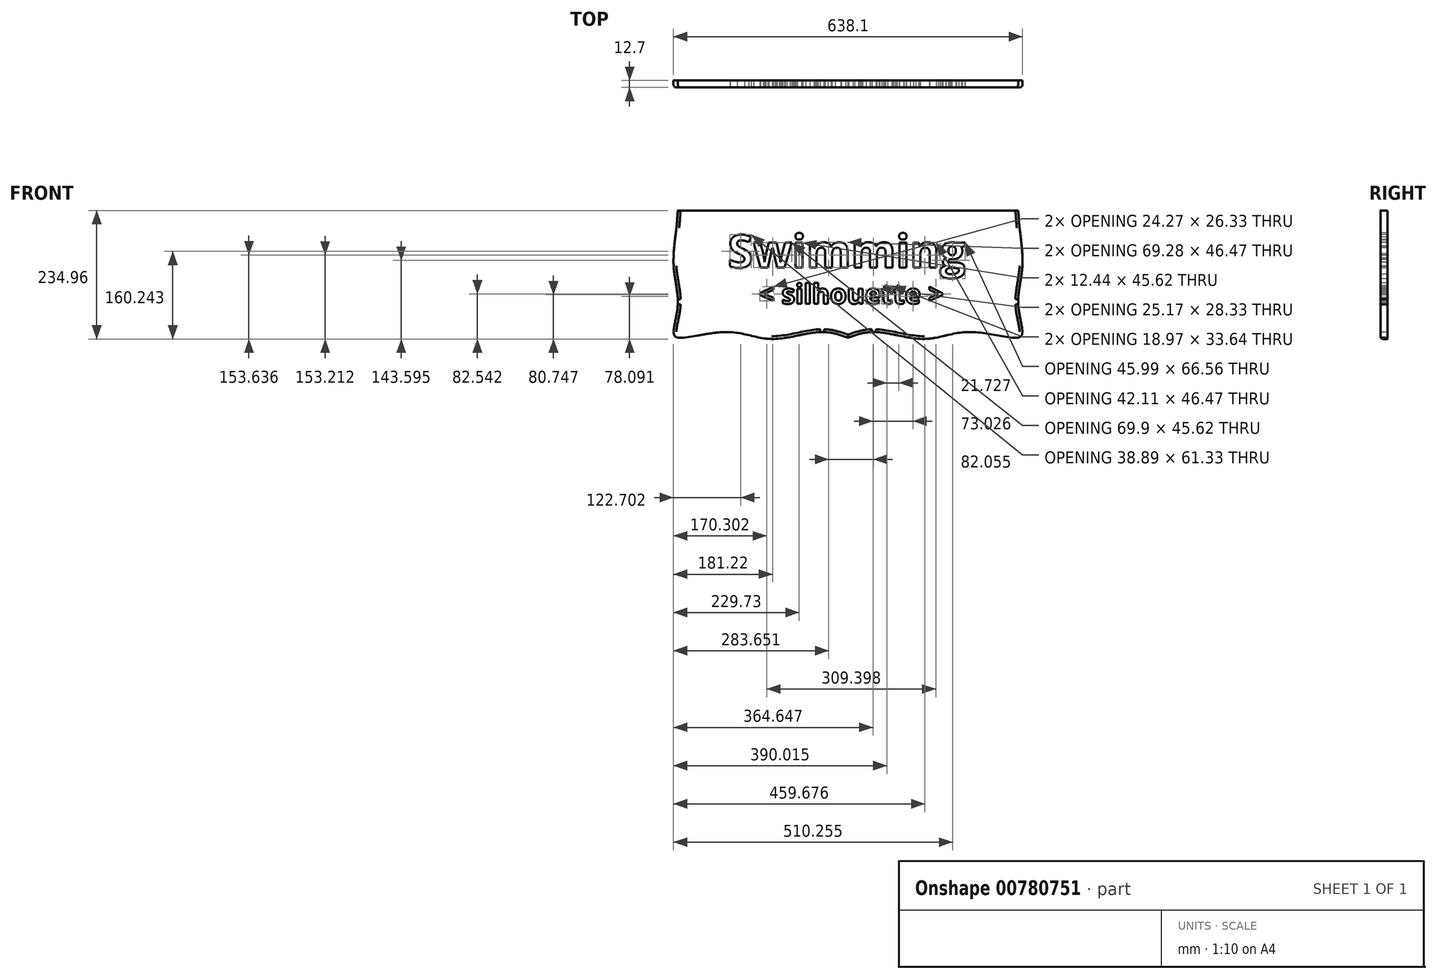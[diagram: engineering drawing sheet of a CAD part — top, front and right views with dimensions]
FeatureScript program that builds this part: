
annotation { "Feature Type Name" : "Feature", "Feature Type Description" : "" }
export const myFeature = defineFeature(function(context is Context, id is Id, definition is map)
    precondition{}
    {
        {
            var Q0;
            Q0=qCreatedBy(makeId("Front.planeOp"),FACE);
            var sketch = newSketch(context, id + "F0", { "sketchPlane" : qUnion([Q0])});
            skLineSegment(sketch, "E0.bottom", {"start": v(-290.57, 108.48) * mm, "end": v(331.73, 108.48) * mm});
            skLineSegment(sketch, "E0.top", {"start": v(-290.57, -113.77) * mm, "end": v(331.73, -113.77) * mm});
            skLineSegment(sketch, "E0.left", {"start": v(-290.57, 108.48) * mm, "end": v(-290.57, -113.77) * mm});
            skLineSegment(sketch, "E0.right", {"start": v(331.73, 108.48) * mm, "end": v(331.73, -113.77) * mm});
            skPoint(sketch, "E1", {"position": v(20.58, 108.48) * mm});
            skSolve(sketch);
        }
        {
            var Q0;
            Q0=makeQuery(id+"F0.imprint","IMPRINT",FACE,{"disambiguationData":[TD([[makeQuery(id+"F0.imprint","IMPRINT",EDGE,{"derivedFrom":sQuery(id+"F0.wireOp",EDGE,"E0.bottom")}),-1.0]])]});
            extrude(context, id + "F1", {"entities" : qUnion([Q0]), "depth" : 12.7 * mm, "offsetDistance" : 25.4 * mm});
        }
        {
            var Q0;
            Q0=makeQuery(id+"F1.opExtrude","CAP_FACE",FACE,{"disambiguationData":[OSD([sQuery(id+"F0.wireOp",EDGE,"E0.bottom"),sQuery(id+"F0.wireOp",EDGE,"E0.top"),sQuery(id+"F0.wireOp",EDGE,"E0.left"),sQuery(id+"F0.wireOp",EDGE,"E0.right")])],"isStart":false});
            var sketch = newSketch(context, id + "F2", { "sketchPlane" : qUnion([Q0])});
            skText(sketch, "E2", { "text": "Swimming", "fontName": "OpenSans-Bold.ttf"});
            skPoint(sketch, "E3", {"position": v(20.58, 108.48) * mm});
            const initialGuessF2  = {"E2": [-0.19905, 0.00392, 1, 0, 0.06017]};
            skSetInitialGuess(sketch, initialGuessF2);
            skSolve(sketch);
        }
        {
            var Q0;
            Q0=makeQuery(id+"F2.imprint","IMPRINT",FACE,{"disambiguationData":[TD([[makeQuery(id+"F2.imprint","IMPRINT",EDGE,{"derivedFrom":sQuery(id+"F2.wireOp",EDGE,"E2.sketch_text.stroke-0")}),1.0]])]});
            var sketch = newSketch(context, id + "F3", { "sketchPlane" : qUnion([Q0])});
            skText(sketch, "E4", { "text": " < silhouette >", "fontName": "OpenSans-Bold.ttf"});
            skPoint(sketch, "E5", {"position": v(20.58, -113.77) * mm});
            const initialGuessF3  = {"E4": [-0.15546, -0.06206, 1, 0, 0.03604]};
            skSetInitialGuess(sketch, initialGuessF3);
            skSolve(sketch);
        }
        {
            var Q0;
            Q0=qSketchRegion(id+"F2",true);
            var Q1;
            Q1=qSketchRegion(id+"F3",true);
            extrude(context, id + "F4", {"entities" : qUnion([Q0, Q1]), "operationType" : NewBodyOperationType.REMOVE, "oppositeDirection" : true, "depth" : 25.4 * mm, "offsetDistance" : 25.4 * mm});
        }
        {
            var Q0;
            {var subQ0=sQuery(id+"F0.wireOp",EDGE,"E0.right");var subQ1=sQuery(id+"F0.wireOp",EDGE,"E0.bottom");var subQ2=sQuery(id+"F0.wireOp",EDGE,"E0.left");var subQ3=sQuery(id+"F0.wireOp",EDGE,"E0.top");Q0=makeQuery(id+"F4.boolean.opBoolean","SPLIT",FACE,{"disambiguationData":[TD([makeQuery(id+"F1.opExtrude","SWEPT_FACE",FACE,{"disambiguationData":[OSD([subQ1])]})])],"derivedFrom":makeQuery(id+"F1.opExtrude","CAP_FACE",FACE,{"disambiguationData":[OSD([subQ1,subQ3,subQ2,subQ0])],"isStart":false})});}
            var sketch = newSketch(context, id + "F5", { "sketchPlane" : qUnion([Q0])});
            skPoint(sketch, "E6", {"position": v(-290.57, -62.97) * mm});
            skPoint(sketch, "E7", {"position": v(-290.57, 6.88) * mm});
            skPoint(sketch, "E8", {"position": v(-290.57, 76.73) * mm});
            skLineSegment(sketch, "E9", {"start": v(-290.57, 76.73) * mm, "end": v(-293.1, 76.73) * mm});
            skLineSegment(sketch, "E10", {"start": v(-290.57, 6.88) * mm, "end": v(-298.19, 6.88) * mm});
            skLineSegment(sketch, "E11", {"start": v(-290.57, -113.77) * mm, "end": v(-298.19, -113.77) * mm});
            skLineSegment(sketch, "E12", {"start": v(-290.57, -113.77) * mm, "end": v(-290.57, -123.93) * mm});
            skPoint(sketch, "E13", {"position": v(-201.67, -113.77) * mm});
            skPoint(sketch, "E14", {"position": v(20.58, -113.77) * mm});
            skPoint(sketch, "E15", {"position": v(-30.22, -113.77) * mm});
            skPoint(sketch, "E16", {"position": v(-119.12, -113.77) * mm});
            skPoint(sketch, "E17", {"position": v(71.38, -113.77) * mm});
            skPoint(sketch, "E18", {"position": v(160.28, -113.77) * mm});
            skPoint(sketch, "E19", {"position": v(242.83, -113.77) * mm});
            skPoint(sketch, "E20", {"position": v(331.73, -62.97) * mm});
            skPoint(sketch, "E21", {"position": v(331.73, 6.88) * mm});
            skPoint(sketch, "E22", {"position": v(331.73, 76.73) * mm});
            skLineSegment(sketch, "E23", {"start": v(331.73, 76.73) * mm, "end": v(334.27, 76.73) * mm});
            skLineSegment(sketch, "E24", {"start": v(331.73, 6.88) * mm, "end": v(339.35, 6.88) * mm});
            skLineSegment(sketch, "E25", {"start": v(331.73, -113.77) * mm, "end": v(339.35, -113.77) * mm});
            skLineSegment(sketch, "E26", {"start": v(331.73, -113.77) * mm, "end": v(331.73, -123.93) * mm});
            skLineSegment(sketch, "E27", {"start": v(-119.12, -113.77) * mm, "end": v(-119.12, -126.47) * mm});
            skLineSegment(sketch, "E28", {"start": v(20.58, -113.77) * mm, "end": v(20.58, -123.93) * mm});
            skLineSegment(sketch, "E29", {"start": v(160.28, -113.77) * mm, "end": v(160.28, -126.47) * mm});
            skFitSpline(sketch, "E30", {"points": [v(-290.57, 108.48) * mm, v(-293.1, 76.73) * mm, v(-298.19, 6.88) * mm, v(-290.57, -62.97) * mm, v(-298.19, -113.77) * mm, v(-290.57, -123.93) * mm, v(-201.67, -113.77) * mm, v(-119.12, -126.47) * mm, v(-30.22, -113.77) * mm, v(20.58, -123.93) * mm], "startDerivative": vector(-26.2, -341.82) * mm, "endDerivative": vector(438.15, -148.5) * mm});
            skFitSpline(sketch, "E31", {"points": [v(331.73, 108.48) * mm, v(334.27, 76.73) * mm, v(339.35, 6.88) * mm, v(331.73, -62.97) * mm, v(339.35, -113.77) * mm, v(331.73, -123.93) * mm, v(242.83, -113.77) * mm, v(160.28, -126.47) * mm, v(71.38, -113.77) * mm, v(20.58, -123.93) * mm], "startDerivative": vector(26.2, -341.82) * mm, "endDerivative": vector(-438.15, -148.5) * mm});
            skSolve(sketch);
        }
        {
            var Q0;
            {var subQ0=sQuery(id+"F5.wireOp",EDGE,"E28");Q0=makeQuery(id+"F5.imprint","IMPRINT",FACE,{"disambiguationData":[TD([[makeQuery(id+"F5.imprint","IMPRINT",EDGE,{"derivedFrom":subQ0}),-1.0]])]});}
            var Q1;
            {var subQ0=sQuery(id+"F5.wireOp",EDGE,"E28");Q1=makeQuery(id+"F5.imprint","IMPRINT",FACE,{"disambiguationData":[TD([[makeQuery(id+"F5.imprint","IMPRINT",EDGE,{"derivedFrom":subQ0}),1.0]])]});}
            var Q2;
            {var subQ0=sQuery(id+"F5.wireOp",EDGE,"E27");Q2=makeQuery(id+"F5.imprint","IMPRINT",FACE,{"disambiguationData":[TD([[makeQuery(id+"F5.imprint","IMPRINT",EDGE,{"derivedFrom":subQ0}),1.0]])]});}
            var Q3;
            {var subQ0=sQuery(id+"F5.wireOp",EDGE,"E27");Q3=makeQuery(id+"F5.imprint","IMPRINT",FACE,{"disambiguationData":[TD([[makeQuery(id+"F5.imprint","IMPRINT",EDGE,{"derivedFrom":subQ0}),-1.0]])]});}
            var Q4;
            {var subQ0=sQuery(id+"F5.wireOp",EDGE,"E12");Q4=makeQuery(id+"F5.imprint","IMPRINT",FACE,{"disambiguationData":[TD([[makeQuery(id+"F5.imprint","IMPRINT",EDGE,{"derivedFrom":subQ0}),1.0]])]});}
            var Q5;
            {var subQ0=sQuery(id+"F5.wireOp",EDGE,"E11");Q5=makeQuery(id+"F5.imprint","IMPRINT",FACE,{"disambiguationData":[TD([[makeQuery(id+"F5.imprint","IMPRINT",EDGE,{"derivedFrom":subQ0}),1.0]])]});}
            var Q6;
            {var subQ0=sQuery(id+"F5.wireOp",EDGE,"E11");Q6=makeQuery(id+"F5.imprint","IMPRINT",FACE,{"disambiguationData":[TD([[makeQuery(id+"F5.imprint","IMPRINT",EDGE,{"derivedFrom":subQ0}),-1.0]])]});}
            var Q7;
            {var subQ0=sQuery(id+"F5.wireOp",EDGE,"E10");Q7=makeQuery(id+"F5.imprint","IMPRINT",FACE,{"disambiguationData":[TD([[makeQuery(id+"F5.imprint","IMPRINT",EDGE,{"derivedFrom":subQ0}),1.0]])]});}
            var Q8;
            {var subQ0=sQuery(id+"F5.wireOp",EDGE,"E9");Q8=makeQuery(id+"F5.imprint","IMPRINT",FACE,{"disambiguationData":[TD([[makeQuery(id+"F5.imprint","IMPRINT",EDGE,{"derivedFrom":subQ0}),1.0]])]});}
            var Q9;
            {var subQ0=makeQuery(id+"F1.opExtrude","CAP_EDGE",EDGE,{"disambiguationData":[OSD([sQuery(id+"F0.wireOp",EDGE,"E0.bottom")])],"isStart":false});Q9=makeQuery(id+"F5.imprint","IMPRINT",FACE,{"disambiguationData":[TD([[makeQuery(id+"F5.imprint","IMPRINT",EDGE,{"derivedFrom":subQ0}),-1.0]])]});}
            var Q10;
            {var subQ0=sQuery(id+"F5.wireOp",EDGE,"E29");Q10=makeQuery(id+"F5.imprint","IMPRINT",FACE,{"disambiguationData":[TD([[makeQuery(id+"F5.imprint","IMPRINT",EDGE,{"derivedFrom":subQ0}),-1.0]])]});}
            var Q11;
            {var subQ0=sQuery(id+"F5.wireOp",EDGE,"E29");Q11=makeQuery(id+"F5.imprint","IMPRINT",FACE,{"disambiguationData":[TD([[makeQuery(id+"F5.imprint","IMPRINT",EDGE,{"derivedFrom":subQ0}),1.0]])]});}
            var Q12;
            {var subQ0=sQuery(id+"F5.wireOp",EDGE,"E26");Q12=makeQuery(id+"F5.imprint","IMPRINT",FACE,{"disambiguationData":[TD([[makeQuery(id+"F5.imprint","IMPRINT",EDGE,{"derivedFrom":subQ0}),-1.0]])]});}
            var Q13;
            {var subQ0=sQuery(id+"F5.wireOp",EDGE,"E25");Q13=makeQuery(id+"F5.imprint","IMPRINT",FACE,{"disambiguationData":[TD([[makeQuery(id+"F5.imprint","IMPRINT",EDGE,{"derivedFrom":subQ0}),-1.0]])]});}
            var Q14;
            {var subQ0=sQuery(id+"F5.wireOp",EDGE,"E25");Q14=makeQuery(id+"F5.imprint","IMPRINT",FACE,{"disambiguationData":[TD([[makeQuery(id+"F5.imprint","IMPRINT",EDGE,{"derivedFrom":subQ0}),1.0]])]});}
            var Q15;
            {var subQ0=sQuery(id+"F5.wireOp",EDGE,"E24");Q15=makeQuery(id+"F5.imprint","IMPRINT",FACE,{"disambiguationData":[TD([[makeQuery(id+"F5.imprint","IMPRINT",EDGE,{"derivedFrom":subQ0}),-1.0]])]});}
            var Q16;
            {var subQ0=sQuery(id+"F5.wireOp",EDGE,"E23");Q16=makeQuery(id+"F5.imprint","IMPRINT",FACE,{"disambiguationData":[TD([[makeQuery(id+"F5.imprint","IMPRINT",EDGE,{"derivedFrom":subQ0}),-1.0]])]});}
            var Q17;
            {var subQ0=sQuery(id+"F5.wireOp",EDGE,"E23");Q17=makeQuery(id+"F5.imprint","IMPRINT",FACE,{"disambiguationData":[TD([[makeQuery(id+"F5.imprint","IMPRINT",EDGE,{"derivedFrom":subQ0}),1.0]])]});}
            var Q18;
            {var subQ0=sQuery(id+"F5.wireOp",EDGE,"E9");Q18=makeQuery(id+"F5.imprint","IMPRINT",FACE,{"disambiguationData":[TD([[makeQuery(id+"F5.imprint","IMPRINT",EDGE,{"derivedFrom":subQ0}),-1.0]])]});}
            extrude(context, id + "F6", {"entities" : qUnion([Q0, Q1, Q2, Q3, Q4, Q5, Q6, Q7, Q8, Q9, Q10, Q11, Q12, Q13, Q14, Q15, Q16, Q17, Q18]), "operationType" : NewBodyOperationType.ADD, "depth" : -12.7 * mm, "offsetDistance" : 25.4 * mm});
        }
        {
            var Q0;
            {var subQ0=sQuery(id+"F5.wireOp",EDGE,"8007402e-1a4e-4a06-85a5-2af08e553504");var subQ1=sQuery(id+"F0.wireOp",EDGE,"E0.left");var subQ2=sQuery(id+"F0.wireOp",EDGE,"E0.top");var subQ3=sQuery(id+"F0.wireOp",EDGE,"E0.bottom");Q0=makeQuery(id+"F6.boolean.opBoolean","SPLIT",EDGE,{"disambiguationData":[TD([makeQuery(id+"F1.opExtrude","CAP_FACE",FACE,{"disambiguationData":[OSD([subQ3,subQ2,subQ1,sQuery(id+"F0.wireOp",EDGE,"E0.right")])],"isStart":false}),makeQuery(id+"F1.opExtrude","SWEPT_FACE",FACE,{"disambiguationData":[OSD([subQ2])]}),makeQuery(id+"F1.opExtrude","SWEPT_FACE",FACE,{"disambiguationData":[OSD([subQ1])]}),makeQuery(id+"F6.opExtrude","SWEPT_FACE",FACE,{"disambiguationData":[OSD([subQ0])]}),makeQuery(id+"F6.opExtrude","CAP_FACE",FACE,{"disambiguationData":[OSD([subQ3,sQuery(id+"F2.wireOp",EDGE,"E2.sketch_text.stroke-0"),sQuery(id+"F2.wireOp",EDGE,"E2.sketch_text.stroke-1"),sQuery(id+"F2.wireOp",EDGE,"E2.sketch_text.stroke-2"),sQuery(id+"F2.wireOp",EDGE,"E2.sketch_text.stroke-3"),sQuery(id+"F2.wireOp",EDGE,"E2.sketch_text.stroke-4"),sQuery(id+"F2.wireOp",EDGE,"E2.sketch_text.stroke-5"),sQuery(id+"F2.wireOp",EDGE,"E2.sketch_text.stroke-6"),sQuery(id+"F2.wireOp",EDGE,"E2.sketch_text.stroke-7"),sQuery(id+"F2.wireOp",EDGE,"E2.sketch_text.stroke-8"),sQuery(id+"F2.wireOp",EDGE,"E2.sketch_text.stroke-9"),sQuery(id+"F2.wireOp",EDGE,"E2.sketch_text.stroke-10"),sQuery(id+"F2.wireOp",EDGE,"E2.sketch_text.stroke-11"),sQuery(id+"F2.wireOp",EDGE,"E2.sketch_text.stroke-12"),sQuery(id+"F2.wireOp",EDGE,"E2.sketch_text.stroke-13"),sQuery(id+"F2.wireOp",EDGE,"E2.sketch_text.stroke-14"),sQuery(id+"F2.wireOp",EDGE,"E2.sketch_text.stroke-15"),sQuery(id+"F2.wireOp",EDGE,"E2.sketch_text.stroke-16"),sQuery(id+"F2.wireOp",EDGE,"E2.sketch_text.stroke-17"),sQuery(id+"F2.wireOp",EDGE,"E2.sketch_text.stroke-18"),sQuery(id+"F2.wireOp",EDGE,"E2.sketch_text.stroke-19"),sQuery(id+"F2.wireOp",EDGE,"E2.sketch_text.stroke-20"),sQuery(id+"F2.wireOp",EDGE,"E2.sketch_text.stroke-21"),sQuery(id+"F2.wireOp",EDGE,"E2.sketch_text.stroke-22"),sQuery(id+"F2.wireOp",EDGE,"E2.sketch_text.stroke-23"),sQuery(id+"F2.wireOp",EDGE,"E2.sketch_text.stroke-24"),sQuery(id+"F2.wireOp",EDGE,"E2.sketch_text.stroke-25"),sQuery(id+"F2.wireOp",EDGE,"E2.sketch_text.stroke-26"),sQuery(id+"F2.wireOp",EDGE,"E2.sketch_text.stroke-27"),sQuery(id+"F2.wireOp",EDGE,"E2.sketch_text.stroke-28"),sQuery(id+"F2.wireOp",EDGE,"E2.sketch_text.stroke-29"),sQuery(id+"F2.wireOp",EDGE,"E2.sketch_text.stroke-30"),sQuery(id+"F2.wireOp",EDGE,"E2.sketch_text.stroke-31"),sQuery(id+"F2.wireOp",EDGE,"E2.sketch_text.stroke-32"),sQuery(id+"F2.wireOp",EDGE,"E2.sketch_text.stroke-33"),sQuery(id+"F2.wireOp",EDGE,"E2.sketch_text.stroke-34"),sQuery(id+"F2.wireOp",EDGE,"E2.sketch_text.stroke-35"),sQuery(id+"F2.wireOp",EDGE,"E2.sketch_text.stroke-36"),sQuery(id+"F2.wireOp",EDGE,"E2.sketch_text.stroke-37"),sQuery(id+"F2.wireOp",EDGE,"E2.sketch_text.stroke-38"),sQuery(id+"F2.wireOp",EDGE,"E2.sketch_text.stroke-39"),sQuery(id+"F2.wireOp",EDGE,"E2.sketch_text.stroke-40"),sQuery(id+"F2.wireOp",EDGE,"E2.sketch_text.stroke-41"),sQuery(id+"F2.wireOp",EDGE,"E2.sketch_text.stroke-42"),sQuery(id+"F2.wireOp",EDGE,"E2.sketch_text.stroke-43"),sQuery(id+"F2.wireOp",EDGE,"E2.sketch_text.stroke-44"),sQuery(id+"F2.wireOp",EDGE,"E2.sketch_text.stroke-45"),sQuery(id+"F2.wireOp",EDGE,"E2.sketch_text.stroke-46"),sQuery(id+"F2.wireOp",EDGE,"E2.sketch_text.stroke-47"),sQuery(id+"F2.wireOp",EDGE,"E2.sketch_text.stroke-48"),sQuery(id+"F2.wireOp",EDGE,"E2.sketch_text.stroke-49"),sQuery(id+"F2.wireOp",EDGE,"E2.sketch_text.stroke-50"),sQuery(id+"F2.wireOp",EDGE,"E2.sketch_text.stroke-51"),sQuery(id+"F2.wireOp",EDGE,"E2.sketch_text.stroke-52"),sQuery(id+"F2.wireOp",EDGE,"E2.sketch_text.stroke-53"),sQuery(id+"F2.wireOp",EDGE,"E2.sketch_text.stroke-54"),sQuery(id+"F2.wireOp",EDGE,"E2.sketch_text.stroke-55"),sQuery(id+"F2.wireOp",EDGE,"E2.sketch_text.stroke-56"),sQuery(id+"F2.wireOp",EDGE,"E2.sketch_text.stroke-57"),sQuery(id+"F2.wireOp",EDGE,"E2.sketch_text.stroke-58"),sQuery(id+"F2.wireOp",EDGE,"E2.sketch_text.stroke-59"),sQuery(id+"F2.wireOp",EDGE,"E2.sketch_text.stroke-60"),sQuery(id+"F2.wireOp",EDGE,"E2.sketch_text.stroke-61"),sQuery(id+"F2.wireOp",EDGE,"E2.sketch_text.stroke-62"),sQuery(id+"F2.wireOp",EDGE,"E2.sketch_text.stroke-63"),sQuery(id+"F2.wireOp",EDGE,"E2.sketch_text.stroke-64"),sQuery(id+"F2.wireOp",EDGE,"E2.sketch_text.stroke-65"),sQuery(id+"F2.wireOp",EDGE,"E2.sketch_text.stroke-66"),sQuery(id+"F2.wireOp",EDGE,"E2.sketch_text.stroke-67"),sQuery(id+"F2.wireOp",EDGE,"E2.sketch_text.stroke-68"),sQuery(id+"F2.wireOp",EDGE,"E2.sketch_text.stroke-69"),sQuery(id+"F2.wireOp",EDGE,"E2.sketch_text.stroke-70"),sQuery(id+"F2.wireOp",EDGE,"E2.sketch_text.stroke-71"),sQuery(id+"F2.wireOp",EDGE,"E2.sketch_text.stroke-72"),sQuery(id+"F2.wireOp",EDGE,"E2.sketch_text.stroke-73"),sQuery(id+"F2.wireOp",EDGE,"E2.sketch_text.stroke-74"),sQuery(id+"F2.wireOp",EDGE,"E2.sketch_text.stroke-75"),sQuery(id+"F2.wireOp",EDGE,"E2.sketch_text.stroke-76"),sQuery(id+"F2.wireOp",EDGE,"E2.sketch_text.stroke-77"),sQuery(id+"F2.wireOp",EDGE,"E2.sketch_text.stroke-78"),sQuery(id+"F2.wireOp",EDGE,"E2.sketch_text.stroke-79"),sQuery(id+"F2.wireOp",EDGE,"E2.sketch_text.stroke-80"),sQuery(id+"F2.wireOp",EDGE,"E2.sketch_text.stroke-81"),sQuery(id+"F2.wireOp",EDGE,"E2.sketch_text.stroke-82"),sQuery(id+"F2.wireOp",EDGE,"E2.sketch_text.stroke-83"),sQuery(id+"F2.wireOp",EDGE,"E2.sketch_text.stroke-84"),sQuery(id+"F2.wireOp",EDGE,"E2.sketch_text.stroke-85"),sQuery(id+"F2.wireOp",EDGE,"E2.sketch_text.stroke-86"),sQuery(id+"F2.wireOp",EDGE,"E2.sketch_text.stroke-87"),sQuery(id+"F2.wireOp",EDGE,"E2.sketch_text.stroke-88"),sQuery(id+"F2.wireOp",EDGE,"E2.sketch_text.stroke-89"),sQuery(id+"F2.wireOp",EDGE,"E2.sketch_text.stroke-90"),sQuery(id+"F2.wireOp",EDGE,"E2.sketch_text.stroke-91"),sQuery(id+"F2.wireOp",EDGE,"E2.sketch_text.stroke-92"),sQuery(id+"F2.wireOp",EDGE,"E2.sketch_text.stroke-93"),sQuery(id+"F2.wireOp",EDGE,"E2.sketch_text.stroke-94"),sQuery(id+"F2.wireOp",EDGE,"E2.sketch_text.stroke-95"),sQuery(id+"F2.wireOp",EDGE,"E2.sketch_text.stroke-96"),sQuery(id+"F2.wireOp",EDGE,"E2.sketch_text.stroke-97"),sQuery(id+"F2.wireOp",EDGE,"E2.sketch_text.stroke-98"),sQuery(id+"F2.wireOp",EDGE,"E2.sketch_text.stroke-99"),sQuery(id+"F2.wireOp",EDGE,"E2.sketch_text.stroke-100"),sQuery(id+"F2.wireOp",EDGE,"E2.sketch_text.stroke-101"),sQuery(id+"F2.wireOp",EDGE,"E2.sketch_text.stroke-102"),sQuery(id+"F2.wireOp",EDGE,"E2.sketch_text.stroke-103"),sQuery(id+"F2.wireOp",EDGE,"E2.sketch_text.stroke-104"),sQuery(id+"F2.wireOp",EDGE,"E2.sketch_text.stroke-105"),sQuery(id+"F2.wireOp",EDGE,"E2.sketch_text.stroke-106"),sQuery(id+"F2.wireOp",EDGE,"E2.sketch_text.stroke-107"),sQuery(id+"F2.wireOp",EDGE,"E2.sketch_text.stroke-108"),sQuery(id+"F2.wireOp",EDGE,"E2.sketch_text.stroke-109"),sQuery(id+"F2.wireOp",EDGE,"E2.sketch_text.stroke-110"),sQuery(id+"F2.wireOp",EDGE,"E2.sketch_text.stroke-111"),sQuery(id+"F2.wireOp",EDGE,"E2.sketch_text.stroke-112"),sQuery(id+"F2.wireOp",EDGE,"E2.sketch_text.stroke-113"),sQuery(id+"F2.wireOp",EDGE,"E2.sketch_text.stroke-114"),sQuery(id+"F2.wireOp",EDGE,"E2.sketch_text.stroke-115"),sQuery(id+"F2.wireOp",EDGE,"E2.sketch_text.stroke-116"),sQuery(id+"F2.wireOp",EDGE,"E2.sketch_text.stroke-117"),sQuery(id+"F2.wireOp",EDGE,"E2.sketch_text.stroke-118"),sQuery(id+"F2.wireOp",EDGE,"E2.sketch_text.stroke-119"),sQuery(id+"F2.wireOp",EDGE,"E2.sketch_text.stroke-120"),sQuery(id+"F2.wireOp",EDGE,"E2.sketch_text.stroke-121"),sQuery(id+"F2.wireOp",EDGE,"E2.sketch_text.stroke-122"),sQuery(id+"F2.wireOp",EDGE,"E2.sketch_text.stroke-123"),sQuery(id+"F2.wireOp",EDGE,"E2.sketch_text.stroke-124"),sQuery(id+"F2.wireOp",EDGE,"E2.sketch_text.stroke-125"),sQuery(id+"F2.wireOp",EDGE,"E2.sketch_text.stroke-126"),sQuery(id+"F2.wireOp",EDGE,"E2.sketch_text.stroke-127"),sQuery(id+"F2.wireOp",EDGE,"E2.sketch_text.stroke-128"),sQuery(id+"F2.wireOp",EDGE,"E2.sketch_text.stroke-129"),sQuery(id+"F2.wireOp",EDGE,"E2.sketch_text.stroke-130"),sQuery(id+"F2.wireOp",EDGE,"E2.sketch_text.stroke-131"),sQuery(id+"F2.wireOp",EDGE,"E2.sketch_text.stroke-132"),sQuery(id+"F2.wireOp",EDGE,"E2.sketch_text.stroke-133"),sQuery(id+"F2.wireOp",EDGE,"E2.sketch_text.stroke-134"),sQuery(id+"F2.wireOp",EDGE,"E2.sketch_text.stroke-135"),sQuery(id+"F2.wireOp",EDGE,"E2.sketch_text.stroke-136"),sQuery(id+"F2.wireOp",EDGE,"E2.sketch_text.stroke-137"),sQuery(id+"F2.wireOp",EDGE,"E2.sketch_text.stroke-138"),sQuery(id+"F2.wireOp",EDGE,"E2.sketch_text.stroke-139"),sQuery(id+"F2.wireOp",EDGE,"E2.sketch_text.stroke-140"),sQuery(id+"F2.wireOp",EDGE,"E2.sketch_text.stroke-141"),sQuery(id+"F2.wireOp",EDGE,"E2.sketch_text.stroke-142"),sQuery(id+"F2.wireOp",EDGE,"E2.sketch_text.stroke-143"),sQuery(id+"F2.wireOp",EDGE,"E2.sketch_text.stroke-144"),sQuery(id+"F2.wireOp",EDGE,"E2.sketch_text.stroke-145"),sQuery(id+"F2.wireOp",EDGE,"E2.sketch_text.stroke-146"),sQuery(id+"F2.wireOp",EDGE,"E2.sketch_text.stroke-147"),sQuery(id+"F2.wireOp",EDGE,"E2.sketch_text.stroke-148"),sQuery(id+"F2.wireOp",EDGE,"E2.sketch_text.stroke-149"),sQuery(id+"F2.wireOp",EDGE,"E2.sketch_text.stroke-150"),sQuery(id+"F2.wireOp",EDGE,"E2.sketch_text.stroke-151"),sQuery(id+"F2.wireOp",EDGE,"E2.sketch_text.stroke-152"),sQuery(id+"F2.wireOp",EDGE,"E2.sketch_text.stroke-153"),sQuery(id+"F2.wireOp",EDGE,"E2.sketch_text.stroke-154"),sQuery(id+"F2.wireOp",EDGE,"E2.sketch_text.stroke-155"),sQuery(id+"F2.wireOp",EDGE,"E2.sketch_text.stroke-156"),sQuery(id+"F2.wireOp",EDGE,"E2.sketch_text.stroke-157"),sQuery(id+"F2.wireOp",EDGE,"E2.sketch_text.stroke-158"),sQuery(id+"F2.wireOp",EDGE,"E2.sketch_text.stroke-159"),sQuery(id+"F2.wireOp",EDGE,"E2.sketch_text.stroke-160"),sQuery(id+"F2.wireOp",EDGE,"E2.sketch_text.stroke-161"),sQuery(id+"F2.wireOp",EDGE,"E2.sketch_text.stroke-162"),sQuery(id+"F2.wireOp",EDGE,"E2.sketch_text.stroke-163"),sQuery(id+"F2.wireOp",EDGE,"E2.sketch_text.stroke-164"),sQuery(id+"F2.wireOp",EDGE,"E2.sketch_text.stroke-165"),sQuery(id+"F2.wireOp",EDGE,"E2.sketch_text.stroke-166"),sQuery(id+"F2.wireOp",EDGE,"E2.sketch_text.stroke-167"),sQuery(id+"F2.wireOp",EDGE,"E2.sketch_text.stroke-168"),sQuery(id+"F2.wireOp",EDGE,"E2.sketch_text.stroke-169"),sQuery(id+"F2.wireOp",EDGE,"E2.sketch_text.stroke-170"),sQuery(id+"F2.wireOp",EDGE,"E2.sketch_text.stroke-171"),sQuery(id+"F2.wireOp",EDGE,"E2.sketch_text.stroke-172"),sQuery(id+"F2.wireOp",EDGE,"E2.sketch_text.stroke-173"),sQuery(id+"F3.wireOp",EDGE,"E4.sketch_text.stroke-0"),sQuery(id+"F3.wireOp",EDGE,"E4.sketch_text.stroke-1"),sQuery(id+"F3.wireOp",EDGE,"E4.sketch_text.stroke-2"),sQuery(id+"F3.wireOp",EDGE,"E4.sketch_text.stroke-3"),sQuery(id+"F3.wireOp",EDGE,"E4.sketch_text.stroke-4"),sQuery(id+"F3.wireOp",EDGE,"E4.sketch_text.stroke-5"),sQuery(id+"F3.wireOp",EDGE,"E4.sketch_text.stroke-6"),sQuery(id+"F3.wireOp",EDGE,"E4.sketch_text.stroke-7"),sQuery(id+"F3.wireOp",EDGE,"E4.sketch_text.stroke-8"),sQuery(id+"F3.wireOp",EDGE,"E4.sketch_text.stroke-9"),sQuery(id+"F3.wireOp",EDGE,"E4.sketch_text.stroke-10"),sQuery(id+"F3.wireOp",EDGE,"E4.sketch_text.stroke-11"),sQuery(id+"F3.wireOp",EDGE,"E4.sketch_text.stroke-12"),sQuery(id+"F3.wireOp",EDGE,"E4.sketch_text.stroke-13"),sQuery(id+"F3.wireOp",EDGE,"E4.sketch_text.stroke-14"),sQuery(id+"F3.wireOp",EDGE,"E4.sketch_text.stroke-15"),sQuery(id+"F3.wireOp",EDGE,"E4.sketch_text.stroke-16"),sQuery(id+"F3.wireOp",EDGE,"E4.sketch_text.stroke-17"),sQuery(id+"F3.wireOp",EDGE,"E4.sketch_text.stroke-18"),sQuery(id+"F3.wireOp",EDGE,"E4.sketch_text.stroke-19"),sQuery(id+"F3.wireOp",EDGE,"E4.sketch_text.stroke-20"),sQuery(id+"F3.wireOp",EDGE,"E4.sketch_text.stroke-21"),sQuery(id+"F3.wireOp",EDGE,"E4.sketch_text.stroke-22"),sQuery(id+"F3.wireOp",EDGE,"E4.sketch_text.stroke-23"),sQuery(id+"F3.wireOp",EDGE,"E4.sketch_text.stroke-24"),sQuery(id+"F3.wireOp",EDGE,"E4.sketch_text.stroke-25"),sQuery(id+"F3.wireOp",EDGE,"E4.sketch_text.stroke-26"),sQuery(id+"F3.wireOp",EDGE,"E4.sketch_text.stroke-27"),sQuery(id+"F3.wireOp",EDGE,"E4.sketch_text.stroke-28"),sQuery(id+"F3.wireOp",EDGE,"E4.sketch_text.stroke-29"),sQuery(id+"F3.wireOp",EDGE,"E4.sketch_text.stroke-30"),sQuery(id+"F3.wireOp",EDGE,"E4.sketch_text.stroke-31"),sQuery(id+"F3.wireOp",EDGE,"E4.sketch_text.stroke-32"),sQuery(id+"F3.wireOp",EDGE,"E4.sketch_text.stroke-33"),sQuery(id+"F3.wireOp",EDGE,"E4.sketch_text.stroke-34"),sQuery(id+"F3.wireOp",EDGE,"E4.sketch_text.stroke-35"),sQuery(id+"F3.wireOp",EDGE,"E4.sketch_text.stroke-36"),sQuery(id+"F3.wireOp",EDGE,"E4.sketch_text.stroke-37"),sQuery(id+"F3.wireOp",EDGE,"E4.sketch_text.stroke-38"),sQuery(id+"F3.wireOp",EDGE,"E4.sketch_text.stroke-39"),sQuery(id+"F3.wireOp",EDGE,"E4.sketch_text.stroke-40"),sQuery(id+"F3.wireOp",EDGE,"E4.sketch_text.stroke-41"),sQuery(id+"F3.wireOp",EDGE,"E4.sketch_text.stroke-42"),sQuery(id+"F3.wireOp",EDGE,"E4.sketch_text.stroke-43"),sQuery(id+"F3.wireOp",EDGE,"E4.sketch_text.stroke-44"),sQuery(id+"F3.wireOp",EDGE,"E4.sketch_text.stroke-45"),sQuery(id+"F3.wireOp",EDGE,"E4.sketch_text.stroke-46"),sQuery(id+"F3.wireOp",EDGE,"E4.sketch_text.stroke-47"),sQuery(id+"F3.wireOp",EDGE,"E4.sketch_text.stroke-48"),sQuery(id+"F3.wireOp",EDGE,"E4.sketch_text.stroke-49"),sQuery(id+"F3.wireOp",EDGE,"E4.sketch_text.stroke-50"),sQuery(id+"F3.wireOp",EDGE,"E4.sketch_text.stroke-51"),sQuery(id+"F3.wireOp",EDGE,"E4.sketch_text.stroke-52"),sQuery(id+"F3.wireOp",EDGE,"E4.sketch_text.stroke-53"),sQuery(id+"F3.wireOp",EDGE,"E4.sketch_text.stroke-54"),sQuery(id+"F3.wireOp",EDGE,"E4.sketch_text.stroke-55"),sQuery(id+"F3.wireOp",EDGE,"E4.sketch_text.stroke-56"),sQuery(id+"F3.wireOp",EDGE,"E4.sketch_text.stroke-57"),sQuery(id+"F3.wireOp",EDGE,"E4.sketch_text.stroke-58"),sQuery(id+"F3.wireOp",EDGE,"E4.sketch_text.stroke-59"),sQuery(id+"F3.wireOp",EDGE,"E4.sketch_text.stroke-60"),sQuery(id+"F3.wireOp",EDGE,"E4.sketch_text.stroke-61"),sQuery(id+"F3.wireOp",EDGE,"E4.sketch_text.stroke-62"),sQuery(id+"F3.wireOp",EDGE,"E4.sketch_text.stroke-71"),sQuery(id+"F3.wireOp",EDGE,"E4.sketch_text.stroke-72"),sQuery(id+"F3.wireOp",EDGE,"E4.sketch_text.stroke-73"),sQuery(id+"F3.wireOp",EDGE,"E4.sketch_text.stroke-74"),sQuery(id+"F3.wireOp",EDGE,"E4.sketch_text.stroke-75"),sQuery(id+"F3.wireOp",EDGE,"E4.sketch_text.stroke-76"),sQuery(id+"F3.wireOp",EDGE,"E4.sketch_text.stroke-77"),sQuery(id+"F3.wireOp",EDGE,"E4.sketch_text.stroke-78"),sQuery(id+"F3.wireOp",EDGE,"E4.sketch_text.stroke-79"),sQuery(id+"F3.wireOp",EDGE,"E4.sketch_text.stroke-80"),sQuery(id+"F3.wireOp",EDGE,"E4.sketch_text.stroke-81"),sQuery(id+"F3.wireOp",EDGE,"E4.sketch_text.stroke-82"),sQuery(id+"F3.wireOp",EDGE,"E4.sketch_text.stroke-83"),sQuery(id+"F3.wireOp",EDGE,"E4.sketch_text.stroke-84"),sQuery(id+"F3.wireOp",EDGE,"E4.sketch_text.stroke-85"),sQuery(id+"F3.wireOp",EDGE,"E4.sketch_text.stroke-86"),sQuery(id+"F3.wireOp",EDGE,"E4.sketch_text.stroke-87"),sQuery(id+"F3.wireOp",EDGE,"E4.sketch_text.stroke-88"),sQuery(id+"F3.wireOp",EDGE,"E4.sketch_text.stroke-89"),sQuery(id+"F3.wireOp",EDGE,"E4.sketch_text.stroke-90"),sQuery(id+"F3.wireOp",EDGE,"E4.sketch_text.stroke-91"),sQuery(id+"F3.wireOp",EDGE,"E4.sketch_text.stroke-92"),sQuery(id+"F3.wireOp",EDGE,"E4.sketch_text.stroke-93"),sQuery(id+"F3.wireOp",EDGE,"E4.sketch_text.stroke-94"),sQuery(id+"F3.wireOp",EDGE,"E4.sketch_text.stroke-95"),sQuery(id+"F3.wireOp",EDGE,"E4.sketch_text.stroke-96"),sQuery(id+"F3.wireOp",EDGE,"E4.sketch_text.stroke-97"),sQuery(id+"F3.wireOp",EDGE,"E4.sketch_text.stroke-103"),sQuery(id+"F3.wireOp",EDGE,"E4.sketch_text.stroke-104"),sQuery(id+"F3.wireOp",EDGE,"E4.sketch_text.stroke-105"),sQuery(id+"F3.wireOp",EDGE,"E4.sketch_text.stroke-106"),sQuery(id+"F3.wireOp",EDGE,"E4.sketch_text.stroke-107"),sQuery(id+"F3.wireOp",EDGE,"E4.sketch_text.stroke-108"),sQuery(id+"F3.wireOp",EDGE,"E4.sketch_text.stroke-109"),sQuery(id+"F3.wireOp",EDGE,"E4.sketch_text.stroke-110"),sQuery(id+"F3.wireOp",EDGE,"E4.sketch_text.stroke-111"),sQuery(id+"F3.wireOp",EDGE,"E4.sketch_text.stroke-112"),sQuery(id+"F3.wireOp",EDGE,"E4.sketch_text.stroke-113"),sQuery(id+"F3.wireOp",EDGE,"E4.sketch_text.stroke-114"),sQuery(id+"F3.wireOp",EDGE,"E4.sketch_text.stroke-115"),sQuery(id+"F3.wireOp",EDGE,"E4.sketch_text.stroke-116"),sQuery(id+"F3.wireOp",EDGE,"E4.sketch_text.stroke-117"),sQuery(id+"F3.wireOp",EDGE,"E4.sketch_text.stroke-118"),sQuery(id+"F3.wireOp",EDGE,"E4.sketch_text.stroke-119"),sQuery(id+"F3.wireOp",EDGE,"E4.sketch_text.stroke-120"),sQuery(id+"F3.wireOp",EDGE,"E4.sketch_text.stroke-121"),sQuery(id+"F3.wireOp",EDGE,"E4.sketch_text.stroke-122"),sQuery(id+"F3.wireOp",EDGE,"E4.sketch_text.stroke-123"),sQuery(id+"F3.wireOp",EDGE,"E4.sketch_text.stroke-124"),sQuery(id+"F3.wireOp",EDGE,"E4.sketch_text.stroke-125"),sQuery(id+"F3.wireOp",EDGE,"E4.sketch_text.stroke-126"),sQuery(id+"F3.wireOp",EDGE,"E4.sketch_text.stroke-127"),sQuery(id+"F3.wireOp",EDGE,"E4.sketch_text.stroke-128"),sQuery(id+"F3.wireOp",EDGE,"E4.sketch_text.stroke-129"),sQuery(id+"F3.wireOp",EDGE,"E4.sketch_text.stroke-130"),sQuery(id+"F3.wireOp",EDGE,"E4.sketch_text.stroke-131"),sQuery(id+"F3.wireOp",EDGE,"E4.sketch_text.stroke-132"),sQuery(id+"F3.wireOp",EDGE,"E4.sketch_text.stroke-133"),sQuery(id+"F3.wireOp",EDGE,"E4.sketch_text.stroke-134"),sQuery(id+"F3.wireOp",EDGE,"E4.sketch_text.stroke-135"),sQuery(id+"F3.wireOp",EDGE,"E4.sketch_text.stroke-136"),sQuery(id+"F3.wireOp",EDGE,"E4.sketch_text.stroke-137"),sQuery(id+"F3.wireOp",EDGE,"E4.sketch_text.stroke-138"),sQuery(id+"F3.wireOp",EDGE,"E4.sketch_text.stroke-139"),sQuery(id+"F3.wireOp",EDGE,"E4.sketch_text.stroke-140"),sQuery(id+"F3.wireOp",EDGE,"E4.sketch_text.stroke-141"),sQuery(id+"F3.wireOp",EDGE,"E4.sketch_text.stroke-142"),sQuery(id+"F3.wireOp",EDGE,"E4.sketch_text.stroke-143"),sQuery(id+"F3.wireOp",EDGE,"E4.sketch_text.stroke-144"),sQuery(id+"F3.wireOp",EDGE,"E4.sketch_text.stroke-145"),sQuery(id+"F3.wireOp",EDGE,"E4.sketch_text.stroke-146"),sQuery(id+"F3.wireOp",EDGE,"E4.sketch_text.stroke-147"),sQuery(id+"F3.wireOp",EDGE,"E4.sketch_text.stroke-148"),sQuery(id+"F3.wireOp",EDGE,"E4.sketch_text.stroke-149"),sQuery(id+"F3.wireOp",EDGE,"E4.sketch_text.stroke-150"),sQuery(id+"F3.wireOp",EDGE,"E4.sketch_text.stroke-151"),sQuery(id+"F3.wireOp",EDGE,"E4.sketch_text.stroke-152"),sQuery(id+"F3.wireOp",EDGE,"E4.sketch_text.stroke-153"),sQuery(id+"F3.wireOp",EDGE,"E4.sketch_text.stroke-159"),sQuery(id+"F3.wireOp",EDGE,"E4.sketch_text.stroke-160"),sQuery(id+"F3.wireOp",EDGE,"E4.sketch_text.stroke-161"),sQuery(id+"F3.wireOp",EDGE,"E4.sketch_text.stroke-162"),sQuery(id+"F3.wireOp",EDGE,"E4.sketch_text.stroke-163"),sQuery(id+"F3.wireOp",EDGE,"E4.sketch_text.stroke-164"),sQuery(id+"F3.wireOp",EDGE,"E4.sketch_text.stroke-165"),sQuery(id+"F3.wireOp",EDGE,"E4.sketch_text.stroke-166"),sQuery(id+"F3.wireOp",EDGE,"E4.sketch_text.stroke-167"),sQuery(id+"F3.wireOp",EDGE,"E4.sketch_text.stroke-168"),sQuery(id+"F3.wireOp",EDGE,"E4.sketch_text.stroke-169"),sQuery(id+"F3.wireOp",EDGE,"E4.sketch_text.stroke-170"),sQuery(id+"F3.wireOp",EDGE,"E4.sketch_text.stroke-171"),sQuery(id+"F3.wireOp",EDGE,"E4.sketch_text.stroke-172"),sQuery(id+"F3.wireOp",EDGE,"E4.sketch_text.stroke-173"),sQuery(id+"F3.wireOp",EDGE,"E4.sketch_text.stroke-174"),sQuery(id+"F3.wireOp",EDGE,"E4.sketch_text.stroke-175"),sQuery(id+"F3.wireOp",EDGE,"E4.sketch_text.stroke-176"),sQuery(id+"F3.wireOp",EDGE,"E4.sketch_text.stroke-177"),sQuery(id+"F3.wireOp",EDGE,"E4.sketch_text.stroke-178"),sQuery(id+"F3.wireOp",EDGE,"E4.sketch_text.stroke-179"),sQuery(id+"F3.wireOp",EDGE,"E4.sketch_text.stroke-180"),subQ0,sQuery(id+"F5.wireOp",EDGE,"6ee83ff3-586e-4dbe-aaea-af71240543bd")])],"isStart":true})])],"derivedFrom":makeQuery(id+"F6.opExtrude","CAP_EDGE",EDGE,{"disambiguationData":[OSD([subQ0])],"isStart":true})});}
            var Q1;
            Q1=makeQuery(id+"F1.opExtrude","CAP_EDGE",EDGE,{"disambiguationData":[OSD([sQuery(id+"F0.wireOp",EDGE,"E0.left")])],"isStart":false});
            var Q2;
            {var subQ0=sQuery(id+"F0.wireOp",EDGE,"E0.top");var subQ1=sQuery(id+"F0.wireOp",EDGE,"E0.bottom");var subQ2=sQuery(id+"F5.wireOp",EDGE,"8007402e-1a4e-4a06-85a5-2af08e553504");Q2=makeQuery(id+"F6.boolean.opBoolean","SPLIT",EDGE,{"disambiguationData":[TD([makeQuery(id+"F1.opExtrude","CAP_FACE",FACE,{"disambiguationData":[OSD([subQ1,subQ0,sQuery(id+"F0.wireOp",EDGE,"E0.left"),sQuery(id+"F0.wireOp",EDGE,"E0.right")])],"isStart":false}),makeQuery(id+"F1.opExtrude","SWEPT_FACE",FACE,{"disambiguationData":[OSD([subQ0])]}),makeQuery(id+"F6.opExtrude","SWEPT_FACE",FACE,{"disambiguationData":[OSD([subQ2])]}),makeQuery(id+"F6.opExtrude","CAP_FACE",FACE,{"disambiguationData":[OSD([subQ1,sQuery(id+"F2.wireOp",EDGE,"E2.sketch_text.stroke-0"),sQuery(id+"F2.wireOp",EDGE,"E2.sketch_text.stroke-1"),sQuery(id+"F2.wireOp",EDGE,"E2.sketch_text.stroke-2"),sQuery(id+"F2.wireOp",EDGE,"E2.sketch_text.stroke-3"),sQuery(id+"F2.wireOp",EDGE,"E2.sketch_text.stroke-4"),sQuery(id+"F2.wireOp",EDGE,"E2.sketch_text.stroke-5"),sQuery(id+"F2.wireOp",EDGE,"E2.sketch_text.stroke-6"),sQuery(id+"F2.wireOp",EDGE,"E2.sketch_text.stroke-7"),sQuery(id+"F2.wireOp",EDGE,"E2.sketch_text.stroke-8"),sQuery(id+"F2.wireOp",EDGE,"E2.sketch_text.stroke-9"),sQuery(id+"F2.wireOp",EDGE,"E2.sketch_text.stroke-10"),sQuery(id+"F2.wireOp",EDGE,"E2.sketch_text.stroke-11"),sQuery(id+"F2.wireOp",EDGE,"E2.sketch_text.stroke-12"),sQuery(id+"F2.wireOp",EDGE,"E2.sketch_text.stroke-13"),sQuery(id+"F2.wireOp",EDGE,"E2.sketch_text.stroke-14"),sQuery(id+"F2.wireOp",EDGE,"E2.sketch_text.stroke-15"),sQuery(id+"F2.wireOp",EDGE,"E2.sketch_text.stroke-16"),sQuery(id+"F2.wireOp",EDGE,"E2.sketch_text.stroke-17"),sQuery(id+"F2.wireOp",EDGE,"E2.sketch_text.stroke-18"),sQuery(id+"F2.wireOp",EDGE,"E2.sketch_text.stroke-19"),sQuery(id+"F2.wireOp",EDGE,"E2.sketch_text.stroke-20"),sQuery(id+"F2.wireOp",EDGE,"E2.sketch_text.stroke-21"),sQuery(id+"F2.wireOp",EDGE,"E2.sketch_text.stroke-22"),sQuery(id+"F2.wireOp",EDGE,"E2.sketch_text.stroke-23"),sQuery(id+"F2.wireOp",EDGE,"E2.sketch_text.stroke-24"),sQuery(id+"F2.wireOp",EDGE,"E2.sketch_text.stroke-25"),sQuery(id+"F2.wireOp",EDGE,"E2.sketch_text.stroke-26"),sQuery(id+"F2.wireOp",EDGE,"E2.sketch_text.stroke-27"),sQuery(id+"F2.wireOp",EDGE,"E2.sketch_text.stroke-28"),sQuery(id+"F2.wireOp",EDGE,"E2.sketch_text.stroke-29"),sQuery(id+"F2.wireOp",EDGE,"E2.sketch_text.stroke-30"),sQuery(id+"F2.wireOp",EDGE,"E2.sketch_text.stroke-31"),sQuery(id+"F2.wireOp",EDGE,"E2.sketch_text.stroke-32"),sQuery(id+"F2.wireOp",EDGE,"E2.sketch_text.stroke-33"),sQuery(id+"F2.wireOp",EDGE,"E2.sketch_text.stroke-34"),sQuery(id+"F2.wireOp",EDGE,"E2.sketch_text.stroke-35"),sQuery(id+"F2.wireOp",EDGE,"E2.sketch_text.stroke-36"),sQuery(id+"F2.wireOp",EDGE,"E2.sketch_text.stroke-37"),sQuery(id+"F2.wireOp",EDGE,"E2.sketch_text.stroke-38"),sQuery(id+"F2.wireOp",EDGE,"E2.sketch_text.stroke-39"),sQuery(id+"F2.wireOp",EDGE,"E2.sketch_text.stroke-40"),sQuery(id+"F2.wireOp",EDGE,"E2.sketch_text.stroke-41"),sQuery(id+"F2.wireOp",EDGE,"E2.sketch_text.stroke-42"),sQuery(id+"F2.wireOp",EDGE,"E2.sketch_text.stroke-43"),sQuery(id+"F2.wireOp",EDGE,"E2.sketch_text.stroke-44"),sQuery(id+"F2.wireOp",EDGE,"E2.sketch_text.stroke-45"),sQuery(id+"F2.wireOp",EDGE,"E2.sketch_text.stroke-46"),sQuery(id+"F2.wireOp",EDGE,"E2.sketch_text.stroke-47"),sQuery(id+"F2.wireOp",EDGE,"E2.sketch_text.stroke-48"),sQuery(id+"F2.wireOp",EDGE,"E2.sketch_text.stroke-49"),sQuery(id+"F2.wireOp",EDGE,"E2.sketch_text.stroke-50"),sQuery(id+"F2.wireOp",EDGE,"E2.sketch_text.stroke-51"),sQuery(id+"F2.wireOp",EDGE,"E2.sketch_text.stroke-52"),sQuery(id+"F2.wireOp",EDGE,"E2.sketch_text.stroke-53"),sQuery(id+"F2.wireOp",EDGE,"E2.sketch_text.stroke-54"),sQuery(id+"F2.wireOp",EDGE,"E2.sketch_text.stroke-55"),sQuery(id+"F2.wireOp",EDGE,"E2.sketch_text.stroke-56"),sQuery(id+"F2.wireOp",EDGE,"E2.sketch_text.stroke-57"),sQuery(id+"F2.wireOp",EDGE,"E2.sketch_text.stroke-58"),sQuery(id+"F2.wireOp",EDGE,"E2.sketch_text.stroke-59"),sQuery(id+"F2.wireOp",EDGE,"E2.sketch_text.stroke-60"),sQuery(id+"F2.wireOp",EDGE,"E2.sketch_text.stroke-61"),sQuery(id+"F2.wireOp",EDGE,"E2.sketch_text.stroke-62"),sQuery(id+"F2.wireOp",EDGE,"E2.sketch_text.stroke-63"),sQuery(id+"F2.wireOp",EDGE,"E2.sketch_text.stroke-64"),sQuery(id+"F2.wireOp",EDGE,"E2.sketch_text.stroke-65"),sQuery(id+"F2.wireOp",EDGE,"E2.sketch_text.stroke-66"),sQuery(id+"F2.wireOp",EDGE,"E2.sketch_text.stroke-67"),sQuery(id+"F2.wireOp",EDGE,"E2.sketch_text.stroke-68"),sQuery(id+"F2.wireOp",EDGE,"E2.sketch_text.stroke-69"),sQuery(id+"F2.wireOp",EDGE,"E2.sketch_text.stroke-70"),sQuery(id+"F2.wireOp",EDGE,"E2.sketch_text.stroke-71"),sQuery(id+"F2.wireOp",EDGE,"E2.sketch_text.stroke-72"),sQuery(id+"F2.wireOp",EDGE,"E2.sketch_text.stroke-73"),sQuery(id+"F2.wireOp",EDGE,"E2.sketch_text.stroke-74"),sQuery(id+"F2.wireOp",EDGE,"E2.sketch_text.stroke-75"),sQuery(id+"F2.wireOp",EDGE,"E2.sketch_text.stroke-76"),sQuery(id+"F2.wireOp",EDGE,"E2.sketch_text.stroke-77"),sQuery(id+"F2.wireOp",EDGE,"E2.sketch_text.stroke-78"),sQuery(id+"F2.wireOp",EDGE,"E2.sketch_text.stroke-79"),sQuery(id+"F2.wireOp",EDGE,"E2.sketch_text.stroke-80"),sQuery(id+"F2.wireOp",EDGE,"E2.sketch_text.stroke-81"),sQuery(id+"F2.wireOp",EDGE,"E2.sketch_text.stroke-82"),sQuery(id+"F2.wireOp",EDGE,"E2.sketch_text.stroke-83"),sQuery(id+"F2.wireOp",EDGE,"E2.sketch_text.stroke-84"),sQuery(id+"F2.wireOp",EDGE,"E2.sketch_text.stroke-85"),sQuery(id+"F2.wireOp",EDGE,"E2.sketch_text.stroke-86"),sQuery(id+"F2.wireOp",EDGE,"E2.sketch_text.stroke-87"),sQuery(id+"F2.wireOp",EDGE,"E2.sketch_text.stroke-88"),sQuery(id+"F2.wireOp",EDGE,"E2.sketch_text.stroke-89"),sQuery(id+"F2.wireOp",EDGE,"E2.sketch_text.stroke-90"),sQuery(id+"F2.wireOp",EDGE,"E2.sketch_text.stroke-91"),sQuery(id+"F2.wireOp",EDGE,"E2.sketch_text.stroke-92"),sQuery(id+"F2.wireOp",EDGE,"E2.sketch_text.stroke-93"),sQuery(id+"F2.wireOp",EDGE,"E2.sketch_text.stroke-94"),sQuery(id+"F2.wireOp",EDGE,"E2.sketch_text.stroke-95"),sQuery(id+"F2.wireOp",EDGE,"E2.sketch_text.stroke-96"),sQuery(id+"F2.wireOp",EDGE,"E2.sketch_text.stroke-97"),sQuery(id+"F2.wireOp",EDGE,"E2.sketch_text.stroke-98"),sQuery(id+"F2.wireOp",EDGE,"E2.sketch_text.stroke-99"),sQuery(id+"F2.wireOp",EDGE,"E2.sketch_text.stroke-100"),sQuery(id+"F2.wireOp",EDGE,"E2.sketch_text.stroke-101"),sQuery(id+"F2.wireOp",EDGE,"E2.sketch_text.stroke-102"),sQuery(id+"F2.wireOp",EDGE,"E2.sketch_text.stroke-103"),sQuery(id+"F2.wireOp",EDGE,"E2.sketch_text.stroke-104"),sQuery(id+"F2.wireOp",EDGE,"E2.sketch_text.stroke-105"),sQuery(id+"F2.wireOp",EDGE,"E2.sketch_text.stroke-106"),sQuery(id+"F2.wireOp",EDGE,"E2.sketch_text.stroke-107"),sQuery(id+"F2.wireOp",EDGE,"E2.sketch_text.stroke-108"),sQuery(id+"F2.wireOp",EDGE,"E2.sketch_text.stroke-109"),sQuery(id+"F2.wireOp",EDGE,"E2.sketch_text.stroke-110"),sQuery(id+"F2.wireOp",EDGE,"E2.sketch_text.stroke-111"),sQuery(id+"F2.wireOp",EDGE,"E2.sketch_text.stroke-112"),sQuery(id+"F2.wireOp",EDGE,"E2.sketch_text.stroke-113"),sQuery(id+"F2.wireOp",EDGE,"E2.sketch_text.stroke-114"),sQuery(id+"F2.wireOp",EDGE,"E2.sketch_text.stroke-115"),sQuery(id+"F2.wireOp",EDGE,"E2.sketch_text.stroke-116"),sQuery(id+"F2.wireOp",EDGE,"E2.sketch_text.stroke-117"),sQuery(id+"F2.wireOp",EDGE,"E2.sketch_text.stroke-118"),sQuery(id+"F2.wireOp",EDGE,"E2.sketch_text.stroke-119"),sQuery(id+"F2.wireOp",EDGE,"E2.sketch_text.stroke-120"),sQuery(id+"F2.wireOp",EDGE,"E2.sketch_text.stroke-121"),sQuery(id+"F2.wireOp",EDGE,"E2.sketch_text.stroke-122"),sQuery(id+"F2.wireOp",EDGE,"E2.sketch_text.stroke-123"),sQuery(id+"F2.wireOp",EDGE,"E2.sketch_text.stroke-124"),sQuery(id+"F2.wireOp",EDGE,"E2.sketch_text.stroke-125"),sQuery(id+"F2.wireOp",EDGE,"E2.sketch_text.stroke-126"),sQuery(id+"F2.wireOp",EDGE,"E2.sketch_text.stroke-127"),sQuery(id+"F2.wireOp",EDGE,"E2.sketch_text.stroke-128"),sQuery(id+"F2.wireOp",EDGE,"E2.sketch_text.stroke-129"),sQuery(id+"F2.wireOp",EDGE,"E2.sketch_text.stroke-130"),sQuery(id+"F2.wireOp",EDGE,"E2.sketch_text.stroke-131"),sQuery(id+"F2.wireOp",EDGE,"E2.sketch_text.stroke-132"),sQuery(id+"F2.wireOp",EDGE,"E2.sketch_text.stroke-133"),sQuery(id+"F2.wireOp",EDGE,"E2.sketch_text.stroke-134"),sQuery(id+"F2.wireOp",EDGE,"E2.sketch_text.stroke-135"),sQuery(id+"F2.wireOp",EDGE,"E2.sketch_text.stroke-136"),sQuery(id+"F2.wireOp",EDGE,"E2.sketch_text.stroke-137"),sQuery(id+"F2.wireOp",EDGE,"E2.sketch_text.stroke-138"),sQuery(id+"F2.wireOp",EDGE,"E2.sketch_text.stroke-139"),sQuery(id+"F2.wireOp",EDGE,"E2.sketch_text.stroke-140"),sQuery(id+"F2.wireOp",EDGE,"E2.sketch_text.stroke-141"),sQuery(id+"F2.wireOp",EDGE,"E2.sketch_text.stroke-142"),sQuery(id+"F2.wireOp",EDGE,"E2.sketch_text.stroke-143"),sQuery(id+"F2.wireOp",EDGE,"E2.sketch_text.stroke-144"),sQuery(id+"F2.wireOp",EDGE,"E2.sketch_text.stroke-145"),sQuery(id+"F2.wireOp",EDGE,"E2.sketch_text.stroke-146"),sQuery(id+"F2.wireOp",EDGE,"E2.sketch_text.stroke-147"),sQuery(id+"F2.wireOp",EDGE,"E2.sketch_text.stroke-148"),sQuery(id+"F2.wireOp",EDGE,"E2.sketch_text.stroke-149"),sQuery(id+"F2.wireOp",EDGE,"E2.sketch_text.stroke-150"),sQuery(id+"F2.wireOp",EDGE,"E2.sketch_text.stroke-151"),sQuery(id+"F2.wireOp",EDGE,"E2.sketch_text.stroke-152"),sQuery(id+"F2.wireOp",EDGE,"E2.sketch_text.stroke-153"),sQuery(id+"F2.wireOp",EDGE,"E2.sketch_text.stroke-154"),sQuery(id+"F2.wireOp",EDGE,"E2.sketch_text.stroke-155"),sQuery(id+"F2.wireOp",EDGE,"E2.sketch_text.stroke-156"),sQuery(id+"F2.wireOp",EDGE,"E2.sketch_text.stroke-157"),sQuery(id+"F2.wireOp",EDGE,"E2.sketch_text.stroke-158"),sQuery(id+"F2.wireOp",EDGE,"E2.sketch_text.stroke-159"),sQuery(id+"F2.wireOp",EDGE,"E2.sketch_text.stroke-160"),sQuery(id+"F2.wireOp",EDGE,"E2.sketch_text.stroke-161"),sQuery(id+"F2.wireOp",EDGE,"E2.sketch_text.stroke-162"),sQuery(id+"F2.wireOp",EDGE,"E2.sketch_text.stroke-163"),sQuery(id+"F2.wireOp",EDGE,"E2.sketch_text.stroke-164"),sQuery(id+"F2.wireOp",EDGE,"E2.sketch_text.stroke-165"),sQuery(id+"F2.wireOp",EDGE,"E2.sketch_text.stroke-166"),sQuery(id+"F2.wireOp",EDGE,"E2.sketch_text.stroke-167"),sQuery(id+"F2.wireOp",EDGE,"E2.sketch_text.stroke-168"),sQuery(id+"F2.wireOp",EDGE,"E2.sketch_text.stroke-169"),sQuery(id+"F2.wireOp",EDGE,"E2.sketch_text.stroke-170"),sQuery(id+"F2.wireOp",EDGE,"E2.sketch_text.stroke-171"),sQuery(id+"F2.wireOp",EDGE,"E2.sketch_text.stroke-172"),sQuery(id+"F2.wireOp",EDGE,"E2.sketch_text.stroke-173"),sQuery(id+"F3.wireOp",EDGE,"E4.sketch_text.stroke-0"),sQuery(id+"F3.wireOp",EDGE,"E4.sketch_text.stroke-1"),sQuery(id+"F3.wireOp",EDGE,"E4.sketch_text.stroke-2"),sQuery(id+"F3.wireOp",EDGE,"E4.sketch_text.stroke-3"),sQuery(id+"F3.wireOp",EDGE,"E4.sketch_text.stroke-4"),sQuery(id+"F3.wireOp",EDGE,"E4.sketch_text.stroke-5"),sQuery(id+"F3.wireOp",EDGE,"E4.sketch_text.stroke-6"),sQuery(id+"F3.wireOp",EDGE,"E4.sketch_text.stroke-7"),sQuery(id+"F3.wireOp",EDGE,"E4.sketch_text.stroke-8"),sQuery(id+"F3.wireOp",EDGE,"E4.sketch_text.stroke-9"),sQuery(id+"F3.wireOp",EDGE,"E4.sketch_text.stroke-10"),sQuery(id+"F3.wireOp",EDGE,"E4.sketch_text.stroke-11"),sQuery(id+"F3.wireOp",EDGE,"E4.sketch_text.stroke-12"),sQuery(id+"F3.wireOp",EDGE,"E4.sketch_text.stroke-13"),sQuery(id+"F3.wireOp",EDGE,"E4.sketch_text.stroke-14"),sQuery(id+"F3.wireOp",EDGE,"E4.sketch_text.stroke-15"),sQuery(id+"F3.wireOp",EDGE,"E4.sketch_text.stroke-16"),sQuery(id+"F3.wireOp",EDGE,"E4.sketch_text.stroke-17"),sQuery(id+"F3.wireOp",EDGE,"E4.sketch_text.stroke-18"),sQuery(id+"F3.wireOp",EDGE,"E4.sketch_text.stroke-19"),sQuery(id+"F3.wireOp",EDGE,"E4.sketch_text.stroke-20"),sQuery(id+"F3.wireOp",EDGE,"E4.sketch_text.stroke-21"),sQuery(id+"F3.wireOp",EDGE,"E4.sketch_text.stroke-22"),sQuery(id+"F3.wireOp",EDGE,"E4.sketch_text.stroke-23"),sQuery(id+"F3.wireOp",EDGE,"E4.sketch_text.stroke-24"),sQuery(id+"F3.wireOp",EDGE,"E4.sketch_text.stroke-25"),sQuery(id+"F3.wireOp",EDGE,"E4.sketch_text.stroke-26"),sQuery(id+"F3.wireOp",EDGE,"E4.sketch_text.stroke-27"),sQuery(id+"F3.wireOp",EDGE,"E4.sketch_text.stroke-28"),sQuery(id+"F3.wireOp",EDGE,"E4.sketch_text.stroke-29"),sQuery(id+"F3.wireOp",EDGE,"E4.sketch_text.stroke-30"),sQuery(id+"F3.wireOp",EDGE,"E4.sketch_text.stroke-31"),sQuery(id+"F3.wireOp",EDGE,"E4.sketch_text.stroke-32"),sQuery(id+"F3.wireOp",EDGE,"E4.sketch_text.stroke-33"),sQuery(id+"F3.wireOp",EDGE,"E4.sketch_text.stroke-34"),sQuery(id+"F3.wireOp",EDGE,"E4.sketch_text.stroke-35"),sQuery(id+"F3.wireOp",EDGE,"E4.sketch_text.stroke-36"),sQuery(id+"F3.wireOp",EDGE,"E4.sketch_text.stroke-37"),sQuery(id+"F3.wireOp",EDGE,"E4.sketch_text.stroke-38"),sQuery(id+"F3.wireOp",EDGE,"E4.sketch_text.stroke-39"),sQuery(id+"F3.wireOp",EDGE,"E4.sketch_text.stroke-40"),sQuery(id+"F3.wireOp",EDGE,"E4.sketch_text.stroke-41"),sQuery(id+"F3.wireOp",EDGE,"E4.sketch_text.stroke-42"),sQuery(id+"F3.wireOp",EDGE,"E4.sketch_text.stroke-43"),sQuery(id+"F3.wireOp",EDGE,"E4.sketch_text.stroke-44"),sQuery(id+"F3.wireOp",EDGE,"E4.sketch_text.stroke-45"),sQuery(id+"F3.wireOp",EDGE,"E4.sketch_text.stroke-46"),sQuery(id+"F3.wireOp",EDGE,"E4.sketch_text.stroke-47"),sQuery(id+"F3.wireOp",EDGE,"E4.sketch_text.stroke-48"),sQuery(id+"F3.wireOp",EDGE,"E4.sketch_text.stroke-49"),sQuery(id+"F3.wireOp",EDGE,"E4.sketch_text.stroke-50"),sQuery(id+"F3.wireOp",EDGE,"E4.sketch_text.stroke-51"),sQuery(id+"F3.wireOp",EDGE,"E4.sketch_text.stroke-52"),sQuery(id+"F3.wireOp",EDGE,"E4.sketch_text.stroke-53"),sQuery(id+"F3.wireOp",EDGE,"E4.sketch_text.stroke-54"),sQuery(id+"F3.wireOp",EDGE,"E4.sketch_text.stroke-55"),sQuery(id+"F3.wireOp",EDGE,"E4.sketch_text.stroke-56"),sQuery(id+"F3.wireOp",EDGE,"E4.sketch_text.stroke-57"),sQuery(id+"F3.wireOp",EDGE,"E4.sketch_text.stroke-58"),sQuery(id+"F3.wireOp",EDGE,"E4.sketch_text.stroke-59"),sQuery(id+"F3.wireOp",EDGE,"E4.sketch_text.stroke-60"),sQuery(id+"F3.wireOp",EDGE,"E4.sketch_text.stroke-61"),sQuery(id+"F3.wireOp",EDGE,"E4.sketch_text.stroke-62"),sQuery(id+"F3.wireOp",EDGE,"E4.sketch_text.stroke-71"),sQuery(id+"F3.wireOp",EDGE,"E4.sketch_text.stroke-72"),sQuery(id+"F3.wireOp",EDGE,"E4.sketch_text.stroke-73"),sQuery(id+"F3.wireOp",EDGE,"E4.sketch_text.stroke-74"),sQuery(id+"F3.wireOp",EDGE,"E4.sketch_text.stroke-75"),sQuery(id+"F3.wireOp",EDGE,"E4.sketch_text.stroke-76"),sQuery(id+"F3.wireOp",EDGE,"E4.sketch_text.stroke-77"),sQuery(id+"F3.wireOp",EDGE,"E4.sketch_text.stroke-78"),sQuery(id+"F3.wireOp",EDGE,"E4.sketch_text.stroke-79"),sQuery(id+"F3.wireOp",EDGE,"E4.sketch_text.stroke-80"),sQuery(id+"F3.wireOp",EDGE,"E4.sketch_text.stroke-81"),sQuery(id+"F3.wireOp",EDGE,"E4.sketch_text.stroke-82"),sQuery(id+"F3.wireOp",EDGE,"E4.sketch_text.stroke-83"),sQuery(id+"F3.wireOp",EDGE,"E4.sketch_text.stroke-84"),sQuery(id+"F3.wireOp",EDGE,"E4.sketch_text.stroke-85"),sQuery(id+"F3.wireOp",EDGE,"E4.sketch_text.stroke-86"),sQuery(id+"F3.wireOp",EDGE,"E4.sketch_text.stroke-87"),sQuery(id+"F3.wireOp",EDGE,"E4.sketch_text.stroke-88"),sQuery(id+"F3.wireOp",EDGE,"E4.sketch_text.stroke-89"),sQuery(id+"F3.wireOp",EDGE,"E4.sketch_text.stroke-90"),sQuery(id+"F3.wireOp",EDGE,"E4.sketch_text.stroke-91"),sQuery(id+"F3.wireOp",EDGE,"E4.sketch_text.stroke-92"),sQuery(id+"F3.wireOp",EDGE,"E4.sketch_text.stroke-93"),sQuery(id+"F3.wireOp",EDGE,"E4.sketch_text.stroke-94"),sQuery(id+"F3.wireOp",EDGE,"E4.sketch_text.stroke-95"),sQuery(id+"F3.wireOp",EDGE,"E4.sketch_text.stroke-96"),sQuery(id+"F3.wireOp",EDGE,"E4.sketch_text.stroke-97"),sQuery(id+"F3.wireOp",EDGE,"E4.sketch_text.stroke-103"),sQuery(id+"F3.wireOp",EDGE,"E4.sketch_text.stroke-104"),sQuery(id+"F3.wireOp",EDGE,"E4.sketch_text.stroke-105"),sQuery(id+"F3.wireOp",EDGE,"E4.sketch_text.stroke-106"),sQuery(id+"F3.wireOp",EDGE,"E4.sketch_text.stroke-107"),sQuery(id+"F3.wireOp",EDGE,"E4.sketch_text.stroke-108"),sQuery(id+"F3.wireOp",EDGE,"E4.sketch_text.stroke-109"),sQuery(id+"F3.wireOp",EDGE,"E4.sketch_text.stroke-110"),sQuery(id+"F3.wireOp",EDGE,"E4.sketch_text.stroke-111"),sQuery(id+"F3.wireOp",EDGE,"E4.sketch_text.stroke-112"),sQuery(id+"F3.wireOp",EDGE,"E4.sketch_text.stroke-113"),sQuery(id+"F3.wireOp",EDGE,"E4.sketch_text.stroke-114"),sQuery(id+"F3.wireOp",EDGE,"E4.sketch_text.stroke-115"),sQuery(id+"F3.wireOp",EDGE,"E4.sketch_text.stroke-116"),sQuery(id+"F3.wireOp",EDGE,"E4.sketch_text.stroke-117"),sQuery(id+"F3.wireOp",EDGE,"E4.sketch_text.stroke-118"),sQuery(id+"F3.wireOp",EDGE,"E4.sketch_text.stroke-119"),sQuery(id+"F3.wireOp",EDGE,"E4.sketch_text.stroke-120"),sQuery(id+"F3.wireOp",EDGE,"E4.sketch_text.stroke-121"),sQuery(id+"F3.wireOp",EDGE,"E4.sketch_text.stroke-122"),sQuery(id+"F3.wireOp",EDGE,"E4.sketch_text.stroke-123"),sQuery(id+"F3.wireOp",EDGE,"E4.sketch_text.stroke-124"),sQuery(id+"F3.wireOp",EDGE,"E4.sketch_text.stroke-125"),sQuery(id+"F3.wireOp",EDGE,"E4.sketch_text.stroke-126"),sQuery(id+"F3.wireOp",EDGE,"E4.sketch_text.stroke-127"),sQuery(id+"F3.wireOp",EDGE,"E4.sketch_text.stroke-128"),sQuery(id+"F3.wireOp",EDGE,"E4.sketch_text.stroke-129"),sQuery(id+"F3.wireOp",EDGE,"E4.sketch_text.stroke-130"),sQuery(id+"F3.wireOp",EDGE,"E4.sketch_text.stroke-131"),sQuery(id+"F3.wireOp",EDGE,"E4.sketch_text.stroke-132"),sQuery(id+"F3.wireOp",EDGE,"E4.sketch_text.stroke-133"),sQuery(id+"F3.wireOp",EDGE,"E4.sketch_text.stroke-134"),sQuery(id+"F3.wireOp",EDGE,"E4.sketch_text.stroke-135"),sQuery(id+"F3.wireOp",EDGE,"E4.sketch_text.stroke-136"),sQuery(id+"F3.wireOp",EDGE,"E4.sketch_text.stroke-137"),sQuery(id+"F3.wireOp",EDGE,"E4.sketch_text.stroke-138"),sQuery(id+"F3.wireOp",EDGE,"E4.sketch_text.stroke-139"),sQuery(id+"F3.wireOp",EDGE,"E4.sketch_text.stroke-140"),sQuery(id+"F3.wireOp",EDGE,"E4.sketch_text.stroke-141"),sQuery(id+"F3.wireOp",EDGE,"E4.sketch_text.stroke-142"),sQuery(id+"F3.wireOp",EDGE,"E4.sketch_text.stroke-143"),sQuery(id+"F3.wireOp",EDGE,"E4.sketch_text.stroke-144"),sQuery(id+"F3.wireOp",EDGE,"E4.sketch_text.stroke-145"),sQuery(id+"F3.wireOp",EDGE,"E4.sketch_text.stroke-146"),sQuery(id+"F3.wireOp",EDGE,"E4.sketch_text.stroke-147"),sQuery(id+"F3.wireOp",EDGE,"E4.sketch_text.stroke-148"),sQuery(id+"F3.wireOp",EDGE,"E4.sketch_text.stroke-149"),sQuery(id+"F3.wireOp",EDGE,"E4.sketch_text.stroke-150"),sQuery(id+"F3.wireOp",EDGE,"E4.sketch_text.stroke-151"),sQuery(id+"F3.wireOp",EDGE,"E4.sketch_text.stroke-152"),sQuery(id+"F3.wireOp",EDGE,"E4.sketch_text.stroke-153"),sQuery(id+"F3.wireOp",EDGE,"E4.sketch_text.stroke-159"),sQuery(id+"F3.wireOp",EDGE,"E4.sketch_text.stroke-160"),sQuery(id+"F3.wireOp",EDGE,"E4.sketch_text.stroke-161"),sQuery(id+"F3.wireOp",EDGE,"E4.sketch_text.stroke-162"),sQuery(id+"F3.wireOp",EDGE,"E4.sketch_text.stroke-163"),sQuery(id+"F3.wireOp",EDGE,"E4.sketch_text.stroke-164"),sQuery(id+"F3.wireOp",EDGE,"E4.sketch_text.stroke-165"),sQuery(id+"F3.wireOp",EDGE,"E4.sketch_text.stroke-166"),sQuery(id+"F3.wireOp",EDGE,"E4.sketch_text.stroke-167"),sQuery(id+"F3.wireOp",EDGE,"E4.sketch_text.stroke-168"),sQuery(id+"F3.wireOp",EDGE,"E4.sketch_text.stroke-169"),sQuery(id+"F3.wireOp",EDGE,"E4.sketch_text.stroke-170"),sQuery(id+"F3.wireOp",EDGE,"E4.sketch_text.stroke-171"),sQuery(id+"F3.wireOp",EDGE,"E4.sketch_text.stroke-172"),sQuery(id+"F3.wireOp",EDGE,"E4.sketch_text.stroke-173"),sQuery(id+"F3.wireOp",EDGE,"E4.sketch_text.stroke-174"),sQuery(id+"F3.wireOp",EDGE,"E4.sketch_text.stroke-175"),sQuery(id+"F3.wireOp",EDGE,"E4.sketch_text.stroke-176"),sQuery(id+"F3.wireOp",EDGE,"E4.sketch_text.stroke-177"),sQuery(id+"F3.wireOp",EDGE,"E4.sketch_text.stroke-178"),sQuery(id+"F3.wireOp",EDGE,"E4.sketch_text.stroke-179"),sQuery(id+"F3.wireOp",EDGE,"E4.sketch_text.stroke-180"),subQ2,sQuery(id+"F5.wireOp",EDGE,"6ee83ff3-586e-4dbe-aaea-af71240543bd")])],"isStart":true})])],"derivedFrom":makeQuery(id+"F6.opExtrude","CAP_EDGE",EDGE,{"disambiguationData":[OSD([subQ2])],"isStart":true})});}
            var Q3;
            {var subQ0=sQuery(id+"F5.wireOp",EDGE,"8007402e-1a4e-4a06-85a5-2af08e553504");var subQ1=sQuery(id+"F0.wireOp",EDGE,"E0.top");var subQ2=sQuery(id+"F5.wireOp",EDGE,"6ee83ff3-586e-4dbe-aaea-af71240543bd");var subQ3=sQuery(id+"F0.wireOp",EDGE,"E0.bottom");Q3=makeQuery(id+"F6.boolean.opBoolean","SPLIT",EDGE,{"disambiguationData":[TD([makeQuery(id+"F1.opExtrude","CAP_FACE",FACE,{"disambiguationData":[OSD([subQ3,subQ1,sQuery(id+"F0.wireOp",EDGE,"E0.left"),sQuery(id+"F0.wireOp",EDGE,"E0.right")])],"isStart":false}),makeQuery(id+"F1.opExtrude","SWEPT_FACE",FACE,{"disambiguationData":[OSD([subQ1])]}),makeQuery(id+"F6.opExtrude","SWEPT_FACE",FACE,{"disambiguationData":[OSD([subQ0])]}),makeQuery(id+"F6.opExtrude","CAP_FACE",FACE,{"disambiguationData":[OSD([subQ3,sQuery(id+"F2.wireOp",EDGE,"E2.sketch_text.stroke-0"),sQuery(id+"F2.wireOp",EDGE,"E2.sketch_text.stroke-1"),sQuery(id+"F2.wireOp",EDGE,"E2.sketch_text.stroke-2"),sQuery(id+"F2.wireOp",EDGE,"E2.sketch_text.stroke-3"),sQuery(id+"F2.wireOp",EDGE,"E2.sketch_text.stroke-4"),sQuery(id+"F2.wireOp",EDGE,"E2.sketch_text.stroke-5"),sQuery(id+"F2.wireOp",EDGE,"E2.sketch_text.stroke-6"),sQuery(id+"F2.wireOp",EDGE,"E2.sketch_text.stroke-7"),sQuery(id+"F2.wireOp",EDGE,"E2.sketch_text.stroke-8"),sQuery(id+"F2.wireOp",EDGE,"E2.sketch_text.stroke-9"),sQuery(id+"F2.wireOp",EDGE,"E2.sketch_text.stroke-10"),sQuery(id+"F2.wireOp",EDGE,"E2.sketch_text.stroke-11"),sQuery(id+"F2.wireOp",EDGE,"E2.sketch_text.stroke-12"),sQuery(id+"F2.wireOp",EDGE,"E2.sketch_text.stroke-13"),sQuery(id+"F2.wireOp",EDGE,"E2.sketch_text.stroke-14"),sQuery(id+"F2.wireOp",EDGE,"E2.sketch_text.stroke-15"),sQuery(id+"F2.wireOp",EDGE,"E2.sketch_text.stroke-16"),sQuery(id+"F2.wireOp",EDGE,"E2.sketch_text.stroke-17"),sQuery(id+"F2.wireOp",EDGE,"E2.sketch_text.stroke-18"),sQuery(id+"F2.wireOp",EDGE,"E2.sketch_text.stroke-19"),sQuery(id+"F2.wireOp",EDGE,"E2.sketch_text.stroke-20"),sQuery(id+"F2.wireOp",EDGE,"E2.sketch_text.stroke-21"),sQuery(id+"F2.wireOp",EDGE,"E2.sketch_text.stroke-22"),sQuery(id+"F2.wireOp",EDGE,"E2.sketch_text.stroke-23"),sQuery(id+"F2.wireOp",EDGE,"E2.sketch_text.stroke-24"),sQuery(id+"F2.wireOp",EDGE,"E2.sketch_text.stroke-25"),sQuery(id+"F2.wireOp",EDGE,"E2.sketch_text.stroke-26"),sQuery(id+"F2.wireOp",EDGE,"E2.sketch_text.stroke-27"),sQuery(id+"F2.wireOp",EDGE,"E2.sketch_text.stroke-28"),sQuery(id+"F2.wireOp",EDGE,"E2.sketch_text.stroke-29"),sQuery(id+"F2.wireOp",EDGE,"E2.sketch_text.stroke-30"),sQuery(id+"F2.wireOp",EDGE,"E2.sketch_text.stroke-31"),sQuery(id+"F2.wireOp",EDGE,"E2.sketch_text.stroke-32"),sQuery(id+"F2.wireOp",EDGE,"E2.sketch_text.stroke-33"),sQuery(id+"F2.wireOp",EDGE,"E2.sketch_text.stroke-34"),sQuery(id+"F2.wireOp",EDGE,"E2.sketch_text.stroke-35"),sQuery(id+"F2.wireOp",EDGE,"E2.sketch_text.stroke-36"),sQuery(id+"F2.wireOp",EDGE,"E2.sketch_text.stroke-37"),sQuery(id+"F2.wireOp",EDGE,"E2.sketch_text.stroke-38"),sQuery(id+"F2.wireOp",EDGE,"E2.sketch_text.stroke-39"),sQuery(id+"F2.wireOp",EDGE,"E2.sketch_text.stroke-40"),sQuery(id+"F2.wireOp",EDGE,"E2.sketch_text.stroke-41"),sQuery(id+"F2.wireOp",EDGE,"E2.sketch_text.stroke-42"),sQuery(id+"F2.wireOp",EDGE,"E2.sketch_text.stroke-43"),sQuery(id+"F2.wireOp",EDGE,"E2.sketch_text.stroke-44"),sQuery(id+"F2.wireOp",EDGE,"E2.sketch_text.stroke-45"),sQuery(id+"F2.wireOp",EDGE,"E2.sketch_text.stroke-46"),sQuery(id+"F2.wireOp",EDGE,"E2.sketch_text.stroke-47"),sQuery(id+"F2.wireOp",EDGE,"E2.sketch_text.stroke-48"),sQuery(id+"F2.wireOp",EDGE,"E2.sketch_text.stroke-49"),sQuery(id+"F2.wireOp",EDGE,"E2.sketch_text.stroke-50"),sQuery(id+"F2.wireOp",EDGE,"E2.sketch_text.stroke-51"),sQuery(id+"F2.wireOp",EDGE,"E2.sketch_text.stroke-52"),sQuery(id+"F2.wireOp",EDGE,"E2.sketch_text.stroke-53"),sQuery(id+"F2.wireOp",EDGE,"E2.sketch_text.stroke-54"),sQuery(id+"F2.wireOp",EDGE,"E2.sketch_text.stroke-55"),sQuery(id+"F2.wireOp",EDGE,"E2.sketch_text.stroke-56"),sQuery(id+"F2.wireOp",EDGE,"E2.sketch_text.stroke-57"),sQuery(id+"F2.wireOp",EDGE,"E2.sketch_text.stroke-58"),sQuery(id+"F2.wireOp",EDGE,"E2.sketch_text.stroke-59"),sQuery(id+"F2.wireOp",EDGE,"E2.sketch_text.stroke-60"),sQuery(id+"F2.wireOp",EDGE,"E2.sketch_text.stroke-61"),sQuery(id+"F2.wireOp",EDGE,"E2.sketch_text.stroke-62"),sQuery(id+"F2.wireOp",EDGE,"E2.sketch_text.stroke-63"),sQuery(id+"F2.wireOp",EDGE,"E2.sketch_text.stroke-64"),sQuery(id+"F2.wireOp",EDGE,"E2.sketch_text.stroke-65"),sQuery(id+"F2.wireOp",EDGE,"E2.sketch_text.stroke-66"),sQuery(id+"F2.wireOp",EDGE,"E2.sketch_text.stroke-67"),sQuery(id+"F2.wireOp",EDGE,"E2.sketch_text.stroke-68"),sQuery(id+"F2.wireOp",EDGE,"E2.sketch_text.stroke-69"),sQuery(id+"F2.wireOp",EDGE,"E2.sketch_text.stroke-70"),sQuery(id+"F2.wireOp",EDGE,"E2.sketch_text.stroke-71"),sQuery(id+"F2.wireOp",EDGE,"E2.sketch_text.stroke-72"),sQuery(id+"F2.wireOp",EDGE,"E2.sketch_text.stroke-73"),sQuery(id+"F2.wireOp",EDGE,"E2.sketch_text.stroke-74"),sQuery(id+"F2.wireOp",EDGE,"E2.sketch_text.stroke-75"),sQuery(id+"F2.wireOp",EDGE,"E2.sketch_text.stroke-76"),sQuery(id+"F2.wireOp",EDGE,"E2.sketch_text.stroke-77"),sQuery(id+"F2.wireOp",EDGE,"E2.sketch_text.stroke-78"),sQuery(id+"F2.wireOp",EDGE,"E2.sketch_text.stroke-79"),sQuery(id+"F2.wireOp",EDGE,"E2.sketch_text.stroke-80"),sQuery(id+"F2.wireOp",EDGE,"E2.sketch_text.stroke-81"),sQuery(id+"F2.wireOp",EDGE,"E2.sketch_text.stroke-82"),sQuery(id+"F2.wireOp",EDGE,"E2.sketch_text.stroke-83"),sQuery(id+"F2.wireOp",EDGE,"E2.sketch_text.stroke-84"),sQuery(id+"F2.wireOp",EDGE,"E2.sketch_text.stroke-85"),sQuery(id+"F2.wireOp",EDGE,"E2.sketch_text.stroke-86"),sQuery(id+"F2.wireOp",EDGE,"E2.sketch_text.stroke-87"),sQuery(id+"F2.wireOp",EDGE,"E2.sketch_text.stroke-88"),sQuery(id+"F2.wireOp",EDGE,"E2.sketch_text.stroke-89"),sQuery(id+"F2.wireOp",EDGE,"E2.sketch_text.stroke-90"),sQuery(id+"F2.wireOp",EDGE,"E2.sketch_text.stroke-91"),sQuery(id+"F2.wireOp",EDGE,"E2.sketch_text.stroke-92"),sQuery(id+"F2.wireOp",EDGE,"E2.sketch_text.stroke-93"),sQuery(id+"F2.wireOp",EDGE,"E2.sketch_text.stroke-94"),sQuery(id+"F2.wireOp",EDGE,"E2.sketch_text.stroke-95"),sQuery(id+"F2.wireOp",EDGE,"E2.sketch_text.stroke-96"),sQuery(id+"F2.wireOp",EDGE,"E2.sketch_text.stroke-97"),sQuery(id+"F2.wireOp",EDGE,"E2.sketch_text.stroke-98"),sQuery(id+"F2.wireOp",EDGE,"E2.sketch_text.stroke-99"),sQuery(id+"F2.wireOp",EDGE,"E2.sketch_text.stroke-100"),sQuery(id+"F2.wireOp",EDGE,"E2.sketch_text.stroke-101"),sQuery(id+"F2.wireOp",EDGE,"E2.sketch_text.stroke-102"),sQuery(id+"F2.wireOp",EDGE,"E2.sketch_text.stroke-103"),sQuery(id+"F2.wireOp",EDGE,"E2.sketch_text.stroke-104"),sQuery(id+"F2.wireOp",EDGE,"E2.sketch_text.stroke-105"),sQuery(id+"F2.wireOp",EDGE,"E2.sketch_text.stroke-106"),sQuery(id+"F2.wireOp",EDGE,"E2.sketch_text.stroke-107"),sQuery(id+"F2.wireOp",EDGE,"E2.sketch_text.stroke-108"),sQuery(id+"F2.wireOp",EDGE,"E2.sketch_text.stroke-109"),sQuery(id+"F2.wireOp",EDGE,"E2.sketch_text.stroke-110"),sQuery(id+"F2.wireOp",EDGE,"E2.sketch_text.stroke-111"),sQuery(id+"F2.wireOp",EDGE,"E2.sketch_text.stroke-112"),sQuery(id+"F2.wireOp",EDGE,"E2.sketch_text.stroke-113"),sQuery(id+"F2.wireOp",EDGE,"E2.sketch_text.stroke-114"),sQuery(id+"F2.wireOp",EDGE,"E2.sketch_text.stroke-115"),sQuery(id+"F2.wireOp",EDGE,"E2.sketch_text.stroke-116"),sQuery(id+"F2.wireOp",EDGE,"E2.sketch_text.stroke-117"),sQuery(id+"F2.wireOp",EDGE,"E2.sketch_text.stroke-118"),sQuery(id+"F2.wireOp",EDGE,"E2.sketch_text.stroke-119"),sQuery(id+"F2.wireOp",EDGE,"E2.sketch_text.stroke-120"),sQuery(id+"F2.wireOp",EDGE,"E2.sketch_text.stroke-121"),sQuery(id+"F2.wireOp",EDGE,"E2.sketch_text.stroke-122"),sQuery(id+"F2.wireOp",EDGE,"E2.sketch_text.stroke-123"),sQuery(id+"F2.wireOp",EDGE,"E2.sketch_text.stroke-124"),sQuery(id+"F2.wireOp",EDGE,"E2.sketch_text.stroke-125"),sQuery(id+"F2.wireOp",EDGE,"E2.sketch_text.stroke-126"),sQuery(id+"F2.wireOp",EDGE,"E2.sketch_text.stroke-127"),sQuery(id+"F2.wireOp",EDGE,"E2.sketch_text.stroke-128"),sQuery(id+"F2.wireOp",EDGE,"E2.sketch_text.stroke-129"),sQuery(id+"F2.wireOp",EDGE,"E2.sketch_text.stroke-130"),sQuery(id+"F2.wireOp",EDGE,"E2.sketch_text.stroke-131"),sQuery(id+"F2.wireOp",EDGE,"E2.sketch_text.stroke-132"),sQuery(id+"F2.wireOp",EDGE,"E2.sketch_text.stroke-133"),sQuery(id+"F2.wireOp",EDGE,"E2.sketch_text.stroke-134"),sQuery(id+"F2.wireOp",EDGE,"E2.sketch_text.stroke-135"),sQuery(id+"F2.wireOp",EDGE,"E2.sketch_text.stroke-136"),sQuery(id+"F2.wireOp",EDGE,"E2.sketch_text.stroke-137"),sQuery(id+"F2.wireOp",EDGE,"E2.sketch_text.stroke-138"),sQuery(id+"F2.wireOp",EDGE,"E2.sketch_text.stroke-139"),sQuery(id+"F2.wireOp",EDGE,"E2.sketch_text.stroke-140"),sQuery(id+"F2.wireOp",EDGE,"E2.sketch_text.stroke-141"),sQuery(id+"F2.wireOp",EDGE,"E2.sketch_text.stroke-142"),sQuery(id+"F2.wireOp",EDGE,"E2.sketch_text.stroke-143"),sQuery(id+"F2.wireOp",EDGE,"E2.sketch_text.stroke-144"),sQuery(id+"F2.wireOp",EDGE,"E2.sketch_text.stroke-145"),sQuery(id+"F2.wireOp",EDGE,"E2.sketch_text.stroke-146"),sQuery(id+"F2.wireOp",EDGE,"E2.sketch_text.stroke-147"),sQuery(id+"F2.wireOp",EDGE,"E2.sketch_text.stroke-148"),sQuery(id+"F2.wireOp",EDGE,"E2.sketch_text.stroke-149"),sQuery(id+"F2.wireOp",EDGE,"E2.sketch_text.stroke-150"),sQuery(id+"F2.wireOp",EDGE,"E2.sketch_text.stroke-151"),sQuery(id+"F2.wireOp",EDGE,"E2.sketch_text.stroke-152"),sQuery(id+"F2.wireOp",EDGE,"E2.sketch_text.stroke-153"),sQuery(id+"F2.wireOp",EDGE,"E2.sketch_text.stroke-154"),sQuery(id+"F2.wireOp",EDGE,"E2.sketch_text.stroke-155"),sQuery(id+"F2.wireOp",EDGE,"E2.sketch_text.stroke-156"),sQuery(id+"F2.wireOp",EDGE,"E2.sketch_text.stroke-157"),sQuery(id+"F2.wireOp",EDGE,"E2.sketch_text.stroke-158"),sQuery(id+"F2.wireOp",EDGE,"E2.sketch_text.stroke-159"),sQuery(id+"F2.wireOp",EDGE,"E2.sketch_text.stroke-160"),sQuery(id+"F2.wireOp",EDGE,"E2.sketch_text.stroke-161"),sQuery(id+"F2.wireOp",EDGE,"E2.sketch_text.stroke-162"),sQuery(id+"F2.wireOp",EDGE,"E2.sketch_text.stroke-163"),sQuery(id+"F2.wireOp",EDGE,"E2.sketch_text.stroke-164"),sQuery(id+"F2.wireOp",EDGE,"E2.sketch_text.stroke-165"),sQuery(id+"F2.wireOp",EDGE,"E2.sketch_text.stroke-166"),sQuery(id+"F2.wireOp",EDGE,"E2.sketch_text.stroke-167"),sQuery(id+"F2.wireOp",EDGE,"E2.sketch_text.stroke-168"),sQuery(id+"F2.wireOp",EDGE,"E2.sketch_text.stroke-169"),sQuery(id+"F2.wireOp",EDGE,"E2.sketch_text.stroke-170"),sQuery(id+"F2.wireOp",EDGE,"E2.sketch_text.stroke-171"),sQuery(id+"F2.wireOp",EDGE,"E2.sketch_text.stroke-172"),sQuery(id+"F2.wireOp",EDGE,"E2.sketch_text.stroke-173"),sQuery(id+"F3.wireOp",EDGE,"E4.sketch_text.stroke-0"),sQuery(id+"F3.wireOp",EDGE,"E4.sketch_text.stroke-1"),sQuery(id+"F3.wireOp",EDGE,"E4.sketch_text.stroke-2"),sQuery(id+"F3.wireOp",EDGE,"E4.sketch_text.stroke-3"),sQuery(id+"F3.wireOp",EDGE,"E4.sketch_text.stroke-4"),sQuery(id+"F3.wireOp",EDGE,"E4.sketch_text.stroke-5"),sQuery(id+"F3.wireOp",EDGE,"E4.sketch_text.stroke-6"),sQuery(id+"F3.wireOp",EDGE,"E4.sketch_text.stroke-7"),sQuery(id+"F3.wireOp",EDGE,"E4.sketch_text.stroke-8"),sQuery(id+"F3.wireOp",EDGE,"E4.sketch_text.stroke-9"),sQuery(id+"F3.wireOp",EDGE,"E4.sketch_text.stroke-10"),sQuery(id+"F3.wireOp",EDGE,"E4.sketch_text.stroke-11"),sQuery(id+"F3.wireOp",EDGE,"E4.sketch_text.stroke-12"),sQuery(id+"F3.wireOp",EDGE,"E4.sketch_text.stroke-13"),sQuery(id+"F3.wireOp",EDGE,"E4.sketch_text.stroke-14"),sQuery(id+"F3.wireOp",EDGE,"E4.sketch_text.stroke-15"),sQuery(id+"F3.wireOp",EDGE,"E4.sketch_text.stroke-16"),sQuery(id+"F3.wireOp",EDGE,"E4.sketch_text.stroke-17"),sQuery(id+"F3.wireOp",EDGE,"E4.sketch_text.stroke-18"),sQuery(id+"F3.wireOp",EDGE,"E4.sketch_text.stroke-19"),sQuery(id+"F3.wireOp",EDGE,"E4.sketch_text.stroke-20"),sQuery(id+"F3.wireOp",EDGE,"E4.sketch_text.stroke-21"),sQuery(id+"F3.wireOp",EDGE,"E4.sketch_text.stroke-22"),sQuery(id+"F3.wireOp",EDGE,"E4.sketch_text.stroke-23"),sQuery(id+"F3.wireOp",EDGE,"E4.sketch_text.stroke-24"),sQuery(id+"F3.wireOp",EDGE,"E4.sketch_text.stroke-25"),sQuery(id+"F3.wireOp",EDGE,"E4.sketch_text.stroke-26"),sQuery(id+"F3.wireOp",EDGE,"E4.sketch_text.stroke-27"),sQuery(id+"F3.wireOp",EDGE,"E4.sketch_text.stroke-28"),sQuery(id+"F3.wireOp",EDGE,"E4.sketch_text.stroke-29"),sQuery(id+"F3.wireOp",EDGE,"E4.sketch_text.stroke-30"),sQuery(id+"F3.wireOp",EDGE,"E4.sketch_text.stroke-31"),sQuery(id+"F3.wireOp",EDGE,"E4.sketch_text.stroke-32"),sQuery(id+"F3.wireOp",EDGE,"E4.sketch_text.stroke-33"),sQuery(id+"F3.wireOp",EDGE,"E4.sketch_text.stroke-34"),sQuery(id+"F3.wireOp",EDGE,"E4.sketch_text.stroke-35"),sQuery(id+"F3.wireOp",EDGE,"E4.sketch_text.stroke-36"),sQuery(id+"F3.wireOp",EDGE,"E4.sketch_text.stroke-37"),sQuery(id+"F3.wireOp",EDGE,"E4.sketch_text.stroke-38"),sQuery(id+"F3.wireOp",EDGE,"E4.sketch_text.stroke-39"),sQuery(id+"F3.wireOp",EDGE,"E4.sketch_text.stroke-40"),sQuery(id+"F3.wireOp",EDGE,"E4.sketch_text.stroke-41"),sQuery(id+"F3.wireOp",EDGE,"E4.sketch_text.stroke-42"),sQuery(id+"F3.wireOp",EDGE,"E4.sketch_text.stroke-43"),sQuery(id+"F3.wireOp",EDGE,"E4.sketch_text.stroke-44"),sQuery(id+"F3.wireOp",EDGE,"E4.sketch_text.stroke-45"),sQuery(id+"F3.wireOp",EDGE,"E4.sketch_text.stroke-46"),sQuery(id+"F3.wireOp",EDGE,"E4.sketch_text.stroke-47"),sQuery(id+"F3.wireOp",EDGE,"E4.sketch_text.stroke-48"),sQuery(id+"F3.wireOp",EDGE,"E4.sketch_text.stroke-49"),sQuery(id+"F3.wireOp",EDGE,"E4.sketch_text.stroke-50"),sQuery(id+"F3.wireOp",EDGE,"E4.sketch_text.stroke-51"),sQuery(id+"F3.wireOp",EDGE,"E4.sketch_text.stroke-52"),sQuery(id+"F3.wireOp",EDGE,"E4.sketch_text.stroke-53"),sQuery(id+"F3.wireOp",EDGE,"E4.sketch_text.stroke-54"),sQuery(id+"F3.wireOp",EDGE,"E4.sketch_text.stroke-55"),sQuery(id+"F3.wireOp",EDGE,"E4.sketch_text.stroke-56"),sQuery(id+"F3.wireOp",EDGE,"E4.sketch_text.stroke-57"),sQuery(id+"F3.wireOp",EDGE,"E4.sketch_text.stroke-58"),sQuery(id+"F3.wireOp",EDGE,"E4.sketch_text.stroke-59"),sQuery(id+"F3.wireOp",EDGE,"E4.sketch_text.stroke-60"),sQuery(id+"F3.wireOp",EDGE,"E4.sketch_text.stroke-61"),sQuery(id+"F3.wireOp",EDGE,"E4.sketch_text.stroke-62"),sQuery(id+"F3.wireOp",EDGE,"E4.sketch_text.stroke-71"),sQuery(id+"F3.wireOp",EDGE,"E4.sketch_text.stroke-72"),sQuery(id+"F3.wireOp",EDGE,"E4.sketch_text.stroke-73"),sQuery(id+"F3.wireOp",EDGE,"E4.sketch_text.stroke-74"),sQuery(id+"F3.wireOp",EDGE,"E4.sketch_text.stroke-75"),sQuery(id+"F3.wireOp",EDGE,"E4.sketch_text.stroke-76"),sQuery(id+"F3.wireOp",EDGE,"E4.sketch_text.stroke-77"),sQuery(id+"F3.wireOp",EDGE,"E4.sketch_text.stroke-78"),sQuery(id+"F3.wireOp",EDGE,"E4.sketch_text.stroke-79"),sQuery(id+"F3.wireOp",EDGE,"E4.sketch_text.stroke-80"),sQuery(id+"F3.wireOp",EDGE,"E4.sketch_text.stroke-81"),sQuery(id+"F3.wireOp",EDGE,"E4.sketch_text.stroke-82"),sQuery(id+"F3.wireOp",EDGE,"E4.sketch_text.stroke-83"),sQuery(id+"F3.wireOp",EDGE,"E4.sketch_text.stroke-84"),sQuery(id+"F3.wireOp",EDGE,"E4.sketch_text.stroke-85"),sQuery(id+"F3.wireOp",EDGE,"E4.sketch_text.stroke-86"),sQuery(id+"F3.wireOp",EDGE,"E4.sketch_text.stroke-87"),sQuery(id+"F3.wireOp",EDGE,"E4.sketch_text.stroke-88"),sQuery(id+"F3.wireOp",EDGE,"E4.sketch_text.stroke-89"),sQuery(id+"F3.wireOp",EDGE,"E4.sketch_text.stroke-90"),sQuery(id+"F3.wireOp",EDGE,"E4.sketch_text.stroke-91"),sQuery(id+"F3.wireOp",EDGE,"E4.sketch_text.stroke-92"),sQuery(id+"F3.wireOp",EDGE,"E4.sketch_text.stroke-93"),sQuery(id+"F3.wireOp",EDGE,"E4.sketch_text.stroke-94"),sQuery(id+"F3.wireOp",EDGE,"E4.sketch_text.stroke-95"),sQuery(id+"F3.wireOp",EDGE,"E4.sketch_text.stroke-96"),sQuery(id+"F3.wireOp",EDGE,"E4.sketch_text.stroke-97"),sQuery(id+"F3.wireOp",EDGE,"E4.sketch_text.stroke-103"),sQuery(id+"F3.wireOp",EDGE,"E4.sketch_text.stroke-104"),sQuery(id+"F3.wireOp",EDGE,"E4.sketch_text.stroke-105"),sQuery(id+"F3.wireOp",EDGE,"E4.sketch_text.stroke-106"),sQuery(id+"F3.wireOp",EDGE,"E4.sketch_text.stroke-107"),sQuery(id+"F3.wireOp",EDGE,"E4.sketch_text.stroke-108"),sQuery(id+"F3.wireOp",EDGE,"E4.sketch_text.stroke-109"),sQuery(id+"F3.wireOp",EDGE,"E4.sketch_text.stroke-110"),sQuery(id+"F3.wireOp",EDGE,"E4.sketch_text.stroke-111"),sQuery(id+"F3.wireOp",EDGE,"E4.sketch_text.stroke-112"),sQuery(id+"F3.wireOp",EDGE,"E4.sketch_text.stroke-113"),sQuery(id+"F3.wireOp",EDGE,"E4.sketch_text.stroke-114"),sQuery(id+"F3.wireOp",EDGE,"E4.sketch_text.stroke-115"),sQuery(id+"F3.wireOp",EDGE,"E4.sketch_text.stroke-116"),sQuery(id+"F3.wireOp",EDGE,"E4.sketch_text.stroke-117"),sQuery(id+"F3.wireOp",EDGE,"E4.sketch_text.stroke-118"),sQuery(id+"F3.wireOp",EDGE,"E4.sketch_text.stroke-119"),sQuery(id+"F3.wireOp",EDGE,"E4.sketch_text.stroke-120"),sQuery(id+"F3.wireOp",EDGE,"E4.sketch_text.stroke-121"),sQuery(id+"F3.wireOp",EDGE,"E4.sketch_text.stroke-122"),sQuery(id+"F3.wireOp",EDGE,"E4.sketch_text.stroke-123"),sQuery(id+"F3.wireOp",EDGE,"E4.sketch_text.stroke-124"),sQuery(id+"F3.wireOp",EDGE,"E4.sketch_text.stroke-125"),sQuery(id+"F3.wireOp",EDGE,"E4.sketch_text.stroke-126"),sQuery(id+"F3.wireOp",EDGE,"E4.sketch_text.stroke-127"),sQuery(id+"F3.wireOp",EDGE,"E4.sketch_text.stroke-128"),sQuery(id+"F3.wireOp",EDGE,"E4.sketch_text.stroke-129"),sQuery(id+"F3.wireOp",EDGE,"E4.sketch_text.stroke-130"),sQuery(id+"F3.wireOp",EDGE,"E4.sketch_text.stroke-131"),sQuery(id+"F3.wireOp",EDGE,"E4.sketch_text.stroke-132"),sQuery(id+"F3.wireOp",EDGE,"E4.sketch_text.stroke-133"),sQuery(id+"F3.wireOp",EDGE,"E4.sketch_text.stroke-134"),sQuery(id+"F3.wireOp",EDGE,"E4.sketch_text.stroke-135"),sQuery(id+"F3.wireOp",EDGE,"E4.sketch_text.stroke-136"),sQuery(id+"F3.wireOp",EDGE,"E4.sketch_text.stroke-137"),sQuery(id+"F3.wireOp",EDGE,"E4.sketch_text.stroke-138"),sQuery(id+"F3.wireOp",EDGE,"E4.sketch_text.stroke-139"),sQuery(id+"F3.wireOp",EDGE,"E4.sketch_text.stroke-140"),sQuery(id+"F3.wireOp",EDGE,"E4.sketch_text.stroke-141"),sQuery(id+"F3.wireOp",EDGE,"E4.sketch_text.stroke-142"),sQuery(id+"F3.wireOp",EDGE,"E4.sketch_text.stroke-143"),sQuery(id+"F3.wireOp",EDGE,"E4.sketch_text.stroke-144"),sQuery(id+"F3.wireOp",EDGE,"E4.sketch_text.stroke-145"),sQuery(id+"F3.wireOp",EDGE,"E4.sketch_text.stroke-146"),sQuery(id+"F3.wireOp",EDGE,"E4.sketch_text.stroke-147"),sQuery(id+"F3.wireOp",EDGE,"E4.sketch_text.stroke-148"),sQuery(id+"F3.wireOp",EDGE,"E4.sketch_text.stroke-149"),sQuery(id+"F3.wireOp",EDGE,"E4.sketch_text.stroke-150"),sQuery(id+"F3.wireOp",EDGE,"E4.sketch_text.stroke-151"),sQuery(id+"F3.wireOp",EDGE,"E4.sketch_text.stroke-152"),sQuery(id+"F3.wireOp",EDGE,"E4.sketch_text.stroke-153"),sQuery(id+"F3.wireOp",EDGE,"E4.sketch_text.stroke-159"),sQuery(id+"F3.wireOp",EDGE,"E4.sketch_text.stroke-160"),sQuery(id+"F3.wireOp",EDGE,"E4.sketch_text.stroke-161"),sQuery(id+"F3.wireOp",EDGE,"E4.sketch_text.stroke-162"),sQuery(id+"F3.wireOp",EDGE,"E4.sketch_text.stroke-163"),sQuery(id+"F3.wireOp",EDGE,"E4.sketch_text.stroke-164"),sQuery(id+"F3.wireOp",EDGE,"E4.sketch_text.stroke-165"),sQuery(id+"F3.wireOp",EDGE,"E4.sketch_text.stroke-166"),sQuery(id+"F3.wireOp",EDGE,"E4.sketch_text.stroke-167"),sQuery(id+"F3.wireOp",EDGE,"E4.sketch_text.stroke-168"),sQuery(id+"F3.wireOp",EDGE,"E4.sketch_text.stroke-169"),sQuery(id+"F3.wireOp",EDGE,"E4.sketch_text.stroke-170"),sQuery(id+"F3.wireOp",EDGE,"E4.sketch_text.stroke-171"),sQuery(id+"F3.wireOp",EDGE,"E4.sketch_text.stroke-172"),sQuery(id+"F3.wireOp",EDGE,"E4.sketch_text.stroke-173"),sQuery(id+"F3.wireOp",EDGE,"E4.sketch_text.stroke-174"),sQuery(id+"F3.wireOp",EDGE,"E4.sketch_text.stroke-175"),sQuery(id+"F3.wireOp",EDGE,"E4.sketch_text.stroke-176"),sQuery(id+"F3.wireOp",EDGE,"E4.sketch_text.stroke-177"),sQuery(id+"F3.wireOp",EDGE,"E4.sketch_text.stroke-178"),sQuery(id+"F3.wireOp",EDGE,"E4.sketch_text.stroke-179"),sQuery(id+"F3.wireOp",EDGE,"E4.sketch_text.stroke-180"),subQ0,subQ2])],"isStart":true}),makeQuery(id+"F6.opExtrude","SWEPT_FACE",FACE,{"disambiguationData":[OSD([subQ2])]})])],"derivedFrom":makeQuery(id+"F6.opExtrude","CAP_EDGE",EDGE,{"disambiguationData":[OSD([subQ0])],"isStart":true})});}
            var Q4;
            {var subQ0=sQuery(id+"F0.wireOp",EDGE,"E0.top");var subQ1=sQuery(id+"F0.wireOp",EDGE,"E0.bottom");var subQ2=sQuery(id+"F5.wireOp",EDGE,"8007402e-1a4e-4a06-85a5-2af08e553504");Q4=makeQuery(id+"F6.boolean.opBoolean","SPLIT",EDGE,{"disambiguationData":[TD([makeQuery(id+"F1.opExtrude","CAP_FACE",FACE,{"disambiguationData":[OSD([subQ1,subQ0,sQuery(id+"F0.wireOp",EDGE,"E0.left"),sQuery(id+"F0.wireOp",EDGE,"E0.right")])],"isStart":false}),makeQuery(id+"F1.opExtrude","SWEPT_FACE",FACE,{"disambiguationData":[OSD([subQ0])]}),makeQuery(id+"F6.opExtrude","SWEPT_FACE",FACE,{"disambiguationData":[OSD([subQ2])]}),makeQuery(id+"F6.opExtrude","CAP_FACE",FACE,{"disambiguationData":[OSD([subQ1,sQuery(id+"F2.wireOp",EDGE,"E2.sketch_text.stroke-0"),sQuery(id+"F2.wireOp",EDGE,"E2.sketch_text.stroke-1"),sQuery(id+"F2.wireOp",EDGE,"E2.sketch_text.stroke-2"),sQuery(id+"F2.wireOp",EDGE,"E2.sketch_text.stroke-3"),sQuery(id+"F2.wireOp",EDGE,"E2.sketch_text.stroke-4"),sQuery(id+"F2.wireOp",EDGE,"E2.sketch_text.stroke-5"),sQuery(id+"F2.wireOp",EDGE,"E2.sketch_text.stroke-6"),sQuery(id+"F2.wireOp",EDGE,"E2.sketch_text.stroke-7"),sQuery(id+"F2.wireOp",EDGE,"E2.sketch_text.stroke-8"),sQuery(id+"F2.wireOp",EDGE,"E2.sketch_text.stroke-9"),sQuery(id+"F2.wireOp",EDGE,"E2.sketch_text.stroke-10"),sQuery(id+"F2.wireOp",EDGE,"E2.sketch_text.stroke-11"),sQuery(id+"F2.wireOp",EDGE,"E2.sketch_text.stroke-12"),sQuery(id+"F2.wireOp",EDGE,"E2.sketch_text.stroke-13"),sQuery(id+"F2.wireOp",EDGE,"E2.sketch_text.stroke-14"),sQuery(id+"F2.wireOp",EDGE,"E2.sketch_text.stroke-15"),sQuery(id+"F2.wireOp",EDGE,"E2.sketch_text.stroke-16"),sQuery(id+"F2.wireOp",EDGE,"E2.sketch_text.stroke-17"),sQuery(id+"F2.wireOp",EDGE,"E2.sketch_text.stroke-18"),sQuery(id+"F2.wireOp",EDGE,"E2.sketch_text.stroke-19"),sQuery(id+"F2.wireOp",EDGE,"E2.sketch_text.stroke-20"),sQuery(id+"F2.wireOp",EDGE,"E2.sketch_text.stroke-21"),sQuery(id+"F2.wireOp",EDGE,"E2.sketch_text.stroke-22"),sQuery(id+"F2.wireOp",EDGE,"E2.sketch_text.stroke-23"),sQuery(id+"F2.wireOp",EDGE,"E2.sketch_text.stroke-24"),sQuery(id+"F2.wireOp",EDGE,"E2.sketch_text.stroke-25"),sQuery(id+"F2.wireOp",EDGE,"E2.sketch_text.stroke-26"),sQuery(id+"F2.wireOp",EDGE,"E2.sketch_text.stroke-27"),sQuery(id+"F2.wireOp",EDGE,"E2.sketch_text.stroke-28"),sQuery(id+"F2.wireOp",EDGE,"E2.sketch_text.stroke-29"),sQuery(id+"F2.wireOp",EDGE,"E2.sketch_text.stroke-30"),sQuery(id+"F2.wireOp",EDGE,"E2.sketch_text.stroke-31"),sQuery(id+"F2.wireOp",EDGE,"E2.sketch_text.stroke-32"),sQuery(id+"F2.wireOp",EDGE,"E2.sketch_text.stroke-33"),sQuery(id+"F2.wireOp",EDGE,"E2.sketch_text.stroke-34"),sQuery(id+"F2.wireOp",EDGE,"E2.sketch_text.stroke-35"),sQuery(id+"F2.wireOp",EDGE,"E2.sketch_text.stroke-36"),sQuery(id+"F2.wireOp",EDGE,"E2.sketch_text.stroke-37"),sQuery(id+"F2.wireOp",EDGE,"E2.sketch_text.stroke-38"),sQuery(id+"F2.wireOp",EDGE,"E2.sketch_text.stroke-39"),sQuery(id+"F2.wireOp",EDGE,"E2.sketch_text.stroke-40"),sQuery(id+"F2.wireOp",EDGE,"E2.sketch_text.stroke-41"),sQuery(id+"F2.wireOp",EDGE,"E2.sketch_text.stroke-42"),sQuery(id+"F2.wireOp",EDGE,"E2.sketch_text.stroke-43"),sQuery(id+"F2.wireOp",EDGE,"E2.sketch_text.stroke-44"),sQuery(id+"F2.wireOp",EDGE,"E2.sketch_text.stroke-45"),sQuery(id+"F2.wireOp",EDGE,"E2.sketch_text.stroke-46"),sQuery(id+"F2.wireOp",EDGE,"E2.sketch_text.stroke-47"),sQuery(id+"F2.wireOp",EDGE,"E2.sketch_text.stroke-48"),sQuery(id+"F2.wireOp",EDGE,"E2.sketch_text.stroke-49"),sQuery(id+"F2.wireOp",EDGE,"E2.sketch_text.stroke-50"),sQuery(id+"F2.wireOp",EDGE,"E2.sketch_text.stroke-51"),sQuery(id+"F2.wireOp",EDGE,"E2.sketch_text.stroke-52"),sQuery(id+"F2.wireOp",EDGE,"E2.sketch_text.stroke-53"),sQuery(id+"F2.wireOp",EDGE,"E2.sketch_text.stroke-54"),sQuery(id+"F2.wireOp",EDGE,"E2.sketch_text.stroke-55"),sQuery(id+"F2.wireOp",EDGE,"E2.sketch_text.stroke-56"),sQuery(id+"F2.wireOp",EDGE,"E2.sketch_text.stroke-57"),sQuery(id+"F2.wireOp",EDGE,"E2.sketch_text.stroke-58"),sQuery(id+"F2.wireOp",EDGE,"E2.sketch_text.stroke-59"),sQuery(id+"F2.wireOp",EDGE,"E2.sketch_text.stroke-60"),sQuery(id+"F2.wireOp",EDGE,"E2.sketch_text.stroke-61"),sQuery(id+"F2.wireOp",EDGE,"E2.sketch_text.stroke-62"),sQuery(id+"F2.wireOp",EDGE,"E2.sketch_text.stroke-63"),sQuery(id+"F2.wireOp",EDGE,"E2.sketch_text.stroke-64"),sQuery(id+"F2.wireOp",EDGE,"E2.sketch_text.stroke-65"),sQuery(id+"F2.wireOp",EDGE,"E2.sketch_text.stroke-66"),sQuery(id+"F2.wireOp",EDGE,"E2.sketch_text.stroke-67"),sQuery(id+"F2.wireOp",EDGE,"E2.sketch_text.stroke-68"),sQuery(id+"F2.wireOp",EDGE,"E2.sketch_text.stroke-69"),sQuery(id+"F2.wireOp",EDGE,"E2.sketch_text.stroke-70"),sQuery(id+"F2.wireOp",EDGE,"E2.sketch_text.stroke-71"),sQuery(id+"F2.wireOp",EDGE,"E2.sketch_text.stroke-72"),sQuery(id+"F2.wireOp",EDGE,"E2.sketch_text.stroke-73"),sQuery(id+"F2.wireOp",EDGE,"E2.sketch_text.stroke-74"),sQuery(id+"F2.wireOp",EDGE,"E2.sketch_text.stroke-75"),sQuery(id+"F2.wireOp",EDGE,"E2.sketch_text.stroke-76"),sQuery(id+"F2.wireOp",EDGE,"E2.sketch_text.stroke-77"),sQuery(id+"F2.wireOp",EDGE,"E2.sketch_text.stroke-78"),sQuery(id+"F2.wireOp",EDGE,"E2.sketch_text.stroke-79"),sQuery(id+"F2.wireOp",EDGE,"E2.sketch_text.stroke-80"),sQuery(id+"F2.wireOp",EDGE,"E2.sketch_text.stroke-81"),sQuery(id+"F2.wireOp",EDGE,"E2.sketch_text.stroke-82"),sQuery(id+"F2.wireOp",EDGE,"E2.sketch_text.stroke-83"),sQuery(id+"F2.wireOp",EDGE,"E2.sketch_text.stroke-84"),sQuery(id+"F2.wireOp",EDGE,"E2.sketch_text.stroke-85"),sQuery(id+"F2.wireOp",EDGE,"E2.sketch_text.stroke-86"),sQuery(id+"F2.wireOp",EDGE,"E2.sketch_text.stroke-87"),sQuery(id+"F2.wireOp",EDGE,"E2.sketch_text.stroke-88"),sQuery(id+"F2.wireOp",EDGE,"E2.sketch_text.stroke-89"),sQuery(id+"F2.wireOp",EDGE,"E2.sketch_text.stroke-90"),sQuery(id+"F2.wireOp",EDGE,"E2.sketch_text.stroke-91"),sQuery(id+"F2.wireOp",EDGE,"E2.sketch_text.stroke-92"),sQuery(id+"F2.wireOp",EDGE,"E2.sketch_text.stroke-93"),sQuery(id+"F2.wireOp",EDGE,"E2.sketch_text.stroke-94"),sQuery(id+"F2.wireOp",EDGE,"E2.sketch_text.stroke-95"),sQuery(id+"F2.wireOp",EDGE,"E2.sketch_text.stroke-96"),sQuery(id+"F2.wireOp",EDGE,"E2.sketch_text.stroke-97"),sQuery(id+"F2.wireOp",EDGE,"E2.sketch_text.stroke-98"),sQuery(id+"F2.wireOp",EDGE,"E2.sketch_text.stroke-99"),sQuery(id+"F2.wireOp",EDGE,"E2.sketch_text.stroke-100"),sQuery(id+"F2.wireOp",EDGE,"E2.sketch_text.stroke-101"),sQuery(id+"F2.wireOp",EDGE,"E2.sketch_text.stroke-102"),sQuery(id+"F2.wireOp",EDGE,"E2.sketch_text.stroke-103"),sQuery(id+"F2.wireOp",EDGE,"E2.sketch_text.stroke-104"),sQuery(id+"F2.wireOp",EDGE,"E2.sketch_text.stroke-105"),sQuery(id+"F2.wireOp",EDGE,"E2.sketch_text.stroke-106"),sQuery(id+"F2.wireOp",EDGE,"E2.sketch_text.stroke-107"),sQuery(id+"F2.wireOp",EDGE,"E2.sketch_text.stroke-108"),sQuery(id+"F2.wireOp",EDGE,"E2.sketch_text.stroke-109"),sQuery(id+"F2.wireOp",EDGE,"E2.sketch_text.stroke-110"),sQuery(id+"F2.wireOp",EDGE,"E2.sketch_text.stroke-111"),sQuery(id+"F2.wireOp",EDGE,"E2.sketch_text.stroke-112"),sQuery(id+"F2.wireOp",EDGE,"E2.sketch_text.stroke-113"),sQuery(id+"F2.wireOp",EDGE,"E2.sketch_text.stroke-114"),sQuery(id+"F2.wireOp",EDGE,"E2.sketch_text.stroke-115"),sQuery(id+"F2.wireOp",EDGE,"E2.sketch_text.stroke-116"),sQuery(id+"F2.wireOp",EDGE,"E2.sketch_text.stroke-117"),sQuery(id+"F2.wireOp",EDGE,"E2.sketch_text.stroke-118"),sQuery(id+"F2.wireOp",EDGE,"E2.sketch_text.stroke-119"),sQuery(id+"F2.wireOp",EDGE,"E2.sketch_text.stroke-120"),sQuery(id+"F2.wireOp",EDGE,"E2.sketch_text.stroke-121"),sQuery(id+"F2.wireOp",EDGE,"E2.sketch_text.stroke-122"),sQuery(id+"F2.wireOp",EDGE,"E2.sketch_text.stroke-123"),sQuery(id+"F2.wireOp",EDGE,"E2.sketch_text.stroke-124"),sQuery(id+"F2.wireOp",EDGE,"E2.sketch_text.stroke-125"),sQuery(id+"F2.wireOp",EDGE,"E2.sketch_text.stroke-126"),sQuery(id+"F2.wireOp",EDGE,"E2.sketch_text.stroke-127"),sQuery(id+"F2.wireOp",EDGE,"E2.sketch_text.stroke-128"),sQuery(id+"F2.wireOp",EDGE,"E2.sketch_text.stroke-129"),sQuery(id+"F2.wireOp",EDGE,"E2.sketch_text.stroke-130"),sQuery(id+"F2.wireOp",EDGE,"E2.sketch_text.stroke-131"),sQuery(id+"F2.wireOp",EDGE,"E2.sketch_text.stroke-132"),sQuery(id+"F2.wireOp",EDGE,"E2.sketch_text.stroke-133"),sQuery(id+"F2.wireOp",EDGE,"E2.sketch_text.stroke-134"),sQuery(id+"F2.wireOp",EDGE,"E2.sketch_text.stroke-135"),sQuery(id+"F2.wireOp",EDGE,"E2.sketch_text.stroke-136"),sQuery(id+"F2.wireOp",EDGE,"E2.sketch_text.stroke-137"),sQuery(id+"F2.wireOp",EDGE,"E2.sketch_text.stroke-138"),sQuery(id+"F2.wireOp",EDGE,"E2.sketch_text.stroke-139"),sQuery(id+"F2.wireOp",EDGE,"E2.sketch_text.stroke-140"),sQuery(id+"F2.wireOp",EDGE,"E2.sketch_text.stroke-141"),sQuery(id+"F2.wireOp",EDGE,"E2.sketch_text.stroke-142"),sQuery(id+"F2.wireOp",EDGE,"E2.sketch_text.stroke-143"),sQuery(id+"F2.wireOp",EDGE,"E2.sketch_text.stroke-144"),sQuery(id+"F2.wireOp",EDGE,"E2.sketch_text.stroke-145"),sQuery(id+"F2.wireOp",EDGE,"E2.sketch_text.stroke-146"),sQuery(id+"F2.wireOp",EDGE,"E2.sketch_text.stroke-147"),sQuery(id+"F2.wireOp",EDGE,"E2.sketch_text.stroke-148"),sQuery(id+"F2.wireOp",EDGE,"E2.sketch_text.stroke-149"),sQuery(id+"F2.wireOp",EDGE,"E2.sketch_text.stroke-150"),sQuery(id+"F2.wireOp",EDGE,"E2.sketch_text.stroke-151"),sQuery(id+"F2.wireOp",EDGE,"E2.sketch_text.stroke-152"),sQuery(id+"F2.wireOp",EDGE,"E2.sketch_text.stroke-153"),sQuery(id+"F2.wireOp",EDGE,"E2.sketch_text.stroke-154"),sQuery(id+"F2.wireOp",EDGE,"E2.sketch_text.stroke-155"),sQuery(id+"F2.wireOp",EDGE,"E2.sketch_text.stroke-156"),sQuery(id+"F2.wireOp",EDGE,"E2.sketch_text.stroke-157"),sQuery(id+"F2.wireOp",EDGE,"E2.sketch_text.stroke-158"),sQuery(id+"F2.wireOp",EDGE,"E2.sketch_text.stroke-159"),sQuery(id+"F2.wireOp",EDGE,"E2.sketch_text.stroke-160"),sQuery(id+"F2.wireOp",EDGE,"E2.sketch_text.stroke-161"),sQuery(id+"F2.wireOp",EDGE,"E2.sketch_text.stroke-162"),sQuery(id+"F2.wireOp",EDGE,"E2.sketch_text.stroke-163"),sQuery(id+"F2.wireOp",EDGE,"E2.sketch_text.stroke-164"),sQuery(id+"F2.wireOp",EDGE,"E2.sketch_text.stroke-165"),sQuery(id+"F2.wireOp",EDGE,"E2.sketch_text.stroke-166"),sQuery(id+"F2.wireOp",EDGE,"E2.sketch_text.stroke-167"),sQuery(id+"F2.wireOp",EDGE,"E2.sketch_text.stroke-168"),sQuery(id+"F2.wireOp",EDGE,"E2.sketch_text.stroke-169"),sQuery(id+"F2.wireOp",EDGE,"E2.sketch_text.stroke-170"),sQuery(id+"F2.wireOp",EDGE,"E2.sketch_text.stroke-171"),sQuery(id+"F2.wireOp",EDGE,"E2.sketch_text.stroke-172"),sQuery(id+"F2.wireOp",EDGE,"E2.sketch_text.stroke-173"),sQuery(id+"F3.wireOp",EDGE,"E4.sketch_text.stroke-0"),sQuery(id+"F3.wireOp",EDGE,"E4.sketch_text.stroke-1"),sQuery(id+"F3.wireOp",EDGE,"E4.sketch_text.stroke-2"),sQuery(id+"F3.wireOp",EDGE,"E4.sketch_text.stroke-3"),sQuery(id+"F3.wireOp",EDGE,"E4.sketch_text.stroke-4"),sQuery(id+"F3.wireOp",EDGE,"E4.sketch_text.stroke-5"),sQuery(id+"F3.wireOp",EDGE,"E4.sketch_text.stroke-6"),sQuery(id+"F3.wireOp",EDGE,"E4.sketch_text.stroke-7"),sQuery(id+"F3.wireOp",EDGE,"E4.sketch_text.stroke-8"),sQuery(id+"F3.wireOp",EDGE,"E4.sketch_text.stroke-9"),sQuery(id+"F3.wireOp",EDGE,"E4.sketch_text.stroke-10"),sQuery(id+"F3.wireOp",EDGE,"E4.sketch_text.stroke-11"),sQuery(id+"F3.wireOp",EDGE,"E4.sketch_text.stroke-12"),sQuery(id+"F3.wireOp",EDGE,"E4.sketch_text.stroke-13"),sQuery(id+"F3.wireOp",EDGE,"E4.sketch_text.stroke-14"),sQuery(id+"F3.wireOp",EDGE,"E4.sketch_text.stroke-15"),sQuery(id+"F3.wireOp",EDGE,"E4.sketch_text.stroke-16"),sQuery(id+"F3.wireOp",EDGE,"E4.sketch_text.stroke-17"),sQuery(id+"F3.wireOp",EDGE,"E4.sketch_text.stroke-18"),sQuery(id+"F3.wireOp",EDGE,"E4.sketch_text.stroke-19"),sQuery(id+"F3.wireOp",EDGE,"E4.sketch_text.stroke-20"),sQuery(id+"F3.wireOp",EDGE,"E4.sketch_text.stroke-21"),sQuery(id+"F3.wireOp",EDGE,"E4.sketch_text.stroke-22"),sQuery(id+"F3.wireOp",EDGE,"E4.sketch_text.stroke-23"),sQuery(id+"F3.wireOp",EDGE,"E4.sketch_text.stroke-24"),sQuery(id+"F3.wireOp",EDGE,"E4.sketch_text.stroke-25"),sQuery(id+"F3.wireOp",EDGE,"E4.sketch_text.stroke-26"),sQuery(id+"F3.wireOp",EDGE,"E4.sketch_text.stroke-27"),sQuery(id+"F3.wireOp",EDGE,"E4.sketch_text.stroke-28"),sQuery(id+"F3.wireOp",EDGE,"E4.sketch_text.stroke-29"),sQuery(id+"F3.wireOp",EDGE,"E4.sketch_text.stroke-30"),sQuery(id+"F3.wireOp",EDGE,"E4.sketch_text.stroke-31"),sQuery(id+"F3.wireOp",EDGE,"E4.sketch_text.stroke-32"),sQuery(id+"F3.wireOp",EDGE,"E4.sketch_text.stroke-33"),sQuery(id+"F3.wireOp",EDGE,"E4.sketch_text.stroke-34"),sQuery(id+"F3.wireOp",EDGE,"E4.sketch_text.stroke-35"),sQuery(id+"F3.wireOp",EDGE,"E4.sketch_text.stroke-36"),sQuery(id+"F3.wireOp",EDGE,"E4.sketch_text.stroke-37"),sQuery(id+"F3.wireOp",EDGE,"E4.sketch_text.stroke-38"),sQuery(id+"F3.wireOp",EDGE,"E4.sketch_text.stroke-39"),sQuery(id+"F3.wireOp",EDGE,"E4.sketch_text.stroke-40"),sQuery(id+"F3.wireOp",EDGE,"E4.sketch_text.stroke-41"),sQuery(id+"F3.wireOp",EDGE,"E4.sketch_text.stroke-42"),sQuery(id+"F3.wireOp",EDGE,"E4.sketch_text.stroke-43"),sQuery(id+"F3.wireOp",EDGE,"E4.sketch_text.stroke-44"),sQuery(id+"F3.wireOp",EDGE,"E4.sketch_text.stroke-45"),sQuery(id+"F3.wireOp",EDGE,"E4.sketch_text.stroke-46"),sQuery(id+"F3.wireOp",EDGE,"E4.sketch_text.stroke-47"),sQuery(id+"F3.wireOp",EDGE,"E4.sketch_text.stroke-48"),sQuery(id+"F3.wireOp",EDGE,"E4.sketch_text.stroke-49"),sQuery(id+"F3.wireOp",EDGE,"E4.sketch_text.stroke-50"),sQuery(id+"F3.wireOp",EDGE,"E4.sketch_text.stroke-51"),sQuery(id+"F3.wireOp",EDGE,"E4.sketch_text.stroke-52"),sQuery(id+"F3.wireOp",EDGE,"E4.sketch_text.stroke-53"),sQuery(id+"F3.wireOp",EDGE,"E4.sketch_text.stroke-54"),sQuery(id+"F3.wireOp",EDGE,"E4.sketch_text.stroke-55"),sQuery(id+"F3.wireOp",EDGE,"E4.sketch_text.stroke-56"),sQuery(id+"F3.wireOp",EDGE,"E4.sketch_text.stroke-57"),sQuery(id+"F3.wireOp",EDGE,"E4.sketch_text.stroke-58"),sQuery(id+"F3.wireOp",EDGE,"E4.sketch_text.stroke-59"),sQuery(id+"F3.wireOp",EDGE,"E4.sketch_text.stroke-60"),sQuery(id+"F3.wireOp",EDGE,"E4.sketch_text.stroke-61"),sQuery(id+"F3.wireOp",EDGE,"E4.sketch_text.stroke-62"),sQuery(id+"F3.wireOp",EDGE,"E4.sketch_text.stroke-71"),sQuery(id+"F3.wireOp",EDGE,"E4.sketch_text.stroke-72"),sQuery(id+"F3.wireOp",EDGE,"E4.sketch_text.stroke-73"),sQuery(id+"F3.wireOp",EDGE,"E4.sketch_text.stroke-74"),sQuery(id+"F3.wireOp",EDGE,"E4.sketch_text.stroke-75"),sQuery(id+"F3.wireOp",EDGE,"E4.sketch_text.stroke-76"),sQuery(id+"F3.wireOp",EDGE,"E4.sketch_text.stroke-77"),sQuery(id+"F3.wireOp",EDGE,"E4.sketch_text.stroke-78"),sQuery(id+"F3.wireOp",EDGE,"E4.sketch_text.stroke-79"),sQuery(id+"F3.wireOp",EDGE,"E4.sketch_text.stroke-80"),sQuery(id+"F3.wireOp",EDGE,"E4.sketch_text.stroke-81"),sQuery(id+"F3.wireOp",EDGE,"E4.sketch_text.stroke-82"),sQuery(id+"F3.wireOp",EDGE,"E4.sketch_text.stroke-83"),sQuery(id+"F3.wireOp",EDGE,"E4.sketch_text.stroke-84"),sQuery(id+"F3.wireOp",EDGE,"E4.sketch_text.stroke-85"),sQuery(id+"F3.wireOp",EDGE,"E4.sketch_text.stroke-86"),sQuery(id+"F3.wireOp",EDGE,"E4.sketch_text.stroke-87"),sQuery(id+"F3.wireOp",EDGE,"E4.sketch_text.stroke-88"),sQuery(id+"F3.wireOp",EDGE,"E4.sketch_text.stroke-89"),sQuery(id+"F3.wireOp",EDGE,"E4.sketch_text.stroke-90"),sQuery(id+"F3.wireOp",EDGE,"E4.sketch_text.stroke-91"),sQuery(id+"F3.wireOp",EDGE,"E4.sketch_text.stroke-92"),sQuery(id+"F3.wireOp",EDGE,"E4.sketch_text.stroke-93"),sQuery(id+"F3.wireOp",EDGE,"E4.sketch_text.stroke-94"),sQuery(id+"F3.wireOp",EDGE,"E4.sketch_text.stroke-95"),sQuery(id+"F3.wireOp",EDGE,"E4.sketch_text.stroke-96"),sQuery(id+"F3.wireOp",EDGE,"E4.sketch_text.stroke-97"),sQuery(id+"F3.wireOp",EDGE,"E4.sketch_text.stroke-103"),sQuery(id+"F3.wireOp",EDGE,"E4.sketch_text.stroke-104"),sQuery(id+"F3.wireOp",EDGE,"E4.sketch_text.stroke-105"),sQuery(id+"F3.wireOp",EDGE,"E4.sketch_text.stroke-106"),sQuery(id+"F3.wireOp",EDGE,"E4.sketch_text.stroke-107"),sQuery(id+"F3.wireOp",EDGE,"E4.sketch_text.stroke-108"),sQuery(id+"F3.wireOp",EDGE,"E4.sketch_text.stroke-109"),sQuery(id+"F3.wireOp",EDGE,"E4.sketch_text.stroke-110"),sQuery(id+"F3.wireOp",EDGE,"E4.sketch_text.stroke-111"),sQuery(id+"F3.wireOp",EDGE,"E4.sketch_text.stroke-112"),sQuery(id+"F3.wireOp",EDGE,"E4.sketch_text.stroke-113"),sQuery(id+"F3.wireOp",EDGE,"E4.sketch_text.stroke-114"),sQuery(id+"F3.wireOp",EDGE,"E4.sketch_text.stroke-115"),sQuery(id+"F3.wireOp",EDGE,"E4.sketch_text.stroke-116"),sQuery(id+"F3.wireOp",EDGE,"E4.sketch_text.stroke-117"),sQuery(id+"F3.wireOp",EDGE,"E4.sketch_text.stroke-118"),sQuery(id+"F3.wireOp",EDGE,"E4.sketch_text.stroke-119"),sQuery(id+"F3.wireOp",EDGE,"E4.sketch_text.stroke-120"),sQuery(id+"F3.wireOp",EDGE,"E4.sketch_text.stroke-121"),sQuery(id+"F3.wireOp",EDGE,"E4.sketch_text.stroke-122"),sQuery(id+"F3.wireOp",EDGE,"E4.sketch_text.stroke-123"),sQuery(id+"F3.wireOp",EDGE,"E4.sketch_text.stroke-124"),sQuery(id+"F3.wireOp",EDGE,"E4.sketch_text.stroke-125"),sQuery(id+"F3.wireOp",EDGE,"E4.sketch_text.stroke-126"),sQuery(id+"F3.wireOp",EDGE,"E4.sketch_text.stroke-127"),sQuery(id+"F3.wireOp",EDGE,"E4.sketch_text.stroke-128"),sQuery(id+"F3.wireOp",EDGE,"E4.sketch_text.stroke-129"),sQuery(id+"F3.wireOp",EDGE,"E4.sketch_text.stroke-130"),sQuery(id+"F3.wireOp",EDGE,"E4.sketch_text.stroke-131"),sQuery(id+"F3.wireOp",EDGE,"E4.sketch_text.stroke-132"),sQuery(id+"F3.wireOp",EDGE,"E4.sketch_text.stroke-133"),sQuery(id+"F3.wireOp",EDGE,"E4.sketch_text.stroke-134"),sQuery(id+"F3.wireOp",EDGE,"E4.sketch_text.stroke-135"),sQuery(id+"F3.wireOp",EDGE,"E4.sketch_text.stroke-136"),sQuery(id+"F3.wireOp",EDGE,"E4.sketch_text.stroke-137"),sQuery(id+"F3.wireOp",EDGE,"E4.sketch_text.stroke-138"),sQuery(id+"F3.wireOp",EDGE,"E4.sketch_text.stroke-139"),sQuery(id+"F3.wireOp",EDGE,"E4.sketch_text.stroke-140"),sQuery(id+"F3.wireOp",EDGE,"E4.sketch_text.stroke-141"),sQuery(id+"F3.wireOp",EDGE,"E4.sketch_text.stroke-142"),sQuery(id+"F3.wireOp",EDGE,"E4.sketch_text.stroke-143"),sQuery(id+"F3.wireOp",EDGE,"E4.sketch_text.stroke-144"),sQuery(id+"F3.wireOp",EDGE,"E4.sketch_text.stroke-145"),sQuery(id+"F3.wireOp",EDGE,"E4.sketch_text.stroke-146"),sQuery(id+"F3.wireOp",EDGE,"E4.sketch_text.stroke-147"),sQuery(id+"F3.wireOp",EDGE,"E4.sketch_text.stroke-148"),sQuery(id+"F3.wireOp",EDGE,"E4.sketch_text.stroke-149"),sQuery(id+"F3.wireOp",EDGE,"E4.sketch_text.stroke-150"),sQuery(id+"F3.wireOp",EDGE,"E4.sketch_text.stroke-151"),sQuery(id+"F3.wireOp",EDGE,"E4.sketch_text.stroke-152"),sQuery(id+"F3.wireOp",EDGE,"E4.sketch_text.stroke-153"),sQuery(id+"F3.wireOp",EDGE,"E4.sketch_text.stroke-159"),sQuery(id+"F3.wireOp",EDGE,"E4.sketch_text.stroke-160"),sQuery(id+"F3.wireOp",EDGE,"E4.sketch_text.stroke-161"),sQuery(id+"F3.wireOp",EDGE,"E4.sketch_text.stroke-162"),sQuery(id+"F3.wireOp",EDGE,"E4.sketch_text.stroke-163"),sQuery(id+"F3.wireOp",EDGE,"E4.sketch_text.stroke-164"),sQuery(id+"F3.wireOp",EDGE,"E4.sketch_text.stroke-165"),sQuery(id+"F3.wireOp",EDGE,"E4.sketch_text.stroke-166"),sQuery(id+"F3.wireOp",EDGE,"E4.sketch_text.stroke-167"),sQuery(id+"F3.wireOp",EDGE,"E4.sketch_text.stroke-168"),sQuery(id+"F3.wireOp",EDGE,"E4.sketch_text.stroke-169"),sQuery(id+"F3.wireOp",EDGE,"E4.sketch_text.stroke-170"),sQuery(id+"F3.wireOp",EDGE,"E4.sketch_text.stroke-171"),sQuery(id+"F3.wireOp",EDGE,"E4.sketch_text.stroke-172"),sQuery(id+"F3.wireOp",EDGE,"E4.sketch_text.stroke-173"),sQuery(id+"F3.wireOp",EDGE,"E4.sketch_text.stroke-174"),sQuery(id+"F3.wireOp",EDGE,"E4.sketch_text.stroke-175"),sQuery(id+"F3.wireOp",EDGE,"E4.sketch_text.stroke-176"),sQuery(id+"F3.wireOp",EDGE,"E4.sketch_text.stroke-177"),sQuery(id+"F3.wireOp",EDGE,"E4.sketch_text.stroke-178"),sQuery(id+"F3.wireOp",EDGE,"E4.sketch_text.stroke-179"),sQuery(id+"F3.wireOp",EDGE,"E4.sketch_text.stroke-180"),subQ2,sQuery(id+"F5.wireOp",EDGE,"6ee83ff3-586e-4dbe-aaea-af71240543bd")])],"isStart":true})]),OD(1.0)],"derivedFrom":makeQuery(id+"F1.opExtrude","CAP_EDGE",EDGE,{"disambiguationData":[OSD([subQ0])],"isStart":false})});}
            var Q5;
            {var subQ0=sQuery(id+"F0.wireOp",EDGE,"E0.top");var subQ1=sQuery(id+"F0.wireOp",EDGE,"E0.bottom");var subQ2=sQuery(id+"F5.wireOp",EDGE,"8007402e-1a4e-4a06-85a5-2af08e553504");Q5=makeQuery(id+"F6.boolean.opBoolean","SPLIT",EDGE,{"disambiguationData":[TD([makeQuery(id+"F1.opExtrude","CAP_FACE",FACE,{"disambiguationData":[OSD([subQ1,subQ0,sQuery(id+"F0.wireOp",EDGE,"E0.left"),sQuery(id+"F0.wireOp",EDGE,"E0.right")])],"isStart":false}),makeQuery(id+"F1.opExtrude","SWEPT_FACE",FACE,{"disambiguationData":[OSD([subQ0])]}),makeQuery(id+"F6.opExtrude","SWEPT_FACE",FACE,{"disambiguationData":[OSD([subQ2])]}),makeQuery(id+"F6.opExtrude","CAP_FACE",FACE,{"disambiguationData":[OSD([subQ1,sQuery(id+"F2.wireOp",EDGE,"E2.sketch_text.stroke-0"),sQuery(id+"F2.wireOp",EDGE,"E2.sketch_text.stroke-1"),sQuery(id+"F2.wireOp",EDGE,"E2.sketch_text.stroke-2"),sQuery(id+"F2.wireOp",EDGE,"E2.sketch_text.stroke-3"),sQuery(id+"F2.wireOp",EDGE,"E2.sketch_text.stroke-4"),sQuery(id+"F2.wireOp",EDGE,"E2.sketch_text.stroke-5"),sQuery(id+"F2.wireOp",EDGE,"E2.sketch_text.stroke-6"),sQuery(id+"F2.wireOp",EDGE,"E2.sketch_text.stroke-7"),sQuery(id+"F2.wireOp",EDGE,"E2.sketch_text.stroke-8"),sQuery(id+"F2.wireOp",EDGE,"E2.sketch_text.stroke-9"),sQuery(id+"F2.wireOp",EDGE,"E2.sketch_text.stroke-10"),sQuery(id+"F2.wireOp",EDGE,"E2.sketch_text.stroke-11"),sQuery(id+"F2.wireOp",EDGE,"E2.sketch_text.stroke-12"),sQuery(id+"F2.wireOp",EDGE,"E2.sketch_text.stroke-13"),sQuery(id+"F2.wireOp",EDGE,"E2.sketch_text.stroke-14"),sQuery(id+"F2.wireOp",EDGE,"E2.sketch_text.stroke-15"),sQuery(id+"F2.wireOp",EDGE,"E2.sketch_text.stroke-16"),sQuery(id+"F2.wireOp",EDGE,"E2.sketch_text.stroke-17"),sQuery(id+"F2.wireOp",EDGE,"E2.sketch_text.stroke-18"),sQuery(id+"F2.wireOp",EDGE,"E2.sketch_text.stroke-19"),sQuery(id+"F2.wireOp",EDGE,"E2.sketch_text.stroke-20"),sQuery(id+"F2.wireOp",EDGE,"E2.sketch_text.stroke-21"),sQuery(id+"F2.wireOp",EDGE,"E2.sketch_text.stroke-22"),sQuery(id+"F2.wireOp",EDGE,"E2.sketch_text.stroke-23"),sQuery(id+"F2.wireOp",EDGE,"E2.sketch_text.stroke-24"),sQuery(id+"F2.wireOp",EDGE,"E2.sketch_text.stroke-25"),sQuery(id+"F2.wireOp",EDGE,"E2.sketch_text.stroke-26"),sQuery(id+"F2.wireOp",EDGE,"E2.sketch_text.stroke-27"),sQuery(id+"F2.wireOp",EDGE,"E2.sketch_text.stroke-28"),sQuery(id+"F2.wireOp",EDGE,"E2.sketch_text.stroke-29"),sQuery(id+"F2.wireOp",EDGE,"E2.sketch_text.stroke-30"),sQuery(id+"F2.wireOp",EDGE,"E2.sketch_text.stroke-31"),sQuery(id+"F2.wireOp",EDGE,"E2.sketch_text.stroke-32"),sQuery(id+"F2.wireOp",EDGE,"E2.sketch_text.stroke-33"),sQuery(id+"F2.wireOp",EDGE,"E2.sketch_text.stroke-34"),sQuery(id+"F2.wireOp",EDGE,"E2.sketch_text.stroke-35"),sQuery(id+"F2.wireOp",EDGE,"E2.sketch_text.stroke-36"),sQuery(id+"F2.wireOp",EDGE,"E2.sketch_text.stroke-37"),sQuery(id+"F2.wireOp",EDGE,"E2.sketch_text.stroke-38"),sQuery(id+"F2.wireOp",EDGE,"E2.sketch_text.stroke-39"),sQuery(id+"F2.wireOp",EDGE,"E2.sketch_text.stroke-40"),sQuery(id+"F2.wireOp",EDGE,"E2.sketch_text.stroke-41"),sQuery(id+"F2.wireOp",EDGE,"E2.sketch_text.stroke-42"),sQuery(id+"F2.wireOp",EDGE,"E2.sketch_text.stroke-43"),sQuery(id+"F2.wireOp",EDGE,"E2.sketch_text.stroke-44"),sQuery(id+"F2.wireOp",EDGE,"E2.sketch_text.stroke-45"),sQuery(id+"F2.wireOp",EDGE,"E2.sketch_text.stroke-46"),sQuery(id+"F2.wireOp",EDGE,"E2.sketch_text.stroke-47"),sQuery(id+"F2.wireOp",EDGE,"E2.sketch_text.stroke-48"),sQuery(id+"F2.wireOp",EDGE,"E2.sketch_text.stroke-49"),sQuery(id+"F2.wireOp",EDGE,"E2.sketch_text.stroke-50"),sQuery(id+"F2.wireOp",EDGE,"E2.sketch_text.stroke-51"),sQuery(id+"F2.wireOp",EDGE,"E2.sketch_text.stroke-52"),sQuery(id+"F2.wireOp",EDGE,"E2.sketch_text.stroke-53"),sQuery(id+"F2.wireOp",EDGE,"E2.sketch_text.stroke-54"),sQuery(id+"F2.wireOp",EDGE,"E2.sketch_text.stroke-55"),sQuery(id+"F2.wireOp",EDGE,"E2.sketch_text.stroke-56"),sQuery(id+"F2.wireOp",EDGE,"E2.sketch_text.stroke-57"),sQuery(id+"F2.wireOp",EDGE,"E2.sketch_text.stroke-58"),sQuery(id+"F2.wireOp",EDGE,"E2.sketch_text.stroke-59"),sQuery(id+"F2.wireOp",EDGE,"E2.sketch_text.stroke-60"),sQuery(id+"F2.wireOp",EDGE,"E2.sketch_text.stroke-61"),sQuery(id+"F2.wireOp",EDGE,"E2.sketch_text.stroke-62"),sQuery(id+"F2.wireOp",EDGE,"E2.sketch_text.stroke-63"),sQuery(id+"F2.wireOp",EDGE,"E2.sketch_text.stroke-64"),sQuery(id+"F2.wireOp",EDGE,"E2.sketch_text.stroke-65"),sQuery(id+"F2.wireOp",EDGE,"E2.sketch_text.stroke-66"),sQuery(id+"F2.wireOp",EDGE,"E2.sketch_text.stroke-67"),sQuery(id+"F2.wireOp",EDGE,"E2.sketch_text.stroke-68"),sQuery(id+"F2.wireOp",EDGE,"E2.sketch_text.stroke-69"),sQuery(id+"F2.wireOp",EDGE,"E2.sketch_text.stroke-70"),sQuery(id+"F2.wireOp",EDGE,"E2.sketch_text.stroke-71"),sQuery(id+"F2.wireOp",EDGE,"E2.sketch_text.stroke-72"),sQuery(id+"F2.wireOp",EDGE,"E2.sketch_text.stroke-73"),sQuery(id+"F2.wireOp",EDGE,"E2.sketch_text.stroke-74"),sQuery(id+"F2.wireOp",EDGE,"E2.sketch_text.stroke-75"),sQuery(id+"F2.wireOp",EDGE,"E2.sketch_text.stroke-76"),sQuery(id+"F2.wireOp",EDGE,"E2.sketch_text.stroke-77"),sQuery(id+"F2.wireOp",EDGE,"E2.sketch_text.stroke-78"),sQuery(id+"F2.wireOp",EDGE,"E2.sketch_text.stroke-79"),sQuery(id+"F2.wireOp",EDGE,"E2.sketch_text.stroke-80"),sQuery(id+"F2.wireOp",EDGE,"E2.sketch_text.stroke-81"),sQuery(id+"F2.wireOp",EDGE,"E2.sketch_text.stroke-82"),sQuery(id+"F2.wireOp",EDGE,"E2.sketch_text.stroke-83"),sQuery(id+"F2.wireOp",EDGE,"E2.sketch_text.stroke-84"),sQuery(id+"F2.wireOp",EDGE,"E2.sketch_text.stroke-85"),sQuery(id+"F2.wireOp",EDGE,"E2.sketch_text.stroke-86"),sQuery(id+"F2.wireOp",EDGE,"E2.sketch_text.stroke-87"),sQuery(id+"F2.wireOp",EDGE,"E2.sketch_text.stroke-88"),sQuery(id+"F2.wireOp",EDGE,"E2.sketch_text.stroke-89"),sQuery(id+"F2.wireOp",EDGE,"E2.sketch_text.stroke-90"),sQuery(id+"F2.wireOp",EDGE,"E2.sketch_text.stroke-91"),sQuery(id+"F2.wireOp",EDGE,"E2.sketch_text.stroke-92"),sQuery(id+"F2.wireOp",EDGE,"E2.sketch_text.stroke-93"),sQuery(id+"F2.wireOp",EDGE,"E2.sketch_text.stroke-94"),sQuery(id+"F2.wireOp",EDGE,"E2.sketch_text.stroke-95"),sQuery(id+"F2.wireOp",EDGE,"E2.sketch_text.stroke-96"),sQuery(id+"F2.wireOp",EDGE,"E2.sketch_text.stroke-97"),sQuery(id+"F2.wireOp",EDGE,"E2.sketch_text.stroke-98"),sQuery(id+"F2.wireOp",EDGE,"E2.sketch_text.stroke-99"),sQuery(id+"F2.wireOp",EDGE,"E2.sketch_text.stroke-100"),sQuery(id+"F2.wireOp",EDGE,"E2.sketch_text.stroke-101"),sQuery(id+"F2.wireOp",EDGE,"E2.sketch_text.stroke-102"),sQuery(id+"F2.wireOp",EDGE,"E2.sketch_text.stroke-103"),sQuery(id+"F2.wireOp",EDGE,"E2.sketch_text.stroke-104"),sQuery(id+"F2.wireOp",EDGE,"E2.sketch_text.stroke-105"),sQuery(id+"F2.wireOp",EDGE,"E2.sketch_text.stroke-106"),sQuery(id+"F2.wireOp",EDGE,"E2.sketch_text.stroke-107"),sQuery(id+"F2.wireOp",EDGE,"E2.sketch_text.stroke-108"),sQuery(id+"F2.wireOp",EDGE,"E2.sketch_text.stroke-109"),sQuery(id+"F2.wireOp",EDGE,"E2.sketch_text.stroke-110"),sQuery(id+"F2.wireOp",EDGE,"E2.sketch_text.stroke-111"),sQuery(id+"F2.wireOp",EDGE,"E2.sketch_text.stroke-112"),sQuery(id+"F2.wireOp",EDGE,"E2.sketch_text.stroke-113"),sQuery(id+"F2.wireOp",EDGE,"E2.sketch_text.stroke-114"),sQuery(id+"F2.wireOp",EDGE,"E2.sketch_text.stroke-115"),sQuery(id+"F2.wireOp",EDGE,"E2.sketch_text.stroke-116"),sQuery(id+"F2.wireOp",EDGE,"E2.sketch_text.stroke-117"),sQuery(id+"F2.wireOp",EDGE,"E2.sketch_text.stroke-118"),sQuery(id+"F2.wireOp",EDGE,"E2.sketch_text.stroke-119"),sQuery(id+"F2.wireOp",EDGE,"E2.sketch_text.stroke-120"),sQuery(id+"F2.wireOp",EDGE,"E2.sketch_text.stroke-121"),sQuery(id+"F2.wireOp",EDGE,"E2.sketch_text.stroke-122"),sQuery(id+"F2.wireOp",EDGE,"E2.sketch_text.stroke-123"),sQuery(id+"F2.wireOp",EDGE,"E2.sketch_text.stroke-124"),sQuery(id+"F2.wireOp",EDGE,"E2.sketch_text.stroke-125"),sQuery(id+"F2.wireOp",EDGE,"E2.sketch_text.stroke-126"),sQuery(id+"F2.wireOp",EDGE,"E2.sketch_text.stroke-127"),sQuery(id+"F2.wireOp",EDGE,"E2.sketch_text.stroke-128"),sQuery(id+"F2.wireOp",EDGE,"E2.sketch_text.stroke-129"),sQuery(id+"F2.wireOp",EDGE,"E2.sketch_text.stroke-130"),sQuery(id+"F2.wireOp",EDGE,"E2.sketch_text.stroke-131"),sQuery(id+"F2.wireOp",EDGE,"E2.sketch_text.stroke-132"),sQuery(id+"F2.wireOp",EDGE,"E2.sketch_text.stroke-133"),sQuery(id+"F2.wireOp",EDGE,"E2.sketch_text.stroke-134"),sQuery(id+"F2.wireOp",EDGE,"E2.sketch_text.stroke-135"),sQuery(id+"F2.wireOp",EDGE,"E2.sketch_text.stroke-136"),sQuery(id+"F2.wireOp",EDGE,"E2.sketch_text.stroke-137"),sQuery(id+"F2.wireOp",EDGE,"E2.sketch_text.stroke-138"),sQuery(id+"F2.wireOp",EDGE,"E2.sketch_text.stroke-139"),sQuery(id+"F2.wireOp",EDGE,"E2.sketch_text.stroke-140"),sQuery(id+"F2.wireOp",EDGE,"E2.sketch_text.stroke-141"),sQuery(id+"F2.wireOp",EDGE,"E2.sketch_text.stroke-142"),sQuery(id+"F2.wireOp",EDGE,"E2.sketch_text.stroke-143"),sQuery(id+"F2.wireOp",EDGE,"E2.sketch_text.stroke-144"),sQuery(id+"F2.wireOp",EDGE,"E2.sketch_text.stroke-145"),sQuery(id+"F2.wireOp",EDGE,"E2.sketch_text.stroke-146"),sQuery(id+"F2.wireOp",EDGE,"E2.sketch_text.stroke-147"),sQuery(id+"F2.wireOp",EDGE,"E2.sketch_text.stroke-148"),sQuery(id+"F2.wireOp",EDGE,"E2.sketch_text.stroke-149"),sQuery(id+"F2.wireOp",EDGE,"E2.sketch_text.stroke-150"),sQuery(id+"F2.wireOp",EDGE,"E2.sketch_text.stroke-151"),sQuery(id+"F2.wireOp",EDGE,"E2.sketch_text.stroke-152"),sQuery(id+"F2.wireOp",EDGE,"E2.sketch_text.stroke-153"),sQuery(id+"F2.wireOp",EDGE,"E2.sketch_text.stroke-154"),sQuery(id+"F2.wireOp",EDGE,"E2.sketch_text.stroke-155"),sQuery(id+"F2.wireOp",EDGE,"E2.sketch_text.stroke-156"),sQuery(id+"F2.wireOp",EDGE,"E2.sketch_text.stroke-157"),sQuery(id+"F2.wireOp",EDGE,"E2.sketch_text.stroke-158"),sQuery(id+"F2.wireOp",EDGE,"E2.sketch_text.stroke-159"),sQuery(id+"F2.wireOp",EDGE,"E2.sketch_text.stroke-160"),sQuery(id+"F2.wireOp",EDGE,"E2.sketch_text.stroke-161"),sQuery(id+"F2.wireOp",EDGE,"E2.sketch_text.stroke-162"),sQuery(id+"F2.wireOp",EDGE,"E2.sketch_text.stroke-163"),sQuery(id+"F2.wireOp",EDGE,"E2.sketch_text.stroke-164"),sQuery(id+"F2.wireOp",EDGE,"E2.sketch_text.stroke-165"),sQuery(id+"F2.wireOp",EDGE,"E2.sketch_text.stroke-166"),sQuery(id+"F2.wireOp",EDGE,"E2.sketch_text.stroke-167"),sQuery(id+"F2.wireOp",EDGE,"E2.sketch_text.stroke-168"),sQuery(id+"F2.wireOp",EDGE,"E2.sketch_text.stroke-169"),sQuery(id+"F2.wireOp",EDGE,"E2.sketch_text.stroke-170"),sQuery(id+"F2.wireOp",EDGE,"E2.sketch_text.stroke-171"),sQuery(id+"F2.wireOp",EDGE,"E2.sketch_text.stroke-172"),sQuery(id+"F2.wireOp",EDGE,"E2.sketch_text.stroke-173"),sQuery(id+"F3.wireOp",EDGE,"E4.sketch_text.stroke-0"),sQuery(id+"F3.wireOp",EDGE,"E4.sketch_text.stroke-1"),sQuery(id+"F3.wireOp",EDGE,"E4.sketch_text.stroke-2"),sQuery(id+"F3.wireOp",EDGE,"E4.sketch_text.stroke-3"),sQuery(id+"F3.wireOp",EDGE,"E4.sketch_text.stroke-4"),sQuery(id+"F3.wireOp",EDGE,"E4.sketch_text.stroke-5"),sQuery(id+"F3.wireOp",EDGE,"E4.sketch_text.stroke-6"),sQuery(id+"F3.wireOp",EDGE,"E4.sketch_text.stroke-7"),sQuery(id+"F3.wireOp",EDGE,"E4.sketch_text.stroke-8"),sQuery(id+"F3.wireOp",EDGE,"E4.sketch_text.stroke-9"),sQuery(id+"F3.wireOp",EDGE,"E4.sketch_text.stroke-10"),sQuery(id+"F3.wireOp",EDGE,"E4.sketch_text.stroke-11"),sQuery(id+"F3.wireOp",EDGE,"E4.sketch_text.stroke-12"),sQuery(id+"F3.wireOp",EDGE,"E4.sketch_text.stroke-13"),sQuery(id+"F3.wireOp",EDGE,"E4.sketch_text.stroke-14"),sQuery(id+"F3.wireOp",EDGE,"E4.sketch_text.stroke-15"),sQuery(id+"F3.wireOp",EDGE,"E4.sketch_text.stroke-16"),sQuery(id+"F3.wireOp",EDGE,"E4.sketch_text.stroke-17"),sQuery(id+"F3.wireOp",EDGE,"E4.sketch_text.stroke-18"),sQuery(id+"F3.wireOp",EDGE,"E4.sketch_text.stroke-19"),sQuery(id+"F3.wireOp",EDGE,"E4.sketch_text.stroke-20"),sQuery(id+"F3.wireOp",EDGE,"E4.sketch_text.stroke-21"),sQuery(id+"F3.wireOp",EDGE,"E4.sketch_text.stroke-22"),sQuery(id+"F3.wireOp",EDGE,"E4.sketch_text.stroke-23"),sQuery(id+"F3.wireOp",EDGE,"E4.sketch_text.stroke-24"),sQuery(id+"F3.wireOp",EDGE,"E4.sketch_text.stroke-25"),sQuery(id+"F3.wireOp",EDGE,"E4.sketch_text.stroke-26"),sQuery(id+"F3.wireOp",EDGE,"E4.sketch_text.stroke-27"),sQuery(id+"F3.wireOp",EDGE,"E4.sketch_text.stroke-28"),sQuery(id+"F3.wireOp",EDGE,"E4.sketch_text.stroke-29"),sQuery(id+"F3.wireOp",EDGE,"E4.sketch_text.stroke-30"),sQuery(id+"F3.wireOp",EDGE,"E4.sketch_text.stroke-31"),sQuery(id+"F3.wireOp",EDGE,"E4.sketch_text.stroke-32"),sQuery(id+"F3.wireOp",EDGE,"E4.sketch_text.stroke-33"),sQuery(id+"F3.wireOp",EDGE,"E4.sketch_text.stroke-34"),sQuery(id+"F3.wireOp",EDGE,"E4.sketch_text.stroke-35"),sQuery(id+"F3.wireOp",EDGE,"E4.sketch_text.stroke-36"),sQuery(id+"F3.wireOp",EDGE,"E4.sketch_text.stroke-37"),sQuery(id+"F3.wireOp",EDGE,"E4.sketch_text.stroke-38"),sQuery(id+"F3.wireOp",EDGE,"E4.sketch_text.stroke-39"),sQuery(id+"F3.wireOp",EDGE,"E4.sketch_text.stroke-40"),sQuery(id+"F3.wireOp",EDGE,"E4.sketch_text.stroke-41"),sQuery(id+"F3.wireOp",EDGE,"E4.sketch_text.stroke-42"),sQuery(id+"F3.wireOp",EDGE,"E4.sketch_text.stroke-43"),sQuery(id+"F3.wireOp",EDGE,"E4.sketch_text.stroke-44"),sQuery(id+"F3.wireOp",EDGE,"E4.sketch_text.stroke-45"),sQuery(id+"F3.wireOp",EDGE,"E4.sketch_text.stroke-46"),sQuery(id+"F3.wireOp",EDGE,"E4.sketch_text.stroke-47"),sQuery(id+"F3.wireOp",EDGE,"E4.sketch_text.stroke-48"),sQuery(id+"F3.wireOp",EDGE,"E4.sketch_text.stroke-49"),sQuery(id+"F3.wireOp",EDGE,"E4.sketch_text.stroke-50"),sQuery(id+"F3.wireOp",EDGE,"E4.sketch_text.stroke-51"),sQuery(id+"F3.wireOp",EDGE,"E4.sketch_text.stroke-52"),sQuery(id+"F3.wireOp",EDGE,"E4.sketch_text.stroke-53"),sQuery(id+"F3.wireOp",EDGE,"E4.sketch_text.stroke-54"),sQuery(id+"F3.wireOp",EDGE,"E4.sketch_text.stroke-55"),sQuery(id+"F3.wireOp",EDGE,"E4.sketch_text.stroke-56"),sQuery(id+"F3.wireOp",EDGE,"E4.sketch_text.stroke-57"),sQuery(id+"F3.wireOp",EDGE,"E4.sketch_text.stroke-58"),sQuery(id+"F3.wireOp",EDGE,"E4.sketch_text.stroke-59"),sQuery(id+"F3.wireOp",EDGE,"E4.sketch_text.stroke-60"),sQuery(id+"F3.wireOp",EDGE,"E4.sketch_text.stroke-61"),sQuery(id+"F3.wireOp",EDGE,"E4.sketch_text.stroke-62"),sQuery(id+"F3.wireOp",EDGE,"E4.sketch_text.stroke-71"),sQuery(id+"F3.wireOp",EDGE,"E4.sketch_text.stroke-72"),sQuery(id+"F3.wireOp",EDGE,"E4.sketch_text.stroke-73"),sQuery(id+"F3.wireOp",EDGE,"E4.sketch_text.stroke-74"),sQuery(id+"F3.wireOp",EDGE,"E4.sketch_text.stroke-75"),sQuery(id+"F3.wireOp",EDGE,"E4.sketch_text.stroke-76"),sQuery(id+"F3.wireOp",EDGE,"E4.sketch_text.stroke-77"),sQuery(id+"F3.wireOp",EDGE,"E4.sketch_text.stroke-78"),sQuery(id+"F3.wireOp",EDGE,"E4.sketch_text.stroke-79"),sQuery(id+"F3.wireOp",EDGE,"E4.sketch_text.stroke-80"),sQuery(id+"F3.wireOp",EDGE,"E4.sketch_text.stroke-81"),sQuery(id+"F3.wireOp",EDGE,"E4.sketch_text.stroke-82"),sQuery(id+"F3.wireOp",EDGE,"E4.sketch_text.stroke-83"),sQuery(id+"F3.wireOp",EDGE,"E4.sketch_text.stroke-84"),sQuery(id+"F3.wireOp",EDGE,"E4.sketch_text.stroke-85"),sQuery(id+"F3.wireOp",EDGE,"E4.sketch_text.stroke-86"),sQuery(id+"F3.wireOp",EDGE,"E4.sketch_text.stroke-87"),sQuery(id+"F3.wireOp",EDGE,"E4.sketch_text.stroke-88"),sQuery(id+"F3.wireOp",EDGE,"E4.sketch_text.stroke-89"),sQuery(id+"F3.wireOp",EDGE,"E4.sketch_text.stroke-90"),sQuery(id+"F3.wireOp",EDGE,"E4.sketch_text.stroke-91"),sQuery(id+"F3.wireOp",EDGE,"E4.sketch_text.stroke-92"),sQuery(id+"F3.wireOp",EDGE,"E4.sketch_text.stroke-93"),sQuery(id+"F3.wireOp",EDGE,"E4.sketch_text.stroke-94"),sQuery(id+"F3.wireOp",EDGE,"E4.sketch_text.stroke-95"),sQuery(id+"F3.wireOp",EDGE,"E4.sketch_text.stroke-96"),sQuery(id+"F3.wireOp",EDGE,"E4.sketch_text.stroke-97"),sQuery(id+"F3.wireOp",EDGE,"E4.sketch_text.stroke-103"),sQuery(id+"F3.wireOp",EDGE,"E4.sketch_text.stroke-104"),sQuery(id+"F3.wireOp",EDGE,"E4.sketch_text.stroke-105"),sQuery(id+"F3.wireOp",EDGE,"E4.sketch_text.stroke-106"),sQuery(id+"F3.wireOp",EDGE,"E4.sketch_text.stroke-107"),sQuery(id+"F3.wireOp",EDGE,"E4.sketch_text.stroke-108"),sQuery(id+"F3.wireOp",EDGE,"E4.sketch_text.stroke-109"),sQuery(id+"F3.wireOp",EDGE,"E4.sketch_text.stroke-110"),sQuery(id+"F3.wireOp",EDGE,"E4.sketch_text.stroke-111"),sQuery(id+"F3.wireOp",EDGE,"E4.sketch_text.stroke-112"),sQuery(id+"F3.wireOp",EDGE,"E4.sketch_text.stroke-113"),sQuery(id+"F3.wireOp",EDGE,"E4.sketch_text.stroke-114"),sQuery(id+"F3.wireOp",EDGE,"E4.sketch_text.stroke-115"),sQuery(id+"F3.wireOp",EDGE,"E4.sketch_text.stroke-116"),sQuery(id+"F3.wireOp",EDGE,"E4.sketch_text.stroke-117"),sQuery(id+"F3.wireOp",EDGE,"E4.sketch_text.stroke-118"),sQuery(id+"F3.wireOp",EDGE,"E4.sketch_text.stroke-119"),sQuery(id+"F3.wireOp",EDGE,"E4.sketch_text.stroke-120"),sQuery(id+"F3.wireOp",EDGE,"E4.sketch_text.stroke-121"),sQuery(id+"F3.wireOp",EDGE,"E4.sketch_text.stroke-122"),sQuery(id+"F3.wireOp",EDGE,"E4.sketch_text.stroke-123"),sQuery(id+"F3.wireOp",EDGE,"E4.sketch_text.stroke-124"),sQuery(id+"F3.wireOp",EDGE,"E4.sketch_text.stroke-125"),sQuery(id+"F3.wireOp",EDGE,"E4.sketch_text.stroke-126"),sQuery(id+"F3.wireOp",EDGE,"E4.sketch_text.stroke-127"),sQuery(id+"F3.wireOp",EDGE,"E4.sketch_text.stroke-128"),sQuery(id+"F3.wireOp",EDGE,"E4.sketch_text.stroke-129"),sQuery(id+"F3.wireOp",EDGE,"E4.sketch_text.stroke-130"),sQuery(id+"F3.wireOp",EDGE,"E4.sketch_text.stroke-131"),sQuery(id+"F3.wireOp",EDGE,"E4.sketch_text.stroke-132"),sQuery(id+"F3.wireOp",EDGE,"E4.sketch_text.stroke-133"),sQuery(id+"F3.wireOp",EDGE,"E4.sketch_text.stroke-134"),sQuery(id+"F3.wireOp",EDGE,"E4.sketch_text.stroke-135"),sQuery(id+"F3.wireOp",EDGE,"E4.sketch_text.stroke-136"),sQuery(id+"F3.wireOp",EDGE,"E4.sketch_text.stroke-137"),sQuery(id+"F3.wireOp",EDGE,"E4.sketch_text.stroke-138"),sQuery(id+"F3.wireOp",EDGE,"E4.sketch_text.stroke-139"),sQuery(id+"F3.wireOp",EDGE,"E4.sketch_text.stroke-140"),sQuery(id+"F3.wireOp",EDGE,"E4.sketch_text.stroke-141"),sQuery(id+"F3.wireOp",EDGE,"E4.sketch_text.stroke-142"),sQuery(id+"F3.wireOp",EDGE,"E4.sketch_text.stroke-143"),sQuery(id+"F3.wireOp",EDGE,"E4.sketch_text.stroke-144"),sQuery(id+"F3.wireOp",EDGE,"E4.sketch_text.stroke-145"),sQuery(id+"F3.wireOp",EDGE,"E4.sketch_text.stroke-146"),sQuery(id+"F3.wireOp",EDGE,"E4.sketch_text.stroke-147"),sQuery(id+"F3.wireOp",EDGE,"E4.sketch_text.stroke-148"),sQuery(id+"F3.wireOp",EDGE,"E4.sketch_text.stroke-149"),sQuery(id+"F3.wireOp",EDGE,"E4.sketch_text.stroke-150"),sQuery(id+"F3.wireOp",EDGE,"E4.sketch_text.stroke-151"),sQuery(id+"F3.wireOp",EDGE,"E4.sketch_text.stroke-152"),sQuery(id+"F3.wireOp",EDGE,"E4.sketch_text.stroke-153"),sQuery(id+"F3.wireOp",EDGE,"E4.sketch_text.stroke-159"),sQuery(id+"F3.wireOp",EDGE,"E4.sketch_text.stroke-160"),sQuery(id+"F3.wireOp",EDGE,"E4.sketch_text.stroke-161"),sQuery(id+"F3.wireOp",EDGE,"E4.sketch_text.stroke-162"),sQuery(id+"F3.wireOp",EDGE,"E4.sketch_text.stroke-163"),sQuery(id+"F3.wireOp",EDGE,"E4.sketch_text.stroke-164"),sQuery(id+"F3.wireOp",EDGE,"E4.sketch_text.stroke-165"),sQuery(id+"F3.wireOp",EDGE,"E4.sketch_text.stroke-166"),sQuery(id+"F3.wireOp",EDGE,"E4.sketch_text.stroke-167"),sQuery(id+"F3.wireOp",EDGE,"E4.sketch_text.stroke-168"),sQuery(id+"F3.wireOp",EDGE,"E4.sketch_text.stroke-169"),sQuery(id+"F3.wireOp",EDGE,"E4.sketch_text.stroke-170"),sQuery(id+"F3.wireOp",EDGE,"E4.sketch_text.stroke-171"),sQuery(id+"F3.wireOp",EDGE,"E4.sketch_text.stroke-172"),sQuery(id+"F3.wireOp",EDGE,"E4.sketch_text.stroke-173"),sQuery(id+"F3.wireOp",EDGE,"E4.sketch_text.stroke-174"),sQuery(id+"F3.wireOp",EDGE,"E4.sketch_text.stroke-175"),sQuery(id+"F3.wireOp",EDGE,"E4.sketch_text.stroke-176"),sQuery(id+"F3.wireOp",EDGE,"E4.sketch_text.stroke-177"),sQuery(id+"F3.wireOp",EDGE,"E4.sketch_text.stroke-178"),sQuery(id+"F3.wireOp",EDGE,"E4.sketch_text.stroke-179"),sQuery(id+"F3.wireOp",EDGE,"E4.sketch_text.stroke-180"),subQ2,sQuery(id+"F5.wireOp",EDGE,"6ee83ff3-586e-4dbe-aaea-af71240543bd")])],"isStart":true})]),OD(0.0)],"derivedFrom":makeQuery(id+"F1.opExtrude","CAP_EDGE",EDGE,{"disambiguationData":[OSD([subQ0])],"isStart":false})});}
            var Q6;
            {var subQ0=sQuery(id+"F5.wireOp",EDGE,"6ee83ff3-586e-4dbe-aaea-af71240543bd");var subQ1=sQuery(id+"F0.wireOp",EDGE,"E0.bottom");var subQ2=sQuery(id+"F0.wireOp",EDGE,"E0.right");Q6=makeQuery(id+"F6.boolean.opBoolean","SPLIT",EDGE,{"disambiguationData":[TD([makeQuery(id+"F1.opExtrude","SWEPT_FACE",FACE,{"disambiguationData":[OSD([subQ1])]}),makeQuery(id+"F1.opExtrude","CAP_FACE",FACE,{"disambiguationData":[OSD([subQ1,sQuery(id+"F0.wireOp",EDGE,"E0.top"),sQuery(id+"F0.wireOp",EDGE,"E0.left"),subQ2])],"isStart":false}),makeQuery(id+"F1.opExtrude","SWEPT_FACE",FACE,{"disambiguationData":[OSD([subQ2])]}),makeQuery(id+"F6.opExtrude","CAP_FACE",FACE,{"disambiguationData":[OSD([subQ1,sQuery(id+"F2.wireOp",EDGE,"E2.sketch_text.stroke-0"),sQuery(id+"F2.wireOp",EDGE,"E2.sketch_text.stroke-1"),sQuery(id+"F2.wireOp",EDGE,"E2.sketch_text.stroke-2"),sQuery(id+"F2.wireOp",EDGE,"E2.sketch_text.stroke-3"),sQuery(id+"F2.wireOp",EDGE,"E2.sketch_text.stroke-4"),sQuery(id+"F2.wireOp",EDGE,"E2.sketch_text.stroke-5"),sQuery(id+"F2.wireOp",EDGE,"E2.sketch_text.stroke-6"),sQuery(id+"F2.wireOp",EDGE,"E2.sketch_text.stroke-7"),sQuery(id+"F2.wireOp",EDGE,"E2.sketch_text.stroke-8"),sQuery(id+"F2.wireOp",EDGE,"E2.sketch_text.stroke-9"),sQuery(id+"F2.wireOp",EDGE,"E2.sketch_text.stroke-10"),sQuery(id+"F2.wireOp",EDGE,"E2.sketch_text.stroke-11"),sQuery(id+"F2.wireOp",EDGE,"E2.sketch_text.stroke-12"),sQuery(id+"F2.wireOp",EDGE,"E2.sketch_text.stroke-13"),sQuery(id+"F2.wireOp",EDGE,"E2.sketch_text.stroke-14"),sQuery(id+"F2.wireOp",EDGE,"E2.sketch_text.stroke-15"),sQuery(id+"F2.wireOp",EDGE,"E2.sketch_text.stroke-16"),sQuery(id+"F2.wireOp",EDGE,"E2.sketch_text.stroke-17"),sQuery(id+"F2.wireOp",EDGE,"E2.sketch_text.stroke-18"),sQuery(id+"F2.wireOp",EDGE,"E2.sketch_text.stroke-19"),sQuery(id+"F2.wireOp",EDGE,"E2.sketch_text.stroke-20"),sQuery(id+"F2.wireOp",EDGE,"E2.sketch_text.stroke-21"),sQuery(id+"F2.wireOp",EDGE,"E2.sketch_text.stroke-22"),sQuery(id+"F2.wireOp",EDGE,"E2.sketch_text.stroke-23"),sQuery(id+"F2.wireOp",EDGE,"E2.sketch_text.stroke-24"),sQuery(id+"F2.wireOp",EDGE,"E2.sketch_text.stroke-25"),sQuery(id+"F2.wireOp",EDGE,"E2.sketch_text.stroke-26"),sQuery(id+"F2.wireOp",EDGE,"E2.sketch_text.stroke-27"),sQuery(id+"F2.wireOp",EDGE,"E2.sketch_text.stroke-28"),sQuery(id+"F2.wireOp",EDGE,"E2.sketch_text.stroke-29"),sQuery(id+"F2.wireOp",EDGE,"E2.sketch_text.stroke-30"),sQuery(id+"F2.wireOp",EDGE,"E2.sketch_text.stroke-31"),sQuery(id+"F2.wireOp",EDGE,"E2.sketch_text.stroke-32"),sQuery(id+"F2.wireOp",EDGE,"E2.sketch_text.stroke-33"),sQuery(id+"F2.wireOp",EDGE,"E2.sketch_text.stroke-34"),sQuery(id+"F2.wireOp",EDGE,"E2.sketch_text.stroke-35"),sQuery(id+"F2.wireOp",EDGE,"E2.sketch_text.stroke-36"),sQuery(id+"F2.wireOp",EDGE,"E2.sketch_text.stroke-37"),sQuery(id+"F2.wireOp",EDGE,"E2.sketch_text.stroke-38"),sQuery(id+"F2.wireOp",EDGE,"E2.sketch_text.stroke-39"),sQuery(id+"F2.wireOp",EDGE,"E2.sketch_text.stroke-40"),sQuery(id+"F2.wireOp",EDGE,"E2.sketch_text.stroke-41"),sQuery(id+"F2.wireOp",EDGE,"E2.sketch_text.stroke-42"),sQuery(id+"F2.wireOp",EDGE,"E2.sketch_text.stroke-43"),sQuery(id+"F2.wireOp",EDGE,"E2.sketch_text.stroke-44"),sQuery(id+"F2.wireOp",EDGE,"E2.sketch_text.stroke-45"),sQuery(id+"F2.wireOp",EDGE,"E2.sketch_text.stroke-46"),sQuery(id+"F2.wireOp",EDGE,"E2.sketch_text.stroke-47"),sQuery(id+"F2.wireOp",EDGE,"E2.sketch_text.stroke-48"),sQuery(id+"F2.wireOp",EDGE,"E2.sketch_text.stroke-49"),sQuery(id+"F2.wireOp",EDGE,"E2.sketch_text.stroke-50"),sQuery(id+"F2.wireOp",EDGE,"E2.sketch_text.stroke-51"),sQuery(id+"F2.wireOp",EDGE,"E2.sketch_text.stroke-52"),sQuery(id+"F2.wireOp",EDGE,"E2.sketch_text.stroke-53"),sQuery(id+"F2.wireOp",EDGE,"E2.sketch_text.stroke-54"),sQuery(id+"F2.wireOp",EDGE,"E2.sketch_text.stroke-55"),sQuery(id+"F2.wireOp",EDGE,"E2.sketch_text.stroke-56"),sQuery(id+"F2.wireOp",EDGE,"E2.sketch_text.stroke-57"),sQuery(id+"F2.wireOp",EDGE,"E2.sketch_text.stroke-58"),sQuery(id+"F2.wireOp",EDGE,"E2.sketch_text.stroke-59"),sQuery(id+"F2.wireOp",EDGE,"E2.sketch_text.stroke-60"),sQuery(id+"F2.wireOp",EDGE,"E2.sketch_text.stroke-61"),sQuery(id+"F2.wireOp",EDGE,"E2.sketch_text.stroke-62"),sQuery(id+"F2.wireOp",EDGE,"E2.sketch_text.stroke-63"),sQuery(id+"F2.wireOp",EDGE,"E2.sketch_text.stroke-64"),sQuery(id+"F2.wireOp",EDGE,"E2.sketch_text.stroke-65"),sQuery(id+"F2.wireOp",EDGE,"E2.sketch_text.stroke-66"),sQuery(id+"F2.wireOp",EDGE,"E2.sketch_text.stroke-67"),sQuery(id+"F2.wireOp",EDGE,"E2.sketch_text.stroke-68"),sQuery(id+"F2.wireOp",EDGE,"E2.sketch_text.stroke-69"),sQuery(id+"F2.wireOp",EDGE,"E2.sketch_text.stroke-70"),sQuery(id+"F2.wireOp",EDGE,"E2.sketch_text.stroke-71"),sQuery(id+"F2.wireOp",EDGE,"E2.sketch_text.stroke-72"),sQuery(id+"F2.wireOp",EDGE,"E2.sketch_text.stroke-73"),sQuery(id+"F2.wireOp",EDGE,"E2.sketch_text.stroke-74"),sQuery(id+"F2.wireOp",EDGE,"E2.sketch_text.stroke-75"),sQuery(id+"F2.wireOp",EDGE,"E2.sketch_text.stroke-76"),sQuery(id+"F2.wireOp",EDGE,"E2.sketch_text.stroke-77"),sQuery(id+"F2.wireOp",EDGE,"E2.sketch_text.stroke-78"),sQuery(id+"F2.wireOp",EDGE,"E2.sketch_text.stroke-79"),sQuery(id+"F2.wireOp",EDGE,"E2.sketch_text.stroke-80"),sQuery(id+"F2.wireOp",EDGE,"E2.sketch_text.stroke-81"),sQuery(id+"F2.wireOp",EDGE,"E2.sketch_text.stroke-82"),sQuery(id+"F2.wireOp",EDGE,"E2.sketch_text.stroke-83"),sQuery(id+"F2.wireOp",EDGE,"E2.sketch_text.stroke-84"),sQuery(id+"F2.wireOp",EDGE,"E2.sketch_text.stroke-85"),sQuery(id+"F2.wireOp",EDGE,"E2.sketch_text.stroke-86"),sQuery(id+"F2.wireOp",EDGE,"E2.sketch_text.stroke-87"),sQuery(id+"F2.wireOp",EDGE,"E2.sketch_text.stroke-88"),sQuery(id+"F2.wireOp",EDGE,"E2.sketch_text.stroke-89"),sQuery(id+"F2.wireOp",EDGE,"E2.sketch_text.stroke-90"),sQuery(id+"F2.wireOp",EDGE,"E2.sketch_text.stroke-91"),sQuery(id+"F2.wireOp",EDGE,"E2.sketch_text.stroke-92"),sQuery(id+"F2.wireOp",EDGE,"E2.sketch_text.stroke-93"),sQuery(id+"F2.wireOp",EDGE,"E2.sketch_text.stroke-94"),sQuery(id+"F2.wireOp",EDGE,"E2.sketch_text.stroke-95"),sQuery(id+"F2.wireOp",EDGE,"E2.sketch_text.stroke-96"),sQuery(id+"F2.wireOp",EDGE,"E2.sketch_text.stroke-97"),sQuery(id+"F2.wireOp",EDGE,"E2.sketch_text.stroke-98"),sQuery(id+"F2.wireOp",EDGE,"E2.sketch_text.stroke-99"),sQuery(id+"F2.wireOp",EDGE,"E2.sketch_text.stroke-100"),sQuery(id+"F2.wireOp",EDGE,"E2.sketch_text.stroke-101"),sQuery(id+"F2.wireOp",EDGE,"E2.sketch_text.stroke-102"),sQuery(id+"F2.wireOp",EDGE,"E2.sketch_text.stroke-103"),sQuery(id+"F2.wireOp",EDGE,"E2.sketch_text.stroke-104"),sQuery(id+"F2.wireOp",EDGE,"E2.sketch_text.stroke-105"),sQuery(id+"F2.wireOp",EDGE,"E2.sketch_text.stroke-106"),sQuery(id+"F2.wireOp",EDGE,"E2.sketch_text.stroke-107"),sQuery(id+"F2.wireOp",EDGE,"E2.sketch_text.stroke-108"),sQuery(id+"F2.wireOp",EDGE,"E2.sketch_text.stroke-109"),sQuery(id+"F2.wireOp",EDGE,"E2.sketch_text.stroke-110"),sQuery(id+"F2.wireOp",EDGE,"E2.sketch_text.stroke-111"),sQuery(id+"F2.wireOp",EDGE,"E2.sketch_text.stroke-112"),sQuery(id+"F2.wireOp",EDGE,"E2.sketch_text.stroke-113"),sQuery(id+"F2.wireOp",EDGE,"E2.sketch_text.stroke-114"),sQuery(id+"F2.wireOp",EDGE,"E2.sketch_text.stroke-115"),sQuery(id+"F2.wireOp",EDGE,"E2.sketch_text.stroke-116"),sQuery(id+"F2.wireOp",EDGE,"E2.sketch_text.stroke-117"),sQuery(id+"F2.wireOp",EDGE,"E2.sketch_text.stroke-118"),sQuery(id+"F2.wireOp",EDGE,"E2.sketch_text.stroke-119"),sQuery(id+"F2.wireOp",EDGE,"E2.sketch_text.stroke-120"),sQuery(id+"F2.wireOp",EDGE,"E2.sketch_text.stroke-121"),sQuery(id+"F2.wireOp",EDGE,"E2.sketch_text.stroke-122"),sQuery(id+"F2.wireOp",EDGE,"E2.sketch_text.stroke-123"),sQuery(id+"F2.wireOp",EDGE,"E2.sketch_text.stroke-124"),sQuery(id+"F2.wireOp",EDGE,"E2.sketch_text.stroke-125"),sQuery(id+"F2.wireOp",EDGE,"E2.sketch_text.stroke-126"),sQuery(id+"F2.wireOp",EDGE,"E2.sketch_text.stroke-127"),sQuery(id+"F2.wireOp",EDGE,"E2.sketch_text.stroke-128"),sQuery(id+"F2.wireOp",EDGE,"E2.sketch_text.stroke-129"),sQuery(id+"F2.wireOp",EDGE,"E2.sketch_text.stroke-130"),sQuery(id+"F2.wireOp",EDGE,"E2.sketch_text.stroke-131"),sQuery(id+"F2.wireOp",EDGE,"E2.sketch_text.stroke-132"),sQuery(id+"F2.wireOp",EDGE,"E2.sketch_text.stroke-133"),sQuery(id+"F2.wireOp",EDGE,"E2.sketch_text.stroke-134"),sQuery(id+"F2.wireOp",EDGE,"E2.sketch_text.stroke-135"),sQuery(id+"F2.wireOp",EDGE,"E2.sketch_text.stroke-136"),sQuery(id+"F2.wireOp",EDGE,"E2.sketch_text.stroke-137"),sQuery(id+"F2.wireOp",EDGE,"E2.sketch_text.stroke-138"),sQuery(id+"F2.wireOp",EDGE,"E2.sketch_text.stroke-139"),sQuery(id+"F2.wireOp",EDGE,"E2.sketch_text.stroke-140"),sQuery(id+"F2.wireOp",EDGE,"E2.sketch_text.stroke-141"),sQuery(id+"F2.wireOp",EDGE,"E2.sketch_text.stroke-142"),sQuery(id+"F2.wireOp",EDGE,"E2.sketch_text.stroke-143"),sQuery(id+"F2.wireOp",EDGE,"E2.sketch_text.stroke-144"),sQuery(id+"F2.wireOp",EDGE,"E2.sketch_text.stroke-145"),sQuery(id+"F2.wireOp",EDGE,"E2.sketch_text.stroke-146"),sQuery(id+"F2.wireOp",EDGE,"E2.sketch_text.stroke-147"),sQuery(id+"F2.wireOp",EDGE,"E2.sketch_text.stroke-148"),sQuery(id+"F2.wireOp",EDGE,"E2.sketch_text.stroke-149"),sQuery(id+"F2.wireOp",EDGE,"E2.sketch_text.stroke-150"),sQuery(id+"F2.wireOp",EDGE,"E2.sketch_text.stroke-151"),sQuery(id+"F2.wireOp",EDGE,"E2.sketch_text.stroke-152"),sQuery(id+"F2.wireOp",EDGE,"E2.sketch_text.stroke-153"),sQuery(id+"F2.wireOp",EDGE,"E2.sketch_text.stroke-154"),sQuery(id+"F2.wireOp",EDGE,"E2.sketch_text.stroke-155"),sQuery(id+"F2.wireOp",EDGE,"E2.sketch_text.stroke-156"),sQuery(id+"F2.wireOp",EDGE,"E2.sketch_text.stroke-157"),sQuery(id+"F2.wireOp",EDGE,"E2.sketch_text.stroke-158"),sQuery(id+"F2.wireOp",EDGE,"E2.sketch_text.stroke-159"),sQuery(id+"F2.wireOp",EDGE,"E2.sketch_text.stroke-160"),sQuery(id+"F2.wireOp",EDGE,"E2.sketch_text.stroke-161"),sQuery(id+"F2.wireOp",EDGE,"E2.sketch_text.stroke-162"),sQuery(id+"F2.wireOp",EDGE,"E2.sketch_text.stroke-163"),sQuery(id+"F2.wireOp",EDGE,"E2.sketch_text.stroke-164"),sQuery(id+"F2.wireOp",EDGE,"E2.sketch_text.stroke-165"),sQuery(id+"F2.wireOp",EDGE,"E2.sketch_text.stroke-166"),sQuery(id+"F2.wireOp",EDGE,"E2.sketch_text.stroke-167"),sQuery(id+"F2.wireOp",EDGE,"E2.sketch_text.stroke-168"),sQuery(id+"F2.wireOp",EDGE,"E2.sketch_text.stroke-169"),sQuery(id+"F2.wireOp",EDGE,"E2.sketch_text.stroke-170"),sQuery(id+"F2.wireOp",EDGE,"E2.sketch_text.stroke-171"),sQuery(id+"F2.wireOp",EDGE,"E2.sketch_text.stroke-172"),sQuery(id+"F2.wireOp",EDGE,"E2.sketch_text.stroke-173"),sQuery(id+"F3.wireOp",EDGE,"E4.sketch_text.stroke-0"),sQuery(id+"F3.wireOp",EDGE,"E4.sketch_text.stroke-1"),sQuery(id+"F3.wireOp",EDGE,"E4.sketch_text.stroke-2"),sQuery(id+"F3.wireOp",EDGE,"E4.sketch_text.stroke-3"),sQuery(id+"F3.wireOp",EDGE,"E4.sketch_text.stroke-4"),sQuery(id+"F3.wireOp",EDGE,"E4.sketch_text.stroke-5"),sQuery(id+"F3.wireOp",EDGE,"E4.sketch_text.stroke-6"),sQuery(id+"F3.wireOp",EDGE,"E4.sketch_text.stroke-7"),sQuery(id+"F3.wireOp",EDGE,"E4.sketch_text.stroke-8"),sQuery(id+"F3.wireOp",EDGE,"E4.sketch_text.stroke-9"),sQuery(id+"F3.wireOp",EDGE,"E4.sketch_text.stroke-10"),sQuery(id+"F3.wireOp",EDGE,"E4.sketch_text.stroke-11"),sQuery(id+"F3.wireOp",EDGE,"E4.sketch_text.stroke-12"),sQuery(id+"F3.wireOp",EDGE,"E4.sketch_text.stroke-13"),sQuery(id+"F3.wireOp",EDGE,"E4.sketch_text.stroke-14"),sQuery(id+"F3.wireOp",EDGE,"E4.sketch_text.stroke-15"),sQuery(id+"F3.wireOp",EDGE,"E4.sketch_text.stroke-16"),sQuery(id+"F3.wireOp",EDGE,"E4.sketch_text.stroke-17"),sQuery(id+"F3.wireOp",EDGE,"E4.sketch_text.stroke-18"),sQuery(id+"F3.wireOp",EDGE,"E4.sketch_text.stroke-19"),sQuery(id+"F3.wireOp",EDGE,"E4.sketch_text.stroke-20"),sQuery(id+"F3.wireOp",EDGE,"E4.sketch_text.stroke-21"),sQuery(id+"F3.wireOp",EDGE,"E4.sketch_text.stroke-22"),sQuery(id+"F3.wireOp",EDGE,"E4.sketch_text.stroke-23"),sQuery(id+"F3.wireOp",EDGE,"E4.sketch_text.stroke-24"),sQuery(id+"F3.wireOp",EDGE,"E4.sketch_text.stroke-25"),sQuery(id+"F3.wireOp",EDGE,"E4.sketch_text.stroke-26"),sQuery(id+"F3.wireOp",EDGE,"E4.sketch_text.stroke-27"),sQuery(id+"F3.wireOp",EDGE,"E4.sketch_text.stroke-28"),sQuery(id+"F3.wireOp",EDGE,"E4.sketch_text.stroke-29"),sQuery(id+"F3.wireOp",EDGE,"E4.sketch_text.stroke-30"),sQuery(id+"F3.wireOp",EDGE,"E4.sketch_text.stroke-31"),sQuery(id+"F3.wireOp",EDGE,"E4.sketch_text.stroke-32"),sQuery(id+"F3.wireOp",EDGE,"E4.sketch_text.stroke-33"),sQuery(id+"F3.wireOp",EDGE,"E4.sketch_text.stroke-34"),sQuery(id+"F3.wireOp",EDGE,"E4.sketch_text.stroke-35"),sQuery(id+"F3.wireOp",EDGE,"E4.sketch_text.stroke-36"),sQuery(id+"F3.wireOp",EDGE,"E4.sketch_text.stroke-37"),sQuery(id+"F3.wireOp",EDGE,"E4.sketch_text.stroke-38"),sQuery(id+"F3.wireOp",EDGE,"E4.sketch_text.stroke-39"),sQuery(id+"F3.wireOp",EDGE,"E4.sketch_text.stroke-40"),sQuery(id+"F3.wireOp",EDGE,"E4.sketch_text.stroke-41"),sQuery(id+"F3.wireOp",EDGE,"E4.sketch_text.stroke-42"),sQuery(id+"F3.wireOp",EDGE,"E4.sketch_text.stroke-43"),sQuery(id+"F3.wireOp",EDGE,"E4.sketch_text.stroke-44"),sQuery(id+"F3.wireOp",EDGE,"E4.sketch_text.stroke-45"),sQuery(id+"F3.wireOp",EDGE,"E4.sketch_text.stroke-46"),sQuery(id+"F3.wireOp",EDGE,"E4.sketch_text.stroke-47"),sQuery(id+"F3.wireOp",EDGE,"E4.sketch_text.stroke-48"),sQuery(id+"F3.wireOp",EDGE,"E4.sketch_text.stroke-49"),sQuery(id+"F3.wireOp",EDGE,"E4.sketch_text.stroke-50"),sQuery(id+"F3.wireOp",EDGE,"E4.sketch_text.stroke-51"),sQuery(id+"F3.wireOp",EDGE,"E4.sketch_text.stroke-52"),sQuery(id+"F3.wireOp",EDGE,"E4.sketch_text.stroke-53"),sQuery(id+"F3.wireOp",EDGE,"E4.sketch_text.stroke-54"),sQuery(id+"F3.wireOp",EDGE,"E4.sketch_text.stroke-55"),sQuery(id+"F3.wireOp",EDGE,"E4.sketch_text.stroke-56"),sQuery(id+"F3.wireOp",EDGE,"E4.sketch_text.stroke-57"),sQuery(id+"F3.wireOp",EDGE,"E4.sketch_text.stroke-58"),sQuery(id+"F3.wireOp",EDGE,"E4.sketch_text.stroke-59"),sQuery(id+"F3.wireOp",EDGE,"E4.sketch_text.stroke-60"),sQuery(id+"F3.wireOp",EDGE,"E4.sketch_text.stroke-61"),sQuery(id+"F3.wireOp",EDGE,"E4.sketch_text.stroke-62"),sQuery(id+"F3.wireOp",EDGE,"E4.sketch_text.stroke-71"),sQuery(id+"F3.wireOp",EDGE,"E4.sketch_text.stroke-72"),sQuery(id+"F3.wireOp",EDGE,"E4.sketch_text.stroke-73"),sQuery(id+"F3.wireOp",EDGE,"E4.sketch_text.stroke-74"),sQuery(id+"F3.wireOp",EDGE,"E4.sketch_text.stroke-75"),sQuery(id+"F3.wireOp",EDGE,"E4.sketch_text.stroke-76"),sQuery(id+"F3.wireOp",EDGE,"E4.sketch_text.stroke-77"),sQuery(id+"F3.wireOp",EDGE,"E4.sketch_text.stroke-78"),sQuery(id+"F3.wireOp",EDGE,"E4.sketch_text.stroke-79"),sQuery(id+"F3.wireOp",EDGE,"E4.sketch_text.stroke-80"),sQuery(id+"F3.wireOp",EDGE,"E4.sketch_text.stroke-81"),sQuery(id+"F3.wireOp",EDGE,"E4.sketch_text.stroke-82"),sQuery(id+"F3.wireOp",EDGE,"E4.sketch_text.stroke-83"),sQuery(id+"F3.wireOp",EDGE,"E4.sketch_text.stroke-84"),sQuery(id+"F3.wireOp",EDGE,"E4.sketch_text.stroke-85"),sQuery(id+"F3.wireOp",EDGE,"E4.sketch_text.stroke-86"),sQuery(id+"F3.wireOp",EDGE,"E4.sketch_text.stroke-87"),sQuery(id+"F3.wireOp",EDGE,"E4.sketch_text.stroke-88"),sQuery(id+"F3.wireOp",EDGE,"E4.sketch_text.stroke-89"),sQuery(id+"F3.wireOp",EDGE,"E4.sketch_text.stroke-90"),sQuery(id+"F3.wireOp",EDGE,"E4.sketch_text.stroke-91"),sQuery(id+"F3.wireOp",EDGE,"E4.sketch_text.stroke-92"),sQuery(id+"F3.wireOp",EDGE,"E4.sketch_text.stroke-93"),sQuery(id+"F3.wireOp",EDGE,"E4.sketch_text.stroke-94"),sQuery(id+"F3.wireOp",EDGE,"E4.sketch_text.stroke-95"),sQuery(id+"F3.wireOp",EDGE,"E4.sketch_text.stroke-96"),sQuery(id+"F3.wireOp",EDGE,"E4.sketch_text.stroke-97"),sQuery(id+"F3.wireOp",EDGE,"E4.sketch_text.stroke-103"),sQuery(id+"F3.wireOp",EDGE,"E4.sketch_text.stroke-104"),sQuery(id+"F3.wireOp",EDGE,"E4.sketch_text.stroke-105"),sQuery(id+"F3.wireOp",EDGE,"E4.sketch_text.stroke-106"),sQuery(id+"F3.wireOp",EDGE,"E4.sketch_text.stroke-107"),sQuery(id+"F3.wireOp",EDGE,"E4.sketch_text.stroke-108"),sQuery(id+"F3.wireOp",EDGE,"E4.sketch_text.stroke-109"),sQuery(id+"F3.wireOp",EDGE,"E4.sketch_text.stroke-110"),sQuery(id+"F3.wireOp",EDGE,"E4.sketch_text.stroke-111"),sQuery(id+"F3.wireOp",EDGE,"E4.sketch_text.stroke-112"),sQuery(id+"F3.wireOp",EDGE,"E4.sketch_text.stroke-113"),sQuery(id+"F3.wireOp",EDGE,"E4.sketch_text.stroke-114"),sQuery(id+"F3.wireOp",EDGE,"E4.sketch_text.stroke-115"),sQuery(id+"F3.wireOp",EDGE,"E4.sketch_text.stroke-116"),sQuery(id+"F3.wireOp",EDGE,"E4.sketch_text.stroke-117"),sQuery(id+"F3.wireOp",EDGE,"E4.sketch_text.stroke-118"),sQuery(id+"F3.wireOp",EDGE,"E4.sketch_text.stroke-119"),sQuery(id+"F3.wireOp",EDGE,"E4.sketch_text.stroke-120"),sQuery(id+"F3.wireOp",EDGE,"E4.sketch_text.stroke-121"),sQuery(id+"F3.wireOp",EDGE,"E4.sketch_text.stroke-122"),sQuery(id+"F3.wireOp",EDGE,"E4.sketch_text.stroke-123"),sQuery(id+"F3.wireOp",EDGE,"E4.sketch_text.stroke-124"),sQuery(id+"F3.wireOp",EDGE,"E4.sketch_text.stroke-125"),sQuery(id+"F3.wireOp",EDGE,"E4.sketch_text.stroke-126"),sQuery(id+"F3.wireOp",EDGE,"E4.sketch_text.stroke-127"),sQuery(id+"F3.wireOp",EDGE,"E4.sketch_text.stroke-128"),sQuery(id+"F3.wireOp",EDGE,"E4.sketch_text.stroke-129"),sQuery(id+"F3.wireOp",EDGE,"E4.sketch_text.stroke-130"),sQuery(id+"F3.wireOp",EDGE,"E4.sketch_text.stroke-131"),sQuery(id+"F3.wireOp",EDGE,"E4.sketch_text.stroke-132"),sQuery(id+"F3.wireOp",EDGE,"E4.sketch_text.stroke-133"),sQuery(id+"F3.wireOp",EDGE,"E4.sketch_text.stroke-134"),sQuery(id+"F3.wireOp",EDGE,"E4.sketch_text.stroke-135"),sQuery(id+"F3.wireOp",EDGE,"E4.sketch_text.stroke-136"),sQuery(id+"F3.wireOp",EDGE,"E4.sketch_text.stroke-137"),sQuery(id+"F3.wireOp",EDGE,"E4.sketch_text.stroke-138"),sQuery(id+"F3.wireOp",EDGE,"E4.sketch_text.stroke-139"),sQuery(id+"F3.wireOp",EDGE,"E4.sketch_text.stroke-140"),sQuery(id+"F3.wireOp",EDGE,"E4.sketch_text.stroke-141"),sQuery(id+"F3.wireOp",EDGE,"E4.sketch_text.stroke-142"),sQuery(id+"F3.wireOp",EDGE,"E4.sketch_text.stroke-143"),sQuery(id+"F3.wireOp",EDGE,"E4.sketch_text.stroke-144"),sQuery(id+"F3.wireOp",EDGE,"E4.sketch_text.stroke-145"),sQuery(id+"F3.wireOp",EDGE,"E4.sketch_text.stroke-146"),sQuery(id+"F3.wireOp",EDGE,"E4.sketch_text.stroke-147"),sQuery(id+"F3.wireOp",EDGE,"E4.sketch_text.stroke-148"),sQuery(id+"F3.wireOp",EDGE,"E4.sketch_text.stroke-149"),sQuery(id+"F3.wireOp",EDGE,"E4.sketch_text.stroke-150"),sQuery(id+"F3.wireOp",EDGE,"E4.sketch_text.stroke-151"),sQuery(id+"F3.wireOp",EDGE,"E4.sketch_text.stroke-152"),sQuery(id+"F3.wireOp",EDGE,"E4.sketch_text.stroke-153"),sQuery(id+"F3.wireOp",EDGE,"E4.sketch_text.stroke-159"),sQuery(id+"F3.wireOp",EDGE,"E4.sketch_text.stroke-160"),sQuery(id+"F3.wireOp",EDGE,"E4.sketch_text.stroke-161"),sQuery(id+"F3.wireOp",EDGE,"E4.sketch_text.stroke-162"),sQuery(id+"F3.wireOp",EDGE,"E4.sketch_text.stroke-163"),sQuery(id+"F3.wireOp",EDGE,"E4.sketch_text.stroke-164"),sQuery(id+"F3.wireOp",EDGE,"E4.sketch_text.stroke-165"),sQuery(id+"F3.wireOp",EDGE,"E4.sketch_text.stroke-166"),sQuery(id+"F3.wireOp",EDGE,"E4.sketch_text.stroke-167"),sQuery(id+"F3.wireOp",EDGE,"E4.sketch_text.stroke-168"),sQuery(id+"F3.wireOp",EDGE,"E4.sketch_text.stroke-169"),sQuery(id+"F3.wireOp",EDGE,"E4.sketch_text.stroke-170"),sQuery(id+"F3.wireOp",EDGE,"E4.sketch_text.stroke-171"),sQuery(id+"F3.wireOp",EDGE,"E4.sketch_text.stroke-172"),sQuery(id+"F3.wireOp",EDGE,"E4.sketch_text.stroke-173"),sQuery(id+"F3.wireOp",EDGE,"E4.sketch_text.stroke-174"),sQuery(id+"F3.wireOp",EDGE,"E4.sketch_text.stroke-175"),sQuery(id+"F3.wireOp",EDGE,"E4.sketch_text.stroke-176"),sQuery(id+"F3.wireOp",EDGE,"E4.sketch_text.stroke-177"),sQuery(id+"F3.wireOp",EDGE,"E4.sketch_text.stroke-178"),sQuery(id+"F3.wireOp",EDGE,"E4.sketch_text.stroke-179"),sQuery(id+"F3.wireOp",EDGE,"E4.sketch_text.stroke-180"),sQuery(id+"F5.wireOp",EDGE,"8007402e-1a4e-4a06-85a5-2af08e553504"),subQ0])],"isStart":true}),makeQuery(id+"F6.opExtrude","SWEPT_FACE",FACE,{"disambiguationData":[OSD([subQ0])]})])],"derivedFrom":makeQuery(id+"F6.opExtrude","CAP_EDGE",EDGE,{"disambiguationData":[OSD([subQ0])],"isStart":true})});}
            var Q7;
            {var subQ0=sQuery(id+"F0.wireOp",EDGE,"E0.right");var subQ1=sQuery(id+"F0.wireOp",EDGE,"E0.top");var subQ2=sQuery(id+"F5.wireOp",EDGE,"6ee83ff3-586e-4dbe-aaea-af71240543bd");var subQ3=sQuery(id+"F0.wireOp",EDGE,"E0.bottom");Q7=makeQuery(id+"F6.boolean.opBoolean","SPLIT",EDGE,{"disambiguationData":[TD([makeQuery(id+"F1.opExtrude","CAP_FACE",FACE,{"disambiguationData":[OSD([subQ3,subQ1,sQuery(id+"F0.wireOp",EDGE,"E0.left"),subQ0])],"isStart":false}),makeQuery(id+"F1.opExtrude","SWEPT_FACE",FACE,{"disambiguationData":[OSD([subQ1])]}),makeQuery(id+"F1.opExtrude","SWEPT_FACE",FACE,{"disambiguationData":[OSD([subQ0])]}),makeQuery(id+"F6.opExtrude","CAP_FACE",FACE,{"disambiguationData":[OSD([subQ3,sQuery(id+"F2.wireOp",EDGE,"E2.sketch_text.stroke-0"),sQuery(id+"F2.wireOp",EDGE,"E2.sketch_text.stroke-1"),sQuery(id+"F2.wireOp",EDGE,"E2.sketch_text.stroke-2"),sQuery(id+"F2.wireOp",EDGE,"E2.sketch_text.stroke-3"),sQuery(id+"F2.wireOp",EDGE,"E2.sketch_text.stroke-4"),sQuery(id+"F2.wireOp",EDGE,"E2.sketch_text.stroke-5"),sQuery(id+"F2.wireOp",EDGE,"E2.sketch_text.stroke-6"),sQuery(id+"F2.wireOp",EDGE,"E2.sketch_text.stroke-7"),sQuery(id+"F2.wireOp",EDGE,"E2.sketch_text.stroke-8"),sQuery(id+"F2.wireOp",EDGE,"E2.sketch_text.stroke-9"),sQuery(id+"F2.wireOp",EDGE,"E2.sketch_text.stroke-10"),sQuery(id+"F2.wireOp",EDGE,"E2.sketch_text.stroke-11"),sQuery(id+"F2.wireOp",EDGE,"E2.sketch_text.stroke-12"),sQuery(id+"F2.wireOp",EDGE,"E2.sketch_text.stroke-13"),sQuery(id+"F2.wireOp",EDGE,"E2.sketch_text.stroke-14"),sQuery(id+"F2.wireOp",EDGE,"E2.sketch_text.stroke-15"),sQuery(id+"F2.wireOp",EDGE,"E2.sketch_text.stroke-16"),sQuery(id+"F2.wireOp",EDGE,"E2.sketch_text.stroke-17"),sQuery(id+"F2.wireOp",EDGE,"E2.sketch_text.stroke-18"),sQuery(id+"F2.wireOp",EDGE,"E2.sketch_text.stroke-19"),sQuery(id+"F2.wireOp",EDGE,"E2.sketch_text.stroke-20"),sQuery(id+"F2.wireOp",EDGE,"E2.sketch_text.stroke-21"),sQuery(id+"F2.wireOp",EDGE,"E2.sketch_text.stroke-22"),sQuery(id+"F2.wireOp",EDGE,"E2.sketch_text.stroke-23"),sQuery(id+"F2.wireOp",EDGE,"E2.sketch_text.stroke-24"),sQuery(id+"F2.wireOp",EDGE,"E2.sketch_text.stroke-25"),sQuery(id+"F2.wireOp",EDGE,"E2.sketch_text.stroke-26"),sQuery(id+"F2.wireOp",EDGE,"E2.sketch_text.stroke-27"),sQuery(id+"F2.wireOp",EDGE,"E2.sketch_text.stroke-28"),sQuery(id+"F2.wireOp",EDGE,"E2.sketch_text.stroke-29"),sQuery(id+"F2.wireOp",EDGE,"E2.sketch_text.stroke-30"),sQuery(id+"F2.wireOp",EDGE,"E2.sketch_text.stroke-31"),sQuery(id+"F2.wireOp",EDGE,"E2.sketch_text.stroke-32"),sQuery(id+"F2.wireOp",EDGE,"E2.sketch_text.stroke-33"),sQuery(id+"F2.wireOp",EDGE,"E2.sketch_text.stroke-34"),sQuery(id+"F2.wireOp",EDGE,"E2.sketch_text.stroke-35"),sQuery(id+"F2.wireOp",EDGE,"E2.sketch_text.stroke-36"),sQuery(id+"F2.wireOp",EDGE,"E2.sketch_text.stroke-37"),sQuery(id+"F2.wireOp",EDGE,"E2.sketch_text.stroke-38"),sQuery(id+"F2.wireOp",EDGE,"E2.sketch_text.stroke-39"),sQuery(id+"F2.wireOp",EDGE,"E2.sketch_text.stroke-40"),sQuery(id+"F2.wireOp",EDGE,"E2.sketch_text.stroke-41"),sQuery(id+"F2.wireOp",EDGE,"E2.sketch_text.stroke-42"),sQuery(id+"F2.wireOp",EDGE,"E2.sketch_text.stroke-43"),sQuery(id+"F2.wireOp",EDGE,"E2.sketch_text.stroke-44"),sQuery(id+"F2.wireOp",EDGE,"E2.sketch_text.stroke-45"),sQuery(id+"F2.wireOp",EDGE,"E2.sketch_text.stroke-46"),sQuery(id+"F2.wireOp",EDGE,"E2.sketch_text.stroke-47"),sQuery(id+"F2.wireOp",EDGE,"E2.sketch_text.stroke-48"),sQuery(id+"F2.wireOp",EDGE,"E2.sketch_text.stroke-49"),sQuery(id+"F2.wireOp",EDGE,"E2.sketch_text.stroke-50"),sQuery(id+"F2.wireOp",EDGE,"E2.sketch_text.stroke-51"),sQuery(id+"F2.wireOp",EDGE,"E2.sketch_text.stroke-52"),sQuery(id+"F2.wireOp",EDGE,"E2.sketch_text.stroke-53"),sQuery(id+"F2.wireOp",EDGE,"E2.sketch_text.stroke-54"),sQuery(id+"F2.wireOp",EDGE,"E2.sketch_text.stroke-55"),sQuery(id+"F2.wireOp",EDGE,"E2.sketch_text.stroke-56"),sQuery(id+"F2.wireOp",EDGE,"E2.sketch_text.stroke-57"),sQuery(id+"F2.wireOp",EDGE,"E2.sketch_text.stroke-58"),sQuery(id+"F2.wireOp",EDGE,"E2.sketch_text.stroke-59"),sQuery(id+"F2.wireOp",EDGE,"E2.sketch_text.stroke-60"),sQuery(id+"F2.wireOp",EDGE,"E2.sketch_text.stroke-61"),sQuery(id+"F2.wireOp",EDGE,"E2.sketch_text.stroke-62"),sQuery(id+"F2.wireOp",EDGE,"E2.sketch_text.stroke-63"),sQuery(id+"F2.wireOp",EDGE,"E2.sketch_text.stroke-64"),sQuery(id+"F2.wireOp",EDGE,"E2.sketch_text.stroke-65"),sQuery(id+"F2.wireOp",EDGE,"E2.sketch_text.stroke-66"),sQuery(id+"F2.wireOp",EDGE,"E2.sketch_text.stroke-67"),sQuery(id+"F2.wireOp",EDGE,"E2.sketch_text.stroke-68"),sQuery(id+"F2.wireOp",EDGE,"E2.sketch_text.stroke-69"),sQuery(id+"F2.wireOp",EDGE,"E2.sketch_text.stroke-70"),sQuery(id+"F2.wireOp",EDGE,"E2.sketch_text.stroke-71"),sQuery(id+"F2.wireOp",EDGE,"E2.sketch_text.stroke-72"),sQuery(id+"F2.wireOp",EDGE,"E2.sketch_text.stroke-73"),sQuery(id+"F2.wireOp",EDGE,"E2.sketch_text.stroke-74"),sQuery(id+"F2.wireOp",EDGE,"E2.sketch_text.stroke-75"),sQuery(id+"F2.wireOp",EDGE,"E2.sketch_text.stroke-76"),sQuery(id+"F2.wireOp",EDGE,"E2.sketch_text.stroke-77"),sQuery(id+"F2.wireOp",EDGE,"E2.sketch_text.stroke-78"),sQuery(id+"F2.wireOp",EDGE,"E2.sketch_text.stroke-79"),sQuery(id+"F2.wireOp",EDGE,"E2.sketch_text.stroke-80"),sQuery(id+"F2.wireOp",EDGE,"E2.sketch_text.stroke-81"),sQuery(id+"F2.wireOp",EDGE,"E2.sketch_text.stroke-82"),sQuery(id+"F2.wireOp",EDGE,"E2.sketch_text.stroke-83"),sQuery(id+"F2.wireOp",EDGE,"E2.sketch_text.stroke-84"),sQuery(id+"F2.wireOp",EDGE,"E2.sketch_text.stroke-85"),sQuery(id+"F2.wireOp",EDGE,"E2.sketch_text.stroke-86"),sQuery(id+"F2.wireOp",EDGE,"E2.sketch_text.stroke-87"),sQuery(id+"F2.wireOp",EDGE,"E2.sketch_text.stroke-88"),sQuery(id+"F2.wireOp",EDGE,"E2.sketch_text.stroke-89"),sQuery(id+"F2.wireOp",EDGE,"E2.sketch_text.stroke-90"),sQuery(id+"F2.wireOp",EDGE,"E2.sketch_text.stroke-91"),sQuery(id+"F2.wireOp",EDGE,"E2.sketch_text.stroke-92"),sQuery(id+"F2.wireOp",EDGE,"E2.sketch_text.stroke-93"),sQuery(id+"F2.wireOp",EDGE,"E2.sketch_text.stroke-94"),sQuery(id+"F2.wireOp",EDGE,"E2.sketch_text.stroke-95"),sQuery(id+"F2.wireOp",EDGE,"E2.sketch_text.stroke-96"),sQuery(id+"F2.wireOp",EDGE,"E2.sketch_text.stroke-97"),sQuery(id+"F2.wireOp",EDGE,"E2.sketch_text.stroke-98"),sQuery(id+"F2.wireOp",EDGE,"E2.sketch_text.stroke-99"),sQuery(id+"F2.wireOp",EDGE,"E2.sketch_text.stroke-100"),sQuery(id+"F2.wireOp",EDGE,"E2.sketch_text.stroke-101"),sQuery(id+"F2.wireOp",EDGE,"E2.sketch_text.stroke-102"),sQuery(id+"F2.wireOp",EDGE,"E2.sketch_text.stroke-103"),sQuery(id+"F2.wireOp",EDGE,"E2.sketch_text.stroke-104"),sQuery(id+"F2.wireOp",EDGE,"E2.sketch_text.stroke-105"),sQuery(id+"F2.wireOp",EDGE,"E2.sketch_text.stroke-106"),sQuery(id+"F2.wireOp",EDGE,"E2.sketch_text.stroke-107"),sQuery(id+"F2.wireOp",EDGE,"E2.sketch_text.stroke-108"),sQuery(id+"F2.wireOp",EDGE,"E2.sketch_text.stroke-109"),sQuery(id+"F2.wireOp",EDGE,"E2.sketch_text.stroke-110"),sQuery(id+"F2.wireOp",EDGE,"E2.sketch_text.stroke-111"),sQuery(id+"F2.wireOp",EDGE,"E2.sketch_text.stroke-112"),sQuery(id+"F2.wireOp",EDGE,"E2.sketch_text.stroke-113"),sQuery(id+"F2.wireOp",EDGE,"E2.sketch_text.stroke-114"),sQuery(id+"F2.wireOp",EDGE,"E2.sketch_text.stroke-115"),sQuery(id+"F2.wireOp",EDGE,"E2.sketch_text.stroke-116"),sQuery(id+"F2.wireOp",EDGE,"E2.sketch_text.stroke-117"),sQuery(id+"F2.wireOp",EDGE,"E2.sketch_text.stroke-118"),sQuery(id+"F2.wireOp",EDGE,"E2.sketch_text.stroke-119"),sQuery(id+"F2.wireOp",EDGE,"E2.sketch_text.stroke-120"),sQuery(id+"F2.wireOp",EDGE,"E2.sketch_text.stroke-121"),sQuery(id+"F2.wireOp",EDGE,"E2.sketch_text.stroke-122"),sQuery(id+"F2.wireOp",EDGE,"E2.sketch_text.stroke-123"),sQuery(id+"F2.wireOp",EDGE,"E2.sketch_text.stroke-124"),sQuery(id+"F2.wireOp",EDGE,"E2.sketch_text.stroke-125"),sQuery(id+"F2.wireOp",EDGE,"E2.sketch_text.stroke-126"),sQuery(id+"F2.wireOp",EDGE,"E2.sketch_text.stroke-127"),sQuery(id+"F2.wireOp",EDGE,"E2.sketch_text.stroke-128"),sQuery(id+"F2.wireOp",EDGE,"E2.sketch_text.stroke-129"),sQuery(id+"F2.wireOp",EDGE,"E2.sketch_text.stroke-130"),sQuery(id+"F2.wireOp",EDGE,"E2.sketch_text.stroke-131"),sQuery(id+"F2.wireOp",EDGE,"E2.sketch_text.stroke-132"),sQuery(id+"F2.wireOp",EDGE,"E2.sketch_text.stroke-133"),sQuery(id+"F2.wireOp",EDGE,"E2.sketch_text.stroke-134"),sQuery(id+"F2.wireOp",EDGE,"E2.sketch_text.stroke-135"),sQuery(id+"F2.wireOp",EDGE,"E2.sketch_text.stroke-136"),sQuery(id+"F2.wireOp",EDGE,"E2.sketch_text.stroke-137"),sQuery(id+"F2.wireOp",EDGE,"E2.sketch_text.stroke-138"),sQuery(id+"F2.wireOp",EDGE,"E2.sketch_text.stroke-139"),sQuery(id+"F2.wireOp",EDGE,"E2.sketch_text.stroke-140"),sQuery(id+"F2.wireOp",EDGE,"E2.sketch_text.stroke-141"),sQuery(id+"F2.wireOp",EDGE,"E2.sketch_text.stroke-142"),sQuery(id+"F2.wireOp",EDGE,"E2.sketch_text.stroke-143"),sQuery(id+"F2.wireOp",EDGE,"E2.sketch_text.stroke-144"),sQuery(id+"F2.wireOp",EDGE,"E2.sketch_text.stroke-145"),sQuery(id+"F2.wireOp",EDGE,"E2.sketch_text.stroke-146"),sQuery(id+"F2.wireOp",EDGE,"E2.sketch_text.stroke-147"),sQuery(id+"F2.wireOp",EDGE,"E2.sketch_text.stroke-148"),sQuery(id+"F2.wireOp",EDGE,"E2.sketch_text.stroke-149"),sQuery(id+"F2.wireOp",EDGE,"E2.sketch_text.stroke-150"),sQuery(id+"F2.wireOp",EDGE,"E2.sketch_text.stroke-151"),sQuery(id+"F2.wireOp",EDGE,"E2.sketch_text.stroke-152"),sQuery(id+"F2.wireOp",EDGE,"E2.sketch_text.stroke-153"),sQuery(id+"F2.wireOp",EDGE,"E2.sketch_text.stroke-154"),sQuery(id+"F2.wireOp",EDGE,"E2.sketch_text.stroke-155"),sQuery(id+"F2.wireOp",EDGE,"E2.sketch_text.stroke-156"),sQuery(id+"F2.wireOp",EDGE,"E2.sketch_text.stroke-157"),sQuery(id+"F2.wireOp",EDGE,"E2.sketch_text.stroke-158"),sQuery(id+"F2.wireOp",EDGE,"E2.sketch_text.stroke-159"),sQuery(id+"F2.wireOp",EDGE,"E2.sketch_text.stroke-160"),sQuery(id+"F2.wireOp",EDGE,"E2.sketch_text.stroke-161"),sQuery(id+"F2.wireOp",EDGE,"E2.sketch_text.stroke-162"),sQuery(id+"F2.wireOp",EDGE,"E2.sketch_text.stroke-163"),sQuery(id+"F2.wireOp",EDGE,"E2.sketch_text.stroke-164"),sQuery(id+"F2.wireOp",EDGE,"E2.sketch_text.stroke-165"),sQuery(id+"F2.wireOp",EDGE,"E2.sketch_text.stroke-166"),sQuery(id+"F2.wireOp",EDGE,"E2.sketch_text.stroke-167"),sQuery(id+"F2.wireOp",EDGE,"E2.sketch_text.stroke-168"),sQuery(id+"F2.wireOp",EDGE,"E2.sketch_text.stroke-169"),sQuery(id+"F2.wireOp",EDGE,"E2.sketch_text.stroke-170"),sQuery(id+"F2.wireOp",EDGE,"E2.sketch_text.stroke-171"),sQuery(id+"F2.wireOp",EDGE,"E2.sketch_text.stroke-172"),sQuery(id+"F2.wireOp",EDGE,"E2.sketch_text.stroke-173"),sQuery(id+"F3.wireOp",EDGE,"E4.sketch_text.stroke-0"),sQuery(id+"F3.wireOp",EDGE,"E4.sketch_text.stroke-1"),sQuery(id+"F3.wireOp",EDGE,"E4.sketch_text.stroke-2"),sQuery(id+"F3.wireOp",EDGE,"E4.sketch_text.stroke-3"),sQuery(id+"F3.wireOp",EDGE,"E4.sketch_text.stroke-4"),sQuery(id+"F3.wireOp",EDGE,"E4.sketch_text.stroke-5"),sQuery(id+"F3.wireOp",EDGE,"E4.sketch_text.stroke-6"),sQuery(id+"F3.wireOp",EDGE,"E4.sketch_text.stroke-7"),sQuery(id+"F3.wireOp",EDGE,"E4.sketch_text.stroke-8"),sQuery(id+"F3.wireOp",EDGE,"E4.sketch_text.stroke-9"),sQuery(id+"F3.wireOp",EDGE,"E4.sketch_text.stroke-10"),sQuery(id+"F3.wireOp",EDGE,"E4.sketch_text.stroke-11"),sQuery(id+"F3.wireOp",EDGE,"E4.sketch_text.stroke-12"),sQuery(id+"F3.wireOp",EDGE,"E4.sketch_text.stroke-13"),sQuery(id+"F3.wireOp",EDGE,"E4.sketch_text.stroke-14"),sQuery(id+"F3.wireOp",EDGE,"E4.sketch_text.stroke-15"),sQuery(id+"F3.wireOp",EDGE,"E4.sketch_text.stroke-16"),sQuery(id+"F3.wireOp",EDGE,"E4.sketch_text.stroke-17"),sQuery(id+"F3.wireOp",EDGE,"E4.sketch_text.stroke-18"),sQuery(id+"F3.wireOp",EDGE,"E4.sketch_text.stroke-19"),sQuery(id+"F3.wireOp",EDGE,"E4.sketch_text.stroke-20"),sQuery(id+"F3.wireOp",EDGE,"E4.sketch_text.stroke-21"),sQuery(id+"F3.wireOp",EDGE,"E4.sketch_text.stroke-22"),sQuery(id+"F3.wireOp",EDGE,"E4.sketch_text.stroke-23"),sQuery(id+"F3.wireOp",EDGE,"E4.sketch_text.stroke-24"),sQuery(id+"F3.wireOp",EDGE,"E4.sketch_text.stroke-25"),sQuery(id+"F3.wireOp",EDGE,"E4.sketch_text.stroke-26"),sQuery(id+"F3.wireOp",EDGE,"E4.sketch_text.stroke-27"),sQuery(id+"F3.wireOp",EDGE,"E4.sketch_text.stroke-28"),sQuery(id+"F3.wireOp",EDGE,"E4.sketch_text.stroke-29"),sQuery(id+"F3.wireOp",EDGE,"E4.sketch_text.stroke-30"),sQuery(id+"F3.wireOp",EDGE,"E4.sketch_text.stroke-31"),sQuery(id+"F3.wireOp",EDGE,"E4.sketch_text.stroke-32"),sQuery(id+"F3.wireOp",EDGE,"E4.sketch_text.stroke-33"),sQuery(id+"F3.wireOp",EDGE,"E4.sketch_text.stroke-34"),sQuery(id+"F3.wireOp",EDGE,"E4.sketch_text.stroke-35"),sQuery(id+"F3.wireOp",EDGE,"E4.sketch_text.stroke-36"),sQuery(id+"F3.wireOp",EDGE,"E4.sketch_text.stroke-37"),sQuery(id+"F3.wireOp",EDGE,"E4.sketch_text.stroke-38"),sQuery(id+"F3.wireOp",EDGE,"E4.sketch_text.stroke-39"),sQuery(id+"F3.wireOp",EDGE,"E4.sketch_text.stroke-40"),sQuery(id+"F3.wireOp",EDGE,"E4.sketch_text.stroke-41"),sQuery(id+"F3.wireOp",EDGE,"E4.sketch_text.stroke-42"),sQuery(id+"F3.wireOp",EDGE,"E4.sketch_text.stroke-43"),sQuery(id+"F3.wireOp",EDGE,"E4.sketch_text.stroke-44"),sQuery(id+"F3.wireOp",EDGE,"E4.sketch_text.stroke-45"),sQuery(id+"F3.wireOp",EDGE,"E4.sketch_text.stroke-46"),sQuery(id+"F3.wireOp",EDGE,"E4.sketch_text.stroke-47"),sQuery(id+"F3.wireOp",EDGE,"E4.sketch_text.stroke-48"),sQuery(id+"F3.wireOp",EDGE,"E4.sketch_text.stroke-49"),sQuery(id+"F3.wireOp",EDGE,"E4.sketch_text.stroke-50"),sQuery(id+"F3.wireOp",EDGE,"E4.sketch_text.stroke-51"),sQuery(id+"F3.wireOp",EDGE,"E4.sketch_text.stroke-52"),sQuery(id+"F3.wireOp",EDGE,"E4.sketch_text.stroke-53"),sQuery(id+"F3.wireOp",EDGE,"E4.sketch_text.stroke-54"),sQuery(id+"F3.wireOp",EDGE,"E4.sketch_text.stroke-55"),sQuery(id+"F3.wireOp",EDGE,"E4.sketch_text.stroke-56"),sQuery(id+"F3.wireOp",EDGE,"E4.sketch_text.stroke-57"),sQuery(id+"F3.wireOp",EDGE,"E4.sketch_text.stroke-58"),sQuery(id+"F3.wireOp",EDGE,"E4.sketch_text.stroke-59"),sQuery(id+"F3.wireOp",EDGE,"E4.sketch_text.stroke-60"),sQuery(id+"F3.wireOp",EDGE,"E4.sketch_text.stroke-61"),sQuery(id+"F3.wireOp",EDGE,"E4.sketch_text.stroke-62"),sQuery(id+"F3.wireOp",EDGE,"E4.sketch_text.stroke-71"),sQuery(id+"F3.wireOp",EDGE,"E4.sketch_text.stroke-72"),sQuery(id+"F3.wireOp",EDGE,"E4.sketch_text.stroke-73"),sQuery(id+"F3.wireOp",EDGE,"E4.sketch_text.stroke-74"),sQuery(id+"F3.wireOp",EDGE,"E4.sketch_text.stroke-75"),sQuery(id+"F3.wireOp",EDGE,"E4.sketch_text.stroke-76"),sQuery(id+"F3.wireOp",EDGE,"E4.sketch_text.stroke-77"),sQuery(id+"F3.wireOp",EDGE,"E4.sketch_text.stroke-78"),sQuery(id+"F3.wireOp",EDGE,"E4.sketch_text.stroke-79"),sQuery(id+"F3.wireOp",EDGE,"E4.sketch_text.stroke-80"),sQuery(id+"F3.wireOp",EDGE,"E4.sketch_text.stroke-81"),sQuery(id+"F3.wireOp",EDGE,"E4.sketch_text.stroke-82"),sQuery(id+"F3.wireOp",EDGE,"E4.sketch_text.stroke-83"),sQuery(id+"F3.wireOp",EDGE,"E4.sketch_text.stroke-84"),sQuery(id+"F3.wireOp",EDGE,"E4.sketch_text.stroke-85"),sQuery(id+"F3.wireOp",EDGE,"E4.sketch_text.stroke-86"),sQuery(id+"F3.wireOp",EDGE,"E4.sketch_text.stroke-87"),sQuery(id+"F3.wireOp",EDGE,"E4.sketch_text.stroke-88"),sQuery(id+"F3.wireOp",EDGE,"E4.sketch_text.stroke-89"),sQuery(id+"F3.wireOp",EDGE,"E4.sketch_text.stroke-90"),sQuery(id+"F3.wireOp",EDGE,"E4.sketch_text.stroke-91"),sQuery(id+"F3.wireOp",EDGE,"E4.sketch_text.stroke-92"),sQuery(id+"F3.wireOp",EDGE,"E4.sketch_text.stroke-93"),sQuery(id+"F3.wireOp",EDGE,"E4.sketch_text.stroke-94"),sQuery(id+"F3.wireOp",EDGE,"E4.sketch_text.stroke-95"),sQuery(id+"F3.wireOp",EDGE,"E4.sketch_text.stroke-96"),sQuery(id+"F3.wireOp",EDGE,"E4.sketch_text.stroke-97"),sQuery(id+"F3.wireOp",EDGE,"E4.sketch_text.stroke-103"),sQuery(id+"F3.wireOp",EDGE,"E4.sketch_text.stroke-104"),sQuery(id+"F3.wireOp",EDGE,"E4.sketch_text.stroke-105"),sQuery(id+"F3.wireOp",EDGE,"E4.sketch_text.stroke-106"),sQuery(id+"F3.wireOp",EDGE,"E4.sketch_text.stroke-107"),sQuery(id+"F3.wireOp",EDGE,"E4.sketch_text.stroke-108"),sQuery(id+"F3.wireOp",EDGE,"E4.sketch_text.stroke-109"),sQuery(id+"F3.wireOp",EDGE,"E4.sketch_text.stroke-110"),sQuery(id+"F3.wireOp",EDGE,"E4.sketch_text.stroke-111"),sQuery(id+"F3.wireOp",EDGE,"E4.sketch_text.stroke-112"),sQuery(id+"F3.wireOp",EDGE,"E4.sketch_text.stroke-113"),sQuery(id+"F3.wireOp",EDGE,"E4.sketch_text.stroke-114"),sQuery(id+"F3.wireOp",EDGE,"E4.sketch_text.stroke-115"),sQuery(id+"F3.wireOp",EDGE,"E4.sketch_text.stroke-116"),sQuery(id+"F3.wireOp",EDGE,"E4.sketch_text.stroke-117"),sQuery(id+"F3.wireOp",EDGE,"E4.sketch_text.stroke-118"),sQuery(id+"F3.wireOp",EDGE,"E4.sketch_text.stroke-119"),sQuery(id+"F3.wireOp",EDGE,"E4.sketch_text.stroke-120"),sQuery(id+"F3.wireOp",EDGE,"E4.sketch_text.stroke-121"),sQuery(id+"F3.wireOp",EDGE,"E4.sketch_text.stroke-122"),sQuery(id+"F3.wireOp",EDGE,"E4.sketch_text.stroke-123"),sQuery(id+"F3.wireOp",EDGE,"E4.sketch_text.stroke-124"),sQuery(id+"F3.wireOp",EDGE,"E4.sketch_text.stroke-125"),sQuery(id+"F3.wireOp",EDGE,"E4.sketch_text.stroke-126"),sQuery(id+"F3.wireOp",EDGE,"E4.sketch_text.stroke-127"),sQuery(id+"F3.wireOp",EDGE,"E4.sketch_text.stroke-128"),sQuery(id+"F3.wireOp",EDGE,"E4.sketch_text.stroke-129"),sQuery(id+"F3.wireOp",EDGE,"E4.sketch_text.stroke-130"),sQuery(id+"F3.wireOp",EDGE,"E4.sketch_text.stroke-131"),sQuery(id+"F3.wireOp",EDGE,"E4.sketch_text.stroke-132"),sQuery(id+"F3.wireOp",EDGE,"E4.sketch_text.stroke-133"),sQuery(id+"F3.wireOp",EDGE,"E4.sketch_text.stroke-134"),sQuery(id+"F3.wireOp",EDGE,"E4.sketch_text.stroke-135"),sQuery(id+"F3.wireOp",EDGE,"E4.sketch_text.stroke-136"),sQuery(id+"F3.wireOp",EDGE,"E4.sketch_text.stroke-137"),sQuery(id+"F3.wireOp",EDGE,"E4.sketch_text.stroke-138"),sQuery(id+"F3.wireOp",EDGE,"E4.sketch_text.stroke-139"),sQuery(id+"F3.wireOp",EDGE,"E4.sketch_text.stroke-140"),sQuery(id+"F3.wireOp",EDGE,"E4.sketch_text.stroke-141"),sQuery(id+"F3.wireOp",EDGE,"E4.sketch_text.stroke-142"),sQuery(id+"F3.wireOp",EDGE,"E4.sketch_text.stroke-143"),sQuery(id+"F3.wireOp",EDGE,"E4.sketch_text.stroke-144"),sQuery(id+"F3.wireOp",EDGE,"E4.sketch_text.stroke-145"),sQuery(id+"F3.wireOp",EDGE,"E4.sketch_text.stroke-146"),sQuery(id+"F3.wireOp",EDGE,"E4.sketch_text.stroke-147"),sQuery(id+"F3.wireOp",EDGE,"E4.sketch_text.stroke-148"),sQuery(id+"F3.wireOp",EDGE,"E4.sketch_text.stroke-149"),sQuery(id+"F3.wireOp",EDGE,"E4.sketch_text.stroke-150"),sQuery(id+"F3.wireOp",EDGE,"E4.sketch_text.stroke-151"),sQuery(id+"F3.wireOp",EDGE,"E4.sketch_text.stroke-152"),sQuery(id+"F3.wireOp",EDGE,"E4.sketch_text.stroke-153"),sQuery(id+"F3.wireOp",EDGE,"E4.sketch_text.stroke-159"),sQuery(id+"F3.wireOp",EDGE,"E4.sketch_text.stroke-160"),sQuery(id+"F3.wireOp",EDGE,"E4.sketch_text.stroke-161"),sQuery(id+"F3.wireOp",EDGE,"E4.sketch_text.stroke-162"),sQuery(id+"F3.wireOp",EDGE,"E4.sketch_text.stroke-163"),sQuery(id+"F3.wireOp",EDGE,"E4.sketch_text.stroke-164"),sQuery(id+"F3.wireOp",EDGE,"E4.sketch_text.stroke-165"),sQuery(id+"F3.wireOp",EDGE,"E4.sketch_text.stroke-166"),sQuery(id+"F3.wireOp",EDGE,"E4.sketch_text.stroke-167"),sQuery(id+"F3.wireOp",EDGE,"E4.sketch_text.stroke-168"),sQuery(id+"F3.wireOp",EDGE,"E4.sketch_text.stroke-169"),sQuery(id+"F3.wireOp",EDGE,"E4.sketch_text.stroke-170"),sQuery(id+"F3.wireOp",EDGE,"E4.sketch_text.stroke-171"),sQuery(id+"F3.wireOp",EDGE,"E4.sketch_text.stroke-172"),sQuery(id+"F3.wireOp",EDGE,"E4.sketch_text.stroke-173"),sQuery(id+"F3.wireOp",EDGE,"E4.sketch_text.stroke-174"),sQuery(id+"F3.wireOp",EDGE,"E4.sketch_text.stroke-175"),sQuery(id+"F3.wireOp",EDGE,"E4.sketch_text.stroke-176"),sQuery(id+"F3.wireOp",EDGE,"E4.sketch_text.stroke-177"),sQuery(id+"F3.wireOp",EDGE,"E4.sketch_text.stroke-178"),sQuery(id+"F3.wireOp",EDGE,"E4.sketch_text.stroke-179"),sQuery(id+"F3.wireOp",EDGE,"E4.sketch_text.stroke-180"),sQuery(id+"F5.wireOp",EDGE,"8007402e-1a4e-4a06-85a5-2af08e553504"),subQ2])],"isStart":true}),makeQuery(id+"F6.opExtrude","SWEPT_FACE",FACE,{"disambiguationData":[OSD([subQ2])]})])],"derivedFrom":makeQuery(id+"F6.opExtrude","CAP_EDGE",EDGE,{"disambiguationData":[OSD([subQ2])],"isStart":true})});}
            var Q8;
            Q8=makeQuery(id+"F1.opExtrude","CAP_EDGE",EDGE,{"disambiguationData":[OSD([sQuery(id+"F0.wireOp",EDGE,"E0.right")])],"isStart":false});
            var Q9;
            {var subQ0=sQuery(id+"F0.wireOp",EDGE,"E0.top");var subQ1=sQuery(id+"F0.wireOp",EDGE,"E0.bottom");var subQ2=sQuery(id+"F5.wireOp",EDGE,"6ee83ff3-586e-4dbe-aaea-af71240543bd");Q9=makeQuery(id+"F6.boolean.opBoolean","SPLIT",EDGE,{"disambiguationData":[TD([makeQuery(id+"F1.opExtrude","CAP_FACE",FACE,{"disambiguationData":[OSD([subQ1,subQ0,sQuery(id+"F0.wireOp",EDGE,"E0.left"),sQuery(id+"F0.wireOp",EDGE,"E0.right")])],"isStart":false}),makeQuery(id+"F1.opExtrude","SWEPT_FACE",FACE,{"disambiguationData":[OSD([subQ0])]}),makeQuery(id+"F6.opExtrude","CAP_FACE",FACE,{"disambiguationData":[OSD([subQ1,sQuery(id+"F2.wireOp",EDGE,"E2.sketch_text.stroke-0"),sQuery(id+"F2.wireOp",EDGE,"E2.sketch_text.stroke-1"),sQuery(id+"F2.wireOp",EDGE,"E2.sketch_text.stroke-2"),sQuery(id+"F2.wireOp",EDGE,"E2.sketch_text.stroke-3"),sQuery(id+"F2.wireOp",EDGE,"E2.sketch_text.stroke-4"),sQuery(id+"F2.wireOp",EDGE,"E2.sketch_text.stroke-5"),sQuery(id+"F2.wireOp",EDGE,"E2.sketch_text.stroke-6"),sQuery(id+"F2.wireOp",EDGE,"E2.sketch_text.stroke-7"),sQuery(id+"F2.wireOp",EDGE,"E2.sketch_text.stroke-8"),sQuery(id+"F2.wireOp",EDGE,"E2.sketch_text.stroke-9"),sQuery(id+"F2.wireOp",EDGE,"E2.sketch_text.stroke-10"),sQuery(id+"F2.wireOp",EDGE,"E2.sketch_text.stroke-11"),sQuery(id+"F2.wireOp",EDGE,"E2.sketch_text.stroke-12"),sQuery(id+"F2.wireOp",EDGE,"E2.sketch_text.stroke-13"),sQuery(id+"F2.wireOp",EDGE,"E2.sketch_text.stroke-14"),sQuery(id+"F2.wireOp",EDGE,"E2.sketch_text.stroke-15"),sQuery(id+"F2.wireOp",EDGE,"E2.sketch_text.stroke-16"),sQuery(id+"F2.wireOp",EDGE,"E2.sketch_text.stroke-17"),sQuery(id+"F2.wireOp",EDGE,"E2.sketch_text.stroke-18"),sQuery(id+"F2.wireOp",EDGE,"E2.sketch_text.stroke-19"),sQuery(id+"F2.wireOp",EDGE,"E2.sketch_text.stroke-20"),sQuery(id+"F2.wireOp",EDGE,"E2.sketch_text.stroke-21"),sQuery(id+"F2.wireOp",EDGE,"E2.sketch_text.stroke-22"),sQuery(id+"F2.wireOp",EDGE,"E2.sketch_text.stroke-23"),sQuery(id+"F2.wireOp",EDGE,"E2.sketch_text.stroke-24"),sQuery(id+"F2.wireOp",EDGE,"E2.sketch_text.stroke-25"),sQuery(id+"F2.wireOp",EDGE,"E2.sketch_text.stroke-26"),sQuery(id+"F2.wireOp",EDGE,"E2.sketch_text.stroke-27"),sQuery(id+"F2.wireOp",EDGE,"E2.sketch_text.stroke-28"),sQuery(id+"F2.wireOp",EDGE,"E2.sketch_text.stroke-29"),sQuery(id+"F2.wireOp",EDGE,"E2.sketch_text.stroke-30"),sQuery(id+"F2.wireOp",EDGE,"E2.sketch_text.stroke-31"),sQuery(id+"F2.wireOp",EDGE,"E2.sketch_text.stroke-32"),sQuery(id+"F2.wireOp",EDGE,"E2.sketch_text.stroke-33"),sQuery(id+"F2.wireOp",EDGE,"E2.sketch_text.stroke-34"),sQuery(id+"F2.wireOp",EDGE,"E2.sketch_text.stroke-35"),sQuery(id+"F2.wireOp",EDGE,"E2.sketch_text.stroke-36"),sQuery(id+"F2.wireOp",EDGE,"E2.sketch_text.stroke-37"),sQuery(id+"F2.wireOp",EDGE,"E2.sketch_text.stroke-38"),sQuery(id+"F2.wireOp",EDGE,"E2.sketch_text.stroke-39"),sQuery(id+"F2.wireOp",EDGE,"E2.sketch_text.stroke-40"),sQuery(id+"F2.wireOp",EDGE,"E2.sketch_text.stroke-41"),sQuery(id+"F2.wireOp",EDGE,"E2.sketch_text.stroke-42"),sQuery(id+"F2.wireOp",EDGE,"E2.sketch_text.stroke-43"),sQuery(id+"F2.wireOp",EDGE,"E2.sketch_text.stroke-44"),sQuery(id+"F2.wireOp",EDGE,"E2.sketch_text.stroke-45"),sQuery(id+"F2.wireOp",EDGE,"E2.sketch_text.stroke-46"),sQuery(id+"F2.wireOp",EDGE,"E2.sketch_text.stroke-47"),sQuery(id+"F2.wireOp",EDGE,"E2.sketch_text.stroke-48"),sQuery(id+"F2.wireOp",EDGE,"E2.sketch_text.stroke-49"),sQuery(id+"F2.wireOp",EDGE,"E2.sketch_text.stroke-50"),sQuery(id+"F2.wireOp",EDGE,"E2.sketch_text.stroke-51"),sQuery(id+"F2.wireOp",EDGE,"E2.sketch_text.stroke-52"),sQuery(id+"F2.wireOp",EDGE,"E2.sketch_text.stroke-53"),sQuery(id+"F2.wireOp",EDGE,"E2.sketch_text.stroke-54"),sQuery(id+"F2.wireOp",EDGE,"E2.sketch_text.stroke-55"),sQuery(id+"F2.wireOp",EDGE,"E2.sketch_text.stroke-56"),sQuery(id+"F2.wireOp",EDGE,"E2.sketch_text.stroke-57"),sQuery(id+"F2.wireOp",EDGE,"E2.sketch_text.stroke-58"),sQuery(id+"F2.wireOp",EDGE,"E2.sketch_text.stroke-59"),sQuery(id+"F2.wireOp",EDGE,"E2.sketch_text.stroke-60"),sQuery(id+"F2.wireOp",EDGE,"E2.sketch_text.stroke-61"),sQuery(id+"F2.wireOp",EDGE,"E2.sketch_text.stroke-62"),sQuery(id+"F2.wireOp",EDGE,"E2.sketch_text.stroke-63"),sQuery(id+"F2.wireOp",EDGE,"E2.sketch_text.stroke-64"),sQuery(id+"F2.wireOp",EDGE,"E2.sketch_text.stroke-65"),sQuery(id+"F2.wireOp",EDGE,"E2.sketch_text.stroke-66"),sQuery(id+"F2.wireOp",EDGE,"E2.sketch_text.stroke-67"),sQuery(id+"F2.wireOp",EDGE,"E2.sketch_text.stroke-68"),sQuery(id+"F2.wireOp",EDGE,"E2.sketch_text.stroke-69"),sQuery(id+"F2.wireOp",EDGE,"E2.sketch_text.stroke-70"),sQuery(id+"F2.wireOp",EDGE,"E2.sketch_text.stroke-71"),sQuery(id+"F2.wireOp",EDGE,"E2.sketch_text.stroke-72"),sQuery(id+"F2.wireOp",EDGE,"E2.sketch_text.stroke-73"),sQuery(id+"F2.wireOp",EDGE,"E2.sketch_text.stroke-74"),sQuery(id+"F2.wireOp",EDGE,"E2.sketch_text.stroke-75"),sQuery(id+"F2.wireOp",EDGE,"E2.sketch_text.stroke-76"),sQuery(id+"F2.wireOp",EDGE,"E2.sketch_text.stroke-77"),sQuery(id+"F2.wireOp",EDGE,"E2.sketch_text.stroke-78"),sQuery(id+"F2.wireOp",EDGE,"E2.sketch_text.stroke-79"),sQuery(id+"F2.wireOp",EDGE,"E2.sketch_text.stroke-80"),sQuery(id+"F2.wireOp",EDGE,"E2.sketch_text.stroke-81"),sQuery(id+"F2.wireOp",EDGE,"E2.sketch_text.stroke-82"),sQuery(id+"F2.wireOp",EDGE,"E2.sketch_text.stroke-83"),sQuery(id+"F2.wireOp",EDGE,"E2.sketch_text.stroke-84"),sQuery(id+"F2.wireOp",EDGE,"E2.sketch_text.stroke-85"),sQuery(id+"F2.wireOp",EDGE,"E2.sketch_text.stroke-86"),sQuery(id+"F2.wireOp",EDGE,"E2.sketch_text.stroke-87"),sQuery(id+"F2.wireOp",EDGE,"E2.sketch_text.stroke-88"),sQuery(id+"F2.wireOp",EDGE,"E2.sketch_text.stroke-89"),sQuery(id+"F2.wireOp",EDGE,"E2.sketch_text.stroke-90"),sQuery(id+"F2.wireOp",EDGE,"E2.sketch_text.stroke-91"),sQuery(id+"F2.wireOp",EDGE,"E2.sketch_text.stroke-92"),sQuery(id+"F2.wireOp",EDGE,"E2.sketch_text.stroke-93"),sQuery(id+"F2.wireOp",EDGE,"E2.sketch_text.stroke-94"),sQuery(id+"F2.wireOp",EDGE,"E2.sketch_text.stroke-95"),sQuery(id+"F2.wireOp",EDGE,"E2.sketch_text.stroke-96"),sQuery(id+"F2.wireOp",EDGE,"E2.sketch_text.stroke-97"),sQuery(id+"F2.wireOp",EDGE,"E2.sketch_text.stroke-98"),sQuery(id+"F2.wireOp",EDGE,"E2.sketch_text.stroke-99"),sQuery(id+"F2.wireOp",EDGE,"E2.sketch_text.stroke-100"),sQuery(id+"F2.wireOp",EDGE,"E2.sketch_text.stroke-101"),sQuery(id+"F2.wireOp",EDGE,"E2.sketch_text.stroke-102"),sQuery(id+"F2.wireOp",EDGE,"E2.sketch_text.stroke-103"),sQuery(id+"F2.wireOp",EDGE,"E2.sketch_text.stroke-104"),sQuery(id+"F2.wireOp",EDGE,"E2.sketch_text.stroke-105"),sQuery(id+"F2.wireOp",EDGE,"E2.sketch_text.stroke-106"),sQuery(id+"F2.wireOp",EDGE,"E2.sketch_text.stroke-107"),sQuery(id+"F2.wireOp",EDGE,"E2.sketch_text.stroke-108"),sQuery(id+"F2.wireOp",EDGE,"E2.sketch_text.stroke-109"),sQuery(id+"F2.wireOp",EDGE,"E2.sketch_text.stroke-110"),sQuery(id+"F2.wireOp",EDGE,"E2.sketch_text.stroke-111"),sQuery(id+"F2.wireOp",EDGE,"E2.sketch_text.stroke-112"),sQuery(id+"F2.wireOp",EDGE,"E2.sketch_text.stroke-113"),sQuery(id+"F2.wireOp",EDGE,"E2.sketch_text.stroke-114"),sQuery(id+"F2.wireOp",EDGE,"E2.sketch_text.stroke-115"),sQuery(id+"F2.wireOp",EDGE,"E2.sketch_text.stroke-116"),sQuery(id+"F2.wireOp",EDGE,"E2.sketch_text.stroke-117"),sQuery(id+"F2.wireOp",EDGE,"E2.sketch_text.stroke-118"),sQuery(id+"F2.wireOp",EDGE,"E2.sketch_text.stroke-119"),sQuery(id+"F2.wireOp",EDGE,"E2.sketch_text.stroke-120"),sQuery(id+"F2.wireOp",EDGE,"E2.sketch_text.stroke-121"),sQuery(id+"F2.wireOp",EDGE,"E2.sketch_text.stroke-122"),sQuery(id+"F2.wireOp",EDGE,"E2.sketch_text.stroke-123"),sQuery(id+"F2.wireOp",EDGE,"E2.sketch_text.stroke-124"),sQuery(id+"F2.wireOp",EDGE,"E2.sketch_text.stroke-125"),sQuery(id+"F2.wireOp",EDGE,"E2.sketch_text.stroke-126"),sQuery(id+"F2.wireOp",EDGE,"E2.sketch_text.stroke-127"),sQuery(id+"F2.wireOp",EDGE,"E2.sketch_text.stroke-128"),sQuery(id+"F2.wireOp",EDGE,"E2.sketch_text.stroke-129"),sQuery(id+"F2.wireOp",EDGE,"E2.sketch_text.stroke-130"),sQuery(id+"F2.wireOp",EDGE,"E2.sketch_text.stroke-131"),sQuery(id+"F2.wireOp",EDGE,"E2.sketch_text.stroke-132"),sQuery(id+"F2.wireOp",EDGE,"E2.sketch_text.stroke-133"),sQuery(id+"F2.wireOp",EDGE,"E2.sketch_text.stroke-134"),sQuery(id+"F2.wireOp",EDGE,"E2.sketch_text.stroke-135"),sQuery(id+"F2.wireOp",EDGE,"E2.sketch_text.stroke-136"),sQuery(id+"F2.wireOp",EDGE,"E2.sketch_text.stroke-137"),sQuery(id+"F2.wireOp",EDGE,"E2.sketch_text.stroke-138"),sQuery(id+"F2.wireOp",EDGE,"E2.sketch_text.stroke-139"),sQuery(id+"F2.wireOp",EDGE,"E2.sketch_text.stroke-140"),sQuery(id+"F2.wireOp",EDGE,"E2.sketch_text.stroke-141"),sQuery(id+"F2.wireOp",EDGE,"E2.sketch_text.stroke-142"),sQuery(id+"F2.wireOp",EDGE,"E2.sketch_text.stroke-143"),sQuery(id+"F2.wireOp",EDGE,"E2.sketch_text.stroke-144"),sQuery(id+"F2.wireOp",EDGE,"E2.sketch_text.stroke-145"),sQuery(id+"F2.wireOp",EDGE,"E2.sketch_text.stroke-146"),sQuery(id+"F2.wireOp",EDGE,"E2.sketch_text.stroke-147"),sQuery(id+"F2.wireOp",EDGE,"E2.sketch_text.stroke-148"),sQuery(id+"F2.wireOp",EDGE,"E2.sketch_text.stroke-149"),sQuery(id+"F2.wireOp",EDGE,"E2.sketch_text.stroke-150"),sQuery(id+"F2.wireOp",EDGE,"E2.sketch_text.stroke-151"),sQuery(id+"F2.wireOp",EDGE,"E2.sketch_text.stroke-152"),sQuery(id+"F2.wireOp",EDGE,"E2.sketch_text.stroke-153"),sQuery(id+"F2.wireOp",EDGE,"E2.sketch_text.stroke-154"),sQuery(id+"F2.wireOp",EDGE,"E2.sketch_text.stroke-155"),sQuery(id+"F2.wireOp",EDGE,"E2.sketch_text.stroke-156"),sQuery(id+"F2.wireOp",EDGE,"E2.sketch_text.stroke-157"),sQuery(id+"F2.wireOp",EDGE,"E2.sketch_text.stroke-158"),sQuery(id+"F2.wireOp",EDGE,"E2.sketch_text.stroke-159"),sQuery(id+"F2.wireOp",EDGE,"E2.sketch_text.stroke-160"),sQuery(id+"F2.wireOp",EDGE,"E2.sketch_text.stroke-161"),sQuery(id+"F2.wireOp",EDGE,"E2.sketch_text.stroke-162"),sQuery(id+"F2.wireOp",EDGE,"E2.sketch_text.stroke-163"),sQuery(id+"F2.wireOp",EDGE,"E2.sketch_text.stroke-164"),sQuery(id+"F2.wireOp",EDGE,"E2.sketch_text.stroke-165"),sQuery(id+"F2.wireOp",EDGE,"E2.sketch_text.stroke-166"),sQuery(id+"F2.wireOp",EDGE,"E2.sketch_text.stroke-167"),sQuery(id+"F2.wireOp",EDGE,"E2.sketch_text.stroke-168"),sQuery(id+"F2.wireOp",EDGE,"E2.sketch_text.stroke-169"),sQuery(id+"F2.wireOp",EDGE,"E2.sketch_text.stroke-170"),sQuery(id+"F2.wireOp",EDGE,"E2.sketch_text.stroke-171"),sQuery(id+"F2.wireOp",EDGE,"E2.sketch_text.stroke-172"),sQuery(id+"F2.wireOp",EDGE,"E2.sketch_text.stroke-173"),sQuery(id+"F3.wireOp",EDGE,"E4.sketch_text.stroke-0"),sQuery(id+"F3.wireOp",EDGE,"E4.sketch_text.stroke-1"),sQuery(id+"F3.wireOp",EDGE,"E4.sketch_text.stroke-2"),sQuery(id+"F3.wireOp",EDGE,"E4.sketch_text.stroke-3"),sQuery(id+"F3.wireOp",EDGE,"E4.sketch_text.stroke-4"),sQuery(id+"F3.wireOp",EDGE,"E4.sketch_text.stroke-5"),sQuery(id+"F3.wireOp",EDGE,"E4.sketch_text.stroke-6"),sQuery(id+"F3.wireOp",EDGE,"E4.sketch_text.stroke-7"),sQuery(id+"F3.wireOp",EDGE,"E4.sketch_text.stroke-8"),sQuery(id+"F3.wireOp",EDGE,"E4.sketch_text.stroke-9"),sQuery(id+"F3.wireOp",EDGE,"E4.sketch_text.stroke-10"),sQuery(id+"F3.wireOp",EDGE,"E4.sketch_text.stroke-11"),sQuery(id+"F3.wireOp",EDGE,"E4.sketch_text.stroke-12"),sQuery(id+"F3.wireOp",EDGE,"E4.sketch_text.stroke-13"),sQuery(id+"F3.wireOp",EDGE,"E4.sketch_text.stroke-14"),sQuery(id+"F3.wireOp",EDGE,"E4.sketch_text.stroke-15"),sQuery(id+"F3.wireOp",EDGE,"E4.sketch_text.stroke-16"),sQuery(id+"F3.wireOp",EDGE,"E4.sketch_text.stroke-17"),sQuery(id+"F3.wireOp",EDGE,"E4.sketch_text.stroke-18"),sQuery(id+"F3.wireOp",EDGE,"E4.sketch_text.stroke-19"),sQuery(id+"F3.wireOp",EDGE,"E4.sketch_text.stroke-20"),sQuery(id+"F3.wireOp",EDGE,"E4.sketch_text.stroke-21"),sQuery(id+"F3.wireOp",EDGE,"E4.sketch_text.stroke-22"),sQuery(id+"F3.wireOp",EDGE,"E4.sketch_text.stroke-23"),sQuery(id+"F3.wireOp",EDGE,"E4.sketch_text.stroke-24"),sQuery(id+"F3.wireOp",EDGE,"E4.sketch_text.stroke-25"),sQuery(id+"F3.wireOp",EDGE,"E4.sketch_text.stroke-26"),sQuery(id+"F3.wireOp",EDGE,"E4.sketch_text.stroke-27"),sQuery(id+"F3.wireOp",EDGE,"E4.sketch_text.stroke-28"),sQuery(id+"F3.wireOp",EDGE,"E4.sketch_text.stroke-29"),sQuery(id+"F3.wireOp",EDGE,"E4.sketch_text.stroke-30"),sQuery(id+"F3.wireOp",EDGE,"E4.sketch_text.stroke-31"),sQuery(id+"F3.wireOp",EDGE,"E4.sketch_text.stroke-32"),sQuery(id+"F3.wireOp",EDGE,"E4.sketch_text.stroke-33"),sQuery(id+"F3.wireOp",EDGE,"E4.sketch_text.stroke-34"),sQuery(id+"F3.wireOp",EDGE,"E4.sketch_text.stroke-35"),sQuery(id+"F3.wireOp",EDGE,"E4.sketch_text.stroke-36"),sQuery(id+"F3.wireOp",EDGE,"E4.sketch_text.stroke-37"),sQuery(id+"F3.wireOp",EDGE,"E4.sketch_text.stroke-38"),sQuery(id+"F3.wireOp",EDGE,"E4.sketch_text.stroke-39"),sQuery(id+"F3.wireOp",EDGE,"E4.sketch_text.stroke-40"),sQuery(id+"F3.wireOp",EDGE,"E4.sketch_text.stroke-41"),sQuery(id+"F3.wireOp",EDGE,"E4.sketch_text.stroke-42"),sQuery(id+"F3.wireOp",EDGE,"E4.sketch_text.stroke-43"),sQuery(id+"F3.wireOp",EDGE,"E4.sketch_text.stroke-44"),sQuery(id+"F3.wireOp",EDGE,"E4.sketch_text.stroke-45"),sQuery(id+"F3.wireOp",EDGE,"E4.sketch_text.stroke-46"),sQuery(id+"F3.wireOp",EDGE,"E4.sketch_text.stroke-47"),sQuery(id+"F3.wireOp",EDGE,"E4.sketch_text.stroke-48"),sQuery(id+"F3.wireOp",EDGE,"E4.sketch_text.stroke-49"),sQuery(id+"F3.wireOp",EDGE,"E4.sketch_text.stroke-50"),sQuery(id+"F3.wireOp",EDGE,"E4.sketch_text.stroke-51"),sQuery(id+"F3.wireOp",EDGE,"E4.sketch_text.stroke-52"),sQuery(id+"F3.wireOp",EDGE,"E4.sketch_text.stroke-53"),sQuery(id+"F3.wireOp",EDGE,"E4.sketch_text.stroke-54"),sQuery(id+"F3.wireOp",EDGE,"E4.sketch_text.stroke-55"),sQuery(id+"F3.wireOp",EDGE,"E4.sketch_text.stroke-56"),sQuery(id+"F3.wireOp",EDGE,"E4.sketch_text.stroke-57"),sQuery(id+"F3.wireOp",EDGE,"E4.sketch_text.stroke-58"),sQuery(id+"F3.wireOp",EDGE,"E4.sketch_text.stroke-59"),sQuery(id+"F3.wireOp",EDGE,"E4.sketch_text.stroke-60"),sQuery(id+"F3.wireOp",EDGE,"E4.sketch_text.stroke-61"),sQuery(id+"F3.wireOp",EDGE,"E4.sketch_text.stroke-62"),sQuery(id+"F3.wireOp",EDGE,"E4.sketch_text.stroke-71"),sQuery(id+"F3.wireOp",EDGE,"E4.sketch_text.stroke-72"),sQuery(id+"F3.wireOp",EDGE,"E4.sketch_text.stroke-73"),sQuery(id+"F3.wireOp",EDGE,"E4.sketch_text.stroke-74"),sQuery(id+"F3.wireOp",EDGE,"E4.sketch_text.stroke-75"),sQuery(id+"F3.wireOp",EDGE,"E4.sketch_text.stroke-76"),sQuery(id+"F3.wireOp",EDGE,"E4.sketch_text.stroke-77"),sQuery(id+"F3.wireOp",EDGE,"E4.sketch_text.stroke-78"),sQuery(id+"F3.wireOp",EDGE,"E4.sketch_text.stroke-79"),sQuery(id+"F3.wireOp",EDGE,"E4.sketch_text.stroke-80"),sQuery(id+"F3.wireOp",EDGE,"E4.sketch_text.stroke-81"),sQuery(id+"F3.wireOp",EDGE,"E4.sketch_text.stroke-82"),sQuery(id+"F3.wireOp",EDGE,"E4.sketch_text.stroke-83"),sQuery(id+"F3.wireOp",EDGE,"E4.sketch_text.stroke-84"),sQuery(id+"F3.wireOp",EDGE,"E4.sketch_text.stroke-85"),sQuery(id+"F3.wireOp",EDGE,"E4.sketch_text.stroke-86"),sQuery(id+"F3.wireOp",EDGE,"E4.sketch_text.stroke-87"),sQuery(id+"F3.wireOp",EDGE,"E4.sketch_text.stroke-88"),sQuery(id+"F3.wireOp",EDGE,"E4.sketch_text.stroke-89"),sQuery(id+"F3.wireOp",EDGE,"E4.sketch_text.stroke-90"),sQuery(id+"F3.wireOp",EDGE,"E4.sketch_text.stroke-91"),sQuery(id+"F3.wireOp",EDGE,"E4.sketch_text.stroke-92"),sQuery(id+"F3.wireOp",EDGE,"E4.sketch_text.stroke-93"),sQuery(id+"F3.wireOp",EDGE,"E4.sketch_text.stroke-94"),sQuery(id+"F3.wireOp",EDGE,"E4.sketch_text.stroke-95"),sQuery(id+"F3.wireOp",EDGE,"E4.sketch_text.stroke-96"),sQuery(id+"F3.wireOp",EDGE,"E4.sketch_text.stroke-97"),sQuery(id+"F3.wireOp",EDGE,"E4.sketch_text.stroke-103"),sQuery(id+"F3.wireOp",EDGE,"E4.sketch_text.stroke-104"),sQuery(id+"F3.wireOp",EDGE,"E4.sketch_text.stroke-105"),sQuery(id+"F3.wireOp",EDGE,"E4.sketch_text.stroke-106"),sQuery(id+"F3.wireOp",EDGE,"E4.sketch_text.stroke-107"),sQuery(id+"F3.wireOp",EDGE,"E4.sketch_text.stroke-108"),sQuery(id+"F3.wireOp",EDGE,"E4.sketch_text.stroke-109"),sQuery(id+"F3.wireOp",EDGE,"E4.sketch_text.stroke-110"),sQuery(id+"F3.wireOp",EDGE,"E4.sketch_text.stroke-111"),sQuery(id+"F3.wireOp",EDGE,"E4.sketch_text.stroke-112"),sQuery(id+"F3.wireOp",EDGE,"E4.sketch_text.stroke-113"),sQuery(id+"F3.wireOp",EDGE,"E4.sketch_text.stroke-114"),sQuery(id+"F3.wireOp",EDGE,"E4.sketch_text.stroke-115"),sQuery(id+"F3.wireOp",EDGE,"E4.sketch_text.stroke-116"),sQuery(id+"F3.wireOp",EDGE,"E4.sketch_text.stroke-117"),sQuery(id+"F3.wireOp",EDGE,"E4.sketch_text.stroke-118"),sQuery(id+"F3.wireOp",EDGE,"E4.sketch_text.stroke-119"),sQuery(id+"F3.wireOp",EDGE,"E4.sketch_text.stroke-120"),sQuery(id+"F3.wireOp",EDGE,"E4.sketch_text.stroke-121"),sQuery(id+"F3.wireOp",EDGE,"E4.sketch_text.stroke-122"),sQuery(id+"F3.wireOp",EDGE,"E4.sketch_text.stroke-123"),sQuery(id+"F3.wireOp",EDGE,"E4.sketch_text.stroke-124"),sQuery(id+"F3.wireOp",EDGE,"E4.sketch_text.stroke-125"),sQuery(id+"F3.wireOp",EDGE,"E4.sketch_text.stroke-126"),sQuery(id+"F3.wireOp",EDGE,"E4.sketch_text.stroke-127"),sQuery(id+"F3.wireOp",EDGE,"E4.sketch_text.stroke-128"),sQuery(id+"F3.wireOp",EDGE,"E4.sketch_text.stroke-129"),sQuery(id+"F3.wireOp",EDGE,"E4.sketch_text.stroke-130"),sQuery(id+"F3.wireOp",EDGE,"E4.sketch_text.stroke-131"),sQuery(id+"F3.wireOp",EDGE,"E4.sketch_text.stroke-132"),sQuery(id+"F3.wireOp",EDGE,"E4.sketch_text.stroke-133"),sQuery(id+"F3.wireOp",EDGE,"E4.sketch_text.stroke-134"),sQuery(id+"F3.wireOp",EDGE,"E4.sketch_text.stroke-135"),sQuery(id+"F3.wireOp",EDGE,"E4.sketch_text.stroke-136"),sQuery(id+"F3.wireOp",EDGE,"E4.sketch_text.stroke-137"),sQuery(id+"F3.wireOp",EDGE,"E4.sketch_text.stroke-138"),sQuery(id+"F3.wireOp",EDGE,"E4.sketch_text.stroke-139"),sQuery(id+"F3.wireOp",EDGE,"E4.sketch_text.stroke-140"),sQuery(id+"F3.wireOp",EDGE,"E4.sketch_text.stroke-141"),sQuery(id+"F3.wireOp",EDGE,"E4.sketch_text.stroke-142"),sQuery(id+"F3.wireOp",EDGE,"E4.sketch_text.stroke-143"),sQuery(id+"F3.wireOp",EDGE,"E4.sketch_text.stroke-144"),sQuery(id+"F3.wireOp",EDGE,"E4.sketch_text.stroke-145"),sQuery(id+"F3.wireOp",EDGE,"E4.sketch_text.stroke-146"),sQuery(id+"F3.wireOp",EDGE,"E4.sketch_text.stroke-147"),sQuery(id+"F3.wireOp",EDGE,"E4.sketch_text.stroke-148"),sQuery(id+"F3.wireOp",EDGE,"E4.sketch_text.stroke-149"),sQuery(id+"F3.wireOp",EDGE,"E4.sketch_text.stroke-150"),sQuery(id+"F3.wireOp",EDGE,"E4.sketch_text.stroke-151"),sQuery(id+"F3.wireOp",EDGE,"E4.sketch_text.stroke-152"),sQuery(id+"F3.wireOp",EDGE,"E4.sketch_text.stroke-153"),sQuery(id+"F3.wireOp",EDGE,"E4.sketch_text.stroke-159"),sQuery(id+"F3.wireOp",EDGE,"E4.sketch_text.stroke-160"),sQuery(id+"F3.wireOp",EDGE,"E4.sketch_text.stroke-161"),sQuery(id+"F3.wireOp",EDGE,"E4.sketch_text.stroke-162"),sQuery(id+"F3.wireOp",EDGE,"E4.sketch_text.stroke-163"),sQuery(id+"F3.wireOp",EDGE,"E4.sketch_text.stroke-164"),sQuery(id+"F3.wireOp",EDGE,"E4.sketch_text.stroke-165"),sQuery(id+"F3.wireOp",EDGE,"E4.sketch_text.stroke-166"),sQuery(id+"F3.wireOp",EDGE,"E4.sketch_text.stroke-167"),sQuery(id+"F3.wireOp",EDGE,"E4.sketch_text.stroke-168"),sQuery(id+"F3.wireOp",EDGE,"E4.sketch_text.stroke-169"),sQuery(id+"F3.wireOp",EDGE,"E4.sketch_text.stroke-170"),sQuery(id+"F3.wireOp",EDGE,"E4.sketch_text.stroke-171"),sQuery(id+"F3.wireOp",EDGE,"E4.sketch_text.stroke-172"),sQuery(id+"F3.wireOp",EDGE,"E4.sketch_text.stroke-173"),sQuery(id+"F3.wireOp",EDGE,"E4.sketch_text.stroke-174"),sQuery(id+"F3.wireOp",EDGE,"E4.sketch_text.stroke-175"),sQuery(id+"F3.wireOp",EDGE,"E4.sketch_text.stroke-176"),sQuery(id+"F3.wireOp",EDGE,"E4.sketch_text.stroke-177"),sQuery(id+"F3.wireOp",EDGE,"E4.sketch_text.stroke-178"),sQuery(id+"F3.wireOp",EDGE,"E4.sketch_text.stroke-179"),sQuery(id+"F3.wireOp",EDGE,"E4.sketch_text.stroke-180"),sQuery(id+"F5.wireOp",EDGE,"8007402e-1a4e-4a06-85a5-2af08e553504"),subQ2])],"isStart":true}),makeQuery(id+"F6.opExtrude","SWEPT_FACE",FACE,{"disambiguationData":[OSD([subQ2])]})])],"derivedFrom":makeQuery(id+"F6.opExtrude","CAP_EDGE",EDGE,{"disambiguationData":[OSD([subQ2])],"isStart":true})});}
            var Q10;
            {var subQ0=sQuery(id+"F5.wireOp",EDGE,"8007402e-1a4e-4a06-85a5-2af08e553504");var subQ1=sQuery(id+"F0.wireOp",EDGE,"E0.top");var subQ2=sQuery(id+"F5.wireOp",EDGE,"6ee83ff3-586e-4dbe-aaea-af71240543bd");var subQ3=sQuery(id+"F0.wireOp",EDGE,"E0.bottom");Q10=makeQuery(id+"F6.boolean.opBoolean","SPLIT",EDGE,{"disambiguationData":[TD([makeQuery(id+"F1.opExtrude","CAP_FACE",FACE,{"disambiguationData":[OSD([subQ3,subQ1,sQuery(id+"F0.wireOp",EDGE,"E0.left"),sQuery(id+"F0.wireOp",EDGE,"E0.right")])],"isStart":false}),makeQuery(id+"F1.opExtrude","SWEPT_FACE",FACE,{"disambiguationData":[OSD([subQ1])]}),makeQuery(id+"F6.opExtrude","SWEPT_FACE",FACE,{"disambiguationData":[OSD([subQ0])]}),makeQuery(id+"F6.opExtrude","CAP_FACE",FACE,{"disambiguationData":[OSD([subQ3,sQuery(id+"F2.wireOp",EDGE,"E2.sketch_text.stroke-0"),sQuery(id+"F2.wireOp",EDGE,"E2.sketch_text.stroke-1"),sQuery(id+"F2.wireOp",EDGE,"E2.sketch_text.stroke-2"),sQuery(id+"F2.wireOp",EDGE,"E2.sketch_text.stroke-3"),sQuery(id+"F2.wireOp",EDGE,"E2.sketch_text.stroke-4"),sQuery(id+"F2.wireOp",EDGE,"E2.sketch_text.stroke-5"),sQuery(id+"F2.wireOp",EDGE,"E2.sketch_text.stroke-6"),sQuery(id+"F2.wireOp",EDGE,"E2.sketch_text.stroke-7"),sQuery(id+"F2.wireOp",EDGE,"E2.sketch_text.stroke-8"),sQuery(id+"F2.wireOp",EDGE,"E2.sketch_text.stroke-9"),sQuery(id+"F2.wireOp",EDGE,"E2.sketch_text.stroke-10"),sQuery(id+"F2.wireOp",EDGE,"E2.sketch_text.stroke-11"),sQuery(id+"F2.wireOp",EDGE,"E2.sketch_text.stroke-12"),sQuery(id+"F2.wireOp",EDGE,"E2.sketch_text.stroke-13"),sQuery(id+"F2.wireOp",EDGE,"E2.sketch_text.stroke-14"),sQuery(id+"F2.wireOp",EDGE,"E2.sketch_text.stroke-15"),sQuery(id+"F2.wireOp",EDGE,"E2.sketch_text.stroke-16"),sQuery(id+"F2.wireOp",EDGE,"E2.sketch_text.stroke-17"),sQuery(id+"F2.wireOp",EDGE,"E2.sketch_text.stroke-18"),sQuery(id+"F2.wireOp",EDGE,"E2.sketch_text.stroke-19"),sQuery(id+"F2.wireOp",EDGE,"E2.sketch_text.stroke-20"),sQuery(id+"F2.wireOp",EDGE,"E2.sketch_text.stroke-21"),sQuery(id+"F2.wireOp",EDGE,"E2.sketch_text.stroke-22"),sQuery(id+"F2.wireOp",EDGE,"E2.sketch_text.stroke-23"),sQuery(id+"F2.wireOp",EDGE,"E2.sketch_text.stroke-24"),sQuery(id+"F2.wireOp",EDGE,"E2.sketch_text.stroke-25"),sQuery(id+"F2.wireOp",EDGE,"E2.sketch_text.stroke-26"),sQuery(id+"F2.wireOp",EDGE,"E2.sketch_text.stroke-27"),sQuery(id+"F2.wireOp",EDGE,"E2.sketch_text.stroke-28"),sQuery(id+"F2.wireOp",EDGE,"E2.sketch_text.stroke-29"),sQuery(id+"F2.wireOp",EDGE,"E2.sketch_text.stroke-30"),sQuery(id+"F2.wireOp",EDGE,"E2.sketch_text.stroke-31"),sQuery(id+"F2.wireOp",EDGE,"E2.sketch_text.stroke-32"),sQuery(id+"F2.wireOp",EDGE,"E2.sketch_text.stroke-33"),sQuery(id+"F2.wireOp",EDGE,"E2.sketch_text.stroke-34"),sQuery(id+"F2.wireOp",EDGE,"E2.sketch_text.stroke-35"),sQuery(id+"F2.wireOp",EDGE,"E2.sketch_text.stroke-36"),sQuery(id+"F2.wireOp",EDGE,"E2.sketch_text.stroke-37"),sQuery(id+"F2.wireOp",EDGE,"E2.sketch_text.stroke-38"),sQuery(id+"F2.wireOp",EDGE,"E2.sketch_text.stroke-39"),sQuery(id+"F2.wireOp",EDGE,"E2.sketch_text.stroke-40"),sQuery(id+"F2.wireOp",EDGE,"E2.sketch_text.stroke-41"),sQuery(id+"F2.wireOp",EDGE,"E2.sketch_text.stroke-42"),sQuery(id+"F2.wireOp",EDGE,"E2.sketch_text.stroke-43"),sQuery(id+"F2.wireOp",EDGE,"E2.sketch_text.stroke-44"),sQuery(id+"F2.wireOp",EDGE,"E2.sketch_text.stroke-45"),sQuery(id+"F2.wireOp",EDGE,"E2.sketch_text.stroke-46"),sQuery(id+"F2.wireOp",EDGE,"E2.sketch_text.stroke-47"),sQuery(id+"F2.wireOp",EDGE,"E2.sketch_text.stroke-48"),sQuery(id+"F2.wireOp",EDGE,"E2.sketch_text.stroke-49"),sQuery(id+"F2.wireOp",EDGE,"E2.sketch_text.stroke-50"),sQuery(id+"F2.wireOp",EDGE,"E2.sketch_text.stroke-51"),sQuery(id+"F2.wireOp",EDGE,"E2.sketch_text.stroke-52"),sQuery(id+"F2.wireOp",EDGE,"E2.sketch_text.stroke-53"),sQuery(id+"F2.wireOp",EDGE,"E2.sketch_text.stroke-54"),sQuery(id+"F2.wireOp",EDGE,"E2.sketch_text.stroke-55"),sQuery(id+"F2.wireOp",EDGE,"E2.sketch_text.stroke-56"),sQuery(id+"F2.wireOp",EDGE,"E2.sketch_text.stroke-57"),sQuery(id+"F2.wireOp",EDGE,"E2.sketch_text.stroke-58"),sQuery(id+"F2.wireOp",EDGE,"E2.sketch_text.stroke-59"),sQuery(id+"F2.wireOp",EDGE,"E2.sketch_text.stroke-60"),sQuery(id+"F2.wireOp",EDGE,"E2.sketch_text.stroke-61"),sQuery(id+"F2.wireOp",EDGE,"E2.sketch_text.stroke-62"),sQuery(id+"F2.wireOp",EDGE,"E2.sketch_text.stroke-63"),sQuery(id+"F2.wireOp",EDGE,"E2.sketch_text.stroke-64"),sQuery(id+"F2.wireOp",EDGE,"E2.sketch_text.stroke-65"),sQuery(id+"F2.wireOp",EDGE,"E2.sketch_text.stroke-66"),sQuery(id+"F2.wireOp",EDGE,"E2.sketch_text.stroke-67"),sQuery(id+"F2.wireOp",EDGE,"E2.sketch_text.stroke-68"),sQuery(id+"F2.wireOp",EDGE,"E2.sketch_text.stroke-69"),sQuery(id+"F2.wireOp",EDGE,"E2.sketch_text.stroke-70"),sQuery(id+"F2.wireOp",EDGE,"E2.sketch_text.stroke-71"),sQuery(id+"F2.wireOp",EDGE,"E2.sketch_text.stroke-72"),sQuery(id+"F2.wireOp",EDGE,"E2.sketch_text.stroke-73"),sQuery(id+"F2.wireOp",EDGE,"E2.sketch_text.stroke-74"),sQuery(id+"F2.wireOp",EDGE,"E2.sketch_text.stroke-75"),sQuery(id+"F2.wireOp",EDGE,"E2.sketch_text.stroke-76"),sQuery(id+"F2.wireOp",EDGE,"E2.sketch_text.stroke-77"),sQuery(id+"F2.wireOp",EDGE,"E2.sketch_text.stroke-78"),sQuery(id+"F2.wireOp",EDGE,"E2.sketch_text.stroke-79"),sQuery(id+"F2.wireOp",EDGE,"E2.sketch_text.stroke-80"),sQuery(id+"F2.wireOp",EDGE,"E2.sketch_text.stroke-81"),sQuery(id+"F2.wireOp",EDGE,"E2.sketch_text.stroke-82"),sQuery(id+"F2.wireOp",EDGE,"E2.sketch_text.stroke-83"),sQuery(id+"F2.wireOp",EDGE,"E2.sketch_text.stroke-84"),sQuery(id+"F2.wireOp",EDGE,"E2.sketch_text.stroke-85"),sQuery(id+"F2.wireOp",EDGE,"E2.sketch_text.stroke-86"),sQuery(id+"F2.wireOp",EDGE,"E2.sketch_text.stroke-87"),sQuery(id+"F2.wireOp",EDGE,"E2.sketch_text.stroke-88"),sQuery(id+"F2.wireOp",EDGE,"E2.sketch_text.stroke-89"),sQuery(id+"F2.wireOp",EDGE,"E2.sketch_text.stroke-90"),sQuery(id+"F2.wireOp",EDGE,"E2.sketch_text.stroke-91"),sQuery(id+"F2.wireOp",EDGE,"E2.sketch_text.stroke-92"),sQuery(id+"F2.wireOp",EDGE,"E2.sketch_text.stroke-93"),sQuery(id+"F2.wireOp",EDGE,"E2.sketch_text.stroke-94"),sQuery(id+"F2.wireOp",EDGE,"E2.sketch_text.stroke-95"),sQuery(id+"F2.wireOp",EDGE,"E2.sketch_text.stroke-96"),sQuery(id+"F2.wireOp",EDGE,"E2.sketch_text.stroke-97"),sQuery(id+"F2.wireOp",EDGE,"E2.sketch_text.stroke-98"),sQuery(id+"F2.wireOp",EDGE,"E2.sketch_text.stroke-99"),sQuery(id+"F2.wireOp",EDGE,"E2.sketch_text.stroke-100"),sQuery(id+"F2.wireOp",EDGE,"E2.sketch_text.stroke-101"),sQuery(id+"F2.wireOp",EDGE,"E2.sketch_text.stroke-102"),sQuery(id+"F2.wireOp",EDGE,"E2.sketch_text.stroke-103"),sQuery(id+"F2.wireOp",EDGE,"E2.sketch_text.stroke-104"),sQuery(id+"F2.wireOp",EDGE,"E2.sketch_text.stroke-105"),sQuery(id+"F2.wireOp",EDGE,"E2.sketch_text.stroke-106"),sQuery(id+"F2.wireOp",EDGE,"E2.sketch_text.stroke-107"),sQuery(id+"F2.wireOp",EDGE,"E2.sketch_text.stroke-108"),sQuery(id+"F2.wireOp",EDGE,"E2.sketch_text.stroke-109"),sQuery(id+"F2.wireOp",EDGE,"E2.sketch_text.stroke-110"),sQuery(id+"F2.wireOp",EDGE,"E2.sketch_text.stroke-111"),sQuery(id+"F2.wireOp",EDGE,"E2.sketch_text.stroke-112"),sQuery(id+"F2.wireOp",EDGE,"E2.sketch_text.stroke-113"),sQuery(id+"F2.wireOp",EDGE,"E2.sketch_text.stroke-114"),sQuery(id+"F2.wireOp",EDGE,"E2.sketch_text.stroke-115"),sQuery(id+"F2.wireOp",EDGE,"E2.sketch_text.stroke-116"),sQuery(id+"F2.wireOp",EDGE,"E2.sketch_text.stroke-117"),sQuery(id+"F2.wireOp",EDGE,"E2.sketch_text.stroke-118"),sQuery(id+"F2.wireOp",EDGE,"E2.sketch_text.stroke-119"),sQuery(id+"F2.wireOp",EDGE,"E2.sketch_text.stroke-120"),sQuery(id+"F2.wireOp",EDGE,"E2.sketch_text.stroke-121"),sQuery(id+"F2.wireOp",EDGE,"E2.sketch_text.stroke-122"),sQuery(id+"F2.wireOp",EDGE,"E2.sketch_text.stroke-123"),sQuery(id+"F2.wireOp",EDGE,"E2.sketch_text.stroke-124"),sQuery(id+"F2.wireOp",EDGE,"E2.sketch_text.stroke-125"),sQuery(id+"F2.wireOp",EDGE,"E2.sketch_text.stroke-126"),sQuery(id+"F2.wireOp",EDGE,"E2.sketch_text.stroke-127"),sQuery(id+"F2.wireOp",EDGE,"E2.sketch_text.stroke-128"),sQuery(id+"F2.wireOp",EDGE,"E2.sketch_text.stroke-129"),sQuery(id+"F2.wireOp",EDGE,"E2.sketch_text.stroke-130"),sQuery(id+"F2.wireOp",EDGE,"E2.sketch_text.stroke-131"),sQuery(id+"F2.wireOp",EDGE,"E2.sketch_text.stroke-132"),sQuery(id+"F2.wireOp",EDGE,"E2.sketch_text.stroke-133"),sQuery(id+"F2.wireOp",EDGE,"E2.sketch_text.stroke-134"),sQuery(id+"F2.wireOp",EDGE,"E2.sketch_text.stroke-135"),sQuery(id+"F2.wireOp",EDGE,"E2.sketch_text.stroke-136"),sQuery(id+"F2.wireOp",EDGE,"E2.sketch_text.stroke-137"),sQuery(id+"F2.wireOp",EDGE,"E2.sketch_text.stroke-138"),sQuery(id+"F2.wireOp",EDGE,"E2.sketch_text.stroke-139"),sQuery(id+"F2.wireOp",EDGE,"E2.sketch_text.stroke-140"),sQuery(id+"F2.wireOp",EDGE,"E2.sketch_text.stroke-141"),sQuery(id+"F2.wireOp",EDGE,"E2.sketch_text.stroke-142"),sQuery(id+"F2.wireOp",EDGE,"E2.sketch_text.stroke-143"),sQuery(id+"F2.wireOp",EDGE,"E2.sketch_text.stroke-144"),sQuery(id+"F2.wireOp",EDGE,"E2.sketch_text.stroke-145"),sQuery(id+"F2.wireOp",EDGE,"E2.sketch_text.stroke-146"),sQuery(id+"F2.wireOp",EDGE,"E2.sketch_text.stroke-147"),sQuery(id+"F2.wireOp",EDGE,"E2.sketch_text.stroke-148"),sQuery(id+"F2.wireOp",EDGE,"E2.sketch_text.stroke-149"),sQuery(id+"F2.wireOp",EDGE,"E2.sketch_text.stroke-150"),sQuery(id+"F2.wireOp",EDGE,"E2.sketch_text.stroke-151"),sQuery(id+"F2.wireOp",EDGE,"E2.sketch_text.stroke-152"),sQuery(id+"F2.wireOp",EDGE,"E2.sketch_text.stroke-153"),sQuery(id+"F2.wireOp",EDGE,"E2.sketch_text.stroke-154"),sQuery(id+"F2.wireOp",EDGE,"E2.sketch_text.stroke-155"),sQuery(id+"F2.wireOp",EDGE,"E2.sketch_text.stroke-156"),sQuery(id+"F2.wireOp",EDGE,"E2.sketch_text.stroke-157"),sQuery(id+"F2.wireOp",EDGE,"E2.sketch_text.stroke-158"),sQuery(id+"F2.wireOp",EDGE,"E2.sketch_text.stroke-159"),sQuery(id+"F2.wireOp",EDGE,"E2.sketch_text.stroke-160"),sQuery(id+"F2.wireOp",EDGE,"E2.sketch_text.stroke-161"),sQuery(id+"F2.wireOp",EDGE,"E2.sketch_text.stroke-162"),sQuery(id+"F2.wireOp",EDGE,"E2.sketch_text.stroke-163"),sQuery(id+"F2.wireOp",EDGE,"E2.sketch_text.stroke-164"),sQuery(id+"F2.wireOp",EDGE,"E2.sketch_text.stroke-165"),sQuery(id+"F2.wireOp",EDGE,"E2.sketch_text.stroke-166"),sQuery(id+"F2.wireOp",EDGE,"E2.sketch_text.stroke-167"),sQuery(id+"F2.wireOp",EDGE,"E2.sketch_text.stroke-168"),sQuery(id+"F2.wireOp",EDGE,"E2.sketch_text.stroke-169"),sQuery(id+"F2.wireOp",EDGE,"E2.sketch_text.stroke-170"),sQuery(id+"F2.wireOp",EDGE,"E2.sketch_text.stroke-171"),sQuery(id+"F2.wireOp",EDGE,"E2.sketch_text.stroke-172"),sQuery(id+"F2.wireOp",EDGE,"E2.sketch_text.stroke-173"),sQuery(id+"F3.wireOp",EDGE,"E4.sketch_text.stroke-0"),sQuery(id+"F3.wireOp",EDGE,"E4.sketch_text.stroke-1"),sQuery(id+"F3.wireOp",EDGE,"E4.sketch_text.stroke-2"),sQuery(id+"F3.wireOp",EDGE,"E4.sketch_text.stroke-3"),sQuery(id+"F3.wireOp",EDGE,"E4.sketch_text.stroke-4"),sQuery(id+"F3.wireOp",EDGE,"E4.sketch_text.stroke-5"),sQuery(id+"F3.wireOp",EDGE,"E4.sketch_text.stroke-6"),sQuery(id+"F3.wireOp",EDGE,"E4.sketch_text.stroke-7"),sQuery(id+"F3.wireOp",EDGE,"E4.sketch_text.stroke-8"),sQuery(id+"F3.wireOp",EDGE,"E4.sketch_text.stroke-9"),sQuery(id+"F3.wireOp",EDGE,"E4.sketch_text.stroke-10"),sQuery(id+"F3.wireOp",EDGE,"E4.sketch_text.stroke-11"),sQuery(id+"F3.wireOp",EDGE,"E4.sketch_text.stroke-12"),sQuery(id+"F3.wireOp",EDGE,"E4.sketch_text.stroke-13"),sQuery(id+"F3.wireOp",EDGE,"E4.sketch_text.stroke-14"),sQuery(id+"F3.wireOp",EDGE,"E4.sketch_text.stroke-15"),sQuery(id+"F3.wireOp",EDGE,"E4.sketch_text.stroke-16"),sQuery(id+"F3.wireOp",EDGE,"E4.sketch_text.stroke-17"),sQuery(id+"F3.wireOp",EDGE,"E4.sketch_text.stroke-18"),sQuery(id+"F3.wireOp",EDGE,"E4.sketch_text.stroke-19"),sQuery(id+"F3.wireOp",EDGE,"E4.sketch_text.stroke-20"),sQuery(id+"F3.wireOp",EDGE,"E4.sketch_text.stroke-21"),sQuery(id+"F3.wireOp",EDGE,"E4.sketch_text.stroke-22"),sQuery(id+"F3.wireOp",EDGE,"E4.sketch_text.stroke-23"),sQuery(id+"F3.wireOp",EDGE,"E4.sketch_text.stroke-24"),sQuery(id+"F3.wireOp",EDGE,"E4.sketch_text.stroke-25"),sQuery(id+"F3.wireOp",EDGE,"E4.sketch_text.stroke-26"),sQuery(id+"F3.wireOp",EDGE,"E4.sketch_text.stroke-27"),sQuery(id+"F3.wireOp",EDGE,"E4.sketch_text.stroke-28"),sQuery(id+"F3.wireOp",EDGE,"E4.sketch_text.stroke-29"),sQuery(id+"F3.wireOp",EDGE,"E4.sketch_text.stroke-30"),sQuery(id+"F3.wireOp",EDGE,"E4.sketch_text.stroke-31"),sQuery(id+"F3.wireOp",EDGE,"E4.sketch_text.stroke-32"),sQuery(id+"F3.wireOp",EDGE,"E4.sketch_text.stroke-33"),sQuery(id+"F3.wireOp",EDGE,"E4.sketch_text.stroke-34"),sQuery(id+"F3.wireOp",EDGE,"E4.sketch_text.stroke-35"),sQuery(id+"F3.wireOp",EDGE,"E4.sketch_text.stroke-36"),sQuery(id+"F3.wireOp",EDGE,"E4.sketch_text.stroke-37"),sQuery(id+"F3.wireOp",EDGE,"E4.sketch_text.stroke-38"),sQuery(id+"F3.wireOp",EDGE,"E4.sketch_text.stroke-39"),sQuery(id+"F3.wireOp",EDGE,"E4.sketch_text.stroke-40"),sQuery(id+"F3.wireOp",EDGE,"E4.sketch_text.stroke-41"),sQuery(id+"F3.wireOp",EDGE,"E4.sketch_text.stroke-42"),sQuery(id+"F3.wireOp",EDGE,"E4.sketch_text.stroke-43"),sQuery(id+"F3.wireOp",EDGE,"E4.sketch_text.stroke-44"),sQuery(id+"F3.wireOp",EDGE,"E4.sketch_text.stroke-45"),sQuery(id+"F3.wireOp",EDGE,"E4.sketch_text.stroke-46"),sQuery(id+"F3.wireOp",EDGE,"E4.sketch_text.stroke-47"),sQuery(id+"F3.wireOp",EDGE,"E4.sketch_text.stroke-48"),sQuery(id+"F3.wireOp",EDGE,"E4.sketch_text.stroke-49"),sQuery(id+"F3.wireOp",EDGE,"E4.sketch_text.stroke-50"),sQuery(id+"F3.wireOp",EDGE,"E4.sketch_text.stroke-51"),sQuery(id+"F3.wireOp",EDGE,"E4.sketch_text.stroke-52"),sQuery(id+"F3.wireOp",EDGE,"E4.sketch_text.stroke-53"),sQuery(id+"F3.wireOp",EDGE,"E4.sketch_text.stroke-54"),sQuery(id+"F3.wireOp",EDGE,"E4.sketch_text.stroke-55"),sQuery(id+"F3.wireOp",EDGE,"E4.sketch_text.stroke-56"),sQuery(id+"F3.wireOp",EDGE,"E4.sketch_text.stroke-57"),sQuery(id+"F3.wireOp",EDGE,"E4.sketch_text.stroke-58"),sQuery(id+"F3.wireOp",EDGE,"E4.sketch_text.stroke-59"),sQuery(id+"F3.wireOp",EDGE,"E4.sketch_text.stroke-60"),sQuery(id+"F3.wireOp",EDGE,"E4.sketch_text.stroke-61"),sQuery(id+"F3.wireOp",EDGE,"E4.sketch_text.stroke-62"),sQuery(id+"F3.wireOp",EDGE,"E4.sketch_text.stroke-71"),sQuery(id+"F3.wireOp",EDGE,"E4.sketch_text.stroke-72"),sQuery(id+"F3.wireOp",EDGE,"E4.sketch_text.stroke-73"),sQuery(id+"F3.wireOp",EDGE,"E4.sketch_text.stroke-74"),sQuery(id+"F3.wireOp",EDGE,"E4.sketch_text.stroke-75"),sQuery(id+"F3.wireOp",EDGE,"E4.sketch_text.stroke-76"),sQuery(id+"F3.wireOp",EDGE,"E4.sketch_text.stroke-77"),sQuery(id+"F3.wireOp",EDGE,"E4.sketch_text.stroke-78"),sQuery(id+"F3.wireOp",EDGE,"E4.sketch_text.stroke-79"),sQuery(id+"F3.wireOp",EDGE,"E4.sketch_text.stroke-80"),sQuery(id+"F3.wireOp",EDGE,"E4.sketch_text.stroke-81"),sQuery(id+"F3.wireOp",EDGE,"E4.sketch_text.stroke-82"),sQuery(id+"F3.wireOp",EDGE,"E4.sketch_text.stroke-83"),sQuery(id+"F3.wireOp",EDGE,"E4.sketch_text.stroke-84"),sQuery(id+"F3.wireOp",EDGE,"E4.sketch_text.stroke-85"),sQuery(id+"F3.wireOp",EDGE,"E4.sketch_text.stroke-86"),sQuery(id+"F3.wireOp",EDGE,"E4.sketch_text.stroke-87"),sQuery(id+"F3.wireOp",EDGE,"E4.sketch_text.stroke-88"),sQuery(id+"F3.wireOp",EDGE,"E4.sketch_text.stroke-89"),sQuery(id+"F3.wireOp",EDGE,"E4.sketch_text.stroke-90"),sQuery(id+"F3.wireOp",EDGE,"E4.sketch_text.stroke-91"),sQuery(id+"F3.wireOp",EDGE,"E4.sketch_text.stroke-92"),sQuery(id+"F3.wireOp",EDGE,"E4.sketch_text.stroke-93"),sQuery(id+"F3.wireOp",EDGE,"E4.sketch_text.stroke-94"),sQuery(id+"F3.wireOp",EDGE,"E4.sketch_text.stroke-95"),sQuery(id+"F3.wireOp",EDGE,"E4.sketch_text.stroke-96"),sQuery(id+"F3.wireOp",EDGE,"E4.sketch_text.stroke-97"),sQuery(id+"F3.wireOp",EDGE,"E4.sketch_text.stroke-103"),sQuery(id+"F3.wireOp",EDGE,"E4.sketch_text.stroke-104"),sQuery(id+"F3.wireOp",EDGE,"E4.sketch_text.stroke-105"),sQuery(id+"F3.wireOp",EDGE,"E4.sketch_text.stroke-106"),sQuery(id+"F3.wireOp",EDGE,"E4.sketch_text.stroke-107"),sQuery(id+"F3.wireOp",EDGE,"E4.sketch_text.stroke-108"),sQuery(id+"F3.wireOp",EDGE,"E4.sketch_text.stroke-109"),sQuery(id+"F3.wireOp",EDGE,"E4.sketch_text.stroke-110"),sQuery(id+"F3.wireOp",EDGE,"E4.sketch_text.stroke-111"),sQuery(id+"F3.wireOp",EDGE,"E4.sketch_text.stroke-112"),sQuery(id+"F3.wireOp",EDGE,"E4.sketch_text.stroke-113"),sQuery(id+"F3.wireOp",EDGE,"E4.sketch_text.stroke-114"),sQuery(id+"F3.wireOp",EDGE,"E4.sketch_text.stroke-115"),sQuery(id+"F3.wireOp",EDGE,"E4.sketch_text.stroke-116"),sQuery(id+"F3.wireOp",EDGE,"E4.sketch_text.stroke-117"),sQuery(id+"F3.wireOp",EDGE,"E4.sketch_text.stroke-118"),sQuery(id+"F3.wireOp",EDGE,"E4.sketch_text.stroke-119"),sQuery(id+"F3.wireOp",EDGE,"E4.sketch_text.stroke-120"),sQuery(id+"F3.wireOp",EDGE,"E4.sketch_text.stroke-121"),sQuery(id+"F3.wireOp",EDGE,"E4.sketch_text.stroke-122"),sQuery(id+"F3.wireOp",EDGE,"E4.sketch_text.stroke-123"),sQuery(id+"F3.wireOp",EDGE,"E4.sketch_text.stroke-124"),sQuery(id+"F3.wireOp",EDGE,"E4.sketch_text.stroke-125"),sQuery(id+"F3.wireOp",EDGE,"E4.sketch_text.stroke-126"),sQuery(id+"F3.wireOp",EDGE,"E4.sketch_text.stroke-127"),sQuery(id+"F3.wireOp",EDGE,"E4.sketch_text.stroke-128"),sQuery(id+"F3.wireOp",EDGE,"E4.sketch_text.stroke-129"),sQuery(id+"F3.wireOp",EDGE,"E4.sketch_text.stroke-130"),sQuery(id+"F3.wireOp",EDGE,"E4.sketch_text.stroke-131"),sQuery(id+"F3.wireOp",EDGE,"E4.sketch_text.stroke-132"),sQuery(id+"F3.wireOp",EDGE,"E4.sketch_text.stroke-133"),sQuery(id+"F3.wireOp",EDGE,"E4.sketch_text.stroke-134"),sQuery(id+"F3.wireOp",EDGE,"E4.sketch_text.stroke-135"),sQuery(id+"F3.wireOp",EDGE,"E4.sketch_text.stroke-136"),sQuery(id+"F3.wireOp",EDGE,"E4.sketch_text.stroke-137"),sQuery(id+"F3.wireOp",EDGE,"E4.sketch_text.stroke-138"),sQuery(id+"F3.wireOp",EDGE,"E4.sketch_text.stroke-139"),sQuery(id+"F3.wireOp",EDGE,"E4.sketch_text.stroke-140"),sQuery(id+"F3.wireOp",EDGE,"E4.sketch_text.stroke-141"),sQuery(id+"F3.wireOp",EDGE,"E4.sketch_text.stroke-142"),sQuery(id+"F3.wireOp",EDGE,"E4.sketch_text.stroke-143"),sQuery(id+"F3.wireOp",EDGE,"E4.sketch_text.stroke-144"),sQuery(id+"F3.wireOp",EDGE,"E4.sketch_text.stroke-145"),sQuery(id+"F3.wireOp",EDGE,"E4.sketch_text.stroke-146"),sQuery(id+"F3.wireOp",EDGE,"E4.sketch_text.stroke-147"),sQuery(id+"F3.wireOp",EDGE,"E4.sketch_text.stroke-148"),sQuery(id+"F3.wireOp",EDGE,"E4.sketch_text.stroke-149"),sQuery(id+"F3.wireOp",EDGE,"E4.sketch_text.stroke-150"),sQuery(id+"F3.wireOp",EDGE,"E4.sketch_text.stroke-151"),sQuery(id+"F3.wireOp",EDGE,"E4.sketch_text.stroke-152"),sQuery(id+"F3.wireOp",EDGE,"E4.sketch_text.stroke-153"),sQuery(id+"F3.wireOp",EDGE,"E4.sketch_text.stroke-159"),sQuery(id+"F3.wireOp",EDGE,"E4.sketch_text.stroke-160"),sQuery(id+"F3.wireOp",EDGE,"E4.sketch_text.stroke-161"),sQuery(id+"F3.wireOp",EDGE,"E4.sketch_text.stroke-162"),sQuery(id+"F3.wireOp",EDGE,"E4.sketch_text.stroke-163"),sQuery(id+"F3.wireOp",EDGE,"E4.sketch_text.stroke-164"),sQuery(id+"F3.wireOp",EDGE,"E4.sketch_text.stroke-165"),sQuery(id+"F3.wireOp",EDGE,"E4.sketch_text.stroke-166"),sQuery(id+"F3.wireOp",EDGE,"E4.sketch_text.stroke-167"),sQuery(id+"F3.wireOp",EDGE,"E4.sketch_text.stroke-168"),sQuery(id+"F3.wireOp",EDGE,"E4.sketch_text.stroke-169"),sQuery(id+"F3.wireOp",EDGE,"E4.sketch_text.stroke-170"),sQuery(id+"F3.wireOp",EDGE,"E4.sketch_text.stroke-171"),sQuery(id+"F3.wireOp",EDGE,"E4.sketch_text.stroke-172"),sQuery(id+"F3.wireOp",EDGE,"E4.sketch_text.stroke-173"),sQuery(id+"F3.wireOp",EDGE,"E4.sketch_text.stroke-174"),sQuery(id+"F3.wireOp",EDGE,"E4.sketch_text.stroke-175"),sQuery(id+"F3.wireOp",EDGE,"E4.sketch_text.stroke-176"),sQuery(id+"F3.wireOp",EDGE,"E4.sketch_text.stroke-177"),sQuery(id+"F3.wireOp",EDGE,"E4.sketch_text.stroke-178"),sQuery(id+"F3.wireOp",EDGE,"E4.sketch_text.stroke-179"),sQuery(id+"F3.wireOp",EDGE,"E4.sketch_text.stroke-180"),subQ0,subQ2])],"isStart":true}),makeQuery(id+"F6.opExtrude","SWEPT_FACE",FACE,{"disambiguationData":[OSD([subQ2])]})])],"derivedFrom":makeQuery(id+"F6.opExtrude","CAP_EDGE",EDGE,{"disambiguationData":[OSD([subQ2])],"isStart":true})});}
            var Q11;
            {var subQ0=sQuery(id+"F0.wireOp",EDGE,"E0.top");var subQ1=sQuery(id+"F0.wireOp",EDGE,"E0.bottom");var subQ2=sQuery(id+"F5.wireOp",EDGE,"6ee83ff3-586e-4dbe-aaea-af71240543bd");Q11=makeQuery(id+"F6.boolean.opBoolean","SPLIT",EDGE,{"disambiguationData":[TD([makeQuery(id+"F1.opExtrude","CAP_FACE",FACE,{"disambiguationData":[OSD([subQ1,subQ0,sQuery(id+"F0.wireOp",EDGE,"E0.left"),sQuery(id+"F0.wireOp",EDGE,"E0.right")])],"isStart":false}),makeQuery(id+"F1.opExtrude","SWEPT_FACE",FACE,{"disambiguationData":[OSD([subQ0])]}),makeQuery(id+"F6.opExtrude","CAP_FACE",FACE,{"disambiguationData":[OSD([subQ1,sQuery(id+"F2.wireOp",EDGE,"E2.sketch_text.stroke-0"),sQuery(id+"F2.wireOp",EDGE,"E2.sketch_text.stroke-1"),sQuery(id+"F2.wireOp",EDGE,"E2.sketch_text.stroke-2"),sQuery(id+"F2.wireOp",EDGE,"E2.sketch_text.stroke-3"),sQuery(id+"F2.wireOp",EDGE,"E2.sketch_text.stroke-4"),sQuery(id+"F2.wireOp",EDGE,"E2.sketch_text.stroke-5"),sQuery(id+"F2.wireOp",EDGE,"E2.sketch_text.stroke-6"),sQuery(id+"F2.wireOp",EDGE,"E2.sketch_text.stroke-7"),sQuery(id+"F2.wireOp",EDGE,"E2.sketch_text.stroke-8"),sQuery(id+"F2.wireOp",EDGE,"E2.sketch_text.stroke-9"),sQuery(id+"F2.wireOp",EDGE,"E2.sketch_text.stroke-10"),sQuery(id+"F2.wireOp",EDGE,"E2.sketch_text.stroke-11"),sQuery(id+"F2.wireOp",EDGE,"E2.sketch_text.stroke-12"),sQuery(id+"F2.wireOp",EDGE,"E2.sketch_text.stroke-13"),sQuery(id+"F2.wireOp",EDGE,"E2.sketch_text.stroke-14"),sQuery(id+"F2.wireOp",EDGE,"E2.sketch_text.stroke-15"),sQuery(id+"F2.wireOp",EDGE,"E2.sketch_text.stroke-16"),sQuery(id+"F2.wireOp",EDGE,"E2.sketch_text.stroke-17"),sQuery(id+"F2.wireOp",EDGE,"E2.sketch_text.stroke-18"),sQuery(id+"F2.wireOp",EDGE,"E2.sketch_text.stroke-19"),sQuery(id+"F2.wireOp",EDGE,"E2.sketch_text.stroke-20"),sQuery(id+"F2.wireOp",EDGE,"E2.sketch_text.stroke-21"),sQuery(id+"F2.wireOp",EDGE,"E2.sketch_text.stroke-22"),sQuery(id+"F2.wireOp",EDGE,"E2.sketch_text.stroke-23"),sQuery(id+"F2.wireOp",EDGE,"E2.sketch_text.stroke-24"),sQuery(id+"F2.wireOp",EDGE,"E2.sketch_text.stroke-25"),sQuery(id+"F2.wireOp",EDGE,"E2.sketch_text.stroke-26"),sQuery(id+"F2.wireOp",EDGE,"E2.sketch_text.stroke-27"),sQuery(id+"F2.wireOp",EDGE,"E2.sketch_text.stroke-28"),sQuery(id+"F2.wireOp",EDGE,"E2.sketch_text.stroke-29"),sQuery(id+"F2.wireOp",EDGE,"E2.sketch_text.stroke-30"),sQuery(id+"F2.wireOp",EDGE,"E2.sketch_text.stroke-31"),sQuery(id+"F2.wireOp",EDGE,"E2.sketch_text.stroke-32"),sQuery(id+"F2.wireOp",EDGE,"E2.sketch_text.stroke-33"),sQuery(id+"F2.wireOp",EDGE,"E2.sketch_text.stroke-34"),sQuery(id+"F2.wireOp",EDGE,"E2.sketch_text.stroke-35"),sQuery(id+"F2.wireOp",EDGE,"E2.sketch_text.stroke-36"),sQuery(id+"F2.wireOp",EDGE,"E2.sketch_text.stroke-37"),sQuery(id+"F2.wireOp",EDGE,"E2.sketch_text.stroke-38"),sQuery(id+"F2.wireOp",EDGE,"E2.sketch_text.stroke-39"),sQuery(id+"F2.wireOp",EDGE,"E2.sketch_text.stroke-40"),sQuery(id+"F2.wireOp",EDGE,"E2.sketch_text.stroke-41"),sQuery(id+"F2.wireOp",EDGE,"E2.sketch_text.stroke-42"),sQuery(id+"F2.wireOp",EDGE,"E2.sketch_text.stroke-43"),sQuery(id+"F2.wireOp",EDGE,"E2.sketch_text.stroke-44"),sQuery(id+"F2.wireOp",EDGE,"E2.sketch_text.stroke-45"),sQuery(id+"F2.wireOp",EDGE,"E2.sketch_text.stroke-46"),sQuery(id+"F2.wireOp",EDGE,"E2.sketch_text.stroke-47"),sQuery(id+"F2.wireOp",EDGE,"E2.sketch_text.stroke-48"),sQuery(id+"F2.wireOp",EDGE,"E2.sketch_text.stroke-49"),sQuery(id+"F2.wireOp",EDGE,"E2.sketch_text.stroke-50"),sQuery(id+"F2.wireOp",EDGE,"E2.sketch_text.stroke-51"),sQuery(id+"F2.wireOp",EDGE,"E2.sketch_text.stroke-52"),sQuery(id+"F2.wireOp",EDGE,"E2.sketch_text.stroke-53"),sQuery(id+"F2.wireOp",EDGE,"E2.sketch_text.stroke-54"),sQuery(id+"F2.wireOp",EDGE,"E2.sketch_text.stroke-55"),sQuery(id+"F2.wireOp",EDGE,"E2.sketch_text.stroke-56"),sQuery(id+"F2.wireOp",EDGE,"E2.sketch_text.stroke-57"),sQuery(id+"F2.wireOp",EDGE,"E2.sketch_text.stroke-58"),sQuery(id+"F2.wireOp",EDGE,"E2.sketch_text.stroke-59"),sQuery(id+"F2.wireOp",EDGE,"E2.sketch_text.stroke-60"),sQuery(id+"F2.wireOp",EDGE,"E2.sketch_text.stroke-61"),sQuery(id+"F2.wireOp",EDGE,"E2.sketch_text.stroke-62"),sQuery(id+"F2.wireOp",EDGE,"E2.sketch_text.stroke-63"),sQuery(id+"F2.wireOp",EDGE,"E2.sketch_text.stroke-64"),sQuery(id+"F2.wireOp",EDGE,"E2.sketch_text.stroke-65"),sQuery(id+"F2.wireOp",EDGE,"E2.sketch_text.stroke-66"),sQuery(id+"F2.wireOp",EDGE,"E2.sketch_text.stroke-67"),sQuery(id+"F2.wireOp",EDGE,"E2.sketch_text.stroke-68"),sQuery(id+"F2.wireOp",EDGE,"E2.sketch_text.stroke-69"),sQuery(id+"F2.wireOp",EDGE,"E2.sketch_text.stroke-70"),sQuery(id+"F2.wireOp",EDGE,"E2.sketch_text.stroke-71"),sQuery(id+"F2.wireOp",EDGE,"E2.sketch_text.stroke-72"),sQuery(id+"F2.wireOp",EDGE,"E2.sketch_text.stroke-73"),sQuery(id+"F2.wireOp",EDGE,"E2.sketch_text.stroke-74"),sQuery(id+"F2.wireOp",EDGE,"E2.sketch_text.stroke-75"),sQuery(id+"F2.wireOp",EDGE,"E2.sketch_text.stroke-76"),sQuery(id+"F2.wireOp",EDGE,"E2.sketch_text.stroke-77"),sQuery(id+"F2.wireOp",EDGE,"E2.sketch_text.stroke-78"),sQuery(id+"F2.wireOp",EDGE,"E2.sketch_text.stroke-79"),sQuery(id+"F2.wireOp",EDGE,"E2.sketch_text.stroke-80"),sQuery(id+"F2.wireOp",EDGE,"E2.sketch_text.stroke-81"),sQuery(id+"F2.wireOp",EDGE,"E2.sketch_text.stroke-82"),sQuery(id+"F2.wireOp",EDGE,"E2.sketch_text.stroke-83"),sQuery(id+"F2.wireOp",EDGE,"E2.sketch_text.stroke-84"),sQuery(id+"F2.wireOp",EDGE,"E2.sketch_text.stroke-85"),sQuery(id+"F2.wireOp",EDGE,"E2.sketch_text.stroke-86"),sQuery(id+"F2.wireOp",EDGE,"E2.sketch_text.stroke-87"),sQuery(id+"F2.wireOp",EDGE,"E2.sketch_text.stroke-88"),sQuery(id+"F2.wireOp",EDGE,"E2.sketch_text.stroke-89"),sQuery(id+"F2.wireOp",EDGE,"E2.sketch_text.stroke-90"),sQuery(id+"F2.wireOp",EDGE,"E2.sketch_text.stroke-91"),sQuery(id+"F2.wireOp",EDGE,"E2.sketch_text.stroke-92"),sQuery(id+"F2.wireOp",EDGE,"E2.sketch_text.stroke-93"),sQuery(id+"F2.wireOp",EDGE,"E2.sketch_text.stroke-94"),sQuery(id+"F2.wireOp",EDGE,"E2.sketch_text.stroke-95"),sQuery(id+"F2.wireOp",EDGE,"E2.sketch_text.stroke-96"),sQuery(id+"F2.wireOp",EDGE,"E2.sketch_text.stroke-97"),sQuery(id+"F2.wireOp",EDGE,"E2.sketch_text.stroke-98"),sQuery(id+"F2.wireOp",EDGE,"E2.sketch_text.stroke-99"),sQuery(id+"F2.wireOp",EDGE,"E2.sketch_text.stroke-100"),sQuery(id+"F2.wireOp",EDGE,"E2.sketch_text.stroke-101"),sQuery(id+"F2.wireOp",EDGE,"E2.sketch_text.stroke-102"),sQuery(id+"F2.wireOp",EDGE,"E2.sketch_text.stroke-103"),sQuery(id+"F2.wireOp",EDGE,"E2.sketch_text.stroke-104"),sQuery(id+"F2.wireOp",EDGE,"E2.sketch_text.stroke-105"),sQuery(id+"F2.wireOp",EDGE,"E2.sketch_text.stroke-106"),sQuery(id+"F2.wireOp",EDGE,"E2.sketch_text.stroke-107"),sQuery(id+"F2.wireOp",EDGE,"E2.sketch_text.stroke-108"),sQuery(id+"F2.wireOp",EDGE,"E2.sketch_text.stroke-109"),sQuery(id+"F2.wireOp",EDGE,"E2.sketch_text.stroke-110"),sQuery(id+"F2.wireOp",EDGE,"E2.sketch_text.stroke-111"),sQuery(id+"F2.wireOp",EDGE,"E2.sketch_text.stroke-112"),sQuery(id+"F2.wireOp",EDGE,"E2.sketch_text.stroke-113"),sQuery(id+"F2.wireOp",EDGE,"E2.sketch_text.stroke-114"),sQuery(id+"F2.wireOp",EDGE,"E2.sketch_text.stroke-115"),sQuery(id+"F2.wireOp",EDGE,"E2.sketch_text.stroke-116"),sQuery(id+"F2.wireOp",EDGE,"E2.sketch_text.stroke-117"),sQuery(id+"F2.wireOp",EDGE,"E2.sketch_text.stroke-118"),sQuery(id+"F2.wireOp",EDGE,"E2.sketch_text.stroke-119"),sQuery(id+"F2.wireOp",EDGE,"E2.sketch_text.stroke-120"),sQuery(id+"F2.wireOp",EDGE,"E2.sketch_text.stroke-121"),sQuery(id+"F2.wireOp",EDGE,"E2.sketch_text.stroke-122"),sQuery(id+"F2.wireOp",EDGE,"E2.sketch_text.stroke-123"),sQuery(id+"F2.wireOp",EDGE,"E2.sketch_text.stroke-124"),sQuery(id+"F2.wireOp",EDGE,"E2.sketch_text.stroke-125"),sQuery(id+"F2.wireOp",EDGE,"E2.sketch_text.stroke-126"),sQuery(id+"F2.wireOp",EDGE,"E2.sketch_text.stroke-127"),sQuery(id+"F2.wireOp",EDGE,"E2.sketch_text.stroke-128"),sQuery(id+"F2.wireOp",EDGE,"E2.sketch_text.stroke-129"),sQuery(id+"F2.wireOp",EDGE,"E2.sketch_text.stroke-130"),sQuery(id+"F2.wireOp",EDGE,"E2.sketch_text.stroke-131"),sQuery(id+"F2.wireOp",EDGE,"E2.sketch_text.stroke-132"),sQuery(id+"F2.wireOp",EDGE,"E2.sketch_text.stroke-133"),sQuery(id+"F2.wireOp",EDGE,"E2.sketch_text.stroke-134"),sQuery(id+"F2.wireOp",EDGE,"E2.sketch_text.stroke-135"),sQuery(id+"F2.wireOp",EDGE,"E2.sketch_text.stroke-136"),sQuery(id+"F2.wireOp",EDGE,"E2.sketch_text.stroke-137"),sQuery(id+"F2.wireOp",EDGE,"E2.sketch_text.stroke-138"),sQuery(id+"F2.wireOp",EDGE,"E2.sketch_text.stroke-139"),sQuery(id+"F2.wireOp",EDGE,"E2.sketch_text.stroke-140"),sQuery(id+"F2.wireOp",EDGE,"E2.sketch_text.stroke-141"),sQuery(id+"F2.wireOp",EDGE,"E2.sketch_text.stroke-142"),sQuery(id+"F2.wireOp",EDGE,"E2.sketch_text.stroke-143"),sQuery(id+"F2.wireOp",EDGE,"E2.sketch_text.stroke-144"),sQuery(id+"F2.wireOp",EDGE,"E2.sketch_text.stroke-145"),sQuery(id+"F2.wireOp",EDGE,"E2.sketch_text.stroke-146"),sQuery(id+"F2.wireOp",EDGE,"E2.sketch_text.stroke-147"),sQuery(id+"F2.wireOp",EDGE,"E2.sketch_text.stroke-148"),sQuery(id+"F2.wireOp",EDGE,"E2.sketch_text.stroke-149"),sQuery(id+"F2.wireOp",EDGE,"E2.sketch_text.stroke-150"),sQuery(id+"F2.wireOp",EDGE,"E2.sketch_text.stroke-151"),sQuery(id+"F2.wireOp",EDGE,"E2.sketch_text.stroke-152"),sQuery(id+"F2.wireOp",EDGE,"E2.sketch_text.stroke-153"),sQuery(id+"F2.wireOp",EDGE,"E2.sketch_text.stroke-154"),sQuery(id+"F2.wireOp",EDGE,"E2.sketch_text.stroke-155"),sQuery(id+"F2.wireOp",EDGE,"E2.sketch_text.stroke-156"),sQuery(id+"F2.wireOp",EDGE,"E2.sketch_text.stroke-157"),sQuery(id+"F2.wireOp",EDGE,"E2.sketch_text.stroke-158"),sQuery(id+"F2.wireOp",EDGE,"E2.sketch_text.stroke-159"),sQuery(id+"F2.wireOp",EDGE,"E2.sketch_text.stroke-160"),sQuery(id+"F2.wireOp",EDGE,"E2.sketch_text.stroke-161"),sQuery(id+"F2.wireOp",EDGE,"E2.sketch_text.stroke-162"),sQuery(id+"F2.wireOp",EDGE,"E2.sketch_text.stroke-163"),sQuery(id+"F2.wireOp",EDGE,"E2.sketch_text.stroke-164"),sQuery(id+"F2.wireOp",EDGE,"E2.sketch_text.stroke-165"),sQuery(id+"F2.wireOp",EDGE,"E2.sketch_text.stroke-166"),sQuery(id+"F2.wireOp",EDGE,"E2.sketch_text.stroke-167"),sQuery(id+"F2.wireOp",EDGE,"E2.sketch_text.stroke-168"),sQuery(id+"F2.wireOp",EDGE,"E2.sketch_text.stroke-169"),sQuery(id+"F2.wireOp",EDGE,"E2.sketch_text.stroke-170"),sQuery(id+"F2.wireOp",EDGE,"E2.sketch_text.stroke-171"),sQuery(id+"F2.wireOp",EDGE,"E2.sketch_text.stroke-172"),sQuery(id+"F2.wireOp",EDGE,"E2.sketch_text.stroke-173"),sQuery(id+"F3.wireOp",EDGE,"E4.sketch_text.stroke-0"),sQuery(id+"F3.wireOp",EDGE,"E4.sketch_text.stroke-1"),sQuery(id+"F3.wireOp",EDGE,"E4.sketch_text.stroke-2"),sQuery(id+"F3.wireOp",EDGE,"E4.sketch_text.stroke-3"),sQuery(id+"F3.wireOp",EDGE,"E4.sketch_text.stroke-4"),sQuery(id+"F3.wireOp",EDGE,"E4.sketch_text.stroke-5"),sQuery(id+"F3.wireOp",EDGE,"E4.sketch_text.stroke-6"),sQuery(id+"F3.wireOp",EDGE,"E4.sketch_text.stroke-7"),sQuery(id+"F3.wireOp",EDGE,"E4.sketch_text.stroke-8"),sQuery(id+"F3.wireOp",EDGE,"E4.sketch_text.stroke-9"),sQuery(id+"F3.wireOp",EDGE,"E4.sketch_text.stroke-10"),sQuery(id+"F3.wireOp",EDGE,"E4.sketch_text.stroke-11"),sQuery(id+"F3.wireOp",EDGE,"E4.sketch_text.stroke-12"),sQuery(id+"F3.wireOp",EDGE,"E4.sketch_text.stroke-13"),sQuery(id+"F3.wireOp",EDGE,"E4.sketch_text.stroke-14"),sQuery(id+"F3.wireOp",EDGE,"E4.sketch_text.stroke-15"),sQuery(id+"F3.wireOp",EDGE,"E4.sketch_text.stroke-16"),sQuery(id+"F3.wireOp",EDGE,"E4.sketch_text.stroke-17"),sQuery(id+"F3.wireOp",EDGE,"E4.sketch_text.stroke-18"),sQuery(id+"F3.wireOp",EDGE,"E4.sketch_text.stroke-19"),sQuery(id+"F3.wireOp",EDGE,"E4.sketch_text.stroke-20"),sQuery(id+"F3.wireOp",EDGE,"E4.sketch_text.stroke-21"),sQuery(id+"F3.wireOp",EDGE,"E4.sketch_text.stroke-22"),sQuery(id+"F3.wireOp",EDGE,"E4.sketch_text.stroke-23"),sQuery(id+"F3.wireOp",EDGE,"E4.sketch_text.stroke-24"),sQuery(id+"F3.wireOp",EDGE,"E4.sketch_text.stroke-25"),sQuery(id+"F3.wireOp",EDGE,"E4.sketch_text.stroke-26"),sQuery(id+"F3.wireOp",EDGE,"E4.sketch_text.stroke-27"),sQuery(id+"F3.wireOp",EDGE,"E4.sketch_text.stroke-28"),sQuery(id+"F3.wireOp",EDGE,"E4.sketch_text.stroke-29"),sQuery(id+"F3.wireOp",EDGE,"E4.sketch_text.stroke-30"),sQuery(id+"F3.wireOp",EDGE,"E4.sketch_text.stroke-31"),sQuery(id+"F3.wireOp",EDGE,"E4.sketch_text.stroke-32"),sQuery(id+"F3.wireOp",EDGE,"E4.sketch_text.stroke-33"),sQuery(id+"F3.wireOp",EDGE,"E4.sketch_text.stroke-34"),sQuery(id+"F3.wireOp",EDGE,"E4.sketch_text.stroke-35"),sQuery(id+"F3.wireOp",EDGE,"E4.sketch_text.stroke-36"),sQuery(id+"F3.wireOp",EDGE,"E4.sketch_text.stroke-37"),sQuery(id+"F3.wireOp",EDGE,"E4.sketch_text.stroke-38"),sQuery(id+"F3.wireOp",EDGE,"E4.sketch_text.stroke-39"),sQuery(id+"F3.wireOp",EDGE,"E4.sketch_text.stroke-40"),sQuery(id+"F3.wireOp",EDGE,"E4.sketch_text.stroke-41"),sQuery(id+"F3.wireOp",EDGE,"E4.sketch_text.stroke-42"),sQuery(id+"F3.wireOp",EDGE,"E4.sketch_text.stroke-43"),sQuery(id+"F3.wireOp",EDGE,"E4.sketch_text.stroke-44"),sQuery(id+"F3.wireOp",EDGE,"E4.sketch_text.stroke-45"),sQuery(id+"F3.wireOp",EDGE,"E4.sketch_text.stroke-46"),sQuery(id+"F3.wireOp",EDGE,"E4.sketch_text.stroke-47"),sQuery(id+"F3.wireOp",EDGE,"E4.sketch_text.stroke-48"),sQuery(id+"F3.wireOp",EDGE,"E4.sketch_text.stroke-49"),sQuery(id+"F3.wireOp",EDGE,"E4.sketch_text.stroke-50"),sQuery(id+"F3.wireOp",EDGE,"E4.sketch_text.stroke-51"),sQuery(id+"F3.wireOp",EDGE,"E4.sketch_text.stroke-52"),sQuery(id+"F3.wireOp",EDGE,"E4.sketch_text.stroke-53"),sQuery(id+"F3.wireOp",EDGE,"E4.sketch_text.stroke-54"),sQuery(id+"F3.wireOp",EDGE,"E4.sketch_text.stroke-55"),sQuery(id+"F3.wireOp",EDGE,"E4.sketch_text.stroke-56"),sQuery(id+"F3.wireOp",EDGE,"E4.sketch_text.stroke-57"),sQuery(id+"F3.wireOp",EDGE,"E4.sketch_text.stroke-58"),sQuery(id+"F3.wireOp",EDGE,"E4.sketch_text.stroke-59"),sQuery(id+"F3.wireOp",EDGE,"E4.sketch_text.stroke-60"),sQuery(id+"F3.wireOp",EDGE,"E4.sketch_text.stroke-61"),sQuery(id+"F3.wireOp",EDGE,"E4.sketch_text.stroke-62"),sQuery(id+"F3.wireOp",EDGE,"E4.sketch_text.stroke-71"),sQuery(id+"F3.wireOp",EDGE,"E4.sketch_text.stroke-72"),sQuery(id+"F3.wireOp",EDGE,"E4.sketch_text.stroke-73"),sQuery(id+"F3.wireOp",EDGE,"E4.sketch_text.stroke-74"),sQuery(id+"F3.wireOp",EDGE,"E4.sketch_text.stroke-75"),sQuery(id+"F3.wireOp",EDGE,"E4.sketch_text.stroke-76"),sQuery(id+"F3.wireOp",EDGE,"E4.sketch_text.stroke-77"),sQuery(id+"F3.wireOp",EDGE,"E4.sketch_text.stroke-78"),sQuery(id+"F3.wireOp",EDGE,"E4.sketch_text.stroke-79"),sQuery(id+"F3.wireOp",EDGE,"E4.sketch_text.stroke-80"),sQuery(id+"F3.wireOp",EDGE,"E4.sketch_text.stroke-81"),sQuery(id+"F3.wireOp",EDGE,"E4.sketch_text.stroke-82"),sQuery(id+"F3.wireOp",EDGE,"E4.sketch_text.stroke-83"),sQuery(id+"F3.wireOp",EDGE,"E4.sketch_text.stroke-84"),sQuery(id+"F3.wireOp",EDGE,"E4.sketch_text.stroke-85"),sQuery(id+"F3.wireOp",EDGE,"E4.sketch_text.stroke-86"),sQuery(id+"F3.wireOp",EDGE,"E4.sketch_text.stroke-87"),sQuery(id+"F3.wireOp",EDGE,"E4.sketch_text.stroke-88"),sQuery(id+"F3.wireOp",EDGE,"E4.sketch_text.stroke-89"),sQuery(id+"F3.wireOp",EDGE,"E4.sketch_text.stroke-90"),sQuery(id+"F3.wireOp",EDGE,"E4.sketch_text.stroke-91"),sQuery(id+"F3.wireOp",EDGE,"E4.sketch_text.stroke-92"),sQuery(id+"F3.wireOp",EDGE,"E4.sketch_text.stroke-93"),sQuery(id+"F3.wireOp",EDGE,"E4.sketch_text.stroke-94"),sQuery(id+"F3.wireOp",EDGE,"E4.sketch_text.stroke-95"),sQuery(id+"F3.wireOp",EDGE,"E4.sketch_text.stroke-96"),sQuery(id+"F3.wireOp",EDGE,"E4.sketch_text.stroke-97"),sQuery(id+"F3.wireOp",EDGE,"E4.sketch_text.stroke-103"),sQuery(id+"F3.wireOp",EDGE,"E4.sketch_text.stroke-104"),sQuery(id+"F3.wireOp",EDGE,"E4.sketch_text.stroke-105"),sQuery(id+"F3.wireOp",EDGE,"E4.sketch_text.stroke-106"),sQuery(id+"F3.wireOp",EDGE,"E4.sketch_text.stroke-107"),sQuery(id+"F3.wireOp",EDGE,"E4.sketch_text.stroke-108"),sQuery(id+"F3.wireOp",EDGE,"E4.sketch_text.stroke-109"),sQuery(id+"F3.wireOp",EDGE,"E4.sketch_text.stroke-110"),sQuery(id+"F3.wireOp",EDGE,"E4.sketch_text.stroke-111"),sQuery(id+"F3.wireOp",EDGE,"E4.sketch_text.stroke-112"),sQuery(id+"F3.wireOp",EDGE,"E4.sketch_text.stroke-113"),sQuery(id+"F3.wireOp",EDGE,"E4.sketch_text.stroke-114"),sQuery(id+"F3.wireOp",EDGE,"E4.sketch_text.stroke-115"),sQuery(id+"F3.wireOp",EDGE,"E4.sketch_text.stroke-116"),sQuery(id+"F3.wireOp",EDGE,"E4.sketch_text.stroke-117"),sQuery(id+"F3.wireOp",EDGE,"E4.sketch_text.stroke-118"),sQuery(id+"F3.wireOp",EDGE,"E4.sketch_text.stroke-119"),sQuery(id+"F3.wireOp",EDGE,"E4.sketch_text.stroke-120"),sQuery(id+"F3.wireOp",EDGE,"E4.sketch_text.stroke-121"),sQuery(id+"F3.wireOp",EDGE,"E4.sketch_text.stroke-122"),sQuery(id+"F3.wireOp",EDGE,"E4.sketch_text.stroke-123"),sQuery(id+"F3.wireOp",EDGE,"E4.sketch_text.stroke-124"),sQuery(id+"F3.wireOp",EDGE,"E4.sketch_text.stroke-125"),sQuery(id+"F3.wireOp",EDGE,"E4.sketch_text.stroke-126"),sQuery(id+"F3.wireOp",EDGE,"E4.sketch_text.stroke-127"),sQuery(id+"F3.wireOp",EDGE,"E4.sketch_text.stroke-128"),sQuery(id+"F3.wireOp",EDGE,"E4.sketch_text.stroke-129"),sQuery(id+"F3.wireOp",EDGE,"E4.sketch_text.stroke-130"),sQuery(id+"F3.wireOp",EDGE,"E4.sketch_text.stroke-131"),sQuery(id+"F3.wireOp",EDGE,"E4.sketch_text.stroke-132"),sQuery(id+"F3.wireOp",EDGE,"E4.sketch_text.stroke-133"),sQuery(id+"F3.wireOp",EDGE,"E4.sketch_text.stroke-134"),sQuery(id+"F3.wireOp",EDGE,"E4.sketch_text.stroke-135"),sQuery(id+"F3.wireOp",EDGE,"E4.sketch_text.stroke-136"),sQuery(id+"F3.wireOp",EDGE,"E4.sketch_text.stroke-137"),sQuery(id+"F3.wireOp",EDGE,"E4.sketch_text.stroke-138"),sQuery(id+"F3.wireOp",EDGE,"E4.sketch_text.stroke-139"),sQuery(id+"F3.wireOp",EDGE,"E4.sketch_text.stroke-140"),sQuery(id+"F3.wireOp",EDGE,"E4.sketch_text.stroke-141"),sQuery(id+"F3.wireOp",EDGE,"E4.sketch_text.stroke-142"),sQuery(id+"F3.wireOp",EDGE,"E4.sketch_text.stroke-143"),sQuery(id+"F3.wireOp",EDGE,"E4.sketch_text.stroke-144"),sQuery(id+"F3.wireOp",EDGE,"E4.sketch_text.stroke-145"),sQuery(id+"F3.wireOp",EDGE,"E4.sketch_text.stroke-146"),sQuery(id+"F3.wireOp",EDGE,"E4.sketch_text.stroke-147"),sQuery(id+"F3.wireOp",EDGE,"E4.sketch_text.stroke-148"),sQuery(id+"F3.wireOp",EDGE,"E4.sketch_text.stroke-149"),sQuery(id+"F3.wireOp",EDGE,"E4.sketch_text.stroke-150"),sQuery(id+"F3.wireOp",EDGE,"E4.sketch_text.stroke-151"),sQuery(id+"F3.wireOp",EDGE,"E4.sketch_text.stroke-152"),sQuery(id+"F3.wireOp",EDGE,"E4.sketch_text.stroke-153"),sQuery(id+"F3.wireOp",EDGE,"E4.sketch_text.stroke-159"),sQuery(id+"F3.wireOp",EDGE,"E4.sketch_text.stroke-160"),sQuery(id+"F3.wireOp",EDGE,"E4.sketch_text.stroke-161"),sQuery(id+"F3.wireOp",EDGE,"E4.sketch_text.stroke-162"),sQuery(id+"F3.wireOp",EDGE,"E4.sketch_text.stroke-163"),sQuery(id+"F3.wireOp",EDGE,"E4.sketch_text.stroke-164"),sQuery(id+"F3.wireOp",EDGE,"E4.sketch_text.stroke-165"),sQuery(id+"F3.wireOp",EDGE,"E4.sketch_text.stroke-166"),sQuery(id+"F3.wireOp",EDGE,"E4.sketch_text.stroke-167"),sQuery(id+"F3.wireOp",EDGE,"E4.sketch_text.stroke-168"),sQuery(id+"F3.wireOp",EDGE,"E4.sketch_text.stroke-169"),sQuery(id+"F3.wireOp",EDGE,"E4.sketch_text.stroke-170"),sQuery(id+"F3.wireOp",EDGE,"E4.sketch_text.stroke-171"),sQuery(id+"F3.wireOp",EDGE,"E4.sketch_text.stroke-172"),sQuery(id+"F3.wireOp",EDGE,"E4.sketch_text.stroke-173"),sQuery(id+"F3.wireOp",EDGE,"E4.sketch_text.stroke-174"),sQuery(id+"F3.wireOp",EDGE,"E4.sketch_text.stroke-175"),sQuery(id+"F3.wireOp",EDGE,"E4.sketch_text.stroke-176"),sQuery(id+"F3.wireOp",EDGE,"E4.sketch_text.stroke-177"),sQuery(id+"F3.wireOp",EDGE,"E4.sketch_text.stroke-178"),sQuery(id+"F3.wireOp",EDGE,"E4.sketch_text.stroke-179"),sQuery(id+"F3.wireOp",EDGE,"E4.sketch_text.stroke-180"),sQuery(id+"F5.wireOp",EDGE,"8007402e-1a4e-4a06-85a5-2af08e553504"),subQ2])],"isStart":true}),makeQuery(id+"F6.opExtrude","SWEPT_FACE",FACE,{"disambiguationData":[OSD([subQ2])]})]),OD(0.0)],"derivedFrom":makeQuery(id+"F1.opExtrude","CAP_EDGE",EDGE,{"disambiguationData":[OSD([subQ0])],"isStart":false})});}
            var Q12;
            {var subQ0=sQuery(id+"F0.wireOp",EDGE,"E0.top");var subQ1=sQuery(id+"F0.wireOp",EDGE,"E0.bottom");var subQ2=sQuery(id+"F5.wireOp",EDGE,"6ee83ff3-586e-4dbe-aaea-af71240543bd");Q12=makeQuery(id+"F6.boolean.opBoolean","SPLIT",EDGE,{"disambiguationData":[TD([makeQuery(id+"F1.opExtrude","CAP_FACE",FACE,{"disambiguationData":[OSD([subQ1,subQ0,sQuery(id+"F0.wireOp",EDGE,"E0.left"),sQuery(id+"F0.wireOp",EDGE,"E0.right")])],"isStart":false}),makeQuery(id+"F1.opExtrude","SWEPT_FACE",FACE,{"disambiguationData":[OSD([subQ0])]}),makeQuery(id+"F6.opExtrude","CAP_FACE",FACE,{"disambiguationData":[OSD([subQ1,sQuery(id+"F2.wireOp",EDGE,"E2.sketch_text.stroke-0"),sQuery(id+"F2.wireOp",EDGE,"E2.sketch_text.stroke-1"),sQuery(id+"F2.wireOp",EDGE,"E2.sketch_text.stroke-2"),sQuery(id+"F2.wireOp",EDGE,"E2.sketch_text.stroke-3"),sQuery(id+"F2.wireOp",EDGE,"E2.sketch_text.stroke-4"),sQuery(id+"F2.wireOp",EDGE,"E2.sketch_text.stroke-5"),sQuery(id+"F2.wireOp",EDGE,"E2.sketch_text.stroke-6"),sQuery(id+"F2.wireOp",EDGE,"E2.sketch_text.stroke-7"),sQuery(id+"F2.wireOp",EDGE,"E2.sketch_text.stroke-8"),sQuery(id+"F2.wireOp",EDGE,"E2.sketch_text.stroke-9"),sQuery(id+"F2.wireOp",EDGE,"E2.sketch_text.stroke-10"),sQuery(id+"F2.wireOp",EDGE,"E2.sketch_text.stroke-11"),sQuery(id+"F2.wireOp",EDGE,"E2.sketch_text.stroke-12"),sQuery(id+"F2.wireOp",EDGE,"E2.sketch_text.stroke-13"),sQuery(id+"F2.wireOp",EDGE,"E2.sketch_text.stroke-14"),sQuery(id+"F2.wireOp",EDGE,"E2.sketch_text.stroke-15"),sQuery(id+"F2.wireOp",EDGE,"E2.sketch_text.stroke-16"),sQuery(id+"F2.wireOp",EDGE,"E2.sketch_text.stroke-17"),sQuery(id+"F2.wireOp",EDGE,"E2.sketch_text.stroke-18"),sQuery(id+"F2.wireOp",EDGE,"E2.sketch_text.stroke-19"),sQuery(id+"F2.wireOp",EDGE,"E2.sketch_text.stroke-20"),sQuery(id+"F2.wireOp",EDGE,"E2.sketch_text.stroke-21"),sQuery(id+"F2.wireOp",EDGE,"E2.sketch_text.stroke-22"),sQuery(id+"F2.wireOp",EDGE,"E2.sketch_text.stroke-23"),sQuery(id+"F2.wireOp",EDGE,"E2.sketch_text.stroke-24"),sQuery(id+"F2.wireOp",EDGE,"E2.sketch_text.stroke-25"),sQuery(id+"F2.wireOp",EDGE,"E2.sketch_text.stroke-26"),sQuery(id+"F2.wireOp",EDGE,"E2.sketch_text.stroke-27"),sQuery(id+"F2.wireOp",EDGE,"E2.sketch_text.stroke-28"),sQuery(id+"F2.wireOp",EDGE,"E2.sketch_text.stroke-29"),sQuery(id+"F2.wireOp",EDGE,"E2.sketch_text.stroke-30"),sQuery(id+"F2.wireOp",EDGE,"E2.sketch_text.stroke-31"),sQuery(id+"F2.wireOp",EDGE,"E2.sketch_text.stroke-32"),sQuery(id+"F2.wireOp",EDGE,"E2.sketch_text.stroke-33"),sQuery(id+"F2.wireOp",EDGE,"E2.sketch_text.stroke-34"),sQuery(id+"F2.wireOp",EDGE,"E2.sketch_text.stroke-35"),sQuery(id+"F2.wireOp",EDGE,"E2.sketch_text.stroke-36"),sQuery(id+"F2.wireOp",EDGE,"E2.sketch_text.stroke-37"),sQuery(id+"F2.wireOp",EDGE,"E2.sketch_text.stroke-38"),sQuery(id+"F2.wireOp",EDGE,"E2.sketch_text.stroke-39"),sQuery(id+"F2.wireOp",EDGE,"E2.sketch_text.stroke-40"),sQuery(id+"F2.wireOp",EDGE,"E2.sketch_text.stroke-41"),sQuery(id+"F2.wireOp",EDGE,"E2.sketch_text.stroke-42"),sQuery(id+"F2.wireOp",EDGE,"E2.sketch_text.stroke-43"),sQuery(id+"F2.wireOp",EDGE,"E2.sketch_text.stroke-44"),sQuery(id+"F2.wireOp",EDGE,"E2.sketch_text.stroke-45"),sQuery(id+"F2.wireOp",EDGE,"E2.sketch_text.stroke-46"),sQuery(id+"F2.wireOp",EDGE,"E2.sketch_text.stroke-47"),sQuery(id+"F2.wireOp",EDGE,"E2.sketch_text.stroke-48"),sQuery(id+"F2.wireOp",EDGE,"E2.sketch_text.stroke-49"),sQuery(id+"F2.wireOp",EDGE,"E2.sketch_text.stroke-50"),sQuery(id+"F2.wireOp",EDGE,"E2.sketch_text.stroke-51"),sQuery(id+"F2.wireOp",EDGE,"E2.sketch_text.stroke-52"),sQuery(id+"F2.wireOp",EDGE,"E2.sketch_text.stroke-53"),sQuery(id+"F2.wireOp",EDGE,"E2.sketch_text.stroke-54"),sQuery(id+"F2.wireOp",EDGE,"E2.sketch_text.stroke-55"),sQuery(id+"F2.wireOp",EDGE,"E2.sketch_text.stroke-56"),sQuery(id+"F2.wireOp",EDGE,"E2.sketch_text.stroke-57"),sQuery(id+"F2.wireOp",EDGE,"E2.sketch_text.stroke-58"),sQuery(id+"F2.wireOp",EDGE,"E2.sketch_text.stroke-59"),sQuery(id+"F2.wireOp",EDGE,"E2.sketch_text.stroke-60"),sQuery(id+"F2.wireOp",EDGE,"E2.sketch_text.stroke-61"),sQuery(id+"F2.wireOp",EDGE,"E2.sketch_text.stroke-62"),sQuery(id+"F2.wireOp",EDGE,"E2.sketch_text.stroke-63"),sQuery(id+"F2.wireOp",EDGE,"E2.sketch_text.stroke-64"),sQuery(id+"F2.wireOp",EDGE,"E2.sketch_text.stroke-65"),sQuery(id+"F2.wireOp",EDGE,"E2.sketch_text.stroke-66"),sQuery(id+"F2.wireOp",EDGE,"E2.sketch_text.stroke-67"),sQuery(id+"F2.wireOp",EDGE,"E2.sketch_text.stroke-68"),sQuery(id+"F2.wireOp",EDGE,"E2.sketch_text.stroke-69"),sQuery(id+"F2.wireOp",EDGE,"E2.sketch_text.stroke-70"),sQuery(id+"F2.wireOp",EDGE,"E2.sketch_text.stroke-71"),sQuery(id+"F2.wireOp",EDGE,"E2.sketch_text.stroke-72"),sQuery(id+"F2.wireOp",EDGE,"E2.sketch_text.stroke-73"),sQuery(id+"F2.wireOp",EDGE,"E2.sketch_text.stroke-74"),sQuery(id+"F2.wireOp",EDGE,"E2.sketch_text.stroke-75"),sQuery(id+"F2.wireOp",EDGE,"E2.sketch_text.stroke-76"),sQuery(id+"F2.wireOp",EDGE,"E2.sketch_text.stroke-77"),sQuery(id+"F2.wireOp",EDGE,"E2.sketch_text.stroke-78"),sQuery(id+"F2.wireOp",EDGE,"E2.sketch_text.stroke-79"),sQuery(id+"F2.wireOp",EDGE,"E2.sketch_text.stroke-80"),sQuery(id+"F2.wireOp",EDGE,"E2.sketch_text.stroke-81"),sQuery(id+"F2.wireOp",EDGE,"E2.sketch_text.stroke-82"),sQuery(id+"F2.wireOp",EDGE,"E2.sketch_text.stroke-83"),sQuery(id+"F2.wireOp",EDGE,"E2.sketch_text.stroke-84"),sQuery(id+"F2.wireOp",EDGE,"E2.sketch_text.stroke-85"),sQuery(id+"F2.wireOp",EDGE,"E2.sketch_text.stroke-86"),sQuery(id+"F2.wireOp",EDGE,"E2.sketch_text.stroke-87"),sQuery(id+"F2.wireOp",EDGE,"E2.sketch_text.stroke-88"),sQuery(id+"F2.wireOp",EDGE,"E2.sketch_text.stroke-89"),sQuery(id+"F2.wireOp",EDGE,"E2.sketch_text.stroke-90"),sQuery(id+"F2.wireOp",EDGE,"E2.sketch_text.stroke-91"),sQuery(id+"F2.wireOp",EDGE,"E2.sketch_text.stroke-92"),sQuery(id+"F2.wireOp",EDGE,"E2.sketch_text.stroke-93"),sQuery(id+"F2.wireOp",EDGE,"E2.sketch_text.stroke-94"),sQuery(id+"F2.wireOp",EDGE,"E2.sketch_text.stroke-95"),sQuery(id+"F2.wireOp",EDGE,"E2.sketch_text.stroke-96"),sQuery(id+"F2.wireOp",EDGE,"E2.sketch_text.stroke-97"),sQuery(id+"F2.wireOp",EDGE,"E2.sketch_text.stroke-98"),sQuery(id+"F2.wireOp",EDGE,"E2.sketch_text.stroke-99"),sQuery(id+"F2.wireOp",EDGE,"E2.sketch_text.stroke-100"),sQuery(id+"F2.wireOp",EDGE,"E2.sketch_text.stroke-101"),sQuery(id+"F2.wireOp",EDGE,"E2.sketch_text.stroke-102"),sQuery(id+"F2.wireOp",EDGE,"E2.sketch_text.stroke-103"),sQuery(id+"F2.wireOp",EDGE,"E2.sketch_text.stroke-104"),sQuery(id+"F2.wireOp",EDGE,"E2.sketch_text.stroke-105"),sQuery(id+"F2.wireOp",EDGE,"E2.sketch_text.stroke-106"),sQuery(id+"F2.wireOp",EDGE,"E2.sketch_text.stroke-107"),sQuery(id+"F2.wireOp",EDGE,"E2.sketch_text.stroke-108"),sQuery(id+"F2.wireOp",EDGE,"E2.sketch_text.stroke-109"),sQuery(id+"F2.wireOp",EDGE,"E2.sketch_text.stroke-110"),sQuery(id+"F2.wireOp",EDGE,"E2.sketch_text.stroke-111"),sQuery(id+"F2.wireOp",EDGE,"E2.sketch_text.stroke-112"),sQuery(id+"F2.wireOp",EDGE,"E2.sketch_text.stroke-113"),sQuery(id+"F2.wireOp",EDGE,"E2.sketch_text.stroke-114"),sQuery(id+"F2.wireOp",EDGE,"E2.sketch_text.stroke-115"),sQuery(id+"F2.wireOp",EDGE,"E2.sketch_text.stroke-116"),sQuery(id+"F2.wireOp",EDGE,"E2.sketch_text.stroke-117"),sQuery(id+"F2.wireOp",EDGE,"E2.sketch_text.stroke-118"),sQuery(id+"F2.wireOp",EDGE,"E2.sketch_text.stroke-119"),sQuery(id+"F2.wireOp",EDGE,"E2.sketch_text.stroke-120"),sQuery(id+"F2.wireOp",EDGE,"E2.sketch_text.stroke-121"),sQuery(id+"F2.wireOp",EDGE,"E2.sketch_text.stroke-122"),sQuery(id+"F2.wireOp",EDGE,"E2.sketch_text.stroke-123"),sQuery(id+"F2.wireOp",EDGE,"E2.sketch_text.stroke-124"),sQuery(id+"F2.wireOp",EDGE,"E2.sketch_text.stroke-125"),sQuery(id+"F2.wireOp",EDGE,"E2.sketch_text.stroke-126"),sQuery(id+"F2.wireOp",EDGE,"E2.sketch_text.stroke-127"),sQuery(id+"F2.wireOp",EDGE,"E2.sketch_text.stroke-128"),sQuery(id+"F2.wireOp",EDGE,"E2.sketch_text.stroke-129"),sQuery(id+"F2.wireOp",EDGE,"E2.sketch_text.stroke-130"),sQuery(id+"F2.wireOp",EDGE,"E2.sketch_text.stroke-131"),sQuery(id+"F2.wireOp",EDGE,"E2.sketch_text.stroke-132"),sQuery(id+"F2.wireOp",EDGE,"E2.sketch_text.stroke-133"),sQuery(id+"F2.wireOp",EDGE,"E2.sketch_text.stroke-134"),sQuery(id+"F2.wireOp",EDGE,"E2.sketch_text.stroke-135"),sQuery(id+"F2.wireOp",EDGE,"E2.sketch_text.stroke-136"),sQuery(id+"F2.wireOp",EDGE,"E2.sketch_text.stroke-137"),sQuery(id+"F2.wireOp",EDGE,"E2.sketch_text.stroke-138"),sQuery(id+"F2.wireOp",EDGE,"E2.sketch_text.stroke-139"),sQuery(id+"F2.wireOp",EDGE,"E2.sketch_text.stroke-140"),sQuery(id+"F2.wireOp",EDGE,"E2.sketch_text.stroke-141"),sQuery(id+"F2.wireOp",EDGE,"E2.sketch_text.stroke-142"),sQuery(id+"F2.wireOp",EDGE,"E2.sketch_text.stroke-143"),sQuery(id+"F2.wireOp",EDGE,"E2.sketch_text.stroke-144"),sQuery(id+"F2.wireOp",EDGE,"E2.sketch_text.stroke-145"),sQuery(id+"F2.wireOp",EDGE,"E2.sketch_text.stroke-146"),sQuery(id+"F2.wireOp",EDGE,"E2.sketch_text.stroke-147"),sQuery(id+"F2.wireOp",EDGE,"E2.sketch_text.stroke-148"),sQuery(id+"F2.wireOp",EDGE,"E2.sketch_text.stroke-149"),sQuery(id+"F2.wireOp",EDGE,"E2.sketch_text.stroke-150"),sQuery(id+"F2.wireOp",EDGE,"E2.sketch_text.stroke-151"),sQuery(id+"F2.wireOp",EDGE,"E2.sketch_text.stroke-152"),sQuery(id+"F2.wireOp",EDGE,"E2.sketch_text.stroke-153"),sQuery(id+"F2.wireOp",EDGE,"E2.sketch_text.stroke-154"),sQuery(id+"F2.wireOp",EDGE,"E2.sketch_text.stroke-155"),sQuery(id+"F2.wireOp",EDGE,"E2.sketch_text.stroke-156"),sQuery(id+"F2.wireOp",EDGE,"E2.sketch_text.stroke-157"),sQuery(id+"F2.wireOp",EDGE,"E2.sketch_text.stroke-158"),sQuery(id+"F2.wireOp",EDGE,"E2.sketch_text.stroke-159"),sQuery(id+"F2.wireOp",EDGE,"E2.sketch_text.stroke-160"),sQuery(id+"F2.wireOp",EDGE,"E2.sketch_text.stroke-161"),sQuery(id+"F2.wireOp",EDGE,"E2.sketch_text.stroke-162"),sQuery(id+"F2.wireOp",EDGE,"E2.sketch_text.stroke-163"),sQuery(id+"F2.wireOp",EDGE,"E2.sketch_text.stroke-164"),sQuery(id+"F2.wireOp",EDGE,"E2.sketch_text.stroke-165"),sQuery(id+"F2.wireOp",EDGE,"E2.sketch_text.stroke-166"),sQuery(id+"F2.wireOp",EDGE,"E2.sketch_text.stroke-167"),sQuery(id+"F2.wireOp",EDGE,"E2.sketch_text.stroke-168"),sQuery(id+"F2.wireOp",EDGE,"E2.sketch_text.stroke-169"),sQuery(id+"F2.wireOp",EDGE,"E2.sketch_text.stroke-170"),sQuery(id+"F2.wireOp",EDGE,"E2.sketch_text.stroke-171"),sQuery(id+"F2.wireOp",EDGE,"E2.sketch_text.stroke-172"),sQuery(id+"F2.wireOp",EDGE,"E2.sketch_text.stroke-173"),sQuery(id+"F3.wireOp",EDGE,"E4.sketch_text.stroke-0"),sQuery(id+"F3.wireOp",EDGE,"E4.sketch_text.stroke-1"),sQuery(id+"F3.wireOp",EDGE,"E4.sketch_text.stroke-2"),sQuery(id+"F3.wireOp",EDGE,"E4.sketch_text.stroke-3"),sQuery(id+"F3.wireOp",EDGE,"E4.sketch_text.stroke-4"),sQuery(id+"F3.wireOp",EDGE,"E4.sketch_text.stroke-5"),sQuery(id+"F3.wireOp",EDGE,"E4.sketch_text.stroke-6"),sQuery(id+"F3.wireOp",EDGE,"E4.sketch_text.stroke-7"),sQuery(id+"F3.wireOp",EDGE,"E4.sketch_text.stroke-8"),sQuery(id+"F3.wireOp",EDGE,"E4.sketch_text.stroke-9"),sQuery(id+"F3.wireOp",EDGE,"E4.sketch_text.stroke-10"),sQuery(id+"F3.wireOp",EDGE,"E4.sketch_text.stroke-11"),sQuery(id+"F3.wireOp",EDGE,"E4.sketch_text.stroke-12"),sQuery(id+"F3.wireOp",EDGE,"E4.sketch_text.stroke-13"),sQuery(id+"F3.wireOp",EDGE,"E4.sketch_text.stroke-14"),sQuery(id+"F3.wireOp",EDGE,"E4.sketch_text.stroke-15"),sQuery(id+"F3.wireOp",EDGE,"E4.sketch_text.stroke-16"),sQuery(id+"F3.wireOp",EDGE,"E4.sketch_text.stroke-17"),sQuery(id+"F3.wireOp",EDGE,"E4.sketch_text.stroke-18"),sQuery(id+"F3.wireOp",EDGE,"E4.sketch_text.stroke-19"),sQuery(id+"F3.wireOp",EDGE,"E4.sketch_text.stroke-20"),sQuery(id+"F3.wireOp",EDGE,"E4.sketch_text.stroke-21"),sQuery(id+"F3.wireOp",EDGE,"E4.sketch_text.stroke-22"),sQuery(id+"F3.wireOp",EDGE,"E4.sketch_text.stroke-23"),sQuery(id+"F3.wireOp",EDGE,"E4.sketch_text.stroke-24"),sQuery(id+"F3.wireOp",EDGE,"E4.sketch_text.stroke-25"),sQuery(id+"F3.wireOp",EDGE,"E4.sketch_text.stroke-26"),sQuery(id+"F3.wireOp",EDGE,"E4.sketch_text.stroke-27"),sQuery(id+"F3.wireOp",EDGE,"E4.sketch_text.stroke-28"),sQuery(id+"F3.wireOp",EDGE,"E4.sketch_text.stroke-29"),sQuery(id+"F3.wireOp",EDGE,"E4.sketch_text.stroke-30"),sQuery(id+"F3.wireOp",EDGE,"E4.sketch_text.stroke-31"),sQuery(id+"F3.wireOp",EDGE,"E4.sketch_text.stroke-32"),sQuery(id+"F3.wireOp",EDGE,"E4.sketch_text.stroke-33"),sQuery(id+"F3.wireOp",EDGE,"E4.sketch_text.stroke-34"),sQuery(id+"F3.wireOp",EDGE,"E4.sketch_text.stroke-35"),sQuery(id+"F3.wireOp",EDGE,"E4.sketch_text.stroke-36"),sQuery(id+"F3.wireOp",EDGE,"E4.sketch_text.stroke-37"),sQuery(id+"F3.wireOp",EDGE,"E4.sketch_text.stroke-38"),sQuery(id+"F3.wireOp",EDGE,"E4.sketch_text.stroke-39"),sQuery(id+"F3.wireOp",EDGE,"E4.sketch_text.stroke-40"),sQuery(id+"F3.wireOp",EDGE,"E4.sketch_text.stroke-41"),sQuery(id+"F3.wireOp",EDGE,"E4.sketch_text.stroke-42"),sQuery(id+"F3.wireOp",EDGE,"E4.sketch_text.stroke-43"),sQuery(id+"F3.wireOp",EDGE,"E4.sketch_text.stroke-44"),sQuery(id+"F3.wireOp",EDGE,"E4.sketch_text.stroke-45"),sQuery(id+"F3.wireOp",EDGE,"E4.sketch_text.stroke-46"),sQuery(id+"F3.wireOp",EDGE,"E4.sketch_text.stroke-47"),sQuery(id+"F3.wireOp",EDGE,"E4.sketch_text.stroke-48"),sQuery(id+"F3.wireOp",EDGE,"E4.sketch_text.stroke-49"),sQuery(id+"F3.wireOp",EDGE,"E4.sketch_text.stroke-50"),sQuery(id+"F3.wireOp",EDGE,"E4.sketch_text.stroke-51"),sQuery(id+"F3.wireOp",EDGE,"E4.sketch_text.stroke-52"),sQuery(id+"F3.wireOp",EDGE,"E4.sketch_text.stroke-53"),sQuery(id+"F3.wireOp",EDGE,"E4.sketch_text.stroke-54"),sQuery(id+"F3.wireOp",EDGE,"E4.sketch_text.stroke-55"),sQuery(id+"F3.wireOp",EDGE,"E4.sketch_text.stroke-56"),sQuery(id+"F3.wireOp",EDGE,"E4.sketch_text.stroke-57"),sQuery(id+"F3.wireOp",EDGE,"E4.sketch_text.stroke-58"),sQuery(id+"F3.wireOp",EDGE,"E4.sketch_text.stroke-59"),sQuery(id+"F3.wireOp",EDGE,"E4.sketch_text.stroke-60"),sQuery(id+"F3.wireOp",EDGE,"E4.sketch_text.stroke-61"),sQuery(id+"F3.wireOp",EDGE,"E4.sketch_text.stroke-62"),sQuery(id+"F3.wireOp",EDGE,"E4.sketch_text.stroke-71"),sQuery(id+"F3.wireOp",EDGE,"E4.sketch_text.stroke-72"),sQuery(id+"F3.wireOp",EDGE,"E4.sketch_text.stroke-73"),sQuery(id+"F3.wireOp",EDGE,"E4.sketch_text.stroke-74"),sQuery(id+"F3.wireOp",EDGE,"E4.sketch_text.stroke-75"),sQuery(id+"F3.wireOp",EDGE,"E4.sketch_text.stroke-76"),sQuery(id+"F3.wireOp",EDGE,"E4.sketch_text.stroke-77"),sQuery(id+"F3.wireOp",EDGE,"E4.sketch_text.stroke-78"),sQuery(id+"F3.wireOp",EDGE,"E4.sketch_text.stroke-79"),sQuery(id+"F3.wireOp",EDGE,"E4.sketch_text.stroke-80"),sQuery(id+"F3.wireOp",EDGE,"E4.sketch_text.stroke-81"),sQuery(id+"F3.wireOp",EDGE,"E4.sketch_text.stroke-82"),sQuery(id+"F3.wireOp",EDGE,"E4.sketch_text.stroke-83"),sQuery(id+"F3.wireOp",EDGE,"E4.sketch_text.stroke-84"),sQuery(id+"F3.wireOp",EDGE,"E4.sketch_text.stroke-85"),sQuery(id+"F3.wireOp",EDGE,"E4.sketch_text.stroke-86"),sQuery(id+"F3.wireOp",EDGE,"E4.sketch_text.stroke-87"),sQuery(id+"F3.wireOp",EDGE,"E4.sketch_text.stroke-88"),sQuery(id+"F3.wireOp",EDGE,"E4.sketch_text.stroke-89"),sQuery(id+"F3.wireOp",EDGE,"E4.sketch_text.stroke-90"),sQuery(id+"F3.wireOp",EDGE,"E4.sketch_text.stroke-91"),sQuery(id+"F3.wireOp",EDGE,"E4.sketch_text.stroke-92"),sQuery(id+"F3.wireOp",EDGE,"E4.sketch_text.stroke-93"),sQuery(id+"F3.wireOp",EDGE,"E4.sketch_text.stroke-94"),sQuery(id+"F3.wireOp",EDGE,"E4.sketch_text.stroke-95"),sQuery(id+"F3.wireOp",EDGE,"E4.sketch_text.stroke-96"),sQuery(id+"F3.wireOp",EDGE,"E4.sketch_text.stroke-97"),sQuery(id+"F3.wireOp",EDGE,"E4.sketch_text.stroke-103"),sQuery(id+"F3.wireOp",EDGE,"E4.sketch_text.stroke-104"),sQuery(id+"F3.wireOp",EDGE,"E4.sketch_text.stroke-105"),sQuery(id+"F3.wireOp",EDGE,"E4.sketch_text.stroke-106"),sQuery(id+"F3.wireOp",EDGE,"E4.sketch_text.stroke-107"),sQuery(id+"F3.wireOp",EDGE,"E4.sketch_text.stroke-108"),sQuery(id+"F3.wireOp",EDGE,"E4.sketch_text.stroke-109"),sQuery(id+"F3.wireOp",EDGE,"E4.sketch_text.stroke-110"),sQuery(id+"F3.wireOp",EDGE,"E4.sketch_text.stroke-111"),sQuery(id+"F3.wireOp",EDGE,"E4.sketch_text.stroke-112"),sQuery(id+"F3.wireOp",EDGE,"E4.sketch_text.stroke-113"),sQuery(id+"F3.wireOp",EDGE,"E4.sketch_text.stroke-114"),sQuery(id+"F3.wireOp",EDGE,"E4.sketch_text.stroke-115"),sQuery(id+"F3.wireOp",EDGE,"E4.sketch_text.stroke-116"),sQuery(id+"F3.wireOp",EDGE,"E4.sketch_text.stroke-117"),sQuery(id+"F3.wireOp",EDGE,"E4.sketch_text.stroke-118"),sQuery(id+"F3.wireOp",EDGE,"E4.sketch_text.stroke-119"),sQuery(id+"F3.wireOp",EDGE,"E4.sketch_text.stroke-120"),sQuery(id+"F3.wireOp",EDGE,"E4.sketch_text.stroke-121"),sQuery(id+"F3.wireOp",EDGE,"E4.sketch_text.stroke-122"),sQuery(id+"F3.wireOp",EDGE,"E4.sketch_text.stroke-123"),sQuery(id+"F3.wireOp",EDGE,"E4.sketch_text.stroke-124"),sQuery(id+"F3.wireOp",EDGE,"E4.sketch_text.stroke-125"),sQuery(id+"F3.wireOp",EDGE,"E4.sketch_text.stroke-126"),sQuery(id+"F3.wireOp",EDGE,"E4.sketch_text.stroke-127"),sQuery(id+"F3.wireOp",EDGE,"E4.sketch_text.stroke-128"),sQuery(id+"F3.wireOp",EDGE,"E4.sketch_text.stroke-129"),sQuery(id+"F3.wireOp",EDGE,"E4.sketch_text.stroke-130"),sQuery(id+"F3.wireOp",EDGE,"E4.sketch_text.stroke-131"),sQuery(id+"F3.wireOp",EDGE,"E4.sketch_text.stroke-132"),sQuery(id+"F3.wireOp",EDGE,"E4.sketch_text.stroke-133"),sQuery(id+"F3.wireOp",EDGE,"E4.sketch_text.stroke-134"),sQuery(id+"F3.wireOp",EDGE,"E4.sketch_text.stroke-135"),sQuery(id+"F3.wireOp",EDGE,"E4.sketch_text.stroke-136"),sQuery(id+"F3.wireOp",EDGE,"E4.sketch_text.stroke-137"),sQuery(id+"F3.wireOp",EDGE,"E4.sketch_text.stroke-138"),sQuery(id+"F3.wireOp",EDGE,"E4.sketch_text.stroke-139"),sQuery(id+"F3.wireOp",EDGE,"E4.sketch_text.stroke-140"),sQuery(id+"F3.wireOp",EDGE,"E4.sketch_text.stroke-141"),sQuery(id+"F3.wireOp",EDGE,"E4.sketch_text.stroke-142"),sQuery(id+"F3.wireOp",EDGE,"E4.sketch_text.stroke-143"),sQuery(id+"F3.wireOp",EDGE,"E4.sketch_text.stroke-144"),sQuery(id+"F3.wireOp",EDGE,"E4.sketch_text.stroke-145"),sQuery(id+"F3.wireOp",EDGE,"E4.sketch_text.stroke-146"),sQuery(id+"F3.wireOp",EDGE,"E4.sketch_text.stroke-147"),sQuery(id+"F3.wireOp",EDGE,"E4.sketch_text.stroke-148"),sQuery(id+"F3.wireOp",EDGE,"E4.sketch_text.stroke-149"),sQuery(id+"F3.wireOp",EDGE,"E4.sketch_text.stroke-150"),sQuery(id+"F3.wireOp",EDGE,"E4.sketch_text.stroke-151"),sQuery(id+"F3.wireOp",EDGE,"E4.sketch_text.stroke-152"),sQuery(id+"F3.wireOp",EDGE,"E4.sketch_text.stroke-153"),sQuery(id+"F3.wireOp",EDGE,"E4.sketch_text.stroke-159"),sQuery(id+"F3.wireOp",EDGE,"E4.sketch_text.stroke-160"),sQuery(id+"F3.wireOp",EDGE,"E4.sketch_text.stroke-161"),sQuery(id+"F3.wireOp",EDGE,"E4.sketch_text.stroke-162"),sQuery(id+"F3.wireOp",EDGE,"E4.sketch_text.stroke-163"),sQuery(id+"F3.wireOp",EDGE,"E4.sketch_text.stroke-164"),sQuery(id+"F3.wireOp",EDGE,"E4.sketch_text.stroke-165"),sQuery(id+"F3.wireOp",EDGE,"E4.sketch_text.stroke-166"),sQuery(id+"F3.wireOp",EDGE,"E4.sketch_text.stroke-167"),sQuery(id+"F3.wireOp",EDGE,"E4.sketch_text.stroke-168"),sQuery(id+"F3.wireOp",EDGE,"E4.sketch_text.stroke-169"),sQuery(id+"F3.wireOp",EDGE,"E4.sketch_text.stroke-170"),sQuery(id+"F3.wireOp",EDGE,"E4.sketch_text.stroke-171"),sQuery(id+"F3.wireOp",EDGE,"E4.sketch_text.stroke-172"),sQuery(id+"F3.wireOp",EDGE,"E4.sketch_text.stroke-173"),sQuery(id+"F3.wireOp",EDGE,"E4.sketch_text.stroke-174"),sQuery(id+"F3.wireOp",EDGE,"E4.sketch_text.stroke-175"),sQuery(id+"F3.wireOp",EDGE,"E4.sketch_text.stroke-176"),sQuery(id+"F3.wireOp",EDGE,"E4.sketch_text.stroke-177"),sQuery(id+"F3.wireOp",EDGE,"E4.sketch_text.stroke-178"),sQuery(id+"F3.wireOp",EDGE,"E4.sketch_text.stroke-179"),sQuery(id+"F3.wireOp",EDGE,"E4.sketch_text.stroke-180"),sQuery(id+"F5.wireOp",EDGE,"8007402e-1a4e-4a06-85a5-2af08e553504"),subQ2])],"isStart":true}),makeQuery(id+"F6.opExtrude","SWEPT_FACE",FACE,{"disambiguationData":[OSD([subQ2])]})]),OD(1.0)],"derivedFrom":makeQuery(id+"F1.opExtrude","CAP_EDGE",EDGE,{"disambiguationData":[OSD([subQ0])],"isStart":false})});}
            var Q13;
            {var subQ0=sQuery(id+"F0.wireOp",EDGE,"E0.top");var subQ1=sQuery(id+"F0.wireOp",EDGE,"E0.bottom");var subQ2=sQuery(id+"F5.wireOp",EDGE,"727ac2c1-f511-4829-95a7-a443ef16a4cd");Q13=makeQuery(id+"F6.boolean.opBoolean","SPLIT",EDGE,{"disambiguationData":[TD([makeQuery(id+"F1.opExtrude","CAP_FACE",FACE,{"disambiguationData":[OSD([subQ1,subQ0,sQuery(id+"F0.wireOp",EDGE,"E0.left"),sQuery(id+"F0.wireOp",EDGE,"E0.right")])],"isStart":false}),makeQuery(id+"F1.opExtrude","SWEPT_FACE",FACE,{"disambiguationData":[OSD([subQ0])]}),makeQuery(id+"F6.opExtrude","CAP_FACE",FACE,{"disambiguationData":[OSD([subQ1,sQuery(id+"F2.wireOp",EDGE,"E2.sketch_text.stroke-0"),sQuery(id+"F2.wireOp",EDGE,"E2.sketch_text.stroke-1"),sQuery(id+"F2.wireOp",EDGE,"E2.sketch_text.stroke-2"),sQuery(id+"F2.wireOp",EDGE,"E2.sketch_text.stroke-3"),sQuery(id+"F2.wireOp",EDGE,"E2.sketch_text.stroke-4"),sQuery(id+"F2.wireOp",EDGE,"E2.sketch_text.stroke-5"),sQuery(id+"F2.wireOp",EDGE,"E2.sketch_text.stroke-6"),sQuery(id+"F2.wireOp",EDGE,"E2.sketch_text.stroke-7"),sQuery(id+"F2.wireOp",EDGE,"E2.sketch_text.stroke-8"),sQuery(id+"F2.wireOp",EDGE,"E2.sketch_text.stroke-9"),sQuery(id+"F2.wireOp",EDGE,"E2.sketch_text.stroke-10"),sQuery(id+"F2.wireOp",EDGE,"E2.sketch_text.stroke-11"),sQuery(id+"F2.wireOp",EDGE,"E2.sketch_text.stroke-12"),sQuery(id+"F2.wireOp",EDGE,"E2.sketch_text.stroke-13"),sQuery(id+"F2.wireOp",EDGE,"E2.sketch_text.stroke-14"),sQuery(id+"F2.wireOp",EDGE,"E2.sketch_text.stroke-15"),sQuery(id+"F2.wireOp",EDGE,"E2.sketch_text.stroke-16"),sQuery(id+"F2.wireOp",EDGE,"E2.sketch_text.stroke-17"),sQuery(id+"F2.wireOp",EDGE,"E2.sketch_text.stroke-18"),sQuery(id+"F2.wireOp",EDGE,"E2.sketch_text.stroke-19"),sQuery(id+"F2.wireOp",EDGE,"E2.sketch_text.stroke-20"),sQuery(id+"F2.wireOp",EDGE,"E2.sketch_text.stroke-21"),sQuery(id+"F2.wireOp",EDGE,"E2.sketch_text.stroke-22"),sQuery(id+"F2.wireOp",EDGE,"E2.sketch_text.stroke-23"),sQuery(id+"F2.wireOp",EDGE,"E2.sketch_text.stroke-24"),sQuery(id+"F2.wireOp",EDGE,"E2.sketch_text.stroke-25"),sQuery(id+"F2.wireOp",EDGE,"E2.sketch_text.stroke-26"),sQuery(id+"F2.wireOp",EDGE,"E2.sketch_text.stroke-27"),sQuery(id+"F2.wireOp",EDGE,"E2.sketch_text.stroke-28"),sQuery(id+"F2.wireOp",EDGE,"E2.sketch_text.stroke-29"),sQuery(id+"F2.wireOp",EDGE,"E2.sketch_text.stroke-30"),sQuery(id+"F2.wireOp",EDGE,"E2.sketch_text.stroke-31"),sQuery(id+"F2.wireOp",EDGE,"E2.sketch_text.stroke-32"),sQuery(id+"F2.wireOp",EDGE,"E2.sketch_text.stroke-33"),sQuery(id+"F2.wireOp",EDGE,"E2.sketch_text.stroke-34"),sQuery(id+"F2.wireOp",EDGE,"E2.sketch_text.stroke-35"),sQuery(id+"F2.wireOp",EDGE,"E2.sketch_text.stroke-36"),sQuery(id+"F2.wireOp",EDGE,"E2.sketch_text.stroke-37"),sQuery(id+"F2.wireOp",EDGE,"E2.sketch_text.stroke-38"),sQuery(id+"F2.wireOp",EDGE,"E2.sketch_text.stroke-39"),sQuery(id+"F2.wireOp",EDGE,"E2.sketch_text.stroke-40"),sQuery(id+"F2.wireOp",EDGE,"E2.sketch_text.stroke-41"),sQuery(id+"F2.wireOp",EDGE,"E2.sketch_text.stroke-42"),sQuery(id+"F2.wireOp",EDGE,"E2.sketch_text.stroke-43"),sQuery(id+"F2.wireOp",EDGE,"E2.sketch_text.stroke-44"),sQuery(id+"F2.wireOp",EDGE,"E2.sketch_text.stroke-45"),sQuery(id+"F2.wireOp",EDGE,"E2.sketch_text.stroke-46"),sQuery(id+"F2.wireOp",EDGE,"E2.sketch_text.stroke-47"),sQuery(id+"F2.wireOp",EDGE,"E2.sketch_text.stroke-48"),sQuery(id+"F2.wireOp",EDGE,"E2.sketch_text.stroke-49"),sQuery(id+"F2.wireOp",EDGE,"E2.sketch_text.stroke-50"),sQuery(id+"F2.wireOp",EDGE,"E2.sketch_text.stroke-51"),sQuery(id+"F2.wireOp",EDGE,"E2.sketch_text.stroke-52"),sQuery(id+"F2.wireOp",EDGE,"E2.sketch_text.stroke-53"),sQuery(id+"F2.wireOp",EDGE,"E2.sketch_text.stroke-54"),sQuery(id+"F2.wireOp",EDGE,"E2.sketch_text.stroke-55"),sQuery(id+"F2.wireOp",EDGE,"E2.sketch_text.stroke-56"),sQuery(id+"F2.wireOp",EDGE,"E2.sketch_text.stroke-57"),sQuery(id+"F2.wireOp",EDGE,"E2.sketch_text.stroke-58"),sQuery(id+"F2.wireOp",EDGE,"E2.sketch_text.stroke-59"),sQuery(id+"F2.wireOp",EDGE,"E2.sketch_text.stroke-60"),sQuery(id+"F2.wireOp",EDGE,"E2.sketch_text.stroke-61"),sQuery(id+"F2.wireOp",EDGE,"E2.sketch_text.stroke-62"),sQuery(id+"F2.wireOp",EDGE,"E2.sketch_text.stroke-63"),sQuery(id+"F2.wireOp",EDGE,"E2.sketch_text.stroke-64"),sQuery(id+"F2.wireOp",EDGE,"E2.sketch_text.stroke-65"),sQuery(id+"F2.wireOp",EDGE,"E2.sketch_text.stroke-66"),sQuery(id+"F2.wireOp",EDGE,"E2.sketch_text.stroke-67"),sQuery(id+"F2.wireOp",EDGE,"E2.sketch_text.stroke-68"),sQuery(id+"F2.wireOp",EDGE,"E2.sketch_text.stroke-69"),sQuery(id+"F2.wireOp",EDGE,"E2.sketch_text.stroke-70"),sQuery(id+"F2.wireOp",EDGE,"E2.sketch_text.stroke-71"),sQuery(id+"F2.wireOp",EDGE,"E2.sketch_text.stroke-72"),sQuery(id+"F2.wireOp",EDGE,"E2.sketch_text.stroke-73"),sQuery(id+"F2.wireOp",EDGE,"E2.sketch_text.stroke-74"),sQuery(id+"F2.wireOp",EDGE,"E2.sketch_text.stroke-75"),sQuery(id+"F2.wireOp",EDGE,"E2.sketch_text.stroke-76"),sQuery(id+"F2.wireOp",EDGE,"E2.sketch_text.stroke-77"),sQuery(id+"F2.wireOp",EDGE,"E2.sketch_text.stroke-78"),sQuery(id+"F2.wireOp",EDGE,"E2.sketch_text.stroke-79"),sQuery(id+"F2.wireOp",EDGE,"E2.sketch_text.stroke-80"),sQuery(id+"F2.wireOp",EDGE,"E2.sketch_text.stroke-81"),sQuery(id+"F2.wireOp",EDGE,"E2.sketch_text.stroke-82"),sQuery(id+"F2.wireOp",EDGE,"E2.sketch_text.stroke-83"),sQuery(id+"F2.wireOp",EDGE,"E2.sketch_text.stroke-84"),sQuery(id+"F2.wireOp",EDGE,"E2.sketch_text.stroke-85"),sQuery(id+"F2.wireOp",EDGE,"E2.sketch_text.stroke-86"),sQuery(id+"F2.wireOp",EDGE,"E2.sketch_text.stroke-87"),sQuery(id+"F2.wireOp",EDGE,"E2.sketch_text.stroke-88"),sQuery(id+"F2.wireOp",EDGE,"E2.sketch_text.stroke-89"),sQuery(id+"F2.wireOp",EDGE,"E2.sketch_text.stroke-90"),sQuery(id+"F2.wireOp",EDGE,"E2.sketch_text.stroke-91"),sQuery(id+"F2.wireOp",EDGE,"E2.sketch_text.stroke-92"),sQuery(id+"F2.wireOp",EDGE,"E2.sketch_text.stroke-93"),sQuery(id+"F2.wireOp",EDGE,"E2.sketch_text.stroke-94"),sQuery(id+"F2.wireOp",EDGE,"E2.sketch_text.stroke-95"),sQuery(id+"F2.wireOp",EDGE,"E2.sketch_text.stroke-96"),sQuery(id+"F2.wireOp",EDGE,"E2.sketch_text.stroke-97"),sQuery(id+"F2.wireOp",EDGE,"E2.sketch_text.stroke-98"),sQuery(id+"F2.wireOp",EDGE,"E2.sketch_text.stroke-99"),sQuery(id+"F2.wireOp",EDGE,"E2.sketch_text.stroke-100"),sQuery(id+"F2.wireOp",EDGE,"E2.sketch_text.stroke-101"),sQuery(id+"F2.wireOp",EDGE,"E2.sketch_text.stroke-102"),sQuery(id+"F2.wireOp",EDGE,"E2.sketch_text.stroke-103"),sQuery(id+"F2.wireOp",EDGE,"E2.sketch_text.stroke-104"),sQuery(id+"F2.wireOp",EDGE,"E2.sketch_text.stroke-105"),sQuery(id+"F2.wireOp",EDGE,"E2.sketch_text.stroke-106"),sQuery(id+"F2.wireOp",EDGE,"E2.sketch_text.stroke-107"),sQuery(id+"F2.wireOp",EDGE,"E2.sketch_text.stroke-108"),sQuery(id+"F2.wireOp",EDGE,"E2.sketch_text.stroke-109"),sQuery(id+"F2.wireOp",EDGE,"E2.sketch_text.stroke-110"),sQuery(id+"F2.wireOp",EDGE,"E2.sketch_text.stroke-111"),sQuery(id+"F2.wireOp",EDGE,"E2.sketch_text.stroke-112"),sQuery(id+"F2.wireOp",EDGE,"E2.sketch_text.stroke-113"),sQuery(id+"F2.wireOp",EDGE,"E2.sketch_text.stroke-114"),sQuery(id+"F2.wireOp",EDGE,"E2.sketch_text.stroke-115"),sQuery(id+"F2.wireOp",EDGE,"E2.sketch_text.stroke-116"),sQuery(id+"F2.wireOp",EDGE,"E2.sketch_text.stroke-117"),sQuery(id+"F2.wireOp",EDGE,"E2.sketch_text.stroke-118"),sQuery(id+"F2.wireOp",EDGE,"E2.sketch_text.stroke-119"),sQuery(id+"F2.wireOp",EDGE,"E2.sketch_text.stroke-120"),sQuery(id+"F2.wireOp",EDGE,"E2.sketch_text.stroke-121"),sQuery(id+"F2.wireOp",EDGE,"E2.sketch_text.stroke-122"),sQuery(id+"F2.wireOp",EDGE,"E2.sketch_text.stroke-123"),sQuery(id+"F2.wireOp",EDGE,"E2.sketch_text.stroke-124"),sQuery(id+"F2.wireOp",EDGE,"E2.sketch_text.stroke-125"),sQuery(id+"F2.wireOp",EDGE,"E2.sketch_text.stroke-126"),sQuery(id+"F2.wireOp",EDGE,"E2.sketch_text.stroke-127"),sQuery(id+"F2.wireOp",EDGE,"E2.sketch_text.stroke-128"),sQuery(id+"F2.wireOp",EDGE,"E2.sketch_text.stroke-129"),sQuery(id+"F2.wireOp",EDGE,"E2.sketch_text.stroke-130"),sQuery(id+"F2.wireOp",EDGE,"E2.sketch_text.stroke-131"),sQuery(id+"F2.wireOp",EDGE,"E2.sketch_text.stroke-132"),sQuery(id+"F2.wireOp",EDGE,"E2.sketch_text.stroke-133"),sQuery(id+"F2.wireOp",EDGE,"E2.sketch_text.stroke-134"),sQuery(id+"F2.wireOp",EDGE,"E2.sketch_text.stroke-135"),sQuery(id+"F2.wireOp",EDGE,"E2.sketch_text.stroke-136"),sQuery(id+"F2.wireOp",EDGE,"E2.sketch_text.stroke-137"),sQuery(id+"F2.wireOp",EDGE,"E2.sketch_text.stroke-138"),sQuery(id+"F2.wireOp",EDGE,"E2.sketch_text.stroke-139"),sQuery(id+"F2.wireOp",EDGE,"E2.sketch_text.stroke-140"),sQuery(id+"F2.wireOp",EDGE,"E2.sketch_text.stroke-141"),sQuery(id+"F2.wireOp",EDGE,"E2.sketch_text.stroke-142"),sQuery(id+"F2.wireOp",EDGE,"E2.sketch_text.stroke-143"),sQuery(id+"F2.wireOp",EDGE,"E2.sketch_text.stroke-144"),sQuery(id+"F2.wireOp",EDGE,"E2.sketch_text.stroke-145"),sQuery(id+"F2.wireOp",EDGE,"E2.sketch_text.stroke-146"),sQuery(id+"F2.wireOp",EDGE,"E2.sketch_text.stroke-147"),sQuery(id+"F2.wireOp",EDGE,"E2.sketch_text.stroke-148"),sQuery(id+"F2.wireOp",EDGE,"E2.sketch_text.stroke-149"),sQuery(id+"F2.wireOp",EDGE,"E2.sketch_text.stroke-150"),sQuery(id+"F2.wireOp",EDGE,"E2.sketch_text.stroke-151"),sQuery(id+"F2.wireOp",EDGE,"E2.sketch_text.stroke-152"),sQuery(id+"F2.wireOp",EDGE,"E2.sketch_text.stroke-153"),sQuery(id+"F2.wireOp",EDGE,"E2.sketch_text.stroke-154"),sQuery(id+"F2.wireOp",EDGE,"E2.sketch_text.stroke-155"),sQuery(id+"F2.wireOp",EDGE,"E2.sketch_text.stroke-156"),sQuery(id+"F2.wireOp",EDGE,"E2.sketch_text.stroke-157"),sQuery(id+"F2.wireOp",EDGE,"E2.sketch_text.stroke-158"),sQuery(id+"F2.wireOp",EDGE,"E2.sketch_text.stroke-159"),sQuery(id+"F2.wireOp",EDGE,"E2.sketch_text.stroke-160"),sQuery(id+"F2.wireOp",EDGE,"E2.sketch_text.stroke-161"),sQuery(id+"F2.wireOp",EDGE,"E2.sketch_text.stroke-162"),sQuery(id+"F2.wireOp",EDGE,"E2.sketch_text.stroke-163"),sQuery(id+"F2.wireOp",EDGE,"E2.sketch_text.stroke-164"),sQuery(id+"F2.wireOp",EDGE,"E2.sketch_text.stroke-165"),sQuery(id+"F2.wireOp",EDGE,"E2.sketch_text.stroke-166"),sQuery(id+"F2.wireOp",EDGE,"E2.sketch_text.stroke-167"),sQuery(id+"F2.wireOp",EDGE,"E2.sketch_text.stroke-168"),sQuery(id+"F2.wireOp",EDGE,"E2.sketch_text.stroke-169"),sQuery(id+"F2.wireOp",EDGE,"E2.sketch_text.stroke-170"),sQuery(id+"F2.wireOp",EDGE,"E2.sketch_text.stroke-171"),sQuery(id+"F2.wireOp",EDGE,"E2.sketch_text.stroke-172"),sQuery(id+"F2.wireOp",EDGE,"E2.sketch_text.stroke-173"),sQuery(id+"F3.wireOp",EDGE,"E4.sketch_text.stroke-0"),sQuery(id+"F3.wireOp",EDGE,"E4.sketch_text.stroke-1"),sQuery(id+"F3.wireOp",EDGE,"E4.sketch_text.stroke-2"),sQuery(id+"F3.wireOp",EDGE,"E4.sketch_text.stroke-3"),sQuery(id+"F3.wireOp",EDGE,"E4.sketch_text.stroke-4"),sQuery(id+"F3.wireOp",EDGE,"E4.sketch_text.stroke-5"),sQuery(id+"F3.wireOp",EDGE,"E4.sketch_text.stroke-6"),sQuery(id+"F3.wireOp",EDGE,"E4.sketch_text.stroke-7"),sQuery(id+"F3.wireOp",EDGE,"E4.sketch_text.stroke-8"),sQuery(id+"F3.wireOp",EDGE,"E4.sketch_text.stroke-9"),sQuery(id+"F3.wireOp",EDGE,"E4.sketch_text.stroke-10"),sQuery(id+"F3.wireOp",EDGE,"E4.sketch_text.stroke-11"),sQuery(id+"F3.wireOp",EDGE,"E4.sketch_text.stroke-12"),sQuery(id+"F3.wireOp",EDGE,"E4.sketch_text.stroke-13"),sQuery(id+"F3.wireOp",EDGE,"E4.sketch_text.stroke-14"),sQuery(id+"F3.wireOp",EDGE,"E4.sketch_text.stroke-15"),sQuery(id+"F3.wireOp",EDGE,"E4.sketch_text.stroke-16"),sQuery(id+"F3.wireOp",EDGE,"E4.sketch_text.stroke-17"),sQuery(id+"F3.wireOp",EDGE,"E4.sketch_text.stroke-18"),sQuery(id+"F3.wireOp",EDGE,"E4.sketch_text.stroke-19"),sQuery(id+"F3.wireOp",EDGE,"E4.sketch_text.stroke-20"),sQuery(id+"F3.wireOp",EDGE,"E4.sketch_text.stroke-21"),sQuery(id+"F3.wireOp",EDGE,"E4.sketch_text.stroke-22"),sQuery(id+"F3.wireOp",EDGE,"E4.sketch_text.stroke-23"),sQuery(id+"F3.wireOp",EDGE,"E4.sketch_text.stroke-24"),sQuery(id+"F3.wireOp",EDGE,"E4.sketch_text.stroke-25"),sQuery(id+"F3.wireOp",EDGE,"E4.sketch_text.stroke-26"),sQuery(id+"F3.wireOp",EDGE,"E4.sketch_text.stroke-27"),sQuery(id+"F3.wireOp",EDGE,"E4.sketch_text.stroke-28"),sQuery(id+"F3.wireOp",EDGE,"E4.sketch_text.stroke-29"),sQuery(id+"F3.wireOp",EDGE,"E4.sketch_text.stroke-30"),sQuery(id+"F3.wireOp",EDGE,"E4.sketch_text.stroke-31"),sQuery(id+"F3.wireOp",EDGE,"E4.sketch_text.stroke-32"),sQuery(id+"F3.wireOp",EDGE,"E4.sketch_text.stroke-33"),sQuery(id+"F3.wireOp",EDGE,"E4.sketch_text.stroke-34"),sQuery(id+"F3.wireOp",EDGE,"E4.sketch_text.stroke-35"),sQuery(id+"F3.wireOp",EDGE,"E4.sketch_text.stroke-36"),sQuery(id+"F3.wireOp",EDGE,"E4.sketch_text.stroke-37"),sQuery(id+"F3.wireOp",EDGE,"E4.sketch_text.stroke-38"),sQuery(id+"F3.wireOp",EDGE,"E4.sketch_text.stroke-39"),sQuery(id+"F3.wireOp",EDGE,"E4.sketch_text.stroke-40"),sQuery(id+"F3.wireOp",EDGE,"E4.sketch_text.stroke-41"),sQuery(id+"F3.wireOp",EDGE,"E4.sketch_text.stroke-42"),sQuery(id+"F3.wireOp",EDGE,"E4.sketch_text.stroke-43"),sQuery(id+"F3.wireOp",EDGE,"E4.sketch_text.stroke-44"),sQuery(id+"F3.wireOp",EDGE,"E4.sketch_text.stroke-45"),sQuery(id+"F3.wireOp",EDGE,"E4.sketch_text.stroke-46"),sQuery(id+"F3.wireOp",EDGE,"E4.sketch_text.stroke-47"),sQuery(id+"F3.wireOp",EDGE,"E4.sketch_text.stroke-48"),sQuery(id+"F3.wireOp",EDGE,"E4.sketch_text.stroke-49"),sQuery(id+"F3.wireOp",EDGE,"E4.sketch_text.stroke-50"),sQuery(id+"F3.wireOp",EDGE,"E4.sketch_text.stroke-51"),sQuery(id+"F3.wireOp",EDGE,"E4.sketch_text.stroke-52"),sQuery(id+"F3.wireOp",EDGE,"E4.sketch_text.stroke-53"),sQuery(id+"F3.wireOp",EDGE,"E4.sketch_text.stroke-54"),sQuery(id+"F3.wireOp",EDGE,"E4.sketch_text.stroke-55"),sQuery(id+"F3.wireOp",EDGE,"E4.sketch_text.stroke-56"),sQuery(id+"F3.wireOp",EDGE,"E4.sketch_text.stroke-57"),sQuery(id+"F3.wireOp",EDGE,"E4.sketch_text.stroke-58"),sQuery(id+"F3.wireOp",EDGE,"E4.sketch_text.stroke-59"),sQuery(id+"F3.wireOp",EDGE,"E4.sketch_text.stroke-60"),sQuery(id+"F3.wireOp",EDGE,"E4.sketch_text.stroke-61"),sQuery(id+"F3.wireOp",EDGE,"E4.sketch_text.stroke-62"),sQuery(id+"F3.wireOp",EDGE,"E4.sketch_text.stroke-71"),sQuery(id+"F3.wireOp",EDGE,"E4.sketch_text.stroke-72"),sQuery(id+"F3.wireOp",EDGE,"E4.sketch_text.stroke-73"),sQuery(id+"F3.wireOp",EDGE,"E4.sketch_text.stroke-74"),sQuery(id+"F3.wireOp",EDGE,"E4.sketch_text.stroke-75"),sQuery(id+"F3.wireOp",EDGE,"E4.sketch_text.stroke-76"),sQuery(id+"F3.wireOp",EDGE,"E4.sketch_text.stroke-77"),sQuery(id+"F3.wireOp",EDGE,"E4.sketch_text.stroke-78"),sQuery(id+"F3.wireOp",EDGE,"E4.sketch_text.stroke-79"),sQuery(id+"F3.wireOp",EDGE,"E4.sketch_text.stroke-80"),sQuery(id+"F3.wireOp",EDGE,"E4.sketch_text.stroke-81"),sQuery(id+"F3.wireOp",EDGE,"E4.sketch_text.stroke-82"),sQuery(id+"F3.wireOp",EDGE,"E4.sketch_text.stroke-83"),sQuery(id+"F3.wireOp",EDGE,"E4.sketch_text.stroke-84"),sQuery(id+"F3.wireOp",EDGE,"E4.sketch_text.stroke-85"),sQuery(id+"F3.wireOp",EDGE,"E4.sketch_text.stroke-86"),sQuery(id+"F3.wireOp",EDGE,"E4.sketch_text.stroke-87"),sQuery(id+"F3.wireOp",EDGE,"E4.sketch_text.stroke-88"),sQuery(id+"F3.wireOp",EDGE,"E4.sketch_text.stroke-89"),sQuery(id+"F3.wireOp",EDGE,"E4.sketch_text.stroke-90"),sQuery(id+"F3.wireOp",EDGE,"E4.sketch_text.stroke-91"),sQuery(id+"F3.wireOp",EDGE,"E4.sketch_text.stroke-92"),sQuery(id+"F3.wireOp",EDGE,"E4.sketch_text.stroke-93"),sQuery(id+"F3.wireOp",EDGE,"E4.sketch_text.stroke-94"),sQuery(id+"F3.wireOp",EDGE,"E4.sketch_text.stroke-95"),sQuery(id+"F3.wireOp",EDGE,"E4.sketch_text.stroke-96"),sQuery(id+"F3.wireOp",EDGE,"E4.sketch_text.stroke-97"),sQuery(id+"F3.wireOp",EDGE,"E4.sketch_text.stroke-103"),sQuery(id+"F3.wireOp",EDGE,"E4.sketch_text.stroke-104"),sQuery(id+"F3.wireOp",EDGE,"E4.sketch_text.stroke-105"),sQuery(id+"F3.wireOp",EDGE,"E4.sketch_text.stroke-106"),sQuery(id+"F3.wireOp",EDGE,"E4.sketch_text.stroke-107"),sQuery(id+"F3.wireOp",EDGE,"E4.sketch_text.stroke-108"),sQuery(id+"F3.wireOp",EDGE,"E4.sketch_text.stroke-109"),sQuery(id+"F3.wireOp",EDGE,"E4.sketch_text.stroke-110"),sQuery(id+"F3.wireOp",EDGE,"E4.sketch_text.stroke-111"),sQuery(id+"F3.wireOp",EDGE,"E4.sketch_text.stroke-112"),sQuery(id+"F3.wireOp",EDGE,"E4.sketch_text.stroke-113"),sQuery(id+"F3.wireOp",EDGE,"E4.sketch_text.stroke-114"),sQuery(id+"F3.wireOp",EDGE,"E4.sketch_text.stroke-115"),sQuery(id+"F3.wireOp",EDGE,"E4.sketch_text.stroke-116"),sQuery(id+"F3.wireOp",EDGE,"E4.sketch_text.stroke-117"),sQuery(id+"F3.wireOp",EDGE,"E4.sketch_text.stroke-118"),sQuery(id+"F3.wireOp",EDGE,"E4.sketch_text.stroke-119"),sQuery(id+"F3.wireOp",EDGE,"E4.sketch_text.stroke-120"),sQuery(id+"F3.wireOp",EDGE,"E4.sketch_text.stroke-121"),sQuery(id+"F3.wireOp",EDGE,"E4.sketch_text.stroke-122"),sQuery(id+"F3.wireOp",EDGE,"E4.sketch_text.stroke-123"),sQuery(id+"F3.wireOp",EDGE,"E4.sketch_text.stroke-124"),sQuery(id+"F3.wireOp",EDGE,"E4.sketch_text.stroke-125"),sQuery(id+"F3.wireOp",EDGE,"E4.sketch_text.stroke-126"),sQuery(id+"F3.wireOp",EDGE,"E4.sketch_text.stroke-127"),sQuery(id+"F3.wireOp",EDGE,"E4.sketch_text.stroke-128"),sQuery(id+"F3.wireOp",EDGE,"E4.sketch_text.stroke-129"),sQuery(id+"F3.wireOp",EDGE,"E4.sketch_text.stroke-130"),sQuery(id+"F3.wireOp",EDGE,"E4.sketch_text.stroke-131"),sQuery(id+"F3.wireOp",EDGE,"E4.sketch_text.stroke-132"),sQuery(id+"F3.wireOp",EDGE,"E4.sketch_text.stroke-133"),sQuery(id+"F3.wireOp",EDGE,"E4.sketch_text.stroke-134"),sQuery(id+"F3.wireOp",EDGE,"E4.sketch_text.stroke-135"),sQuery(id+"F3.wireOp",EDGE,"E4.sketch_text.stroke-136"),sQuery(id+"F3.wireOp",EDGE,"E4.sketch_text.stroke-137"),sQuery(id+"F3.wireOp",EDGE,"E4.sketch_text.stroke-138"),sQuery(id+"F3.wireOp",EDGE,"E4.sketch_text.stroke-139"),sQuery(id+"F3.wireOp",EDGE,"E4.sketch_text.stroke-140"),sQuery(id+"F3.wireOp",EDGE,"E4.sketch_text.stroke-141"),sQuery(id+"F3.wireOp",EDGE,"E4.sketch_text.stroke-142"),sQuery(id+"F3.wireOp",EDGE,"E4.sketch_text.stroke-143"),sQuery(id+"F3.wireOp",EDGE,"E4.sketch_text.stroke-144"),sQuery(id+"F3.wireOp",EDGE,"E4.sketch_text.stroke-145"),sQuery(id+"F3.wireOp",EDGE,"E4.sketch_text.stroke-146"),sQuery(id+"F3.wireOp",EDGE,"E4.sketch_text.stroke-147"),sQuery(id+"F3.wireOp",EDGE,"E4.sketch_text.stroke-148"),sQuery(id+"F3.wireOp",EDGE,"E4.sketch_text.stroke-149"),sQuery(id+"F3.wireOp",EDGE,"E4.sketch_text.stroke-150"),sQuery(id+"F3.wireOp",EDGE,"E4.sketch_text.stroke-151"),sQuery(id+"F3.wireOp",EDGE,"E4.sketch_text.stroke-152"),sQuery(id+"F3.wireOp",EDGE,"E4.sketch_text.stroke-153"),sQuery(id+"F3.wireOp",EDGE,"E4.sketch_text.stroke-159"),sQuery(id+"F3.wireOp",EDGE,"E4.sketch_text.stroke-160"),sQuery(id+"F3.wireOp",EDGE,"E4.sketch_text.stroke-161"),sQuery(id+"F3.wireOp",EDGE,"E4.sketch_text.stroke-162"),sQuery(id+"F3.wireOp",EDGE,"E4.sketch_text.stroke-163"),sQuery(id+"F3.wireOp",EDGE,"E4.sketch_text.stroke-164"),sQuery(id+"F3.wireOp",EDGE,"E4.sketch_text.stroke-165"),sQuery(id+"F3.wireOp",EDGE,"E4.sketch_text.stroke-166"),sQuery(id+"F3.wireOp",EDGE,"E4.sketch_text.stroke-167"),sQuery(id+"F3.wireOp",EDGE,"E4.sketch_text.stroke-168"),sQuery(id+"F3.wireOp",EDGE,"E4.sketch_text.stroke-169"),sQuery(id+"F3.wireOp",EDGE,"E4.sketch_text.stroke-170"),sQuery(id+"F3.wireOp",EDGE,"E4.sketch_text.stroke-171"),sQuery(id+"F3.wireOp",EDGE,"E4.sketch_text.stroke-172"),sQuery(id+"F3.wireOp",EDGE,"E4.sketch_text.stroke-173"),sQuery(id+"F3.wireOp",EDGE,"E4.sketch_text.stroke-174"),sQuery(id+"F3.wireOp",EDGE,"E4.sketch_text.stroke-175"),sQuery(id+"F3.wireOp",EDGE,"E4.sketch_text.stroke-176"),sQuery(id+"F3.wireOp",EDGE,"E4.sketch_text.stroke-177"),sQuery(id+"F3.wireOp",EDGE,"E4.sketch_text.stroke-178"),sQuery(id+"F3.wireOp",EDGE,"E4.sketch_text.stroke-179"),sQuery(id+"F3.wireOp",EDGE,"E4.sketch_text.stroke-180"),sQuery(id+"F5.wireOp",EDGE,"8007402e-1a4e-4a06-85a5-2af08e553504"),subQ2])],"isStart":true}),makeQuery(id+"F6.opExtrude","SWEPT_FACE",FACE,{"disambiguationData":[OSD([subQ2])]})])],"derivedFrom":makeQuery(id+"F6.opExtrude","CAP_EDGE",EDGE,{"disambiguationData":[OSD([subQ2])],"isStart":true})});}
            var Q14;
            {var subQ0=sQuery(id+"F0.wireOp",EDGE,"E0.top");var subQ1=sQuery(id+"F0.wireOp",EDGE,"E0.bottom");var subQ2=sQuery(id+"F5.wireOp",EDGE,"727ac2c1-f511-4829-95a7-a443ef16a4cd");Q14=makeQuery(id+"F6.boolean.opBoolean","SPLIT",EDGE,{"disambiguationData":[TD([makeQuery(id+"F1.opExtrude","CAP_FACE",FACE,{"disambiguationData":[OSD([subQ1,subQ0,sQuery(id+"F0.wireOp",EDGE,"E0.left"),sQuery(id+"F0.wireOp",EDGE,"E0.right")])],"isStart":false}),makeQuery(id+"F1.opExtrude","SWEPT_FACE",FACE,{"disambiguationData":[OSD([subQ0])]}),makeQuery(id+"F6.opExtrude","CAP_FACE",FACE,{"disambiguationData":[OSD([subQ1,sQuery(id+"F2.wireOp",EDGE,"E2.sketch_text.stroke-0"),sQuery(id+"F2.wireOp",EDGE,"E2.sketch_text.stroke-1"),sQuery(id+"F2.wireOp",EDGE,"E2.sketch_text.stroke-2"),sQuery(id+"F2.wireOp",EDGE,"E2.sketch_text.stroke-3"),sQuery(id+"F2.wireOp",EDGE,"E2.sketch_text.stroke-4"),sQuery(id+"F2.wireOp",EDGE,"E2.sketch_text.stroke-5"),sQuery(id+"F2.wireOp",EDGE,"E2.sketch_text.stroke-6"),sQuery(id+"F2.wireOp",EDGE,"E2.sketch_text.stroke-7"),sQuery(id+"F2.wireOp",EDGE,"E2.sketch_text.stroke-8"),sQuery(id+"F2.wireOp",EDGE,"E2.sketch_text.stroke-9"),sQuery(id+"F2.wireOp",EDGE,"E2.sketch_text.stroke-10"),sQuery(id+"F2.wireOp",EDGE,"E2.sketch_text.stroke-11"),sQuery(id+"F2.wireOp",EDGE,"E2.sketch_text.stroke-12"),sQuery(id+"F2.wireOp",EDGE,"E2.sketch_text.stroke-13"),sQuery(id+"F2.wireOp",EDGE,"E2.sketch_text.stroke-14"),sQuery(id+"F2.wireOp",EDGE,"E2.sketch_text.stroke-15"),sQuery(id+"F2.wireOp",EDGE,"E2.sketch_text.stroke-16"),sQuery(id+"F2.wireOp",EDGE,"E2.sketch_text.stroke-17"),sQuery(id+"F2.wireOp",EDGE,"E2.sketch_text.stroke-18"),sQuery(id+"F2.wireOp",EDGE,"E2.sketch_text.stroke-19"),sQuery(id+"F2.wireOp",EDGE,"E2.sketch_text.stroke-20"),sQuery(id+"F2.wireOp",EDGE,"E2.sketch_text.stroke-21"),sQuery(id+"F2.wireOp",EDGE,"E2.sketch_text.stroke-22"),sQuery(id+"F2.wireOp",EDGE,"E2.sketch_text.stroke-23"),sQuery(id+"F2.wireOp",EDGE,"E2.sketch_text.stroke-24"),sQuery(id+"F2.wireOp",EDGE,"E2.sketch_text.stroke-25"),sQuery(id+"F2.wireOp",EDGE,"E2.sketch_text.stroke-26"),sQuery(id+"F2.wireOp",EDGE,"E2.sketch_text.stroke-27"),sQuery(id+"F2.wireOp",EDGE,"E2.sketch_text.stroke-28"),sQuery(id+"F2.wireOp",EDGE,"E2.sketch_text.stroke-29"),sQuery(id+"F2.wireOp",EDGE,"E2.sketch_text.stroke-30"),sQuery(id+"F2.wireOp",EDGE,"E2.sketch_text.stroke-31"),sQuery(id+"F2.wireOp",EDGE,"E2.sketch_text.stroke-32"),sQuery(id+"F2.wireOp",EDGE,"E2.sketch_text.stroke-33"),sQuery(id+"F2.wireOp",EDGE,"E2.sketch_text.stroke-34"),sQuery(id+"F2.wireOp",EDGE,"E2.sketch_text.stroke-35"),sQuery(id+"F2.wireOp",EDGE,"E2.sketch_text.stroke-36"),sQuery(id+"F2.wireOp",EDGE,"E2.sketch_text.stroke-37"),sQuery(id+"F2.wireOp",EDGE,"E2.sketch_text.stroke-38"),sQuery(id+"F2.wireOp",EDGE,"E2.sketch_text.stroke-39"),sQuery(id+"F2.wireOp",EDGE,"E2.sketch_text.stroke-40"),sQuery(id+"F2.wireOp",EDGE,"E2.sketch_text.stroke-41"),sQuery(id+"F2.wireOp",EDGE,"E2.sketch_text.stroke-42"),sQuery(id+"F2.wireOp",EDGE,"E2.sketch_text.stroke-43"),sQuery(id+"F2.wireOp",EDGE,"E2.sketch_text.stroke-44"),sQuery(id+"F2.wireOp",EDGE,"E2.sketch_text.stroke-45"),sQuery(id+"F2.wireOp",EDGE,"E2.sketch_text.stroke-46"),sQuery(id+"F2.wireOp",EDGE,"E2.sketch_text.stroke-47"),sQuery(id+"F2.wireOp",EDGE,"E2.sketch_text.stroke-48"),sQuery(id+"F2.wireOp",EDGE,"E2.sketch_text.stroke-49"),sQuery(id+"F2.wireOp",EDGE,"E2.sketch_text.stroke-50"),sQuery(id+"F2.wireOp",EDGE,"E2.sketch_text.stroke-51"),sQuery(id+"F2.wireOp",EDGE,"E2.sketch_text.stroke-52"),sQuery(id+"F2.wireOp",EDGE,"E2.sketch_text.stroke-53"),sQuery(id+"F2.wireOp",EDGE,"E2.sketch_text.stroke-54"),sQuery(id+"F2.wireOp",EDGE,"E2.sketch_text.stroke-55"),sQuery(id+"F2.wireOp",EDGE,"E2.sketch_text.stroke-56"),sQuery(id+"F2.wireOp",EDGE,"E2.sketch_text.stroke-57"),sQuery(id+"F2.wireOp",EDGE,"E2.sketch_text.stroke-58"),sQuery(id+"F2.wireOp",EDGE,"E2.sketch_text.stroke-59"),sQuery(id+"F2.wireOp",EDGE,"E2.sketch_text.stroke-60"),sQuery(id+"F2.wireOp",EDGE,"E2.sketch_text.stroke-61"),sQuery(id+"F2.wireOp",EDGE,"E2.sketch_text.stroke-62"),sQuery(id+"F2.wireOp",EDGE,"E2.sketch_text.stroke-63"),sQuery(id+"F2.wireOp",EDGE,"E2.sketch_text.stroke-64"),sQuery(id+"F2.wireOp",EDGE,"E2.sketch_text.stroke-65"),sQuery(id+"F2.wireOp",EDGE,"E2.sketch_text.stroke-66"),sQuery(id+"F2.wireOp",EDGE,"E2.sketch_text.stroke-67"),sQuery(id+"F2.wireOp",EDGE,"E2.sketch_text.stroke-68"),sQuery(id+"F2.wireOp",EDGE,"E2.sketch_text.stroke-69"),sQuery(id+"F2.wireOp",EDGE,"E2.sketch_text.stroke-70"),sQuery(id+"F2.wireOp",EDGE,"E2.sketch_text.stroke-71"),sQuery(id+"F2.wireOp",EDGE,"E2.sketch_text.stroke-72"),sQuery(id+"F2.wireOp",EDGE,"E2.sketch_text.stroke-73"),sQuery(id+"F2.wireOp",EDGE,"E2.sketch_text.stroke-74"),sQuery(id+"F2.wireOp",EDGE,"E2.sketch_text.stroke-75"),sQuery(id+"F2.wireOp",EDGE,"E2.sketch_text.stroke-76"),sQuery(id+"F2.wireOp",EDGE,"E2.sketch_text.stroke-77"),sQuery(id+"F2.wireOp",EDGE,"E2.sketch_text.stroke-78"),sQuery(id+"F2.wireOp",EDGE,"E2.sketch_text.stroke-79"),sQuery(id+"F2.wireOp",EDGE,"E2.sketch_text.stroke-80"),sQuery(id+"F2.wireOp",EDGE,"E2.sketch_text.stroke-81"),sQuery(id+"F2.wireOp",EDGE,"E2.sketch_text.stroke-82"),sQuery(id+"F2.wireOp",EDGE,"E2.sketch_text.stroke-83"),sQuery(id+"F2.wireOp",EDGE,"E2.sketch_text.stroke-84"),sQuery(id+"F2.wireOp",EDGE,"E2.sketch_text.stroke-85"),sQuery(id+"F2.wireOp",EDGE,"E2.sketch_text.stroke-86"),sQuery(id+"F2.wireOp",EDGE,"E2.sketch_text.stroke-87"),sQuery(id+"F2.wireOp",EDGE,"E2.sketch_text.stroke-88"),sQuery(id+"F2.wireOp",EDGE,"E2.sketch_text.stroke-89"),sQuery(id+"F2.wireOp",EDGE,"E2.sketch_text.stroke-90"),sQuery(id+"F2.wireOp",EDGE,"E2.sketch_text.stroke-91"),sQuery(id+"F2.wireOp",EDGE,"E2.sketch_text.stroke-92"),sQuery(id+"F2.wireOp",EDGE,"E2.sketch_text.stroke-93"),sQuery(id+"F2.wireOp",EDGE,"E2.sketch_text.stroke-94"),sQuery(id+"F2.wireOp",EDGE,"E2.sketch_text.stroke-95"),sQuery(id+"F2.wireOp",EDGE,"E2.sketch_text.stroke-96"),sQuery(id+"F2.wireOp",EDGE,"E2.sketch_text.stroke-97"),sQuery(id+"F2.wireOp",EDGE,"E2.sketch_text.stroke-98"),sQuery(id+"F2.wireOp",EDGE,"E2.sketch_text.stroke-99"),sQuery(id+"F2.wireOp",EDGE,"E2.sketch_text.stroke-100"),sQuery(id+"F2.wireOp",EDGE,"E2.sketch_text.stroke-101"),sQuery(id+"F2.wireOp",EDGE,"E2.sketch_text.stroke-102"),sQuery(id+"F2.wireOp",EDGE,"E2.sketch_text.stroke-103"),sQuery(id+"F2.wireOp",EDGE,"E2.sketch_text.stroke-104"),sQuery(id+"F2.wireOp",EDGE,"E2.sketch_text.stroke-105"),sQuery(id+"F2.wireOp",EDGE,"E2.sketch_text.stroke-106"),sQuery(id+"F2.wireOp",EDGE,"E2.sketch_text.stroke-107"),sQuery(id+"F2.wireOp",EDGE,"E2.sketch_text.stroke-108"),sQuery(id+"F2.wireOp",EDGE,"E2.sketch_text.stroke-109"),sQuery(id+"F2.wireOp",EDGE,"E2.sketch_text.stroke-110"),sQuery(id+"F2.wireOp",EDGE,"E2.sketch_text.stroke-111"),sQuery(id+"F2.wireOp",EDGE,"E2.sketch_text.stroke-112"),sQuery(id+"F2.wireOp",EDGE,"E2.sketch_text.stroke-113"),sQuery(id+"F2.wireOp",EDGE,"E2.sketch_text.stroke-114"),sQuery(id+"F2.wireOp",EDGE,"E2.sketch_text.stroke-115"),sQuery(id+"F2.wireOp",EDGE,"E2.sketch_text.stroke-116"),sQuery(id+"F2.wireOp",EDGE,"E2.sketch_text.stroke-117"),sQuery(id+"F2.wireOp",EDGE,"E2.sketch_text.stroke-118"),sQuery(id+"F2.wireOp",EDGE,"E2.sketch_text.stroke-119"),sQuery(id+"F2.wireOp",EDGE,"E2.sketch_text.stroke-120"),sQuery(id+"F2.wireOp",EDGE,"E2.sketch_text.stroke-121"),sQuery(id+"F2.wireOp",EDGE,"E2.sketch_text.stroke-122"),sQuery(id+"F2.wireOp",EDGE,"E2.sketch_text.stroke-123"),sQuery(id+"F2.wireOp",EDGE,"E2.sketch_text.stroke-124"),sQuery(id+"F2.wireOp",EDGE,"E2.sketch_text.stroke-125"),sQuery(id+"F2.wireOp",EDGE,"E2.sketch_text.stroke-126"),sQuery(id+"F2.wireOp",EDGE,"E2.sketch_text.stroke-127"),sQuery(id+"F2.wireOp",EDGE,"E2.sketch_text.stroke-128"),sQuery(id+"F2.wireOp",EDGE,"E2.sketch_text.stroke-129"),sQuery(id+"F2.wireOp",EDGE,"E2.sketch_text.stroke-130"),sQuery(id+"F2.wireOp",EDGE,"E2.sketch_text.stroke-131"),sQuery(id+"F2.wireOp",EDGE,"E2.sketch_text.stroke-132"),sQuery(id+"F2.wireOp",EDGE,"E2.sketch_text.stroke-133"),sQuery(id+"F2.wireOp",EDGE,"E2.sketch_text.stroke-134"),sQuery(id+"F2.wireOp",EDGE,"E2.sketch_text.stroke-135"),sQuery(id+"F2.wireOp",EDGE,"E2.sketch_text.stroke-136"),sQuery(id+"F2.wireOp",EDGE,"E2.sketch_text.stroke-137"),sQuery(id+"F2.wireOp",EDGE,"E2.sketch_text.stroke-138"),sQuery(id+"F2.wireOp",EDGE,"E2.sketch_text.stroke-139"),sQuery(id+"F2.wireOp",EDGE,"E2.sketch_text.stroke-140"),sQuery(id+"F2.wireOp",EDGE,"E2.sketch_text.stroke-141"),sQuery(id+"F2.wireOp",EDGE,"E2.sketch_text.stroke-142"),sQuery(id+"F2.wireOp",EDGE,"E2.sketch_text.stroke-143"),sQuery(id+"F2.wireOp",EDGE,"E2.sketch_text.stroke-144"),sQuery(id+"F2.wireOp",EDGE,"E2.sketch_text.stroke-145"),sQuery(id+"F2.wireOp",EDGE,"E2.sketch_text.stroke-146"),sQuery(id+"F2.wireOp",EDGE,"E2.sketch_text.stroke-147"),sQuery(id+"F2.wireOp",EDGE,"E2.sketch_text.stroke-148"),sQuery(id+"F2.wireOp",EDGE,"E2.sketch_text.stroke-149"),sQuery(id+"F2.wireOp",EDGE,"E2.sketch_text.stroke-150"),sQuery(id+"F2.wireOp",EDGE,"E2.sketch_text.stroke-151"),sQuery(id+"F2.wireOp",EDGE,"E2.sketch_text.stroke-152"),sQuery(id+"F2.wireOp",EDGE,"E2.sketch_text.stroke-153"),sQuery(id+"F2.wireOp",EDGE,"E2.sketch_text.stroke-154"),sQuery(id+"F2.wireOp",EDGE,"E2.sketch_text.stroke-155"),sQuery(id+"F2.wireOp",EDGE,"E2.sketch_text.stroke-156"),sQuery(id+"F2.wireOp",EDGE,"E2.sketch_text.stroke-157"),sQuery(id+"F2.wireOp",EDGE,"E2.sketch_text.stroke-158"),sQuery(id+"F2.wireOp",EDGE,"E2.sketch_text.stroke-159"),sQuery(id+"F2.wireOp",EDGE,"E2.sketch_text.stroke-160"),sQuery(id+"F2.wireOp",EDGE,"E2.sketch_text.stroke-161"),sQuery(id+"F2.wireOp",EDGE,"E2.sketch_text.stroke-162"),sQuery(id+"F2.wireOp",EDGE,"E2.sketch_text.stroke-163"),sQuery(id+"F2.wireOp",EDGE,"E2.sketch_text.stroke-164"),sQuery(id+"F2.wireOp",EDGE,"E2.sketch_text.stroke-165"),sQuery(id+"F2.wireOp",EDGE,"E2.sketch_text.stroke-166"),sQuery(id+"F2.wireOp",EDGE,"E2.sketch_text.stroke-167"),sQuery(id+"F2.wireOp",EDGE,"E2.sketch_text.stroke-168"),sQuery(id+"F2.wireOp",EDGE,"E2.sketch_text.stroke-169"),sQuery(id+"F2.wireOp",EDGE,"E2.sketch_text.stroke-170"),sQuery(id+"F2.wireOp",EDGE,"E2.sketch_text.stroke-171"),sQuery(id+"F2.wireOp",EDGE,"E2.sketch_text.stroke-172"),sQuery(id+"F2.wireOp",EDGE,"E2.sketch_text.stroke-173"),sQuery(id+"F3.wireOp",EDGE,"E4.sketch_text.stroke-0"),sQuery(id+"F3.wireOp",EDGE,"E4.sketch_text.stroke-1"),sQuery(id+"F3.wireOp",EDGE,"E4.sketch_text.stroke-2"),sQuery(id+"F3.wireOp",EDGE,"E4.sketch_text.stroke-3"),sQuery(id+"F3.wireOp",EDGE,"E4.sketch_text.stroke-4"),sQuery(id+"F3.wireOp",EDGE,"E4.sketch_text.stroke-5"),sQuery(id+"F3.wireOp",EDGE,"E4.sketch_text.stroke-6"),sQuery(id+"F3.wireOp",EDGE,"E4.sketch_text.stroke-7"),sQuery(id+"F3.wireOp",EDGE,"E4.sketch_text.stroke-8"),sQuery(id+"F3.wireOp",EDGE,"E4.sketch_text.stroke-9"),sQuery(id+"F3.wireOp",EDGE,"E4.sketch_text.stroke-10"),sQuery(id+"F3.wireOp",EDGE,"E4.sketch_text.stroke-11"),sQuery(id+"F3.wireOp",EDGE,"E4.sketch_text.stroke-12"),sQuery(id+"F3.wireOp",EDGE,"E4.sketch_text.stroke-13"),sQuery(id+"F3.wireOp",EDGE,"E4.sketch_text.stroke-14"),sQuery(id+"F3.wireOp",EDGE,"E4.sketch_text.stroke-15"),sQuery(id+"F3.wireOp",EDGE,"E4.sketch_text.stroke-16"),sQuery(id+"F3.wireOp",EDGE,"E4.sketch_text.stroke-17"),sQuery(id+"F3.wireOp",EDGE,"E4.sketch_text.stroke-18"),sQuery(id+"F3.wireOp",EDGE,"E4.sketch_text.stroke-19"),sQuery(id+"F3.wireOp",EDGE,"E4.sketch_text.stroke-20"),sQuery(id+"F3.wireOp",EDGE,"E4.sketch_text.stroke-21"),sQuery(id+"F3.wireOp",EDGE,"E4.sketch_text.stroke-22"),sQuery(id+"F3.wireOp",EDGE,"E4.sketch_text.stroke-23"),sQuery(id+"F3.wireOp",EDGE,"E4.sketch_text.stroke-24"),sQuery(id+"F3.wireOp",EDGE,"E4.sketch_text.stroke-25"),sQuery(id+"F3.wireOp",EDGE,"E4.sketch_text.stroke-26"),sQuery(id+"F3.wireOp",EDGE,"E4.sketch_text.stroke-27"),sQuery(id+"F3.wireOp",EDGE,"E4.sketch_text.stroke-28"),sQuery(id+"F3.wireOp",EDGE,"E4.sketch_text.stroke-29"),sQuery(id+"F3.wireOp",EDGE,"E4.sketch_text.stroke-30"),sQuery(id+"F3.wireOp",EDGE,"E4.sketch_text.stroke-31"),sQuery(id+"F3.wireOp",EDGE,"E4.sketch_text.stroke-32"),sQuery(id+"F3.wireOp",EDGE,"E4.sketch_text.stroke-33"),sQuery(id+"F3.wireOp",EDGE,"E4.sketch_text.stroke-34"),sQuery(id+"F3.wireOp",EDGE,"E4.sketch_text.stroke-35"),sQuery(id+"F3.wireOp",EDGE,"E4.sketch_text.stroke-36"),sQuery(id+"F3.wireOp",EDGE,"E4.sketch_text.stroke-37"),sQuery(id+"F3.wireOp",EDGE,"E4.sketch_text.stroke-38"),sQuery(id+"F3.wireOp",EDGE,"E4.sketch_text.stroke-39"),sQuery(id+"F3.wireOp",EDGE,"E4.sketch_text.stroke-40"),sQuery(id+"F3.wireOp",EDGE,"E4.sketch_text.stroke-41"),sQuery(id+"F3.wireOp",EDGE,"E4.sketch_text.stroke-42"),sQuery(id+"F3.wireOp",EDGE,"E4.sketch_text.stroke-43"),sQuery(id+"F3.wireOp",EDGE,"E4.sketch_text.stroke-44"),sQuery(id+"F3.wireOp",EDGE,"E4.sketch_text.stroke-45"),sQuery(id+"F3.wireOp",EDGE,"E4.sketch_text.stroke-46"),sQuery(id+"F3.wireOp",EDGE,"E4.sketch_text.stroke-47"),sQuery(id+"F3.wireOp",EDGE,"E4.sketch_text.stroke-48"),sQuery(id+"F3.wireOp",EDGE,"E4.sketch_text.stroke-49"),sQuery(id+"F3.wireOp",EDGE,"E4.sketch_text.stroke-50"),sQuery(id+"F3.wireOp",EDGE,"E4.sketch_text.stroke-51"),sQuery(id+"F3.wireOp",EDGE,"E4.sketch_text.stroke-52"),sQuery(id+"F3.wireOp",EDGE,"E4.sketch_text.stroke-53"),sQuery(id+"F3.wireOp",EDGE,"E4.sketch_text.stroke-54"),sQuery(id+"F3.wireOp",EDGE,"E4.sketch_text.stroke-55"),sQuery(id+"F3.wireOp",EDGE,"E4.sketch_text.stroke-56"),sQuery(id+"F3.wireOp",EDGE,"E4.sketch_text.stroke-57"),sQuery(id+"F3.wireOp",EDGE,"E4.sketch_text.stroke-58"),sQuery(id+"F3.wireOp",EDGE,"E4.sketch_text.stroke-59"),sQuery(id+"F3.wireOp",EDGE,"E4.sketch_text.stroke-60"),sQuery(id+"F3.wireOp",EDGE,"E4.sketch_text.stroke-61"),sQuery(id+"F3.wireOp",EDGE,"E4.sketch_text.stroke-62"),sQuery(id+"F3.wireOp",EDGE,"E4.sketch_text.stroke-71"),sQuery(id+"F3.wireOp",EDGE,"E4.sketch_text.stroke-72"),sQuery(id+"F3.wireOp",EDGE,"E4.sketch_text.stroke-73"),sQuery(id+"F3.wireOp",EDGE,"E4.sketch_text.stroke-74"),sQuery(id+"F3.wireOp",EDGE,"E4.sketch_text.stroke-75"),sQuery(id+"F3.wireOp",EDGE,"E4.sketch_text.stroke-76"),sQuery(id+"F3.wireOp",EDGE,"E4.sketch_text.stroke-77"),sQuery(id+"F3.wireOp",EDGE,"E4.sketch_text.stroke-78"),sQuery(id+"F3.wireOp",EDGE,"E4.sketch_text.stroke-79"),sQuery(id+"F3.wireOp",EDGE,"E4.sketch_text.stroke-80"),sQuery(id+"F3.wireOp",EDGE,"E4.sketch_text.stroke-81"),sQuery(id+"F3.wireOp",EDGE,"E4.sketch_text.stroke-82"),sQuery(id+"F3.wireOp",EDGE,"E4.sketch_text.stroke-83"),sQuery(id+"F3.wireOp",EDGE,"E4.sketch_text.stroke-84"),sQuery(id+"F3.wireOp",EDGE,"E4.sketch_text.stroke-85"),sQuery(id+"F3.wireOp",EDGE,"E4.sketch_text.stroke-86"),sQuery(id+"F3.wireOp",EDGE,"E4.sketch_text.stroke-87"),sQuery(id+"F3.wireOp",EDGE,"E4.sketch_text.stroke-88"),sQuery(id+"F3.wireOp",EDGE,"E4.sketch_text.stroke-89"),sQuery(id+"F3.wireOp",EDGE,"E4.sketch_text.stroke-90"),sQuery(id+"F3.wireOp",EDGE,"E4.sketch_text.stroke-91"),sQuery(id+"F3.wireOp",EDGE,"E4.sketch_text.stroke-92"),sQuery(id+"F3.wireOp",EDGE,"E4.sketch_text.stroke-93"),sQuery(id+"F3.wireOp",EDGE,"E4.sketch_text.stroke-94"),sQuery(id+"F3.wireOp",EDGE,"E4.sketch_text.stroke-95"),sQuery(id+"F3.wireOp",EDGE,"E4.sketch_text.stroke-96"),sQuery(id+"F3.wireOp",EDGE,"E4.sketch_text.stroke-97"),sQuery(id+"F3.wireOp",EDGE,"E4.sketch_text.stroke-103"),sQuery(id+"F3.wireOp",EDGE,"E4.sketch_text.stroke-104"),sQuery(id+"F3.wireOp",EDGE,"E4.sketch_text.stroke-105"),sQuery(id+"F3.wireOp",EDGE,"E4.sketch_text.stroke-106"),sQuery(id+"F3.wireOp",EDGE,"E4.sketch_text.stroke-107"),sQuery(id+"F3.wireOp",EDGE,"E4.sketch_text.stroke-108"),sQuery(id+"F3.wireOp",EDGE,"E4.sketch_text.stroke-109"),sQuery(id+"F3.wireOp",EDGE,"E4.sketch_text.stroke-110"),sQuery(id+"F3.wireOp",EDGE,"E4.sketch_text.stroke-111"),sQuery(id+"F3.wireOp",EDGE,"E4.sketch_text.stroke-112"),sQuery(id+"F3.wireOp",EDGE,"E4.sketch_text.stroke-113"),sQuery(id+"F3.wireOp",EDGE,"E4.sketch_text.stroke-114"),sQuery(id+"F3.wireOp",EDGE,"E4.sketch_text.stroke-115"),sQuery(id+"F3.wireOp",EDGE,"E4.sketch_text.stroke-116"),sQuery(id+"F3.wireOp",EDGE,"E4.sketch_text.stroke-117"),sQuery(id+"F3.wireOp",EDGE,"E4.sketch_text.stroke-118"),sQuery(id+"F3.wireOp",EDGE,"E4.sketch_text.stroke-119"),sQuery(id+"F3.wireOp",EDGE,"E4.sketch_text.stroke-120"),sQuery(id+"F3.wireOp",EDGE,"E4.sketch_text.stroke-121"),sQuery(id+"F3.wireOp",EDGE,"E4.sketch_text.stroke-122"),sQuery(id+"F3.wireOp",EDGE,"E4.sketch_text.stroke-123"),sQuery(id+"F3.wireOp",EDGE,"E4.sketch_text.stroke-124"),sQuery(id+"F3.wireOp",EDGE,"E4.sketch_text.stroke-125"),sQuery(id+"F3.wireOp",EDGE,"E4.sketch_text.stroke-126"),sQuery(id+"F3.wireOp",EDGE,"E4.sketch_text.stroke-127"),sQuery(id+"F3.wireOp",EDGE,"E4.sketch_text.stroke-128"),sQuery(id+"F3.wireOp",EDGE,"E4.sketch_text.stroke-129"),sQuery(id+"F3.wireOp",EDGE,"E4.sketch_text.stroke-130"),sQuery(id+"F3.wireOp",EDGE,"E4.sketch_text.stroke-131"),sQuery(id+"F3.wireOp",EDGE,"E4.sketch_text.stroke-132"),sQuery(id+"F3.wireOp",EDGE,"E4.sketch_text.stroke-133"),sQuery(id+"F3.wireOp",EDGE,"E4.sketch_text.stroke-134"),sQuery(id+"F3.wireOp",EDGE,"E4.sketch_text.stroke-135"),sQuery(id+"F3.wireOp",EDGE,"E4.sketch_text.stroke-136"),sQuery(id+"F3.wireOp",EDGE,"E4.sketch_text.stroke-137"),sQuery(id+"F3.wireOp",EDGE,"E4.sketch_text.stroke-138"),sQuery(id+"F3.wireOp",EDGE,"E4.sketch_text.stroke-139"),sQuery(id+"F3.wireOp",EDGE,"E4.sketch_text.stroke-140"),sQuery(id+"F3.wireOp",EDGE,"E4.sketch_text.stroke-141"),sQuery(id+"F3.wireOp",EDGE,"E4.sketch_text.stroke-142"),sQuery(id+"F3.wireOp",EDGE,"E4.sketch_text.stroke-143"),sQuery(id+"F3.wireOp",EDGE,"E4.sketch_text.stroke-144"),sQuery(id+"F3.wireOp",EDGE,"E4.sketch_text.stroke-145"),sQuery(id+"F3.wireOp",EDGE,"E4.sketch_text.stroke-146"),sQuery(id+"F3.wireOp",EDGE,"E4.sketch_text.stroke-147"),sQuery(id+"F3.wireOp",EDGE,"E4.sketch_text.stroke-148"),sQuery(id+"F3.wireOp",EDGE,"E4.sketch_text.stroke-149"),sQuery(id+"F3.wireOp",EDGE,"E4.sketch_text.stroke-150"),sQuery(id+"F3.wireOp",EDGE,"E4.sketch_text.stroke-151"),sQuery(id+"F3.wireOp",EDGE,"E4.sketch_text.stroke-152"),sQuery(id+"F3.wireOp",EDGE,"E4.sketch_text.stroke-153"),sQuery(id+"F3.wireOp",EDGE,"E4.sketch_text.stroke-159"),sQuery(id+"F3.wireOp",EDGE,"E4.sketch_text.stroke-160"),sQuery(id+"F3.wireOp",EDGE,"E4.sketch_text.stroke-161"),sQuery(id+"F3.wireOp",EDGE,"E4.sketch_text.stroke-162"),sQuery(id+"F3.wireOp",EDGE,"E4.sketch_text.stroke-163"),sQuery(id+"F3.wireOp",EDGE,"E4.sketch_text.stroke-164"),sQuery(id+"F3.wireOp",EDGE,"E4.sketch_text.stroke-165"),sQuery(id+"F3.wireOp",EDGE,"E4.sketch_text.stroke-166"),sQuery(id+"F3.wireOp",EDGE,"E4.sketch_text.stroke-167"),sQuery(id+"F3.wireOp",EDGE,"E4.sketch_text.stroke-168"),sQuery(id+"F3.wireOp",EDGE,"E4.sketch_text.stroke-169"),sQuery(id+"F3.wireOp",EDGE,"E4.sketch_text.stroke-170"),sQuery(id+"F3.wireOp",EDGE,"E4.sketch_text.stroke-171"),sQuery(id+"F3.wireOp",EDGE,"E4.sketch_text.stroke-172"),sQuery(id+"F3.wireOp",EDGE,"E4.sketch_text.stroke-173"),sQuery(id+"F3.wireOp",EDGE,"E4.sketch_text.stroke-174"),sQuery(id+"F3.wireOp",EDGE,"E4.sketch_text.stroke-175"),sQuery(id+"F3.wireOp",EDGE,"E4.sketch_text.stroke-176"),sQuery(id+"F3.wireOp",EDGE,"E4.sketch_text.stroke-177"),sQuery(id+"F3.wireOp",EDGE,"E4.sketch_text.stroke-178"),sQuery(id+"F3.wireOp",EDGE,"E4.sketch_text.stroke-179"),sQuery(id+"F3.wireOp",EDGE,"E4.sketch_text.stroke-180"),sQuery(id+"F5.wireOp",EDGE,"8007402e-1a4e-4a06-85a5-2af08e553504"),subQ2])],"isStart":true}),makeQuery(id+"F6.opExtrude","SWEPT_FACE",FACE,{"disambiguationData":[OSD([subQ2])]})]),OD(1.0)],"derivedFrom":makeQuery(id+"F1.opExtrude","CAP_EDGE",EDGE,{"disambiguationData":[OSD([subQ0])],"isStart":false})});}
            var Q15;
            {var subQ0=sQuery(id+"F5.wireOp",EDGE,"8007402e-1a4e-4a06-85a5-2af08e553504");var subQ1=sQuery(id+"F0.wireOp",EDGE,"E0.top");var subQ2=sQuery(id+"F5.wireOp",EDGE,"727ac2c1-f511-4829-95a7-a443ef16a4cd");var subQ3=sQuery(id+"F0.wireOp",EDGE,"E0.bottom");Q15=makeQuery(id+"F6.boolean.opBoolean","SPLIT",EDGE,{"disambiguationData":[TD([makeQuery(id+"F1.opExtrude","CAP_FACE",FACE,{"disambiguationData":[OSD([subQ3,subQ1,sQuery(id+"F0.wireOp",EDGE,"E0.left"),sQuery(id+"F0.wireOp",EDGE,"E0.right")])],"isStart":false}),makeQuery(id+"F1.opExtrude","SWEPT_FACE",FACE,{"disambiguationData":[OSD([subQ1])]}),makeQuery(id+"F6.opExtrude","SWEPT_FACE",FACE,{"disambiguationData":[OSD([subQ0])]}),makeQuery(id+"F6.opExtrude","CAP_FACE",FACE,{"disambiguationData":[OSD([subQ3,sQuery(id+"F2.wireOp",EDGE,"E2.sketch_text.stroke-0"),sQuery(id+"F2.wireOp",EDGE,"E2.sketch_text.stroke-1"),sQuery(id+"F2.wireOp",EDGE,"E2.sketch_text.stroke-2"),sQuery(id+"F2.wireOp",EDGE,"E2.sketch_text.stroke-3"),sQuery(id+"F2.wireOp",EDGE,"E2.sketch_text.stroke-4"),sQuery(id+"F2.wireOp",EDGE,"E2.sketch_text.stroke-5"),sQuery(id+"F2.wireOp",EDGE,"E2.sketch_text.stroke-6"),sQuery(id+"F2.wireOp",EDGE,"E2.sketch_text.stroke-7"),sQuery(id+"F2.wireOp",EDGE,"E2.sketch_text.stroke-8"),sQuery(id+"F2.wireOp",EDGE,"E2.sketch_text.stroke-9"),sQuery(id+"F2.wireOp",EDGE,"E2.sketch_text.stroke-10"),sQuery(id+"F2.wireOp",EDGE,"E2.sketch_text.stroke-11"),sQuery(id+"F2.wireOp",EDGE,"E2.sketch_text.stroke-12"),sQuery(id+"F2.wireOp",EDGE,"E2.sketch_text.stroke-13"),sQuery(id+"F2.wireOp",EDGE,"E2.sketch_text.stroke-14"),sQuery(id+"F2.wireOp",EDGE,"E2.sketch_text.stroke-15"),sQuery(id+"F2.wireOp",EDGE,"E2.sketch_text.stroke-16"),sQuery(id+"F2.wireOp",EDGE,"E2.sketch_text.stroke-17"),sQuery(id+"F2.wireOp",EDGE,"E2.sketch_text.stroke-18"),sQuery(id+"F2.wireOp",EDGE,"E2.sketch_text.stroke-19"),sQuery(id+"F2.wireOp",EDGE,"E2.sketch_text.stroke-20"),sQuery(id+"F2.wireOp",EDGE,"E2.sketch_text.stroke-21"),sQuery(id+"F2.wireOp",EDGE,"E2.sketch_text.stroke-22"),sQuery(id+"F2.wireOp",EDGE,"E2.sketch_text.stroke-23"),sQuery(id+"F2.wireOp",EDGE,"E2.sketch_text.stroke-24"),sQuery(id+"F2.wireOp",EDGE,"E2.sketch_text.stroke-25"),sQuery(id+"F2.wireOp",EDGE,"E2.sketch_text.stroke-26"),sQuery(id+"F2.wireOp",EDGE,"E2.sketch_text.stroke-27"),sQuery(id+"F2.wireOp",EDGE,"E2.sketch_text.stroke-28"),sQuery(id+"F2.wireOp",EDGE,"E2.sketch_text.stroke-29"),sQuery(id+"F2.wireOp",EDGE,"E2.sketch_text.stroke-30"),sQuery(id+"F2.wireOp",EDGE,"E2.sketch_text.stroke-31"),sQuery(id+"F2.wireOp",EDGE,"E2.sketch_text.stroke-32"),sQuery(id+"F2.wireOp",EDGE,"E2.sketch_text.stroke-33"),sQuery(id+"F2.wireOp",EDGE,"E2.sketch_text.stroke-34"),sQuery(id+"F2.wireOp",EDGE,"E2.sketch_text.stroke-35"),sQuery(id+"F2.wireOp",EDGE,"E2.sketch_text.stroke-36"),sQuery(id+"F2.wireOp",EDGE,"E2.sketch_text.stroke-37"),sQuery(id+"F2.wireOp",EDGE,"E2.sketch_text.stroke-38"),sQuery(id+"F2.wireOp",EDGE,"E2.sketch_text.stroke-39"),sQuery(id+"F2.wireOp",EDGE,"E2.sketch_text.stroke-40"),sQuery(id+"F2.wireOp",EDGE,"E2.sketch_text.stroke-41"),sQuery(id+"F2.wireOp",EDGE,"E2.sketch_text.stroke-42"),sQuery(id+"F2.wireOp",EDGE,"E2.sketch_text.stroke-43"),sQuery(id+"F2.wireOp",EDGE,"E2.sketch_text.stroke-44"),sQuery(id+"F2.wireOp",EDGE,"E2.sketch_text.stroke-45"),sQuery(id+"F2.wireOp",EDGE,"E2.sketch_text.stroke-46"),sQuery(id+"F2.wireOp",EDGE,"E2.sketch_text.stroke-47"),sQuery(id+"F2.wireOp",EDGE,"E2.sketch_text.stroke-48"),sQuery(id+"F2.wireOp",EDGE,"E2.sketch_text.stroke-49"),sQuery(id+"F2.wireOp",EDGE,"E2.sketch_text.stroke-50"),sQuery(id+"F2.wireOp",EDGE,"E2.sketch_text.stroke-51"),sQuery(id+"F2.wireOp",EDGE,"E2.sketch_text.stroke-52"),sQuery(id+"F2.wireOp",EDGE,"E2.sketch_text.stroke-53"),sQuery(id+"F2.wireOp",EDGE,"E2.sketch_text.stroke-54"),sQuery(id+"F2.wireOp",EDGE,"E2.sketch_text.stroke-55"),sQuery(id+"F2.wireOp",EDGE,"E2.sketch_text.stroke-56"),sQuery(id+"F2.wireOp",EDGE,"E2.sketch_text.stroke-57"),sQuery(id+"F2.wireOp",EDGE,"E2.sketch_text.stroke-58"),sQuery(id+"F2.wireOp",EDGE,"E2.sketch_text.stroke-59"),sQuery(id+"F2.wireOp",EDGE,"E2.sketch_text.stroke-60"),sQuery(id+"F2.wireOp",EDGE,"E2.sketch_text.stroke-61"),sQuery(id+"F2.wireOp",EDGE,"E2.sketch_text.stroke-62"),sQuery(id+"F2.wireOp",EDGE,"E2.sketch_text.stroke-63"),sQuery(id+"F2.wireOp",EDGE,"E2.sketch_text.stroke-64"),sQuery(id+"F2.wireOp",EDGE,"E2.sketch_text.stroke-65"),sQuery(id+"F2.wireOp",EDGE,"E2.sketch_text.stroke-66"),sQuery(id+"F2.wireOp",EDGE,"E2.sketch_text.stroke-67"),sQuery(id+"F2.wireOp",EDGE,"E2.sketch_text.stroke-68"),sQuery(id+"F2.wireOp",EDGE,"E2.sketch_text.stroke-69"),sQuery(id+"F2.wireOp",EDGE,"E2.sketch_text.stroke-70"),sQuery(id+"F2.wireOp",EDGE,"E2.sketch_text.stroke-71"),sQuery(id+"F2.wireOp",EDGE,"E2.sketch_text.stroke-72"),sQuery(id+"F2.wireOp",EDGE,"E2.sketch_text.stroke-73"),sQuery(id+"F2.wireOp",EDGE,"E2.sketch_text.stroke-74"),sQuery(id+"F2.wireOp",EDGE,"E2.sketch_text.stroke-75"),sQuery(id+"F2.wireOp",EDGE,"E2.sketch_text.stroke-76"),sQuery(id+"F2.wireOp",EDGE,"E2.sketch_text.stroke-77"),sQuery(id+"F2.wireOp",EDGE,"E2.sketch_text.stroke-78"),sQuery(id+"F2.wireOp",EDGE,"E2.sketch_text.stroke-79"),sQuery(id+"F2.wireOp",EDGE,"E2.sketch_text.stroke-80"),sQuery(id+"F2.wireOp",EDGE,"E2.sketch_text.stroke-81"),sQuery(id+"F2.wireOp",EDGE,"E2.sketch_text.stroke-82"),sQuery(id+"F2.wireOp",EDGE,"E2.sketch_text.stroke-83"),sQuery(id+"F2.wireOp",EDGE,"E2.sketch_text.stroke-84"),sQuery(id+"F2.wireOp",EDGE,"E2.sketch_text.stroke-85"),sQuery(id+"F2.wireOp",EDGE,"E2.sketch_text.stroke-86"),sQuery(id+"F2.wireOp",EDGE,"E2.sketch_text.stroke-87"),sQuery(id+"F2.wireOp",EDGE,"E2.sketch_text.stroke-88"),sQuery(id+"F2.wireOp",EDGE,"E2.sketch_text.stroke-89"),sQuery(id+"F2.wireOp",EDGE,"E2.sketch_text.stroke-90"),sQuery(id+"F2.wireOp",EDGE,"E2.sketch_text.stroke-91"),sQuery(id+"F2.wireOp",EDGE,"E2.sketch_text.stroke-92"),sQuery(id+"F2.wireOp",EDGE,"E2.sketch_text.stroke-93"),sQuery(id+"F2.wireOp",EDGE,"E2.sketch_text.stroke-94"),sQuery(id+"F2.wireOp",EDGE,"E2.sketch_text.stroke-95"),sQuery(id+"F2.wireOp",EDGE,"E2.sketch_text.stroke-96"),sQuery(id+"F2.wireOp",EDGE,"E2.sketch_text.stroke-97"),sQuery(id+"F2.wireOp",EDGE,"E2.sketch_text.stroke-98"),sQuery(id+"F2.wireOp",EDGE,"E2.sketch_text.stroke-99"),sQuery(id+"F2.wireOp",EDGE,"E2.sketch_text.stroke-100"),sQuery(id+"F2.wireOp",EDGE,"E2.sketch_text.stroke-101"),sQuery(id+"F2.wireOp",EDGE,"E2.sketch_text.stroke-102"),sQuery(id+"F2.wireOp",EDGE,"E2.sketch_text.stroke-103"),sQuery(id+"F2.wireOp",EDGE,"E2.sketch_text.stroke-104"),sQuery(id+"F2.wireOp",EDGE,"E2.sketch_text.stroke-105"),sQuery(id+"F2.wireOp",EDGE,"E2.sketch_text.stroke-106"),sQuery(id+"F2.wireOp",EDGE,"E2.sketch_text.stroke-107"),sQuery(id+"F2.wireOp",EDGE,"E2.sketch_text.stroke-108"),sQuery(id+"F2.wireOp",EDGE,"E2.sketch_text.stroke-109"),sQuery(id+"F2.wireOp",EDGE,"E2.sketch_text.stroke-110"),sQuery(id+"F2.wireOp",EDGE,"E2.sketch_text.stroke-111"),sQuery(id+"F2.wireOp",EDGE,"E2.sketch_text.stroke-112"),sQuery(id+"F2.wireOp",EDGE,"E2.sketch_text.stroke-113"),sQuery(id+"F2.wireOp",EDGE,"E2.sketch_text.stroke-114"),sQuery(id+"F2.wireOp",EDGE,"E2.sketch_text.stroke-115"),sQuery(id+"F2.wireOp",EDGE,"E2.sketch_text.stroke-116"),sQuery(id+"F2.wireOp",EDGE,"E2.sketch_text.stroke-117"),sQuery(id+"F2.wireOp",EDGE,"E2.sketch_text.stroke-118"),sQuery(id+"F2.wireOp",EDGE,"E2.sketch_text.stroke-119"),sQuery(id+"F2.wireOp",EDGE,"E2.sketch_text.stroke-120"),sQuery(id+"F2.wireOp",EDGE,"E2.sketch_text.stroke-121"),sQuery(id+"F2.wireOp",EDGE,"E2.sketch_text.stroke-122"),sQuery(id+"F2.wireOp",EDGE,"E2.sketch_text.stroke-123"),sQuery(id+"F2.wireOp",EDGE,"E2.sketch_text.stroke-124"),sQuery(id+"F2.wireOp",EDGE,"E2.sketch_text.stroke-125"),sQuery(id+"F2.wireOp",EDGE,"E2.sketch_text.stroke-126"),sQuery(id+"F2.wireOp",EDGE,"E2.sketch_text.stroke-127"),sQuery(id+"F2.wireOp",EDGE,"E2.sketch_text.stroke-128"),sQuery(id+"F2.wireOp",EDGE,"E2.sketch_text.stroke-129"),sQuery(id+"F2.wireOp",EDGE,"E2.sketch_text.stroke-130"),sQuery(id+"F2.wireOp",EDGE,"E2.sketch_text.stroke-131"),sQuery(id+"F2.wireOp",EDGE,"E2.sketch_text.stroke-132"),sQuery(id+"F2.wireOp",EDGE,"E2.sketch_text.stroke-133"),sQuery(id+"F2.wireOp",EDGE,"E2.sketch_text.stroke-134"),sQuery(id+"F2.wireOp",EDGE,"E2.sketch_text.stroke-135"),sQuery(id+"F2.wireOp",EDGE,"E2.sketch_text.stroke-136"),sQuery(id+"F2.wireOp",EDGE,"E2.sketch_text.stroke-137"),sQuery(id+"F2.wireOp",EDGE,"E2.sketch_text.stroke-138"),sQuery(id+"F2.wireOp",EDGE,"E2.sketch_text.stroke-139"),sQuery(id+"F2.wireOp",EDGE,"E2.sketch_text.stroke-140"),sQuery(id+"F2.wireOp",EDGE,"E2.sketch_text.stroke-141"),sQuery(id+"F2.wireOp",EDGE,"E2.sketch_text.stroke-142"),sQuery(id+"F2.wireOp",EDGE,"E2.sketch_text.stroke-143"),sQuery(id+"F2.wireOp",EDGE,"E2.sketch_text.stroke-144"),sQuery(id+"F2.wireOp",EDGE,"E2.sketch_text.stroke-145"),sQuery(id+"F2.wireOp",EDGE,"E2.sketch_text.stroke-146"),sQuery(id+"F2.wireOp",EDGE,"E2.sketch_text.stroke-147"),sQuery(id+"F2.wireOp",EDGE,"E2.sketch_text.stroke-148"),sQuery(id+"F2.wireOp",EDGE,"E2.sketch_text.stroke-149"),sQuery(id+"F2.wireOp",EDGE,"E2.sketch_text.stroke-150"),sQuery(id+"F2.wireOp",EDGE,"E2.sketch_text.stroke-151"),sQuery(id+"F2.wireOp",EDGE,"E2.sketch_text.stroke-152"),sQuery(id+"F2.wireOp",EDGE,"E2.sketch_text.stroke-153"),sQuery(id+"F2.wireOp",EDGE,"E2.sketch_text.stroke-154"),sQuery(id+"F2.wireOp",EDGE,"E2.sketch_text.stroke-155"),sQuery(id+"F2.wireOp",EDGE,"E2.sketch_text.stroke-156"),sQuery(id+"F2.wireOp",EDGE,"E2.sketch_text.stroke-157"),sQuery(id+"F2.wireOp",EDGE,"E2.sketch_text.stroke-158"),sQuery(id+"F2.wireOp",EDGE,"E2.sketch_text.stroke-159"),sQuery(id+"F2.wireOp",EDGE,"E2.sketch_text.stroke-160"),sQuery(id+"F2.wireOp",EDGE,"E2.sketch_text.stroke-161"),sQuery(id+"F2.wireOp",EDGE,"E2.sketch_text.stroke-162"),sQuery(id+"F2.wireOp",EDGE,"E2.sketch_text.stroke-163"),sQuery(id+"F2.wireOp",EDGE,"E2.sketch_text.stroke-164"),sQuery(id+"F2.wireOp",EDGE,"E2.sketch_text.stroke-165"),sQuery(id+"F2.wireOp",EDGE,"E2.sketch_text.stroke-166"),sQuery(id+"F2.wireOp",EDGE,"E2.sketch_text.stroke-167"),sQuery(id+"F2.wireOp",EDGE,"E2.sketch_text.stroke-168"),sQuery(id+"F2.wireOp",EDGE,"E2.sketch_text.stroke-169"),sQuery(id+"F2.wireOp",EDGE,"E2.sketch_text.stroke-170"),sQuery(id+"F2.wireOp",EDGE,"E2.sketch_text.stroke-171"),sQuery(id+"F2.wireOp",EDGE,"E2.sketch_text.stroke-172"),sQuery(id+"F2.wireOp",EDGE,"E2.sketch_text.stroke-173"),sQuery(id+"F3.wireOp",EDGE,"E4.sketch_text.stroke-0"),sQuery(id+"F3.wireOp",EDGE,"E4.sketch_text.stroke-1"),sQuery(id+"F3.wireOp",EDGE,"E4.sketch_text.stroke-2"),sQuery(id+"F3.wireOp",EDGE,"E4.sketch_text.stroke-3"),sQuery(id+"F3.wireOp",EDGE,"E4.sketch_text.stroke-4"),sQuery(id+"F3.wireOp",EDGE,"E4.sketch_text.stroke-5"),sQuery(id+"F3.wireOp",EDGE,"E4.sketch_text.stroke-6"),sQuery(id+"F3.wireOp",EDGE,"E4.sketch_text.stroke-7"),sQuery(id+"F3.wireOp",EDGE,"E4.sketch_text.stroke-8"),sQuery(id+"F3.wireOp",EDGE,"E4.sketch_text.stroke-9"),sQuery(id+"F3.wireOp",EDGE,"E4.sketch_text.stroke-10"),sQuery(id+"F3.wireOp",EDGE,"E4.sketch_text.stroke-11"),sQuery(id+"F3.wireOp",EDGE,"E4.sketch_text.stroke-12"),sQuery(id+"F3.wireOp",EDGE,"E4.sketch_text.stroke-13"),sQuery(id+"F3.wireOp",EDGE,"E4.sketch_text.stroke-14"),sQuery(id+"F3.wireOp",EDGE,"E4.sketch_text.stroke-15"),sQuery(id+"F3.wireOp",EDGE,"E4.sketch_text.stroke-16"),sQuery(id+"F3.wireOp",EDGE,"E4.sketch_text.stroke-17"),sQuery(id+"F3.wireOp",EDGE,"E4.sketch_text.stroke-18"),sQuery(id+"F3.wireOp",EDGE,"E4.sketch_text.stroke-19"),sQuery(id+"F3.wireOp",EDGE,"E4.sketch_text.stroke-20"),sQuery(id+"F3.wireOp",EDGE,"E4.sketch_text.stroke-21"),sQuery(id+"F3.wireOp",EDGE,"E4.sketch_text.stroke-22"),sQuery(id+"F3.wireOp",EDGE,"E4.sketch_text.stroke-23"),sQuery(id+"F3.wireOp",EDGE,"E4.sketch_text.stroke-24"),sQuery(id+"F3.wireOp",EDGE,"E4.sketch_text.stroke-25"),sQuery(id+"F3.wireOp",EDGE,"E4.sketch_text.stroke-26"),sQuery(id+"F3.wireOp",EDGE,"E4.sketch_text.stroke-27"),sQuery(id+"F3.wireOp",EDGE,"E4.sketch_text.stroke-28"),sQuery(id+"F3.wireOp",EDGE,"E4.sketch_text.stroke-29"),sQuery(id+"F3.wireOp",EDGE,"E4.sketch_text.stroke-30"),sQuery(id+"F3.wireOp",EDGE,"E4.sketch_text.stroke-31"),sQuery(id+"F3.wireOp",EDGE,"E4.sketch_text.stroke-32"),sQuery(id+"F3.wireOp",EDGE,"E4.sketch_text.stroke-33"),sQuery(id+"F3.wireOp",EDGE,"E4.sketch_text.stroke-34"),sQuery(id+"F3.wireOp",EDGE,"E4.sketch_text.stroke-35"),sQuery(id+"F3.wireOp",EDGE,"E4.sketch_text.stroke-36"),sQuery(id+"F3.wireOp",EDGE,"E4.sketch_text.stroke-37"),sQuery(id+"F3.wireOp",EDGE,"E4.sketch_text.stroke-38"),sQuery(id+"F3.wireOp",EDGE,"E4.sketch_text.stroke-39"),sQuery(id+"F3.wireOp",EDGE,"E4.sketch_text.stroke-40"),sQuery(id+"F3.wireOp",EDGE,"E4.sketch_text.stroke-41"),sQuery(id+"F3.wireOp",EDGE,"E4.sketch_text.stroke-42"),sQuery(id+"F3.wireOp",EDGE,"E4.sketch_text.stroke-43"),sQuery(id+"F3.wireOp",EDGE,"E4.sketch_text.stroke-44"),sQuery(id+"F3.wireOp",EDGE,"E4.sketch_text.stroke-45"),sQuery(id+"F3.wireOp",EDGE,"E4.sketch_text.stroke-46"),sQuery(id+"F3.wireOp",EDGE,"E4.sketch_text.stroke-47"),sQuery(id+"F3.wireOp",EDGE,"E4.sketch_text.stroke-48"),sQuery(id+"F3.wireOp",EDGE,"E4.sketch_text.stroke-49"),sQuery(id+"F3.wireOp",EDGE,"E4.sketch_text.stroke-50"),sQuery(id+"F3.wireOp",EDGE,"E4.sketch_text.stroke-51"),sQuery(id+"F3.wireOp",EDGE,"E4.sketch_text.stroke-52"),sQuery(id+"F3.wireOp",EDGE,"E4.sketch_text.stroke-53"),sQuery(id+"F3.wireOp",EDGE,"E4.sketch_text.stroke-54"),sQuery(id+"F3.wireOp",EDGE,"E4.sketch_text.stroke-55"),sQuery(id+"F3.wireOp",EDGE,"E4.sketch_text.stroke-56"),sQuery(id+"F3.wireOp",EDGE,"E4.sketch_text.stroke-57"),sQuery(id+"F3.wireOp",EDGE,"E4.sketch_text.stroke-58"),sQuery(id+"F3.wireOp",EDGE,"E4.sketch_text.stroke-59"),sQuery(id+"F3.wireOp",EDGE,"E4.sketch_text.stroke-60"),sQuery(id+"F3.wireOp",EDGE,"E4.sketch_text.stroke-61"),sQuery(id+"F3.wireOp",EDGE,"E4.sketch_text.stroke-62"),sQuery(id+"F3.wireOp",EDGE,"E4.sketch_text.stroke-71"),sQuery(id+"F3.wireOp",EDGE,"E4.sketch_text.stroke-72"),sQuery(id+"F3.wireOp",EDGE,"E4.sketch_text.stroke-73"),sQuery(id+"F3.wireOp",EDGE,"E4.sketch_text.stroke-74"),sQuery(id+"F3.wireOp",EDGE,"E4.sketch_text.stroke-75"),sQuery(id+"F3.wireOp",EDGE,"E4.sketch_text.stroke-76"),sQuery(id+"F3.wireOp",EDGE,"E4.sketch_text.stroke-77"),sQuery(id+"F3.wireOp",EDGE,"E4.sketch_text.stroke-78"),sQuery(id+"F3.wireOp",EDGE,"E4.sketch_text.stroke-79"),sQuery(id+"F3.wireOp",EDGE,"E4.sketch_text.stroke-80"),sQuery(id+"F3.wireOp",EDGE,"E4.sketch_text.stroke-81"),sQuery(id+"F3.wireOp",EDGE,"E4.sketch_text.stroke-82"),sQuery(id+"F3.wireOp",EDGE,"E4.sketch_text.stroke-83"),sQuery(id+"F3.wireOp",EDGE,"E4.sketch_text.stroke-84"),sQuery(id+"F3.wireOp",EDGE,"E4.sketch_text.stroke-85"),sQuery(id+"F3.wireOp",EDGE,"E4.sketch_text.stroke-86"),sQuery(id+"F3.wireOp",EDGE,"E4.sketch_text.stroke-87"),sQuery(id+"F3.wireOp",EDGE,"E4.sketch_text.stroke-88"),sQuery(id+"F3.wireOp",EDGE,"E4.sketch_text.stroke-89"),sQuery(id+"F3.wireOp",EDGE,"E4.sketch_text.stroke-90"),sQuery(id+"F3.wireOp",EDGE,"E4.sketch_text.stroke-91"),sQuery(id+"F3.wireOp",EDGE,"E4.sketch_text.stroke-92"),sQuery(id+"F3.wireOp",EDGE,"E4.sketch_text.stroke-93"),sQuery(id+"F3.wireOp",EDGE,"E4.sketch_text.stroke-94"),sQuery(id+"F3.wireOp",EDGE,"E4.sketch_text.stroke-95"),sQuery(id+"F3.wireOp",EDGE,"E4.sketch_text.stroke-96"),sQuery(id+"F3.wireOp",EDGE,"E4.sketch_text.stroke-97"),sQuery(id+"F3.wireOp",EDGE,"E4.sketch_text.stroke-103"),sQuery(id+"F3.wireOp",EDGE,"E4.sketch_text.stroke-104"),sQuery(id+"F3.wireOp",EDGE,"E4.sketch_text.stroke-105"),sQuery(id+"F3.wireOp",EDGE,"E4.sketch_text.stroke-106"),sQuery(id+"F3.wireOp",EDGE,"E4.sketch_text.stroke-107"),sQuery(id+"F3.wireOp",EDGE,"E4.sketch_text.stroke-108"),sQuery(id+"F3.wireOp",EDGE,"E4.sketch_text.stroke-109"),sQuery(id+"F3.wireOp",EDGE,"E4.sketch_text.stroke-110"),sQuery(id+"F3.wireOp",EDGE,"E4.sketch_text.stroke-111"),sQuery(id+"F3.wireOp",EDGE,"E4.sketch_text.stroke-112"),sQuery(id+"F3.wireOp",EDGE,"E4.sketch_text.stroke-113"),sQuery(id+"F3.wireOp",EDGE,"E4.sketch_text.stroke-114"),sQuery(id+"F3.wireOp",EDGE,"E4.sketch_text.stroke-115"),sQuery(id+"F3.wireOp",EDGE,"E4.sketch_text.stroke-116"),sQuery(id+"F3.wireOp",EDGE,"E4.sketch_text.stroke-117"),sQuery(id+"F3.wireOp",EDGE,"E4.sketch_text.stroke-118"),sQuery(id+"F3.wireOp",EDGE,"E4.sketch_text.stroke-119"),sQuery(id+"F3.wireOp",EDGE,"E4.sketch_text.stroke-120"),sQuery(id+"F3.wireOp",EDGE,"E4.sketch_text.stroke-121"),sQuery(id+"F3.wireOp",EDGE,"E4.sketch_text.stroke-122"),sQuery(id+"F3.wireOp",EDGE,"E4.sketch_text.stroke-123"),sQuery(id+"F3.wireOp",EDGE,"E4.sketch_text.stroke-124"),sQuery(id+"F3.wireOp",EDGE,"E4.sketch_text.stroke-125"),sQuery(id+"F3.wireOp",EDGE,"E4.sketch_text.stroke-126"),sQuery(id+"F3.wireOp",EDGE,"E4.sketch_text.stroke-127"),sQuery(id+"F3.wireOp",EDGE,"E4.sketch_text.stroke-128"),sQuery(id+"F3.wireOp",EDGE,"E4.sketch_text.stroke-129"),sQuery(id+"F3.wireOp",EDGE,"E4.sketch_text.stroke-130"),sQuery(id+"F3.wireOp",EDGE,"E4.sketch_text.stroke-131"),sQuery(id+"F3.wireOp",EDGE,"E4.sketch_text.stroke-132"),sQuery(id+"F3.wireOp",EDGE,"E4.sketch_text.stroke-133"),sQuery(id+"F3.wireOp",EDGE,"E4.sketch_text.stroke-134"),sQuery(id+"F3.wireOp",EDGE,"E4.sketch_text.stroke-135"),sQuery(id+"F3.wireOp",EDGE,"E4.sketch_text.stroke-136"),sQuery(id+"F3.wireOp",EDGE,"E4.sketch_text.stroke-137"),sQuery(id+"F3.wireOp",EDGE,"E4.sketch_text.stroke-138"),sQuery(id+"F3.wireOp",EDGE,"E4.sketch_text.stroke-139"),sQuery(id+"F3.wireOp",EDGE,"E4.sketch_text.stroke-140"),sQuery(id+"F3.wireOp",EDGE,"E4.sketch_text.stroke-141"),sQuery(id+"F3.wireOp",EDGE,"E4.sketch_text.stroke-142"),sQuery(id+"F3.wireOp",EDGE,"E4.sketch_text.stroke-143"),sQuery(id+"F3.wireOp",EDGE,"E4.sketch_text.stroke-144"),sQuery(id+"F3.wireOp",EDGE,"E4.sketch_text.stroke-145"),sQuery(id+"F3.wireOp",EDGE,"E4.sketch_text.stroke-146"),sQuery(id+"F3.wireOp",EDGE,"E4.sketch_text.stroke-147"),sQuery(id+"F3.wireOp",EDGE,"E4.sketch_text.stroke-148"),sQuery(id+"F3.wireOp",EDGE,"E4.sketch_text.stroke-149"),sQuery(id+"F3.wireOp",EDGE,"E4.sketch_text.stroke-150"),sQuery(id+"F3.wireOp",EDGE,"E4.sketch_text.stroke-151"),sQuery(id+"F3.wireOp",EDGE,"E4.sketch_text.stroke-152"),sQuery(id+"F3.wireOp",EDGE,"E4.sketch_text.stroke-153"),sQuery(id+"F3.wireOp",EDGE,"E4.sketch_text.stroke-159"),sQuery(id+"F3.wireOp",EDGE,"E4.sketch_text.stroke-160"),sQuery(id+"F3.wireOp",EDGE,"E4.sketch_text.stroke-161"),sQuery(id+"F3.wireOp",EDGE,"E4.sketch_text.stroke-162"),sQuery(id+"F3.wireOp",EDGE,"E4.sketch_text.stroke-163"),sQuery(id+"F3.wireOp",EDGE,"E4.sketch_text.stroke-164"),sQuery(id+"F3.wireOp",EDGE,"E4.sketch_text.stroke-165"),sQuery(id+"F3.wireOp",EDGE,"E4.sketch_text.stroke-166"),sQuery(id+"F3.wireOp",EDGE,"E4.sketch_text.stroke-167"),sQuery(id+"F3.wireOp",EDGE,"E4.sketch_text.stroke-168"),sQuery(id+"F3.wireOp",EDGE,"E4.sketch_text.stroke-169"),sQuery(id+"F3.wireOp",EDGE,"E4.sketch_text.stroke-170"),sQuery(id+"F3.wireOp",EDGE,"E4.sketch_text.stroke-171"),sQuery(id+"F3.wireOp",EDGE,"E4.sketch_text.stroke-172"),sQuery(id+"F3.wireOp",EDGE,"E4.sketch_text.stroke-173"),sQuery(id+"F3.wireOp",EDGE,"E4.sketch_text.stroke-174"),sQuery(id+"F3.wireOp",EDGE,"E4.sketch_text.stroke-175"),sQuery(id+"F3.wireOp",EDGE,"E4.sketch_text.stroke-176"),sQuery(id+"F3.wireOp",EDGE,"E4.sketch_text.stroke-177"),sQuery(id+"F3.wireOp",EDGE,"E4.sketch_text.stroke-178"),sQuery(id+"F3.wireOp",EDGE,"E4.sketch_text.stroke-179"),sQuery(id+"F3.wireOp",EDGE,"E4.sketch_text.stroke-180"),subQ0,subQ2])],"isStart":true}),makeQuery(id+"F6.opExtrude","SWEPT_FACE",FACE,{"disambiguationData":[OSD([subQ2])]})])],"derivedFrom":makeQuery(id+"F6.opExtrude","CAP_EDGE",EDGE,{"disambiguationData":[OSD([subQ2])],"isStart":true})});}
            var Q16;
            {var subQ0=sQuery(id+"F0.wireOp",EDGE,"E0.top");var subQ1=sQuery(id+"F0.wireOp",EDGE,"E0.bottom");var subQ2=sQuery(id+"F5.wireOp",EDGE,"727ac2c1-f511-4829-95a7-a443ef16a4cd");Q16=makeQuery(id+"F6.boolean.opBoolean","SPLIT",EDGE,{"disambiguationData":[TD([makeQuery(id+"F1.opExtrude","CAP_FACE",FACE,{"disambiguationData":[OSD([subQ1,subQ0,sQuery(id+"F0.wireOp",EDGE,"E0.left"),sQuery(id+"F0.wireOp",EDGE,"E0.right")])],"isStart":false}),makeQuery(id+"F1.opExtrude","SWEPT_FACE",FACE,{"disambiguationData":[OSD([subQ0])]}),makeQuery(id+"F6.opExtrude","CAP_FACE",FACE,{"disambiguationData":[OSD([subQ1,sQuery(id+"F2.wireOp",EDGE,"E2.sketch_text.stroke-0"),sQuery(id+"F2.wireOp",EDGE,"E2.sketch_text.stroke-1"),sQuery(id+"F2.wireOp",EDGE,"E2.sketch_text.stroke-2"),sQuery(id+"F2.wireOp",EDGE,"E2.sketch_text.stroke-3"),sQuery(id+"F2.wireOp",EDGE,"E2.sketch_text.stroke-4"),sQuery(id+"F2.wireOp",EDGE,"E2.sketch_text.stroke-5"),sQuery(id+"F2.wireOp",EDGE,"E2.sketch_text.stroke-6"),sQuery(id+"F2.wireOp",EDGE,"E2.sketch_text.stroke-7"),sQuery(id+"F2.wireOp",EDGE,"E2.sketch_text.stroke-8"),sQuery(id+"F2.wireOp",EDGE,"E2.sketch_text.stroke-9"),sQuery(id+"F2.wireOp",EDGE,"E2.sketch_text.stroke-10"),sQuery(id+"F2.wireOp",EDGE,"E2.sketch_text.stroke-11"),sQuery(id+"F2.wireOp",EDGE,"E2.sketch_text.stroke-12"),sQuery(id+"F2.wireOp",EDGE,"E2.sketch_text.stroke-13"),sQuery(id+"F2.wireOp",EDGE,"E2.sketch_text.stroke-14"),sQuery(id+"F2.wireOp",EDGE,"E2.sketch_text.stroke-15"),sQuery(id+"F2.wireOp",EDGE,"E2.sketch_text.stroke-16"),sQuery(id+"F2.wireOp",EDGE,"E2.sketch_text.stroke-17"),sQuery(id+"F2.wireOp",EDGE,"E2.sketch_text.stroke-18"),sQuery(id+"F2.wireOp",EDGE,"E2.sketch_text.stroke-19"),sQuery(id+"F2.wireOp",EDGE,"E2.sketch_text.stroke-20"),sQuery(id+"F2.wireOp",EDGE,"E2.sketch_text.stroke-21"),sQuery(id+"F2.wireOp",EDGE,"E2.sketch_text.stroke-22"),sQuery(id+"F2.wireOp",EDGE,"E2.sketch_text.stroke-23"),sQuery(id+"F2.wireOp",EDGE,"E2.sketch_text.stroke-24"),sQuery(id+"F2.wireOp",EDGE,"E2.sketch_text.stroke-25"),sQuery(id+"F2.wireOp",EDGE,"E2.sketch_text.stroke-26"),sQuery(id+"F2.wireOp",EDGE,"E2.sketch_text.stroke-27"),sQuery(id+"F2.wireOp",EDGE,"E2.sketch_text.stroke-28"),sQuery(id+"F2.wireOp",EDGE,"E2.sketch_text.stroke-29"),sQuery(id+"F2.wireOp",EDGE,"E2.sketch_text.stroke-30"),sQuery(id+"F2.wireOp",EDGE,"E2.sketch_text.stroke-31"),sQuery(id+"F2.wireOp",EDGE,"E2.sketch_text.stroke-32"),sQuery(id+"F2.wireOp",EDGE,"E2.sketch_text.stroke-33"),sQuery(id+"F2.wireOp",EDGE,"E2.sketch_text.stroke-34"),sQuery(id+"F2.wireOp",EDGE,"E2.sketch_text.stroke-35"),sQuery(id+"F2.wireOp",EDGE,"E2.sketch_text.stroke-36"),sQuery(id+"F2.wireOp",EDGE,"E2.sketch_text.stroke-37"),sQuery(id+"F2.wireOp",EDGE,"E2.sketch_text.stroke-38"),sQuery(id+"F2.wireOp",EDGE,"E2.sketch_text.stroke-39"),sQuery(id+"F2.wireOp",EDGE,"E2.sketch_text.stroke-40"),sQuery(id+"F2.wireOp",EDGE,"E2.sketch_text.stroke-41"),sQuery(id+"F2.wireOp",EDGE,"E2.sketch_text.stroke-42"),sQuery(id+"F2.wireOp",EDGE,"E2.sketch_text.stroke-43"),sQuery(id+"F2.wireOp",EDGE,"E2.sketch_text.stroke-44"),sQuery(id+"F2.wireOp",EDGE,"E2.sketch_text.stroke-45"),sQuery(id+"F2.wireOp",EDGE,"E2.sketch_text.stroke-46"),sQuery(id+"F2.wireOp",EDGE,"E2.sketch_text.stroke-47"),sQuery(id+"F2.wireOp",EDGE,"E2.sketch_text.stroke-48"),sQuery(id+"F2.wireOp",EDGE,"E2.sketch_text.stroke-49"),sQuery(id+"F2.wireOp",EDGE,"E2.sketch_text.stroke-50"),sQuery(id+"F2.wireOp",EDGE,"E2.sketch_text.stroke-51"),sQuery(id+"F2.wireOp",EDGE,"E2.sketch_text.stroke-52"),sQuery(id+"F2.wireOp",EDGE,"E2.sketch_text.stroke-53"),sQuery(id+"F2.wireOp",EDGE,"E2.sketch_text.stroke-54"),sQuery(id+"F2.wireOp",EDGE,"E2.sketch_text.stroke-55"),sQuery(id+"F2.wireOp",EDGE,"E2.sketch_text.stroke-56"),sQuery(id+"F2.wireOp",EDGE,"E2.sketch_text.stroke-57"),sQuery(id+"F2.wireOp",EDGE,"E2.sketch_text.stroke-58"),sQuery(id+"F2.wireOp",EDGE,"E2.sketch_text.stroke-59"),sQuery(id+"F2.wireOp",EDGE,"E2.sketch_text.stroke-60"),sQuery(id+"F2.wireOp",EDGE,"E2.sketch_text.stroke-61"),sQuery(id+"F2.wireOp",EDGE,"E2.sketch_text.stroke-62"),sQuery(id+"F2.wireOp",EDGE,"E2.sketch_text.stroke-63"),sQuery(id+"F2.wireOp",EDGE,"E2.sketch_text.stroke-64"),sQuery(id+"F2.wireOp",EDGE,"E2.sketch_text.stroke-65"),sQuery(id+"F2.wireOp",EDGE,"E2.sketch_text.stroke-66"),sQuery(id+"F2.wireOp",EDGE,"E2.sketch_text.stroke-67"),sQuery(id+"F2.wireOp",EDGE,"E2.sketch_text.stroke-68"),sQuery(id+"F2.wireOp",EDGE,"E2.sketch_text.stroke-69"),sQuery(id+"F2.wireOp",EDGE,"E2.sketch_text.stroke-70"),sQuery(id+"F2.wireOp",EDGE,"E2.sketch_text.stroke-71"),sQuery(id+"F2.wireOp",EDGE,"E2.sketch_text.stroke-72"),sQuery(id+"F2.wireOp",EDGE,"E2.sketch_text.stroke-73"),sQuery(id+"F2.wireOp",EDGE,"E2.sketch_text.stroke-74"),sQuery(id+"F2.wireOp",EDGE,"E2.sketch_text.stroke-75"),sQuery(id+"F2.wireOp",EDGE,"E2.sketch_text.stroke-76"),sQuery(id+"F2.wireOp",EDGE,"E2.sketch_text.stroke-77"),sQuery(id+"F2.wireOp",EDGE,"E2.sketch_text.stroke-78"),sQuery(id+"F2.wireOp",EDGE,"E2.sketch_text.stroke-79"),sQuery(id+"F2.wireOp",EDGE,"E2.sketch_text.stroke-80"),sQuery(id+"F2.wireOp",EDGE,"E2.sketch_text.stroke-81"),sQuery(id+"F2.wireOp",EDGE,"E2.sketch_text.stroke-82"),sQuery(id+"F2.wireOp",EDGE,"E2.sketch_text.stroke-83"),sQuery(id+"F2.wireOp",EDGE,"E2.sketch_text.stroke-84"),sQuery(id+"F2.wireOp",EDGE,"E2.sketch_text.stroke-85"),sQuery(id+"F2.wireOp",EDGE,"E2.sketch_text.stroke-86"),sQuery(id+"F2.wireOp",EDGE,"E2.sketch_text.stroke-87"),sQuery(id+"F2.wireOp",EDGE,"E2.sketch_text.stroke-88"),sQuery(id+"F2.wireOp",EDGE,"E2.sketch_text.stroke-89"),sQuery(id+"F2.wireOp",EDGE,"E2.sketch_text.stroke-90"),sQuery(id+"F2.wireOp",EDGE,"E2.sketch_text.stroke-91"),sQuery(id+"F2.wireOp",EDGE,"E2.sketch_text.stroke-92"),sQuery(id+"F2.wireOp",EDGE,"E2.sketch_text.stroke-93"),sQuery(id+"F2.wireOp",EDGE,"E2.sketch_text.stroke-94"),sQuery(id+"F2.wireOp",EDGE,"E2.sketch_text.stroke-95"),sQuery(id+"F2.wireOp",EDGE,"E2.sketch_text.stroke-96"),sQuery(id+"F2.wireOp",EDGE,"E2.sketch_text.stroke-97"),sQuery(id+"F2.wireOp",EDGE,"E2.sketch_text.stroke-98"),sQuery(id+"F2.wireOp",EDGE,"E2.sketch_text.stroke-99"),sQuery(id+"F2.wireOp",EDGE,"E2.sketch_text.stroke-100"),sQuery(id+"F2.wireOp",EDGE,"E2.sketch_text.stroke-101"),sQuery(id+"F2.wireOp",EDGE,"E2.sketch_text.stroke-102"),sQuery(id+"F2.wireOp",EDGE,"E2.sketch_text.stroke-103"),sQuery(id+"F2.wireOp",EDGE,"E2.sketch_text.stroke-104"),sQuery(id+"F2.wireOp",EDGE,"E2.sketch_text.stroke-105"),sQuery(id+"F2.wireOp",EDGE,"E2.sketch_text.stroke-106"),sQuery(id+"F2.wireOp",EDGE,"E2.sketch_text.stroke-107"),sQuery(id+"F2.wireOp",EDGE,"E2.sketch_text.stroke-108"),sQuery(id+"F2.wireOp",EDGE,"E2.sketch_text.stroke-109"),sQuery(id+"F2.wireOp",EDGE,"E2.sketch_text.stroke-110"),sQuery(id+"F2.wireOp",EDGE,"E2.sketch_text.stroke-111"),sQuery(id+"F2.wireOp",EDGE,"E2.sketch_text.stroke-112"),sQuery(id+"F2.wireOp",EDGE,"E2.sketch_text.stroke-113"),sQuery(id+"F2.wireOp",EDGE,"E2.sketch_text.stroke-114"),sQuery(id+"F2.wireOp",EDGE,"E2.sketch_text.stroke-115"),sQuery(id+"F2.wireOp",EDGE,"E2.sketch_text.stroke-116"),sQuery(id+"F2.wireOp",EDGE,"E2.sketch_text.stroke-117"),sQuery(id+"F2.wireOp",EDGE,"E2.sketch_text.stroke-118"),sQuery(id+"F2.wireOp",EDGE,"E2.sketch_text.stroke-119"),sQuery(id+"F2.wireOp",EDGE,"E2.sketch_text.stroke-120"),sQuery(id+"F2.wireOp",EDGE,"E2.sketch_text.stroke-121"),sQuery(id+"F2.wireOp",EDGE,"E2.sketch_text.stroke-122"),sQuery(id+"F2.wireOp",EDGE,"E2.sketch_text.stroke-123"),sQuery(id+"F2.wireOp",EDGE,"E2.sketch_text.stroke-124"),sQuery(id+"F2.wireOp",EDGE,"E2.sketch_text.stroke-125"),sQuery(id+"F2.wireOp",EDGE,"E2.sketch_text.stroke-126"),sQuery(id+"F2.wireOp",EDGE,"E2.sketch_text.stroke-127"),sQuery(id+"F2.wireOp",EDGE,"E2.sketch_text.stroke-128"),sQuery(id+"F2.wireOp",EDGE,"E2.sketch_text.stroke-129"),sQuery(id+"F2.wireOp",EDGE,"E2.sketch_text.stroke-130"),sQuery(id+"F2.wireOp",EDGE,"E2.sketch_text.stroke-131"),sQuery(id+"F2.wireOp",EDGE,"E2.sketch_text.stroke-132"),sQuery(id+"F2.wireOp",EDGE,"E2.sketch_text.stroke-133"),sQuery(id+"F2.wireOp",EDGE,"E2.sketch_text.stroke-134"),sQuery(id+"F2.wireOp",EDGE,"E2.sketch_text.stroke-135"),sQuery(id+"F2.wireOp",EDGE,"E2.sketch_text.stroke-136"),sQuery(id+"F2.wireOp",EDGE,"E2.sketch_text.stroke-137"),sQuery(id+"F2.wireOp",EDGE,"E2.sketch_text.stroke-138"),sQuery(id+"F2.wireOp",EDGE,"E2.sketch_text.stroke-139"),sQuery(id+"F2.wireOp",EDGE,"E2.sketch_text.stroke-140"),sQuery(id+"F2.wireOp",EDGE,"E2.sketch_text.stroke-141"),sQuery(id+"F2.wireOp",EDGE,"E2.sketch_text.stroke-142"),sQuery(id+"F2.wireOp",EDGE,"E2.sketch_text.stroke-143"),sQuery(id+"F2.wireOp",EDGE,"E2.sketch_text.stroke-144"),sQuery(id+"F2.wireOp",EDGE,"E2.sketch_text.stroke-145"),sQuery(id+"F2.wireOp",EDGE,"E2.sketch_text.stroke-146"),sQuery(id+"F2.wireOp",EDGE,"E2.sketch_text.stroke-147"),sQuery(id+"F2.wireOp",EDGE,"E2.sketch_text.stroke-148"),sQuery(id+"F2.wireOp",EDGE,"E2.sketch_text.stroke-149"),sQuery(id+"F2.wireOp",EDGE,"E2.sketch_text.stroke-150"),sQuery(id+"F2.wireOp",EDGE,"E2.sketch_text.stroke-151"),sQuery(id+"F2.wireOp",EDGE,"E2.sketch_text.stroke-152"),sQuery(id+"F2.wireOp",EDGE,"E2.sketch_text.stroke-153"),sQuery(id+"F2.wireOp",EDGE,"E2.sketch_text.stroke-154"),sQuery(id+"F2.wireOp",EDGE,"E2.sketch_text.stroke-155"),sQuery(id+"F2.wireOp",EDGE,"E2.sketch_text.stroke-156"),sQuery(id+"F2.wireOp",EDGE,"E2.sketch_text.stroke-157"),sQuery(id+"F2.wireOp",EDGE,"E2.sketch_text.stroke-158"),sQuery(id+"F2.wireOp",EDGE,"E2.sketch_text.stroke-159"),sQuery(id+"F2.wireOp",EDGE,"E2.sketch_text.stroke-160"),sQuery(id+"F2.wireOp",EDGE,"E2.sketch_text.stroke-161"),sQuery(id+"F2.wireOp",EDGE,"E2.sketch_text.stroke-162"),sQuery(id+"F2.wireOp",EDGE,"E2.sketch_text.stroke-163"),sQuery(id+"F2.wireOp",EDGE,"E2.sketch_text.stroke-164"),sQuery(id+"F2.wireOp",EDGE,"E2.sketch_text.stroke-165"),sQuery(id+"F2.wireOp",EDGE,"E2.sketch_text.stroke-166"),sQuery(id+"F2.wireOp",EDGE,"E2.sketch_text.stroke-167"),sQuery(id+"F2.wireOp",EDGE,"E2.sketch_text.stroke-168"),sQuery(id+"F2.wireOp",EDGE,"E2.sketch_text.stroke-169"),sQuery(id+"F2.wireOp",EDGE,"E2.sketch_text.stroke-170"),sQuery(id+"F2.wireOp",EDGE,"E2.sketch_text.stroke-171"),sQuery(id+"F2.wireOp",EDGE,"E2.sketch_text.stroke-172"),sQuery(id+"F2.wireOp",EDGE,"E2.sketch_text.stroke-173"),sQuery(id+"F3.wireOp",EDGE,"E4.sketch_text.stroke-0"),sQuery(id+"F3.wireOp",EDGE,"E4.sketch_text.stroke-1"),sQuery(id+"F3.wireOp",EDGE,"E4.sketch_text.stroke-2"),sQuery(id+"F3.wireOp",EDGE,"E4.sketch_text.stroke-3"),sQuery(id+"F3.wireOp",EDGE,"E4.sketch_text.stroke-4"),sQuery(id+"F3.wireOp",EDGE,"E4.sketch_text.stroke-5"),sQuery(id+"F3.wireOp",EDGE,"E4.sketch_text.stroke-6"),sQuery(id+"F3.wireOp",EDGE,"E4.sketch_text.stroke-7"),sQuery(id+"F3.wireOp",EDGE,"E4.sketch_text.stroke-8"),sQuery(id+"F3.wireOp",EDGE,"E4.sketch_text.stroke-9"),sQuery(id+"F3.wireOp",EDGE,"E4.sketch_text.stroke-10"),sQuery(id+"F3.wireOp",EDGE,"E4.sketch_text.stroke-11"),sQuery(id+"F3.wireOp",EDGE,"E4.sketch_text.stroke-12"),sQuery(id+"F3.wireOp",EDGE,"E4.sketch_text.stroke-13"),sQuery(id+"F3.wireOp",EDGE,"E4.sketch_text.stroke-14"),sQuery(id+"F3.wireOp",EDGE,"E4.sketch_text.stroke-15"),sQuery(id+"F3.wireOp",EDGE,"E4.sketch_text.stroke-16"),sQuery(id+"F3.wireOp",EDGE,"E4.sketch_text.stroke-17"),sQuery(id+"F3.wireOp",EDGE,"E4.sketch_text.stroke-18"),sQuery(id+"F3.wireOp",EDGE,"E4.sketch_text.stroke-19"),sQuery(id+"F3.wireOp",EDGE,"E4.sketch_text.stroke-20"),sQuery(id+"F3.wireOp",EDGE,"E4.sketch_text.stroke-21"),sQuery(id+"F3.wireOp",EDGE,"E4.sketch_text.stroke-22"),sQuery(id+"F3.wireOp",EDGE,"E4.sketch_text.stroke-23"),sQuery(id+"F3.wireOp",EDGE,"E4.sketch_text.stroke-24"),sQuery(id+"F3.wireOp",EDGE,"E4.sketch_text.stroke-25"),sQuery(id+"F3.wireOp",EDGE,"E4.sketch_text.stroke-26"),sQuery(id+"F3.wireOp",EDGE,"E4.sketch_text.stroke-27"),sQuery(id+"F3.wireOp",EDGE,"E4.sketch_text.stroke-28"),sQuery(id+"F3.wireOp",EDGE,"E4.sketch_text.stroke-29"),sQuery(id+"F3.wireOp",EDGE,"E4.sketch_text.stroke-30"),sQuery(id+"F3.wireOp",EDGE,"E4.sketch_text.stroke-31"),sQuery(id+"F3.wireOp",EDGE,"E4.sketch_text.stroke-32"),sQuery(id+"F3.wireOp",EDGE,"E4.sketch_text.stroke-33"),sQuery(id+"F3.wireOp",EDGE,"E4.sketch_text.stroke-34"),sQuery(id+"F3.wireOp",EDGE,"E4.sketch_text.stroke-35"),sQuery(id+"F3.wireOp",EDGE,"E4.sketch_text.stroke-36"),sQuery(id+"F3.wireOp",EDGE,"E4.sketch_text.stroke-37"),sQuery(id+"F3.wireOp",EDGE,"E4.sketch_text.stroke-38"),sQuery(id+"F3.wireOp",EDGE,"E4.sketch_text.stroke-39"),sQuery(id+"F3.wireOp",EDGE,"E4.sketch_text.stroke-40"),sQuery(id+"F3.wireOp",EDGE,"E4.sketch_text.stroke-41"),sQuery(id+"F3.wireOp",EDGE,"E4.sketch_text.stroke-42"),sQuery(id+"F3.wireOp",EDGE,"E4.sketch_text.stroke-43"),sQuery(id+"F3.wireOp",EDGE,"E4.sketch_text.stroke-44"),sQuery(id+"F3.wireOp",EDGE,"E4.sketch_text.stroke-45"),sQuery(id+"F3.wireOp",EDGE,"E4.sketch_text.stroke-46"),sQuery(id+"F3.wireOp",EDGE,"E4.sketch_text.stroke-47"),sQuery(id+"F3.wireOp",EDGE,"E4.sketch_text.stroke-48"),sQuery(id+"F3.wireOp",EDGE,"E4.sketch_text.stroke-49"),sQuery(id+"F3.wireOp",EDGE,"E4.sketch_text.stroke-50"),sQuery(id+"F3.wireOp",EDGE,"E4.sketch_text.stroke-51"),sQuery(id+"F3.wireOp",EDGE,"E4.sketch_text.stroke-52"),sQuery(id+"F3.wireOp",EDGE,"E4.sketch_text.stroke-53"),sQuery(id+"F3.wireOp",EDGE,"E4.sketch_text.stroke-54"),sQuery(id+"F3.wireOp",EDGE,"E4.sketch_text.stroke-55"),sQuery(id+"F3.wireOp",EDGE,"E4.sketch_text.stroke-56"),sQuery(id+"F3.wireOp",EDGE,"E4.sketch_text.stroke-57"),sQuery(id+"F3.wireOp",EDGE,"E4.sketch_text.stroke-58"),sQuery(id+"F3.wireOp",EDGE,"E4.sketch_text.stroke-59"),sQuery(id+"F3.wireOp",EDGE,"E4.sketch_text.stroke-60"),sQuery(id+"F3.wireOp",EDGE,"E4.sketch_text.stroke-61"),sQuery(id+"F3.wireOp",EDGE,"E4.sketch_text.stroke-62"),sQuery(id+"F3.wireOp",EDGE,"E4.sketch_text.stroke-71"),sQuery(id+"F3.wireOp",EDGE,"E4.sketch_text.stroke-72"),sQuery(id+"F3.wireOp",EDGE,"E4.sketch_text.stroke-73"),sQuery(id+"F3.wireOp",EDGE,"E4.sketch_text.stroke-74"),sQuery(id+"F3.wireOp",EDGE,"E4.sketch_text.stroke-75"),sQuery(id+"F3.wireOp",EDGE,"E4.sketch_text.stroke-76"),sQuery(id+"F3.wireOp",EDGE,"E4.sketch_text.stroke-77"),sQuery(id+"F3.wireOp",EDGE,"E4.sketch_text.stroke-78"),sQuery(id+"F3.wireOp",EDGE,"E4.sketch_text.stroke-79"),sQuery(id+"F3.wireOp",EDGE,"E4.sketch_text.stroke-80"),sQuery(id+"F3.wireOp",EDGE,"E4.sketch_text.stroke-81"),sQuery(id+"F3.wireOp",EDGE,"E4.sketch_text.stroke-82"),sQuery(id+"F3.wireOp",EDGE,"E4.sketch_text.stroke-83"),sQuery(id+"F3.wireOp",EDGE,"E4.sketch_text.stroke-84"),sQuery(id+"F3.wireOp",EDGE,"E4.sketch_text.stroke-85"),sQuery(id+"F3.wireOp",EDGE,"E4.sketch_text.stroke-86"),sQuery(id+"F3.wireOp",EDGE,"E4.sketch_text.stroke-87"),sQuery(id+"F3.wireOp",EDGE,"E4.sketch_text.stroke-88"),sQuery(id+"F3.wireOp",EDGE,"E4.sketch_text.stroke-89"),sQuery(id+"F3.wireOp",EDGE,"E4.sketch_text.stroke-90"),sQuery(id+"F3.wireOp",EDGE,"E4.sketch_text.stroke-91"),sQuery(id+"F3.wireOp",EDGE,"E4.sketch_text.stroke-92"),sQuery(id+"F3.wireOp",EDGE,"E4.sketch_text.stroke-93"),sQuery(id+"F3.wireOp",EDGE,"E4.sketch_text.stroke-94"),sQuery(id+"F3.wireOp",EDGE,"E4.sketch_text.stroke-95"),sQuery(id+"F3.wireOp",EDGE,"E4.sketch_text.stroke-96"),sQuery(id+"F3.wireOp",EDGE,"E4.sketch_text.stroke-97"),sQuery(id+"F3.wireOp",EDGE,"E4.sketch_text.stroke-103"),sQuery(id+"F3.wireOp",EDGE,"E4.sketch_text.stroke-104"),sQuery(id+"F3.wireOp",EDGE,"E4.sketch_text.stroke-105"),sQuery(id+"F3.wireOp",EDGE,"E4.sketch_text.stroke-106"),sQuery(id+"F3.wireOp",EDGE,"E4.sketch_text.stroke-107"),sQuery(id+"F3.wireOp",EDGE,"E4.sketch_text.stroke-108"),sQuery(id+"F3.wireOp",EDGE,"E4.sketch_text.stroke-109"),sQuery(id+"F3.wireOp",EDGE,"E4.sketch_text.stroke-110"),sQuery(id+"F3.wireOp",EDGE,"E4.sketch_text.stroke-111"),sQuery(id+"F3.wireOp",EDGE,"E4.sketch_text.stroke-112"),sQuery(id+"F3.wireOp",EDGE,"E4.sketch_text.stroke-113"),sQuery(id+"F3.wireOp",EDGE,"E4.sketch_text.stroke-114"),sQuery(id+"F3.wireOp",EDGE,"E4.sketch_text.stroke-115"),sQuery(id+"F3.wireOp",EDGE,"E4.sketch_text.stroke-116"),sQuery(id+"F3.wireOp",EDGE,"E4.sketch_text.stroke-117"),sQuery(id+"F3.wireOp",EDGE,"E4.sketch_text.stroke-118"),sQuery(id+"F3.wireOp",EDGE,"E4.sketch_text.stroke-119"),sQuery(id+"F3.wireOp",EDGE,"E4.sketch_text.stroke-120"),sQuery(id+"F3.wireOp",EDGE,"E4.sketch_text.stroke-121"),sQuery(id+"F3.wireOp",EDGE,"E4.sketch_text.stroke-122"),sQuery(id+"F3.wireOp",EDGE,"E4.sketch_text.stroke-123"),sQuery(id+"F3.wireOp",EDGE,"E4.sketch_text.stroke-124"),sQuery(id+"F3.wireOp",EDGE,"E4.sketch_text.stroke-125"),sQuery(id+"F3.wireOp",EDGE,"E4.sketch_text.stroke-126"),sQuery(id+"F3.wireOp",EDGE,"E4.sketch_text.stroke-127"),sQuery(id+"F3.wireOp",EDGE,"E4.sketch_text.stroke-128"),sQuery(id+"F3.wireOp",EDGE,"E4.sketch_text.stroke-129"),sQuery(id+"F3.wireOp",EDGE,"E4.sketch_text.stroke-130"),sQuery(id+"F3.wireOp",EDGE,"E4.sketch_text.stroke-131"),sQuery(id+"F3.wireOp",EDGE,"E4.sketch_text.stroke-132"),sQuery(id+"F3.wireOp",EDGE,"E4.sketch_text.stroke-133"),sQuery(id+"F3.wireOp",EDGE,"E4.sketch_text.stroke-134"),sQuery(id+"F3.wireOp",EDGE,"E4.sketch_text.stroke-135"),sQuery(id+"F3.wireOp",EDGE,"E4.sketch_text.stroke-136"),sQuery(id+"F3.wireOp",EDGE,"E4.sketch_text.stroke-137"),sQuery(id+"F3.wireOp",EDGE,"E4.sketch_text.stroke-138"),sQuery(id+"F3.wireOp",EDGE,"E4.sketch_text.stroke-139"),sQuery(id+"F3.wireOp",EDGE,"E4.sketch_text.stroke-140"),sQuery(id+"F3.wireOp",EDGE,"E4.sketch_text.stroke-141"),sQuery(id+"F3.wireOp",EDGE,"E4.sketch_text.stroke-142"),sQuery(id+"F3.wireOp",EDGE,"E4.sketch_text.stroke-143"),sQuery(id+"F3.wireOp",EDGE,"E4.sketch_text.stroke-144"),sQuery(id+"F3.wireOp",EDGE,"E4.sketch_text.stroke-145"),sQuery(id+"F3.wireOp",EDGE,"E4.sketch_text.stroke-146"),sQuery(id+"F3.wireOp",EDGE,"E4.sketch_text.stroke-147"),sQuery(id+"F3.wireOp",EDGE,"E4.sketch_text.stroke-148"),sQuery(id+"F3.wireOp",EDGE,"E4.sketch_text.stroke-149"),sQuery(id+"F3.wireOp",EDGE,"E4.sketch_text.stroke-150"),sQuery(id+"F3.wireOp",EDGE,"E4.sketch_text.stroke-151"),sQuery(id+"F3.wireOp",EDGE,"E4.sketch_text.stroke-152"),sQuery(id+"F3.wireOp",EDGE,"E4.sketch_text.stroke-153"),sQuery(id+"F3.wireOp",EDGE,"E4.sketch_text.stroke-159"),sQuery(id+"F3.wireOp",EDGE,"E4.sketch_text.stroke-160"),sQuery(id+"F3.wireOp",EDGE,"E4.sketch_text.stroke-161"),sQuery(id+"F3.wireOp",EDGE,"E4.sketch_text.stroke-162"),sQuery(id+"F3.wireOp",EDGE,"E4.sketch_text.stroke-163"),sQuery(id+"F3.wireOp",EDGE,"E4.sketch_text.stroke-164"),sQuery(id+"F3.wireOp",EDGE,"E4.sketch_text.stroke-165"),sQuery(id+"F3.wireOp",EDGE,"E4.sketch_text.stroke-166"),sQuery(id+"F3.wireOp",EDGE,"E4.sketch_text.stroke-167"),sQuery(id+"F3.wireOp",EDGE,"E4.sketch_text.stroke-168"),sQuery(id+"F3.wireOp",EDGE,"E4.sketch_text.stroke-169"),sQuery(id+"F3.wireOp",EDGE,"E4.sketch_text.stroke-170"),sQuery(id+"F3.wireOp",EDGE,"E4.sketch_text.stroke-171"),sQuery(id+"F3.wireOp",EDGE,"E4.sketch_text.stroke-172"),sQuery(id+"F3.wireOp",EDGE,"E4.sketch_text.stroke-173"),sQuery(id+"F3.wireOp",EDGE,"E4.sketch_text.stroke-174"),sQuery(id+"F3.wireOp",EDGE,"E4.sketch_text.stroke-175"),sQuery(id+"F3.wireOp",EDGE,"E4.sketch_text.stroke-176"),sQuery(id+"F3.wireOp",EDGE,"E4.sketch_text.stroke-177"),sQuery(id+"F3.wireOp",EDGE,"E4.sketch_text.stroke-178"),sQuery(id+"F3.wireOp",EDGE,"E4.sketch_text.stroke-179"),sQuery(id+"F3.wireOp",EDGE,"E4.sketch_text.stroke-180"),sQuery(id+"F5.wireOp",EDGE,"8007402e-1a4e-4a06-85a5-2af08e553504"),subQ2])],"isStart":true}),makeQuery(id+"F6.opExtrude","SWEPT_FACE",FACE,{"disambiguationData":[OSD([subQ2])]})]),OD(0.0)],"derivedFrom":makeQuery(id+"F1.opExtrude","CAP_EDGE",EDGE,{"disambiguationData":[OSD([subQ0])],"isStart":false})});}
            var Q17;
            {var subQ0=sQuery(id+"F0.wireOp",EDGE,"E0.top");var subQ1=sQuery(id+"F0.wireOp",EDGE,"E0.bottom");var subQ2=sQuery(id+"F5.wireOp",EDGE,"1a034e28-a7c2-419d-97de-c33d70a47301");Q17=makeQuery(id+"F6.boolean.opBoolean","SPLIT",EDGE,{"disambiguationData":[TD([makeQuery(id+"F1.opExtrude","CAP_FACE",FACE,{"disambiguationData":[OSD([subQ1,subQ0,sQuery(id+"F0.wireOp",EDGE,"E0.left"),sQuery(id+"F0.wireOp",EDGE,"E0.right")])],"isStart":false}),makeQuery(id+"F1.opExtrude","SWEPT_FACE",FACE,{"disambiguationData":[OSD([subQ0])]}),makeQuery(id+"F6.opExtrude","CAP_FACE",FACE,{"disambiguationData":[OSD([subQ1,sQuery(id+"F2.wireOp",EDGE,"E2.sketch_text.stroke-0"),sQuery(id+"F2.wireOp",EDGE,"E2.sketch_text.stroke-1"),sQuery(id+"F2.wireOp",EDGE,"E2.sketch_text.stroke-2"),sQuery(id+"F2.wireOp",EDGE,"E2.sketch_text.stroke-3"),sQuery(id+"F2.wireOp",EDGE,"E2.sketch_text.stroke-4"),sQuery(id+"F2.wireOp",EDGE,"E2.sketch_text.stroke-5"),sQuery(id+"F2.wireOp",EDGE,"E2.sketch_text.stroke-6"),sQuery(id+"F2.wireOp",EDGE,"E2.sketch_text.stroke-7"),sQuery(id+"F2.wireOp",EDGE,"E2.sketch_text.stroke-8"),sQuery(id+"F2.wireOp",EDGE,"E2.sketch_text.stroke-9"),sQuery(id+"F2.wireOp",EDGE,"E2.sketch_text.stroke-10"),sQuery(id+"F2.wireOp",EDGE,"E2.sketch_text.stroke-11"),sQuery(id+"F2.wireOp",EDGE,"E2.sketch_text.stroke-12"),sQuery(id+"F2.wireOp",EDGE,"E2.sketch_text.stroke-13"),sQuery(id+"F2.wireOp",EDGE,"E2.sketch_text.stroke-14"),sQuery(id+"F2.wireOp",EDGE,"E2.sketch_text.stroke-15"),sQuery(id+"F2.wireOp",EDGE,"E2.sketch_text.stroke-16"),sQuery(id+"F2.wireOp",EDGE,"E2.sketch_text.stroke-17"),sQuery(id+"F2.wireOp",EDGE,"E2.sketch_text.stroke-18"),sQuery(id+"F2.wireOp",EDGE,"E2.sketch_text.stroke-19"),sQuery(id+"F2.wireOp",EDGE,"E2.sketch_text.stroke-20"),sQuery(id+"F2.wireOp",EDGE,"E2.sketch_text.stroke-21"),sQuery(id+"F2.wireOp",EDGE,"E2.sketch_text.stroke-22"),sQuery(id+"F2.wireOp",EDGE,"E2.sketch_text.stroke-23"),sQuery(id+"F2.wireOp",EDGE,"E2.sketch_text.stroke-24"),sQuery(id+"F2.wireOp",EDGE,"E2.sketch_text.stroke-25"),sQuery(id+"F2.wireOp",EDGE,"E2.sketch_text.stroke-26"),sQuery(id+"F2.wireOp",EDGE,"E2.sketch_text.stroke-27"),sQuery(id+"F2.wireOp",EDGE,"E2.sketch_text.stroke-28"),sQuery(id+"F2.wireOp",EDGE,"E2.sketch_text.stroke-29"),sQuery(id+"F2.wireOp",EDGE,"E2.sketch_text.stroke-30"),sQuery(id+"F2.wireOp",EDGE,"E2.sketch_text.stroke-31"),sQuery(id+"F2.wireOp",EDGE,"E2.sketch_text.stroke-32"),sQuery(id+"F2.wireOp",EDGE,"E2.sketch_text.stroke-33"),sQuery(id+"F2.wireOp",EDGE,"E2.sketch_text.stroke-34"),sQuery(id+"F2.wireOp",EDGE,"E2.sketch_text.stroke-35"),sQuery(id+"F2.wireOp",EDGE,"E2.sketch_text.stroke-36"),sQuery(id+"F2.wireOp",EDGE,"E2.sketch_text.stroke-37"),sQuery(id+"F2.wireOp",EDGE,"E2.sketch_text.stroke-38"),sQuery(id+"F2.wireOp",EDGE,"E2.sketch_text.stroke-39"),sQuery(id+"F2.wireOp",EDGE,"E2.sketch_text.stroke-40"),sQuery(id+"F2.wireOp",EDGE,"E2.sketch_text.stroke-41"),sQuery(id+"F2.wireOp",EDGE,"E2.sketch_text.stroke-42"),sQuery(id+"F2.wireOp",EDGE,"E2.sketch_text.stroke-43"),sQuery(id+"F2.wireOp",EDGE,"E2.sketch_text.stroke-44"),sQuery(id+"F2.wireOp",EDGE,"E2.sketch_text.stroke-45"),sQuery(id+"F2.wireOp",EDGE,"E2.sketch_text.stroke-46"),sQuery(id+"F2.wireOp",EDGE,"E2.sketch_text.stroke-47"),sQuery(id+"F2.wireOp",EDGE,"E2.sketch_text.stroke-48"),sQuery(id+"F2.wireOp",EDGE,"E2.sketch_text.stroke-49"),sQuery(id+"F2.wireOp",EDGE,"E2.sketch_text.stroke-50"),sQuery(id+"F2.wireOp",EDGE,"E2.sketch_text.stroke-51"),sQuery(id+"F2.wireOp",EDGE,"E2.sketch_text.stroke-52"),sQuery(id+"F2.wireOp",EDGE,"E2.sketch_text.stroke-53"),sQuery(id+"F2.wireOp",EDGE,"E2.sketch_text.stroke-54"),sQuery(id+"F2.wireOp",EDGE,"E2.sketch_text.stroke-55"),sQuery(id+"F2.wireOp",EDGE,"E2.sketch_text.stroke-56"),sQuery(id+"F2.wireOp",EDGE,"E2.sketch_text.stroke-57"),sQuery(id+"F2.wireOp",EDGE,"E2.sketch_text.stroke-58"),sQuery(id+"F2.wireOp",EDGE,"E2.sketch_text.stroke-59"),sQuery(id+"F2.wireOp",EDGE,"E2.sketch_text.stroke-60"),sQuery(id+"F2.wireOp",EDGE,"E2.sketch_text.stroke-61"),sQuery(id+"F2.wireOp",EDGE,"E2.sketch_text.stroke-62"),sQuery(id+"F2.wireOp",EDGE,"E2.sketch_text.stroke-63"),sQuery(id+"F2.wireOp",EDGE,"E2.sketch_text.stroke-64"),sQuery(id+"F2.wireOp",EDGE,"E2.sketch_text.stroke-65"),sQuery(id+"F2.wireOp",EDGE,"E2.sketch_text.stroke-66"),sQuery(id+"F2.wireOp",EDGE,"E2.sketch_text.stroke-67"),sQuery(id+"F2.wireOp",EDGE,"E2.sketch_text.stroke-68"),sQuery(id+"F2.wireOp",EDGE,"E2.sketch_text.stroke-69"),sQuery(id+"F2.wireOp",EDGE,"E2.sketch_text.stroke-70"),sQuery(id+"F2.wireOp",EDGE,"E2.sketch_text.stroke-71"),sQuery(id+"F2.wireOp",EDGE,"E2.sketch_text.stroke-72"),sQuery(id+"F2.wireOp",EDGE,"E2.sketch_text.stroke-73"),sQuery(id+"F2.wireOp",EDGE,"E2.sketch_text.stroke-74"),sQuery(id+"F2.wireOp",EDGE,"E2.sketch_text.stroke-75"),sQuery(id+"F2.wireOp",EDGE,"E2.sketch_text.stroke-76"),sQuery(id+"F2.wireOp",EDGE,"E2.sketch_text.stroke-77"),sQuery(id+"F2.wireOp",EDGE,"E2.sketch_text.stroke-78"),sQuery(id+"F2.wireOp",EDGE,"E2.sketch_text.stroke-79"),sQuery(id+"F2.wireOp",EDGE,"E2.sketch_text.stroke-80"),sQuery(id+"F2.wireOp",EDGE,"E2.sketch_text.stroke-81"),sQuery(id+"F2.wireOp",EDGE,"E2.sketch_text.stroke-82"),sQuery(id+"F2.wireOp",EDGE,"E2.sketch_text.stroke-83"),sQuery(id+"F2.wireOp",EDGE,"E2.sketch_text.stroke-84"),sQuery(id+"F2.wireOp",EDGE,"E2.sketch_text.stroke-85"),sQuery(id+"F2.wireOp",EDGE,"E2.sketch_text.stroke-86"),sQuery(id+"F2.wireOp",EDGE,"E2.sketch_text.stroke-87"),sQuery(id+"F2.wireOp",EDGE,"E2.sketch_text.stroke-88"),sQuery(id+"F2.wireOp",EDGE,"E2.sketch_text.stroke-89"),sQuery(id+"F2.wireOp",EDGE,"E2.sketch_text.stroke-90"),sQuery(id+"F2.wireOp",EDGE,"E2.sketch_text.stroke-91"),sQuery(id+"F2.wireOp",EDGE,"E2.sketch_text.stroke-92"),sQuery(id+"F2.wireOp",EDGE,"E2.sketch_text.stroke-93"),sQuery(id+"F2.wireOp",EDGE,"E2.sketch_text.stroke-94"),sQuery(id+"F2.wireOp",EDGE,"E2.sketch_text.stroke-95"),sQuery(id+"F2.wireOp",EDGE,"E2.sketch_text.stroke-96"),sQuery(id+"F2.wireOp",EDGE,"E2.sketch_text.stroke-97"),sQuery(id+"F2.wireOp",EDGE,"E2.sketch_text.stroke-98"),sQuery(id+"F2.wireOp",EDGE,"E2.sketch_text.stroke-99"),sQuery(id+"F2.wireOp",EDGE,"E2.sketch_text.stroke-100"),sQuery(id+"F2.wireOp",EDGE,"E2.sketch_text.stroke-101"),sQuery(id+"F2.wireOp",EDGE,"E2.sketch_text.stroke-102"),sQuery(id+"F2.wireOp",EDGE,"E2.sketch_text.stroke-103"),sQuery(id+"F2.wireOp",EDGE,"E2.sketch_text.stroke-104"),sQuery(id+"F2.wireOp",EDGE,"E2.sketch_text.stroke-105"),sQuery(id+"F2.wireOp",EDGE,"E2.sketch_text.stroke-106"),sQuery(id+"F2.wireOp",EDGE,"E2.sketch_text.stroke-107"),sQuery(id+"F2.wireOp",EDGE,"E2.sketch_text.stroke-108"),sQuery(id+"F2.wireOp",EDGE,"E2.sketch_text.stroke-109"),sQuery(id+"F2.wireOp",EDGE,"E2.sketch_text.stroke-110"),sQuery(id+"F2.wireOp",EDGE,"E2.sketch_text.stroke-111"),sQuery(id+"F2.wireOp",EDGE,"E2.sketch_text.stroke-112"),sQuery(id+"F2.wireOp",EDGE,"E2.sketch_text.stroke-113"),sQuery(id+"F2.wireOp",EDGE,"E2.sketch_text.stroke-114"),sQuery(id+"F2.wireOp",EDGE,"E2.sketch_text.stroke-115"),sQuery(id+"F2.wireOp",EDGE,"E2.sketch_text.stroke-116"),sQuery(id+"F2.wireOp",EDGE,"E2.sketch_text.stroke-117"),sQuery(id+"F2.wireOp",EDGE,"E2.sketch_text.stroke-118"),sQuery(id+"F2.wireOp",EDGE,"E2.sketch_text.stroke-119"),sQuery(id+"F2.wireOp",EDGE,"E2.sketch_text.stroke-120"),sQuery(id+"F2.wireOp",EDGE,"E2.sketch_text.stroke-121"),sQuery(id+"F2.wireOp",EDGE,"E2.sketch_text.stroke-122"),sQuery(id+"F2.wireOp",EDGE,"E2.sketch_text.stroke-123"),sQuery(id+"F2.wireOp",EDGE,"E2.sketch_text.stroke-124"),sQuery(id+"F2.wireOp",EDGE,"E2.sketch_text.stroke-125"),sQuery(id+"F2.wireOp",EDGE,"E2.sketch_text.stroke-126"),sQuery(id+"F2.wireOp",EDGE,"E2.sketch_text.stroke-127"),sQuery(id+"F2.wireOp",EDGE,"E2.sketch_text.stroke-128"),sQuery(id+"F2.wireOp",EDGE,"E2.sketch_text.stroke-129"),sQuery(id+"F2.wireOp",EDGE,"E2.sketch_text.stroke-130"),sQuery(id+"F2.wireOp",EDGE,"E2.sketch_text.stroke-131"),sQuery(id+"F2.wireOp",EDGE,"E2.sketch_text.stroke-132"),sQuery(id+"F2.wireOp",EDGE,"E2.sketch_text.stroke-133"),sQuery(id+"F2.wireOp",EDGE,"E2.sketch_text.stroke-134"),sQuery(id+"F2.wireOp",EDGE,"E2.sketch_text.stroke-135"),sQuery(id+"F2.wireOp",EDGE,"E2.sketch_text.stroke-136"),sQuery(id+"F2.wireOp",EDGE,"E2.sketch_text.stroke-137"),sQuery(id+"F2.wireOp",EDGE,"E2.sketch_text.stroke-138"),sQuery(id+"F2.wireOp",EDGE,"E2.sketch_text.stroke-139"),sQuery(id+"F2.wireOp",EDGE,"E2.sketch_text.stroke-140"),sQuery(id+"F2.wireOp",EDGE,"E2.sketch_text.stroke-141"),sQuery(id+"F2.wireOp",EDGE,"E2.sketch_text.stroke-142"),sQuery(id+"F2.wireOp",EDGE,"E2.sketch_text.stroke-143"),sQuery(id+"F2.wireOp",EDGE,"E2.sketch_text.stroke-144"),sQuery(id+"F2.wireOp",EDGE,"E2.sketch_text.stroke-145"),sQuery(id+"F2.wireOp",EDGE,"E2.sketch_text.stroke-146"),sQuery(id+"F2.wireOp",EDGE,"E2.sketch_text.stroke-147"),sQuery(id+"F2.wireOp",EDGE,"E2.sketch_text.stroke-148"),sQuery(id+"F2.wireOp",EDGE,"E2.sketch_text.stroke-149"),sQuery(id+"F2.wireOp",EDGE,"E2.sketch_text.stroke-150"),sQuery(id+"F2.wireOp",EDGE,"E2.sketch_text.stroke-151"),sQuery(id+"F2.wireOp",EDGE,"E2.sketch_text.stroke-152"),sQuery(id+"F2.wireOp",EDGE,"E2.sketch_text.stroke-153"),sQuery(id+"F2.wireOp",EDGE,"E2.sketch_text.stroke-154"),sQuery(id+"F2.wireOp",EDGE,"E2.sketch_text.stroke-155"),sQuery(id+"F2.wireOp",EDGE,"E2.sketch_text.stroke-156"),sQuery(id+"F2.wireOp",EDGE,"E2.sketch_text.stroke-157"),sQuery(id+"F2.wireOp",EDGE,"E2.sketch_text.stroke-158"),sQuery(id+"F2.wireOp",EDGE,"E2.sketch_text.stroke-159"),sQuery(id+"F2.wireOp",EDGE,"E2.sketch_text.stroke-160"),sQuery(id+"F2.wireOp",EDGE,"E2.sketch_text.stroke-161"),sQuery(id+"F2.wireOp",EDGE,"E2.sketch_text.stroke-162"),sQuery(id+"F2.wireOp",EDGE,"E2.sketch_text.stroke-163"),sQuery(id+"F2.wireOp",EDGE,"E2.sketch_text.stroke-164"),sQuery(id+"F2.wireOp",EDGE,"E2.sketch_text.stroke-165"),sQuery(id+"F2.wireOp",EDGE,"E2.sketch_text.stroke-166"),sQuery(id+"F2.wireOp",EDGE,"E2.sketch_text.stroke-167"),sQuery(id+"F2.wireOp",EDGE,"E2.sketch_text.stroke-168"),sQuery(id+"F2.wireOp",EDGE,"E2.sketch_text.stroke-169"),sQuery(id+"F2.wireOp",EDGE,"E2.sketch_text.stroke-170"),sQuery(id+"F2.wireOp",EDGE,"E2.sketch_text.stroke-171"),sQuery(id+"F2.wireOp",EDGE,"E2.sketch_text.stroke-172"),sQuery(id+"F2.wireOp",EDGE,"E2.sketch_text.stroke-173"),sQuery(id+"F3.wireOp",EDGE,"E4.sketch_text.stroke-0"),sQuery(id+"F3.wireOp",EDGE,"E4.sketch_text.stroke-1"),sQuery(id+"F3.wireOp",EDGE,"E4.sketch_text.stroke-2"),sQuery(id+"F3.wireOp",EDGE,"E4.sketch_text.stroke-3"),sQuery(id+"F3.wireOp",EDGE,"E4.sketch_text.stroke-4"),sQuery(id+"F3.wireOp",EDGE,"E4.sketch_text.stroke-5"),sQuery(id+"F3.wireOp",EDGE,"E4.sketch_text.stroke-6"),sQuery(id+"F3.wireOp",EDGE,"E4.sketch_text.stroke-7"),sQuery(id+"F3.wireOp",EDGE,"E4.sketch_text.stroke-8"),sQuery(id+"F3.wireOp",EDGE,"E4.sketch_text.stroke-9"),sQuery(id+"F3.wireOp",EDGE,"E4.sketch_text.stroke-10"),sQuery(id+"F3.wireOp",EDGE,"E4.sketch_text.stroke-11"),sQuery(id+"F3.wireOp",EDGE,"E4.sketch_text.stroke-12"),sQuery(id+"F3.wireOp",EDGE,"E4.sketch_text.stroke-13"),sQuery(id+"F3.wireOp",EDGE,"E4.sketch_text.stroke-14"),sQuery(id+"F3.wireOp",EDGE,"E4.sketch_text.stroke-15"),sQuery(id+"F3.wireOp",EDGE,"E4.sketch_text.stroke-16"),sQuery(id+"F3.wireOp",EDGE,"E4.sketch_text.stroke-17"),sQuery(id+"F3.wireOp",EDGE,"E4.sketch_text.stroke-18"),sQuery(id+"F3.wireOp",EDGE,"E4.sketch_text.stroke-19"),sQuery(id+"F3.wireOp",EDGE,"E4.sketch_text.stroke-20"),sQuery(id+"F3.wireOp",EDGE,"E4.sketch_text.stroke-21"),sQuery(id+"F3.wireOp",EDGE,"E4.sketch_text.stroke-22"),sQuery(id+"F3.wireOp",EDGE,"E4.sketch_text.stroke-23"),sQuery(id+"F3.wireOp",EDGE,"E4.sketch_text.stroke-24"),sQuery(id+"F3.wireOp",EDGE,"E4.sketch_text.stroke-25"),sQuery(id+"F3.wireOp",EDGE,"E4.sketch_text.stroke-26"),sQuery(id+"F3.wireOp",EDGE,"E4.sketch_text.stroke-27"),sQuery(id+"F3.wireOp",EDGE,"E4.sketch_text.stroke-28"),sQuery(id+"F3.wireOp",EDGE,"E4.sketch_text.stroke-29"),sQuery(id+"F3.wireOp",EDGE,"E4.sketch_text.stroke-30"),sQuery(id+"F3.wireOp",EDGE,"E4.sketch_text.stroke-31"),sQuery(id+"F3.wireOp",EDGE,"E4.sketch_text.stroke-32"),sQuery(id+"F3.wireOp",EDGE,"E4.sketch_text.stroke-33"),sQuery(id+"F3.wireOp",EDGE,"E4.sketch_text.stroke-34"),sQuery(id+"F3.wireOp",EDGE,"E4.sketch_text.stroke-35"),sQuery(id+"F3.wireOp",EDGE,"E4.sketch_text.stroke-36"),sQuery(id+"F3.wireOp",EDGE,"E4.sketch_text.stroke-37"),sQuery(id+"F3.wireOp",EDGE,"E4.sketch_text.stroke-38"),sQuery(id+"F3.wireOp",EDGE,"E4.sketch_text.stroke-39"),sQuery(id+"F3.wireOp",EDGE,"E4.sketch_text.stroke-40"),sQuery(id+"F3.wireOp",EDGE,"E4.sketch_text.stroke-41"),sQuery(id+"F3.wireOp",EDGE,"E4.sketch_text.stroke-42"),sQuery(id+"F3.wireOp",EDGE,"E4.sketch_text.stroke-43"),sQuery(id+"F3.wireOp",EDGE,"E4.sketch_text.stroke-44"),sQuery(id+"F3.wireOp",EDGE,"E4.sketch_text.stroke-45"),sQuery(id+"F3.wireOp",EDGE,"E4.sketch_text.stroke-46"),sQuery(id+"F3.wireOp",EDGE,"E4.sketch_text.stroke-47"),sQuery(id+"F3.wireOp",EDGE,"E4.sketch_text.stroke-48"),sQuery(id+"F3.wireOp",EDGE,"E4.sketch_text.stroke-49"),sQuery(id+"F3.wireOp",EDGE,"E4.sketch_text.stroke-50"),sQuery(id+"F3.wireOp",EDGE,"E4.sketch_text.stroke-51"),sQuery(id+"F3.wireOp",EDGE,"E4.sketch_text.stroke-52"),sQuery(id+"F3.wireOp",EDGE,"E4.sketch_text.stroke-53"),sQuery(id+"F3.wireOp",EDGE,"E4.sketch_text.stroke-54"),sQuery(id+"F3.wireOp",EDGE,"E4.sketch_text.stroke-55"),sQuery(id+"F3.wireOp",EDGE,"E4.sketch_text.stroke-56"),sQuery(id+"F3.wireOp",EDGE,"E4.sketch_text.stroke-57"),sQuery(id+"F3.wireOp",EDGE,"E4.sketch_text.stroke-58"),sQuery(id+"F3.wireOp",EDGE,"E4.sketch_text.stroke-59"),sQuery(id+"F3.wireOp",EDGE,"E4.sketch_text.stroke-60"),sQuery(id+"F3.wireOp",EDGE,"E4.sketch_text.stroke-61"),sQuery(id+"F3.wireOp",EDGE,"E4.sketch_text.stroke-62"),sQuery(id+"F3.wireOp",EDGE,"E4.sketch_text.stroke-71"),sQuery(id+"F3.wireOp",EDGE,"E4.sketch_text.stroke-72"),sQuery(id+"F3.wireOp",EDGE,"E4.sketch_text.stroke-73"),sQuery(id+"F3.wireOp",EDGE,"E4.sketch_text.stroke-74"),sQuery(id+"F3.wireOp",EDGE,"E4.sketch_text.stroke-75"),sQuery(id+"F3.wireOp",EDGE,"E4.sketch_text.stroke-76"),sQuery(id+"F3.wireOp",EDGE,"E4.sketch_text.stroke-77"),sQuery(id+"F3.wireOp",EDGE,"E4.sketch_text.stroke-78"),sQuery(id+"F3.wireOp",EDGE,"E4.sketch_text.stroke-79"),sQuery(id+"F3.wireOp",EDGE,"E4.sketch_text.stroke-80"),sQuery(id+"F3.wireOp",EDGE,"E4.sketch_text.stroke-81"),sQuery(id+"F3.wireOp",EDGE,"E4.sketch_text.stroke-82"),sQuery(id+"F3.wireOp",EDGE,"E4.sketch_text.stroke-83"),sQuery(id+"F3.wireOp",EDGE,"E4.sketch_text.stroke-84"),sQuery(id+"F3.wireOp",EDGE,"E4.sketch_text.stroke-85"),sQuery(id+"F3.wireOp",EDGE,"E4.sketch_text.stroke-86"),sQuery(id+"F3.wireOp",EDGE,"E4.sketch_text.stroke-87"),sQuery(id+"F3.wireOp",EDGE,"E4.sketch_text.stroke-88"),sQuery(id+"F3.wireOp",EDGE,"E4.sketch_text.stroke-89"),sQuery(id+"F3.wireOp",EDGE,"E4.sketch_text.stroke-90"),sQuery(id+"F3.wireOp",EDGE,"E4.sketch_text.stroke-91"),sQuery(id+"F3.wireOp",EDGE,"E4.sketch_text.stroke-92"),sQuery(id+"F3.wireOp",EDGE,"E4.sketch_text.stroke-93"),sQuery(id+"F3.wireOp",EDGE,"E4.sketch_text.stroke-94"),sQuery(id+"F3.wireOp",EDGE,"E4.sketch_text.stroke-95"),sQuery(id+"F3.wireOp",EDGE,"E4.sketch_text.stroke-96"),sQuery(id+"F3.wireOp",EDGE,"E4.sketch_text.stroke-97"),sQuery(id+"F3.wireOp",EDGE,"E4.sketch_text.stroke-103"),sQuery(id+"F3.wireOp",EDGE,"E4.sketch_text.stroke-104"),sQuery(id+"F3.wireOp",EDGE,"E4.sketch_text.stroke-105"),sQuery(id+"F3.wireOp",EDGE,"E4.sketch_text.stroke-106"),sQuery(id+"F3.wireOp",EDGE,"E4.sketch_text.stroke-107"),sQuery(id+"F3.wireOp",EDGE,"E4.sketch_text.stroke-108"),sQuery(id+"F3.wireOp",EDGE,"E4.sketch_text.stroke-109"),sQuery(id+"F3.wireOp",EDGE,"E4.sketch_text.stroke-110"),sQuery(id+"F3.wireOp",EDGE,"E4.sketch_text.stroke-111"),sQuery(id+"F3.wireOp",EDGE,"E4.sketch_text.stroke-112"),sQuery(id+"F3.wireOp",EDGE,"E4.sketch_text.stroke-113"),sQuery(id+"F3.wireOp",EDGE,"E4.sketch_text.stroke-114"),sQuery(id+"F3.wireOp",EDGE,"E4.sketch_text.stroke-115"),sQuery(id+"F3.wireOp",EDGE,"E4.sketch_text.stroke-116"),sQuery(id+"F3.wireOp",EDGE,"E4.sketch_text.stroke-117"),sQuery(id+"F3.wireOp",EDGE,"E4.sketch_text.stroke-118"),sQuery(id+"F3.wireOp",EDGE,"E4.sketch_text.stroke-119"),sQuery(id+"F3.wireOp",EDGE,"E4.sketch_text.stroke-120"),sQuery(id+"F3.wireOp",EDGE,"E4.sketch_text.stroke-121"),sQuery(id+"F3.wireOp",EDGE,"E4.sketch_text.stroke-122"),sQuery(id+"F3.wireOp",EDGE,"E4.sketch_text.stroke-123"),sQuery(id+"F3.wireOp",EDGE,"E4.sketch_text.stroke-124"),sQuery(id+"F3.wireOp",EDGE,"E4.sketch_text.stroke-125"),sQuery(id+"F3.wireOp",EDGE,"E4.sketch_text.stroke-126"),sQuery(id+"F3.wireOp",EDGE,"E4.sketch_text.stroke-127"),sQuery(id+"F3.wireOp",EDGE,"E4.sketch_text.stroke-128"),sQuery(id+"F3.wireOp",EDGE,"E4.sketch_text.stroke-129"),sQuery(id+"F3.wireOp",EDGE,"E4.sketch_text.stroke-130"),sQuery(id+"F3.wireOp",EDGE,"E4.sketch_text.stroke-131"),sQuery(id+"F3.wireOp",EDGE,"E4.sketch_text.stroke-132"),sQuery(id+"F3.wireOp",EDGE,"E4.sketch_text.stroke-133"),sQuery(id+"F3.wireOp",EDGE,"E4.sketch_text.stroke-134"),sQuery(id+"F3.wireOp",EDGE,"E4.sketch_text.stroke-135"),sQuery(id+"F3.wireOp",EDGE,"E4.sketch_text.stroke-136"),sQuery(id+"F3.wireOp",EDGE,"E4.sketch_text.stroke-137"),sQuery(id+"F3.wireOp",EDGE,"E4.sketch_text.stroke-138"),sQuery(id+"F3.wireOp",EDGE,"E4.sketch_text.stroke-139"),sQuery(id+"F3.wireOp",EDGE,"E4.sketch_text.stroke-140"),sQuery(id+"F3.wireOp",EDGE,"E4.sketch_text.stroke-141"),sQuery(id+"F3.wireOp",EDGE,"E4.sketch_text.stroke-142"),sQuery(id+"F3.wireOp",EDGE,"E4.sketch_text.stroke-143"),sQuery(id+"F3.wireOp",EDGE,"E4.sketch_text.stroke-144"),sQuery(id+"F3.wireOp",EDGE,"E4.sketch_text.stroke-145"),sQuery(id+"F3.wireOp",EDGE,"E4.sketch_text.stroke-146"),sQuery(id+"F3.wireOp",EDGE,"E4.sketch_text.stroke-147"),sQuery(id+"F3.wireOp",EDGE,"E4.sketch_text.stroke-148"),sQuery(id+"F3.wireOp",EDGE,"E4.sketch_text.stroke-149"),sQuery(id+"F3.wireOp",EDGE,"E4.sketch_text.stroke-150"),sQuery(id+"F3.wireOp",EDGE,"E4.sketch_text.stroke-151"),sQuery(id+"F3.wireOp",EDGE,"E4.sketch_text.stroke-152"),sQuery(id+"F3.wireOp",EDGE,"E4.sketch_text.stroke-153"),sQuery(id+"F3.wireOp",EDGE,"E4.sketch_text.stroke-159"),sQuery(id+"F3.wireOp",EDGE,"E4.sketch_text.stroke-160"),sQuery(id+"F3.wireOp",EDGE,"E4.sketch_text.stroke-161"),sQuery(id+"F3.wireOp",EDGE,"E4.sketch_text.stroke-162"),sQuery(id+"F3.wireOp",EDGE,"E4.sketch_text.stroke-163"),sQuery(id+"F3.wireOp",EDGE,"E4.sketch_text.stroke-164"),sQuery(id+"F3.wireOp",EDGE,"E4.sketch_text.stroke-165"),sQuery(id+"F3.wireOp",EDGE,"E4.sketch_text.stroke-166"),sQuery(id+"F3.wireOp",EDGE,"E4.sketch_text.stroke-167"),sQuery(id+"F3.wireOp",EDGE,"E4.sketch_text.stroke-168"),sQuery(id+"F3.wireOp",EDGE,"E4.sketch_text.stroke-169"),sQuery(id+"F3.wireOp",EDGE,"E4.sketch_text.stroke-170"),sQuery(id+"F3.wireOp",EDGE,"E4.sketch_text.stroke-171"),sQuery(id+"F3.wireOp",EDGE,"E4.sketch_text.stroke-172"),sQuery(id+"F3.wireOp",EDGE,"E4.sketch_text.stroke-173"),sQuery(id+"F3.wireOp",EDGE,"E4.sketch_text.stroke-174"),sQuery(id+"F3.wireOp",EDGE,"E4.sketch_text.stroke-175"),sQuery(id+"F3.wireOp",EDGE,"E4.sketch_text.stroke-176"),sQuery(id+"F3.wireOp",EDGE,"E4.sketch_text.stroke-177"),sQuery(id+"F3.wireOp",EDGE,"E4.sketch_text.stroke-178"),sQuery(id+"F3.wireOp",EDGE,"E4.sketch_text.stroke-179"),sQuery(id+"F3.wireOp",EDGE,"E4.sketch_text.stroke-180"),sQuery(id+"F5.wireOp",EDGE,"727ac2c1-f511-4829-95a7-a443ef16a4cd"),subQ2])],"isStart":true}),makeQuery(id+"F6.opExtrude","SWEPT_FACE",FACE,{"disambiguationData":[OSD([subQ2])]})])],"derivedFrom":makeQuery(id+"F6.opExtrude","CAP_EDGE",EDGE,{"disambiguationData":[OSD([subQ2])],"isStart":true})});}
            var Q18;
            {var subQ0=sQuery(id+"F0.wireOp",EDGE,"E0.top");var subQ1=sQuery(id+"F0.wireOp",EDGE,"E0.bottom");var subQ2=sQuery(id+"F5.wireOp",EDGE,"1a034e28-a7c2-419d-97de-c33d70a47301");Q18=makeQuery(id+"F6.boolean.opBoolean","SPLIT",EDGE,{"disambiguationData":[TD([makeQuery(id+"F1.opExtrude","CAP_FACE",FACE,{"disambiguationData":[OSD([subQ1,subQ0,sQuery(id+"F0.wireOp",EDGE,"E0.left"),sQuery(id+"F0.wireOp",EDGE,"E0.right")])],"isStart":false}),makeQuery(id+"F1.opExtrude","SWEPT_FACE",FACE,{"disambiguationData":[OSD([subQ0])]}),makeQuery(id+"F6.opExtrude","CAP_FACE",FACE,{"disambiguationData":[OSD([subQ1,sQuery(id+"F2.wireOp",EDGE,"E2.sketch_text.stroke-0"),sQuery(id+"F2.wireOp",EDGE,"E2.sketch_text.stroke-1"),sQuery(id+"F2.wireOp",EDGE,"E2.sketch_text.stroke-2"),sQuery(id+"F2.wireOp",EDGE,"E2.sketch_text.stroke-3"),sQuery(id+"F2.wireOp",EDGE,"E2.sketch_text.stroke-4"),sQuery(id+"F2.wireOp",EDGE,"E2.sketch_text.stroke-5"),sQuery(id+"F2.wireOp",EDGE,"E2.sketch_text.stroke-6"),sQuery(id+"F2.wireOp",EDGE,"E2.sketch_text.stroke-7"),sQuery(id+"F2.wireOp",EDGE,"E2.sketch_text.stroke-8"),sQuery(id+"F2.wireOp",EDGE,"E2.sketch_text.stroke-9"),sQuery(id+"F2.wireOp",EDGE,"E2.sketch_text.stroke-10"),sQuery(id+"F2.wireOp",EDGE,"E2.sketch_text.stroke-11"),sQuery(id+"F2.wireOp",EDGE,"E2.sketch_text.stroke-12"),sQuery(id+"F2.wireOp",EDGE,"E2.sketch_text.stroke-13"),sQuery(id+"F2.wireOp",EDGE,"E2.sketch_text.stroke-14"),sQuery(id+"F2.wireOp",EDGE,"E2.sketch_text.stroke-15"),sQuery(id+"F2.wireOp",EDGE,"E2.sketch_text.stroke-16"),sQuery(id+"F2.wireOp",EDGE,"E2.sketch_text.stroke-17"),sQuery(id+"F2.wireOp",EDGE,"E2.sketch_text.stroke-18"),sQuery(id+"F2.wireOp",EDGE,"E2.sketch_text.stroke-19"),sQuery(id+"F2.wireOp",EDGE,"E2.sketch_text.stroke-20"),sQuery(id+"F2.wireOp",EDGE,"E2.sketch_text.stroke-21"),sQuery(id+"F2.wireOp",EDGE,"E2.sketch_text.stroke-22"),sQuery(id+"F2.wireOp",EDGE,"E2.sketch_text.stroke-23"),sQuery(id+"F2.wireOp",EDGE,"E2.sketch_text.stroke-24"),sQuery(id+"F2.wireOp",EDGE,"E2.sketch_text.stroke-25"),sQuery(id+"F2.wireOp",EDGE,"E2.sketch_text.stroke-26"),sQuery(id+"F2.wireOp",EDGE,"E2.sketch_text.stroke-27"),sQuery(id+"F2.wireOp",EDGE,"E2.sketch_text.stroke-28"),sQuery(id+"F2.wireOp",EDGE,"E2.sketch_text.stroke-29"),sQuery(id+"F2.wireOp",EDGE,"E2.sketch_text.stroke-30"),sQuery(id+"F2.wireOp",EDGE,"E2.sketch_text.stroke-31"),sQuery(id+"F2.wireOp",EDGE,"E2.sketch_text.stroke-32"),sQuery(id+"F2.wireOp",EDGE,"E2.sketch_text.stroke-33"),sQuery(id+"F2.wireOp",EDGE,"E2.sketch_text.stroke-34"),sQuery(id+"F2.wireOp",EDGE,"E2.sketch_text.stroke-35"),sQuery(id+"F2.wireOp",EDGE,"E2.sketch_text.stroke-36"),sQuery(id+"F2.wireOp",EDGE,"E2.sketch_text.stroke-37"),sQuery(id+"F2.wireOp",EDGE,"E2.sketch_text.stroke-38"),sQuery(id+"F2.wireOp",EDGE,"E2.sketch_text.stroke-39"),sQuery(id+"F2.wireOp",EDGE,"E2.sketch_text.stroke-40"),sQuery(id+"F2.wireOp",EDGE,"E2.sketch_text.stroke-41"),sQuery(id+"F2.wireOp",EDGE,"E2.sketch_text.stroke-42"),sQuery(id+"F2.wireOp",EDGE,"E2.sketch_text.stroke-43"),sQuery(id+"F2.wireOp",EDGE,"E2.sketch_text.stroke-44"),sQuery(id+"F2.wireOp",EDGE,"E2.sketch_text.stroke-45"),sQuery(id+"F2.wireOp",EDGE,"E2.sketch_text.stroke-46"),sQuery(id+"F2.wireOp",EDGE,"E2.sketch_text.stroke-47"),sQuery(id+"F2.wireOp",EDGE,"E2.sketch_text.stroke-48"),sQuery(id+"F2.wireOp",EDGE,"E2.sketch_text.stroke-49"),sQuery(id+"F2.wireOp",EDGE,"E2.sketch_text.stroke-50"),sQuery(id+"F2.wireOp",EDGE,"E2.sketch_text.stroke-51"),sQuery(id+"F2.wireOp",EDGE,"E2.sketch_text.stroke-52"),sQuery(id+"F2.wireOp",EDGE,"E2.sketch_text.stroke-53"),sQuery(id+"F2.wireOp",EDGE,"E2.sketch_text.stroke-54"),sQuery(id+"F2.wireOp",EDGE,"E2.sketch_text.stroke-55"),sQuery(id+"F2.wireOp",EDGE,"E2.sketch_text.stroke-56"),sQuery(id+"F2.wireOp",EDGE,"E2.sketch_text.stroke-57"),sQuery(id+"F2.wireOp",EDGE,"E2.sketch_text.stroke-58"),sQuery(id+"F2.wireOp",EDGE,"E2.sketch_text.stroke-59"),sQuery(id+"F2.wireOp",EDGE,"E2.sketch_text.stroke-60"),sQuery(id+"F2.wireOp",EDGE,"E2.sketch_text.stroke-61"),sQuery(id+"F2.wireOp",EDGE,"E2.sketch_text.stroke-62"),sQuery(id+"F2.wireOp",EDGE,"E2.sketch_text.stroke-63"),sQuery(id+"F2.wireOp",EDGE,"E2.sketch_text.stroke-64"),sQuery(id+"F2.wireOp",EDGE,"E2.sketch_text.stroke-65"),sQuery(id+"F2.wireOp",EDGE,"E2.sketch_text.stroke-66"),sQuery(id+"F2.wireOp",EDGE,"E2.sketch_text.stroke-67"),sQuery(id+"F2.wireOp",EDGE,"E2.sketch_text.stroke-68"),sQuery(id+"F2.wireOp",EDGE,"E2.sketch_text.stroke-69"),sQuery(id+"F2.wireOp",EDGE,"E2.sketch_text.stroke-70"),sQuery(id+"F2.wireOp",EDGE,"E2.sketch_text.stroke-71"),sQuery(id+"F2.wireOp",EDGE,"E2.sketch_text.stroke-72"),sQuery(id+"F2.wireOp",EDGE,"E2.sketch_text.stroke-73"),sQuery(id+"F2.wireOp",EDGE,"E2.sketch_text.stroke-74"),sQuery(id+"F2.wireOp",EDGE,"E2.sketch_text.stroke-75"),sQuery(id+"F2.wireOp",EDGE,"E2.sketch_text.stroke-76"),sQuery(id+"F2.wireOp",EDGE,"E2.sketch_text.stroke-77"),sQuery(id+"F2.wireOp",EDGE,"E2.sketch_text.stroke-78"),sQuery(id+"F2.wireOp",EDGE,"E2.sketch_text.stroke-79"),sQuery(id+"F2.wireOp",EDGE,"E2.sketch_text.stroke-80"),sQuery(id+"F2.wireOp",EDGE,"E2.sketch_text.stroke-81"),sQuery(id+"F2.wireOp",EDGE,"E2.sketch_text.stroke-82"),sQuery(id+"F2.wireOp",EDGE,"E2.sketch_text.stroke-83"),sQuery(id+"F2.wireOp",EDGE,"E2.sketch_text.stroke-84"),sQuery(id+"F2.wireOp",EDGE,"E2.sketch_text.stroke-85"),sQuery(id+"F2.wireOp",EDGE,"E2.sketch_text.stroke-86"),sQuery(id+"F2.wireOp",EDGE,"E2.sketch_text.stroke-87"),sQuery(id+"F2.wireOp",EDGE,"E2.sketch_text.stroke-88"),sQuery(id+"F2.wireOp",EDGE,"E2.sketch_text.stroke-89"),sQuery(id+"F2.wireOp",EDGE,"E2.sketch_text.stroke-90"),sQuery(id+"F2.wireOp",EDGE,"E2.sketch_text.stroke-91"),sQuery(id+"F2.wireOp",EDGE,"E2.sketch_text.stroke-92"),sQuery(id+"F2.wireOp",EDGE,"E2.sketch_text.stroke-93"),sQuery(id+"F2.wireOp",EDGE,"E2.sketch_text.stroke-94"),sQuery(id+"F2.wireOp",EDGE,"E2.sketch_text.stroke-95"),sQuery(id+"F2.wireOp",EDGE,"E2.sketch_text.stroke-96"),sQuery(id+"F2.wireOp",EDGE,"E2.sketch_text.stroke-97"),sQuery(id+"F2.wireOp",EDGE,"E2.sketch_text.stroke-98"),sQuery(id+"F2.wireOp",EDGE,"E2.sketch_text.stroke-99"),sQuery(id+"F2.wireOp",EDGE,"E2.sketch_text.stroke-100"),sQuery(id+"F2.wireOp",EDGE,"E2.sketch_text.stroke-101"),sQuery(id+"F2.wireOp",EDGE,"E2.sketch_text.stroke-102"),sQuery(id+"F2.wireOp",EDGE,"E2.sketch_text.stroke-103"),sQuery(id+"F2.wireOp",EDGE,"E2.sketch_text.stroke-104"),sQuery(id+"F2.wireOp",EDGE,"E2.sketch_text.stroke-105"),sQuery(id+"F2.wireOp",EDGE,"E2.sketch_text.stroke-106"),sQuery(id+"F2.wireOp",EDGE,"E2.sketch_text.stroke-107"),sQuery(id+"F2.wireOp",EDGE,"E2.sketch_text.stroke-108"),sQuery(id+"F2.wireOp",EDGE,"E2.sketch_text.stroke-109"),sQuery(id+"F2.wireOp",EDGE,"E2.sketch_text.stroke-110"),sQuery(id+"F2.wireOp",EDGE,"E2.sketch_text.stroke-111"),sQuery(id+"F2.wireOp",EDGE,"E2.sketch_text.stroke-112"),sQuery(id+"F2.wireOp",EDGE,"E2.sketch_text.stroke-113"),sQuery(id+"F2.wireOp",EDGE,"E2.sketch_text.stroke-114"),sQuery(id+"F2.wireOp",EDGE,"E2.sketch_text.stroke-115"),sQuery(id+"F2.wireOp",EDGE,"E2.sketch_text.stroke-116"),sQuery(id+"F2.wireOp",EDGE,"E2.sketch_text.stroke-117"),sQuery(id+"F2.wireOp",EDGE,"E2.sketch_text.stroke-118"),sQuery(id+"F2.wireOp",EDGE,"E2.sketch_text.stroke-119"),sQuery(id+"F2.wireOp",EDGE,"E2.sketch_text.stroke-120"),sQuery(id+"F2.wireOp",EDGE,"E2.sketch_text.stroke-121"),sQuery(id+"F2.wireOp",EDGE,"E2.sketch_text.stroke-122"),sQuery(id+"F2.wireOp",EDGE,"E2.sketch_text.stroke-123"),sQuery(id+"F2.wireOp",EDGE,"E2.sketch_text.stroke-124"),sQuery(id+"F2.wireOp",EDGE,"E2.sketch_text.stroke-125"),sQuery(id+"F2.wireOp",EDGE,"E2.sketch_text.stroke-126"),sQuery(id+"F2.wireOp",EDGE,"E2.sketch_text.stroke-127"),sQuery(id+"F2.wireOp",EDGE,"E2.sketch_text.stroke-128"),sQuery(id+"F2.wireOp",EDGE,"E2.sketch_text.stroke-129"),sQuery(id+"F2.wireOp",EDGE,"E2.sketch_text.stroke-130"),sQuery(id+"F2.wireOp",EDGE,"E2.sketch_text.stroke-131"),sQuery(id+"F2.wireOp",EDGE,"E2.sketch_text.stroke-132"),sQuery(id+"F2.wireOp",EDGE,"E2.sketch_text.stroke-133"),sQuery(id+"F2.wireOp",EDGE,"E2.sketch_text.stroke-134"),sQuery(id+"F2.wireOp",EDGE,"E2.sketch_text.stroke-135"),sQuery(id+"F2.wireOp",EDGE,"E2.sketch_text.stroke-136"),sQuery(id+"F2.wireOp",EDGE,"E2.sketch_text.stroke-137"),sQuery(id+"F2.wireOp",EDGE,"E2.sketch_text.stroke-138"),sQuery(id+"F2.wireOp",EDGE,"E2.sketch_text.stroke-139"),sQuery(id+"F2.wireOp",EDGE,"E2.sketch_text.stroke-140"),sQuery(id+"F2.wireOp",EDGE,"E2.sketch_text.stroke-141"),sQuery(id+"F2.wireOp",EDGE,"E2.sketch_text.stroke-142"),sQuery(id+"F2.wireOp",EDGE,"E2.sketch_text.stroke-143"),sQuery(id+"F2.wireOp",EDGE,"E2.sketch_text.stroke-144"),sQuery(id+"F2.wireOp",EDGE,"E2.sketch_text.stroke-145"),sQuery(id+"F2.wireOp",EDGE,"E2.sketch_text.stroke-146"),sQuery(id+"F2.wireOp",EDGE,"E2.sketch_text.stroke-147"),sQuery(id+"F2.wireOp",EDGE,"E2.sketch_text.stroke-148"),sQuery(id+"F2.wireOp",EDGE,"E2.sketch_text.stroke-149"),sQuery(id+"F2.wireOp",EDGE,"E2.sketch_text.stroke-150"),sQuery(id+"F2.wireOp",EDGE,"E2.sketch_text.stroke-151"),sQuery(id+"F2.wireOp",EDGE,"E2.sketch_text.stroke-152"),sQuery(id+"F2.wireOp",EDGE,"E2.sketch_text.stroke-153"),sQuery(id+"F2.wireOp",EDGE,"E2.sketch_text.stroke-154"),sQuery(id+"F2.wireOp",EDGE,"E2.sketch_text.stroke-155"),sQuery(id+"F2.wireOp",EDGE,"E2.sketch_text.stroke-156"),sQuery(id+"F2.wireOp",EDGE,"E2.sketch_text.stroke-157"),sQuery(id+"F2.wireOp",EDGE,"E2.sketch_text.stroke-158"),sQuery(id+"F2.wireOp",EDGE,"E2.sketch_text.stroke-159"),sQuery(id+"F2.wireOp",EDGE,"E2.sketch_text.stroke-160"),sQuery(id+"F2.wireOp",EDGE,"E2.sketch_text.stroke-161"),sQuery(id+"F2.wireOp",EDGE,"E2.sketch_text.stroke-162"),sQuery(id+"F2.wireOp",EDGE,"E2.sketch_text.stroke-163"),sQuery(id+"F2.wireOp",EDGE,"E2.sketch_text.stroke-164"),sQuery(id+"F2.wireOp",EDGE,"E2.sketch_text.stroke-165"),sQuery(id+"F2.wireOp",EDGE,"E2.sketch_text.stroke-166"),sQuery(id+"F2.wireOp",EDGE,"E2.sketch_text.stroke-167"),sQuery(id+"F2.wireOp",EDGE,"E2.sketch_text.stroke-168"),sQuery(id+"F2.wireOp",EDGE,"E2.sketch_text.stroke-169"),sQuery(id+"F2.wireOp",EDGE,"E2.sketch_text.stroke-170"),sQuery(id+"F2.wireOp",EDGE,"E2.sketch_text.stroke-171"),sQuery(id+"F2.wireOp",EDGE,"E2.sketch_text.stroke-172"),sQuery(id+"F2.wireOp",EDGE,"E2.sketch_text.stroke-173"),sQuery(id+"F3.wireOp",EDGE,"E4.sketch_text.stroke-0"),sQuery(id+"F3.wireOp",EDGE,"E4.sketch_text.stroke-1"),sQuery(id+"F3.wireOp",EDGE,"E4.sketch_text.stroke-2"),sQuery(id+"F3.wireOp",EDGE,"E4.sketch_text.stroke-3"),sQuery(id+"F3.wireOp",EDGE,"E4.sketch_text.stroke-4"),sQuery(id+"F3.wireOp",EDGE,"E4.sketch_text.stroke-5"),sQuery(id+"F3.wireOp",EDGE,"E4.sketch_text.stroke-6"),sQuery(id+"F3.wireOp",EDGE,"E4.sketch_text.stroke-7"),sQuery(id+"F3.wireOp",EDGE,"E4.sketch_text.stroke-8"),sQuery(id+"F3.wireOp",EDGE,"E4.sketch_text.stroke-9"),sQuery(id+"F3.wireOp",EDGE,"E4.sketch_text.stroke-10"),sQuery(id+"F3.wireOp",EDGE,"E4.sketch_text.stroke-11"),sQuery(id+"F3.wireOp",EDGE,"E4.sketch_text.stroke-12"),sQuery(id+"F3.wireOp",EDGE,"E4.sketch_text.stroke-13"),sQuery(id+"F3.wireOp",EDGE,"E4.sketch_text.stroke-14"),sQuery(id+"F3.wireOp",EDGE,"E4.sketch_text.stroke-15"),sQuery(id+"F3.wireOp",EDGE,"E4.sketch_text.stroke-16"),sQuery(id+"F3.wireOp",EDGE,"E4.sketch_text.stroke-17"),sQuery(id+"F3.wireOp",EDGE,"E4.sketch_text.stroke-18"),sQuery(id+"F3.wireOp",EDGE,"E4.sketch_text.stroke-19"),sQuery(id+"F3.wireOp",EDGE,"E4.sketch_text.stroke-20"),sQuery(id+"F3.wireOp",EDGE,"E4.sketch_text.stroke-21"),sQuery(id+"F3.wireOp",EDGE,"E4.sketch_text.stroke-22"),sQuery(id+"F3.wireOp",EDGE,"E4.sketch_text.stroke-23"),sQuery(id+"F3.wireOp",EDGE,"E4.sketch_text.stroke-24"),sQuery(id+"F3.wireOp",EDGE,"E4.sketch_text.stroke-25"),sQuery(id+"F3.wireOp",EDGE,"E4.sketch_text.stroke-26"),sQuery(id+"F3.wireOp",EDGE,"E4.sketch_text.stroke-27"),sQuery(id+"F3.wireOp",EDGE,"E4.sketch_text.stroke-28"),sQuery(id+"F3.wireOp",EDGE,"E4.sketch_text.stroke-29"),sQuery(id+"F3.wireOp",EDGE,"E4.sketch_text.stroke-30"),sQuery(id+"F3.wireOp",EDGE,"E4.sketch_text.stroke-31"),sQuery(id+"F3.wireOp",EDGE,"E4.sketch_text.stroke-32"),sQuery(id+"F3.wireOp",EDGE,"E4.sketch_text.stroke-33"),sQuery(id+"F3.wireOp",EDGE,"E4.sketch_text.stroke-34"),sQuery(id+"F3.wireOp",EDGE,"E4.sketch_text.stroke-35"),sQuery(id+"F3.wireOp",EDGE,"E4.sketch_text.stroke-36"),sQuery(id+"F3.wireOp",EDGE,"E4.sketch_text.stroke-37"),sQuery(id+"F3.wireOp",EDGE,"E4.sketch_text.stroke-38"),sQuery(id+"F3.wireOp",EDGE,"E4.sketch_text.stroke-39"),sQuery(id+"F3.wireOp",EDGE,"E4.sketch_text.stroke-40"),sQuery(id+"F3.wireOp",EDGE,"E4.sketch_text.stroke-41"),sQuery(id+"F3.wireOp",EDGE,"E4.sketch_text.stroke-42"),sQuery(id+"F3.wireOp",EDGE,"E4.sketch_text.stroke-43"),sQuery(id+"F3.wireOp",EDGE,"E4.sketch_text.stroke-44"),sQuery(id+"F3.wireOp",EDGE,"E4.sketch_text.stroke-45"),sQuery(id+"F3.wireOp",EDGE,"E4.sketch_text.stroke-46"),sQuery(id+"F3.wireOp",EDGE,"E4.sketch_text.stroke-47"),sQuery(id+"F3.wireOp",EDGE,"E4.sketch_text.stroke-48"),sQuery(id+"F3.wireOp",EDGE,"E4.sketch_text.stroke-49"),sQuery(id+"F3.wireOp",EDGE,"E4.sketch_text.stroke-50"),sQuery(id+"F3.wireOp",EDGE,"E4.sketch_text.stroke-51"),sQuery(id+"F3.wireOp",EDGE,"E4.sketch_text.stroke-52"),sQuery(id+"F3.wireOp",EDGE,"E4.sketch_text.stroke-53"),sQuery(id+"F3.wireOp",EDGE,"E4.sketch_text.stroke-54"),sQuery(id+"F3.wireOp",EDGE,"E4.sketch_text.stroke-55"),sQuery(id+"F3.wireOp",EDGE,"E4.sketch_text.stroke-56"),sQuery(id+"F3.wireOp",EDGE,"E4.sketch_text.stroke-57"),sQuery(id+"F3.wireOp",EDGE,"E4.sketch_text.stroke-58"),sQuery(id+"F3.wireOp",EDGE,"E4.sketch_text.stroke-59"),sQuery(id+"F3.wireOp",EDGE,"E4.sketch_text.stroke-60"),sQuery(id+"F3.wireOp",EDGE,"E4.sketch_text.stroke-61"),sQuery(id+"F3.wireOp",EDGE,"E4.sketch_text.stroke-62"),sQuery(id+"F3.wireOp",EDGE,"E4.sketch_text.stroke-71"),sQuery(id+"F3.wireOp",EDGE,"E4.sketch_text.stroke-72"),sQuery(id+"F3.wireOp",EDGE,"E4.sketch_text.stroke-73"),sQuery(id+"F3.wireOp",EDGE,"E4.sketch_text.stroke-74"),sQuery(id+"F3.wireOp",EDGE,"E4.sketch_text.stroke-75"),sQuery(id+"F3.wireOp",EDGE,"E4.sketch_text.stroke-76"),sQuery(id+"F3.wireOp",EDGE,"E4.sketch_text.stroke-77"),sQuery(id+"F3.wireOp",EDGE,"E4.sketch_text.stroke-78"),sQuery(id+"F3.wireOp",EDGE,"E4.sketch_text.stroke-79"),sQuery(id+"F3.wireOp",EDGE,"E4.sketch_text.stroke-80"),sQuery(id+"F3.wireOp",EDGE,"E4.sketch_text.stroke-81"),sQuery(id+"F3.wireOp",EDGE,"E4.sketch_text.stroke-82"),sQuery(id+"F3.wireOp",EDGE,"E4.sketch_text.stroke-83"),sQuery(id+"F3.wireOp",EDGE,"E4.sketch_text.stroke-84"),sQuery(id+"F3.wireOp",EDGE,"E4.sketch_text.stroke-85"),sQuery(id+"F3.wireOp",EDGE,"E4.sketch_text.stroke-86"),sQuery(id+"F3.wireOp",EDGE,"E4.sketch_text.stroke-87"),sQuery(id+"F3.wireOp",EDGE,"E4.sketch_text.stroke-88"),sQuery(id+"F3.wireOp",EDGE,"E4.sketch_text.stroke-89"),sQuery(id+"F3.wireOp",EDGE,"E4.sketch_text.stroke-90"),sQuery(id+"F3.wireOp",EDGE,"E4.sketch_text.stroke-91"),sQuery(id+"F3.wireOp",EDGE,"E4.sketch_text.stroke-92"),sQuery(id+"F3.wireOp",EDGE,"E4.sketch_text.stroke-93"),sQuery(id+"F3.wireOp",EDGE,"E4.sketch_text.stroke-94"),sQuery(id+"F3.wireOp",EDGE,"E4.sketch_text.stroke-95"),sQuery(id+"F3.wireOp",EDGE,"E4.sketch_text.stroke-96"),sQuery(id+"F3.wireOp",EDGE,"E4.sketch_text.stroke-97"),sQuery(id+"F3.wireOp",EDGE,"E4.sketch_text.stroke-103"),sQuery(id+"F3.wireOp",EDGE,"E4.sketch_text.stroke-104"),sQuery(id+"F3.wireOp",EDGE,"E4.sketch_text.stroke-105"),sQuery(id+"F3.wireOp",EDGE,"E4.sketch_text.stroke-106"),sQuery(id+"F3.wireOp",EDGE,"E4.sketch_text.stroke-107"),sQuery(id+"F3.wireOp",EDGE,"E4.sketch_text.stroke-108"),sQuery(id+"F3.wireOp",EDGE,"E4.sketch_text.stroke-109"),sQuery(id+"F3.wireOp",EDGE,"E4.sketch_text.stroke-110"),sQuery(id+"F3.wireOp",EDGE,"E4.sketch_text.stroke-111"),sQuery(id+"F3.wireOp",EDGE,"E4.sketch_text.stroke-112"),sQuery(id+"F3.wireOp",EDGE,"E4.sketch_text.stroke-113"),sQuery(id+"F3.wireOp",EDGE,"E4.sketch_text.stroke-114"),sQuery(id+"F3.wireOp",EDGE,"E4.sketch_text.stroke-115"),sQuery(id+"F3.wireOp",EDGE,"E4.sketch_text.stroke-116"),sQuery(id+"F3.wireOp",EDGE,"E4.sketch_text.stroke-117"),sQuery(id+"F3.wireOp",EDGE,"E4.sketch_text.stroke-118"),sQuery(id+"F3.wireOp",EDGE,"E4.sketch_text.stroke-119"),sQuery(id+"F3.wireOp",EDGE,"E4.sketch_text.stroke-120"),sQuery(id+"F3.wireOp",EDGE,"E4.sketch_text.stroke-121"),sQuery(id+"F3.wireOp",EDGE,"E4.sketch_text.stroke-122"),sQuery(id+"F3.wireOp",EDGE,"E4.sketch_text.stroke-123"),sQuery(id+"F3.wireOp",EDGE,"E4.sketch_text.stroke-124"),sQuery(id+"F3.wireOp",EDGE,"E4.sketch_text.stroke-125"),sQuery(id+"F3.wireOp",EDGE,"E4.sketch_text.stroke-126"),sQuery(id+"F3.wireOp",EDGE,"E4.sketch_text.stroke-127"),sQuery(id+"F3.wireOp",EDGE,"E4.sketch_text.stroke-128"),sQuery(id+"F3.wireOp",EDGE,"E4.sketch_text.stroke-129"),sQuery(id+"F3.wireOp",EDGE,"E4.sketch_text.stroke-130"),sQuery(id+"F3.wireOp",EDGE,"E4.sketch_text.stroke-131"),sQuery(id+"F3.wireOp",EDGE,"E4.sketch_text.stroke-132"),sQuery(id+"F3.wireOp",EDGE,"E4.sketch_text.stroke-133"),sQuery(id+"F3.wireOp",EDGE,"E4.sketch_text.stroke-134"),sQuery(id+"F3.wireOp",EDGE,"E4.sketch_text.stroke-135"),sQuery(id+"F3.wireOp",EDGE,"E4.sketch_text.stroke-136"),sQuery(id+"F3.wireOp",EDGE,"E4.sketch_text.stroke-137"),sQuery(id+"F3.wireOp",EDGE,"E4.sketch_text.stroke-138"),sQuery(id+"F3.wireOp",EDGE,"E4.sketch_text.stroke-139"),sQuery(id+"F3.wireOp",EDGE,"E4.sketch_text.stroke-140"),sQuery(id+"F3.wireOp",EDGE,"E4.sketch_text.stroke-141"),sQuery(id+"F3.wireOp",EDGE,"E4.sketch_text.stroke-142"),sQuery(id+"F3.wireOp",EDGE,"E4.sketch_text.stroke-143"),sQuery(id+"F3.wireOp",EDGE,"E4.sketch_text.stroke-144"),sQuery(id+"F3.wireOp",EDGE,"E4.sketch_text.stroke-145"),sQuery(id+"F3.wireOp",EDGE,"E4.sketch_text.stroke-146"),sQuery(id+"F3.wireOp",EDGE,"E4.sketch_text.stroke-147"),sQuery(id+"F3.wireOp",EDGE,"E4.sketch_text.stroke-148"),sQuery(id+"F3.wireOp",EDGE,"E4.sketch_text.stroke-149"),sQuery(id+"F3.wireOp",EDGE,"E4.sketch_text.stroke-150"),sQuery(id+"F3.wireOp",EDGE,"E4.sketch_text.stroke-151"),sQuery(id+"F3.wireOp",EDGE,"E4.sketch_text.stroke-152"),sQuery(id+"F3.wireOp",EDGE,"E4.sketch_text.stroke-153"),sQuery(id+"F3.wireOp",EDGE,"E4.sketch_text.stroke-159"),sQuery(id+"F3.wireOp",EDGE,"E4.sketch_text.stroke-160"),sQuery(id+"F3.wireOp",EDGE,"E4.sketch_text.stroke-161"),sQuery(id+"F3.wireOp",EDGE,"E4.sketch_text.stroke-162"),sQuery(id+"F3.wireOp",EDGE,"E4.sketch_text.stroke-163"),sQuery(id+"F3.wireOp",EDGE,"E4.sketch_text.stroke-164"),sQuery(id+"F3.wireOp",EDGE,"E4.sketch_text.stroke-165"),sQuery(id+"F3.wireOp",EDGE,"E4.sketch_text.stroke-166"),sQuery(id+"F3.wireOp",EDGE,"E4.sketch_text.stroke-167"),sQuery(id+"F3.wireOp",EDGE,"E4.sketch_text.stroke-168"),sQuery(id+"F3.wireOp",EDGE,"E4.sketch_text.stroke-169"),sQuery(id+"F3.wireOp",EDGE,"E4.sketch_text.stroke-170"),sQuery(id+"F3.wireOp",EDGE,"E4.sketch_text.stroke-171"),sQuery(id+"F3.wireOp",EDGE,"E4.sketch_text.stroke-172"),sQuery(id+"F3.wireOp",EDGE,"E4.sketch_text.stroke-173"),sQuery(id+"F3.wireOp",EDGE,"E4.sketch_text.stroke-174"),sQuery(id+"F3.wireOp",EDGE,"E4.sketch_text.stroke-175"),sQuery(id+"F3.wireOp",EDGE,"E4.sketch_text.stroke-176"),sQuery(id+"F3.wireOp",EDGE,"E4.sketch_text.stroke-177"),sQuery(id+"F3.wireOp",EDGE,"E4.sketch_text.stroke-178"),sQuery(id+"F3.wireOp",EDGE,"E4.sketch_text.stroke-179"),sQuery(id+"F3.wireOp",EDGE,"E4.sketch_text.stroke-180"),sQuery(id+"F5.wireOp",EDGE,"727ac2c1-f511-4829-95a7-a443ef16a4cd"),subQ2])],"isStart":true}),makeQuery(id+"F6.opExtrude","SWEPT_FACE",FACE,{"disambiguationData":[OSD([subQ2])]})]),OD(0.0)],"derivedFrom":makeQuery(id+"F1.opExtrude","CAP_EDGE",EDGE,{"disambiguationData":[OSD([subQ0])],"isStart":false})});}
            var Q19;
            {var subQ0=sQuery(id+"F0.wireOp",EDGE,"E0.top");var subQ1=sQuery(id+"F0.wireOp",EDGE,"E0.bottom");var subQ2=sQuery(id+"F5.wireOp",EDGE,"1a034e28-a7c2-419d-97de-c33d70a47301");Q19=makeQuery(id+"F6.boolean.opBoolean","SPLIT",EDGE,{"disambiguationData":[TD([makeQuery(id+"F1.opExtrude","CAP_FACE",FACE,{"disambiguationData":[OSD([subQ1,subQ0,sQuery(id+"F0.wireOp",EDGE,"E0.left"),sQuery(id+"F0.wireOp",EDGE,"E0.right")])],"isStart":false}),makeQuery(id+"F1.opExtrude","SWEPT_FACE",FACE,{"disambiguationData":[OSD([subQ0])]}),makeQuery(id+"F6.opExtrude","CAP_FACE",FACE,{"disambiguationData":[OSD([subQ1,sQuery(id+"F2.wireOp",EDGE,"E2.sketch_text.stroke-0"),sQuery(id+"F2.wireOp",EDGE,"E2.sketch_text.stroke-1"),sQuery(id+"F2.wireOp",EDGE,"E2.sketch_text.stroke-2"),sQuery(id+"F2.wireOp",EDGE,"E2.sketch_text.stroke-3"),sQuery(id+"F2.wireOp",EDGE,"E2.sketch_text.stroke-4"),sQuery(id+"F2.wireOp",EDGE,"E2.sketch_text.stroke-5"),sQuery(id+"F2.wireOp",EDGE,"E2.sketch_text.stroke-6"),sQuery(id+"F2.wireOp",EDGE,"E2.sketch_text.stroke-7"),sQuery(id+"F2.wireOp",EDGE,"E2.sketch_text.stroke-8"),sQuery(id+"F2.wireOp",EDGE,"E2.sketch_text.stroke-9"),sQuery(id+"F2.wireOp",EDGE,"E2.sketch_text.stroke-10"),sQuery(id+"F2.wireOp",EDGE,"E2.sketch_text.stroke-11"),sQuery(id+"F2.wireOp",EDGE,"E2.sketch_text.stroke-12"),sQuery(id+"F2.wireOp",EDGE,"E2.sketch_text.stroke-13"),sQuery(id+"F2.wireOp",EDGE,"E2.sketch_text.stroke-14"),sQuery(id+"F2.wireOp",EDGE,"E2.sketch_text.stroke-15"),sQuery(id+"F2.wireOp",EDGE,"E2.sketch_text.stroke-16"),sQuery(id+"F2.wireOp",EDGE,"E2.sketch_text.stroke-17"),sQuery(id+"F2.wireOp",EDGE,"E2.sketch_text.stroke-18"),sQuery(id+"F2.wireOp",EDGE,"E2.sketch_text.stroke-19"),sQuery(id+"F2.wireOp",EDGE,"E2.sketch_text.stroke-20"),sQuery(id+"F2.wireOp",EDGE,"E2.sketch_text.stroke-21"),sQuery(id+"F2.wireOp",EDGE,"E2.sketch_text.stroke-22"),sQuery(id+"F2.wireOp",EDGE,"E2.sketch_text.stroke-23"),sQuery(id+"F2.wireOp",EDGE,"E2.sketch_text.stroke-24"),sQuery(id+"F2.wireOp",EDGE,"E2.sketch_text.stroke-25"),sQuery(id+"F2.wireOp",EDGE,"E2.sketch_text.stroke-26"),sQuery(id+"F2.wireOp",EDGE,"E2.sketch_text.stroke-27"),sQuery(id+"F2.wireOp",EDGE,"E2.sketch_text.stroke-28"),sQuery(id+"F2.wireOp",EDGE,"E2.sketch_text.stroke-29"),sQuery(id+"F2.wireOp",EDGE,"E2.sketch_text.stroke-30"),sQuery(id+"F2.wireOp",EDGE,"E2.sketch_text.stroke-31"),sQuery(id+"F2.wireOp",EDGE,"E2.sketch_text.stroke-32"),sQuery(id+"F2.wireOp",EDGE,"E2.sketch_text.stroke-33"),sQuery(id+"F2.wireOp",EDGE,"E2.sketch_text.stroke-34"),sQuery(id+"F2.wireOp",EDGE,"E2.sketch_text.stroke-35"),sQuery(id+"F2.wireOp",EDGE,"E2.sketch_text.stroke-36"),sQuery(id+"F2.wireOp",EDGE,"E2.sketch_text.stroke-37"),sQuery(id+"F2.wireOp",EDGE,"E2.sketch_text.stroke-38"),sQuery(id+"F2.wireOp",EDGE,"E2.sketch_text.stroke-39"),sQuery(id+"F2.wireOp",EDGE,"E2.sketch_text.stroke-40"),sQuery(id+"F2.wireOp",EDGE,"E2.sketch_text.stroke-41"),sQuery(id+"F2.wireOp",EDGE,"E2.sketch_text.stroke-42"),sQuery(id+"F2.wireOp",EDGE,"E2.sketch_text.stroke-43"),sQuery(id+"F2.wireOp",EDGE,"E2.sketch_text.stroke-44"),sQuery(id+"F2.wireOp",EDGE,"E2.sketch_text.stroke-45"),sQuery(id+"F2.wireOp",EDGE,"E2.sketch_text.stroke-46"),sQuery(id+"F2.wireOp",EDGE,"E2.sketch_text.stroke-47"),sQuery(id+"F2.wireOp",EDGE,"E2.sketch_text.stroke-48"),sQuery(id+"F2.wireOp",EDGE,"E2.sketch_text.stroke-49"),sQuery(id+"F2.wireOp",EDGE,"E2.sketch_text.stroke-50"),sQuery(id+"F2.wireOp",EDGE,"E2.sketch_text.stroke-51"),sQuery(id+"F2.wireOp",EDGE,"E2.sketch_text.stroke-52"),sQuery(id+"F2.wireOp",EDGE,"E2.sketch_text.stroke-53"),sQuery(id+"F2.wireOp",EDGE,"E2.sketch_text.stroke-54"),sQuery(id+"F2.wireOp",EDGE,"E2.sketch_text.stroke-55"),sQuery(id+"F2.wireOp",EDGE,"E2.sketch_text.stroke-56"),sQuery(id+"F2.wireOp",EDGE,"E2.sketch_text.stroke-57"),sQuery(id+"F2.wireOp",EDGE,"E2.sketch_text.stroke-58"),sQuery(id+"F2.wireOp",EDGE,"E2.sketch_text.stroke-59"),sQuery(id+"F2.wireOp",EDGE,"E2.sketch_text.stroke-60"),sQuery(id+"F2.wireOp",EDGE,"E2.sketch_text.stroke-61"),sQuery(id+"F2.wireOp",EDGE,"E2.sketch_text.stroke-62"),sQuery(id+"F2.wireOp",EDGE,"E2.sketch_text.stroke-63"),sQuery(id+"F2.wireOp",EDGE,"E2.sketch_text.stroke-64"),sQuery(id+"F2.wireOp",EDGE,"E2.sketch_text.stroke-65"),sQuery(id+"F2.wireOp",EDGE,"E2.sketch_text.stroke-66"),sQuery(id+"F2.wireOp",EDGE,"E2.sketch_text.stroke-67"),sQuery(id+"F2.wireOp",EDGE,"E2.sketch_text.stroke-68"),sQuery(id+"F2.wireOp",EDGE,"E2.sketch_text.stroke-69"),sQuery(id+"F2.wireOp",EDGE,"E2.sketch_text.stroke-70"),sQuery(id+"F2.wireOp",EDGE,"E2.sketch_text.stroke-71"),sQuery(id+"F2.wireOp",EDGE,"E2.sketch_text.stroke-72"),sQuery(id+"F2.wireOp",EDGE,"E2.sketch_text.stroke-73"),sQuery(id+"F2.wireOp",EDGE,"E2.sketch_text.stroke-74"),sQuery(id+"F2.wireOp",EDGE,"E2.sketch_text.stroke-75"),sQuery(id+"F2.wireOp",EDGE,"E2.sketch_text.stroke-76"),sQuery(id+"F2.wireOp",EDGE,"E2.sketch_text.stroke-77"),sQuery(id+"F2.wireOp",EDGE,"E2.sketch_text.stroke-78"),sQuery(id+"F2.wireOp",EDGE,"E2.sketch_text.stroke-79"),sQuery(id+"F2.wireOp",EDGE,"E2.sketch_text.stroke-80"),sQuery(id+"F2.wireOp",EDGE,"E2.sketch_text.stroke-81"),sQuery(id+"F2.wireOp",EDGE,"E2.sketch_text.stroke-82"),sQuery(id+"F2.wireOp",EDGE,"E2.sketch_text.stroke-83"),sQuery(id+"F2.wireOp",EDGE,"E2.sketch_text.stroke-84"),sQuery(id+"F2.wireOp",EDGE,"E2.sketch_text.stroke-85"),sQuery(id+"F2.wireOp",EDGE,"E2.sketch_text.stroke-86"),sQuery(id+"F2.wireOp",EDGE,"E2.sketch_text.stroke-87"),sQuery(id+"F2.wireOp",EDGE,"E2.sketch_text.stroke-88"),sQuery(id+"F2.wireOp",EDGE,"E2.sketch_text.stroke-89"),sQuery(id+"F2.wireOp",EDGE,"E2.sketch_text.stroke-90"),sQuery(id+"F2.wireOp",EDGE,"E2.sketch_text.stroke-91"),sQuery(id+"F2.wireOp",EDGE,"E2.sketch_text.stroke-92"),sQuery(id+"F2.wireOp",EDGE,"E2.sketch_text.stroke-93"),sQuery(id+"F2.wireOp",EDGE,"E2.sketch_text.stroke-94"),sQuery(id+"F2.wireOp",EDGE,"E2.sketch_text.stroke-95"),sQuery(id+"F2.wireOp",EDGE,"E2.sketch_text.stroke-96"),sQuery(id+"F2.wireOp",EDGE,"E2.sketch_text.stroke-97"),sQuery(id+"F2.wireOp",EDGE,"E2.sketch_text.stroke-98"),sQuery(id+"F2.wireOp",EDGE,"E2.sketch_text.stroke-99"),sQuery(id+"F2.wireOp",EDGE,"E2.sketch_text.stroke-100"),sQuery(id+"F2.wireOp",EDGE,"E2.sketch_text.stroke-101"),sQuery(id+"F2.wireOp",EDGE,"E2.sketch_text.stroke-102"),sQuery(id+"F2.wireOp",EDGE,"E2.sketch_text.stroke-103"),sQuery(id+"F2.wireOp",EDGE,"E2.sketch_text.stroke-104"),sQuery(id+"F2.wireOp",EDGE,"E2.sketch_text.stroke-105"),sQuery(id+"F2.wireOp",EDGE,"E2.sketch_text.stroke-106"),sQuery(id+"F2.wireOp",EDGE,"E2.sketch_text.stroke-107"),sQuery(id+"F2.wireOp",EDGE,"E2.sketch_text.stroke-108"),sQuery(id+"F2.wireOp",EDGE,"E2.sketch_text.stroke-109"),sQuery(id+"F2.wireOp",EDGE,"E2.sketch_text.stroke-110"),sQuery(id+"F2.wireOp",EDGE,"E2.sketch_text.stroke-111"),sQuery(id+"F2.wireOp",EDGE,"E2.sketch_text.stroke-112"),sQuery(id+"F2.wireOp",EDGE,"E2.sketch_text.stroke-113"),sQuery(id+"F2.wireOp",EDGE,"E2.sketch_text.stroke-114"),sQuery(id+"F2.wireOp",EDGE,"E2.sketch_text.stroke-115"),sQuery(id+"F2.wireOp",EDGE,"E2.sketch_text.stroke-116"),sQuery(id+"F2.wireOp",EDGE,"E2.sketch_text.stroke-117"),sQuery(id+"F2.wireOp",EDGE,"E2.sketch_text.stroke-118"),sQuery(id+"F2.wireOp",EDGE,"E2.sketch_text.stroke-119"),sQuery(id+"F2.wireOp",EDGE,"E2.sketch_text.stroke-120"),sQuery(id+"F2.wireOp",EDGE,"E2.sketch_text.stroke-121"),sQuery(id+"F2.wireOp",EDGE,"E2.sketch_text.stroke-122"),sQuery(id+"F2.wireOp",EDGE,"E2.sketch_text.stroke-123"),sQuery(id+"F2.wireOp",EDGE,"E2.sketch_text.stroke-124"),sQuery(id+"F2.wireOp",EDGE,"E2.sketch_text.stroke-125"),sQuery(id+"F2.wireOp",EDGE,"E2.sketch_text.stroke-126"),sQuery(id+"F2.wireOp",EDGE,"E2.sketch_text.stroke-127"),sQuery(id+"F2.wireOp",EDGE,"E2.sketch_text.stroke-128"),sQuery(id+"F2.wireOp",EDGE,"E2.sketch_text.stroke-129"),sQuery(id+"F2.wireOp",EDGE,"E2.sketch_text.stroke-130"),sQuery(id+"F2.wireOp",EDGE,"E2.sketch_text.stroke-131"),sQuery(id+"F2.wireOp",EDGE,"E2.sketch_text.stroke-132"),sQuery(id+"F2.wireOp",EDGE,"E2.sketch_text.stroke-133"),sQuery(id+"F2.wireOp",EDGE,"E2.sketch_text.stroke-134"),sQuery(id+"F2.wireOp",EDGE,"E2.sketch_text.stroke-135"),sQuery(id+"F2.wireOp",EDGE,"E2.sketch_text.stroke-136"),sQuery(id+"F2.wireOp",EDGE,"E2.sketch_text.stroke-137"),sQuery(id+"F2.wireOp",EDGE,"E2.sketch_text.stroke-138"),sQuery(id+"F2.wireOp",EDGE,"E2.sketch_text.stroke-139"),sQuery(id+"F2.wireOp",EDGE,"E2.sketch_text.stroke-140"),sQuery(id+"F2.wireOp",EDGE,"E2.sketch_text.stroke-141"),sQuery(id+"F2.wireOp",EDGE,"E2.sketch_text.stroke-142"),sQuery(id+"F2.wireOp",EDGE,"E2.sketch_text.stroke-143"),sQuery(id+"F2.wireOp",EDGE,"E2.sketch_text.stroke-144"),sQuery(id+"F2.wireOp",EDGE,"E2.sketch_text.stroke-145"),sQuery(id+"F2.wireOp",EDGE,"E2.sketch_text.stroke-146"),sQuery(id+"F2.wireOp",EDGE,"E2.sketch_text.stroke-147"),sQuery(id+"F2.wireOp",EDGE,"E2.sketch_text.stroke-148"),sQuery(id+"F2.wireOp",EDGE,"E2.sketch_text.stroke-149"),sQuery(id+"F2.wireOp",EDGE,"E2.sketch_text.stroke-150"),sQuery(id+"F2.wireOp",EDGE,"E2.sketch_text.stroke-151"),sQuery(id+"F2.wireOp",EDGE,"E2.sketch_text.stroke-152"),sQuery(id+"F2.wireOp",EDGE,"E2.sketch_text.stroke-153"),sQuery(id+"F2.wireOp",EDGE,"E2.sketch_text.stroke-154"),sQuery(id+"F2.wireOp",EDGE,"E2.sketch_text.stroke-155"),sQuery(id+"F2.wireOp",EDGE,"E2.sketch_text.stroke-156"),sQuery(id+"F2.wireOp",EDGE,"E2.sketch_text.stroke-157"),sQuery(id+"F2.wireOp",EDGE,"E2.sketch_text.stroke-158"),sQuery(id+"F2.wireOp",EDGE,"E2.sketch_text.stroke-159"),sQuery(id+"F2.wireOp",EDGE,"E2.sketch_text.stroke-160"),sQuery(id+"F2.wireOp",EDGE,"E2.sketch_text.stroke-161"),sQuery(id+"F2.wireOp",EDGE,"E2.sketch_text.stroke-162"),sQuery(id+"F2.wireOp",EDGE,"E2.sketch_text.stroke-163"),sQuery(id+"F2.wireOp",EDGE,"E2.sketch_text.stroke-164"),sQuery(id+"F2.wireOp",EDGE,"E2.sketch_text.stroke-165"),sQuery(id+"F2.wireOp",EDGE,"E2.sketch_text.stroke-166"),sQuery(id+"F2.wireOp",EDGE,"E2.sketch_text.stroke-167"),sQuery(id+"F2.wireOp",EDGE,"E2.sketch_text.stroke-168"),sQuery(id+"F2.wireOp",EDGE,"E2.sketch_text.stroke-169"),sQuery(id+"F2.wireOp",EDGE,"E2.sketch_text.stroke-170"),sQuery(id+"F2.wireOp",EDGE,"E2.sketch_text.stroke-171"),sQuery(id+"F2.wireOp",EDGE,"E2.sketch_text.stroke-172"),sQuery(id+"F2.wireOp",EDGE,"E2.sketch_text.stroke-173"),sQuery(id+"F3.wireOp",EDGE,"E4.sketch_text.stroke-0"),sQuery(id+"F3.wireOp",EDGE,"E4.sketch_text.stroke-1"),sQuery(id+"F3.wireOp",EDGE,"E4.sketch_text.stroke-2"),sQuery(id+"F3.wireOp",EDGE,"E4.sketch_text.stroke-3"),sQuery(id+"F3.wireOp",EDGE,"E4.sketch_text.stroke-4"),sQuery(id+"F3.wireOp",EDGE,"E4.sketch_text.stroke-5"),sQuery(id+"F3.wireOp",EDGE,"E4.sketch_text.stroke-6"),sQuery(id+"F3.wireOp",EDGE,"E4.sketch_text.stroke-7"),sQuery(id+"F3.wireOp",EDGE,"E4.sketch_text.stroke-8"),sQuery(id+"F3.wireOp",EDGE,"E4.sketch_text.stroke-9"),sQuery(id+"F3.wireOp",EDGE,"E4.sketch_text.stroke-10"),sQuery(id+"F3.wireOp",EDGE,"E4.sketch_text.stroke-11"),sQuery(id+"F3.wireOp",EDGE,"E4.sketch_text.stroke-12"),sQuery(id+"F3.wireOp",EDGE,"E4.sketch_text.stroke-13"),sQuery(id+"F3.wireOp",EDGE,"E4.sketch_text.stroke-14"),sQuery(id+"F3.wireOp",EDGE,"E4.sketch_text.stroke-15"),sQuery(id+"F3.wireOp",EDGE,"E4.sketch_text.stroke-16"),sQuery(id+"F3.wireOp",EDGE,"E4.sketch_text.stroke-17"),sQuery(id+"F3.wireOp",EDGE,"E4.sketch_text.stroke-18"),sQuery(id+"F3.wireOp",EDGE,"E4.sketch_text.stroke-19"),sQuery(id+"F3.wireOp",EDGE,"E4.sketch_text.stroke-20"),sQuery(id+"F3.wireOp",EDGE,"E4.sketch_text.stroke-21"),sQuery(id+"F3.wireOp",EDGE,"E4.sketch_text.stroke-22"),sQuery(id+"F3.wireOp",EDGE,"E4.sketch_text.stroke-23"),sQuery(id+"F3.wireOp",EDGE,"E4.sketch_text.stroke-24"),sQuery(id+"F3.wireOp",EDGE,"E4.sketch_text.stroke-25"),sQuery(id+"F3.wireOp",EDGE,"E4.sketch_text.stroke-26"),sQuery(id+"F3.wireOp",EDGE,"E4.sketch_text.stroke-27"),sQuery(id+"F3.wireOp",EDGE,"E4.sketch_text.stroke-28"),sQuery(id+"F3.wireOp",EDGE,"E4.sketch_text.stroke-29"),sQuery(id+"F3.wireOp",EDGE,"E4.sketch_text.stroke-30"),sQuery(id+"F3.wireOp",EDGE,"E4.sketch_text.stroke-31"),sQuery(id+"F3.wireOp",EDGE,"E4.sketch_text.stroke-32"),sQuery(id+"F3.wireOp",EDGE,"E4.sketch_text.stroke-33"),sQuery(id+"F3.wireOp",EDGE,"E4.sketch_text.stroke-34"),sQuery(id+"F3.wireOp",EDGE,"E4.sketch_text.stroke-35"),sQuery(id+"F3.wireOp",EDGE,"E4.sketch_text.stroke-36"),sQuery(id+"F3.wireOp",EDGE,"E4.sketch_text.stroke-37"),sQuery(id+"F3.wireOp",EDGE,"E4.sketch_text.stroke-38"),sQuery(id+"F3.wireOp",EDGE,"E4.sketch_text.stroke-39"),sQuery(id+"F3.wireOp",EDGE,"E4.sketch_text.stroke-40"),sQuery(id+"F3.wireOp",EDGE,"E4.sketch_text.stroke-41"),sQuery(id+"F3.wireOp",EDGE,"E4.sketch_text.stroke-42"),sQuery(id+"F3.wireOp",EDGE,"E4.sketch_text.stroke-43"),sQuery(id+"F3.wireOp",EDGE,"E4.sketch_text.stroke-44"),sQuery(id+"F3.wireOp",EDGE,"E4.sketch_text.stroke-45"),sQuery(id+"F3.wireOp",EDGE,"E4.sketch_text.stroke-46"),sQuery(id+"F3.wireOp",EDGE,"E4.sketch_text.stroke-47"),sQuery(id+"F3.wireOp",EDGE,"E4.sketch_text.stroke-48"),sQuery(id+"F3.wireOp",EDGE,"E4.sketch_text.stroke-49"),sQuery(id+"F3.wireOp",EDGE,"E4.sketch_text.stroke-50"),sQuery(id+"F3.wireOp",EDGE,"E4.sketch_text.stroke-51"),sQuery(id+"F3.wireOp",EDGE,"E4.sketch_text.stroke-52"),sQuery(id+"F3.wireOp",EDGE,"E4.sketch_text.stroke-53"),sQuery(id+"F3.wireOp",EDGE,"E4.sketch_text.stroke-54"),sQuery(id+"F3.wireOp",EDGE,"E4.sketch_text.stroke-55"),sQuery(id+"F3.wireOp",EDGE,"E4.sketch_text.stroke-56"),sQuery(id+"F3.wireOp",EDGE,"E4.sketch_text.stroke-57"),sQuery(id+"F3.wireOp",EDGE,"E4.sketch_text.stroke-58"),sQuery(id+"F3.wireOp",EDGE,"E4.sketch_text.stroke-59"),sQuery(id+"F3.wireOp",EDGE,"E4.sketch_text.stroke-60"),sQuery(id+"F3.wireOp",EDGE,"E4.sketch_text.stroke-61"),sQuery(id+"F3.wireOp",EDGE,"E4.sketch_text.stroke-62"),sQuery(id+"F3.wireOp",EDGE,"E4.sketch_text.stroke-71"),sQuery(id+"F3.wireOp",EDGE,"E4.sketch_text.stroke-72"),sQuery(id+"F3.wireOp",EDGE,"E4.sketch_text.stroke-73"),sQuery(id+"F3.wireOp",EDGE,"E4.sketch_text.stroke-74"),sQuery(id+"F3.wireOp",EDGE,"E4.sketch_text.stroke-75"),sQuery(id+"F3.wireOp",EDGE,"E4.sketch_text.stroke-76"),sQuery(id+"F3.wireOp",EDGE,"E4.sketch_text.stroke-77"),sQuery(id+"F3.wireOp",EDGE,"E4.sketch_text.stroke-78"),sQuery(id+"F3.wireOp",EDGE,"E4.sketch_text.stroke-79"),sQuery(id+"F3.wireOp",EDGE,"E4.sketch_text.stroke-80"),sQuery(id+"F3.wireOp",EDGE,"E4.sketch_text.stroke-81"),sQuery(id+"F3.wireOp",EDGE,"E4.sketch_text.stroke-82"),sQuery(id+"F3.wireOp",EDGE,"E4.sketch_text.stroke-83"),sQuery(id+"F3.wireOp",EDGE,"E4.sketch_text.stroke-84"),sQuery(id+"F3.wireOp",EDGE,"E4.sketch_text.stroke-85"),sQuery(id+"F3.wireOp",EDGE,"E4.sketch_text.stroke-86"),sQuery(id+"F3.wireOp",EDGE,"E4.sketch_text.stroke-87"),sQuery(id+"F3.wireOp",EDGE,"E4.sketch_text.stroke-88"),sQuery(id+"F3.wireOp",EDGE,"E4.sketch_text.stroke-89"),sQuery(id+"F3.wireOp",EDGE,"E4.sketch_text.stroke-90"),sQuery(id+"F3.wireOp",EDGE,"E4.sketch_text.stroke-91"),sQuery(id+"F3.wireOp",EDGE,"E4.sketch_text.stroke-92"),sQuery(id+"F3.wireOp",EDGE,"E4.sketch_text.stroke-93"),sQuery(id+"F3.wireOp",EDGE,"E4.sketch_text.stroke-94"),sQuery(id+"F3.wireOp",EDGE,"E4.sketch_text.stroke-95"),sQuery(id+"F3.wireOp",EDGE,"E4.sketch_text.stroke-96"),sQuery(id+"F3.wireOp",EDGE,"E4.sketch_text.stroke-97"),sQuery(id+"F3.wireOp",EDGE,"E4.sketch_text.stroke-103"),sQuery(id+"F3.wireOp",EDGE,"E4.sketch_text.stroke-104"),sQuery(id+"F3.wireOp",EDGE,"E4.sketch_text.stroke-105"),sQuery(id+"F3.wireOp",EDGE,"E4.sketch_text.stroke-106"),sQuery(id+"F3.wireOp",EDGE,"E4.sketch_text.stroke-107"),sQuery(id+"F3.wireOp",EDGE,"E4.sketch_text.stroke-108"),sQuery(id+"F3.wireOp",EDGE,"E4.sketch_text.stroke-109"),sQuery(id+"F3.wireOp",EDGE,"E4.sketch_text.stroke-110"),sQuery(id+"F3.wireOp",EDGE,"E4.sketch_text.stroke-111"),sQuery(id+"F3.wireOp",EDGE,"E4.sketch_text.stroke-112"),sQuery(id+"F3.wireOp",EDGE,"E4.sketch_text.stroke-113"),sQuery(id+"F3.wireOp",EDGE,"E4.sketch_text.stroke-114"),sQuery(id+"F3.wireOp",EDGE,"E4.sketch_text.stroke-115"),sQuery(id+"F3.wireOp",EDGE,"E4.sketch_text.stroke-116"),sQuery(id+"F3.wireOp",EDGE,"E4.sketch_text.stroke-117"),sQuery(id+"F3.wireOp",EDGE,"E4.sketch_text.stroke-118"),sQuery(id+"F3.wireOp",EDGE,"E4.sketch_text.stroke-119"),sQuery(id+"F3.wireOp",EDGE,"E4.sketch_text.stroke-120"),sQuery(id+"F3.wireOp",EDGE,"E4.sketch_text.stroke-121"),sQuery(id+"F3.wireOp",EDGE,"E4.sketch_text.stroke-122"),sQuery(id+"F3.wireOp",EDGE,"E4.sketch_text.stroke-123"),sQuery(id+"F3.wireOp",EDGE,"E4.sketch_text.stroke-124"),sQuery(id+"F3.wireOp",EDGE,"E4.sketch_text.stroke-125"),sQuery(id+"F3.wireOp",EDGE,"E4.sketch_text.stroke-126"),sQuery(id+"F3.wireOp",EDGE,"E4.sketch_text.stroke-127"),sQuery(id+"F3.wireOp",EDGE,"E4.sketch_text.stroke-128"),sQuery(id+"F3.wireOp",EDGE,"E4.sketch_text.stroke-129"),sQuery(id+"F3.wireOp",EDGE,"E4.sketch_text.stroke-130"),sQuery(id+"F3.wireOp",EDGE,"E4.sketch_text.stroke-131"),sQuery(id+"F3.wireOp",EDGE,"E4.sketch_text.stroke-132"),sQuery(id+"F3.wireOp",EDGE,"E4.sketch_text.stroke-133"),sQuery(id+"F3.wireOp",EDGE,"E4.sketch_text.stroke-134"),sQuery(id+"F3.wireOp",EDGE,"E4.sketch_text.stroke-135"),sQuery(id+"F3.wireOp",EDGE,"E4.sketch_text.stroke-136"),sQuery(id+"F3.wireOp",EDGE,"E4.sketch_text.stroke-137"),sQuery(id+"F3.wireOp",EDGE,"E4.sketch_text.stroke-138"),sQuery(id+"F3.wireOp",EDGE,"E4.sketch_text.stroke-139"),sQuery(id+"F3.wireOp",EDGE,"E4.sketch_text.stroke-140"),sQuery(id+"F3.wireOp",EDGE,"E4.sketch_text.stroke-141"),sQuery(id+"F3.wireOp",EDGE,"E4.sketch_text.stroke-142"),sQuery(id+"F3.wireOp",EDGE,"E4.sketch_text.stroke-143"),sQuery(id+"F3.wireOp",EDGE,"E4.sketch_text.stroke-144"),sQuery(id+"F3.wireOp",EDGE,"E4.sketch_text.stroke-145"),sQuery(id+"F3.wireOp",EDGE,"E4.sketch_text.stroke-146"),sQuery(id+"F3.wireOp",EDGE,"E4.sketch_text.stroke-147"),sQuery(id+"F3.wireOp",EDGE,"E4.sketch_text.stroke-148"),sQuery(id+"F3.wireOp",EDGE,"E4.sketch_text.stroke-149"),sQuery(id+"F3.wireOp",EDGE,"E4.sketch_text.stroke-150"),sQuery(id+"F3.wireOp",EDGE,"E4.sketch_text.stroke-151"),sQuery(id+"F3.wireOp",EDGE,"E4.sketch_text.stroke-152"),sQuery(id+"F3.wireOp",EDGE,"E4.sketch_text.stroke-153"),sQuery(id+"F3.wireOp",EDGE,"E4.sketch_text.stroke-159"),sQuery(id+"F3.wireOp",EDGE,"E4.sketch_text.stroke-160"),sQuery(id+"F3.wireOp",EDGE,"E4.sketch_text.stroke-161"),sQuery(id+"F3.wireOp",EDGE,"E4.sketch_text.stroke-162"),sQuery(id+"F3.wireOp",EDGE,"E4.sketch_text.stroke-163"),sQuery(id+"F3.wireOp",EDGE,"E4.sketch_text.stroke-164"),sQuery(id+"F3.wireOp",EDGE,"E4.sketch_text.stroke-165"),sQuery(id+"F3.wireOp",EDGE,"E4.sketch_text.stroke-166"),sQuery(id+"F3.wireOp",EDGE,"E4.sketch_text.stroke-167"),sQuery(id+"F3.wireOp",EDGE,"E4.sketch_text.stroke-168"),sQuery(id+"F3.wireOp",EDGE,"E4.sketch_text.stroke-169"),sQuery(id+"F3.wireOp",EDGE,"E4.sketch_text.stroke-170"),sQuery(id+"F3.wireOp",EDGE,"E4.sketch_text.stroke-171"),sQuery(id+"F3.wireOp",EDGE,"E4.sketch_text.stroke-172"),sQuery(id+"F3.wireOp",EDGE,"E4.sketch_text.stroke-173"),sQuery(id+"F3.wireOp",EDGE,"E4.sketch_text.stroke-174"),sQuery(id+"F3.wireOp",EDGE,"E4.sketch_text.stroke-175"),sQuery(id+"F3.wireOp",EDGE,"E4.sketch_text.stroke-176"),sQuery(id+"F3.wireOp",EDGE,"E4.sketch_text.stroke-177"),sQuery(id+"F3.wireOp",EDGE,"E4.sketch_text.stroke-178"),sQuery(id+"F3.wireOp",EDGE,"E4.sketch_text.stroke-179"),sQuery(id+"F3.wireOp",EDGE,"E4.sketch_text.stroke-180"),sQuery(id+"F5.wireOp",EDGE,"727ac2c1-f511-4829-95a7-a443ef16a4cd"),subQ2])],"isStart":true}),makeQuery(id+"F6.opExtrude","SWEPT_FACE",FACE,{"disambiguationData":[OSD([subQ2])]})]),OD(1.0)],"derivedFrom":makeQuery(id+"F1.opExtrude","CAP_EDGE",EDGE,{"disambiguationData":[OSD([subQ0])],"isStart":false})});}
            var Q20;
            {var subQ0=sQuery(id+"F0.wireOp",EDGE,"E0.top");var subQ1=sQuery(id+"F0.wireOp",EDGE,"E0.bottom");var subQ2=sQuery(id+"F5.wireOp",EDGE,"E30");Q20=makeQuery(id+"F6.boolean.opBoolean","SPLIT",EDGE,{"disambiguationData":[TD([makeQuery(id+"F1.opExtrude","CAP_FACE",FACE,{"disambiguationData":[OSD([subQ1,subQ0,sQuery(id+"F0.wireOp",EDGE,"E0.left"),sQuery(id+"F0.wireOp",EDGE,"E0.right")])],"isStart":false}),makeQuery(id+"F1.opExtrude","SWEPT_FACE",FACE,{"disambiguationData":[OSD([subQ0])]}),makeQuery(id+"F6.opExtrude","SWEPT_FACE",FACE,{"disambiguationData":[OSD([subQ2])]}),makeQuery(id+"F6.opExtrude","CAP_FACE",FACE,{"disambiguationData":[OSD([subQ1,sQuery(id+"F2.wireOp",EDGE,"E2.sketch_text.stroke-0"),sQuery(id+"F2.wireOp",EDGE,"E2.sketch_text.stroke-1"),sQuery(id+"F2.wireOp",EDGE,"E2.sketch_text.stroke-2"),sQuery(id+"F2.wireOp",EDGE,"E2.sketch_text.stroke-3"),sQuery(id+"F2.wireOp",EDGE,"E2.sketch_text.stroke-4"),sQuery(id+"F2.wireOp",EDGE,"E2.sketch_text.stroke-5"),sQuery(id+"F2.wireOp",EDGE,"E2.sketch_text.stroke-6"),sQuery(id+"F2.wireOp",EDGE,"E2.sketch_text.stroke-7"),sQuery(id+"F2.wireOp",EDGE,"E2.sketch_text.stroke-8"),sQuery(id+"F2.wireOp",EDGE,"E2.sketch_text.stroke-9"),sQuery(id+"F2.wireOp",EDGE,"E2.sketch_text.stroke-10"),sQuery(id+"F2.wireOp",EDGE,"E2.sketch_text.stroke-11"),sQuery(id+"F2.wireOp",EDGE,"E2.sketch_text.stroke-12"),sQuery(id+"F2.wireOp",EDGE,"E2.sketch_text.stroke-13"),sQuery(id+"F2.wireOp",EDGE,"E2.sketch_text.stroke-14"),sQuery(id+"F2.wireOp",EDGE,"E2.sketch_text.stroke-15"),sQuery(id+"F2.wireOp",EDGE,"E2.sketch_text.stroke-16"),sQuery(id+"F2.wireOp",EDGE,"E2.sketch_text.stroke-17"),sQuery(id+"F2.wireOp",EDGE,"E2.sketch_text.stroke-18"),sQuery(id+"F2.wireOp",EDGE,"E2.sketch_text.stroke-19"),sQuery(id+"F2.wireOp",EDGE,"E2.sketch_text.stroke-20"),sQuery(id+"F2.wireOp",EDGE,"E2.sketch_text.stroke-21"),sQuery(id+"F2.wireOp",EDGE,"E2.sketch_text.stroke-22"),sQuery(id+"F2.wireOp",EDGE,"E2.sketch_text.stroke-23"),sQuery(id+"F2.wireOp",EDGE,"E2.sketch_text.stroke-24"),sQuery(id+"F2.wireOp",EDGE,"E2.sketch_text.stroke-25"),sQuery(id+"F2.wireOp",EDGE,"E2.sketch_text.stroke-26"),sQuery(id+"F2.wireOp",EDGE,"E2.sketch_text.stroke-27"),sQuery(id+"F2.wireOp",EDGE,"E2.sketch_text.stroke-28"),sQuery(id+"F2.wireOp",EDGE,"E2.sketch_text.stroke-29"),sQuery(id+"F2.wireOp",EDGE,"E2.sketch_text.stroke-30"),sQuery(id+"F2.wireOp",EDGE,"E2.sketch_text.stroke-31"),sQuery(id+"F2.wireOp",EDGE,"E2.sketch_text.stroke-32"),sQuery(id+"F2.wireOp",EDGE,"E2.sketch_text.stroke-33"),sQuery(id+"F2.wireOp",EDGE,"E2.sketch_text.stroke-34"),sQuery(id+"F2.wireOp",EDGE,"E2.sketch_text.stroke-35"),sQuery(id+"F2.wireOp",EDGE,"E2.sketch_text.stroke-36"),sQuery(id+"F2.wireOp",EDGE,"E2.sketch_text.stroke-37"),sQuery(id+"F2.wireOp",EDGE,"E2.sketch_text.stroke-38"),sQuery(id+"F2.wireOp",EDGE,"E2.sketch_text.stroke-39"),sQuery(id+"F2.wireOp",EDGE,"E2.sketch_text.stroke-40"),sQuery(id+"F2.wireOp",EDGE,"E2.sketch_text.stroke-41"),sQuery(id+"F2.wireOp",EDGE,"E2.sketch_text.stroke-42"),sQuery(id+"F2.wireOp",EDGE,"E2.sketch_text.stroke-43"),sQuery(id+"F2.wireOp",EDGE,"E2.sketch_text.stroke-44"),sQuery(id+"F2.wireOp",EDGE,"E2.sketch_text.stroke-45"),sQuery(id+"F2.wireOp",EDGE,"E2.sketch_text.stroke-46"),sQuery(id+"F2.wireOp",EDGE,"E2.sketch_text.stroke-47"),sQuery(id+"F2.wireOp",EDGE,"E2.sketch_text.stroke-48"),sQuery(id+"F2.wireOp",EDGE,"E2.sketch_text.stroke-49"),sQuery(id+"F2.wireOp",EDGE,"E2.sketch_text.stroke-50"),sQuery(id+"F2.wireOp",EDGE,"E2.sketch_text.stroke-51"),sQuery(id+"F2.wireOp",EDGE,"E2.sketch_text.stroke-52"),sQuery(id+"F2.wireOp",EDGE,"E2.sketch_text.stroke-53"),sQuery(id+"F2.wireOp",EDGE,"E2.sketch_text.stroke-54"),sQuery(id+"F2.wireOp",EDGE,"E2.sketch_text.stroke-55"),sQuery(id+"F2.wireOp",EDGE,"E2.sketch_text.stroke-56"),sQuery(id+"F2.wireOp",EDGE,"E2.sketch_text.stroke-57"),sQuery(id+"F2.wireOp",EDGE,"E2.sketch_text.stroke-58"),sQuery(id+"F2.wireOp",EDGE,"E2.sketch_text.stroke-59"),sQuery(id+"F2.wireOp",EDGE,"E2.sketch_text.stroke-60"),sQuery(id+"F2.wireOp",EDGE,"E2.sketch_text.stroke-61"),sQuery(id+"F2.wireOp",EDGE,"E2.sketch_text.stroke-62"),sQuery(id+"F2.wireOp",EDGE,"E2.sketch_text.stroke-63"),sQuery(id+"F2.wireOp",EDGE,"E2.sketch_text.stroke-64"),sQuery(id+"F2.wireOp",EDGE,"E2.sketch_text.stroke-65"),sQuery(id+"F2.wireOp",EDGE,"E2.sketch_text.stroke-66"),sQuery(id+"F2.wireOp",EDGE,"E2.sketch_text.stroke-67"),sQuery(id+"F2.wireOp",EDGE,"E2.sketch_text.stroke-68"),sQuery(id+"F2.wireOp",EDGE,"E2.sketch_text.stroke-69"),sQuery(id+"F2.wireOp",EDGE,"E2.sketch_text.stroke-70"),sQuery(id+"F2.wireOp",EDGE,"E2.sketch_text.stroke-71"),sQuery(id+"F2.wireOp",EDGE,"E2.sketch_text.stroke-72"),sQuery(id+"F2.wireOp",EDGE,"E2.sketch_text.stroke-73"),sQuery(id+"F2.wireOp",EDGE,"E2.sketch_text.stroke-74"),sQuery(id+"F2.wireOp",EDGE,"E2.sketch_text.stroke-75"),sQuery(id+"F2.wireOp",EDGE,"E2.sketch_text.stroke-76"),sQuery(id+"F2.wireOp",EDGE,"E2.sketch_text.stroke-77"),sQuery(id+"F2.wireOp",EDGE,"E2.sketch_text.stroke-78"),sQuery(id+"F2.wireOp",EDGE,"E2.sketch_text.stroke-79"),sQuery(id+"F2.wireOp",EDGE,"E2.sketch_text.stroke-80"),sQuery(id+"F2.wireOp",EDGE,"E2.sketch_text.stroke-81"),sQuery(id+"F2.wireOp",EDGE,"E2.sketch_text.stroke-82"),sQuery(id+"F2.wireOp",EDGE,"E2.sketch_text.stroke-83"),sQuery(id+"F2.wireOp",EDGE,"E2.sketch_text.stroke-84"),sQuery(id+"F2.wireOp",EDGE,"E2.sketch_text.stroke-85"),sQuery(id+"F2.wireOp",EDGE,"E2.sketch_text.stroke-86"),sQuery(id+"F2.wireOp",EDGE,"E2.sketch_text.stroke-87"),sQuery(id+"F2.wireOp",EDGE,"E2.sketch_text.stroke-88"),sQuery(id+"F2.wireOp",EDGE,"E2.sketch_text.stroke-89"),sQuery(id+"F2.wireOp",EDGE,"E2.sketch_text.stroke-90"),sQuery(id+"F2.wireOp",EDGE,"E2.sketch_text.stroke-91"),sQuery(id+"F2.wireOp",EDGE,"E2.sketch_text.stroke-92"),sQuery(id+"F2.wireOp",EDGE,"E2.sketch_text.stroke-93"),sQuery(id+"F2.wireOp",EDGE,"E2.sketch_text.stroke-94"),sQuery(id+"F2.wireOp",EDGE,"E2.sketch_text.stroke-95"),sQuery(id+"F2.wireOp",EDGE,"E2.sketch_text.stroke-96"),sQuery(id+"F2.wireOp",EDGE,"E2.sketch_text.stroke-97"),sQuery(id+"F2.wireOp",EDGE,"E2.sketch_text.stroke-98"),sQuery(id+"F2.wireOp",EDGE,"E2.sketch_text.stroke-99"),sQuery(id+"F2.wireOp",EDGE,"E2.sketch_text.stroke-100"),sQuery(id+"F2.wireOp",EDGE,"E2.sketch_text.stroke-101"),sQuery(id+"F2.wireOp",EDGE,"E2.sketch_text.stroke-102"),sQuery(id+"F2.wireOp",EDGE,"E2.sketch_text.stroke-103"),sQuery(id+"F2.wireOp",EDGE,"E2.sketch_text.stroke-104"),sQuery(id+"F2.wireOp",EDGE,"E2.sketch_text.stroke-105"),sQuery(id+"F2.wireOp",EDGE,"E2.sketch_text.stroke-106"),sQuery(id+"F2.wireOp",EDGE,"E2.sketch_text.stroke-107"),sQuery(id+"F2.wireOp",EDGE,"E2.sketch_text.stroke-108"),sQuery(id+"F2.wireOp",EDGE,"E2.sketch_text.stroke-109"),sQuery(id+"F2.wireOp",EDGE,"E2.sketch_text.stroke-110"),sQuery(id+"F2.wireOp",EDGE,"E2.sketch_text.stroke-111"),sQuery(id+"F2.wireOp",EDGE,"E2.sketch_text.stroke-112"),sQuery(id+"F2.wireOp",EDGE,"E2.sketch_text.stroke-113"),sQuery(id+"F2.wireOp",EDGE,"E2.sketch_text.stroke-114"),sQuery(id+"F2.wireOp",EDGE,"E2.sketch_text.stroke-115"),sQuery(id+"F2.wireOp",EDGE,"E2.sketch_text.stroke-116"),sQuery(id+"F2.wireOp",EDGE,"E2.sketch_text.stroke-117"),sQuery(id+"F2.wireOp",EDGE,"E2.sketch_text.stroke-118"),sQuery(id+"F2.wireOp",EDGE,"E2.sketch_text.stroke-119"),sQuery(id+"F2.wireOp",EDGE,"E2.sketch_text.stroke-120"),sQuery(id+"F2.wireOp",EDGE,"E2.sketch_text.stroke-121"),sQuery(id+"F2.wireOp",EDGE,"E2.sketch_text.stroke-122"),sQuery(id+"F2.wireOp",EDGE,"E2.sketch_text.stroke-123"),sQuery(id+"F2.wireOp",EDGE,"E2.sketch_text.stroke-124"),sQuery(id+"F2.wireOp",EDGE,"E2.sketch_text.stroke-125"),sQuery(id+"F2.wireOp",EDGE,"E2.sketch_text.stroke-126"),sQuery(id+"F2.wireOp",EDGE,"E2.sketch_text.stroke-127"),sQuery(id+"F2.wireOp",EDGE,"E2.sketch_text.stroke-128"),sQuery(id+"F2.wireOp",EDGE,"E2.sketch_text.stroke-129"),sQuery(id+"F2.wireOp",EDGE,"E2.sketch_text.stroke-130"),sQuery(id+"F2.wireOp",EDGE,"E2.sketch_text.stroke-131"),sQuery(id+"F2.wireOp",EDGE,"E2.sketch_text.stroke-132"),sQuery(id+"F2.wireOp",EDGE,"E2.sketch_text.stroke-133"),sQuery(id+"F2.wireOp",EDGE,"E2.sketch_text.stroke-134"),sQuery(id+"F2.wireOp",EDGE,"E2.sketch_text.stroke-135"),sQuery(id+"F2.wireOp",EDGE,"E2.sketch_text.stroke-136"),sQuery(id+"F2.wireOp",EDGE,"E2.sketch_text.stroke-137"),sQuery(id+"F2.wireOp",EDGE,"E2.sketch_text.stroke-138"),sQuery(id+"F2.wireOp",EDGE,"E2.sketch_text.stroke-139"),sQuery(id+"F2.wireOp",EDGE,"E2.sketch_text.stroke-140"),sQuery(id+"F2.wireOp",EDGE,"E2.sketch_text.stroke-141"),sQuery(id+"F2.wireOp",EDGE,"E2.sketch_text.stroke-142"),sQuery(id+"F2.wireOp",EDGE,"E2.sketch_text.stroke-143"),sQuery(id+"F2.wireOp",EDGE,"E2.sketch_text.stroke-144"),sQuery(id+"F2.wireOp",EDGE,"E2.sketch_text.stroke-145"),sQuery(id+"F2.wireOp",EDGE,"E2.sketch_text.stroke-146"),sQuery(id+"F2.wireOp",EDGE,"E2.sketch_text.stroke-147"),sQuery(id+"F2.wireOp",EDGE,"E2.sketch_text.stroke-148"),sQuery(id+"F2.wireOp",EDGE,"E2.sketch_text.stroke-149"),sQuery(id+"F2.wireOp",EDGE,"E2.sketch_text.stroke-150"),sQuery(id+"F2.wireOp",EDGE,"E2.sketch_text.stroke-151"),sQuery(id+"F2.wireOp",EDGE,"E2.sketch_text.stroke-152"),sQuery(id+"F2.wireOp",EDGE,"E2.sketch_text.stroke-153"),sQuery(id+"F2.wireOp",EDGE,"E2.sketch_text.stroke-154"),sQuery(id+"F2.wireOp",EDGE,"E2.sketch_text.stroke-155"),sQuery(id+"F2.wireOp",EDGE,"E2.sketch_text.stroke-156"),sQuery(id+"F2.wireOp",EDGE,"E2.sketch_text.stroke-157"),sQuery(id+"F2.wireOp",EDGE,"E2.sketch_text.stroke-158"),sQuery(id+"F2.wireOp",EDGE,"E2.sketch_text.stroke-159"),sQuery(id+"F2.wireOp",EDGE,"E2.sketch_text.stroke-160"),sQuery(id+"F2.wireOp",EDGE,"E2.sketch_text.stroke-161"),sQuery(id+"F2.wireOp",EDGE,"E2.sketch_text.stroke-162"),sQuery(id+"F2.wireOp",EDGE,"E2.sketch_text.stroke-163"),sQuery(id+"F2.wireOp",EDGE,"E2.sketch_text.stroke-164"),sQuery(id+"F2.wireOp",EDGE,"E2.sketch_text.stroke-165"),sQuery(id+"F2.wireOp",EDGE,"E2.sketch_text.stroke-166"),sQuery(id+"F2.wireOp",EDGE,"E2.sketch_text.stroke-167"),sQuery(id+"F2.wireOp",EDGE,"E2.sketch_text.stroke-168"),sQuery(id+"F2.wireOp",EDGE,"E2.sketch_text.stroke-169"),sQuery(id+"F2.wireOp",EDGE,"E2.sketch_text.stroke-170"),sQuery(id+"F2.wireOp",EDGE,"E2.sketch_text.stroke-171"),sQuery(id+"F2.wireOp",EDGE,"E2.sketch_text.stroke-172"),sQuery(id+"F2.wireOp",EDGE,"E2.sketch_text.stroke-173"),sQuery(id+"F3.wireOp",EDGE,"E4.sketch_text.stroke-0"),sQuery(id+"F3.wireOp",EDGE,"E4.sketch_text.stroke-1"),sQuery(id+"F3.wireOp",EDGE,"E4.sketch_text.stroke-2"),sQuery(id+"F3.wireOp",EDGE,"E4.sketch_text.stroke-3"),sQuery(id+"F3.wireOp",EDGE,"E4.sketch_text.stroke-4"),sQuery(id+"F3.wireOp",EDGE,"E4.sketch_text.stroke-5"),sQuery(id+"F3.wireOp",EDGE,"E4.sketch_text.stroke-6"),sQuery(id+"F3.wireOp",EDGE,"E4.sketch_text.stroke-7"),sQuery(id+"F3.wireOp",EDGE,"E4.sketch_text.stroke-8"),sQuery(id+"F3.wireOp",EDGE,"E4.sketch_text.stroke-9"),sQuery(id+"F3.wireOp",EDGE,"E4.sketch_text.stroke-10"),sQuery(id+"F3.wireOp",EDGE,"E4.sketch_text.stroke-11"),sQuery(id+"F3.wireOp",EDGE,"E4.sketch_text.stroke-12"),sQuery(id+"F3.wireOp",EDGE,"E4.sketch_text.stroke-13"),sQuery(id+"F3.wireOp",EDGE,"E4.sketch_text.stroke-14"),sQuery(id+"F3.wireOp",EDGE,"E4.sketch_text.stroke-15"),sQuery(id+"F3.wireOp",EDGE,"E4.sketch_text.stroke-16"),sQuery(id+"F3.wireOp",EDGE,"E4.sketch_text.stroke-17"),sQuery(id+"F3.wireOp",EDGE,"E4.sketch_text.stroke-18"),sQuery(id+"F3.wireOp",EDGE,"E4.sketch_text.stroke-19"),sQuery(id+"F3.wireOp",EDGE,"E4.sketch_text.stroke-20"),sQuery(id+"F3.wireOp",EDGE,"E4.sketch_text.stroke-21"),sQuery(id+"F3.wireOp",EDGE,"E4.sketch_text.stroke-22"),sQuery(id+"F3.wireOp",EDGE,"E4.sketch_text.stroke-23"),sQuery(id+"F3.wireOp",EDGE,"E4.sketch_text.stroke-24"),sQuery(id+"F3.wireOp",EDGE,"E4.sketch_text.stroke-25"),sQuery(id+"F3.wireOp",EDGE,"E4.sketch_text.stroke-26"),sQuery(id+"F3.wireOp",EDGE,"E4.sketch_text.stroke-27"),sQuery(id+"F3.wireOp",EDGE,"E4.sketch_text.stroke-28"),sQuery(id+"F3.wireOp",EDGE,"E4.sketch_text.stroke-29"),sQuery(id+"F3.wireOp",EDGE,"E4.sketch_text.stroke-30"),sQuery(id+"F3.wireOp",EDGE,"E4.sketch_text.stroke-31"),sQuery(id+"F3.wireOp",EDGE,"E4.sketch_text.stroke-32"),sQuery(id+"F3.wireOp",EDGE,"E4.sketch_text.stroke-33"),sQuery(id+"F3.wireOp",EDGE,"E4.sketch_text.stroke-34"),sQuery(id+"F3.wireOp",EDGE,"E4.sketch_text.stroke-35"),sQuery(id+"F3.wireOp",EDGE,"E4.sketch_text.stroke-36"),sQuery(id+"F3.wireOp",EDGE,"E4.sketch_text.stroke-37"),sQuery(id+"F3.wireOp",EDGE,"E4.sketch_text.stroke-38"),sQuery(id+"F3.wireOp",EDGE,"E4.sketch_text.stroke-39"),sQuery(id+"F3.wireOp",EDGE,"E4.sketch_text.stroke-40"),sQuery(id+"F3.wireOp",EDGE,"E4.sketch_text.stroke-41"),sQuery(id+"F3.wireOp",EDGE,"E4.sketch_text.stroke-42"),sQuery(id+"F3.wireOp",EDGE,"E4.sketch_text.stroke-43"),sQuery(id+"F3.wireOp",EDGE,"E4.sketch_text.stroke-44"),sQuery(id+"F3.wireOp",EDGE,"E4.sketch_text.stroke-45"),sQuery(id+"F3.wireOp",EDGE,"E4.sketch_text.stroke-46"),sQuery(id+"F3.wireOp",EDGE,"E4.sketch_text.stroke-47"),sQuery(id+"F3.wireOp",EDGE,"E4.sketch_text.stroke-48"),sQuery(id+"F3.wireOp",EDGE,"E4.sketch_text.stroke-49"),sQuery(id+"F3.wireOp",EDGE,"E4.sketch_text.stroke-50"),sQuery(id+"F3.wireOp",EDGE,"E4.sketch_text.stroke-51"),sQuery(id+"F3.wireOp",EDGE,"E4.sketch_text.stroke-52"),sQuery(id+"F3.wireOp",EDGE,"E4.sketch_text.stroke-53"),sQuery(id+"F3.wireOp",EDGE,"E4.sketch_text.stroke-54"),sQuery(id+"F3.wireOp",EDGE,"E4.sketch_text.stroke-55"),sQuery(id+"F3.wireOp",EDGE,"E4.sketch_text.stroke-56"),sQuery(id+"F3.wireOp",EDGE,"E4.sketch_text.stroke-57"),sQuery(id+"F3.wireOp",EDGE,"E4.sketch_text.stroke-58"),sQuery(id+"F3.wireOp",EDGE,"E4.sketch_text.stroke-59"),sQuery(id+"F3.wireOp",EDGE,"E4.sketch_text.stroke-60"),sQuery(id+"F3.wireOp",EDGE,"E4.sketch_text.stroke-61"),sQuery(id+"F3.wireOp",EDGE,"E4.sketch_text.stroke-62"),sQuery(id+"F3.wireOp",EDGE,"E4.sketch_text.stroke-71"),sQuery(id+"F3.wireOp",EDGE,"E4.sketch_text.stroke-72"),sQuery(id+"F3.wireOp",EDGE,"E4.sketch_text.stroke-73"),sQuery(id+"F3.wireOp",EDGE,"E4.sketch_text.stroke-74"),sQuery(id+"F3.wireOp",EDGE,"E4.sketch_text.stroke-75"),sQuery(id+"F3.wireOp",EDGE,"E4.sketch_text.stroke-76"),sQuery(id+"F3.wireOp",EDGE,"E4.sketch_text.stroke-77"),sQuery(id+"F3.wireOp",EDGE,"E4.sketch_text.stroke-78"),sQuery(id+"F3.wireOp",EDGE,"E4.sketch_text.stroke-79"),sQuery(id+"F3.wireOp",EDGE,"E4.sketch_text.stroke-80"),sQuery(id+"F3.wireOp",EDGE,"E4.sketch_text.stroke-81"),sQuery(id+"F3.wireOp",EDGE,"E4.sketch_text.stroke-82"),sQuery(id+"F3.wireOp",EDGE,"E4.sketch_text.stroke-83"),sQuery(id+"F3.wireOp",EDGE,"E4.sketch_text.stroke-84"),sQuery(id+"F3.wireOp",EDGE,"E4.sketch_text.stroke-85"),sQuery(id+"F3.wireOp",EDGE,"E4.sketch_text.stroke-86"),sQuery(id+"F3.wireOp",EDGE,"E4.sketch_text.stroke-87"),sQuery(id+"F3.wireOp",EDGE,"E4.sketch_text.stroke-88"),sQuery(id+"F3.wireOp",EDGE,"E4.sketch_text.stroke-89"),sQuery(id+"F3.wireOp",EDGE,"E4.sketch_text.stroke-90"),sQuery(id+"F3.wireOp",EDGE,"E4.sketch_text.stroke-91"),sQuery(id+"F3.wireOp",EDGE,"E4.sketch_text.stroke-92"),sQuery(id+"F3.wireOp",EDGE,"E4.sketch_text.stroke-93"),sQuery(id+"F3.wireOp",EDGE,"E4.sketch_text.stroke-94"),sQuery(id+"F3.wireOp",EDGE,"E4.sketch_text.stroke-95"),sQuery(id+"F3.wireOp",EDGE,"E4.sketch_text.stroke-96"),sQuery(id+"F3.wireOp",EDGE,"E4.sketch_text.stroke-97"),sQuery(id+"F3.wireOp",EDGE,"E4.sketch_text.stroke-103"),sQuery(id+"F3.wireOp",EDGE,"E4.sketch_text.stroke-104"),sQuery(id+"F3.wireOp",EDGE,"E4.sketch_text.stroke-105"),sQuery(id+"F3.wireOp",EDGE,"E4.sketch_text.stroke-106"),sQuery(id+"F3.wireOp",EDGE,"E4.sketch_text.stroke-107"),sQuery(id+"F3.wireOp",EDGE,"E4.sketch_text.stroke-108"),sQuery(id+"F3.wireOp",EDGE,"E4.sketch_text.stroke-109"),sQuery(id+"F3.wireOp",EDGE,"E4.sketch_text.stroke-110"),sQuery(id+"F3.wireOp",EDGE,"E4.sketch_text.stroke-111"),sQuery(id+"F3.wireOp",EDGE,"E4.sketch_text.stroke-112"),sQuery(id+"F3.wireOp",EDGE,"E4.sketch_text.stroke-113"),sQuery(id+"F3.wireOp",EDGE,"E4.sketch_text.stroke-114"),sQuery(id+"F3.wireOp",EDGE,"E4.sketch_text.stroke-115"),sQuery(id+"F3.wireOp",EDGE,"E4.sketch_text.stroke-116"),sQuery(id+"F3.wireOp",EDGE,"E4.sketch_text.stroke-117"),sQuery(id+"F3.wireOp",EDGE,"E4.sketch_text.stroke-118"),sQuery(id+"F3.wireOp",EDGE,"E4.sketch_text.stroke-119"),sQuery(id+"F3.wireOp",EDGE,"E4.sketch_text.stroke-120"),sQuery(id+"F3.wireOp",EDGE,"E4.sketch_text.stroke-121"),sQuery(id+"F3.wireOp",EDGE,"E4.sketch_text.stroke-122"),sQuery(id+"F3.wireOp",EDGE,"E4.sketch_text.stroke-123"),sQuery(id+"F3.wireOp",EDGE,"E4.sketch_text.stroke-124"),sQuery(id+"F3.wireOp",EDGE,"E4.sketch_text.stroke-125"),sQuery(id+"F3.wireOp",EDGE,"E4.sketch_text.stroke-126"),sQuery(id+"F3.wireOp",EDGE,"E4.sketch_text.stroke-127"),sQuery(id+"F3.wireOp",EDGE,"E4.sketch_text.stroke-128"),sQuery(id+"F3.wireOp",EDGE,"E4.sketch_text.stroke-129"),sQuery(id+"F3.wireOp",EDGE,"E4.sketch_text.stroke-130"),sQuery(id+"F3.wireOp",EDGE,"E4.sketch_text.stroke-131"),sQuery(id+"F3.wireOp",EDGE,"E4.sketch_text.stroke-132"),sQuery(id+"F3.wireOp",EDGE,"E4.sketch_text.stroke-133"),sQuery(id+"F3.wireOp",EDGE,"E4.sketch_text.stroke-134"),sQuery(id+"F3.wireOp",EDGE,"E4.sketch_text.stroke-135"),sQuery(id+"F3.wireOp",EDGE,"E4.sketch_text.stroke-136"),sQuery(id+"F3.wireOp",EDGE,"E4.sketch_text.stroke-137"),sQuery(id+"F3.wireOp",EDGE,"E4.sketch_text.stroke-138"),sQuery(id+"F3.wireOp",EDGE,"E4.sketch_text.stroke-139"),sQuery(id+"F3.wireOp",EDGE,"E4.sketch_text.stroke-140"),sQuery(id+"F3.wireOp",EDGE,"E4.sketch_text.stroke-141"),sQuery(id+"F3.wireOp",EDGE,"E4.sketch_text.stroke-142"),sQuery(id+"F3.wireOp",EDGE,"E4.sketch_text.stroke-143"),sQuery(id+"F3.wireOp",EDGE,"E4.sketch_text.stroke-144"),sQuery(id+"F3.wireOp",EDGE,"E4.sketch_text.stroke-145"),sQuery(id+"F3.wireOp",EDGE,"E4.sketch_text.stroke-146"),sQuery(id+"F3.wireOp",EDGE,"E4.sketch_text.stroke-147"),sQuery(id+"F3.wireOp",EDGE,"E4.sketch_text.stroke-148"),sQuery(id+"F3.wireOp",EDGE,"E4.sketch_text.stroke-149"),sQuery(id+"F3.wireOp",EDGE,"E4.sketch_text.stroke-150"),sQuery(id+"F3.wireOp",EDGE,"E4.sketch_text.stroke-151"),sQuery(id+"F3.wireOp",EDGE,"E4.sketch_text.stroke-152"),sQuery(id+"F3.wireOp",EDGE,"E4.sketch_text.stroke-153"),sQuery(id+"F3.wireOp",EDGE,"E4.sketch_text.stroke-159"),sQuery(id+"F3.wireOp",EDGE,"E4.sketch_text.stroke-160"),sQuery(id+"F3.wireOp",EDGE,"E4.sketch_text.stroke-161"),sQuery(id+"F3.wireOp",EDGE,"E4.sketch_text.stroke-162"),sQuery(id+"F3.wireOp",EDGE,"E4.sketch_text.stroke-163"),sQuery(id+"F3.wireOp",EDGE,"E4.sketch_text.stroke-164"),sQuery(id+"F3.wireOp",EDGE,"E4.sketch_text.stroke-165"),sQuery(id+"F3.wireOp",EDGE,"E4.sketch_text.stroke-166"),sQuery(id+"F3.wireOp",EDGE,"E4.sketch_text.stroke-167"),sQuery(id+"F3.wireOp",EDGE,"E4.sketch_text.stroke-168"),sQuery(id+"F3.wireOp",EDGE,"E4.sketch_text.stroke-169"),sQuery(id+"F3.wireOp",EDGE,"E4.sketch_text.stroke-170"),sQuery(id+"F3.wireOp",EDGE,"E4.sketch_text.stroke-171"),sQuery(id+"F3.wireOp",EDGE,"E4.sketch_text.stroke-172"),sQuery(id+"F3.wireOp",EDGE,"E4.sketch_text.stroke-173"),sQuery(id+"F3.wireOp",EDGE,"E4.sketch_text.stroke-174"),sQuery(id+"F3.wireOp",EDGE,"E4.sketch_text.stroke-175"),sQuery(id+"F3.wireOp",EDGE,"E4.sketch_text.stroke-176"),sQuery(id+"F3.wireOp",EDGE,"E4.sketch_text.stroke-177"),sQuery(id+"F3.wireOp",EDGE,"E4.sketch_text.stroke-178"),sQuery(id+"F3.wireOp",EDGE,"E4.sketch_text.stroke-179"),sQuery(id+"F3.wireOp",EDGE,"E4.sketch_text.stroke-180"),subQ2,sQuery(id+"F5.wireOp",EDGE,"E31")])],"isStart":true})])],"derivedFrom":makeQuery(id+"F6.opExtrude","CAP_EDGE",EDGE,{"disambiguationData":[OSD([subQ2])],"isStart":true})});}
            var Q21;
            {var subQ0=sQuery(id+"F5.wireOp",EDGE,"E30");var subQ1=sQuery(id+"F0.wireOp",EDGE,"E0.top");var subQ2=sQuery(id+"F5.wireOp",EDGE,"E31");var subQ3=sQuery(id+"F0.wireOp",EDGE,"E0.bottom");Q21=makeQuery(id+"F6.boolean.opBoolean","SPLIT",EDGE,{"disambiguationData":[TD([makeQuery(id+"F1.opExtrude","CAP_FACE",FACE,{"disambiguationData":[OSD([subQ3,subQ1,sQuery(id+"F0.wireOp",EDGE,"E0.left"),sQuery(id+"F0.wireOp",EDGE,"E0.right")])],"isStart":false}),makeQuery(id+"F1.opExtrude","SWEPT_FACE",FACE,{"disambiguationData":[OSD([subQ1])]}),makeQuery(id+"F6.opExtrude","SWEPT_FACE",FACE,{"disambiguationData":[OSD([subQ0])]}),makeQuery(id+"F6.opExtrude","CAP_FACE",FACE,{"disambiguationData":[OSD([subQ3,sQuery(id+"F2.wireOp",EDGE,"E2.sketch_text.stroke-0"),sQuery(id+"F2.wireOp",EDGE,"E2.sketch_text.stroke-1"),sQuery(id+"F2.wireOp",EDGE,"E2.sketch_text.stroke-2"),sQuery(id+"F2.wireOp",EDGE,"E2.sketch_text.stroke-3"),sQuery(id+"F2.wireOp",EDGE,"E2.sketch_text.stroke-4"),sQuery(id+"F2.wireOp",EDGE,"E2.sketch_text.stroke-5"),sQuery(id+"F2.wireOp",EDGE,"E2.sketch_text.stroke-6"),sQuery(id+"F2.wireOp",EDGE,"E2.sketch_text.stroke-7"),sQuery(id+"F2.wireOp",EDGE,"E2.sketch_text.stroke-8"),sQuery(id+"F2.wireOp",EDGE,"E2.sketch_text.stroke-9"),sQuery(id+"F2.wireOp",EDGE,"E2.sketch_text.stroke-10"),sQuery(id+"F2.wireOp",EDGE,"E2.sketch_text.stroke-11"),sQuery(id+"F2.wireOp",EDGE,"E2.sketch_text.stroke-12"),sQuery(id+"F2.wireOp",EDGE,"E2.sketch_text.stroke-13"),sQuery(id+"F2.wireOp",EDGE,"E2.sketch_text.stroke-14"),sQuery(id+"F2.wireOp",EDGE,"E2.sketch_text.stroke-15"),sQuery(id+"F2.wireOp",EDGE,"E2.sketch_text.stroke-16"),sQuery(id+"F2.wireOp",EDGE,"E2.sketch_text.stroke-17"),sQuery(id+"F2.wireOp",EDGE,"E2.sketch_text.stroke-18"),sQuery(id+"F2.wireOp",EDGE,"E2.sketch_text.stroke-19"),sQuery(id+"F2.wireOp",EDGE,"E2.sketch_text.stroke-20"),sQuery(id+"F2.wireOp",EDGE,"E2.sketch_text.stroke-21"),sQuery(id+"F2.wireOp",EDGE,"E2.sketch_text.stroke-22"),sQuery(id+"F2.wireOp",EDGE,"E2.sketch_text.stroke-23"),sQuery(id+"F2.wireOp",EDGE,"E2.sketch_text.stroke-24"),sQuery(id+"F2.wireOp",EDGE,"E2.sketch_text.stroke-25"),sQuery(id+"F2.wireOp",EDGE,"E2.sketch_text.stroke-26"),sQuery(id+"F2.wireOp",EDGE,"E2.sketch_text.stroke-27"),sQuery(id+"F2.wireOp",EDGE,"E2.sketch_text.stroke-28"),sQuery(id+"F2.wireOp",EDGE,"E2.sketch_text.stroke-29"),sQuery(id+"F2.wireOp",EDGE,"E2.sketch_text.stroke-30"),sQuery(id+"F2.wireOp",EDGE,"E2.sketch_text.stroke-31"),sQuery(id+"F2.wireOp",EDGE,"E2.sketch_text.stroke-32"),sQuery(id+"F2.wireOp",EDGE,"E2.sketch_text.stroke-33"),sQuery(id+"F2.wireOp",EDGE,"E2.sketch_text.stroke-34"),sQuery(id+"F2.wireOp",EDGE,"E2.sketch_text.stroke-35"),sQuery(id+"F2.wireOp",EDGE,"E2.sketch_text.stroke-36"),sQuery(id+"F2.wireOp",EDGE,"E2.sketch_text.stroke-37"),sQuery(id+"F2.wireOp",EDGE,"E2.sketch_text.stroke-38"),sQuery(id+"F2.wireOp",EDGE,"E2.sketch_text.stroke-39"),sQuery(id+"F2.wireOp",EDGE,"E2.sketch_text.stroke-40"),sQuery(id+"F2.wireOp",EDGE,"E2.sketch_text.stroke-41"),sQuery(id+"F2.wireOp",EDGE,"E2.sketch_text.stroke-42"),sQuery(id+"F2.wireOp",EDGE,"E2.sketch_text.stroke-43"),sQuery(id+"F2.wireOp",EDGE,"E2.sketch_text.stroke-44"),sQuery(id+"F2.wireOp",EDGE,"E2.sketch_text.stroke-45"),sQuery(id+"F2.wireOp",EDGE,"E2.sketch_text.stroke-46"),sQuery(id+"F2.wireOp",EDGE,"E2.sketch_text.stroke-47"),sQuery(id+"F2.wireOp",EDGE,"E2.sketch_text.stroke-48"),sQuery(id+"F2.wireOp",EDGE,"E2.sketch_text.stroke-49"),sQuery(id+"F2.wireOp",EDGE,"E2.sketch_text.stroke-50"),sQuery(id+"F2.wireOp",EDGE,"E2.sketch_text.stroke-51"),sQuery(id+"F2.wireOp",EDGE,"E2.sketch_text.stroke-52"),sQuery(id+"F2.wireOp",EDGE,"E2.sketch_text.stroke-53"),sQuery(id+"F2.wireOp",EDGE,"E2.sketch_text.stroke-54"),sQuery(id+"F2.wireOp",EDGE,"E2.sketch_text.stroke-55"),sQuery(id+"F2.wireOp",EDGE,"E2.sketch_text.stroke-56"),sQuery(id+"F2.wireOp",EDGE,"E2.sketch_text.stroke-57"),sQuery(id+"F2.wireOp",EDGE,"E2.sketch_text.stroke-58"),sQuery(id+"F2.wireOp",EDGE,"E2.sketch_text.stroke-59"),sQuery(id+"F2.wireOp",EDGE,"E2.sketch_text.stroke-60"),sQuery(id+"F2.wireOp",EDGE,"E2.sketch_text.stroke-61"),sQuery(id+"F2.wireOp",EDGE,"E2.sketch_text.stroke-62"),sQuery(id+"F2.wireOp",EDGE,"E2.sketch_text.stroke-63"),sQuery(id+"F2.wireOp",EDGE,"E2.sketch_text.stroke-64"),sQuery(id+"F2.wireOp",EDGE,"E2.sketch_text.stroke-65"),sQuery(id+"F2.wireOp",EDGE,"E2.sketch_text.stroke-66"),sQuery(id+"F2.wireOp",EDGE,"E2.sketch_text.stroke-67"),sQuery(id+"F2.wireOp",EDGE,"E2.sketch_text.stroke-68"),sQuery(id+"F2.wireOp",EDGE,"E2.sketch_text.stroke-69"),sQuery(id+"F2.wireOp",EDGE,"E2.sketch_text.stroke-70"),sQuery(id+"F2.wireOp",EDGE,"E2.sketch_text.stroke-71"),sQuery(id+"F2.wireOp",EDGE,"E2.sketch_text.stroke-72"),sQuery(id+"F2.wireOp",EDGE,"E2.sketch_text.stroke-73"),sQuery(id+"F2.wireOp",EDGE,"E2.sketch_text.stroke-74"),sQuery(id+"F2.wireOp",EDGE,"E2.sketch_text.stroke-75"),sQuery(id+"F2.wireOp",EDGE,"E2.sketch_text.stroke-76"),sQuery(id+"F2.wireOp",EDGE,"E2.sketch_text.stroke-77"),sQuery(id+"F2.wireOp",EDGE,"E2.sketch_text.stroke-78"),sQuery(id+"F2.wireOp",EDGE,"E2.sketch_text.stroke-79"),sQuery(id+"F2.wireOp",EDGE,"E2.sketch_text.stroke-80"),sQuery(id+"F2.wireOp",EDGE,"E2.sketch_text.stroke-81"),sQuery(id+"F2.wireOp",EDGE,"E2.sketch_text.stroke-82"),sQuery(id+"F2.wireOp",EDGE,"E2.sketch_text.stroke-83"),sQuery(id+"F2.wireOp",EDGE,"E2.sketch_text.stroke-84"),sQuery(id+"F2.wireOp",EDGE,"E2.sketch_text.stroke-85"),sQuery(id+"F2.wireOp",EDGE,"E2.sketch_text.stroke-86"),sQuery(id+"F2.wireOp",EDGE,"E2.sketch_text.stroke-87"),sQuery(id+"F2.wireOp",EDGE,"E2.sketch_text.stroke-88"),sQuery(id+"F2.wireOp",EDGE,"E2.sketch_text.stroke-89"),sQuery(id+"F2.wireOp",EDGE,"E2.sketch_text.stroke-90"),sQuery(id+"F2.wireOp",EDGE,"E2.sketch_text.stroke-91"),sQuery(id+"F2.wireOp",EDGE,"E2.sketch_text.stroke-92"),sQuery(id+"F2.wireOp",EDGE,"E2.sketch_text.stroke-93"),sQuery(id+"F2.wireOp",EDGE,"E2.sketch_text.stroke-94"),sQuery(id+"F2.wireOp",EDGE,"E2.sketch_text.stroke-95"),sQuery(id+"F2.wireOp",EDGE,"E2.sketch_text.stroke-96"),sQuery(id+"F2.wireOp",EDGE,"E2.sketch_text.stroke-97"),sQuery(id+"F2.wireOp",EDGE,"E2.sketch_text.stroke-98"),sQuery(id+"F2.wireOp",EDGE,"E2.sketch_text.stroke-99"),sQuery(id+"F2.wireOp",EDGE,"E2.sketch_text.stroke-100"),sQuery(id+"F2.wireOp",EDGE,"E2.sketch_text.stroke-101"),sQuery(id+"F2.wireOp",EDGE,"E2.sketch_text.stroke-102"),sQuery(id+"F2.wireOp",EDGE,"E2.sketch_text.stroke-103"),sQuery(id+"F2.wireOp",EDGE,"E2.sketch_text.stroke-104"),sQuery(id+"F2.wireOp",EDGE,"E2.sketch_text.stroke-105"),sQuery(id+"F2.wireOp",EDGE,"E2.sketch_text.stroke-106"),sQuery(id+"F2.wireOp",EDGE,"E2.sketch_text.stroke-107"),sQuery(id+"F2.wireOp",EDGE,"E2.sketch_text.stroke-108"),sQuery(id+"F2.wireOp",EDGE,"E2.sketch_text.stroke-109"),sQuery(id+"F2.wireOp",EDGE,"E2.sketch_text.stroke-110"),sQuery(id+"F2.wireOp",EDGE,"E2.sketch_text.stroke-111"),sQuery(id+"F2.wireOp",EDGE,"E2.sketch_text.stroke-112"),sQuery(id+"F2.wireOp",EDGE,"E2.sketch_text.stroke-113"),sQuery(id+"F2.wireOp",EDGE,"E2.sketch_text.stroke-114"),sQuery(id+"F2.wireOp",EDGE,"E2.sketch_text.stroke-115"),sQuery(id+"F2.wireOp",EDGE,"E2.sketch_text.stroke-116"),sQuery(id+"F2.wireOp",EDGE,"E2.sketch_text.stroke-117"),sQuery(id+"F2.wireOp",EDGE,"E2.sketch_text.stroke-118"),sQuery(id+"F2.wireOp",EDGE,"E2.sketch_text.stroke-119"),sQuery(id+"F2.wireOp",EDGE,"E2.sketch_text.stroke-120"),sQuery(id+"F2.wireOp",EDGE,"E2.sketch_text.stroke-121"),sQuery(id+"F2.wireOp",EDGE,"E2.sketch_text.stroke-122"),sQuery(id+"F2.wireOp",EDGE,"E2.sketch_text.stroke-123"),sQuery(id+"F2.wireOp",EDGE,"E2.sketch_text.stroke-124"),sQuery(id+"F2.wireOp",EDGE,"E2.sketch_text.stroke-125"),sQuery(id+"F2.wireOp",EDGE,"E2.sketch_text.stroke-126"),sQuery(id+"F2.wireOp",EDGE,"E2.sketch_text.stroke-127"),sQuery(id+"F2.wireOp",EDGE,"E2.sketch_text.stroke-128"),sQuery(id+"F2.wireOp",EDGE,"E2.sketch_text.stroke-129"),sQuery(id+"F2.wireOp",EDGE,"E2.sketch_text.stroke-130"),sQuery(id+"F2.wireOp",EDGE,"E2.sketch_text.stroke-131"),sQuery(id+"F2.wireOp",EDGE,"E2.sketch_text.stroke-132"),sQuery(id+"F2.wireOp",EDGE,"E2.sketch_text.stroke-133"),sQuery(id+"F2.wireOp",EDGE,"E2.sketch_text.stroke-134"),sQuery(id+"F2.wireOp",EDGE,"E2.sketch_text.stroke-135"),sQuery(id+"F2.wireOp",EDGE,"E2.sketch_text.stroke-136"),sQuery(id+"F2.wireOp",EDGE,"E2.sketch_text.stroke-137"),sQuery(id+"F2.wireOp",EDGE,"E2.sketch_text.stroke-138"),sQuery(id+"F2.wireOp",EDGE,"E2.sketch_text.stroke-139"),sQuery(id+"F2.wireOp",EDGE,"E2.sketch_text.stroke-140"),sQuery(id+"F2.wireOp",EDGE,"E2.sketch_text.stroke-141"),sQuery(id+"F2.wireOp",EDGE,"E2.sketch_text.stroke-142"),sQuery(id+"F2.wireOp",EDGE,"E2.sketch_text.stroke-143"),sQuery(id+"F2.wireOp",EDGE,"E2.sketch_text.stroke-144"),sQuery(id+"F2.wireOp",EDGE,"E2.sketch_text.stroke-145"),sQuery(id+"F2.wireOp",EDGE,"E2.sketch_text.stroke-146"),sQuery(id+"F2.wireOp",EDGE,"E2.sketch_text.stroke-147"),sQuery(id+"F2.wireOp",EDGE,"E2.sketch_text.stroke-148"),sQuery(id+"F2.wireOp",EDGE,"E2.sketch_text.stroke-149"),sQuery(id+"F2.wireOp",EDGE,"E2.sketch_text.stroke-150"),sQuery(id+"F2.wireOp",EDGE,"E2.sketch_text.stroke-151"),sQuery(id+"F2.wireOp",EDGE,"E2.sketch_text.stroke-152"),sQuery(id+"F2.wireOp",EDGE,"E2.sketch_text.stroke-153"),sQuery(id+"F2.wireOp",EDGE,"E2.sketch_text.stroke-154"),sQuery(id+"F2.wireOp",EDGE,"E2.sketch_text.stroke-155"),sQuery(id+"F2.wireOp",EDGE,"E2.sketch_text.stroke-156"),sQuery(id+"F2.wireOp",EDGE,"E2.sketch_text.stroke-157"),sQuery(id+"F2.wireOp",EDGE,"E2.sketch_text.stroke-158"),sQuery(id+"F2.wireOp",EDGE,"E2.sketch_text.stroke-159"),sQuery(id+"F2.wireOp",EDGE,"E2.sketch_text.stroke-160"),sQuery(id+"F2.wireOp",EDGE,"E2.sketch_text.stroke-161"),sQuery(id+"F2.wireOp",EDGE,"E2.sketch_text.stroke-162"),sQuery(id+"F2.wireOp",EDGE,"E2.sketch_text.stroke-163"),sQuery(id+"F2.wireOp",EDGE,"E2.sketch_text.stroke-164"),sQuery(id+"F2.wireOp",EDGE,"E2.sketch_text.stroke-165"),sQuery(id+"F2.wireOp",EDGE,"E2.sketch_text.stroke-166"),sQuery(id+"F2.wireOp",EDGE,"E2.sketch_text.stroke-167"),sQuery(id+"F2.wireOp",EDGE,"E2.sketch_text.stroke-168"),sQuery(id+"F2.wireOp",EDGE,"E2.sketch_text.stroke-169"),sQuery(id+"F2.wireOp",EDGE,"E2.sketch_text.stroke-170"),sQuery(id+"F2.wireOp",EDGE,"E2.sketch_text.stroke-171"),sQuery(id+"F2.wireOp",EDGE,"E2.sketch_text.stroke-172"),sQuery(id+"F2.wireOp",EDGE,"E2.sketch_text.stroke-173"),sQuery(id+"F3.wireOp",EDGE,"E4.sketch_text.stroke-0"),sQuery(id+"F3.wireOp",EDGE,"E4.sketch_text.stroke-1"),sQuery(id+"F3.wireOp",EDGE,"E4.sketch_text.stroke-2"),sQuery(id+"F3.wireOp",EDGE,"E4.sketch_text.stroke-3"),sQuery(id+"F3.wireOp",EDGE,"E4.sketch_text.stroke-4"),sQuery(id+"F3.wireOp",EDGE,"E4.sketch_text.stroke-5"),sQuery(id+"F3.wireOp",EDGE,"E4.sketch_text.stroke-6"),sQuery(id+"F3.wireOp",EDGE,"E4.sketch_text.stroke-7"),sQuery(id+"F3.wireOp",EDGE,"E4.sketch_text.stroke-8"),sQuery(id+"F3.wireOp",EDGE,"E4.sketch_text.stroke-9"),sQuery(id+"F3.wireOp",EDGE,"E4.sketch_text.stroke-10"),sQuery(id+"F3.wireOp",EDGE,"E4.sketch_text.stroke-11"),sQuery(id+"F3.wireOp",EDGE,"E4.sketch_text.stroke-12"),sQuery(id+"F3.wireOp",EDGE,"E4.sketch_text.stroke-13"),sQuery(id+"F3.wireOp",EDGE,"E4.sketch_text.stroke-14"),sQuery(id+"F3.wireOp",EDGE,"E4.sketch_text.stroke-15"),sQuery(id+"F3.wireOp",EDGE,"E4.sketch_text.stroke-16"),sQuery(id+"F3.wireOp",EDGE,"E4.sketch_text.stroke-17"),sQuery(id+"F3.wireOp",EDGE,"E4.sketch_text.stroke-18"),sQuery(id+"F3.wireOp",EDGE,"E4.sketch_text.stroke-19"),sQuery(id+"F3.wireOp",EDGE,"E4.sketch_text.stroke-20"),sQuery(id+"F3.wireOp",EDGE,"E4.sketch_text.stroke-21"),sQuery(id+"F3.wireOp",EDGE,"E4.sketch_text.stroke-22"),sQuery(id+"F3.wireOp",EDGE,"E4.sketch_text.stroke-23"),sQuery(id+"F3.wireOp",EDGE,"E4.sketch_text.stroke-24"),sQuery(id+"F3.wireOp",EDGE,"E4.sketch_text.stroke-25"),sQuery(id+"F3.wireOp",EDGE,"E4.sketch_text.stroke-26"),sQuery(id+"F3.wireOp",EDGE,"E4.sketch_text.stroke-27"),sQuery(id+"F3.wireOp",EDGE,"E4.sketch_text.stroke-28"),sQuery(id+"F3.wireOp",EDGE,"E4.sketch_text.stroke-29"),sQuery(id+"F3.wireOp",EDGE,"E4.sketch_text.stroke-30"),sQuery(id+"F3.wireOp",EDGE,"E4.sketch_text.stroke-31"),sQuery(id+"F3.wireOp",EDGE,"E4.sketch_text.stroke-32"),sQuery(id+"F3.wireOp",EDGE,"E4.sketch_text.stroke-33"),sQuery(id+"F3.wireOp",EDGE,"E4.sketch_text.stroke-34"),sQuery(id+"F3.wireOp",EDGE,"E4.sketch_text.stroke-35"),sQuery(id+"F3.wireOp",EDGE,"E4.sketch_text.stroke-36"),sQuery(id+"F3.wireOp",EDGE,"E4.sketch_text.stroke-37"),sQuery(id+"F3.wireOp",EDGE,"E4.sketch_text.stroke-38"),sQuery(id+"F3.wireOp",EDGE,"E4.sketch_text.stroke-39"),sQuery(id+"F3.wireOp",EDGE,"E4.sketch_text.stroke-40"),sQuery(id+"F3.wireOp",EDGE,"E4.sketch_text.stroke-41"),sQuery(id+"F3.wireOp",EDGE,"E4.sketch_text.stroke-42"),sQuery(id+"F3.wireOp",EDGE,"E4.sketch_text.stroke-43"),sQuery(id+"F3.wireOp",EDGE,"E4.sketch_text.stroke-44"),sQuery(id+"F3.wireOp",EDGE,"E4.sketch_text.stroke-45"),sQuery(id+"F3.wireOp",EDGE,"E4.sketch_text.stroke-46"),sQuery(id+"F3.wireOp",EDGE,"E4.sketch_text.stroke-47"),sQuery(id+"F3.wireOp",EDGE,"E4.sketch_text.stroke-48"),sQuery(id+"F3.wireOp",EDGE,"E4.sketch_text.stroke-49"),sQuery(id+"F3.wireOp",EDGE,"E4.sketch_text.stroke-50"),sQuery(id+"F3.wireOp",EDGE,"E4.sketch_text.stroke-51"),sQuery(id+"F3.wireOp",EDGE,"E4.sketch_text.stroke-52"),sQuery(id+"F3.wireOp",EDGE,"E4.sketch_text.stroke-53"),sQuery(id+"F3.wireOp",EDGE,"E4.sketch_text.stroke-54"),sQuery(id+"F3.wireOp",EDGE,"E4.sketch_text.stroke-55"),sQuery(id+"F3.wireOp",EDGE,"E4.sketch_text.stroke-56"),sQuery(id+"F3.wireOp",EDGE,"E4.sketch_text.stroke-57"),sQuery(id+"F3.wireOp",EDGE,"E4.sketch_text.stroke-58"),sQuery(id+"F3.wireOp",EDGE,"E4.sketch_text.stroke-59"),sQuery(id+"F3.wireOp",EDGE,"E4.sketch_text.stroke-60"),sQuery(id+"F3.wireOp",EDGE,"E4.sketch_text.stroke-61"),sQuery(id+"F3.wireOp",EDGE,"E4.sketch_text.stroke-62"),sQuery(id+"F3.wireOp",EDGE,"E4.sketch_text.stroke-71"),sQuery(id+"F3.wireOp",EDGE,"E4.sketch_text.stroke-72"),sQuery(id+"F3.wireOp",EDGE,"E4.sketch_text.stroke-73"),sQuery(id+"F3.wireOp",EDGE,"E4.sketch_text.stroke-74"),sQuery(id+"F3.wireOp",EDGE,"E4.sketch_text.stroke-75"),sQuery(id+"F3.wireOp",EDGE,"E4.sketch_text.stroke-76"),sQuery(id+"F3.wireOp",EDGE,"E4.sketch_text.stroke-77"),sQuery(id+"F3.wireOp",EDGE,"E4.sketch_text.stroke-78"),sQuery(id+"F3.wireOp",EDGE,"E4.sketch_text.stroke-79"),sQuery(id+"F3.wireOp",EDGE,"E4.sketch_text.stroke-80"),sQuery(id+"F3.wireOp",EDGE,"E4.sketch_text.stroke-81"),sQuery(id+"F3.wireOp",EDGE,"E4.sketch_text.stroke-82"),sQuery(id+"F3.wireOp",EDGE,"E4.sketch_text.stroke-83"),sQuery(id+"F3.wireOp",EDGE,"E4.sketch_text.stroke-84"),sQuery(id+"F3.wireOp",EDGE,"E4.sketch_text.stroke-85"),sQuery(id+"F3.wireOp",EDGE,"E4.sketch_text.stroke-86"),sQuery(id+"F3.wireOp",EDGE,"E4.sketch_text.stroke-87"),sQuery(id+"F3.wireOp",EDGE,"E4.sketch_text.stroke-88"),sQuery(id+"F3.wireOp",EDGE,"E4.sketch_text.stroke-89"),sQuery(id+"F3.wireOp",EDGE,"E4.sketch_text.stroke-90"),sQuery(id+"F3.wireOp",EDGE,"E4.sketch_text.stroke-91"),sQuery(id+"F3.wireOp",EDGE,"E4.sketch_text.stroke-92"),sQuery(id+"F3.wireOp",EDGE,"E4.sketch_text.stroke-93"),sQuery(id+"F3.wireOp",EDGE,"E4.sketch_text.stroke-94"),sQuery(id+"F3.wireOp",EDGE,"E4.sketch_text.stroke-95"),sQuery(id+"F3.wireOp",EDGE,"E4.sketch_text.stroke-96"),sQuery(id+"F3.wireOp",EDGE,"E4.sketch_text.stroke-97"),sQuery(id+"F3.wireOp",EDGE,"E4.sketch_text.stroke-103"),sQuery(id+"F3.wireOp",EDGE,"E4.sketch_text.stroke-104"),sQuery(id+"F3.wireOp",EDGE,"E4.sketch_text.stroke-105"),sQuery(id+"F3.wireOp",EDGE,"E4.sketch_text.stroke-106"),sQuery(id+"F3.wireOp",EDGE,"E4.sketch_text.stroke-107"),sQuery(id+"F3.wireOp",EDGE,"E4.sketch_text.stroke-108"),sQuery(id+"F3.wireOp",EDGE,"E4.sketch_text.stroke-109"),sQuery(id+"F3.wireOp",EDGE,"E4.sketch_text.stroke-110"),sQuery(id+"F3.wireOp",EDGE,"E4.sketch_text.stroke-111"),sQuery(id+"F3.wireOp",EDGE,"E4.sketch_text.stroke-112"),sQuery(id+"F3.wireOp",EDGE,"E4.sketch_text.stroke-113"),sQuery(id+"F3.wireOp",EDGE,"E4.sketch_text.stroke-114"),sQuery(id+"F3.wireOp",EDGE,"E4.sketch_text.stroke-115"),sQuery(id+"F3.wireOp",EDGE,"E4.sketch_text.stroke-116"),sQuery(id+"F3.wireOp",EDGE,"E4.sketch_text.stroke-117"),sQuery(id+"F3.wireOp",EDGE,"E4.sketch_text.stroke-118"),sQuery(id+"F3.wireOp",EDGE,"E4.sketch_text.stroke-119"),sQuery(id+"F3.wireOp",EDGE,"E4.sketch_text.stroke-120"),sQuery(id+"F3.wireOp",EDGE,"E4.sketch_text.stroke-121"),sQuery(id+"F3.wireOp",EDGE,"E4.sketch_text.stroke-122"),sQuery(id+"F3.wireOp",EDGE,"E4.sketch_text.stroke-123"),sQuery(id+"F3.wireOp",EDGE,"E4.sketch_text.stroke-124"),sQuery(id+"F3.wireOp",EDGE,"E4.sketch_text.stroke-125"),sQuery(id+"F3.wireOp",EDGE,"E4.sketch_text.stroke-126"),sQuery(id+"F3.wireOp",EDGE,"E4.sketch_text.stroke-127"),sQuery(id+"F3.wireOp",EDGE,"E4.sketch_text.stroke-128"),sQuery(id+"F3.wireOp",EDGE,"E4.sketch_text.stroke-129"),sQuery(id+"F3.wireOp",EDGE,"E4.sketch_text.stroke-130"),sQuery(id+"F3.wireOp",EDGE,"E4.sketch_text.stroke-131"),sQuery(id+"F3.wireOp",EDGE,"E4.sketch_text.stroke-132"),sQuery(id+"F3.wireOp",EDGE,"E4.sketch_text.stroke-133"),sQuery(id+"F3.wireOp",EDGE,"E4.sketch_text.stroke-134"),sQuery(id+"F3.wireOp",EDGE,"E4.sketch_text.stroke-135"),sQuery(id+"F3.wireOp",EDGE,"E4.sketch_text.stroke-136"),sQuery(id+"F3.wireOp",EDGE,"E4.sketch_text.stroke-137"),sQuery(id+"F3.wireOp",EDGE,"E4.sketch_text.stroke-138"),sQuery(id+"F3.wireOp",EDGE,"E4.sketch_text.stroke-139"),sQuery(id+"F3.wireOp",EDGE,"E4.sketch_text.stroke-140"),sQuery(id+"F3.wireOp",EDGE,"E4.sketch_text.stroke-141"),sQuery(id+"F3.wireOp",EDGE,"E4.sketch_text.stroke-142"),sQuery(id+"F3.wireOp",EDGE,"E4.sketch_text.stroke-143"),sQuery(id+"F3.wireOp",EDGE,"E4.sketch_text.stroke-144"),sQuery(id+"F3.wireOp",EDGE,"E4.sketch_text.stroke-145"),sQuery(id+"F3.wireOp",EDGE,"E4.sketch_text.stroke-146"),sQuery(id+"F3.wireOp",EDGE,"E4.sketch_text.stroke-147"),sQuery(id+"F3.wireOp",EDGE,"E4.sketch_text.stroke-148"),sQuery(id+"F3.wireOp",EDGE,"E4.sketch_text.stroke-149"),sQuery(id+"F3.wireOp",EDGE,"E4.sketch_text.stroke-150"),sQuery(id+"F3.wireOp",EDGE,"E4.sketch_text.stroke-151"),sQuery(id+"F3.wireOp",EDGE,"E4.sketch_text.stroke-152"),sQuery(id+"F3.wireOp",EDGE,"E4.sketch_text.stroke-153"),sQuery(id+"F3.wireOp",EDGE,"E4.sketch_text.stroke-159"),sQuery(id+"F3.wireOp",EDGE,"E4.sketch_text.stroke-160"),sQuery(id+"F3.wireOp",EDGE,"E4.sketch_text.stroke-161"),sQuery(id+"F3.wireOp",EDGE,"E4.sketch_text.stroke-162"),sQuery(id+"F3.wireOp",EDGE,"E4.sketch_text.stroke-163"),sQuery(id+"F3.wireOp",EDGE,"E4.sketch_text.stroke-164"),sQuery(id+"F3.wireOp",EDGE,"E4.sketch_text.stroke-165"),sQuery(id+"F3.wireOp",EDGE,"E4.sketch_text.stroke-166"),sQuery(id+"F3.wireOp",EDGE,"E4.sketch_text.stroke-167"),sQuery(id+"F3.wireOp",EDGE,"E4.sketch_text.stroke-168"),sQuery(id+"F3.wireOp",EDGE,"E4.sketch_text.stroke-169"),sQuery(id+"F3.wireOp",EDGE,"E4.sketch_text.stroke-170"),sQuery(id+"F3.wireOp",EDGE,"E4.sketch_text.stroke-171"),sQuery(id+"F3.wireOp",EDGE,"E4.sketch_text.stroke-172"),sQuery(id+"F3.wireOp",EDGE,"E4.sketch_text.stroke-173"),sQuery(id+"F3.wireOp",EDGE,"E4.sketch_text.stroke-174"),sQuery(id+"F3.wireOp",EDGE,"E4.sketch_text.stroke-175"),sQuery(id+"F3.wireOp",EDGE,"E4.sketch_text.stroke-176"),sQuery(id+"F3.wireOp",EDGE,"E4.sketch_text.stroke-177"),sQuery(id+"F3.wireOp",EDGE,"E4.sketch_text.stroke-178"),sQuery(id+"F3.wireOp",EDGE,"E4.sketch_text.stroke-179"),sQuery(id+"F3.wireOp",EDGE,"E4.sketch_text.stroke-180"),subQ0,subQ2])],"isStart":true}),makeQuery(id+"F6.opExtrude","SWEPT_FACE",FACE,{"disambiguationData":[OSD([subQ2])]})])],"derivedFrom":makeQuery(id+"F6.opExtrude","CAP_EDGE",EDGE,{"disambiguationData":[OSD([subQ0])],"isStart":true})});}
            var Q22;
            {var subQ0=sQuery(id+"F5.wireOp",EDGE,"E30");var subQ1=sQuery(id+"F0.wireOp",EDGE,"E0.top");var subQ2=sQuery(id+"F5.wireOp",EDGE,"E31");var subQ3=sQuery(id+"F0.wireOp",EDGE,"E0.bottom");Q22=makeQuery(id+"F6.boolean.opBoolean","SPLIT",EDGE,{"disambiguationData":[TD([makeQuery(id+"F1.opExtrude","CAP_FACE",FACE,{"disambiguationData":[OSD([subQ3,subQ1,sQuery(id+"F0.wireOp",EDGE,"E0.left"),sQuery(id+"F0.wireOp",EDGE,"E0.right")])],"isStart":false}),makeQuery(id+"F1.opExtrude","SWEPT_FACE",FACE,{"disambiguationData":[OSD([subQ1])]}),makeQuery(id+"F6.opExtrude","SWEPT_FACE",FACE,{"disambiguationData":[OSD([subQ0])]}),makeQuery(id+"F6.opExtrude","CAP_FACE",FACE,{"disambiguationData":[OSD([subQ3,sQuery(id+"F2.wireOp",EDGE,"E2.sketch_text.stroke-0"),sQuery(id+"F2.wireOp",EDGE,"E2.sketch_text.stroke-1"),sQuery(id+"F2.wireOp",EDGE,"E2.sketch_text.stroke-2"),sQuery(id+"F2.wireOp",EDGE,"E2.sketch_text.stroke-3"),sQuery(id+"F2.wireOp",EDGE,"E2.sketch_text.stroke-4"),sQuery(id+"F2.wireOp",EDGE,"E2.sketch_text.stroke-5"),sQuery(id+"F2.wireOp",EDGE,"E2.sketch_text.stroke-6"),sQuery(id+"F2.wireOp",EDGE,"E2.sketch_text.stroke-7"),sQuery(id+"F2.wireOp",EDGE,"E2.sketch_text.stroke-8"),sQuery(id+"F2.wireOp",EDGE,"E2.sketch_text.stroke-9"),sQuery(id+"F2.wireOp",EDGE,"E2.sketch_text.stroke-10"),sQuery(id+"F2.wireOp",EDGE,"E2.sketch_text.stroke-11"),sQuery(id+"F2.wireOp",EDGE,"E2.sketch_text.stroke-12"),sQuery(id+"F2.wireOp",EDGE,"E2.sketch_text.stroke-13"),sQuery(id+"F2.wireOp",EDGE,"E2.sketch_text.stroke-14"),sQuery(id+"F2.wireOp",EDGE,"E2.sketch_text.stroke-15"),sQuery(id+"F2.wireOp",EDGE,"E2.sketch_text.stroke-16"),sQuery(id+"F2.wireOp",EDGE,"E2.sketch_text.stroke-17"),sQuery(id+"F2.wireOp",EDGE,"E2.sketch_text.stroke-18"),sQuery(id+"F2.wireOp",EDGE,"E2.sketch_text.stroke-19"),sQuery(id+"F2.wireOp",EDGE,"E2.sketch_text.stroke-20"),sQuery(id+"F2.wireOp",EDGE,"E2.sketch_text.stroke-21"),sQuery(id+"F2.wireOp",EDGE,"E2.sketch_text.stroke-22"),sQuery(id+"F2.wireOp",EDGE,"E2.sketch_text.stroke-23"),sQuery(id+"F2.wireOp",EDGE,"E2.sketch_text.stroke-24"),sQuery(id+"F2.wireOp",EDGE,"E2.sketch_text.stroke-25"),sQuery(id+"F2.wireOp",EDGE,"E2.sketch_text.stroke-26"),sQuery(id+"F2.wireOp",EDGE,"E2.sketch_text.stroke-27"),sQuery(id+"F2.wireOp",EDGE,"E2.sketch_text.stroke-28"),sQuery(id+"F2.wireOp",EDGE,"E2.sketch_text.stroke-29"),sQuery(id+"F2.wireOp",EDGE,"E2.sketch_text.stroke-30"),sQuery(id+"F2.wireOp",EDGE,"E2.sketch_text.stroke-31"),sQuery(id+"F2.wireOp",EDGE,"E2.sketch_text.stroke-32"),sQuery(id+"F2.wireOp",EDGE,"E2.sketch_text.stroke-33"),sQuery(id+"F2.wireOp",EDGE,"E2.sketch_text.stroke-34"),sQuery(id+"F2.wireOp",EDGE,"E2.sketch_text.stroke-35"),sQuery(id+"F2.wireOp",EDGE,"E2.sketch_text.stroke-36"),sQuery(id+"F2.wireOp",EDGE,"E2.sketch_text.stroke-37"),sQuery(id+"F2.wireOp",EDGE,"E2.sketch_text.stroke-38"),sQuery(id+"F2.wireOp",EDGE,"E2.sketch_text.stroke-39"),sQuery(id+"F2.wireOp",EDGE,"E2.sketch_text.stroke-40"),sQuery(id+"F2.wireOp",EDGE,"E2.sketch_text.stroke-41"),sQuery(id+"F2.wireOp",EDGE,"E2.sketch_text.stroke-42"),sQuery(id+"F2.wireOp",EDGE,"E2.sketch_text.stroke-43"),sQuery(id+"F2.wireOp",EDGE,"E2.sketch_text.stroke-44"),sQuery(id+"F2.wireOp",EDGE,"E2.sketch_text.stroke-45"),sQuery(id+"F2.wireOp",EDGE,"E2.sketch_text.stroke-46"),sQuery(id+"F2.wireOp",EDGE,"E2.sketch_text.stroke-47"),sQuery(id+"F2.wireOp",EDGE,"E2.sketch_text.stroke-48"),sQuery(id+"F2.wireOp",EDGE,"E2.sketch_text.stroke-49"),sQuery(id+"F2.wireOp",EDGE,"E2.sketch_text.stroke-50"),sQuery(id+"F2.wireOp",EDGE,"E2.sketch_text.stroke-51"),sQuery(id+"F2.wireOp",EDGE,"E2.sketch_text.stroke-52"),sQuery(id+"F2.wireOp",EDGE,"E2.sketch_text.stroke-53"),sQuery(id+"F2.wireOp",EDGE,"E2.sketch_text.stroke-54"),sQuery(id+"F2.wireOp",EDGE,"E2.sketch_text.stroke-55"),sQuery(id+"F2.wireOp",EDGE,"E2.sketch_text.stroke-56"),sQuery(id+"F2.wireOp",EDGE,"E2.sketch_text.stroke-57"),sQuery(id+"F2.wireOp",EDGE,"E2.sketch_text.stroke-58"),sQuery(id+"F2.wireOp",EDGE,"E2.sketch_text.stroke-59"),sQuery(id+"F2.wireOp",EDGE,"E2.sketch_text.stroke-60"),sQuery(id+"F2.wireOp",EDGE,"E2.sketch_text.stroke-61"),sQuery(id+"F2.wireOp",EDGE,"E2.sketch_text.stroke-62"),sQuery(id+"F2.wireOp",EDGE,"E2.sketch_text.stroke-63"),sQuery(id+"F2.wireOp",EDGE,"E2.sketch_text.stroke-64"),sQuery(id+"F2.wireOp",EDGE,"E2.sketch_text.stroke-65"),sQuery(id+"F2.wireOp",EDGE,"E2.sketch_text.stroke-66"),sQuery(id+"F2.wireOp",EDGE,"E2.sketch_text.stroke-67"),sQuery(id+"F2.wireOp",EDGE,"E2.sketch_text.stroke-68"),sQuery(id+"F2.wireOp",EDGE,"E2.sketch_text.stroke-69"),sQuery(id+"F2.wireOp",EDGE,"E2.sketch_text.stroke-70"),sQuery(id+"F2.wireOp",EDGE,"E2.sketch_text.stroke-71"),sQuery(id+"F2.wireOp",EDGE,"E2.sketch_text.stroke-72"),sQuery(id+"F2.wireOp",EDGE,"E2.sketch_text.stroke-73"),sQuery(id+"F2.wireOp",EDGE,"E2.sketch_text.stroke-74"),sQuery(id+"F2.wireOp",EDGE,"E2.sketch_text.stroke-75"),sQuery(id+"F2.wireOp",EDGE,"E2.sketch_text.stroke-76"),sQuery(id+"F2.wireOp",EDGE,"E2.sketch_text.stroke-77"),sQuery(id+"F2.wireOp",EDGE,"E2.sketch_text.stroke-78"),sQuery(id+"F2.wireOp",EDGE,"E2.sketch_text.stroke-79"),sQuery(id+"F2.wireOp",EDGE,"E2.sketch_text.stroke-80"),sQuery(id+"F2.wireOp",EDGE,"E2.sketch_text.stroke-81"),sQuery(id+"F2.wireOp",EDGE,"E2.sketch_text.stroke-82"),sQuery(id+"F2.wireOp",EDGE,"E2.sketch_text.stroke-83"),sQuery(id+"F2.wireOp",EDGE,"E2.sketch_text.stroke-84"),sQuery(id+"F2.wireOp",EDGE,"E2.sketch_text.stroke-85"),sQuery(id+"F2.wireOp",EDGE,"E2.sketch_text.stroke-86"),sQuery(id+"F2.wireOp",EDGE,"E2.sketch_text.stroke-87"),sQuery(id+"F2.wireOp",EDGE,"E2.sketch_text.stroke-88"),sQuery(id+"F2.wireOp",EDGE,"E2.sketch_text.stroke-89"),sQuery(id+"F2.wireOp",EDGE,"E2.sketch_text.stroke-90"),sQuery(id+"F2.wireOp",EDGE,"E2.sketch_text.stroke-91"),sQuery(id+"F2.wireOp",EDGE,"E2.sketch_text.stroke-92"),sQuery(id+"F2.wireOp",EDGE,"E2.sketch_text.stroke-93"),sQuery(id+"F2.wireOp",EDGE,"E2.sketch_text.stroke-94"),sQuery(id+"F2.wireOp",EDGE,"E2.sketch_text.stroke-95"),sQuery(id+"F2.wireOp",EDGE,"E2.sketch_text.stroke-96"),sQuery(id+"F2.wireOp",EDGE,"E2.sketch_text.stroke-97"),sQuery(id+"F2.wireOp",EDGE,"E2.sketch_text.stroke-98"),sQuery(id+"F2.wireOp",EDGE,"E2.sketch_text.stroke-99"),sQuery(id+"F2.wireOp",EDGE,"E2.sketch_text.stroke-100"),sQuery(id+"F2.wireOp",EDGE,"E2.sketch_text.stroke-101"),sQuery(id+"F2.wireOp",EDGE,"E2.sketch_text.stroke-102"),sQuery(id+"F2.wireOp",EDGE,"E2.sketch_text.stroke-103"),sQuery(id+"F2.wireOp",EDGE,"E2.sketch_text.stroke-104"),sQuery(id+"F2.wireOp",EDGE,"E2.sketch_text.stroke-105"),sQuery(id+"F2.wireOp",EDGE,"E2.sketch_text.stroke-106"),sQuery(id+"F2.wireOp",EDGE,"E2.sketch_text.stroke-107"),sQuery(id+"F2.wireOp",EDGE,"E2.sketch_text.stroke-108"),sQuery(id+"F2.wireOp",EDGE,"E2.sketch_text.stroke-109"),sQuery(id+"F2.wireOp",EDGE,"E2.sketch_text.stroke-110"),sQuery(id+"F2.wireOp",EDGE,"E2.sketch_text.stroke-111"),sQuery(id+"F2.wireOp",EDGE,"E2.sketch_text.stroke-112"),sQuery(id+"F2.wireOp",EDGE,"E2.sketch_text.stroke-113"),sQuery(id+"F2.wireOp",EDGE,"E2.sketch_text.stroke-114"),sQuery(id+"F2.wireOp",EDGE,"E2.sketch_text.stroke-115"),sQuery(id+"F2.wireOp",EDGE,"E2.sketch_text.stroke-116"),sQuery(id+"F2.wireOp",EDGE,"E2.sketch_text.stroke-117"),sQuery(id+"F2.wireOp",EDGE,"E2.sketch_text.stroke-118"),sQuery(id+"F2.wireOp",EDGE,"E2.sketch_text.stroke-119"),sQuery(id+"F2.wireOp",EDGE,"E2.sketch_text.stroke-120"),sQuery(id+"F2.wireOp",EDGE,"E2.sketch_text.stroke-121"),sQuery(id+"F2.wireOp",EDGE,"E2.sketch_text.stroke-122"),sQuery(id+"F2.wireOp",EDGE,"E2.sketch_text.stroke-123"),sQuery(id+"F2.wireOp",EDGE,"E2.sketch_text.stroke-124"),sQuery(id+"F2.wireOp",EDGE,"E2.sketch_text.stroke-125"),sQuery(id+"F2.wireOp",EDGE,"E2.sketch_text.stroke-126"),sQuery(id+"F2.wireOp",EDGE,"E2.sketch_text.stroke-127"),sQuery(id+"F2.wireOp",EDGE,"E2.sketch_text.stroke-128"),sQuery(id+"F2.wireOp",EDGE,"E2.sketch_text.stroke-129"),sQuery(id+"F2.wireOp",EDGE,"E2.sketch_text.stroke-130"),sQuery(id+"F2.wireOp",EDGE,"E2.sketch_text.stroke-131"),sQuery(id+"F2.wireOp",EDGE,"E2.sketch_text.stroke-132"),sQuery(id+"F2.wireOp",EDGE,"E2.sketch_text.stroke-133"),sQuery(id+"F2.wireOp",EDGE,"E2.sketch_text.stroke-134"),sQuery(id+"F2.wireOp",EDGE,"E2.sketch_text.stroke-135"),sQuery(id+"F2.wireOp",EDGE,"E2.sketch_text.stroke-136"),sQuery(id+"F2.wireOp",EDGE,"E2.sketch_text.stroke-137"),sQuery(id+"F2.wireOp",EDGE,"E2.sketch_text.stroke-138"),sQuery(id+"F2.wireOp",EDGE,"E2.sketch_text.stroke-139"),sQuery(id+"F2.wireOp",EDGE,"E2.sketch_text.stroke-140"),sQuery(id+"F2.wireOp",EDGE,"E2.sketch_text.stroke-141"),sQuery(id+"F2.wireOp",EDGE,"E2.sketch_text.stroke-142"),sQuery(id+"F2.wireOp",EDGE,"E2.sketch_text.stroke-143"),sQuery(id+"F2.wireOp",EDGE,"E2.sketch_text.stroke-144"),sQuery(id+"F2.wireOp",EDGE,"E2.sketch_text.stroke-145"),sQuery(id+"F2.wireOp",EDGE,"E2.sketch_text.stroke-146"),sQuery(id+"F2.wireOp",EDGE,"E2.sketch_text.stroke-147"),sQuery(id+"F2.wireOp",EDGE,"E2.sketch_text.stroke-148"),sQuery(id+"F2.wireOp",EDGE,"E2.sketch_text.stroke-149"),sQuery(id+"F2.wireOp",EDGE,"E2.sketch_text.stroke-150"),sQuery(id+"F2.wireOp",EDGE,"E2.sketch_text.stroke-151"),sQuery(id+"F2.wireOp",EDGE,"E2.sketch_text.stroke-152"),sQuery(id+"F2.wireOp",EDGE,"E2.sketch_text.stroke-153"),sQuery(id+"F2.wireOp",EDGE,"E2.sketch_text.stroke-154"),sQuery(id+"F2.wireOp",EDGE,"E2.sketch_text.stroke-155"),sQuery(id+"F2.wireOp",EDGE,"E2.sketch_text.stroke-156"),sQuery(id+"F2.wireOp",EDGE,"E2.sketch_text.stroke-157"),sQuery(id+"F2.wireOp",EDGE,"E2.sketch_text.stroke-158"),sQuery(id+"F2.wireOp",EDGE,"E2.sketch_text.stroke-159"),sQuery(id+"F2.wireOp",EDGE,"E2.sketch_text.stroke-160"),sQuery(id+"F2.wireOp",EDGE,"E2.sketch_text.stroke-161"),sQuery(id+"F2.wireOp",EDGE,"E2.sketch_text.stroke-162"),sQuery(id+"F2.wireOp",EDGE,"E2.sketch_text.stroke-163"),sQuery(id+"F2.wireOp",EDGE,"E2.sketch_text.stroke-164"),sQuery(id+"F2.wireOp",EDGE,"E2.sketch_text.stroke-165"),sQuery(id+"F2.wireOp",EDGE,"E2.sketch_text.stroke-166"),sQuery(id+"F2.wireOp",EDGE,"E2.sketch_text.stroke-167"),sQuery(id+"F2.wireOp",EDGE,"E2.sketch_text.stroke-168"),sQuery(id+"F2.wireOp",EDGE,"E2.sketch_text.stroke-169"),sQuery(id+"F2.wireOp",EDGE,"E2.sketch_text.stroke-170"),sQuery(id+"F2.wireOp",EDGE,"E2.sketch_text.stroke-171"),sQuery(id+"F2.wireOp",EDGE,"E2.sketch_text.stroke-172"),sQuery(id+"F2.wireOp",EDGE,"E2.sketch_text.stroke-173"),sQuery(id+"F3.wireOp",EDGE,"E4.sketch_text.stroke-0"),sQuery(id+"F3.wireOp",EDGE,"E4.sketch_text.stroke-1"),sQuery(id+"F3.wireOp",EDGE,"E4.sketch_text.stroke-2"),sQuery(id+"F3.wireOp",EDGE,"E4.sketch_text.stroke-3"),sQuery(id+"F3.wireOp",EDGE,"E4.sketch_text.stroke-4"),sQuery(id+"F3.wireOp",EDGE,"E4.sketch_text.stroke-5"),sQuery(id+"F3.wireOp",EDGE,"E4.sketch_text.stroke-6"),sQuery(id+"F3.wireOp",EDGE,"E4.sketch_text.stroke-7"),sQuery(id+"F3.wireOp",EDGE,"E4.sketch_text.stroke-8"),sQuery(id+"F3.wireOp",EDGE,"E4.sketch_text.stroke-9"),sQuery(id+"F3.wireOp",EDGE,"E4.sketch_text.stroke-10"),sQuery(id+"F3.wireOp",EDGE,"E4.sketch_text.stroke-11"),sQuery(id+"F3.wireOp",EDGE,"E4.sketch_text.stroke-12"),sQuery(id+"F3.wireOp",EDGE,"E4.sketch_text.stroke-13"),sQuery(id+"F3.wireOp",EDGE,"E4.sketch_text.stroke-14"),sQuery(id+"F3.wireOp",EDGE,"E4.sketch_text.stroke-15"),sQuery(id+"F3.wireOp",EDGE,"E4.sketch_text.stroke-16"),sQuery(id+"F3.wireOp",EDGE,"E4.sketch_text.stroke-17"),sQuery(id+"F3.wireOp",EDGE,"E4.sketch_text.stroke-18"),sQuery(id+"F3.wireOp",EDGE,"E4.sketch_text.stroke-19"),sQuery(id+"F3.wireOp",EDGE,"E4.sketch_text.stroke-20"),sQuery(id+"F3.wireOp",EDGE,"E4.sketch_text.stroke-21"),sQuery(id+"F3.wireOp",EDGE,"E4.sketch_text.stroke-22"),sQuery(id+"F3.wireOp",EDGE,"E4.sketch_text.stroke-23"),sQuery(id+"F3.wireOp",EDGE,"E4.sketch_text.stroke-24"),sQuery(id+"F3.wireOp",EDGE,"E4.sketch_text.stroke-25"),sQuery(id+"F3.wireOp",EDGE,"E4.sketch_text.stroke-26"),sQuery(id+"F3.wireOp",EDGE,"E4.sketch_text.stroke-27"),sQuery(id+"F3.wireOp",EDGE,"E4.sketch_text.stroke-28"),sQuery(id+"F3.wireOp",EDGE,"E4.sketch_text.stroke-29"),sQuery(id+"F3.wireOp",EDGE,"E4.sketch_text.stroke-30"),sQuery(id+"F3.wireOp",EDGE,"E4.sketch_text.stroke-31"),sQuery(id+"F3.wireOp",EDGE,"E4.sketch_text.stroke-32"),sQuery(id+"F3.wireOp",EDGE,"E4.sketch_text.stroke-33"),sQuery(id+"F3.wireOp",EDGE,"E4.sketch_text.stroke-34"),sQuery(id+"F3.wireOp",EDGE,"E4.sketch_text.stroke-35"),sQuery(id+"F3.wireOp",EDGE,"E4.sketch_text.stroke-36"),sQuery(id+"F3.wireOp",EDGE,"E4.sketch_text.stroke-37"),sQuery(id+"F3.wireOp",EDGE,"E4.sketch_text.stroke-38"),sQuery(id+"F3.wireOp",EDGE,"E4.sketch_text.stroke-39"),sQuery(id+"F3.wireOp",EDGE,"E4.sketch_text.stroke-40"),sQuery(id+"F3.wireOp",EDGE,"E4.sketch_text.stroke-41"),sQuery(id+"F3.wireOp",EDGE,"E4.sketch_text.stroke-42"),sQuery(id+"F3.wireOp",EDGE,"E4.sketch_text.stroke-43"),sQuery(id+"F3.wireOp",EDGE,"E4.sketch_text.stroke-44"),sQuery(id+"F3.wireOp",EDGE,"E4.sketch_text.stroke-45"),sQuery(id+"F3.wireOp",EDGE,"E4.sketch_text.stroke-46"),sQuery(id+"F3.wireOp",EDGE,"E4.sketch_text.stroke-47"),sQuery(id+"F3.wireOp",EDGE,"E4.sketch_text.stroke-48"),sQuery(id+"F3.wireOp",EDGE,"E4.sketch_text.stroke-49"),sQuery(id+"F3.wireOp",EDGE,"E4.sketch_text.stroke-50"),sQuery(id+"F3.wireOp",EDGE,"E4.sketch_text.stroke-51"),sQuery(id+"F3.wireOp",EDGE,"E4.sketch_text.stroke-52"),sQuery(id+"F3.wireOp",EDGE,"E4.sketch_text.stroke-53"),sQuery(id+"F3.wireOp",EDGE,"E4.sketch_text.stroke-54"),sQuery(id+"F3.wireOp",EDGE,"E4.sketch_text.stroke-55"),sQuery(id+"F3.wireOp",EDGE,"E4.sketch_text.stroke-56"),sQuery(id+"F3.wireOp",EDGE,"E4.sketch_text.stroke-57"),sQuery(id+"F3.wireOp",EDGE,"E4.sketch_text.stroke-58"),sQuery(id+"F3.wireOp",EDGE,"E4.sketch_text.stroke-59"),sQuery(id+"F3.wireOp",EDGE,"E4.sketch_text.stroke-60"),sQuery(id+"F3.wireOp",EDGE,"E4.sketch_text.stroke-61"),sQuery(id+"F3.wireOp",EDGE,"E4.sketch_text.stroke-62"),sQuery(id+"F3.wireOp",EDGE,"E4.sketch_text.stroke-71"),sQuery(id+"F3.wireOp",EDGE,"E4.sketch_text.stroke-72"),sQuery(id+"F3.wireOp",EDGE,"E4.sketch_text.stroke-73"),sQuery(id+"F3.wireOp",EDGE,"E4.sketch_text.stroke-74"),sQuery(id+"F3.wireOp",EDGE,"E4.sketch_text.stroke-75"),sQuery(id+"F3.wireOp",EDGE,"E4.sketch_text.stroke-76"),sQuery(id+"F3.wireOp",EDGE,"E4.sketch_text.stroke-77"),sQuery(id+"F3.wireOp",EDGE,"E4.sketch_text.stroke-78"),sQuery(id+"F3.wireOp",EDGE,"E4.sketch_text.stroke-79"),sQuery(id+"F3.wireOp",EDGE,"E4.sketch_text.stroke-80"),sQuery(id+"F3.wireOp",EDGE,"E4.sketch_text.stroke-81"),sQuery(id+"F3.wireOp",EDGE,"E4.sketch_text.stroke-82"),sQuery(id+"F3.wireOp",EDGE,"E4.sketch_text.stroke-83"),sQuery(id+"F3.wireOp",EDGE,"E4.sketch_text.stroke-84"),sQuery(id+"F3.wireOp",EDGE,"E4.sketch_text.stroke-85"),sQuery(id+"F3.wireOp",EDGE,"E4.sketch_text.stroke-86"),sQuery(id+"F3.wireOp",EDGE,"E4.sketch_text.stroke-87"),sQuery(id+"F3.wireOp",EDGE,"E4.sketch_text.stroke-88"),sQuery(id+"F3.wireOp",EDGE,"E4.sketch_text.stroke-89"),sQuery(id+"F3.wireOp",EDGE,"E4.sketch_text.stroke-90"),sQuery(id+"F3.wireOp",EDGE,"E4.sketch_text.stroke-91"),sQuery(id+"F3.wireOp",EDGE,"E4.sketch_text.stroke-92"),sQuery(id+"F3.wireOp",EDGE,"E4.sketch_text.stroke-93"),sQuery(id+"F3.wireOp",EDGE,"E4.sketch_text.stroke-94"),sQuery(id+"F3.wireOp",EDGE,"E4.sketch_text.stroke-95"),sQuery(id+"F3.wireOp",EDGE,"E4.sketch_text.stroke-96"),sQuery(id+"F3.wireOp",EDGE,"E4.sketch_text.stroke-97"),sQuery(id+"F3.wireOp",EDGE,"E4.sketch_text.stroke-103"),sQuery(id+"F3.wireOp",EDGE,"E4.sketch_text.stroke-104"),sQuery(id+"F3.wireOp",EDGE,"E4.sketch_text.stroke-105"),sQuery(id+"F3.wireOp",EDGE,"E4.sketch_text.stroke-106"),sQuery(id+"F3.wireOp",EDGE,"E4.sketch_text.stroke-107"),sQuery(id+"F3.wireOp",EDGE,"E4.sketch_text.stroke-108"),sQuery(id+"F3.wireOp",EDGE,"E4.sketch_text.stroke-109"),sQuery(id+"F3.wireOp",EDGE,"E4.sketch_text.stroke-110"),sQuery(id+"F3.wireOp",EDGE,"E4.sketch_text.stroke-111"),sQuery(id+"F3.wireOp",EDGE,"E4.sketch_text.stroke-112"),sQuery(id+"F3.wireOp",EDGE,"E4.sketch_text.stroke-113"),sQuery(id+"F3.wireOp",EDGE,"E4.sketch_text.stroke-114"),sQuery(id+"F3.wireOp",EDGE,"E4.sketch_text.stroke-115"),sQuery(id+"F3.wireOp",EDGE,"E4.sketch_text.stroke-116"),sQuery(id+"F3.wireOp",EDGE,"E4.sketch_text.stroke-117"),sQuery(id+"F3.wireOp",EDGE,"E4.sketch_text.stroke-118"),sQuery(id+"F3.wireOp",EDGE,"E4.sketch_text.stroke-119"),sQuery(id+"F3.wireOp",EDGE,"E4.sketch_text.stroke-120"),sQuery(id+"F3.wireOp",EDGE,"E4.sketch_text.stroke-121"),sQuery(id+"F3.wireOp",EDGE,"E4.sketch_text.stroke-122"),sQuery(id+"F3.wireOp",EDGE,"E4.sketch_text.stroke-123"),sQuery(id+"F3.wireOp",EDGE,"E4.sketch_text.stroke-124"),sQuery(id+"F3.wireOp",EDGE,"E4.sketch_text.stroke-125"),sQuery(id+"F3.wireOp",EDGE,"E4.sketch_text.stroke-126"),sQuery(id+"F3.wireOp",EDGE,"E4.sketch_text.stroke-127"),sQuery(id+"F3.wireOp",EDGE,"E4.sketch_text.stroke-128"),sQuery(id+"F3.wireOp",EDGE,"E4.sketch_text.stroke-129"),sQuery(id+"F3.wireOp",EDGE,"E4.sketch_text.stroke-130"),sQuery(id+"F3.wireOp",EDGE,"E4.sketch_text.stroke-131"),sQuery(id+"F3.wireOp",EDGE,"E4.sketch_text.stroke-132"),sQuery(id+"F3.wireOp",EDGE,"E4.sketch_text.stroke-133"),sQuery(id+"F3.wireOp",EDGE,"E4.sketch_text.stroke-134"),sQuery(id+"F3.wireOp",EDGE,"E4.sketch_text.stroke-135"),sQuery(id+"F3.wireOp",EDGE,"E4.sketch_text.stroke-136"),sQuery(id+"F3.wireOp",EDGE,"E4.sketch_text.stroke-137"),sQuery(id+"F3.wireOp",EDGE,"E4.sketch_text.stroke-138"),sQuery(id+"F3.wireOp",EDGE,"E4.sketch_text.stroke-139"),sQuery(id+"F3.wireOp",EDGE,"E4.sketch_text.stroke-140"),sQuery(id+"F3.wireOp",EDGE,"E4.sketch_text.stroke-141"),sQuery(id+"F3.wireOp",EDGE,"E4.sketch_text.stroke-142"),sQuery(id+"F3.wireOp",EDGE,"E4.sketch_text.stroke-143"),sQuery(id+"F3.wireOp",EDGE,"E4.sketch_text.stroke-144"),sQuery(id+"F3.wireOp",EDGE,"E4.sketch_text.stroke-145"),sQuery(id+"F3.wireOp",EDGE,"E4.sketch_text.stroke-146"),sQuery(id+"F3.wireOp",EDGE,"E4.sketch_text.stroke-147"),sQuery(id+"F3.wireOp",EDGE,"E4.sketch_text.stroke-148"),sQuery(id+"F3.wireOp",EDGE,"E4.sketch_text.stroke-149"),sQuery(id+"F3.wireOp",EDGE,"E4.sketch_text.stroke-150"),sQuery(id+"F3.wireOp",EDGE,"E4.sketch_text.stroke-151"),sQuery(id+"F3.wireOp",EDGE,"E4.sketch_text.stroke-152"),sQuery(id+"F3.wireOp",EDGE,"E4.sketch_text.stroke-153"),sQuery(id+"F3.wireOp",EDGE,"E4.sketch_text.stroke-159"),sQuery(id+"F3.wireOp",EDGE,"E4.sketch_text.stroke-160"),sQuery(id+"F3.wireOp",EDGE,"E4.sketch_text.stroke-161"),sQuery(id+"F3.wireOp",EDGE,"E4.sketch_text.stroke-162"),sQuery(id+"F3.wireOp",EDGE,"E4.sketch_text.stroke-163"),sQuery(id+"F3.wireOp",EDGE,"E4.sketch_text.stroke-164"),sQuery(id+"F3.wireOp",EDGE,"E4.sketch_text.stroke-165"),sQuery(id+"F3.wireOp",EDGE,"E4.sketch_text.stroke-166"),sQuery(id+"F3.wireOp",EDGE,"E4.sketch_text.stroke-167"),sQuery(id+"F3.wireOp",EDGE,"E4.sketch_text.stroke-168"),sQuery(id+"F3.wireOp",EDGE,"E4.sketch_text.stroke-169"),sQuery(id+"F3.wireOp",EDGE,"E4.sketch_text.stroke-170"),sQuery(id+"F3.wireOp",EDGE,"E4.sketch_text.stroke-171"),sQuery(id+"F3.wireOp",EDGE,"E4.sketch_text.stroke-172"),sQuery(id+"F3.wireOp",EDGE,"E4.sketch_text.stroke-173"),sQuery(id+"F3.wireOp",EDGE,"E4.sketch_text.stroke-174"),sQuery(id+"F3.wireOp",EDGE,"E4.sketch_text.stroke-175"),sQuery(id+"F3.wireOp",EDGE,"E4.sketch_text.stroke-176"),sQuery(id+"F3.wireOp",EDGE,"E4.sketch_text.stroke-177"),sQuery(id+"F3.wireOp",EDGE,"E4.sketch_text.stroke-178"),sQuery(id+"F3.wireOp",EDGE,"E4.sketch_text.stroke-179"),sQuery(id+"F3.wireOp",EDGE,"E4.sketch_text.stroke-180"),subQ0,subQ2])],"isStart":true}),makeQuery(id+"F6.opExtrude","SWEPT_FACE",FACE,{"disambiguationData":[OSD([subQ2])]})])],"derivedFrom":makeQuery(id+"F6.opExtrude","CAP_EDGE",EDGE,{"disambiguationData":[OSD([subQ2])],"isStart":true})});}
            var Q23;
            {var subQ0=sQuery(id+"F0.wireOp",EDGE,"E0.top");var subQ1=sQuery(id+"F0.wireOp",EDGE,"E0.bottom");var subQ2=sQuery(id+"F5.wireOp",EDGE,"E31");Q23=makeQuery(id+"F6.boolean.opBoolean","SPLIT",EDGE,{"disambiguationData":[TD([makeQuery(id+"F1.opExtrude","CAP_FACE",FACE,{"disambiguationData":[OSD([subQ1,subQ0,sQuery(id+"F0.wireOp",EDGE,"E0.left"),sQuery(id+"F0.wireOp",EDGE,"E0.right")])],"isStart":false}),makeQuery(id+"F1.opExtrude","SWEPT_FACE",FACE,{"disambiguationData":[OSD([subQ0])]}),makeQuery(id+"F6.opExtrude","CAP_FACE",FACE,{"disambiguationData":[OSD([subQ1,sQuery(id+"F2.wireOp",EDGE,"E2.sketch_text.stroke-0"),sQuery(id+"F2.wireOp",EDGE,"E2.sketch_text.stroke-1"),sQuery(id+"F2.wireOp",EDGE,"E2.sketch_text.stroke-2"),sQuery(id+"F2.wireOp",EDGE,"E2.sketch_text.stroke-3"),sQuery(id+"F2.wireOp",EDGE,"E2.sketch_text.stroke-4"),sQuery(id+"F2.wireOp",EDGE,"E2.sketch_text.stroke-5"),sQuery(id+"F2.wireOp",EDGE,"E2.sketch_text.stroke-6"),sQuery(id+"F2.wireOp",EDGE,"E2.sketch_text.stroke-7"),sQuery(id+"F2.wireOp",EDGE,"E2.sketch_text.stroke-8"),sQuery(id+"F2.wireOp",EDGE,"E2.sketch_text.stroke-9"),sQuery(id+"F2.wireOp",EDGE,"E2.sketch_text.stroke-10"),sQuery(id+"F2.wireOp",EDGE,"E2.sketch_text.stroke-11"),sQuery(id+"F2.wireOp",EDGE,"E2.sketch_text.stroke-12"),sQuery(id+"F2.wireOp",EDGE,"E2.sketch_text.stroke-13"),sQuery(id+"F2.wireOp",EDGE,"E2.sketch_text.stroke-14"),sQuery(id+"F2.wireOp",EDGE,"E2.sketch_text.stroke-15"),sQuery(id+"F2.wireOp",EDGE,"E2.sketch_text.stroke-16"),sQuery(id+"F2.wireOp",EDGE,"E2.sketch_text.stroke-17"),sQuery(id+"F2.wireOp",EDGE,"E2.sketch_text.stroke-18"),sQuery(id+"F2.wireOp",EDGE,"E2.sketch_text.stroke-19"),sQuery(id+"F2.wireOp",EDGE,"E2.sketch_text.stroke-20"),sQuery(id+"F2.wireOp",EDGE,"E2.sketch_text.stroke-21"),sQuery(id+"F2.wireOp",EDGE,"E2.sketch_text.stroke-22"),sQuery(id+"F2.wireOp",EDGE,"E2.sketch_text.stroke-23"),sQuery(id+"F2.wireOp",EDGE,"E2.sketch_text.stroke-24"),sQuery(id+"F2.wireOp",EDGE,"E2.sketch_text.stroke-25"),sQuery(id+"F2.wireOp",EDGE,"E2.sketch_text.stroke-26"),sQuery(id+"F2.wireOp",EDGE,"E2.sketch_text.stroke-27"),sQuery(id+"F2.wireOp",EDGE,"E2.sketch_text.stroke-28"),sQuery(id+"F2.wireOp",EDGE,"E2.sketch_text.stroke-29"),sQuery(id+"F2.wireOp",EDGE,"E2.sketch_text.stroke-30"),sQuery(id+"F2.wireOp",EDGE,"E2.sketch_text.stroke-31"),sQuery(id+"F2.wireOp",EDGE,"E2.sketch_text.stroke-32"),sQuery(id+"F2.wireOp",EDGE,"E2.sketch_text.stroke-33"),sQuery(id+"F2.wireOp",EDGE,"E2.sketch_text.stroke-34"),sQuery(id+"F2.wireOp",EDGE,"E2.sketch_text.stroke-35"),sQuery(id+"F2.wireOp",EDGE,"E2.sketch_text.stroke-36"),sQuery(id+"F2.wireOp",EDGE,"E2.sketch_text.stroke-37"),sQuery(id+"F2.wireOp",EDGE,"E2.sketch_text.stroke-38"),sQuery(id+"F2.wireOp",EDGE,"E2.sketch_text.stroke-39"),sQuery(id+"F2.wireOp",EDGE,"E2.sketch_text.stroke-40"),sQuery(id+"F2.wireOp",EDGE,"E2.sketch_text.stroke-41"),sQuery(id+"F2.wireOp",EDGE,"E2.sketch_text.stroke-42"),sQuery(id+"F2.wireOp",EDGE,"E2.sketch_text.stroke-43"),sQuery(id+"F2.wireOp",EDGE,"E2.sketch_text.stroke-44"),sQuery(id+"F2.wireOp",EDGE,"E2.sketch_text.stroke-45"),sQuery(id+"F2.wireOp",EDGE,"E2.sketch_text.stroke-46"),sQuery(id+"F2.wireOp",EDGE,"E2.sketch_text.stroke-47"),sQuery(id+"F2.wireOp",EDGE,"E2.sketch_text.stroke-48"),sQuery(id+"F2.wireOp",EDGE,"E2.sketch_text.stroke-49"),sQuery(id+"F2.wireOp",EDGE,"E2.sketch_text.stroke-50"),sQuery(id+"F2.wireOp",EDGE,"E2.sketch_text.stroke-51"),sQuery(id+"F2.wireOp",EDGE,"E2.sketch_text.stroke-52"),sQuery(id+"F2.wireOp",EDGE,"E2.sketch_text.stroke-53"),sQuery(id+"F2.wireOp",EDGE,"E2.sketch_text.stroke-54"),sQuery(id+"F2.wireOp",EDGE,"E2.sketch_text.stroke-55"),sQuery(id+"F2.wireOp",EDGE,"E2.sketch_text.stroke-56"),sQuery(id+"F2.wireOp",EDGE,"E2.sketch_text.stroke-57"),sQuery(id+"F2.wireOp",EDGE,"E2.sketch_text.stroke-58"),sQuery(id+"F2.wireOp",EDGE,"E2.sketch_text.stroke-59"),sQuery(id+"F2.wireOp",EDGE,"E2.sketch_text.stroke-60"),sQuery(id+"F2.wireOp",EDGE,"E2.sketch_text.stroke-61"),sQuery(id+"F2.wireOp",EDGE,"E2.sketch_text.stroke-62"),sQuery(id+"F2.wireOp",EDGE,"E2.sketch_text.stroke-63"),sQuery(id+"F2.wireOp",EDGE,"E2.sketch_text.stroke-64"),sQuery(id+"F2.wireOp",EDGE,"E2.sketch_text.stroke-65"),sQuery(id+"F2.wireOp",EDGE,"E2.sketch_text.stroke-66"),sQuery(id+"F2.wireOp",EDGE,"E2.sketch_text.stroke-67"),sQuery(id+"F2.wireOp",EDGE,"E2.sketch_text.stroke-68"),sQuery(id+"F2.wireOp",EDGE,"E2.sketch_text.stroke-69"),sQuery(id+"F2.wireOp",EDGE,"E2.sketch_text.stroke-70"),sQuery(id+"F2.wireOp",EDGE,"E2.sketch_text.stroke-71"),sQuery(id+"F2.wireOp",EDGE,"E2.sketch_text.stroke-72"),sQuery(id+"F2.wireOp",EDGE,"E2.sketch_text.stroke-73"),sQuery(id+"F2.wireOp",EDGE,"E2.sketch_text.stroke-74"),sQuery(id+"F2.wireOp",EDGE,"E2.sketch_text.stroke-75"),sQuery(id+"F2.wireOp",EDGE,"E2.sketch_text.stroke-76"),sQuery(id+"F2.wireOp",EDGE,"E2.sketch_text.stroke-77"),sQuery(id+"F2.wireOp",EDGE,"E2.sketch_text.stroke-78"),sQuery(id+"F2.wireOp",EDGE,"E2.sketch_text.stroke-79"),sQuery(id+"F2.wireOp",EDGE,"E2.sketch_text.stroke-80"),sQuery(id+"F2.wireOp",EDGE,"E2.sketch_text.stroke-81"),sQuery(id+"F2.wireOp",EDGE,"E2.sketch_text.stroke-82"),sQuery(id+"F2.wireOp",EDGE,"E2.sketch_text.stroke-83"),sQuery(id+"F2.wireOp",EDGE,"E2.sketch_text.stroke-84"),sQuery(id+"F2.wireOp",EDGE,"E2.sketch_text.stroke-85"),sQuery(id+"F2.wireOp",EDGE,"E2.sketch_text.stroke-86"),sQuery(id+"F2.wireOp",EDGE,"E2.sketch_text.stroke-87"),sQuery(id+"F2.wireOp",EDGE,"E2.sketch_text.stroke-88"),sQuery(id+"F2.wireOp",EDGE,"E2.sketch_text.stroke-89"),sQuery(id+"F2.wireOp",EDGE,"E2.sketch_text.stroke-90"),sQuery(id+"F2.wireOp",EDGE,"E2.sketch_text.stroke-91"),sQuery(id+"F2.wireOp",EDGE,"E2.sketch_text.stroke-92"),sQuery(id+"F2.wireOp",EDGE,"E2.sketch_text.stroke-93"),sQuery(id+"F2.wireOp",EDGE,"E2.sketch_text.stroke-94"),sQuery(id+"F2.wireOp",EDGE,"E2.sketch_text.stroke-95"),sQuery(id+"F2.wireOp",EDGE,"E2.sketch_text.stroke-96"),sQuery(id+"F2.wireOp",EDGE,"E2.sketch_text.stroke-97"),sQuery(id+"F2.wireOp",EDGE,"E2.sketch_text.stroke-98"),sQuery(id+"F2.wireOp",EDGE,"E2.sketch_text.stroke-99"),sQuery(id+"F2.wireOp",EDGE,"E2.sketch_text.stroke-100"),sQuery(id+"F2.wireOp",EDGE,"E2.sketch_text.stroke-101"),sQuery(id+"F2.wireOp",EDGE,"E2.sketch_text.stroke-102"),sQuery(id+"F2.wireOp",EDGE,"E2.sketch_text.stroke-103"),sQuery(id+"F2.wireOp",EDGE,"E2.sketch_text.stroke-104"),sQuery(id+"F2.wireOp",EDGE,"E2.sketch_text.stroke-105"),sQuery(id+"F2.wireOp",EDGE,"E2.sketch_text.stroke-106"),sQuery(id+"F2.wireOp",EDGE,"E2.sketch_text.stroke-107"),sQuery(id+"F2.wireOp",EDGE,"E2.sketch_text.stroke-108"),sQuery(id+"F2.wireOp",EDGE,"E2.sketch_text.stroke-109"),sQuery(id+"F2.wireOp",EDGE,"E2.sketch_text.stroke-110"),sQuery(id+"F2.wireOp",EDGE,"E2.sketch_text.stroke-111"),sQuery(id+"F2.wireOp",EDGE,"E2.sketch_text.stroke-112"),sQuery(id+"F2.wireOp",EDGE,"E2.sketch_text.stroke-113"),sQuery(id+"F2.wireOp",EDGE,"E2.sketch_text.stroke-114"),sQuery(id+"F2.wireOp",EDGE,"E2.sketch_text.stroke-115"),sQuery(id+"F2.wireOp",EDGE,"E2.sketch_text.stroke-116"),sQuery(id+"F2.wireOp",EDGE,"E2.sketch_text.stroke-117"),sQuery(id+"F2.wireOp",EDGE,"E2.sketch_text.stroke-118"),sQuery(id+"F2.wireOp",EDGE,"E2.sketch_text.stroke-119"),sQuery(id+"F2.wireOp",EDGE,"E2.sketch_text.stroke-120"),sQuery(id+"F2.wireOp",EDGE,"E2.sketch_text.stroke-121"),sQuery(id+"F2.wireOp",EDGE,"E2.sketch_text.stroke-122"),sQuery(id+"F2.wireOp",EDGE,"E2.sketch_text.stroke-123"),sQuery(id+"F2.wireOp",EDGE,"E2.sketch_text.stroke-124"),sQuery(id+"F2.wireOp",EDGE,"E2.sketch_text.stroke-125"),sQuery(id+"F2.wireOp",EDGE,"E2.sketch_text.stroke-126"),sQuery(id+"F2.wireOp",EDGE,"E2.sketch_text.stroke-127"),sQuery(id+"F2.wireOp",EDGE,"E2.sketch_text.stroke-128"),sQuery(id+"F2.wireOp",EDGE,"E2.sketch_text.stroke-129"),sQuery(id+"F2.wireOp",EDGE,"E2.sketch_text.stroke-130"),sQuery(id+"F2.wireOp",EDGE,"E2.sketch_text.stroke-131"),sQuery(id+"F2.wireOp",EDGE,"E2.sketch_text.stroke-132"),sQuery(id+"F2.wireOp",EDGE,"E2.sketch_text.stroke-133"),sQuery(id+"F2.wireOp",EDGE,"E2.sketch_text.stroke-134"),sQuery(id+"F2.wireOp",EDGE,"E2.sketch_text.stroke-135"),sQuery(id+"F2.wireOp",EDGE,"E2.sketch_text.stroke-136"),sQuery(id+"F2.wireOp",EDGE,"E2.sketch_text.stroke-137"),sQuery(id+"F2.wireOp",EDGE,"E2.sketch_text.stroke-138"),sQuery(id+"F2.wireOp",EDGE,"E2.sketch_text.stroke-139"),sQuery(id+"F2.wireOp",EDGE,"E2.sketch_text.stroke-140"),sQuery(id+"F2.wireOp",EDGE,"E2.sketch_text.stroke-141"),sQuery(id+"F2.wireOp",EDGE,"E2.sketch_text.stroke-142"),sQuery(id+"F2.wireOp",EDGE,"E2.sketch_text.stroke-143"),sQuery(id+"F2.wireOp",EDGE,"E2.sketch_text.stroke-144"),sQuery(id+"F2.wireOp",EDGE,"E2.sketch_text.stroke-145"),sQuery(id+"F2.wireOp",EDGE,"E2.sketch_text.stroke-146"),sQuery(id+"F2.wireOp",EDGE,"E2.sketch_text.stroke-147"),sQuery(id+"F2.wireOp",EDGE,"E2.sketch_text.stroke-148"),sQuery(id+"F2.wireOp",EDGE,"E2.sketch_text.stroke-149"),sQuery(id+"F2.wireOp",EDGE,"E2.sketch_text.stroke-150"),sQuery(id+"F2.wireOp",EDGE,"E2.sketch_text.stroke-151"),sQuery(id+"F2.wireOp",EDGE,"E2.sketch_text.stroke-152"),sQuery(id+"F2.wireOp",EDGE,"E2.sketch_text.stroke-153"),sQuery(id+"F2.wireOp",EDGE,"E2.sketch_text.stroke-154"),sQuery(id+"F2.wireOp",EDGE,"E2.sketch_text.stroke-155"),sQuery(id+"F2.wireOp",EDGE,"E2.sketch_text.stroke-156"),sQuery(id+"F2.wireOp",EDGE,"E2.sketch_text.stroke-157"),sQuery(id+"F2.wireOp",EDGE,"E2.sketch_text.stroke-158"),sQuery(id+"F2.wireOp",EDGE,"E2.sketch_text.stroke-159"),sQuery(id+"F2.wireOp",EDGE,"E2.sketch_text.stroke-160"),sQuery(id+"F2.wireOp",EDGE,"E2.sketch_text.stroke-161"),sQuery(id+"F2.wireOp",EDGE,"E2.sketch_text.stroke-162"),sQuery(id+"F2.wireOp",EDGE,"E2.sketch_text.stroke-163"),sQuery(id+"F2.wireOp",EDGE,"E2.sketch_text.stroke-164"),sQuery(id+"F2.wireOp",EDGE,"E2.sketch_text.stroke-165"),sQuery(id+"F2.wireOp",EDGE,"E2.sketch_text.stroke-166"),sQuery(id+"F2.wireOp",EDGE,"E2.sketch_text.stroke-167"),sQuery(id+"F2.wireOp",EDGE,"E2.sketch_text.stroke-168"),sQuery(id+"F2.wireOp",EDGE,"E2.sketch_text.stroke-169"),sQuery(id+"F2.wireOp",EDGE,"E2.sketch_text.stroke-170"),sQuery(id+"F2.wireOp",EDGE,"E2.sketch_text.stroke-171"),sQuery(id+"F2.wireOp",EDGE,"E2.sketch_text.stroke-172"),sQuery(id+"F2.wireOp",EDGE,"E2.sketch_text.stroke-173"),sQuery(id+"F3.wireOp",EDGE,"E4.sketch_text.stroke-0"),sQuery(id+"F3.wireOp",EDGE,"E4.sketch_text.stroke-1"),sQuery(id+"F3.wireOp",EDGE,"E4.sketch_text.stroke-2"),sQuery(id+"F3.wireOp",EDGE,"E4.sketch_text.stroke-3"),sQuery(id+"F3.wireOp",EDGE,"E4.sketch_text.stroke-4"),sQuery(id+"F3.wireOp",EDGE,"E4.sketch_text.stroke-5"),sQuery(id+"F3.wireOp",EDGE,"E4.sketch_text.stroke-6"),sQuery(id+"F3.wireOp",EDGE,"E4.sketch_text.stroke-7"),sQuery(id+"F3.wireOp",EDGE,"E4.sketch_text.stroke-8"),sQuery(id+"F3.wireOp",EDGE,"E4.sketch_text.stroke-9"),sQuery(id+"F3.wireOp",EDGE,"E4.sketch_text.stroke-10"),sQuery(id+"F3.wireOp",EDGE,"E4.sketch_text.stroke-11"),sQuery(id+"F3.wireOp",EDGE,"E4.sketch_text.stroke-12"),sQuery(id+"F3.wireOp",EDGE,"E4.sketch_text.stroke-13"),sQuery(id+"F3.wireOp",EDGE,"E4.sketch_text.stroke-14"),sQuery(id+"F3.wireOp",EDGE,"E4.sketch_text.stroke-15"),sQuery(id+"F3.wireOp",EDGE,"E4.sketch_text.stroke-16"),sQuery(id+"F3.wireOp",EDGE,"E4.sketch_text.stroke-17"),sQuery(id+"F3.wireOp",EDGE,"E4.sketch_text.stroke-18"),sQuery(id+"F3.wireOp",EDGE,"E4.sketch_text.stroke-19"),sQuery(id+"F3.wireOp",EDGE,"E4.sketch_text.stroke-20"),sQuery(id+"F3.wireOp",EDGE,"E4.sketch_text.stroke-21"),sQuery(id+"F3.wireOp",EDGE,"E4.sketch_text.stroke-22"),sQuery(id+"F3.wireOp",EDGE,"E4.sketch_text.stroke-23"),sQuery(id+"F3.wireOp",EDGE,"E4.sketch_text.stroke-24"),sQuery(id+"F3.wireOp",EDGE,"E4.sketch_text.stroke-25"),sQuery(id+"F3.wireOp",EDGE,"E4.sketch_text.stroke-26"),sQuery(id+"F3.wireOp",EDGE,"E4.sketch_text.stroke-27"),sQuery(id+"F3.wireOp",EDGE,"E4.sketch_text.stroke-28"),sQuery(id+"F3.wireOp",EDGE,"E4.sketch_text.stroke-29"),sQuery(id+"F3.wireOp",EDGE,"E4.sketch_text.stroke-30"),sQuery(id+"F3.wireOp",EDGE,"E4.sketch_text.stroke-31"),sQuery(id+"F3.wireOp",EDGE,"E4.sketch_text.stroke-32"),sQuery(id+"F3.wireOp",EDGE,"E4.sketch_text.stroke-33"),sQuery(id+"F3.wireOp",EDGE,"E4.sketch_text.stroke-34"),sQuery(id+"F3.wireOp",EDGE,"E4.sketch_text.stroke-35"),sQuery(id+"F3.wireOp",EDGE,"E4.sketch_text.stroke-36"),sQuery(id+"F3.wireOp",EDGE,"E4.sketch_text.stroke-37"),sQuery(id+"F3.wireOp",EDGE,"E4.sketch_text.stroke-38"),sQuery(id+"F3.wireOp",EDGE,"E4.sketch_text.stroke-39"),sQuery(id+"F3.wireOp",EDGE,"E4.sketch_text.stroke-40"),sQuery(id+"F3.wireOp",EDGE,"E4.sketch_text.stroke-41"),sQuery(id+"F3.wireOp",EDGE,"E4.sketch_text.stroke-42"),sQuery(id+"F3.wireOp",EDGE,"E4.sketch_text.stroke-43"),sQuery(id+"F3.wireOp",EDGE,"E4.sketch_text.stroke-44"),sQuery(id+"F3.wireOp",EDGE,"E4.sketch_text.stroke-45"),sQuery(id+"F3.wireOp",EDGE,"E4.sketch_text.stroke-46"),sQuery(id+"F3.wireOp",EDGE,"E4.sketch_text.stroke-47"),sQuery(id+"F3.wireOp",EDGE,"E4.sketch_text.stroke-48"),sQuery(id+"F3.wireOp",EDGE,"E4.sketch_text.stroke-49"),sQuery(id+"F3.wireOp",EDGE,"E4.sketch_text.stroke-50"),sQuery(id+"F3.wireOp",EDGE,"E4.sketch_text.stroke-51"),sQuery(id+"F3.wireOp",EDGE,"E4.sketch_text.stroke-52"),sQuery(id+"F3.wireOp",EDGE,"E4.sketch_text.stroke-53"),sQuery(id+"F3.wireOp",EDGE,"E4.sketch_text.stroke-54"),sQuery(id+"F3.wireOp",EDGE,"E4.sketch_text.stroke-55"),sQuery(id+"F3.wireOp",EDGE,"E4.sketch_text.stroke-56"),sQuery(id+"F3.wireOp",EDGE,"E4.sketch_text.stroke-57"),sQuery(id+"F3.wireOp",EDGE,"E4.sketch_text.stroke-58"),sQuery(id+"F3.wireOp",EDGE,"E4.sketch_text.stroke-59"),sQuery(id+"F3.wireOp",EDGE,"E4.sketch_text.stroke-60"),sQuery(id+"F3.wireOp",EDGE,"E4.sketch_text.stroke-61"),sQuery(id+"F3.wireOp",EDGE,"E4.sketch_text.stroke-62"),sQuery(id+"F3.wireOp",EDGE,"E4.sketch_text.stroke-71"),sQuery(id+"F3.wireOp",EDGE,"E4.sketch_text.stroke-72"),sQuery(id+"F3.wireOp",EDGE,"E4.sketch_text.stroke-73"),sQuery(id+"F3.wireOp",EDGE,"E4.sketch_text.stroke-74"),sQuery(id+"F3.wireOp",EDGE,"E4.sketch_text.stroke-75"),sQuery(id+"F3.wireOp",EDGE,"E4.sketch_text.stroke-76"),sQuery(id+"F3.wireOp",EDGE,"E4.sketch_text.stroke-77"),sQuery(id+"F3.wireOp",EDGE,"E4.sketch_text.stroke-78"),sQuery(id+"F3.wireOp",EDGE,"E4.sketch_text.stroke-79"),sQuery(id+"F3.wireOp",EDGE,"E4.sketch_text.stroke-80"),sQuery(id+"F3.wireOp",EDGE,"E4.sketch_text.stroke-81"),sQuery(id+"F3.wireOp",EDGE,"E4.sketch_text.stroke-82"),sQuery(id+"F3.wireOp",EDGE,"E4.sketch_text.stroke-83"),sQuery(id+"F3.wireOp",EDGE,"E4.sketch_text.stroke-84"),sQuery(id+"F3.wireOp",EDGE,"E4.sketch_text.stroke-85"),sQuery(id+"F3.wireOp",EDGE,"E4.sketch_text.stroke-86"),sQuery(id+"F3.wireOp",EDGE,"E4.sketch_text.stroke-87"),sQuery(id+"F3.wireOp",EDGE,"E4.sketch_text.stroke-88"),sQuery(id+"F3.wireOp",EDGE,"E4.sketch_text.stroke-89"),sQuery(id+"F3.wireOp",EDGE,"E4.sketch_text.stroke-90"),sQuery(id+"F3.wireOp",EDGE,"E4.sketch_text.stroke-91"),sQuery(id+"F3.wireOp",EDGE,"E4.sketch_text.stroke-92"),sQuery(id+"F3.wireOp",EDGE,"E4.sketch_text.stroke-93"),sQuery(id+"F3.wireOp",EDGE,"E4.sketch_text.stroke-94"),sQuery(id+"F3.wireOp",EDGE,"E4.sketch_text.stroke-95"),sQuery(id+"F3.wireOp",EDGE,"E4.sketch_text.stroke-96"),sQuery(id+"F3.wireOp",EDGE,"E4.sketch_text.stroke-97"),sQuery(id+"F3.wireOp",EDGE,"E4.sketch_text.stroke-103"),sQuery(id+"F3.wireOp",EDGE,"E4.sketch_text.stroke-104"),sQuery(id+"F3.wireOp",EDGE,"E4.sketch_text.stroke-105"),sQuery(id+"F3.wireOp",EDGE,"E4.sketch_text.stroke-106"),sQuery(id+"F3.wireOp",EDGE,"E4.sketch_text.stroke-107"),sQuery(id+"F3.wireOp",EDGE,"E4.sketch_text.stroke-108"),sQuery(id+"F3.wireOp",EDGE,"E4.sketch_text.stroke-109"),sQuery(id+"F3.wireOp",EDGE,"E4.sketch_text.stroke-110"),sQuery(id+"F3.wireOp",EDGE,"E4.sketch_text.stroke-111"),sQuery(id+"F3.wireOp",EDGE,"E4.sketch_text.stroke-112"),sQuery(id+"F3.wireOp",EDGE,"E4.sketch_text.stroke-113"),sQuery(id+"F3.wireOp",EDGE,"E4.sketch_text.stroke-114"),sQuery(id+"F3.wireOp",EDGE,"E4.sketch_text.stroke-115"),sQuery(id+"F3.wireOp",EDGE,"E4.sketch_text.stroke-116"),sQuery(id+"F3.wireOp",EDGE,"E4.sketch_text.stroke-117"),sQuery(id+"F3.wireOp",EDGE,"E4.sketch_text.stroke-118"),sQuery(id+"F3.wireOp",EDGE,"E4.sketch_text.stroke-119"),sQuery(id+"F3.wireOp",EDGE,"E4.sketch_text.stroke-120"),sQuery(id+"F3.wireOp",EDGE,"E4.sketch_text.stroke-121"),sQuery(id+"F3.wireOp",EDGE,"E4.sketch_text.stroke-122"),sQuery(id+"F3.wireOp",EDGE,"E4.sketch_text.stroke-123"),sQuery(id+"F3.wireOp",EDGE,"E4.sketch_text.stroke-124"),sQuery(id+"F3.wireOp",EDGE,"E4.sketch_text.stroke-125"),sQuery(id+"F3.wireOp",EDGE,"E4.sketch_text.stroke-126"),sQuery(id+"F3.wireOp",EDGE,"E4.sketch_text.stroke-127"),sQuery(id+"F3.wireOp",EDGE,"E4.sketch_text.stroke-128"),sQuery(id+"F3.wireOp",EDGE,"E4.sketch_text.stroke-129"),sQuery(id+"F3.wireOp",EDGE,"E4.sketch_text.stroke-130"),sQuery(id+"F3.wireOp",EDGE,"E4.sketch_text.stroke-131"),sQuery(id+"F3.wireOp",EDGE,"E4.sketch_text.stroke-132"),sQuery(id+"F3.wireOp",EDGE,"E4.sketch_text.stroke-133"),sQuery(id+"F3.wireOp",EDGE,"E4.sketch_text.stroke-134"),sQuery(id+"F3.wireOp",EDGE,"E4.sketch_text.stroke-135"),sQuery(id+"F3.wireOp",EDGE,"E4.sketch_text.stroke-136"),sQuery(id+"F3.wireOp",EDGE,"E4.sketch_text.stroke-137"),sQuery(id+"F3.wireOp",EDGE,"E4.sketch_text.stroke-138"),sQuery(id+"F3.wireOp",EDGE,"E4.sketch_text.stroke-139"),sQuery(id+"F3.wireOp",EDGE,"E4.sketch_text.stroke-140"),sQuery(id+"F3.wireOp",EDGE,"E4.sketch_text.stroke-141"),sQuery(id+"F3.wireOp",EDGE,"E4.sketch_text.stroke-142"),sQuery(id+"F3.wireOp",EDGE,"E4.sketch_text.stroke-143"),sQuery(id+"F3.wireOp",EDGE,"E4.sketch_text.stroke-144"),sQuery(id+"F3.wireOp",EDGE,"E4.sketch_text.stroke-145"),sQuery(id+"F3.wireOp",EDGE,"E4.sketch_text.stroke-146"),sQuery(id+"F3.wireOp",EDGE,"E4.sketch_text.stroke-147"),sQuery(id+"F3.wireOp",EDGE,"E4.sketch_text.stroke-148"),sQuery(id+"F3.wireOp",EDGE,"E4.sketch_text.stroke-149"),sQuery(id+"F3.wireOp",EDGE,"E4.sketch_text.stroke-150"),sQuery(id+"F3.wireOp",EDGE,"E4.sketch_text.stroke-151"),sQuery(id+"F3.wireOp",EDGE,"E4.sketch_text.stroke-152"),sQuery(id+"F3.wireOp",EDGE,"E4.sketch_text.stroke-153"),sQuery(id+"F3.wireOp",EDGE,"E4.sketch_text.stroke-159"),sQuery(id+"F3.wireOp",EDGE,"E4.sketch_text.stroke-160"),sQuery(id+"F3.wireOp",EDGE,"E4.sketch_text.stroke-161"),sQuery(id+"F3.wireOp",EDGE,"E4.sketch_text.stroke-162"),sQuery(id+"F3.wireOp",EDGE,"E4.sketch_text.stroke-163"),sQuery(id+"F3.wireOp",EDGE,"E4.sketch_text.stroke-164"),sQuery(id+"F3.wireOp",EDGE,"E4.sketch_text.stroke-165"),sQuery(id+"F3.wireOp",EDGE,"E4.sketch_text.stroke-166"),sQuery(id+"F3.wireOp",EDGE,"E4.sketch_text.stroke-167"),sQuery(id+"F3.wireOp",EDGE,"E4.sketch_text.stroke-168"),sQuery(id+"F3.wireOp",EDGE,"E4.sketch_text.stroke-169"),sQuery(id+"F3.wireOp",EDGE,"E4.sketch_text.stroke-170"),sQuery(id+"F3.wireOp",EDGE,"E4.sketch_text.stroke-171"),sQuery(id+"F3.wireOp",EDGE,"E4.sketch_text.stroke-172"),sQuery(id+"F3.wireOp",EDGE,"E4.sketch_text.stroke-173"),sQuery(id+"F3.wireOp",EDGE,"E4.sketch_text.stroke-174"),sQuery(id+"F3.wireOp",EDGE,"E4.sketch_text.stroke-175"),sQuery(id+"F3.wireOp",EDGE,"E4.sketch_text.stroke-176"),sQuery(id+"F3.wireOp",EDGE,"E4.sketch_text.stroke-177"),sQuery(id+"F3.wireOp",EDGE,"E4.sketch_text.stroke-178"),sQuery(id+"F3.wireOp",EDGE,"E4.sketch_text.stroke-179"),sQuery(id+"F3.wireOp",EDGE,"E4.sketch_text.stroke-180"),sQuery(id+"F5.wireOp",EDGE,"E30"),subQ2])],"isStart":true}),makeQuery(id+"F6.opExtrude","SWEPT_FACE",FACE,{"disambiguationData":[OSD([subQ2])]})])],"derivedFrom":makeQuery(id+"F6.opExtrude","CAP_EDGE",EDGE,{"disambiguationData":[OSD([subQ2])],"isStart":true})});}
            var Q24;
            {var subQ0=sQuery(id+"F0.wireOp",EDGE,"E0.top");var subQ1=sQuery(id+"F0.wireOp",EDGE,"E0.bottom");var subQ2=sQuery(id+"F5.wireOp",EDGE,"E30");Q24=makeQuery(id+"F6.boolean.opBoolean","SPLIT",EDGE,{"disambiguationData":[TD([makeQuery(id+"F1.opExtrude","CAP_FACE",FACE,{"disambiguationData":[OSD([subQ1,subQ0,sQuery(id+"F0.wireOp",EDGE,"E0.left"),sQuery(id+"F0.wireOp",EDGE,"E0.right")])],"isStart":false}),makeQuery(id+"F1.opExtrude","SWEPT_FACE",FACE,{"disambiguationData":[OSD([subQ0])]}),makeQuery(id+"F6.opExtrude","SWEPT_FACE",FACE,{"disambiguationData":[OSD([subQ2])]}),makeQuery(id+"F6.opExtrude","CAP_FACE",FACE,{"disambiguationData":[OSD([subQ1,sQuery(id+"F2.wireOp",EDGE,"E2.sketch_text.stroke-0"),sQuery(id+"F2.wireOp",EDGE,"E2.sketch_text.stroke-1"),sQuery(id+"F2.wireOp",EDGE,"E2.sketch_text.stroke-2"),sQuery(id+"F2.wireOp",EDGE,"E2.sketch_text.stroke-3"),sQuery(id+"F2.wireOp",EDGE,"E2.sketch_text.stroke-4"),sQuery(id+"F2.wireOp",EDGE,"E2.sketch_text.stroke-5"),sQuery(id+"F2.wireOp",EDGE,"E2.sketch_text.stroke-6"),sQuery(id+"F2.wireOp",EDGE,"E2.sketch_text.stroke-7"),sQuery(id+"F2.wireOp",EDGE,"E2.sketch_text.stroke-8"),sQuery(id+"F2.wireOp",EDGE,"E2.sketch_text.stroke-9"),sQuery(id+"F2.wireOp",EDGE,"E2.sketch_text.stroke-10"),sQuery(id+"F2.wireOp",EDGE,"E2.sketch_text.stroke-11"),sQuery(id+"F2.wireOp",EDGE,"E2.sketch_text.stroke-12"),sQuery(id+"F2.wireOp",EDGE,"E2.sketch_text.stroke-13"),sQuery(id+"F2.wireOp",EDGE,"E2.sketch_text.stroke-14"),sQuery(id+"F2.wireOp",EDGE,"E2.sketch_text.stroke-15"),sQuery(id+"F2.wireOp",EDGE,"E2.sketch_text.stroke-16"),sQuery(id+"F2.wireOp",EDGE,"E2.sketch_text.stroke-17"),sQuery(id+"F2.wireOp",EDGE,"E2.sketch_text.stroke-18"),sQuery(id+"F2.wireOp",EDGE,"E2.sketch_text.stroke-19"),sQuery(id+"F2.wireOp",EDGE,"E2.sketch_text.stroke-20"),sQuery(id+"F2.wireOp",EDGE,"E2.sketch_text.stroke-21"),sQuery(id+"F2.wireOp",EDGE,"E2.sketch_text.stroke-22"),sQuery(id+"F2.wireOp",EDGE,"E2.sketch_text.stroke-23"),sQuery(id+"F2.wireOp",EDGE,"E2.sketch_text.stroke-24"),sQuery(id+"F2.wireOp",EDGE,"E2.sketch_text.stroke-25"),sQuery(id+"F2.wireOp",EDGE,"E2.sketch_text.stroke-26"),sQuery(id+"F2.wireOp",EDGE,"E2.sketch_text.stroke-27"),sQuery(id+"F2.wireOp",EDGE,"E2.sketch_text.stroke-28"),sQuery(id+"F2.wireOp",EDGE,"E2.sketch_text.stroke-29"),sQuery(id+"F2.wireOp",EDGE,"E2.sketch_text.stroke-30"),sQuery(id+"F2.wireOp",EDGE,"E2.sketch_text.stroke-31"),sQuery(id+"F2.wireOp",EDGE,"E2.sketch_text.stroke-32"),sQuery(id+"F2.wireOp",EDGE,"E2.sketch_text.stroke-33"),sQuery(id+"F2.wireOp",EDGE,"E2.sketch_text.stroke-34"),sQuery(id+"F2.wireOp",EDGE,"E2.sketch_text.stroke-35"),sQuery(id+"F2.wireOp",EDGE,"E2.sketch_text.stroke-36"),sQuery(id+"F2.wireOp",EDGE,"E2.sketch_text.stroke-37"),sQuery(id+"F2.wireOp",EDGE,"E2.sketch_text.stroke-38"),sQuery(id+"F2.wireOp",EDGE,"E2.sketch_text.stroke-39"),sQuery(id+"F2.wireOp",EDGE,"E2.sketch_text.stroke-40"),sQuery(id+"F2.wireOp",EDGE,"E2.sketch_text.stroke-41"),sQuery(id+"F2.wireOp",EDGE,"E2.sketch_text.stroke-42"),sQuery(id+"F2.wireOp",EDGE,"E2.sketch_text.stroke-43"),sQuery(id+"F2.wireOp",EDGE,"E2.sketch_text.stroke-44"),sQuery(id+"F2.wireOp",EDGE,"E2.sketch_text.stroke-45"),sQuery(id+"F2.wireOp",EDGE,"E2.sketch_text.stroke-46"),sQuery(id+"F2.wireOp",EDGE,"E2.sketch_text.stroke-47"),sQuery(id+"F2.wireOp",EDGE,"E2.sketch_text.stroke-48"),sQuery(id+"F2.wireOp",EDGE,"E2.sketch_text.stroke-49"),sQuery(id+"F2.wireOp",EDGE,"E2.sketch_text.stroke-50"),sQuery(id+"F2.wireOp",EDGE,"E2.sketch_text.stroke-51"),sQuery(id+"F2.wireOp",EDGE,"E2.sketch_text.stroke-52"),sQuery(id+"F2.wireOp",EDGE,"E2.sketch_text.stroke-53"),sQuery(id+"F2.wireOp",EDGE,"E2.sketch_text.stroke-54"),sQuery(id+"F2.wireOp",EDGE,"E2.sketch_text.stroke-55"),sQuery(id+"F2.wireOp",EDGE,"E2.sketch_text.stroke-56"),sQuery(id+"F2.wireOp",EDGE,"E2.sketch_text.stroke-57"),sQuery(id+"F2.wireOp",EDGE,"E2.sketch_text.stroke-58"),sQuery(id+"F2.wireOp",EDGE,"E2.sketch_text.stroke-59"),sQuery(id+"F2.wireOp",EDGE,"E2.sketch_text.stroke-60"),sQuery(id+"F2.wireOp",EDGE,"E2.sketch_text.stroke-61"),sQuery(id+"F2.wireOp",EDGE,"E2.sketch_text.stroke-62"),sQuery(id+"F2.wireOp",EDGE,"E2.sketch_text.stroke-63"),sQuery(id+"F2.wireOp",EDGE,"E2.sketch_text.stroke-64"),sQuery(id+"F2.wireOp",EDGE,"E2.sketch_text.stroke-65"),sQuery(id+"F2.wireOp",EDGE,"E2.sketch_text.stroke-66"),sQuery(id+"F2.wireOp",EDGE,"E2.sketch_text.stroke-67"),sQuery(id+"F2.wireOp",EDGE,"E2.sketch_text.stroke-68"),sQuery(id+"F2.wireOp",EDGE,"E2.sketch_text.stroke-69"),sQuery(id+"F2.wireOp",EDGE,"E2.sketch_text.stroke-70"),sQuery(id+"F2.wireOp",EDGE,"E2.sketch_text.stroke-71"),sQuery(id+"F2.wireOp",EDGE,"E2.sketch_text.stroke-72"),sQuery(id+"F2.wireOp",EDGE,"E2.sketch_text.stroke-73"),sQuery(id+"F2.wireOp",EDGE,"E2.sketch_text.stroke-74"),sQuery(id+"F2.wireOp",EDGE,"E2.sketch_text.stroke-75"),sQuery(id+"F2.wireOp",EDGE,"E2.sketch_text.stroke-76"),sQuery(id+"F2.wireOp",EDGE,"E2.sketch_text.stroke-77"),sQuery(id+"F2.wireOp",EDGE,"E2.sketch_text.stroke-78"),sQuery(id+"F2.wireOp",EDGE,"E2.sketch_text.stroke-79"),sQuery(id+"F2.wireOp",EDGE,"E2.sketch_text.stroke-80"),sQuery(id+"F2.wireOp",EDGE,"E2.sketch_text.stroke-81"),sQuery(id+"F2.wireOp",EDGE,"E2.sketch_text.stroke-82"),sQuery(id+"F2.wireOp",EDGE,"E2.sketch_text.stroke-83"),sQuery(id+"F2.wireOp",EDGE,"E2.sketch_text.stroke-84"),sQuery(id+"F2.wireOp",EDGE,"E2.sketch_text.stroke-85"),sQuery(id+"F2.wireOp",EDGE,"E2.sketch_text.stroke-86"),sQuery(id+"F2.wireOp",EDGE,"E2.sketch_text.stroke-87"),sQuery(id+"F2.wireOp",EDGE,"E2.sketch_text.stroke-88"),sQuery(id+"F2.wireOp",EDGE,"E2.sketch_text.stroke-89"),sQuery(id+"F2.wireOp",EDGE,"E2.sketch_text.stroke-90"),sQuery(id+"F2.wireOp",EDGE,"E2.sketch_text.stroke-91"),sQuery(id+"F2.wireOp",EDGE,"E2.sketch_text.stroke-92"),sQuery(id+"F2.wireOp",EDGE,"E2.sketch_text.stroke-93"),sQuery(id+"F2.wireOp",EDGE,"E2.sketch_text.stroke-94"),sQuery(id+"F2.wireOp",EDGE,"E2.sketch_text.stroke-95"),sQuery(id+"F2.wireOp",EDGE,"E2.sketch_text.stroke-96"),sQuery(id+"F2.wireOp",EDGE,"E2.sketch_text.stroke-97"),sQuery(id+"F2.wireOp",EDGE,"E2.sketch_text.stroke-98"),sQuery(id+"F2.wireOp",EDGE,"E2.sketch_text.stroke-99"),sQuery(id+"F2.wireOp",EDGE,"E2.sketch_text.stroke-100"),sQuery(id+"F2.wireOp",EDGE,"E2.sketch_text.stroke-101"),sQuery(id+"F2.wireOp",EDGE,"E2.sketch_text.stroke-102"),sQuery(id+"F2.wireOp",EDGE,"E2.sketch_text.stroke-103"),sQuery(id+"F2.wireOp",EDGE,"E2.sketch_text.stroke-104"),sQuery(id+"F2.wireOp",EDGE,"E2.sketch_text.stroke-105"),sQuery(id+"F2.wireOp",EDGE,"E2.sketch_text.stroke-106"),sQuery(id+"F2.wireOp",EDGE,"E2.sketch_text.stroke-107"),sQuery(id+"F2.wireOp",EDGE,"E2.sketch_text.stroke-108"),sQuery(id+"F2.wireOp",EDGE,"E2.sketch_text.stroke-109"),sQuery(id+"F2.wireOp",EDGE,"E2.sketch_text.stroke-110"),sQuery(id+"F2.wireOp",EDGE,"E2.sketch_text.stroke-111"),sQuery(id+"F2.wireOp",EDGE,"E2.sketch_text.stroke-112"),sQuery(id+"F2.wireOp",EDGE,"E2.sketch_text.stroke-113"),sQuery(id+"F2.wireOp",EDGE,"E2.sketch_text.stroke-114"),sQuery(id+"F2.wireOp",EDGE,"E2.sketch_text.stroke-115"),sQuery(id+"F2.wireOp",EDGE,"E2.sketch_text.stroke-116"),sQuery(id+"F2.wireOp",EDGE,"E2.sketch_text.stroke-117"),sQuery(id+"F2.wireOp",EDGE,"E2.sketch_text.stroke-118"),sQuery(id+"F2.wireOp",EDGE,"E2.sketch_text.stroke-119"),sQuery(id+"F2.wireOp",EDGE,"E2.sketch_text.stroke-120"),sQuery(id+"F2.wireOp",EDGE,"E2.sketch_text.stroke-121"),sQuery(id+"F2.wireOp",EDGE,"E2.sketch_text.stroke-122"),sQuery(id+"F2.wireOp",EDGE,"E2.sketch_text.stroke-123"),sQuery(id+"F2.wireOp",EDGE,"E2.sketch_text.stroke-124"),sQuery(id+"F2.wireOp",EDGE,"E2.sketch_text.stroke-125"),sQuery(id+"F2.wireOp",EDGE,"E2.sketch_text.stroke-126"),sQuery(id+"F2.wireOp",EDGE,"E2.sketch_text.stroke-127"),sQuery(id+"F2.wireOp",EDGE,"E2.sketch_text.stroke-128"),sQuery(id+"F2.wireOp",EDGE,"E2.sketch_text.stroke-129"),sQuery(id+"F2.wireOp",EDGE,"E2.sketch_text.stroke-130"),sQuery(id+"F2.wireOp",EDGE,"E2.sketch_text.stroke-131"),sQuery(id+"F2.wireOp",EDGE,"E2.sketch_text.stroke-132"),sQuery(id+"F2.wireOp",EDGE,"E2.sketch_text.stroke-133"),sQuery(id+"F2.wireOp",EDGE,"E2.sketch_text.stroke-134"),sQuery(id+"F2.wireOp",EDGE,"E2.sketch_text.stroke-135"),sQuery(id+"F2.wireOp",EDGE,"E2.sketch_text.stroke-136"),sQuery(id+"F2.wireOp",EDGE,"E2.sketch_text.stroke-137"),sQuery(id+"F2.wireOp",EDGE,"E2.sketch_text.stroke-138"),sQuery(id+"F2.wireOp",EDGE,"E2.sketch_text.stroke-139"),sQuery(id+"F2.wireOp",EDGE,"E2.sketch_text.stroke-140"),sQuery(id+"F2.wireOp",EDGE,"E2.sketch_text.stroke-141"),sQuery(id+"F2.wireOp",EDGE,"E2.sketch_text.stroke-142"),sQuery(id+"F2.wireOp",EDGE,"E2.sketch_text.stroke-143"),sQuery(id+"F2.wireOp",EDGE,"E2.sketch_text.stroke-144"),sQuery(id+"F2.wireOp",EDGE,"E2.sketch_text.stroke-145"),sQuery(id+"F2.wireOp",EDGE,"E2.sketch_text.stroke-146"),sQuery(id+"F2.wireOp",EDGE,"E2.sketch_text.stroke-147"),sQuery(id+"F2.wireOp",EDGE,"E2.sketch_text.stroke-148"),sQuery(id+"F2.wireOp",EDGE,"E2.sketch_text.stroke-149"),sQuery(id+"F2.wireOp",EDGE,"E2.sketch_text.stroke-150"),sQuery(id+"F2.wireOp",EDGE,"E2.sketch_text.stroke-151"),sQuery(id+"F2.wireOp",EDGE,"E2.sketch_text.stroke-152"),sQuery(id+"F2.wireOp",EDGE,"E2.sketch_text.stroke-153"),sQuery(id+"F2.wireOp",EDGE,"E2.sketch_text.stroke-154"),sQuery(id+"F2.wireOp",EDGE,"E2.sketch_text.stroke-155"),sQuery(id+"F2.wireOp",EDGE,"E2.sketch_text.stroke-156"),sQuery(id+"F2.wireOp",EDGE,"E2.sketch_text.stroke-157"),sQuery(id+"F2.wireOp",EDGE,"E2.sketch_text.stroke-158"),sQuery(id+"F2.wireOp",EDGE,"E2.sketch_text.stroke-159"),sQuery(id+"F2.wireOp",EDGE,"E2.sketch_text.stroke-160"),sQuery(id+"F2.wireOp",EDGE,"E2.sketch_text.stroke-161"),sQuery(id+"F2.wireOp",EDGE,"E2.sketch_text.stroke-162"),sQuery(id+"F2.wireOp",EDGE,"E2.sketch_text.stroke-163"),sQuery(id+"F2.wireOp",EDGE,"E2.sketch_text.stroke-164"),sQuery(id+"F2.wireOp",EDGE,"E2.sketch_text.stroke-165"),sQuery(id+"F2.wireOp",EDGE,"E2.sketch_text.stroke-166"),sQuery(id+"F2.wireOp",EDGE,"E2.sketch_text.stroke-167"),sQuery(id+"F2.wireOp",EDGE,"E2.sketch_text.stroke-168"),sQuery(id+"F2.wireOp",EDGE,"E2.sketch_text.stroke-169"),sQuery(id+"F2.wireOp",EDGE,"E2.sketch_text.stroke-170"),sQuery(id+"F2.wireOp",EDGE,"E2.sketch_text.stroke-171"),sQuery(id+"F2.wireOp",EDGE,"E2.sketch_text.stroke-172"),sQuery(id+"F2.wireOp",EDGE,"E2.sketch_text.stroke-173"),sQuery(id+"F3.wireOp",EDGE,"E4.sketch_text.stroke-0"),sQuery(id+"F3.wireOp",EDGE,"E4.sketch_text.stroke-1"),sQuery(id+"F3.wireOp",EDGE,"E4.sketch_text.stroke-2"),sQuery(id+"F3.wireOp",EDGE,"E4.sketch_text.stroke-3"),sQuery(id+"F3.wireOp",EDGE,"E4.sketch_text.stroke-4"),sQuery(id+"F3.wireOp",EDGE,"E4.sketch_text.stroke-5"),sQuery(id+"F3.wireOp",EDGE,"E4.sketch_text.stroke-6"),sQuery(id+"F3.wireOp",EDGE,"E4.sketch_text.stroke-7"),sQuery(id+"F3.wireOp",EDGE,"E4.sketch_text.stroke-8"),sQuery(id+"F3.wireOp",EDGE,"E4.sketch_text.stroke-9"),sQuery(id+"F3.wireOp",EDGE,"E4.sketch_text.stroke-10"),sQuery(id+"F3.wireOp",EDGE,"E4.sketch_text.stroke-11"),sQuery(id+"F3.wireOp",EDGE,"E4.sketch_text.stroke-12"),sQuery(id+"F3.wireOp",EDGE,"E4.sketch_text.stroke-13"),sQuery(id+"F3.wireOp",EDGE,"E4.sketch_text.stroke-14"),sQuery(id+"F3.wireOp",EDGE,"E4.sketch_text.stroke-15"),sQuery(id+"F3.wireOp",EDGE,"E4.sketch_text.stroke-16"),sQuery(id+"F3.wireOp",EDGE,"E4.sketch_text.stroke-17"),sQuery(id+"F3.wireOp",EDGE,"E4.sketch_text.stroke-18"),sQuery(id+"F3.wireOp",EDGE,"E4.sketch_text.stroke-19"),sQuery(id+"F3.wireOp",EDGE,"E4.sketch_text.stroke-20"),sQuery(id+"F3.wireOp",EDGE,"E4.sketch_text.stroke-21"),sQuery(id+"F3.wireOp",EDGE,"E4.sketch_text.stroke-22"),sQuery(id+"F3.wireOp",EDGE,"E4.sketch_text.stroke-23"),sQuery(id+"F3.wireOp",EDGE,"E4.sketch_text.stroke-24"),sQuery(id+"F3.wireOp",EDGE,"E4.sketch_text.stroke-25"),sQuery(id+"F3.wireOp",EDGE,"E4.sketch_text.stroke-26"),sQuery(id+"F3.wireOp",EDGE,"E4.sketch_text.stroke-27"),sQuery(id+"F3.wireOp",EDGE,"E4.sketch_text.stroke-28"),sQuery(id+"F3.wireOp",EDGE,"E4.sketch_text.stroke-29"),sQuery(id+"F3.wireOp",EDGE,"E4.sketch_text.stroke-30"),sQuery(id+"F3.wireOp",EDGE,"E4.sketch_text.stroke-31"),sQuery(id+"F3.wireOp",EDGE,"E4.sketch_text.stroke-32"),sQuery(id+"F3.wireOp",EDGE,"E4.sketch_text.stroke-33"),sQuery(id+"F3.wireOp",EDGE,"E4.sketch_text.stroke-34"),sQuery(id+"F3.wireOp",EDGE,"E4.sketch_text.stroke-35"),sQuery(id+"F3.wireOp",EDGE,"E4.sketch_text.stroke-36"),sQuery(id+"F3.wireOp",EDGE,"E4.sketch_text.stroke-37"),sQuery(id+"F3.wireOp",EDGE,"E4.sketch_text.stroke-38"),sQuery(id+"F3.wireOp",EDGE,"E4.sketch_text.stroke-39"),sQuery(id+"F3.wireOp",EDGE,"E4.sketch_text.stroke-40"),sQuery(id+"F3.wireOp",EDGE,"E4.sketch_text.stroke-41"),sQuery(id+"F3.wireOp",EDGE,"E4.sketch_text.stroke-42"),sQuery(id+"F3.wireOp",EDGE,"E4.sketch_text.stroke-43"),sQuery(id+"F3.wireOp",EDGE,"E4.sketch_text.stroke-44"),sQuery(id+"F3.wireOp",EDGE,"E4.sketch_text.stroke-45"),sQuery(id+"F3.wireOp",EDGE,"E4.sketch_text.stroke-46"),sQuery(id+"F3.wireOp",EDGE,"E4.sketch_text.stroke-47"),sQuery(id+"F3.wireOp",EDGE,"E4.sketch_text.stroke-48"),sQuery(id+"F3.wireOp",EDGE,"E4.sketch_text.stroke-49"),sQuery(id+"F3.wireOp",EDGE,"E4.sketch_text.stroke-50"),sQuery(id+"F3.wireOp",EDGE,"E4.sketch_text.stroke-51"),sQuery(id+"F3.wireOp",EDGE,"E4.sketch_text.stroke-52"),sQuery(id+"F3.wireOp",EDGE,"E4.sketch_text.stroke-53"),sQuery(id+"F3.wireOp",EDGE,"E4.sketch_text.stroke-54"),sQuery(id+"F3.wireOp",EDGE,"E4.sketch_text.stroke-55"),sQuery(id+"F3.wireOp",EDGE,"E4.sketch_text.stroke-56"),sQuery(id+"F3.wireOp",EDGE,"E4.sketch_text.stroke-57"),sQuery(id+"F3.wireOp",EDGE,"E4.sketch_text.stroke-58"),sQuery(id+"F3.wireOp",EDGE,"E4.sketch_text.stroke-59"),sQuery(id+"F3.wireOp",EDGE,"E4.sketch_text.stroke-60"),sQuery(id+"F3.wireOp",EDGE,"E4.sketch_text.stroke-61"),sQuery(id+"F3.wireOp",EDGE,"E4.sketch_text.stroke-62"),sQuery(id+"F3.wireOp",EDGE,"E4.sketch_text.stroke-71"),sQuery(id+"F3.wireOp",EDGE,"E4.sketch_text.stroke-72"),sQuery(id+"F3.wireOp",EDGE,"E4.sketch_text.stroke-73"),sQuery(id+"F3.wireOp",EDGE,"E4.sketch_text.stroke-74"),sQuery(id+"F3.wireOp",EDGE,"E4.sketch_text.stroke-75"),sQuery(id+"F3.wireOp",EDGE,"E4.sketch_text.stroke-76"),sQuery(id+"F3.wireOp",EDGE,"E4.sketch_text.stroke-77"),sQuery(id+"F3.wireOp",EDGE,"E4.sketch_text.stroke-78"),sQuery(id+"F3.wireOp",EDGE,"E4.sketch_text.stroke-79"),sQuery(id+"F3.wireOp",EDGE,"E4.sketch_text.stroke-80"),sQuery(id+"F3.wireOp",EDGE,"E4.sketch_text.stroke-81"),sQuery(id+"F3.wireOp",EDGE,"E4.sketch_text.stroke-82"),sQuery(id+"F3.wireOp",EDGE,"E4.sketch_text.stroke-83"),sQuery(id+"F3.wireOp",EDGE,"E4.sketch_text.stroke-84"),sQuery(id+"F3.wireOp",EDGE,"E4.sketch_text.stroke-85"),sQuery(id+"F3.wireOp",EDGE,"E4.sketch_text.stroke-86"),sQuery(id+"F3.wireOp",EDGE,"E4.sketch_text.stroke-87"),sQuery(id+"F3.wireOp",EDGE,"E4.sketch_text.stroke-88"),sQuery(id+"F3.wireOp",EDGE,"E4.sketch_text.stroke-89"),sQuery(id+"F3.wireOp",EDGE,"E4.sketch_text.stroke-90"),sQuery(id+"F3.wireOp",EDGE,"E4.sketch_text.stroke-91"),sQuery(id+"F3.wireOp",EDGE,"E4.sketch_text.stroke-92"),sQuery(id+"F3.wireOp",EDGE,"E4.sketch_text.stroke-93"),sQuery(id+"F3.wireOp",EDGE,"E4.sketch_text.stroke-94"),sQuery(id+"F3.wireOp",EDGE,"E4.sketch_text.stroke-95"),sQuery(id+"F3.wireOp",EDGE,"E4.sketch_text.stroke-96"),sQuery(id+"F3.wireOp",EDGE,"E4.sketch_text.stroke-97"),sQuery(id+"F3.wireOp",EDGE,"E4.sketch_text.stroke-103"),sQuery(id+"F3.wireOp",EDGE,"E4.sketch_text.stroke-104"),sQuery(id+"F3.wireOp",EDGE,"E4.sketch_text.stroke-105"),sQuery(id+"F3.wireOp",EDGE,"E4.sketch_text.stroke-106"),sQuery(id+"F3.wireOp",EDGE,"E4.sketch_text.stroke-107"),sQuery(id+"F3.wireOp",EDGE,"E4.sketch_text.stroke-108"),sQuery(id+"F3.wireOp",EDGE,"E4.sketch_text.stroke-109"),sQuery(id+"F3.wireOp",EDGE,"E4.sketch_text.stroke-110"),sQuery(id+"F3.wireOp",EDGE,"E4.sketch_text.stroke-111"),sQuery(id+"F3.wireOp",EDGE,"E4.sketch_text.stroke-112"),sQuery(id+"F3.wireOp",EDGE,"E4.sketch_text.stroke-113"),sQuery(id+"F3.wireOp",EDGE,"E4.sketch_text.stroke-114"),sQuery(id+"F3.wireOp",EDGE,"E4.sketch_text.stroke-115"),sQuery(id+"F3.wireOp",EDGE,"E4.sketch_text.stroke-116"),sQuery(id+"F3.wireOp",EDGE,"E4.sketch_text.stroke-117"),sQuery(id+"F3.wireOp",EDGE,"E4.sketch_text.stroke-118"),sQuery(id+"F3.wireOp",EDGE,"E4.sketch_text.stroke-119"),sQuery(id+"F3.wireOp",EDGE,"E4.sketch_text.stroke-120"),sQuery(id+"F3.wireOp",EDGE,"E4.sketch_text.stroke-121"),sQuery(id+"F3.wireOp",EDGE,"E4.sketch_text.stroke-122"),sQuery(id+"F3.wireOp",EDGE,"E4.sketch_text.stroke-123"),sQuery(id+"F3.wireOp",EDGE,"E4.sketch_text.stroke-124"),sQuery(id+"F3.wireOp",EDGE,"E4.sketch_text.stroke-125"),sQuery(id+"F3.wireOp",EDGE,"E4.sketch_text.stroke-126"),sQuery(id+"F3.wireOp",EDGE,"E4.sketch_text.stroke-127"),sQuery(id+"F3.wireOp",EDGE,"E4.sketch_text.stroke-128"),sQuery(id+"F3.wireOp",EDGE,"E4.sketch_text.stroke-129"),sQuery(id+"F3.wireOp",EDGE,"E4.sketch_text.stroke-130"),sQuery(id+"F3.wireOp",EDGE,"E4.sketch_text.stroke-131"),sQuery(id+"F3.wireOp",EDGE,"E4.sketch_text.stroke-132"),sQuery(id+"F3.wireOp",EDGE,"E4.sketch_text.stroke-133"),sQuery(id+"F3.wireOp",EDGE,"E4.sketch_text.stroke-134"),sQuery(id+"F3.wireOp",EDGE,"E4.sketch_text.stroke-135"),sQuery(id+"F3.wireOp",EDGE,"E4.sketch_text.stroke-136"),sQuery(id+"F3.wireOp",EDGE,"E4.sketch_text.stroke-137"),sQuery(id+"F3.wireOp",EDGE,"E4.sketch_text.stroke-138"),sQuery(id+"F3.wireOp",EDGE,"E4.sketch_text.stroke-139"),sQuery(id+"F3.wireOp",EDGE,"E4.sketch_text.stroke-140"),sQuery(id+"F3.wireOp",EDGE,"E4.sketch_text.stroke-141"),sQuery(id+"F3.wireOp",EDGE,"E4.sketch_text.stroke-142"),sQuery(id+"F3.wireOp",EDGE,"E4.sketch_text.stroke-143"),sQuery(id+"F3.wireOp",EDGE,"E4.sketch_text.stroke-144"),sQuery(id+"F3.wireOp",EDGE,"E4.sketch_text.stroke-145"),sQuery(id+"F3.wireOp",EDGE,"E4.sketch_text.stroke-146"),sQuery(id+"F3.wireOp",EDGE,"E4.sketch_text.stroke-147"),sQuery(id+"F3.wireOp",EDGE,"E4.sketch_text.stroke-148"),sQuery(id+"F3.wireOp",EDGE,"E4.sketch_text.stroke-149"),sQuery(id+"F3.wireOp",EDGE,"E4.sketch_text.stroke-150"),sQuery(id+"F3.wireOp",EDGE,"E4.sketch_text.stroke-151"),sQuery(id+"F3.wireOp",EDGE,"E4.sketch_text.stroke-152"),sQuery(id+"F3.wireOp",EDGE,"E4.sketch_text.stroke-153"),sQuery(id+"F3.wireOp",EDGE,"E4.sketch_text.stroke-159"),sQuery(id+"F3.wireOp",EDGE,"E4.sketch_text.stroke-160"),sQuery(id+"F3.wireOp",EDGE,"E4.sketch_text.stroke-161"),sQuery(id+"F3.wireOp",EDGE,"E4.sketch_text.stroke-162"),sQuery(id+"F3.wireOp",EDGE,"E4.sketch_text.stroke-163"),sQuery(id+"F3.wireOp",EDGE,"E4.sketch_text.stroke-164"),sQuery(id+"F3.wireOp",EDGE,"E4.sketch_text.stroke-165"),sQuery(id+"F3.wireOp",EDGE,"E4.sketch_text.stroke-166"),sQuery(id+"F3.wireOp",EDGE,"E4.sketch_text.stroke-167"),sQuery(id+"F3.wireOp",EDGE,"E4.sketch_text.stroke-168"),sQuery(id+"F3.wireOp",EDGE,"E4.sketch_text.stroke-169"),sQuery(id+"F3.wireOp",EDGE,"E4.sketch_text.stroke-170"),sQuery(id+"F3.wireOp",EDGE,"E4.sketch_text.stroke-171"),sQuery(id+"F3.wireOp",EDGE,"E4.sketch_text.stroke-172"),sQuery(id+"F3.wireOp",EDGE,"E4.sketch_text.stroke-173"),sQuery(id+"F3.wireOp",EDGE,"E4.sketch_text.stroke-174"),sQuery(id+"F3.wireOp",EDGE,"E4.sketch_text.stroke-175"),sQuery(id+"F3.wireOp",EDGE,"E4.sketch_text.stroke-176"),sQuery(id+"F3.wireOp",EDGE,"E4.sketch_text.stroke-177"),sQuery(id+"F3.wireOp",EDGE,"E4.sketch_text.stroke-178"),sQuery(id+"F3.wireOp",EDGE,"E4.sketch_text.stroke-179"),sQuery(id+"F3.wireOp",EDGE,"E4.sketch_text.stroke-180"),subQ2,sQuery(id+"F5.wireOp",EDGE,"E31")])],"isStart":true})]),OD(1.0)],"derivedFrom":makeQuery(id+"F1.opExtrude","CAP_EDGE",EDGE,{"disambiguationData":[OSD([subQ0])],"isStart":false})});}
            var Q25;
            {var subQ0=sQuery(id+"F0.wireOp",EDGE,"E0.top");var subQ1=sQuery(id+"F0.wireOp",EDGE,"E0.bottom");var subQ2=sQuery(id+"F5.wireOp",EDGE,"E30");Q25=makeQuery(id+"F6.boolean.opBoolean","SPLIT",EDGE,{"disambiguationData":[TD([makeQuery(id+"F1.opExtrude","CAP_FACE",FACE,{"disambiguationData":[OSD([subQ1,subQ0,sQuery(id+"F0.wireOp",EDGE,"E0.left"),sQuery(id+"F0.wireOp",EDGE,"E0.right")])],"isStart":false}),makeQuery(id+"F1.opExtrude","SWEPT_FACE",FACE,{"disambiguationData":[OSD([subQ0])]}),makeQuery(id+"F6.opExtrude","SWEPT_FACE",FACE,{"disambiguationData":[OSD([subQ2])]}),makeQuery(id+"F6.opExtrude","CAP_FACE",FACE,{"disambiguationData":[OSD([subQ1,sQuery(id+"F2.wireOp",EDGE,"E2.sketch_text.stroke-0"),sQuery(id+"F2.wireOp",EDGE,"E2.sketch_text.stroke-1"),sQuery(id+"F2.wireOp",EDGE,"E2.sketch_text.stroke-2"),sQuery(id+"F2.wireOp",EDGE,"E2.sketch_text.stroke-3"),sQuery(id+"F2.wireOp",EDGE,"E2.sketch_text.stroke-4"),sQuery(id+"F2.wireOp",EDGE,"E2.sketch_text.stroke-5"),sQuery(id+"F2.wireOp",EDGE,"E2.sketch_text.stroke-6"),sQuery(id+"F2.wireOp",EDGE,"E2.sketch_text.stroke-7"),sQuery(id+"F2.wireOp",EDGE,"E2.sketch_text.stroke-8"),sQuery(id+"F2.wireOp",EDGE,"E2.sketch_text.stroke-9"),sQuery(id+"F2.wireOp",EDGE,"E2.sketch_text.stroke-10"),sQuery(id+"F2.wireOp",EDGE,"E2.sketch_text.stroke-11"),sQuery(id+"F2.wireOp",EDGE,"E2.sketch_text.stroke-12"),sQuery(id+"F2.wireOp",EDGE,"E2.sketch_text.stroke-13"),sQuery(id+"F2.wireOp",EDGE,"E2.sketch_text.stroke-14"),sQuery(id+"F2.wireOp",EDGE,"E2.sketch_text.stroke-15"),sQuery(id+"F2.wireOp",EDGE,"E2.sketch_text.stroke-16"),sQuery(id+"F2.wireOp",EDGE,"E2.sketch_text.stroke-17"),sQuery(id+"F2.wireOp",EDGE,"E2.sketch_text.stroke-18"),sQuery(id+"F2.wireOp",EDGE,"E2.sketch_text.stroke-19"),sQuery(id+"F2.wireOp",EDGE,"E2.sketch_text.stroke-20"),sQuery(id+"F2.wireOp",EDGE,"E2.sketch_text.stroke-21"),sQuery(id+"F2.wireOp",EDGE,"E2.sketch_text.stroke-22"),sQuery(id+"F2.wireOp",EDGE,"E2.sketch_text.stroke-23"),sQuery(id+"F2.wireOp",EDGE,"E2.sketch_text.stroke-24"),sQuery(id+"F2.wireOp",EDGE,"E2.sketch_text.stroke-25"),sQuery(id+"F2.wireOp",EDGE,"E2.sketch_text.stroke-26"),sQuery(id+"F2.wireOp",EDGE,"E2.sketch_text.stroke-27"),sQuery(id+"F2.wireOp",EDGE,"E2.sketch_text.stroke-28"),sQuery(id+"F2.wireOp",EDGE,"E2.sketch_text.stroke-29"),sQuery(id+"F2.wireOp",EDGE,"E2.sketch_text.stroke-30"),sQuery(id+"F2.wireOp",EDGE,"E2.sketch_text.stroke-31"),sQuery(id+"F2.wireOp",EDGE,"E2.sketch_text.stroke-32"),sQuery(id+"F2.wireOp",EDGE,"E2.sketch_text.stroke-33"),sQuery(id+"F2.wireOp",EDGE,"E2.sketch_text.stroke-34"),sQuery(id+"F2.wireOp",EDGE,"E2.sketch_text.stroke-35"),sQuery(id+"F2.wireOp",EDGE,"E2.sketch_text.stroke-36"),sQuery(id+"F2.wireOp",EDGE,"E2.sketch_text.stroke-37"),sQuery(id+"F2.wireOp",EDGE,"E2.sketch_text.stroke-38"),sQuery(id+"F2.wireOp",EDGE,"E2.sketch_text.stroke-39"),sQuery(id+"F2.wireOp",EDGE,"E2.sketch_text.stroke-40"),sQuery(id+"F2.wireOp",EDGE,"E2.sketch_text.stroke-41"),sQuery(id+"F2.wireOp",EDGE,"E2.sketch_text.stroke-42"),sQuery(id+"F2.wireOp",EDGE,"E2.sketch_text.stroke-43"),sQuery(id+"F2.wireOp",EDGE,"E2.sketch_text.stroke-44"),sQuery(id+"F2.wireOp",EDGE,"E2.sketch_text.stroke-45"),sQuery(id+"F2.wireOp",EDGE,"E2.sketch_text.stroke-46"),sQuery(id+"F2.wireOp",EDGE,"E2.sketch_text.stroke-47"),sQuery(id+"F2.wireOp",EDGE,"E2.sketch_text.stroke-48"),sQuery(id+"F2.wireOp",EDGE,"E2.sketch_text.stroke-49"),sQuery(id+"F2.wireOp",EDGE,"E2.sketch_text.stroke-50"),sQuery(id+"F2.wireOp",EDGE,"E2.sketch_text.stroke-51"),sQuery(id+"F2.wireOp",EDGE,"E2.sketch_text.stroke-52"),sQuery(id+"F2.wireOp",EDGE,"E2.sketch_text.stroke-53"),sQuery(id+"F2.wireOp",EDGE,"E2.sketch_text.stroke-54"),sQuery(id+"F2.wireOp",EDGE,"E2.sketch_text.stroke-55"),sQuery(id+"F2.wireOp",EDGE,"E2.sketch_text.stroke-56"),sQuery(id+"F2.wireOp",EDGE,"E2.sketch_text.stroke-57"),sQuery(id+"F2.wireOp",EDGE,"E2.sketch_text.stroke-58"),sQuery(id+"F2.wireOp",EDGE,"E2.sketch_text.stroke-59"),sQuery(id+"F2.wireOp",EDGE,"E2.sketch_text.stroke-60"),sQuery(id+"F2.wireOp",EDGE,"E2.sketch_text.stroke-61"),sQuery(id+"F2.wireOp",EDGE,"E2.sketch_text.stroke-62"),sQuery(id+"F2.wireOp",EDGE,"E2.sketch_text.stroke-63"),sQuery(id+"F2.wireOp",EDGE,"E2.sketch_text.stroke-64"),sQuery(id+"F2.wireOp",EDGE,"E2.sketch_text.stroke-65"),sQuery(id+"F2.wireOp",EDGE,"E2.sketch_text.stroke-66"),sQuery(id+"F2.wireOp",EDGE,"E2.sketch_text.stroke-67"),sQuery(id+"F2.wireOp",EDGE,"E2.sketch_text.stroke-68"),sQuery(id+"F2.wireOp",EDGE,"E2.sketch_text.stroke-69"),sQuery(id+"F2.wireOp",EDGE,"E2.sketch_text.stroke-70"),sQuery(id+"F2.wireOp",EDGE,"E2.sketch_text.stroke-71"),sQuery(id+"F2.wireOp",EDGE,"E2.sketch_text.stroke-72"),sQuery(id+"F2.wireOp",EDGE,"E2.sketch_text.stroke-73"),sQuery(id+"F2.wireOp",EDGE,"E2.sketch_text.stroke-74"),sQuery(id+"F2.wireOp",EDGE,"E2.sketch_text.stroke-75"),sQuery(id+"F2.wireOp",EDGE,"E2.sketch_text.stroke-76"),sQuery(id+"F2.wireOp",EDGE,"E2.sketch_text.stroke-77"),sQuery(id+"F2.wireOp",EDGE,"E2.sketch_text.stroke-78"),sQuery(id+"F2.wireOp",EDGE,"E2.sketch_text.stroke-79"),sQuery(id+"F2.wireOp",EDGE,"E2.sketch_text.stroke-80"),sQuery(id+"F2.wireOp",EDGE,"E2.sketch_text.stroke-81"),sQuery(id+"F2.wireOp",EDGE,"E2.sketch_text.stroke-82"),sQuery(id+"F2.wireOp",EDGE,"E2.sketch_text.stroke-83"),sQuery(id+"F2.wireOp",EDGE,"E2.sketch_text.stroke-84"),sQuery(id+"F2.wireOp",EDGE,"E2.sketch_text.stroke-85"),sQuery(id+"F2.wireOp",EDGE,"E2.sketch_text.stroke-86"),sQuery(id+"F2.wireOp",EDGE,"E2.sketch_text.stroke-87"),sQuery(id+"F2.wireOp",EDGE,"E2.sketch_text.stroke-88"),sQuery(id+"F2.wireOp",EDGE,"E2.sketch_text.stroke-89"),sQuery(id+"F2.wireOp",EDGE,"E2.sketch_text.stroke-90"),sQuery(id+"F2.wireOp",EDGE,"E2.sketch_text.stroke-91"),sQuery(id+"F2.wireOp",EDGE,"E2.sketch_text.stroke-92"),sQuery(id+"F2.wireOp",EDGE,"E2.sketch_text.stroke-93"),sQuery(id+"F2.wireOp",EDGE,"E2.sketch_text.stroke-94"),sQuery(id+"F2.wireOp",EDGE,"E2.sketch_text.stroke-95"),sQuery(id+"F2.wireOp",EDGE,"E2.sketch_text.stroke-96"),sQuery(id+"F2.wireOp",EDGE,"E2.sketch_text.stroke-97"),sQuery(id+"F2.wireOp",EDGE,"E2.sketch_text.stroke-98"),sQuery(id+"F2.wireOp",EDGE,"E2.sketch_text.stroke-99"),sQuery(id+"F2.wireOp",EDGE,"E2.sketch_text.stroke-100"),sQuery(id+"F2.wireOp",EDGE,"E2.sketch_text.stroke-101"),sQuery(id+"F2.wireOp",EDGE,"E2.sketch_text.stroke-102"),sQuery(id+"F2.wireOp",EDGE,"E2.sketch_text.stroke-103"),sQuery(id+"F2.wireOp",EDGE,"E2.sketch_text.stroke-104"),sQuery(id+"F2.wireOp",EDGE,"E2.sketch_text.stroke-105"),sQuery(id+"F2.wireOp",EDGE,"E2.sketch_text.stroke-106"),sQuery(id+"F2.wireOp",EDGE,"E2.sketch_text.stroke-107"),sQuery(id+"F2.wireOp",EDGE,"E2.sketch_text.stroke-108"),sQuery(id+"F2.wireOp",EDGE,"E2.sketch_text.stroke-109"),sQuery(id+"F2.wireOp",EDGE,"E2.sketch_text.stroke-110"),sQuery(id+"F2.wireOp",EDGE,"E2.sketch_text.stroke-111"),sQuery(id+"F2.wireOp",EDGE,"E2.sketch_text.stroke-112"),sQuery(id+"F2.wireOp",EDGE,"E2.sketch_text.stroke-113"),sQuery(id+"F2.wireOp",EDGE,"E2.sketch_text.stroke-114"),sQuery(id+"F2.wireOp",EDGE,"E2.sketch_text.stroke-115"),sQuery(id+"F2.wireOp",EDGE,"E2.sketch_text.stroke-116"),sQuery(id+"F2.wireOp",EDGE,"E2.sketch_text.stroke-117"),sQuery(id+"F2.wireOp",EDGE,"E2.sketch_text.stroke-118"),sQuery(id+"F2.wireOp",EDGE,"E2.sketch_text.stroke-119"),sQuery(id+"F2.wireOp",EDGE,"E2.sketch_text.stroke-120"),sQuery(id+"F2.wireOp",EDGE,"E2.sketch_text.stroke-121"),sQuery(id+"F2.wireOp",EDGE,"E2.sketch_text.stroke-122"),sQuery(id+"F2.wireOp",EDGE,"E2.sketch_text.stroke-123"),sQuery(id+"F2.wireOp",EDGE,"E2.sketch_text.stroke-124"),sQuery(id+"F2.wireOp",EDGE,"E2.sketch_text.stroke-125"),sQuery(id+"F2.wireOp",EDGE,"E2.sketch_text.stroke-126"),sQuery(id+"F2.wireOp",EDGE,"E2.sketch_text.stroke-127"),sQuery(id+"F2.wireOp",EDGE,"E2.sketch_text.stroke-128"),sQuery(id+"F2.wireOp",EDGE,"E2.sketch_text.stroke-129"),sQuery(id+"F2.wireOp",EDGE,"E2.sketch_text.stroke-130"),sQuery(id+"F2.wireOp",EDGE,"E2.sketch_text.stroke-131"),sQuery(id+"F2.wireOp",EDGE,"E2.sketch_text.stroke-132"),sQuery(id+"F2.wireOp",EDGE,"E2.sketch_text.stroke-133"),sQuery(id+"F2.wireOp",EDGE,"E2.sketch_text.stroke-134"),sQuery(id+"F2.wireOp",EDGE,"E2.sketch_text.stroke-135"),sQuery(id+"F2.wireOp",EDGE,"E2.sketch_text.stroke-136"),sQuery(id+"F2.wireOp",EDGE,"E2.sketch_text.stroke-137"),sQuery(id+"F2.wireOp",EDGE,"E2.sketch_text.stroke-138"),sQuery(id+"F2.wireOp",EDGE,"E2.sketch_text.stroke-139"),sQuery(id+"F2.wireOp",EDGE,"E2.sketch_text.stroke-140"),sQuery(id+"F2.wireOp",EDGE,"E2.sketch_text.stroke-141"),sQuery(id+"F2.wireOp",EDGE,"E2.sketch_text.stroke-142"),sQuery(id+"F2.wireOp",EDGE,"E2.sketch_text.stroke-143"),sQuery(id+"F2.wireOp",EDGE,"E2.sketch_text.stroke-144"),sQuery(id+"F2.wireOp",EDGE,"E2.sketch_text.stroke-145"),sQuery(id+"F2.wireOp",EDGE,"E2.sketch_text.stroke-146"),sQuery(id+"F2.wireOp",EDGE,"E2.sketch_text.stroke-147"),sQuery(id+"F2.wireOp",EDGE,"E2.sketch_text.stroke-148"),sQuery(id+"F2.wireOp",EDGE,"E2.sketch_text.stroke-149"),sQuery(id+"F2.wireOp",EDGE,"E2.sketch_text.stroke-150"),sQuery(id+"F2.wireOp",EDGE,"E2.sketch_text.stroke-151"),sQuery(id+"F2.wireOp",EDGE,"E2.sketch_text.stroke-152"),sQuery(id+"F2.wireOp",EDGE,"E2.sketch_text.stroke-153"),sQuery(id+"F2.wireOp",EDGE,"E2.sketch_text.stroke-154"),sQuery(id+"F2.wireOp",EDGE,"E2.sketch_text.stroke-155"),sQuery(id+"F2.wireOp",EDGE,"E2.sketch_text.stroke-156"),sQuery(id+"F2.wireOp",EDGE,"E2.sketch_text.stroke-157"),sQuery(id+"F2.wireOp",EDGE,"E2.sketch_text.stroke-158"),sQuery(id+"F2.wireOp",EDGE,"E2.sketch_text.stroke-159"),sQuery(id+"F2.wireOp",EDGE,"E2.sketch_text.stroke-160"),sQuery(id+"F2.wireOp",EDGE,"E2.sketch_text.stroke-161"),sQuery(id+"F2.wireOp",EDGE,"E2.sketch_text.stroke-162"),sQuery(id+"F2.wireOp",EDGE,"E2.sketch_text.stroke-163"),sQuery(id+"F2.wireOp",EDGE,"E2.sketch_text.stroke-164"),sQuery(id+"F2.wireOp",EDGE,"E2.sketch_text.stroke-165"),sQuery(id+"F2.wireOp",EDGE,"E2.sketch_text.stroke-166"),sQuery(id+"F2.wireOp",EDGE,"E2.sketch_text.stroke-167"),sQuery(id+"F2.wireOp",EDGE,"E2.sketch_text.stroke-168"),sQuery(id+"F2.wireOp",EDGE,"E2.sketch_text.stroke-169"),sQuery(id+"F2.wireOp",EDGE,"E2.sketch_text.stroke-170"),sQuery(id+"F2.wireOp",EDGE,"E2.sketch_text.stroke-171"),sQuery(id+"F2.wireOp",EDGE,"E2.sketch_text.stroke-172"),sQuery(id+"F2.wireOp",EDGE,"E2.sketch_text.stroke-173"),sQuery(id+"F3.wireOp",EDGE,"E4.sketch_text.stroke-0"),sQuery(id+"F3.wireOp",EDGE,"E4.sketch_text.stroke-1"),sQuery(id+"F3.wireOp",EDGE,"E4.sketch_text.stroke-2"),sQuery(id+"F3.wireOp",EDGE,"E4.sketch_text.stroke-3"),sQuery(id+"F3.wireOp",EDGE,"E4.sketch_text.stroke-4"),sQuery(id+"F3.wireOp",EDGE,"E4.sketch_text.stroke-5"),sQuery(id+"F3.wireOp",EDGE,"E4.sketch_text.stroke-6"),sQuery(id+"F3.wireOp",EDGE,"E4.sketch_text.stroke-7"),sQuery(id+"F3.wireOp",EDGE,"E4.sketch_text.stroke-8"),sQuery(id+"F3.wireOp",EDGE,"E4.sketch_text.stroke-9"),sQuery(id+"F3.wireOp",EDGE,"E4.sketch_text.stroke-10"),sQuery(id+"F3.wireOp",EDGE,"E4.sketch_text.stroke-11"),sQuery(id+"F3.wireOp",EDGE,"E4.sketch_text.stroke-12"),sQuery(id+"F3.wireOp",EDGE,"E4.sketch_text.stroke-13"),sQuery(id+"F3.wireOp",EDGE,"E4.sketch_text.stroke-14"),sQuery(id+"F3.wireOp",EDGE,"E4.sketch_text.stroke-15"),sQuery(id+"F3.wireOp",EDGE,"E4.sketch_text.stroke-16"),sQuery(id+"F3.wireOp",EDGE,"E4.sketch_text.stroke-17"),sQuery(id+"F3.wireOp",EDGE,"E4.sketch_text.stroke-18"),sQuery(id+"F3.wireOp",EDGE,"E4.sketch_text.stroke-19"),sQuery(id+"F3.wireOp",EDGE,"E4.sketch_text.stroke-20"),sQuery(id+"F3.wireOp",EDGE,"E4.sketch_text.stroke-21"),sQuery(id+"F3.wireOp",EDGE,"E4.sketch_text.stroke-22"),sQuery(id+"F3.wireOp",EDGE,"E4.sketch_text.stroke-23"),sQuery(id+"F3.wireOp",EDGE,"E4.sketch_text.stroke-24"),sQuery(id+"F3.wireOp",EDGE,"E4.sketch_text.stroke-25"),sQuery(id+"F3.wireOp",EDGE,"E4.sketch_text.stroke-26"),sQuery(id+"F3.wireOp",EDGE,"E4.sketch_text.stroke-27"),sQuery(id+"F3.wireOp",EDGE,"E4.sketch_text.stroke-28"),sQuery(id+"F3.wireOp",EDGE,"E4.sketch_text.stroke-29"),sQuery(id+"F3.wireOp",EDGE,"E4.sketch_text.stroke-30"),sQuery(id+"F3.wireOp",EDGE,"E4.sketch_text.stroke-31"),sQuery(id+"F3.wireOp",EDGE,"E4.sketch_text.stroke-32"),sQuery(id+"F3.wireOp",EDGE,"E4.sketch_text.stroke-33"),sQuery(id+"F3.wireOp",EDGE,"E4.sketch_text.stroke-34"),sQuery(id+"F3.wireOp",EDGE,"E4.sketch_text.stroke-35"),sQuery(id+"F3.wireOp",EDGE,"E4.sketch_text.stroke-36"),sQuery(id+"F3.wireOp",EDGE,"E4.sketch_text.stroke-37"),sQuery(id+"F3.wireOp",EDGE,"E4.sketch_text.stroke-38"),sQuery(id+"F3.wireOp",EDGE,"E4.sketch_text.stroke-39"),sQuery(id+"F3.wireOp",EDGE,"E4.sketch_text.stroke-40"),sQuery(id+"F3.wireOp",EDGE,"E4.sketch_text.stroke-41"),sQuery(id+"F3.wireOp",EDGE,"E4.sketch_text.stroke-42"),sQuery(id+"F3.wireOp",EDGE,"E4.sketch_text.stroke-43"),sQuery(id+"F3.wireOp",EDGE,"E4.sketch_text.stroke-44"),sQuery(id+"F3.wireOp",EDGE,"E4.sketch_text.stroke-45"),sQuery(id+"F3.wireOp",EDGE,"E4.sketch_text.stroke-46"),sQuery(id+"F3.wireOp",EDGE,"E4.sketch_text.stroke-47"),sQuery(id+"F3.wireOp",EDGE,"E4.sketch_text.stroke-48"),sQuery(id+"F3.wireOp",EDGE,"E4.sketch_text.stroke-49"),sQuery(id+"F3.wireOp",EDGE,"E4.sketch_text.stroke-50"),sQuery(id+"F3.wireOp",EDGE,"E4.sketch_text.stroke-51"),sQuery(id+"F3.wireOp",EDGE,"E4.sketch_text.stroke-52"),sQuery(id+"F3.wireOp",EDGE,"E4.sketch_text.stroke-53"),sQuery(id+"F3.wireOp",EDGE,"E4.sketch_text.stroke-54"),sQuery(id+"F3.wireOp",EDGE,"E4.sketch_text.stroke-55"),sQuery(id+"F3.wireOp",EDGE,"E4.sketch_text.stroke-56"),sQuery(id+"F3.wireOp",EDGE,"E4.sketch_text.stroke-57"),sQuery(id+"F3.wireOp",EDGE,"E4.sketch_text.stroke-58"),sQuery(id+"F3.wireOp",EDGE,"E4.sketch_text.stroke-59"),sQuery(id+"F3.wireOp",EDGE,"E4.sketch_text.stroke-60"),sQuery(id+"F3.wireOp",EDGE,"E4.sketch_text.stroke-61"),sQuery(id+"F3.wireOp",EDGE,"E4.sketch_text.stroke-62"),sQuery(id+"F3.wireOp",EDGE,"E4.sketch_text.stroke-71"),sQuery(id+"F3.wireOp",EDGE,"E4.sketch_text.stroke-72"),sQuery(id+"F3.wireOp",EDGE,"E4.sketch_text.stroke-73"),sQuery(id+"F3.wireOp",EDGE,"E4.sketch_text.stroke-74"),sQuery(id+"F3.wireOp",EDGE,"E4.sketch_text.stroke-75"),sQuery(id+"F3.wireOp",EDGE,"E4.sketch_text.stroke-76"),sQuery(id+"F3.wireOp",EDGE,"E4.sketch_text.stroke-77"),sQuery(id+"F3.wireOp",EDGE,"E4.sketch_text.stroke-78"),sQuery(id+"F3.wireOp",EDGE,"E4.sketch_text.stroke-79"),sQuery(id+"F3.wireOp",EDGE,"E4.sketch_text.stroke-80"),sQuery(id+"F3.wireOp",EDGE,"E4.sketch_text.stroke-81"),sQuery(id+"F3.wireOp",EDGE,"E4.sketch_text.stroke-82"),sQuery(id+"F3.wireOp",EDGE,"E4.sketch_text.stroke-83"),sQuery(id+"F3.wireOp",EDGE,"E4.sketch_text.stroke-84"),sQuery(id+"F3.wireOp",EDGE,"E4.sketch_text.stroke-85"),sQuery(id+"F3.wireOp",EDGE,"E4.sketch_text.stroke-86"),sQuery(id+"F3.wireOp",EDGE,"E4.sketch_text.stroke-87"),sQuery(id+"F3.wireOp",EDGE,"E4.sketch_text.stroke-88"),sQuery(id+"F3.wireOp",EDGE,"E4.sketch_text.stroke-89"),sQuery(id+"F3.wireOp",EDGE,"E4.sketch_text.stroke-90"),sQuery(id+"F3.wireOp",EDGE,"E4.sketch_text.stroke-91"),sQuery(id+"F3.wireOp",EDGE,"E4.sketch_text.stroke-92"),sQuery(id+"F3.wireOp",EDGE,"E4.sketch_text.stroke-93"),sQuery(id+"F3.wireOp",EDGE,"E4.sketch_text.stroke-94"),sQuery(id+"F3.wireOp",EDGE,"E4.sketch_text.stroke-95"),sQuery(id+"F3.wireOp",EDGE,"E4.sketch_text.stroke-96"),sQuery(id+"F3.wireOp",EDGE,"E4.sketch_text.stroke-97"),sQuery(id+"F3.wireOp",EDGE,"E4.sketch_text.stroke-103"),sQuery(id+"F3.wireOp",EDGE,"E4.sketch_text.stroke-104"),sQuery(id+"F3.wireOp",EDGE,"E4.sketch_text.stroke-105"),sQuery(id+"F3.wireOp",EDGE,"E4.sketch_text.stroke-106"),sQuery(id+"F3.wireOp",EDGE,"E4.sketch_text.stroke-107"),sQuery(id+"F3.wireOp",EDGE,"E4.sketch_text.stroke-108"),sQuery(id+"F3.wireOp",EDGE,"E4.sketch_text.stroke-109"),sQuery(id+"F3.wireOp",EDGE,"E4.sketch_text.stroke-110"),sQuery(id+"F3.wireOp",EDGE,"E4.sketch_text.stroke-111"),sQuery(id+"F3.wireOp",EDGE,"E4.sketch_text.stroke-112"),sQuery(id+"F3.wireOp",EDGE,"E4.sketch_text.stroke-113"),sQuery(id+"F3.wireOp",EDGE,"E4.sketch_text.stroke-114"),sQuery(id+"F3.wireOp",EDGE,"E4.sketch_text.stroke-115"),sQuery(id+"F3.wireOp",EDGE,"E4.sketch_text.stroke-116"),sQuery(id+"F3.wireOp",EDGE,"E4.sketch_text.stroke-117"),sQuery(id+"F3.wireOp",EDGE,"E4.sketch_text.stroke-118"),sQuery(id+"F3.wireOp",EDGE,"E4.sketch_text.stroke-119"),sQuery(id+"F3.wireOp",EDGE,"E4.sketch_text.stroke-120"),sQuery(id+"F3.wireOp",EDGE,"E4.sketch_text.stroke-121"),sQuery(id+"F3.wireOp",EDGE,"E4.sketch_text.stroke-122"),sQuery(id+"F3.wireOp",EDGE,"E4.sketch_text.stroke-123"),sQuery(id+"F3.wireOp",EDGE,"E4.sketch_text.stroke-124"),sQuery(id+"F3.wireOp",EDGE,"E4.sketch_text.stroke-125"),sQuery(id+"F3.wireOp",EDGE,"E4.sketch_text.stroke-126"),sQuery(id+"F3.wireOp",EDGE,"E4.sketch_text.stroke-127"),sQuery(id+"F3.wireOp",EDGE,"E4.sketch_text.stroke-128"),sQuery(id+"F3.wireOp",EDGE,"E4.sketch_text.stroke-129"),sQuery(id+"F3.wireOp",EDGE,"E4.sketch_text.stroke-130"),sQuery(id+"F3.wireOp",EDGE,"E4.sketch_text.stroke-131"),sQuery(id+"F3.wireOp",EDGE,"E4.sketch_text.stroke-132"),sQuery(id+"F3.wireOp",EDGE,"E4.sketch_text.stroke-133"),sQuery(id+"F3.wireOp",EDGE,"E4.sketch_text.stroke-134"),sQuery(id+"F3.wireOp",EDGE,"E4.sketch_text.stroke-135"),sQuery(id+"F3.wireOp",EDGE,"E4.sketch_text.stroke-136"),sQuery(id+"F3.wireOp",EDGE,"E4.sketch_text.stroke-137"),sQuery(id+"F3.wireOp",EDGE,"E4.sketch_text.stroke-138"),sQuery(id+"F3.wireOp",EDGE,"E4.sketch_text.stroke-139"),sQuery(id+"F3.wireOp",EDGE,"E4.sketch_text.stroke-140"),sQuery(id+"F3.wireOp",EDGE,"E4.sketch_text.stroke-141"),sQuery(id+"F3.wireOp",EDGE,"E4.sketch_text.stroke-142"),sQuery(id+"F3.wireOp",EDGE,"E4.sketch_text.stroke-143"),sQuery(id+"F3.wireOp",EDGE,"E4.sketch_text.stroke-144"),sQuery(id+"F3.wireOp",EDGE,"E4.sketch_text.stroke-145"),sQuery(id+"F3.wireOp",EDGE,"E4.sketch_text.stroke-146"),sQuery(id+"F3.wireOp",EDGE,"E4.sketch_text.stroke-147"),sQuery(id+"F3.wireOp",EDGE,"E4.sketch_text.stroke-148"),sQuery(id+"F3.wireOp",EDGE,"E4.sketch_text.stroke-149"),sQuery(id+"F3.wireOp",EDGE,"E4.sketch_text.stroke-150"),sQuery(id+"F3.wireOp",EDGE,"E4.sketch_text.stroke-151"),sQuery(id+"F3.wireOp",EDGE,"E4.sketch_text.stroke-152"),sQuery(id+"F3.wireOp",EDGE,"E4.sketch_text.stroke-153"),sQuery(id+"F3.wireOp",EDGE,"E4.sketch_text.stroke-159"),sQuery(id+"F3.wireOp",EDGE,"E4.sketch_text.stroke-160"),sQuery(id+"F3.wireOp",EDGE,"E4.sketch_text.stroke-161"),sQuery(id+"F3.wireOp",EDGE,"E4.sketch_text.stroke-162"),sQuery(id+"F3.wireOp",EDGE,"E4.sketch_text.stroke-163"),sQuery(id+"F3.wireOp",EDGE,"E4.sketch_text.stroke-164"),sQuery(id+"F3.wireOp",EDGE,"E4.sketch_text.stroke-165"),sQuery(id+"F3.wireOp",EDGE,"E4.sketch_text.stroke-166"),sQuery(id+"F3.wireOp",EDGE,"E4.sketch_text.stroke-167"),sQuery(id+"F3.wireOp",EDGE,"E4.sketch_text.stroke-168"),sQuery(id+"F3.wireOp",EDGE,"E4.sketch_text.stroke-169"),sQuery(id+"F3.wireOp",EDGE,"E4.sketch_text.stroke-170"),sQuery(id+"F3.wireOp",EDGE,"E4.sketch_text.stroke-171"),sQuery(id+"F3.wireOp",EDGE,"E4.sketch_text.stroke-172"),sQuery(id+"F3.wireOp",EDGE,"E4.sketch_text.stroke-173"),sQuery(id+"F3.wireOp",EDGE,"E4.sketch_text.stroke-174"),sQuery(id+"F3.wireOp",EDGE,"E4.sketch_text.stroke-175"),sQuery(id+"F3.wireOp",EDGE,"E4.sketch_text.stroke-176"),sQuery(id+"F3.wireOp",EDGE,"E4.sketch_text.stroke-177"),sQuery(id+"F3.wireOp",EDGE,"E4.sketch_text.stroke-178"),sQuery(id+"F3.wireOp",EDGE,"E4.sketch_text.stroke-179"),sQuery(id+"F3.wireOp",EDGE,"E4.sketch_text.stroke-180"),subQ2,sQuery(id+"F5.wireOp",EDGE,"E31")])],"isStart":true})]),OD(0.0)],"derivedFrom":makeQuery(id+"F1.opExtrude","CAP_EDGE",EDGE,{"disambiguationData":[OSD([subQ0])],"isStart":false})});}
            var Q26;
            {var subQ0=sQuery(id+"F0.wireOp",EDGE,"E0.top");var subQ1=sQuery(id+"F0.wireOp",EDGE,"E0.bottom");var subQ2=sQuery(id+"F5.wireOp",EDGE,"E31");Q26=makeQuery(id+"F6.boolean.opBoolean","SPLIT",EDGE,{"disambiguationData":[TD([makeQuery(id+"F1.opExtrude","CAP_FACE",FACE,{"disambiguationData":[OSD([subQ1,subQ0,sQuery(id+"F0.wireOp",EDGE,"E0.left"),sQuery(id+"F0.wireOp",EDGE,"E0.right")])],"isStart":false}),makeQuery(id+"F1.opExtrude","SWEPT_FACE",FACE,{"disambiguationData":[OSD([subQ0])]}),makeQuery(id+"F6.opExtrude","CAP_FACE",FACE,{"disambiguationData":[OSD([subQ1,sQuery(id+"F2.wireOp",EDGE,"E2.sketch_text.stroke-0"),sQuery(id+"F2.wireOp",EDGE,"E2.sketch_text.stroke-1"),sQuery(id+"F2.wireOp",EDGE,"E2.sketch_text.stroke-2"),sQuery(id+"F2.wireOp",EDGE,"E2.sketch_text.stroke-3"),sQuery(id+"F2.wireOp",EDGE,"E2.sketch_text.stroke-4"),sQuery(id+"F2.wireOp",EDGE,"E2.sketch_text.stroke-5"),sQuery(id+"F2.wireOp",EDGE,"E2.sketch_text.stroke-6"),sQuery(id+"F2.wireOp",EDGE,"E2.sketch_text.stroke-7"),sQuery(id+"F2.wireOp",EDGE,"E2.sketch_text.stroke-8"),sQuery(id+"F2.wireOp",EDGE,"E2.sketch_text.stroke-9"),sQuery(id+"F2.wireOp",EDGE,"E2.sketch_text.stroke-10"),sQuery(id+"F2.wireOp",EDGE,"E2.sketch_text.stroke-11"),sQuery(id+"F2.wireOp",EDGE,"E2.sketch_text.stroke-12"),sQuery(id+"F2.wireOp",EDGE,"E2.sketch_text.stroke-13"),sQuery(id+"F2.wireOp",EDGE,"E2.sketch_text.stroke-14"),sQuery(id+"F2.wireOp",EDGE,"E2.sketch_text.stroke-15"),sQuery(id+"F2.wireOp",EDGE,"E2.sketch_text.stroke-16"),sQuery(id+"F2.wireOp",EDGE,"E2.sketch_text.stroke-17"),sQuery(id+"F2.wireOp",EDGE,"E2.sketch_text.stroke-18"),sQuery(id+"F2.wireOp",EDGE,"E2.sketch_text.stroke-19"),sQuery(id+"F2.wireOp",EDGE,"E2.sketch_text.stroke-20"),sQuery(id+"F2.wireOp",EDGE,"E2.sketch_text.stroke-21"),sQuery(id+"F2.wireOp",EDGE,"E2.sketch_text.stroke-22"),sQuery(id+"F2.wireOp",EDGE,"E2.sketch_text.stroke-23"),sQuery(id+"F2.wireOp",EDGE,"E2.sketch_text.stroke-24"),sQuery(id+"F2.wireOp",EDGE,"E2.sketch_text.stroke-25"),sQuery(id+"F2.wireOp",EDGE,"E2.sketch_text.stroke-26"),sQuery(id+"F2.wireOp",EDGE,"E2.sketch_text.stroke-27"),sQuery(id+"F2.wireOp",EDGE,"E2.sketch_text.stroke-28"),sQuery(id+"F2.wireOp",EDGE,"E2.sketch_text.stroke-29"),sQuery(id+"F2.wireOp",EDGE,"E2.sketch_text.stroke-30"),sQuery(id+"F2.wireOp",EDGE,"E2.sketch_text.stroke-31"),sQuery(id+"F2.wireOp",EDGE,"E2.sketch_text.stroke-32"),sQuery(id+"F2.wireOp",EDGE,"E2.sketch_text.stroke-33"),sQuery(id+"F2.wireOp",EDGE,"E2.sketch_text.stroke-34"),sQuery(id+"F2.wireOp",EDGE,"E2.sketch_text.stroke-35"),sQuery(id+"F2.wireOp",EDGE,"E2.sketch_text.stroke-36"),sQuery(id+"F2.wireOp",EDGE,"E2.sketch_text.stroke-37"),sQuery(id+"F2.wireOp",EDGE,"E2.sketch_text.stroke-38"),sQuery(id+"F2.wireOp",EDGE,"E2.sketch_text.stroke-39"),sQuery(id+"F2.wireOp",EDGE,"E2.sketch_text.stroke-40"),sQuery(id+"F2.wireOp",EDGE,"E2.sketch_text.stroke-41"),sQuery(id+"F2.wireOp",EDGE,"E2.sketch_text.stroke-42"),sQuery(id+"F2.wireOp",EDGE,"E2.sketch_text.stroke-43"),sQuery(id+"F2.wireOp",EDGE,"E2.sketch_text.stroke-44"),sQuery(id+"F2.wireOp",EDGE,"E2.sketch_text.stroke-45"),sQuery(id+"F2.wireOp",EDGE,"E2.sketch_text.stroke-46"),sQuery(id+"F2.wireOp",EDGE,"E2.sketch_text.stroke-47"),sQuery(id+"F2.wireOp",EDGE,"E2.sketch_text.stroke-48"),sQuery(id+"F2.wireOp",EDGE,"E2.sketch_text.stroke-49"),sQuery(id+"F2.wireOp",EDGE,"E2.sketch_text.stroke-50"),sQuery(id+"F2.wireOp",EDGE,"E2.sketch_text.stroke-51"),sQuery(id+"F2.wireOp",EDGE,"E2.sketch_text.stroke-52"),sQuery(id+"F2.wireOp",EDGE,"E2.sketch_text.stroke-53"),sQuery(id+"F2.wireOp",EDGE,"E2.sketch_text.stroke-54"),sQuery(id+"F2.wireOp",EDGE,"E2.sketch_text.stroke-55"),sQuery(id+"F2.wireOp",EDGE,"E2.sketch_text.stroke-56"),sQuery(id+"F2.wireOp",EDGE,"E2.sketch_text.stroke-57"),sQuery(id+"F2.wireOp",EDGE,"E2.sketch_text.stroke-58"),sQuery(id+"F2.wireOp",EDGE,"E2.sketch_text.stroke-59"),sQuery(id+"F2.wireOp",EDGE,"E2.sketch_text.stroke-60"),sQuery(id+"F2.wireOp",EDGE,"E2.sketch_text.stroke-61"),sQuery(id+"F2.wireOp",EDGE,"E2.sketch_text.stroke-62"),sQuery(id+"F2.wireOp",EDGE,"E2.sketch_text.stroke-63"),sQuery(id+"F2.wireOp",EDGE,"E2.sketch_text.stroke-64"),sQuery(id+"F2.wireOp",EDGE,"E2.sketch_text.stroke-65"),sQuery(id+"F2.wireOp",EDGE,"E2.sketch_text.stroke-66"),sQuery(id+"F2.wireOp",EDGE,"E2.sketch_text.stroke-67"),sQuery(id+"F2.wireOp",EDGE,"E2.sketch_text.stroke-68"),sQuery(id+"F2.wireOp",EDGE,"E2.sketch_text.stroke-69"),sQuery(id+"F2.wireOp",EDGE,"E2.sketch_text.stroke-70"),sQuery(id+"F2.wireOp",EDGE,"E2.sketch_text.stroke-71"),sQuery(id+"F2.wireOp",EDGE,"E2.sketch_text.stroke-72"),sQuery(id+"F2.wireOp",EDGE,"E2.sketch_text.stroke-73"),sQuery(id+"F2.wireOp",EDGE,"E2.sketch_text.stroke-74"),sQuery(id+"F2.wireOp",EDGE,"E2.sketch_text.stroke-75"),sQuery(id+"F2.wireOp",EDGE,"E2.sketch_text.stroke-76"),sQuery(id+"F2.wireOp",EDGE,"E2.sketch_text.stroke-77"),sQuery(id+"F2.wireOp",EDGE,"E2.sketch_text.stroke-78"),sQuery(id+"F2.wireOp",EDGE,"E2.sketch_text.stroke-79"),sQuery(id+"F2.wireOp",EDGE,"E2.sketch_text.stroke-80"),sQuery(id+"F2.wireOp",EDGE,"E2.sketch_text.stroke-81"),sQuery(id+"F2.wireOp",EDGE,"E2.sketch_text.stroke-82"),sQuery(id+"F2.wireOp",EDGE,"E2.sketch_text.stroke-83"),sQuery(id+"F2.wireOp",EDGE,"E2.sketch_text.stroke-84"),sQuery(id+"F2.wireOp",EDGE,"E2.sketch_text.stroke-85"),sQuery(id+"F2.wireOp",EDGE,"E2.sketch_text.stroke-86"),sQuery(id+"F2.wireOp",EDGE,"E2.sketch_text.stroke-87"),sQuery(id+"F2.wireOp",EDGE,"E2.sketch_text.stroke-88"),sQuery(id+"F2.wireOp",EDGE,"E2.sketch_text.stroke-89"),sQuery(id+"F2.wireOp",EDGE,"E2.sketch_text.stroke-90"),sQuery(id+"F2.wireOp",EDGE,"E2.sketch_text.stroke-91"),sQuery(id+"F2.wireOp",EDGE,"E2.sketch_text.stroke-92"),sQuery(id+"F2.wireOp",EDGE,"E2.sketch_text.stroke-93"),sQuery(id+"F2.wireOp",EDGE,"E2.sketch_text.stroke-94"),sQuery(id+"F2.wireOp",EDGE,"E2.sketch_text.stroke-95"),sQuery(id+"F2.wireOp",EDGE,"E2.sketch_text.stroke-96"),sQuery(id+"F2.wireOp",EDGE,"E2.sketch_text.stroke-97"),sQuery(id+"F2.wireOp",EDGE,"E2.sketch_text.stroke-98"),sQuery(id+"F2.wireOp",EDGE,"E2.sketch_text.stroke-99"),sQuery(id+"F2.wireOp",EDGE,"E2.sketch_text.stroke-100"),sQuery(id+"F2.wireOp",EDGE,"E2.sketch_text.stroke-101"),sQuery(id+"F2.wireOp",EDGE,"E2.sketch_text.stroke-102"),sQuery(id+"F2.wireOp",EDGE,"E2.sketch_text.stroke-103"),sQuery(id+"F2.wireOp",EDGE,"E2.sketch_text.stroke-104"),sQuery(id+"F2.wireOp",EDGE,"E2.sketch_text.stroke-105"),sQuery(id+"F2.wireOp",EDGE,"E2.sketch_text.stroke-106"),sQuery(id+"F2.wireOp",EDGE,"E2.sketch_text.stroke-107"),sQuery(id+"F2.wireOp",EDGE,"E2.sketch_text.stroke-108"),sQuery(id+"F2.wireOp",EDGE,"E2.sketch_text.stroke-109"),sQuery(id+"F2.wireOp",EDGE,"E2.sketch_text.stroke-110"),sQuery(id+"F2.wireOp",EDGE,"E2.sketch_text.stroke-111"),sQuery(id+"F2.wireOp",EDGE,"E2.sketch_text.stroke-112"),sQuery(id+"F2.wireOp",EDGE,"E2.sketch_text.stroke-113"),sQuery(id+"F2.wireOp",EDGE,"E2.sketch_text.stroke-114"),sQuery(id+"F2.wireOp",EDGE,"E2.sketch_text.stroke-115"),sQuery(id+"F2.wireOp",EDGE,"E2.sketch_text.stroke-116"),sQuery(id+"F2.wireOp",EDGE,"E2.sketch_text.stroke-117"),sQuery(id+"F2.wireOp",EDGE,"E2.sketch_text.stroke-118"),sQuery(id+"F2.wireOp",EDGE,"E2.sketch_text.stroke-119"),sQuery(id+"F2.wireOp",EDGE,"E2.sketch_text.stroke-120"),sQuery(id+"F2.wireOp",EDGE,"E2.sketch_text.stroke-121"),sQuery(id+"F2.wireOp",EDGE,"E2.sketch_text.stroke-122"),sQuery(id+"F2.wireOp",EDGE,"E2.sketch_text.stroke-123"),sQuery(id+"F2.wireOp",EDGE,"E2.sketch_text.stroke-124"),sQuery(id+"F2.wireOp",EDGE,"E2.sketch_text.stroke-125"),sQuery(id+"F2.wireOp",EDGE,"E2.sketch_text.stroke-126"),sQuery(id+"F2.wireOp",EDGE,"E2.sketch_text.stroke-127"),sQuery(id+"F2.wireOp",EDGE,"E2.sketch_text.stroke-128"),sQuery(id+"F2.wireOp",EDGE,"E2.sketch_text.stroke-129"),sQuery(id+"F2.wireOp",EDGE,"E2.sketch_text.stroke-130"),sQuery(id+"F2.wireOp",EDGE,"E2.sketch_text.stroke-131"),sQuery(id+"F2.wireOp",EDGE,"E2.sketch_text.stroke-132"),sQuery(id+"F2.wireOp",EDGE,"E2.sketch_text.stroke-133"),sQuery(id+"F2.wireOp",EDGE,"E2.sketch_text.stroke-134"),sQuery(id+"F2.wireOp",EDGE,"E2.sketch_text.stroke-135"),sQuery(id+"F2.wireOp",EDGE,"E2.sketch_text.stroke-136"),sQuery(id+"F2.wireOp",EDGE,"E2.sketch_text.stroke-137"),sQuery(id+"F2.wireOp",EDGE,"E2.sketch_text.stroke-138"),sQuery(id+"F2.wireOp",EDGE,"E2.sketch_text.stroke-139"),sQuery(id+"F2.wireOp",EDGE,"E2.sketch_text.stroke-140"),sQuery(id+"F2.wireOp",EDGE,"E2.sketch_text.stroke-141"),sQuery(id+"F2.wireOp",EDGE,"E2.sketch_text.stroke-142"),sQuery(id+"F2.wireOp",EDGE,"E2.sketch_text.stroke-143"),sQuery(id+"F2.wireOp",EDGE,"E2.sketch_text.stroke-144"),sQuery(id+"F2.wireOp",EDGE,"E2.sketch_text.stroke-145"),sQuery(id+"F2.wireOp",EDGE,"E2.sketch_text.stroke-146"),sQuery(id+"F2.wireOp",EDGE,"E2.sketch_text.stroke-147"),sQuery(id+"F2.wireOp",EDGE,"E2.sketch_text.stroke-148"),sQuery(id+"F2.wireOp",EDGE,"E2.sketch_text.stroke-149"),sQuery(id+"F2.wireOp",EDGE,"E2.sketch_text.stroke-150"),sQuery(id+"F2.wireOp",EDGE,"E2.sketch_text.stroke-151"),sQuery(id+"F2.wireOp",EDGE,"E2.sketch_text.stroke-152"),sQuery(id+"F2.wireOp",EDGE,"E2.sketch_text.stroke-153"),sQuery(id+"F2.wireOp",EDGE,"E2.sketch_text.stroke-154"),sQuery(id+"F2.wireOp",EDGE,"E2.sketch_text.stroke-155"),sQuery(id+"F2.wireOp",EDGE,"E2.sketch_text.stroke-156"),sQuery(id+"F2.wireOp",EDGE,"E2.sketch_text.stroke-157"),sQuery(id+"F2.wireOp",EDGE,"E2.sketch_text.stroke-158"),sQuery(id+"F2.wireOp",EDGE,"E2.sketch_text.stroke-159"),sQuery(id+"F2.wireOp",EDGE,"E2.sketch_text.stroke-160"),sQuery(id+"F2.wireOp",EDGE,"E2.sketch_text.stroke-161"),sQuery(id+"F2.wireOp",EDGE,"E2.sketch_text.stroke-162"),sQuery(id+"F2.wireOp",EDGE,"E2.sketch_text.stroke-163"),sQuery(id+"F2.wireOp",EDGE,"E2.sketch_text.stroke-164"),sQuery(id+"F2.wireOp",EDGE,"E2.sketch_text.stroke-165"),sQuery(id+"F2.wireOp",EDGE,"E2.sketch_text.stroke-166"),sQuery(id+"F2.wireOp",EDGE,"E2.sketch_text.stroke-167"),sQuery(id+"F2.wireOp",EDGE,"E2.sketch_text.stroke-168"),sQuery(id+"F2.wireOp",EDGE,"E2.sketch_text.stroke-169"),sQuery(id+"F2.wireOp",EDGE,"E2.sketch_text.stroke-170"),sQuery(id+"F2.wireOp",EDGE,"E2.sketch_text.stroke-171"),sQuery(id+"F2.wireOp",EDGE,"E2.sketch_text.stroke-172"),sQuery(id+"F2.wireOp",EDGE,"E2.sketch_text.stroke-173"),sQuery(id+"F3.wireOp",EDGE,"E4.sketch_text.stroke-0"),sQuery(id+"F3.wireOp",EDGE,"E4.sketch_text.stroke-1"),sQuery(id+"F3.wireOp",EDGE,"E4.sketch_text.stroke-2"),sQuery(id+"F3.wireOp",EDGE,"E4.sketch_text.stroke-3"),sQuery(id+"F3.wireOp",EDGE,"E4.sketch_text.stroke-4"),sQuery(id+"F3.wireOp",EDGE,"E4.sketch_text.stroke-5"),sQuery(id+"F3.wireOp",EDGE,"E4.sketch_text.stroke-6"),sQuery(id+"F3.wireOp",EDGE,"E4.sketch_text.stroke-7"),sQuery(id+"F3.wireOp",EDGE,"E4.sketch_text.stroke-8"),sQuery(id+"F3.wireOp",EDGE,"E4.sketch_text.stroke-9"),sQuery(id+"F3.wireOp",EDGE,"E4.sketch_text.stroke-10"),sQuery(id+"F3.wireOp",EDGE,"E4.sketch_text.stroke-11"),sQuery(id+"F3.wireOp",EDGE,"E4.sketch_text.stroke-12"),sQuery(id+"F3.wireOp",EDGE,"E4.sketch_text.stroke-13"),sQuery(id+"F3.wireOp",EDGE,"E4.sketch_text.stroke-14"),sQuery(id+"F3.wireOp",EDGE,"E4.sketch_text.stroke-15"),sQuery(id+"F3.wireOp",EDGE,"E4.sketch_text.stroke-16"),sQuery(id+"F3.wireOp",EDGE,"E4.sketch_text.stroke-17"),sQuery(id+"F3.wireOp",EDGE,"E4.sketch_text.stroke-18"),sQuery(id+"F3.wireOp",EDGE,"E4.sketch_text.stroke-19"),sQuery(id+"F3.wireOp",EDGE,"E4.sketch_text.stroke-20"),sQuery(id+"F3.wireOp",EDGE,"E4.sketch_text.stroke-21"),sQuery(id+"F3.wireOp",EDGE,"E4.sketch_text.stroke-22"),sQuery(id+"F3.wireOp",EDGE,"E4.sketch_text.stroke-23"),sQuery(id+"F3.wireOp",EDGE,"E4.sketch_text.stroke-24"),sQuery(id+"F3.wireOp",EDGE,"E4.sketch_text.stroke-25"),sQuery(id+"F3.wireOp",EDGE,"E4.sketch_text.stroke-26"),sQuery(id+"F3.wireOp",EDGE,"E4.sketch_text.stroke-27"),sQuery(id+"F3.wireOp",EDGE,"E4.sketch_text.stroke-28"),sQuery(id+"F3.wireOp",EDGE,"E4.sketch_text.stroke-29"),sQuery(id+"F3.wireOp",EDGE,"E4.sketch_text.stroke-30"),sQuery(id+"F3.wireOp",EDGE,"E4.sketch_text.stroke-31"),sQuery(id+"F3.wireOp",EDGE,"E4.sketch_text.stroke-32"),sQuery(id+"F3.wireOp",EDGE,"E4.sketch_text.stroke-33"),sQuery(id+"F3.wireOp",EDGE,"E4.sketch_text.stroke-34"),sQuery(id+"F3.wireOp",EDGE,"E4.sketch_text.stroke-35"),sQuery(id+"F3.wireOp",EDGE,"E4.sketch_text.stroke-36"),sQuery(id+"F3.wireOp",EDGE,"E4.sketch_text.stroke-37"),sQuery(id+"F3.wireOp",EDGE,"E4.sketch_text.stroke-38"),sQuery(id+"F3.wireOp",EDGE,"E4.sketch_text.stroke-39"),sQuery(id+"F3.wireOp",EDGE,"E4.sketch_text.stroke-40"),sQuery(id+"F3.wireOp",EDGE,"E4.sketch_text.stroke-41"),sQuery(id+"F3.wireOp",EDGE,"E4.sketch_text.stroke-42"),sQuery(id+"F3.wireOp",EDGE,"E4.sketch_text.stroke-43"),sQuery(id+"F3.wireOp",EDGE,"E4.sketch_text.stroke-44"),sQuery(id+"F3.wireOp",EDGE,"E4.sketch_text.stroke-45"),sQuery(id+"F3.wireOp",EDGE,"E4.sketch_text.stroke-46"),sQuery(id+"F3.wireOp",EDGE,"E4.sketch_text.stroke-47"),sQuery(id+"F3.wireOp",EDGE,"E4.sketch_text.stroke-48"),sQuery(id+"F3.wireOp",EDGE,"E4.sketch_text.stroke-49"),sQuery(id+"F3.wireOp",EDGE,"E4.sketch_text.stroke-50"),sQuery(id+"F3.wireOp",EDGE,"E4.sketch_text.stroke-51"),sQuery(id+"F3.wireOp",EDGE,"E4.sketch_text.stroke-52"),sQuery(id+"F3.wireOp",EDGE,"E4.sketch_text.stroke-53"),sQuery(id+"F3.wireOp",EDGE,"E4.sketch_text.stroke-54"),sQuery(id+"F3.wireOp",EDGE,"E4.sketch_text.stroke-55"),sQuery(id+"F3.wireOp",EDGE,"E4.sketch_text.stroke-56"),sQuery(id+"F3.wireOp",EDGE,"E4.sketch_text.stroke-57"),sQuery(id+"F3.wireOp",EDGE,"E4.sketch_text.stroke-58"),sQuery(id+"F3.wireOp",EDGE,"E4.sketch_text.stroke-59"),sQuery(id+"F3.wireOp",EDGE,"E4.sketch_text.stroke-60"),sQuery(id+"F3.wireOp",EDGE,"E4.sketch_text.stroke-61"),sQuery(id+"F3.wireOp",EDGE,"E4.sketch_text.stroke-62"),sQuery(id+"F3.wireOp",EDGE,"E4.sketch_text.stroke-71"),sQuery(id+"F3.wireOp",EDGE,"E4.sketch_text.stroke-72"),sQuery(id+"F3.wireOp",EDGE,"E4.sketch_text.stroke-73"),sQuery(id+"F3.wireOp",EDGE,"E4.sketch_text.stroke-74"),sQuery(id+"F3.wireOp",EDGE,"E4.sketch_text.stroke-75"),sQuery(id+"F3.wireOp",EDGE,"E4.sketch_text.stroke-76"),sQuery(id+"F3.wireOp",EDGE,"E4.sketch_text.stroke-77"),sQuery(id+"F3.wireOp",EDGE,"E4.sketch_text.stroke-78"),sQuery(id+"F3.wireOp",EDGE,"E4.sketch_text.stroke-79"),sQuery(id+"F3.wireOp",EDGE,"E4.sketch_text.stroke-80"),sQuery(id+"F3.wireOp",EDGE,"E4.sketch_text.stroke-81"),sQuery(id+"F3.wireOp",EDGE,"E4.sketch_text.stroke-82"),sQuery(id+"F3.wireOp",EDGE,"E4.sketch_text.stroke-83"),sQuery(id+"F3.wireOp",EDGE,"E4.sketch_text.stroke-84"),sQuery(id+"F3.wireOp",EDGE,"E4.sketch_text.stroke-85"),sQuery(id+"F3.wireOp",EDGE,"E4.sketch_text.stroke-86"),sQuery(id+"F3.wireOp",EDGE,"E4.sketch_text.stroke-87"),sQuery(id+"F3.wireOp",EDGE,"E4.sketch_text.stroke-88"),sQuery(id+"F3.wireOp",EDGE,"E4.sketch_text.stroke-89"),sQuery(id+"F3.wireOp",EDGE,"E4.sketch_text.stroke-90"),sQuery(id+"F3.wireOp",EDGE,"E4.sketch_text.stroke-91"),sQuery(id+"F3.wireOp",EDGE,"E4.sketch_text.stroke-92"),sQuery(id+"F3.wireOp",EDGE,"E4.sketch_text.stroke-93"),sQuery(id+"F3.wireOp",EDGE,"E4.sketch_text.stroke-94"),sQuery(id+"F3.wireOp",EDGE,"E4.sketch_text.stroke-95"),sQuery(id+"F3.wireOp",EDGE,"E4.sketch_text.stroke-96"),sQuery(id+"F3.wireOp",EDGE,"E4.sketch_text.stroke-97"),sQuery(id+"F3.wireOp",EDGE,"E4.sketch_text.stroke-103"),sQuery(id+"F3.wireOp",EDGE,"E4.sketch_text.stroke-104"),sQuery(id+"F3.wireOp",EDGE,"E4.sketch_text.stroke-105"),sQuery(id+"F3.wireOp",EDGE,"E4.sketch_text.stroke-106"),sQuery(id+"F3.wireOp",EDGE,"E4.sketch_text.stroke-107"),sQuery(id+"F3.wireOp",EDGE,"E4.sketch_text.stroke-108"),sQuery(id+"F3.wireOp",EDGE,"E4.sketch_text.stroke-109"),sQuery(id+"F3.wireOp",EDGE,"E4.sketch_text.stroke-110"),sQuery(id+"F3.wireOp",EDGE,"E4.sketch_text.stroke-111"),sQuery(id+"F3.wireOp",EDGE,"E4.sketch_text.stroke-112"),sQuery(id+"F3.wireOp",EDGE,"E4.sketch_text.stroke-113"),sQuery(id+"F3.wireOp",EDGE,"E4.sketch_text.stroke-114"),sQuery(id+"F3.wireOp",EDGE,"E4.sketch_text.stroke-115"),sQuery(id+"F3.wireOp",EDGE,"E4.sketch_text.stroke-116"),sQuery(id+"F3.wireOp",EDGE,"E4.sketch_text.stroke-117"),sQuery(id+"F3.wireOp",EDGE,"E4.sketch_text.stroke-118"),sQuery(id+"F3.wireOp",EDGE,"E4.sketch_text.stroke-119"),sQuery(id+"F3.wireOp",EDGE,"E4.sketch_text.stroke-120"),sQuery(id+"F3.wireOp",EDGE,"E4.sketch_text.stroke-121"),sQuery(id+"F3.wireOp",EDGE,"E4.sketch_text.stroke-122"),sQuery(id+"F3.wireOp",EDGE,"E4.sketch_text.stroke-123"),sQuery(id+"F3.wireOp",EDGE,"E4.sketch_text.stroke-124"),sQuery(id+"F3.wireOp",EDGE,"E4.sketch_text.stroke-125"),sQuery(id+"F3.wireOp",EDGE,"E4.sketch_text.stroke-126"),sQuery(id+"F3.wireOp",EDGE,"E4.sketch_text.stroke-127"),sQuery(id+"F3.wireOp",EDGE,"E4.sketch_text.stroke-128"),sQuery(id+"F3.wireOp",EDGE,"E4.sketch_text.stroke-129"),sQuery(id+"F3.wireOp",EDGE,"E4.sketch_text.stroke-130"),sQuery(id+"F3.wireOp",EDGE,"E4.sketch_text.stroke-131"),sQuery(id+"F3.wireOp",EDGE,"E4.sketch_text.stroke-132"),sQuery(id+"F3.wireOp",EDGE,"E4.sketch_text.stroke-133"),sQuery(id+"F3.wireOp",EDGE,"E4.sketch_text.stroke-134"),sQuery(id+"F3.wireOp",EDGE,"E4.sketch_text.stroke-135"),sQuery(id+"F3.wireOp",EDGE,"E4.sketch_text.stroke-136"),sQuery(id+"F3.wireOp",EDGE,"E4.sketch_text.stroke-137"),sQuery(id+"F3.wireOp",EDGE,"E4.sketch_text.stroke-138"),sQuery(id+"F3.wireOp",EDGE,"E4.sketch_text.stroke-139"),sQuery(id+"F3.wireOp",EDGE,"E4.sketch_text.stroke-140"),sQuery(id+"F3.wireOp",EDGE,"E4.sketch_text.stroke-141"),sQuery(id+"F3.wireOp",EDGE,"E4.sketch_text.stroke-142"),sQuery(id+"F3.wireOp",EDGE,"E4.sketch_text.stroke-143"),sQuery(id+"F3.wireOp",EDGE,"E4.sketch_text.stroke-144"),sQuery(id+"F3.wireOp",EDGE,"E4.sketch_text.stroke-145"),sQuery(id+"F3.wireOp",EDGE,"E4.sketch_text.stroke-146"),sQuery(id+"F3.wireOp",EDGE,"E4.sketch_text.stroke-147"),sQuery(id+"F3.wireOp",EDGE,"E4.sketch_text.stroke-148"),sQuery(id+"F3.wireOp",EDGE,"E4.sketch_text.stroke-149"),sQuery(id+"F3.wireOp",EDGE,"E4.sketch_text.stroke-150"),sQuery(id+"F3.wireOp",EDGE,"E4.sketch_text.stroke-151"),sQuery(id+"F3.wireOp",EDGE,"E4.sketch_text.stroke-152"),sQuery(id+"F3.wireOp",EDGE,"E4.sketch_text.stroke-153"),sQuery(id+"F3.wireOp",EDGE,"E4.sketch_text.stroke-159"),sQuery(id+"F3.wireOp",EDGE,"E4.sketch_text.stroke-160"),sQuery(id+"F3.wireOp",EDGE,"E4.sketch_text.stroke-161"),sQuery(id+"F3.wireOp",EDGE,"E4.sketch_text.stroke-162"),sQuery(id+"F3.wireOp",EDGE,"E4.sketch_text.stroke-163"),sQuery(id+"F3.wireOp",EDGE,"E4.sketch_text.stroke-164"),sQuery(id+"F3.wireOp",EDGE,"E4.sketch_text.stroke-165"),sQuery(id+"F3.wireOp",EDGE,"E4.sketch_text.stroke-166"),sQuery(id+"F3.wireOp",EDGE,"E4.sketch_text.stroke-167"),sQuery(id+"F3.wireOp",EDGE,"E4.sketch_text.stroke-168"),sQuery(id+"F3.wireOp",EDGE,"E4.sketch_text.stroke-169"),sQuery(id+"F3.wireOp",EDGE,"E4.sketch_text.stroke-170"),sQuery(id+"F3.wireOp",EDGE,"E4.sketch_text.stroke-171"),sQuery(id+"F3.wireOp",EDGE,"E4.sketch_text.stroke-172"),sQuery(id+"F3.wireOp",EDGE,"E4.sketch_text.stroke-173"),sQuery(id+"F3.wireOp",EDGE,"E4.sketch_text.stroke-174"),sQuery(id+"F3.wireOp",EDGE,"E4.sketch_text.stroke-175"),sQuery(id+"F3.wireOp",EDGE,"E4.sketch_text.stroke-176"),sQuery(id+"F3.wireOp",EDGE,"E4.sketch_text.stroke-177"),sQuery(id+"F3.wireOp",EDGE,"E4.sketch_text.stroke-178"),sQuery(id+"F3.wireOp",EDGE,"E4.sketch_text.stroke-179"),sQuery(id+"F3.wireOp",EDGE,"E4.sketch_text.stroke-180"),sQuery(id+"F5.wireOp",EDGE,"E30"),subQ2])],"isStart":true}),makeQuery(id+"F6.opExtrude","SWEPT_FACE",FACE,{"disambiguationData":[OSD([subQ2])]})]),OD(0.0)],"derivedFrom":makeQuery(id+"F1.opExtrude","CAP_EDGE",EDGE,{"disambiguationData":[OSD([subQ0])],"isStart":false})});}
            var Q27;
            {var subQ0=sQuery(id+"F0.wireOp",EDGE,"E0.top");var subQ1=sQuery(id+"F0.wireOp",EDGE,"E0.bottom");var subQ2=sQuery(id+"F5.wireOp",EDGE,"E31");Q27=makeQuery(id+"F6.boolean.opBoolean","SPLIT",EDGE,{"disambiguationData":[TD([makeQuery(id+"F1.opExtrude","CAP_FACE",FACE,{"disambiguationData":[OSD([subQ1,subQ0,sQuery(id+"F0.wireOp",EDGE,"E0.left"),sQuery(id+"F0.wireOp",EDGE,"E0.right")])],"isStart":false}),makeQuery(id+"F1.opExtrude","SWEPT_FACE",FACE,{"disambiguationData":[OSD([subQ0])]}),makeQuery(id+"F6.opExtrude","CAP_FACE",FACE,{"disambiguationData":[OSD([subQ1,sQuery(id+"F2.wireOp",EDGE,"E2.sketch_text.stroke-0"),sQuery(id+"F2.wireOp",EDGE,"E2.sketch_text.stroke-1"),sQuery(id+"F2.wireOp",EDGE,"E2.sketch_text.stroke-2"),sQuery(id+"F2.wireOp",EDGE,"E2.sketch_text.stroke-3"),sQuery(id+"F2.wireOp",EDGE,"E2.sketch_text.stroke-4"),sQuery(id+"F2.wireOp",EDGE,"E2.sketch_text.stroke-5"),sQuery(id+"F2.wireOp",EDGE,"E2.sketch_text.stroke-6"),sQuery(id+"F2.wireOp",EDGE,"E2.sketch_text.stroke-7"),sQuery(id+"F2.wireOp",EDGE,"E2.sketch_text.stroke-8"),sQuery(id+"F2.wireOp",EDGE,"E2.sketch_text.stroke-9"),sQuery(id+"F2.wireOp",EDGE,"E2.sketch_text.stroke-10"),sQuery(id+"F2.wireOp",EDGE,"E2.sketch_text.stroke-11"),sQuery(id+"F2.wireOp",EDGE,"E2.sketch_text.stroke-12"),sQuery(id+"F2.wireOp",EDGE,"E2.sketch_text.stroke-13"),sQuery(id+"F2.wireOp",EDGE,"E2.sketch_text.stroke-14"),sQuery(id+"F2.wireOp",EDGE,"E2.sketch_text.stroke-15"),sQuery(id+"F2.wireOp",EDGE,"E2.sketch_text.stroke-16"),sQuery(id+"F2.wireOp",EDGE,"E2.sketch_text.stroke-17"),sQuery(id+"F2.wireOp",EDGE,"E2.sketch_text.stroke-18"),sQuery(id+"F2.wireOp",EDGE,"E2.sketch_text.stroke-19"),sQuery(id+"F2.wireOp",EDGE,"E2.sketch_text.stroke-20"),sQuery(id+"F2.wireOp",EDGE,"E2.sketch_text.stroke-21"),sQuery(id+"F2.wireOp",EDGE,"E2.sketch_text.stroke-22"),sQuery(id+"F2.wireOp",EDGE,"E2.sketch_text.stroke-23"),sQuery(id+"F2.wireOp",EDGE,"E2.sketch_text.stroke-24"),sQuery(id+"F2.wireOp",EDGE,"E2.sketch_text.stroke-25"),sQuery(id+"F2.wireOp",EDGE,"E2.sketch_text.stroke-26"),sQuery(id+"F2.wireOp",EDGE,"E2.sketch_text.stroke-27"),sQuery(id+"F2.wireOp",EDGE,"E2.sketch_text.stroke-28"),sQuery(id+"F2.wireOp",EDGE,"E2.sketch_text.stroke-29"),sQuery(id+"F2.wireOp",EDGE,"E2.sketch_text.stroke-30"),sQuery(id+"F2.wireOp",EDGE,"E2.sketch_text.stroke-31"),sQuery(id+"F2.wireOp",EDGE,"E2.sketch_text.stroke-32"),sQuery(id+"F2.wireOp",EDGE,"E2.sketch_text.stroke-33"),sQuery(id+"F2.wireOp",EDGE,"E2.sketch_text.stroke-34"),sQuery(id+"F2.wireOp",EDGE,"E2.sketch_text.stroke-35"),sQuery(id+"F2.wireOp",EDGE,"E2.sketch_text.stroke-36"),sQuery(id+"F2.wireOp",EDGE,"E2.sketch_text.stroke-37"),sQuery(id+"F2.wireOp",EDGE,"E2.sketch_text.stroke-38"),sQuery(id+"F2.wireOp",EDGE,"E2.sketch_text.stroke-39"),sQuery(id+"F2.wireOp",EDGE,"E2.sketch_text.stroke-40"),sQuery(id+"F2.wireOp",EDGE,"E2.sketch_text.stroke-41"),sQuery(id+"F2.wireOp",EDGE,"E2.sketch_text.stroke-42"),sQuery(id+"F2.wireOp",EDGE,"E2.sketch_text.stroke-43"),sQuery(id+"F2.wireOp",EDGE,"E2.sketch_text.stroke-44"),sQuery(id+"F2.wireOp",EDGE,"E2.sketch_text.stroke-45"),sQuery(id+"F2.wireOp",EDGE,"E2.sketch_text.stroke-46"),sQuery(id+"F2.wireOp",EDGE,"E2.sketch_text.stroke-47"),sQuery(id+"F2.wireOp",EDGE,"E2.sketch_text.stroke-48"),sQuery(id+"F2.wireOp",EDGE,"E2.sketch_text.stroke-49"),sQuery(id+"F2.wireOp",EDGE,"E2.sketch_text.stroke-50"),sQuery(id+"F2.wireOp",EDGE,"E2.sketch_text.stroke-51"),sQuery(id+"F2.wireOp",EDGE,"E2.sketch_text.stroke-52"),sQuery(id+"F2.wireOp",EDGE,"E2.sketch_text.stroke-53"),sQuery(id+"F2.wireOp",EDGE,"E2.sketch_text.stroke-54"),sQuery(id+"F2.wireOp",EDGE,"E2.sketch_text.stroke-55"),sQuery(id+"F2.wireOp",EDGE,"E2.sketch_text.stroke-56"),sQuery(id+"F2.wireOp",EDGE,"E2.sketch_text.stroke-57"),sQuery(id+"F2.wireOp",EDGE,"E2.sketch_text.stroke-58"),sQuery(id+"F2.wireOp",EDGE,"E2.sketch_text.stroke-59"),sQuery(id+"F2.wireOp",EDGE,"E2.sketch_text.stroke-60"),sQuery(id+"F2.wireOp",EDGE,"E2.sketch_text.stroke-61"),sQuery(id+"F2.wireOp",EDGE,"E2.sketch_text.stroke-62"),sQuery(id+"F2.wireOp",EDGE,"E2.sketch_text.stroke-63"),sQuery(id+"F2.wireOp",EDGE,"E2.sketch_text.stroke-64"),sQuery(id+"F2.wireOp",EDGE,"E2.sketch_text.stroke-65"),sQuery(id+"F2.wireOp",EDGE,"E2.sketch_text.stroke-66"),sQuery(id+"F2.wireOp",EDGE,"E2.sketch_text.stroke-67"),sQuery(id+"F2.wireOp",EDGE,"E2.sketch_text.stroke-68"),sQuery(id+"F2.wireOp",EDGE,"E2.sketch_text.stroke-69"),sQuery(id+"F2.wireOp",EDGE,"E2.sketch_text.stroke-70"),sQuery(id+"F2.wireOp",EDGE,"E2.sketch_text.stroke-71"),sQuery(id+"F2.wireOp",EDGE,"E2.sketch_text.stroke-72"),sQuery(id+"F2.wireOp",EDGE,"E2.sketch_text.stroke-73"),sQuery(id+"F2.wireOp",EDGE,"E2.sketch_text.stroke-74"),sQuery(id+"F2.wireOp",EDGE,"E2.sketch_text.stroke-75"),sQuery(id+"F2.wireOp",EDGE,"E2.sketch_text.stroke-76"),sQuery(id+"F2.wireOp",EDGE,"E2.sketch_text.stroke-77"),sQuery(id+"F2.wireOp",EDGE,"E2.sketch_text.stroke-78"),sQuery(id+"F2.wireOp",EDGE,"E2.sketch_text.stroke-79"),sQuery(id+"F2.wireOp",EDGE,"E2.sketch_text.stroke-80"),sQuery(id+"F2.wireOp",EDGE,"E2.sketch_text.stroke-81"),sQuery(id+"F2.wireOp",EDGE,"E2.sketch_text.stroke-82"),sQuery(id+"F2.wireOp",EDGE,"E2.sketch_text.stroke-83"),sQuery(id+"F2.wireOp",EDGE,"E2.sketch_text.stroke-84"),sQuery(id+"F2.wireOp",EDGE,"E2.sketch_text.stroke-85"),sQuery(id+"F2.wireOp",EDGE,"E2.sketch_text.stroke-86"),sQuery(id+"F2.wireOp",EDGE,"E2.sketch_text.stroke-87"),sQuery(id+"F2.wireOp",EDGE,"E2.sketch_text.stroke-88"),sQuery(id+"F2.wireOp",EDGE,"E2.sketch_text.stroke-89"),sQuery(id+"F2.wireOp",EDGE,"E2.sketch_text.stroke-90"),sQuery(id+"F2.wireOp",EDGE,"E2.sketch_text.stroke-91"),sQuery(id+"F2.wireOp",EDGE,"E2.sketch_text.stroke-92"),sQuery(id+"F2.wireOp",EDGE,"E2.sketch_text.stroke-93"),sQuery(id+"F2.wireOp",EDGE,"E2.sketch_text.stroke-94"),sQuery(id+"F2.wireOp",EDGE,"E2.sketch_text.stroke-95"),sQuery(id+"F2.wireOp",EDGE,"E2.sketch_text.stroke-96"),sQuery(id+"F2.wireOp",EDGE,"E2.sketch_text.stroke-97"),sQuery(id+"F2.wireOp",EDGE,"E2.sketch_text.stroke-98"),sQuery(id+"F2.wireOp",EDGE,"E2.sketch_text.stroke-99"),sQuery(id+"F2.wireOp",EDGE,"E2.sketch_text.stroke-100"),sQuery(id+"F2.wireOp",EDGE,"E2.sketch_text.stroke-101"),sQuery(id+"F2.wireOp",EDGE,"E2.sketch_text.stroke-102"),sQuery(id+"F2.wireOp",EDGE,"E2.sketch_text.stroke-103"),sQuery(id+"F2.wireOp",EDGE,"E2.sketch_text.stroke-104"),sQuery(id+"F2.wireOp",EDGE,"E2.sketch_text.stroke-105"),sQuery(id+"F2.wireOp",EDGE,"E2.sketch_text.stroke-106"),sQuery(id+"F2.wireOp",EDGE,"E2.sketch_text.stroke-107"),sQuery(id+"F2.wireOp",EDGE,"E2.sketch_text.stroke-108"),sQuery(id+"F2.wireOp",EDGE,"E2.sketch_text.stroke-109"),sQuery(id+"F2.wireOp",EDGE,"E2.sketch_text.stroke-110"),sQuery(id+"F2.wireOp",EDGE,"E2.sketch_text.stroke-111"),sQuery(id+"F2.wireOp",EDGE,"E2.sketch_text.stroke-112"),sQuery(id+"F2.wireOp",EDGE,"E2.sketch_text.stroke-113"),sQuery(id+"F2.wireOp",EDGE,"E2.sketch_text.stroke-114"),sQuery(id+"F2.wireOp",EDGE,"E2.sketch_text.stroke-115"),sQuery(id+"F2.wireOp",EDGE,"E2.sketch_text.stroke-116"),sQuery(id+"F2.wireOp",EDGE,"E2.sketch_text.stroke-117"),sQuery(id+"F2.wireOp",EDGE,"E2.sketch_text.stroke-118"),sQuery(id+"F2.wireOp",EDGE,"E2.sketch_text.stroke-119"),sQuery(id+"F2.wireOp",EDGE,"E2.sketch_text.stroke-120"),sQuery(id+"F2.wireOp",EDGE,"E2.sketch_text.stroke-121"),sQuery(id+"F2.wireOp",EDGE,"E2.sketch_text.stroke-122"),sQuery(id+"F2.wireOp",EDGE,"E2.sketch_text.stroke-123"),sQuery(id+"F2.wireOp",EDGE,"E2.sketch_text.stroke-124"),sQuery(id+"F2.wireOp",EDGE,"E2.sketch_text.stroke-125"),sQuery(id+"F2.wireOp",EDGE,"E2.sketch_text.stroke-126"),sQuery(id+"F2.wireOp",EDGE,"E2.sketch_text.stroke-127"),sQuery(id+"F2.wireOp",EDGE,"E2.sketch_text.stroke-128"),sQuery(id+"F2.wireOp",EDGE,"E2.sketch_text.stroke-129"),sQuery(id+"F2.wireOp",EDGE,"E2.sketch_text.stroke-130"),sQuery(id+"F2.wireOp",EDGE,"E2.sketch_text.stroke-131"),sQuery(id+"F2.wireOp",EDGE,"E2.sketch_text.stroke-132"),sQuery(id+"F2.wireOp",EDGE,"E2.sketch_text.stroke-133"),sQuery(id+"F2.wireOp",EDGE,"E2.sketch_text.stroke-134"),sQuery(id+"F2.wireOp",EDGE,"E2.sketch_text.stroke-135"),sQuery(id+"F2.wireOp",EDGE,"E2.sketch_text.stroke-136"),sQuery(id+"F2.wireOp",EDGE,"E2.sketch_text.stroke-137"),sQuery(id+"F2.wireOp",EDGE,"E2.sketch_text.stroke-138"),sQuery(id+"F2.wireOp",EDGE,"E2.sketch_text.stroke-139"),sQuery(id+"F2.wireOp",EDGE,"E2.sketch_text.stroke-140"),sQuery(id+"F2.wireOp",EDGE,"E2.sketch_text.stroke-141"),sQuery(id+"F2.wireOp",EDGE,"E2.sketch_text.stroke-142"),sQuery(id+"F2.wireOp",EDGE,"E2.sketch_text.stroke-143"),sQuery(id+"F2.wireOp",EDGE,"E2.sketch_text.stroke-144"),sQuery(id+"F2.wireOp",EDGE,"E2.sketch_text.stroke-145"),sQuery(id+"F2.wireOp",EDGE,"E2.sketch_text.stroke-146"),sQuery(id+"F2.wireOp",EDGE,"E2.sketch_text.stroke-147"),sQuery(id+"F2.wireOp",EDGE,"E2.sketch_text.stroke-148"),sQuery(id+"F2.wireOp",EDGE,"E2.sketch_text.stroke-149"),sQuery(id+"F2.wireOp",EDGE,"E2.sketch_text.stroke-150"),sQuery(id+"F2.wireOp",EDGE,"E2.sketch_text.stroke-151"),sQuery(id+"F2.wireOp",EDGE,"E2.sketch_text.stroke-152"),sQuery(id+"F2.wireOp",EDGE,"E2.sketch_text.stroke-153"),sQuery(id+"F2.wireOp",EDGE,"E2.sketch_text.stroke-154"),sQuery(id+"F2.wireOp",EDGE,"E2.sketch_text.stroke-155"),sQuery(id+"F2.wireOp",EDGE,"E2.sketch_text.stroke-156"),sQuery(id+"F2.wireOp",EDGE,"E2.sketch_text.stroke-157"),sQuery(id+"F2.wireOp",EDGE,"E2.sketch_text.stroke-158"),sQuery(id+"F2.wireOp",EDGE,"E2.sketch_text.stroke-159"),sQuery(id+"F2.wireOp",EDGE,"E2.sketch_text.stroke-160"),sQuery(id+"F2.wireOp",EDGE,"E2.sketch_text.stroke-161"),sQuery(id+"F2.wireOp",EDGE,"E2.sketch_text.stroke-162"),sQuery(id+"F2.wireOp",EDGE,"E2.sketch_text.stroke-163"),sQuery(id+"F2.wireOp",EDGE,"E2.sketch_text.stroke-164"),sQuery(id+"F2.wireOp",EDGE,"E2.sketch_text.stroke-165"),sQuery(id+"F2.wireOp",EDGE,"E2.sketch_text.stroke-166"),sQuery(id+"F2.wireOp",EDGE,"E2.sketch_text.stroke-167"),sQuery(id+"F2.wireOp",EDGE,"E2.sketch_text.stroke-168"),sQuery(id+"F2.wireOp",EDGE,"E2.sketch_text.stroke-169"),sQuery(id+"F2.wireOp",EDGE,"E2.sketch_text.stroke-170"),sQuery(id+"F2.wireOp",EDGE,"E2.sketch_text.stroke-171"),sQuery(id+"F2.wireOp",EDGE,"E2.sketch_text.stroke-172"),sQuery(id+"F2.wireOp",EDGE,"E2.sketch_text.stroke-173"),sQuery(id+"F3.wireOp",EDGE,"E4.sketch_text.stroke-0"),sQuery(id+"F3.wireOp",EDGE,"E4.sketch_text.stroke-1"),sQuery(id+"F3.wireOp",EDGE,"E4.sketch_text.stroke-2"),sQuery(id+"F3.wireOp",EDGE,"E4.sketch_text.stroke-3"),sQuery(id+"F3.wireOp",EDGE,"E4.sketch_text.stroke-4"),sQuery(id+"F3.wireOp",EDGE,"E4.sketch_text.stroke-5"),sQuery(id+"F3.wireOp",EDGE,"E4.sketch_text.stroke-6"),sQuery(id+"F3.wireOp",EDGE,"E4.sketch_text.stroke-7"),sQuery(id+"F3.wireOp",EDGE,"E4.sketch_text.stroke-8"),sQuery(id+"F3.wireOp",EDGE,"E4.sketch_text.stroke-9"),sQuery(id+"F3.wireOp",EDGE,"E4.sketch_text.stroke-10"),sQuery(id+"F3.wireOp",EDGE,"E4.sketch_text.stroke-11"),sQuery(id+"F3.wireOp",EDGE,"E4.sketch_text.stroke-12"),sQuery(id+"F3.wireOp",EDGE,"E4.sketch_text.stroke-13"),sQuery(id+"F3.wireOp",EDGE,"E4.sketch_text.stroke-14"),sQuery(id+"F3.wireOp",EDGE,"E4.sketch_text.stroke-15"),sQuery(id+"F3.wireOp",EDGE,"E4.sketch_text.stroke-16"),sQuery(id+"F3.wireOp",EDGE,"E4.sketch_text.stroke-17"),sQuery(id+"F3.wireOp",EDGE,"E4.sketch_text.stroke-18"),sQuery(id+"F3.wireOp",EDGE,"E4.sketch_text.stroke-19"),sQuery(id+"F3.wireOp",EDGE,"E4.sketch_text.stroke-20"),sQuery(id+"F3.wireOp",EDGE,"E4.sketch_text.stroke-21"),sQuery(id+"F3.wireOp",EDGE,"E4.sketch_text.stroke-22"),sQuery(id+"F3.wireOp",EDGE,"E4.sketch_text.stroke-23"),sQuery(id+"F3.wireOp",EDGE,"E4.sketch_text.stroke-24"),sQuery(id+"F3.wireOp",EDGE,"E4.sketch_text.stroke-25"),sQuery(id+"F3.wireOp",EDGE,"E4.sketch_text.stroke-26"),sQuery(id+"F3.wireOp",EDGE,"E4.sketch_text.stroke-27"),sQuery(id+"F3.wireOp",EDGE,"E4.sketch_text.stroke-28"),sQuery(id+"F3.wireOp",EDGE,"E4.sketch_text.stroke-29"),sQuery(id+"F3.wireOp",EDGE,"E4.sketch_text.stroke-30"),sQuery(id+"F3.wireOp",EDGE,"E4.sketch_text.stroke-31"),sQuery(id+"F3.wireOp",EDGE,"E4.sketch_text.stroke-32"),sQuery(id+"F3.wireOp",EDGE,"E4.sketch_text.stroke-33"),sQuery(id+"F3.wireOp",EDGE,"E4.sketch_text.stroke-34"),sQuery(id+"F3.wireOp",EDGE,"E4.sketch_text.stroke-35"),sQuery(id+"F3.wireOp",EDGE,"E4.sketch_text.stroke-36"),sQuery(id+"F3.wireOp",EDGE,"E4.sketch_text.stroke-37"),sQuery(id+"F3.wireOp",EDGE,"E4.sketch_text.stroke-38"),sQuery(id+"F3.wireOp",EDGE,"E4.sketch_text.stroke-39"),sQuery(id+"F3.wireOp",EDGE,"E4.sketch_text.stroke-40"),sQuery(id+"F3.wireOp",EDGE,"E4.sketch_text.stroke-41"),sQuery(id+"F3.wireOp",EDGE,"E4.sketch_text.stroke-42"),sQuery(id+"F3.wireOp",EDGE,"E4.sketch_text.stroke-43"),sQuery(id+"F3.wireOp",EDGE,"E4.sketch_text.stroke-44"),sQuery(id+"F3.wireOp",EDGE,"E4.sketch_text.stroke-45"),sQuery(id+"F3.wireOp",EDGE,"E4.sketch_text.stroke-46"),sQuery(id+"F3.wireOp",EDGE,"E4.sketch_text.stroke-47"),sQuery(id+"F3.wireOp",EDGE,"E4.sketch_text.stroke-48"),sQuery(id+"F3.wireOp",EDGE,"E4.sketch_text.stroke-49"),sQuery(id+"F3.wireOp",EDGE,"E4.sketch_text.stroke-50"),sQuery(id+"F3.wireOp",EDGE,"E4.sketch_text.stroke-51"),sQuery(id+"F3.wireOp",EDGE,"E4.sketch_text.stroke-52"),sQuery(id+"F3.wireOp",EDGE,"E4.sketch_text.stroke-53"),sQuery(id+"F3.wireOp",EDGE,"E4.sketch_text.stroke-54"),sQuery(id+"F3.wireOp",EDGE,"E4.sketch_text.stroke-55"),sQuery(id+"F3.wireOp",EDGE,"E4.sketch_text.stroke-56"),sQuery(id+"F3.wireOp",EDGE,"E4.sketch_text.stroke-57"),sQuery(id+"F3.wireOp",EDGE,"E4.sketch_text.stroke-58"),sQuery(id+"F3.wireOp",EDGE,"E4.sketch_text.stroke-59"),sQuery(id+"F3.wireOp",EDGE,"E4.sketch_text.stroke-60"),sQuery(id+"F3.wireOp",EDGE,"E4.sketch_text.stroke-61"),sQuery(id+"F3.wireOp",EDGE,"E4.sketch_text.stroke-62"),sQuery(id+"F3.wireOp",EDGE,"E4.sketch_text.stroke-71"),sQuery(id+"F3.wireOp",EDGE,"E4.sketch_text.stroke-72"),sQuery(id+"F3.wireOp",EDGE,"E4.sketch_text.stroke-73"),sQuery(id+"F3.wireOp",EDGE,"E4.sketch_text.stroke-74"),sQuery(id+"F3.wireOp",EDGE,"E4.sketch_text.stroke-75"),sQuery(id+"F3.wireOp",EDGE,"E4.sketch_text.stroke-76"),sQuery(id+"F3.wireOp",EDGE,"E4.sketch_text.stroke-77"),sQuery(id+"F3.wireOp",EDGE,"E4.sketch_text.stroke-78"),sQuery(id+"F3.wireOp",EDGE,"E4.sketch_text.stroke-79"),sQuery(id+"F3.wireOp",EDGE,"E4.sketch_text.stroke-80"),sQuery(id+"F3.wireOp",EDGE,"E4.sketch_text.stroke-81"),sQuery(id+"F3.wireOp",EDGE,"E4.sketch_text.stroke-82"),sQuery(id+"F3.wireOp",EDGE,"E4.sketch_text.stroke-83"),sQuery(id+"F3.wireOp",EDGE,"E4.sketch_text.stroke-84"),sQuery(id+"F3.wireOp",EDGE,"E4.sketch_text.stroke-85"),sQuery(id+"F3.wireOp",EDGE,"E4.sketch_text.stroke-86"),sQuery(id+"F3.wireOp",EDGE,"E4.sketch_text.stroke-87"),sQuery(id+"F3.wireOp",EDGE,"E4.sketch_text.stroke-88"),sQuery(id+"F3.wireOp",EDGE,"E4.sketch_text.stroke-89"),sQuery(id+"F3.wireOp",EDGE,"E4.sketch_text.stroke-90"),sQuery(id+"F3.wireOp",EDGE,"E4.sketch_text.stroke-91"),sQuery(id+"F3.wireOp",EDGE,"E4.sketch_text.stroke-92"),sQuery(id+"F3.wireOp",EDGE,"E4.sketch_text.stroke-93"),sQuery(id+"F3.wireOp",EDGE,"E4.sketch_text.stroke-94"),sQuery(id+"F3.wireOp",EDGE,"E4.sketch_text.stroke-95"),sQuery(id+"F3.wireOp",EDGE,"E4.sketch_text.stroke-96"),sQuery(id+"F3.wireOp",EDGE,"E4.sketch_text.stroke-97"),sQuery(id+"F3.wireOp",EDGE,"E4.sketch_text.stroke-103"),sQuery(id+"F3.wireOp",EDGE,"E4.sketch_text.stroke-104"),sQuery(id+"F3.wireOp",EDGE,"E4.sketch_text.stroke-105"),sQuery(id+"F3.wireOp",EDGE,"E4.sketch_text.stroke-106"),sQuery(id+"F3.wireOp",EDGE,"E4.sketch_text.stroke-107"),sQuery(id+"F3.wireOp",EDGE,"E4.sketch_text.stroke-108"),sQuery(id+"F3.wireOp",EDGE,"E4.sketch_text.stroke-109"),sQuery(id+"F3.wireOp",EDGE,"E4.sketch_text.stroke-110"),sQuery(id+"F3.wireOp",EDGE,"E4.sketch_text.stroke-111"),sQuery(id+"F3.wireOp",EDGE,"E4.sketch_text.stroke-112"),sQuery(id+"F3.wireOp",EDGE,"E4.sketch_text.stroke-113"),sQuery(id+"F3.wireOp",EDGE,"E4.sketch_text.stroke-114"),sQuery(id+"F3.wireOp",EDGE,"E4.sketch_text.stroke-115"),sQuery(id+"F3.wireOp",EDGE,"E4.sketch_text.stroke-116"),sQuery(id+"F3.wireOp",EDGE,"E4.sketch_text.stroke-117"),sQuery(id+"F3.wireOp",EDGE,"E4.sketch_text.stroke-118"),sQuery(id+"F3.wireOp",EDGE,"E4.sketch_text.stroke-119"),sQuery(id+"F3.wireOp",EDGE,"E4.sketch_text.stroke-120"),sQuery(id+"F3.wireOp",EDGE,"E4.sketch_text.stroke-121"),sQuery(id+"F3.wireOp",EDGE,"E4.sketch_text.stroke-122"),sQuery(id+"F3.wireOp",EDGE,"E4.sketch_text.stroke-123"),sQuery(id+"F3.wireOp",EDGE,"E4.sketch_text.stroke-124"),sQuery(id+"F3.wireOp",EDGE,"E4.sketch_text.stroke-125"),sQuery(id+"F3.wireOp",EDGE,"E4.sketch_text.stroke-126"),sQuery(id+"F3.wireOp",EDGE,"E4.sketch_text.stroke-127"),sQuery(id+"F3.wireOp",EDGE,"E4.sketch_text.stroke-128"),sQuery(id+"F3.wireOp",EDGE,"E4.sketch_text.stroke-129"),sQuery(id+"F3.wireOp",EDGE,"E4.sketch_text.stroke-130"),sQuery(id+"F3.wireOp",EDGE,"E4.sketch_text.stroke-131"),sQuery(id+"F3.wireOp",EDGE,"E4.sketch_text.stroke-132"),sQuery(id+"F3.wireOp",EDGE,"E4.sketch_text.stroke-133"),sQuery(id+"F3.wireOp",EDGE,"E4.sketch_text.stroke-134"),sQuery(id+"F3.wireOp",EDGE,"E4.sketch_text.stroke-135"),sQuery(id+"F3.wireOp",EDGE,"E4.sketch_text.stroke-136"),sQuery(id+"F3.wireOp",EDGE,"E4.sketch_text.stroke-137"),sQuery(id+"F3.wireOp",EDGE,"E4.sketch_text.stroke-138"),sQuery(id+"F3.wireOp",EDGE,"E4.sketch_text.stroke-139"),sQuery(id+"F3.wireOp",EDGE,"E4.sketch_text.stroke-140"),sQuery(id+"F3.wireOp",EDGE,"E4.sketch_text.stroke-141"),sQuery(id+"F3.wireOp",EDGE,"E4.sketch_text.stroke-142"),sQuery(id+"F3.wireOp",EDGE,"E4.sketch_text.stroke-143"),sQuery(id+"F3.wireOp",EDGE,"E4.sketch_text.stroke-144"),sQuery(id+"F3.wireOp",EDGE,"E4.sketch_text.stroke-145"),sQuery(id+"F3.wireOp",EDGE,"E4.sketch_text.stroke-146"),sQuery(id+"F3.wireOp",EDGE,"E4.sketch_text.stroke-147"),sQuery(id+"F3.wireOp",EDGE,"E4.sketch_text.stroke-148"),sQuery(id+"F3.wireOp",EDGE,"E4.sketch_text.stroke-149"),sQuery(id+"F3.wireOp",EDGE,"E4.sketch_text.stroke-150"),sQuery(id+"F3.wireOp",EDGE,"E4.sketch_text.stroke-151"),sQuery(id+"F3.wireOp",EDGE,"E4.sketch_text.stroke-152"),sQuery(id+"F3.wireOp",EDGE,"E4.sketch_text.stroke-153"),sQuery(id+"F3.wireOp",EDGE,"E4.sketch_text.stroke-159"),sQuery(id+"F3.wireOp",EDGE,"E4.sketch_text.stroke-160"),sQuery(id+"F3.wireOp",EDGE,"E4.sketch_text.stroke-161"),sQuery(id+"F3.wireOp",EDGE,"E4.sketch_text.stroke-162"),sQuery(id+"F3.wireOp",EDGE,"E4.sketch_text.stroke-163"),sQuery(id+"F3.wireOp",EDGE,"E4.sketch_text.stroke-164"),sQuery(id+"F3.wireOp",EDGE,"E4.sketch_text.stroke-165"),sQuery(id+"F3.wireOp",EDGE,"E4.sketch_text.stroke-166"),sQuery(id+"F3.wireOp",EDGE,"E4.sketch_text.stroke-167"),sQuery(id+"F3.wireOp",EDGE,"E4.sketch_text.stroke-168"),sQuery(id+"F3.wireOp",EDGE,"E4.sketch_text.stroke-169"),sQuery(id+"F3.wireOp",EDGE,"E4.sketch_text.stroke-170"),sQuery(id+"F3.wireOp",EDGE,"E4.sketch_text.stroke-171"),sQuery(id+"F3.wireOp",EDGE,"E4.sketch_text.stroke-172"),sQuery(id+"F3.wireOp",EDGE,"E4.sketch_text.stroke-173"),sQuery(id+"F3.wireOp",EDGE,"E4.sketch_text.stroke-174"),sQuery(id+"F3.wireOp",EDGE,"E4.sketch_text.stroke-175"),sQuery(id+"F3.wireOp",EDGE,"E4.sketch_text.stroke-176"),sQuery(id+"F3.wireOp",EDGE,"E4.sketch_text.stroke-177"),sQuery(id+"F3.wireOp",EDGE,"E4.sketch_text.stroke-178"),sQuery(id+"F3.wireOp",EDGE,"E4.sketch_text.stroke-179"),sQuery(id+"F3.wireOp",EDGE,"E4.sketch_text.stroke-180"),sQuery(id+"F5.wireOp",EDGE,"E30"),subQ2])],"isStart":true}),makeQuery(id+"F6.opExtrude","SWEPT_FACE",FACE,{"disambiguationData":[OSD([subQ2])]})]),OD(1.0)],"derivedFrom":makeQuery(id+"F1.opExtrude","CAP_EDGE",EDGE,{"disambiguationData":[OSD([subQ0])],"isStart":false})});}
            fillet(context, id + "F7", {"entities" : qUnion([Q0, Q1, Q2, Q3, Q4, Q5, Q6, Q7, Q8, Q9, Q10, Q11, Q12, Q13, Q14, Q15, Q16, Q17, Q18, Q19, Q20, Q21, Q22, Q23, Q24, Q25, Q26, Q27]), "radius" : 5.08 * mm, "tangentPropagation" : true, "allowEdgeOverflow" : false});
        }
    });
